FCSTD DOCUMENT  (FreeCAD 0.20R29410 (Git))
Label: feeder_assembly
License: All rights reserved
LicenseURL: http://en.wikipedia.org/wiki/All_rights_reserved
objects: Part::FeaturePython×592, App::FeaturePython×507, Sketcher::SketchObject×232, PartDesign::Fillet×137, PartDesign::Pad×118, PartDesign::Pocket×107, PartDesign::Body×40, App::Link×18, PartDesign::Chamfer×18, App::DocumentObjectGroup×16, PartDesign::Mirrored×8, Part::Feature×6, PartDesign::LinearPattern×6, Part::Mirroring×4, PartDesign::PolarPattern×3, PartDesign::MultiTransform×2, PartDesign::FeatureBase×1, PartDesign::Thickness×1
note: 1617 computed .brp shape members not serialized (recipe doc carries the construction recipe); baked Part::Feature solids carry a one-line shape summary decoded from their .brp
EXTERNAL_REF file=40cm_2020_aluminum_extrusion.FCStd obj=Pad001
EXTERNAL_REF file=food_dish.FCStd obj=Revolution
EXTERNAL_REF file=orthogonal_2020_aluminum_connector.FCStd obj=Fillet003
EXTERNAL_REF file=dispenser.FCStd obj=Assembly
EXTERNAL_REF file=MG996R.FCStd obj=MG996R001

FEATURE [App::Link] Link  label="40cm_2020_extrusion-01"
  LinkPlacement = pos=(557,-323,-130) rot=(0,0,1;0rad)
  LinkedObject = -> <external 40cm_2020_aluminum_extrusion.FCStd>#Pad001
  Placement = pos=(557,-323,-130) rot=(0,0,1;0rad)
FEATURE [App::Link] Link001  label="40cm_2020_extrusion-02"
  LinkPlacement = pos=(367,-323,-130) rot=(0,0,1;0rad)
  LinkedObject = -> <external 40cm_2020_aluminum_extrusion.FCStd>#Pad001
  Placement = pos=(367,-323,-130) rot=(0,0,1;0rad)
FEATURE [App::Link] Link002  label="40cm_2020_extrusion-03"
  LinkPlacement = pos=(747,-323,-130) rot=(0,0,1;0rad)
  LinkedObject = -> <external 40cm_2020_aluminum_extrusion.FCStd>#Pad001
  Placement = pos=(747,-323,-130) rot=(0,0,1;0rad)
FEATURE [App::Link] Link003  label="40cm_2020_extrusion-04"
  LinkPlacement = pos=(410,-646,-130) rot=(0,0,-1;1.5708rad)
  LinkedObject = -> <external 40cm_2020_aluminum_extrusion.FCStd>#Pad001
  Placement = pos=(410,-646,-130) rot=(0,0,-1;1.5708rad)
FEATURE [App::Link] Link004  label="40cm_2020_extrusion-05"
  LinkPlacement = pos=(23.9999,-386,-130) rot=(0,0,1;1.5708rad)
  LinkedObject = -> <external 40cm_2020_aluminum_extrusion.FCStd>#Pad001
  Placement = pos=(23.9999,-386,-130) rot=(0,0,1;1.5708rad)
FEATURE [App::Link] Link005  label="food_dish_left"
  LinkPlacement = pos=(122.089,-400.044,0) rot=(0.99982,-0.013426,-0.013426;1.57098rad)
  LinkedObject = -> <external food_dish.FCStd>#Revolution
  Placement = pos=(122.089,-400.044,0) rot=(0.99982,-0.013426,-0.013426;1.57098rad)
FEATURE [App::Link] Link006  label="food_dish_right"
  LinkPlacement = pos=(311.742,-398.636,2.1e-14) rot=(0.999997,-0.001682,-0.001682;1.5708rad)
  LinkedObject = -> <external food_dish.FCStd>#Revolution
  Placement = pos=(311.742,-398.636,2.1e-14) rot=(0.999997,-0.001682,-0.001682;1.5708rad)
FEATURE [App::Link] Link007  label="40_cm_2020_vertical-left"
  LinkPlacement = pos=(347,-615.994,7) rot=(-1,0,0;1.5708rad)
  LinkedObject = -> <external 40cm_2020_aluminum_extrusion.FCStd>#Pad001
  Placement = pos=(347,-615.994,7) rot=(-1,0,0;1.5708rad)
FEATURE [App::Link] Link008  label="orthogonal-left-front"
  LinkPlacement = pos=(16.9999,-485.994,20) rot=(-0.707107,0,0.707107;3.14159rad)
  LinkedObject = -> <external orthogonal_2020_aluminum_connector.FCStd>#Fillet003
  Placement = pos=(16.9999,-485.994,20) rot=(-0.707107,0,0.707107;3.14159rad)
FEATURE [App::Link] Link009  label="orthogonal-left-back"
  LinkPlacement = pos=(16.9999,-465.994,1.01614e-10) rot=(0,-1,0;1.5708rad)
  LinkedObject = -> <external orthogonal_2020_aluminum_connector.FCStd>#Fillet003
  Placement = pos=(16.9999,-465.994,1.01614e-10) rot=(0,-1,0;1.5708rad)
FEATURE [Sketcher::SketchObject] Sketch
  FullyConstrained = true
  MapMode = 5
  Placement = pos=(0,0,0) rot=(0.57735,0.57735,0.57735;2.0944rad)
  Support = -> [YZ_Plane]
  sketch-geometry (4):
    g0: LineSegment StartX=0 StartY=0 StartZ=0 EndX=20 EndY=0 EndZ=0
    g1: LineSegment StartX=20 StartY=0 StartZ=0 EndX=20 EndY=30 EndZ=0
    g2: LineSegment StartX=20 StartY=30 StartZ=0 EndX=0 EndY=30 EndZ=0
    g3: LineSegment StartX=0 StartY=30 StartZ=0 EndX=0 EndY=0 EndZ=0
  constraints (11):
    c: Coincident(g0,g1)
    c: Coincident(g1,g2)
    c: Coincident(g2,g3)
    c: Coincident(g3,g0)
    c: Horizontal(g0)
    c: Horizontal(g2)
    c: Vertical(g1)
    c: Vertical(g3)
    c: Coincident(g0,g-1)
    c: DistanceY(g3,g3) = 30
    c: DistanceX(g0,g0) = 20
FEATURE [PartDesign::Pad] Pad  label="Pad-body001"
  Direction = (1,-2e-16,3e-16)
  Length = 200
  Length2 = 10
  Placement = pos=(0,0,0) rot=(0.57735,0.57735,0.57735;2.0944rad)
  Profile = -> Sketch
  ReferenceAxis = -> Sketch [N_Axis]
  Type = 0
FEATURE [Sketcher::SketchObject] Sketch004
  FullyConstrained = true
  MapMode = 5
  Support = -> [XY_Plane003]
  sketch-geometry (4):
    g0: LineSegment StartX=0 StartY=0 StartZ=0 EndX=166 EndY=0 EndZ=0
    g1: LineSegment StartX=166 StartY=0 StartZ=0 EndX=166 EndY=-90 EndZ=0
    g2: LineSegment StartX=166 StartY=-90 StartZ=0 EndX=0 EndY=-90 EndZ=0
    g3: LineSegment StartX=0 StartY=-90 StartZ=0 EndX=0 EndY=0 EndZ=0
  constraints (11):
    c: Coincident(g0,g1)
    c: Coincident(g1,g2)
    c: Coincident(g2,g3)
    c: Coincident(g3,g0)
    c: Horizontal(g0)
    c: Horizontal(g2)
    c: Vertical(g1)
    c: Vertical(g3)
    c: Coincident(g0,g-1)
    c: DistanceX(g2,g2) = 166
    c: DistanceY(g1,g1) = 90
FEATURE [PartDesign::Pad] Pad004  label="Pad-body"
  Direction = (0,0,1)
  Length = 5
  Length2 = 10
  Profile = -> Sketch004
  ReferenceAxis = -> Sketch004 [N_Axis]
  Type = 0
FEATURE [Sketcher::SketchObject] Sketch006
  ExternalGeometry = -> [Pad004]
  FullyConstrained = true
  MapMode = 5
  Placement = pos=(0,0,0) rot=(0.57735,-0.57735,-0.57735;2.0944rad)
  Support = -> [Pad004]
  sketch-geometry (1):
    g0: Circle CenterX=90 CenterY=2.5 CenterZ=0 NormalX=0 NormalY=0 NormalZ=1 AngleXU=0 Radius=4.5
  constraints (3):
    c: PointOnObject(g0,g-3)
    c: DistanceY(g-3,g0) = 2.5
    c: Diameter(g0) = 9
FEATURE [PartDesign::Pad] Pad006  label="Pad-slider_pin"
  BaseFeature = -> Pad004
  Direction = (-1,0,0)
  Length = 21
  Length2 = 177
  Profile = -> Sketch006
  ReferenceAxis = -> Sketch006 [N_Axis]
  Type = 4
FEATURE [App::Link] Link011  label="assy-dispenser-left"
  LinkPlacement = pos=(147,-465.994,202) rot=(0,0,1;1.5708rad)
  LinkedObject = -> <external dispenser.FCStd>#Assembly
  Placement = pos=(147,-465.994,202) rot=(0,0,1;1.5708rad)
FEATURE [App::Link] Link012  label="40cm_2020_extrusion-06"
  LinkPlacement = pos=(767,-335.994,393) rot=(1,0,0;1.5708rad)
  LinkedObject = -> <external 40cm_2020_aluminum_extrusion.FCStd>#Pad001
  Placement = pos=(767,-335.994,393) rot=(1,0,0;1.5708rad)
FEATURE [App::Link] Link013  label="orthogonal-right-front"
  LinkPlacement = pos=(417,-485.994,-1.29023e-10) rot=(0.707107,0,0.707107;3.14159rad)
  LinkedObject = -> <external orthogonal_2020_aluminum_connector.FCStd>#Fillet003
  Placement = pos=(417,-485.994,-1.29023e-10) rot=(0.707107,0,0.707107;3.14159rad)
FEATURE [App::Link] Link014  label="40cm_2020_extrusion-007"
  LinkPlacement = pos=(410,-815.994,124.795) rot=(0,0,-1;1.5708rad)
  LinkedObject = -> <external 40cm_2020_aluminum_extrusion.FCStd>#Pad001
  Placement = pos=(410,-815.994,124.795) rot=(0,0,-1;1.5708rad)
FEATURE [App::Link] Link015  label="assy-dispenser-right"
  LinkPlacement = pos=(287,-465.994,202) rot=(0,0,1;0rad)
  LinkedObject = -> <external dispenser.FCStd>#Assembly
  Placement = pos=(287,-465.994,202) rot=(0,0,1;0rad)
FEATURE [Sketcher::SketchObject] Sketch008
  FullyConstrained = true
  MapMode = 5
  Placement = pos=(8.8e-15,20,-4.4e-15) rot=(0.57735,0.57735,0.57735;4.18879rad)
  Support = -> [Pad]
  sketch-geometry (5):
    g0: Circle CenterX=15 CenterY=10 CenterZ=0 NormalX=0 NormalY=0 NormalZ=1 AngleXU=0 Radius=5
    g1: ArcOfCircle CenterX=15 CenterY=190 CenterZ=0 NormalX=0 NormalY=0 NormalZ=1 AngleXU=0 Radius=5 StartAngle=1.7e-15 EndAngle=3.14159
    g2: ArcOfCircle CenterX=15 CenterY=35 CenterZ=0 NormalX=0 NormalY=0 NormalZ=1 AngleXU=0 Radius=5 StartAngle=3.14159 EndAngle=6.28319
    g3: LineSegment StartX=10 StartY=190 StartZ=0 EndX=10 EndY=35 EndZ=0
    g4: LineSegment StartX=20 StartY=35 StartZ=0 EndX=20 EndY=190 EndZ=0
  constraints (13):
    c: Diameter(g0) = 10
    c: DistanceX(g-1,g0) = 15
    c: DistanceY(g-1,g0) = 10
    c: Tangent(g1,g3) = -1.5708
    c: Tangent(g3,g2) = -1.5708
    c: Tangent(g2,g4) = -1.5708
    c: Tangent(g4,g1) = -1.5708
    c: Equal(g1,g2)
    c: Vertical(g3)
    c: Radius(g2) = 5
    c: Vertical(g2,g0)
    c: DistanceY(g0,g2) = 25
    c: DistanceY(g0,g1) = 180
FEATURE [PartDesign::Pocket] Pocket  label="Pocket-slider_guide"
  BaseFeature = -> Pad
  Direction = (-3e-16,-1,1e-16)
  Length = 5
  Length2 = 5
  Placement = pos=(0,0,0) rot=(0.57735,0.57735,0.57735;2.0944rad)
  Profile = -> Sketch008
  ReferenceAxis = -> Sketch008 [N_Axis]
  Type = 1
FEATURE [Sketcher::SketchObject] Sketch009
  FullyConstrained = true
  MapMode = 5
  Placement = pos=(-8.4e-15,1.32e-14,30) rot=(0,0,-1;1.5708rad)
  Support = -> [Pocket]
  sketch-geometry (2):
    g0: Circle CenterX=-10 CenterY=50 CenterZ=0 NormalX=0 NormalY=0 NormalZ=1 AngleXU=0 Radius=3.1
    g1: Circle CenterX=-10 CenterY=180 CenterZ=0 NormalX=0 NormalY=0 NormalZ=1 AngleXU=0 Radius=3.1
  constraints (6):
    c: DistanceX(g0,g-1) = 10
    c: Vertical(g1,g0)
    c: DistanceY(g-1,g0) = 50
    c: DistanceY(g0,g1) = 130
    c: Diameter(g0) = 6.2
    c: Equal(g1,g0)
FEATURE [PartDesign::Pocket] Pocket001  label="Pocket-mount_holes"
  BaseFeature = -> Pocket
  Direction = (3e-16,-5e-16,-1)
  Length = 26.5
  Length2 = 5
  Placement = pos=(0,0,0) rot=(0.57735,0.57735,0.57735;2.0944rad)
  Profile = -> Sketch009
  ReferenceAxis = -> Sketch009 [N_Axis]
  Type = 0
FEATURE [Sketcher::SketchObject] Sketch013  label="Sketch-slider_guide_line"
  FullyConstrained = false
  MapMode = 5
  Placement = pos=(0,1e-16,0) rot=(-0.57735,-0.57735,0.57735;4.18879rad)
  Support = -> [Pocket001]
  sketch-geometry (1):
    g0: LineSegment StartX=-14.7121 StartY=24.4994 StartZ=0 EndX=-14.7121 EndY=187.74 EndZ=0
  constraints (1):
    c: Vertical(g0)
FEATURE [App::Link] Link016  label="assy-link-slide-right"
  LinkPlacement = pos=(772,-351.327,-140) rot=(0,0,1;0rad)
  LinkedObject = -> Assembly001
  Placement = pos=(772,-351.327,-140) rot=(0,0,1;0rad)
FEATURE [Sketcher::SketchObject] Sketch016
  ExternalGeometry = -> [Pad006]
  FullyConstrained = true
  MapMode = 5
  Placement = pos=(0,0,0) rot=(1,0,0;3.14159rad)
  Support = -> [Pad006]
  sketch-geometry (10):
    g0: LineSegment StartX=15.25 StartY=10.5 StartZ=0 EndX=25.25 EndY=10.5 EndZ=0
    g1: LineSegment StartX=25.25 StartY=10.5 StartZ=0 EndX=25.25 EndY=-4.5 EndZ=0
    g2: LineSegment StartX=25.25 StartY=-4.5 StartZ=0 EndX=15.25 EndY=-4.5 EndZ=0
    g3: LineSegment StartX=15.25 StartY=-4.5 StartZ=0 EndX=15.25 EndY=10.5 EndZ=0
    g4: LineSegment StartX=140.75 StartY=10.5 StartZ=0 EndX=150.75 EndY=10.5 EndZ=0
    g5: LineSegment StartX=150.75 StartY=10.5 StartZ=0 EndX=150.75 EndY=-4.5 EndZ=0
    g6: LineSegment StartX=150.75 StartY=-4.5 StartZ=0 EndX=140.75 EndY=-4.5 EndZ=0
    g7: LineSegment StartX=140.75 StartY=-4.5 StartZ=0 EndX=140.75 EndY=10.5 EndZ=0
    g8: LineSegment StartX=0 StartY=0 StartZ=0 EndX=15.25 EndY=10.5 EndZ=0
    g9: LineSegment StartX=150.75 StartY=10.5 StartZ=0 EndX=166 EndY=-1.8e-15 EndZ=0
  constraints (28):
    c: Coincident(g0,g1)
    c: Coincident(g1,g2)
    c: Coincident(g2,g3)
    c: Coincident(g3,g0)
    c: Horizontal(g0)
    c: Horizontal(g2)
    c: Vertical(g1)
    c: Vertical(g3)
    c: Coincident(g4,g5)
    c: Coincident(g5,g6)
    c: Coincident(g6,g7)
    c: Coincident(g7,g4)
    c: Horizontal(g4)
    c: Horizontal(g6)
    c: Vertical(g5)
    c: Vertical(g7)
    c: Equal(g3,g7)
    c: Equal(g2,g6)
    c: DistanceY(g2,g-3) = 4.5
    c: DistanceX(g-3,g2) = 15.25
    c: DistanceX(g0,g0) = 10
    c: DistanceY(g1,g1) = 15
    c: Horizontal(g6,g1)
    c: Coincident(g8,g-3)
    c: Coincident(g8,g0)
    c: Coincident(g9,g4)
    c: Coincident(g9,g-3)
    c: Equal(g8,g9)
FEATURE [PartDesign::Pad] Pad009
  BaseFeature = -> Pad006
  Direction = (0,0,-1)
  Length = 7
  Length2 = 10
  Profile = -> Sketch016
  ReferenceAxis = -> Sketch016 [N_Axis]
  Type = 0
FEATURE [Sketcher::SketchObject] Sketch017
  FullyConstrained = true
  MapMode = 5
  Placement = pos=(15.25,0,0) rot=(0.57735,-0.57735,-0.57735;2.0944rad)
  Support = -> [Pad009]
  sketch-geometry (4):
    g0: Circle CenterX=-1 CenterY=-3.5 CenterZ=0 NormalX=0 NormalY=0 NormalZ=1 AngleXU=0 Radius=1.75
    g1: LineSegment StartX=10.5 StartY=0 StartZ=0 EndX=10.5 EndY=-7 EndZ=0
    g2: LineSegment StartX=10.5 StartY=-7 StartZ=0 EndX=3.5 EndY=-7 EndZ=0
    g3: LineSegment StartX=3.5 StartY=-7 StartZ=0 EndX=10.5 EndY=0 EndZ=0
  constraints (12):
    c: Diameter(g0) = 3.5
    c: DistanceY(g0,g-1) = 3.5
    c: DistanceX(g0,g-1) = 1
    c: PointOnObject(g1,g-1)
    c: Vertical(g1)
    c: Horizontal(g2)
    c: Coincident(g3,g1)
    c: Coincident(g2,g3)
    c: Coincident(g1,g2)
    c: Angle(g3,g1) = 0.785398
    c: DistanceX(g-1,g1) = 10.5
    c: DistanceY(g1,g1) = 7
FEATURE [PartDesign::Pocket] Pocket005
  BaseFeature = -> Pad009
  Direction = (1,0,0)
  Length = 5
  Length2 = 5
  Profile = -> Sketch017
  ReferenceAxis = -> Sketch017 [N_Axis]
  Type = 1
FEATURE [Sketcher::SketchObject] Sketch018
  ExternalGeometry = -> [Pocket005]
  FullyConstrained = true
  MapMode = 5
  Placement = pos=(-21,0,0) rot=(0.57735,-0.57735,-0.57735;2.0944rad)
  Support = -> [Pocket005]
  sketch-geometry (1):
    g0: GeomPoint X=90 Y=2.5 Z=0
  constraints (1):
    c: Coincident(g0,g-3)
FEATURE [Part::FeaturePython] Workplane  label="Workplane-XY"  # WARN: FeaturePython — macro-defined, semantics opaque (R4)
  Fixed = true
  Length = 400.999
  Placement = pos=(16.9999,-296,0) rot=(0,0,-1;1.5708rad)
  Width = 400.999
FEATURE [Part::FeaturePython] Workplane001  label="Workplane-YZ"  # WARN: FeaturePython — macro-defined, semantics opaque (R4)
  Fixed = true
  Length = 567.098
  Placement = pos=(16.9999,-296,0) rot=(0,-1,0;1.5708rad)
  Width = 567.098
FEATURE [Part::FeaturePython] Workplane002  label="WorkplaneXZ"  # WARN: FeaturePython — macro-defined, semantics opaque (R4)
  Fixed = true
  Length = 567.098
  Placement = pos=(16.9999,-296,0) rot=(1,0,0;1.5708rad)
  Width = 567.098
FEATURE [Sketcher::SketchObject] Sketch001
  FullyConstrained = true
  MapMode = 5
  Support = -> [XY_Plane001]
  sketch-geometry (4):
    g0: LineSegment StartX=0 StartY=50 StartZ=0 EndX=166 EndY=50 EndZ=0
    g1: LineSegment StartX=166 StartY=50 StartZ=0 EndX=166 EndY=140 EndZ=0
    g2: LineSegment StartX=166 StartY=140 StartZ=0 EndX=0 EndY=140 EndZ=0
    g3: LineSegment StartX=0 StartY=140 StartZ=0 EndX=0 EndY=50 EndZ=0
  constraints (12):
    c: Coincident(g0,g1)
    c: Coincident(g1,g2)
    c: Coincident(g2,g3)
    c: Coincident(g3,g0)
    c: Horizontal(g0)
    c: Horizontal(g2)
    c: Vertical(g1)
    c: Vertical(g3)
    c: PointOnObject(g0,g-2)
    c: DistanceY(g1,g1) = 90
    c: DistanceX(g0,g0) = 166
    c: DistanceY(g-1,g2) = 140
FEATURE [PartDesign::Pad] Pad001  label="Pad-base_rect"
  Direction = (0,0,1)
  Length = 5
  Length2 = 10
  Profile = -> Sketch001
  ReferenceAxis = -> Sketch001 [N_Axis]
  Type = 0
FEATURE [Sketcher::SketchObject] Sketch002
  ExternalGeometry = -> [Pad001]
  FullyConstrained = true
  MapMode = 5
  Placement = pos=(0,0,0) rot=(0.57735,-0.57735,-0.57735;2.0944rad)
  Support = -> [Pad001]
  sketch-geometry (1):
    g0: Circle CenterX=-140 CenterY=2.5 CenterZ=0 NormalX=0 NormalY=0 NormalZ=1 AngleXU=0 Radius=4.5
  constraints (3):
    c: DistanceY(g-3,g0) = 2.5
    c: Diameter(g0) = 9
    c: PointOnObject(g0,g-3)
FEATURE [PartDesign::Pad] Pad002  label="Pad-base_9mm_shaft"
  BaseFeature = -> Pad001
  Direction = (-1,0,0)
  Length = 21
  Length2 = 177
  Profile = -> Sketch002
  ReferenceAxis = -> Sketch002 [N_Axis]
  Type = 4
FEATURE [Sketcher::SketchObject] Sketch014
  ExternalGeometry = -> [Pad002]
  FullyConstrained = true
  MapMode = 5
  Placement = pos=(0,0,0) rot=(1,0,0;3.14159rad)
  Support = -> [Pad002]
  sketch-geometry (18):
    g0: LineSegment StartX=10 StartY=-45.5 StartZ=0 EndX=15 EndY=-45.5 EndZ=0
    g1: LineSegment StartX=15 StartY=-45.5 StartZ=0 EndX=15 EndY=-60.5 EndZ=0
    g2: LineSegment StartX=15 StartY=-60.5 StartZ=0 EndX=10 EndY=-60.5 EndZ=0
    g3: LineSegment StartX=10 StartY=-60.5 StartZ=0 EndX=10 EndY=-45.5 EndZ=0
    g4: LineSegment StartX=25.5 StartY=-45.5 StartZ=0 EndX=30.5 EndY=-45.5 EndZ=0
    g5: LineSegment StartX=30.5 StartY=-45.5 StartZ=0 EndX=30.5 EndY=-60.5 EndZ=0
    g6: LineSegment StartX=30.5 StartY=-60.5 StartZ=0 EndX=25.5 EndY=-60.5 EndZ=0
    g7: LineSegment StartX=25.5 StartY=-60.5 StartZ=0 EndX=25.5 EndY=-45.5 EndZ=0
    g8: LineSegment StartX=135.5 StartY=-45.5 StartZ=0 EndX=140.5 EndY=-45.5 EndZ=0
    g9: LineSegment StartX=140.5 StartY=-45.5 StartZ=0 EndX=140.5 EndY=-60.5 EndZ=0
    g10: LineSegment StartX=140.5 StartY=-60.5 StartZ=0 EndX=135.5 EndY=-60.5 EndZ=0
    g11: LineSegment StartX=135.5 StartY=-60.5 StartZ=0 EndX=135.5 EndY=-45.5 EndZ=0
    g12: LineSegment StartX=151 StartY=-45.5 StartZ=0 EndX=156 EndY=-45.5 EndZ=0
    g13: LineSegment StartX=156 StartY=-45.5 StartZ=0 EndX=156 EndY=-60.5 EndZ=0
    g14: LineSegment StartX=156 StartY=-60.5 StartZ=0 EndX=151 EndY=-60.5 EndZ=0
    g15: LineSegment StartX=151 StartY=-60.5 StartZ=0 EndX=151 EndY=-45.5 EndZ=0
    g16: LineSegment StartX=15 StartY=-60.5 StartZ=0 EndX=25.5 EndY=-60.5 EndZ=0
    g17: LineSegment StartX=140.5 StartY=-60.5 StartZ=0 EndX=151 EndY=-60.5 EndZ=0
  constraints (52):
    c: Coincident(g0,g1)
    c: Coincident(g1,g2)
    c: Coincident(g2,g3)
    c: Coincident(g3,g0)
    c: Horizontal(g0)
    c: Horizontal(g2)
    c: Vertical(g1)
    c: Vertical(g3)
    c: Coincident(g4,g5)
    c: Coincident(g5,g6)
    c: Coincident(g6,g7)
    c: Coincident(g7,g4)
    c: Horizontal(g4)
    c: Horizontal(g6)
    c: Vertical(g5)
    c: Vertical(g7)
    c: Coincident(g8,g9)
    c: Coincident(g9,g10)
    c: Coincident(g10,g11)
    c: Coincident(g11,g8)
    c: Horizontal(g8)
    c: Horizontal(g10)
    c: Vertical(g9)
    c: Vertical(g11)
    c: Coincident(g12,g13)
    c: Coincident(g13,g14)
    c: Coincident(g14,g15)
    c: Coincident(g15,g12)
    c: Horizontal(g12)
    c: Horizontal(g14)
    c: Vertical(g13)
    c: Vertical(g15)
    c: Horizontal(g6,g10)
    c: Horizontal(g0,g4)
    c: Horizontal(g4,g8)
    c: Horizontal(g8,g12)
    c: Equal(g2,g6)
    c: Equal(g6,g10)
    c: Equal(g10,g14)
    c: DistanceX(g-1,g2) = 10
    c: DistanceX(g2,g2) = 5
    c: DistanceX(g1,g6) = 10.5
    c: DistanceY(g3,g3) = 15
    c: Coincident(g16,g1)
    c: Coincident(g16,g6)
    c: Horizontal(g16)
    c: Coincident(g17,g9)
    c: Coincident(g17,g14)
    c: Horizontal(g17)
    c: Equal(g16,g17)
    c: DistanceX(g12,g-3) = 10
    c: DistanceY(g-3,g0) = 4.5
FEATURE [PartDesign::Pad] Pad008  label="Pad-left_right_hinges"
  BaseFeature = -> Pad002
  Direction = (0,0,-1)
  Length = 7
  Length2 = 10
  Profile = -> Sketch014
  ReferenceAxis = -> Sketch014 [N_Axis]
  Type = 0
FEATURE [Sketcher::SketchObject] Sketch015
  ExternalGeometry = -> [Pad008]
  FullyConstrained = true
  MapMode = 5
  Placement = pos=(10,0,0) rot=(0.57735,-0.57735,-0.57735;2.0944rad)
  Support = -> [Pad008]
  sketch-geometry (4):
    g0: Circle CenterX=-49 CenterY=-3.5 CenterZ=0 NormalX=0 NormalY=0 NormalZ=1 AngleXU=0 Radius=1.75
    g1: LineSegment StartX=-60.5 StartY=0 StartZ=0 EndX=-53.5 EndY=-7 EndZ=0
    g2: LineSegment StartX=-53.5 StartY=-7 StartZ=0 EndX=-60.5 EndY=-7 EndZ=0
    g3: LineSegment StartX=-60.5 StartY=-7 StartZ=0 EndX=-60.5 EndY=0 EndZ=0
  constraints (12):
    c: Diameter(g0) = 3.5
    c: DistanceX(g-3,g0) = 1
    c: DistanceY(g0,g-3) = 3.5
    c: PointOnObject(g1,g-1)
    c: Coincident(g2,g1)
    c: Horizontal(g2)
    c: Coincident(g3,g2)
    c: Coincident(g3,g1)
    c: Vertical(g3)
    c: DistanceY(g3,g3) = 7
    c: Angle(g3,g1) = 0.785398
    c: DistanceX(g1,g-3) = 10.5
FEATURE [PartDesign::Pocket] Pocket004  label="Pocket-left_right_hinge2"
  BaseFeature = -> Pad008
  Direction = (1,0,0)
  Length = 5
  Length2 = 5
  Profile = -> Sketch015
  ReferenceAxis = -> Sketch015 [N_Axis]
  Type = 1
FEATURE [App::FeaturePython] Constraints005  # WARN: FeaturePython — macro-defined, semantics opaque (R4)
  _Version = 1
FEATURE [Part::Mirroring] Part__Mirroring001  label="Pocket005 (Mirror #2)"
  Base = (0,0,0)
  Normal = (1,0,0)
  Source = -> Pocket005
FEATURE [App::FeaturePython] Constraints006  # WARN: FeaturePython — macro-defined, semantics opaque (R4)
  _Version = 1
FEATURE [Part::FeaturePython] Parts006  # WARN: FeaturePython — macro-defined, semantics opaque (R4)
  Group = -> [Part__Mirroring001]
  GroupMode = 0
FEATURE [App::FeaturePython] Constraints007  # WARN: FeaturePython — macro-defined, semantics opaque (R4)
  _Version = 1
FEATURE [Sketcher::SketchObject] Sketch019
  FullyConstrained = true
  MapMode = 5
  Placement = pos=(0,0,0) rot=(0.57735,0.57735,0.57735;2.0944rad)
  Support = -> [YZ_Plane004]
  sketch-geometry (4):
    g0: LineSegment StartX=0 StartY=0 StartZ=0 EndX=20 EndY=0 EndZ=0
    g1: LineSegment StartX=20 StartY=0 StartZ=0 EndX=20 EndY=30 EndZ=0
    g2: LineSegment StartX=20 StartY=30 StartZ=0 EndX=0 EndY=30 EndZ=0
    g3: LineSegment StartX=0 StartY=30 StartZ=0 EndX=0 EndY=0 EndZ=0
  constraints (11):
    c: Coincident(g0,g1)
    c: Coincident(g1,g2)
    c: Coincident(g2,g3)
    c: Coincident(g3,g0)
    c: Horizontal(g0)
    c: Horizontal(g2)
    c: Vertical(g1)
    c: Vertical(g3)
    c: Coincident(g0,g-1)
    c: DistanceY(g3,g3) = 30
    c: DistanceX(g0,g0) = 20
FEATURE [PartDesign::Pad] Pad010  label="Pad-body002"
  Direction = (1,-2e-16,3e-16)
  Length = 200
  Length2 = 10
  Placement = pos=(0,0,0) rot=(0.57735,0.57735,0.57735;2.0944rad)
  Profile = -> Sketch019
  ReferenceAxis = -> Sketch019 [N_Axis]
  Type = 0
FEATURE [Sketcher::SketchObject] Sketch020
  FullyConstrained = true
  MapMode = 5
  Placement = pos=(8.8e-15,20,-4.4e-15) rot=(0.57735,0.57735,0.57735;4.18879rad)
  Support = -> [Pad010]
  sketch-geometry (5):
    g0: Circle CenterX=15 CenterY=10 CenterZ=0 NormalX=0 NormalY=0 NormalZ=1 AngleXU=0 Radius=5
    g1: ArcOfCircle CenterX=15 CenterY=190 CenterZ=0 NormalX=0 NormalY=0 NormalZ=1 AngleXU=0 Radius=5 StartAngle=1.7e-15 EndAngle=3.14159
    g2: ArcOfCircle CenterX=15 CenterY=35 CenterZ=0 NormalX=0 NormalY=0 NormalZ=1 AngleXU=0 Radius=5 StartAngle=3.14159 EndAngle=6.28319
    g3: LineSegment StartX=10 StartY=190 StartZ=0 EndX=10 EndY=35 EndZ=0
    g4: LineSegment StartX=20 StartY=35 StartZ=0 EndX=20 EndY=190 EndZ=0
  constraints (13):
    c: Diameter(g0) = 10
    c: DistanceX(g-1,g0) = 15
    c: DistanceY(g-1,g0) = 10
    c: Tangent(g1,g3) = -1.5708
    c: Tangent(g3,g2) = -1.5708
    c: Tangent(g2,g4) = -1.5708
    c: Tangent(g4,g1) = -1.5708
    c: Equal(g1,g2)
    c: Vertical(g3)
    c: Radius(g2) = 5
    c: Vertical(g2,g0)
    c: DistanceY(g0,g2) = 25
    c: DistanceY(g0,g1) = 180
FEATURE [PartDesign::Pocket] Pocket006  label="Pocket-slider_guide001"
  BaseFeature = -> Pad010
  Direction = (-4e-16,-1,2e-16)
  Length = 5
  Length2 = 5
  Placement = pos=(0,0,0) rot=(0.57735,0.57735,0.57735;2.0944rad)
  Profile = -> Sketch020
  ReferenceAxis = -> Sketch020 [N_Axis]
  Type = 1
FEATURE [Sketcher::SketchObject] Sketch021
  FullyConstrained = true
  MapMode = 5
  Placement = pos=(-8.4e-15,1.32e-14,30) rot=(0,0,-1;1.5708rad)
  Support = -> [Pocket006]
  sketch-geometry (2):
    g0: Circle CenterX=-10 CenterY=50 CenterZ=0 NormalX=0 NormalY=0 NormalZ=1 AngleXU=0 Radius=5
    g1: Circle CenterX=-10 CenterY=180 CenterZ=0 NormalX=0 NormalY=0 NormalZ=1 AngleXU=0 Radius=5
  constraints (6):
    c: DistanceX(g0,g-1) = 10
    c: Vertical(g1,g0)
    c: DistanceY(g-1,g0) = 50
    c: DistanceY(g0,g1) = 130
    c: Diameter(g1) = 10
    c: Diameter(g0) = 10
FEATURE [PartDesign::Pocket] Pocket007  label="Pocket-mount_holes001"
  BaseFeature = -> Pocket006
  Direction = (7e-16,-7e-16,-1)
  Length = 28
  Length2 = 5
  Placement = pos=(0,0,0) rot=(0.57735,0.57735,0.57735;2.0944rad)
  Profile = -> Sketch021
  ReferenceAxis = -> Sketch021 [N_Axis]
  Type = 0
FEATURE [Sketcher::SketchObject] Sketch022  label="Sketch-slider_guide_line001"
  FullyConstrained = false
  MapMode = 5
  Placement = pos=(0,1e-16,0) rot=(-0.57735,-0.57735,0.57735;4.18879rad)
  Support = -> [Pocket007]
  sketch-geometry (1):
    g0: LineSegment StartX=-14.7121 StartY=24.4994 StartZ=0 EndX=-14.7121 EndY=187.74 EndZ=0
  constraints (1):
    c: Vertical(g0)
FEATURE [PartDesign::Body] Body004  label="Slide-mid-Body001"
  Group = -> [Sketch019,Pad010,Sketch020,Pocket006,Sketch021,Pocket007,Sketch022]
  Origin = -> Origin004
  Placement = pos=(-375,53,160) rot=(0,0,-1;1.5708rad)
  Tip = -> Pocket007
FEATURE [Part::FeaturePython] Parts007  # WARN: FeaturePython — macro-defined, semantics opaque (R4)
  Group = -> [Body004]
  GroupMode = 0
FEATURE [App::FeaturePython] Constraints008  # WARN: FeaturePython — macro-defined, semantics opaque (R4)
  _Version = 1
FEATURE [App::FeaturePython] Elements008  # WARN: FeaturePython — macro-defined, semantics opaque (R4)
FEATURE [App::Link] Link017  label="link-servo"
  LinkPlacement = pos=(-23.0002,-306,45) rot=(0.57735,0.57735,0.57735;4.18879rad)
  LinkedObject = -> <external MG996R.FCStd>#MG996R001
  Placement = pos=(-23.0002,-306,45) rot=(0.57735,0.57735,0.57735;4.18879rad)
FEATURE [Part::FeaturePython] Parts008  # WARN: FeaturePython — macro-defined, semantics opaque (R4)
  Group = -> [Link017]
  GroupMode = 0
FEATURE [Part::FeaturePython] Assembly008  label="assy_servo"  # WARN: FeaturePython — macro-defined, semantics opaque (R4)
  AutoRelax = true
  BuildShape = 0
  Freeze = false
  Group = -> [Constraints008,Elements008,Parts008]
  Verbose = false
  _SolverType = 1
  _Version = 1
FEATURE [Sketcher::SketchObject] Sketch023
  ExternalGeometry = -> [Pocket001]
  FullyConstrained = true
  MapMode = 5
  Placement = pos=(0,0,0) rot=(0.57735,0.57735,-0.57735;4.18879rad)
  Support = -> [Pocket001]
  sketch-geometry (8):
    g0: LineSegment StartX=-10 StartY=2.5 StartZ=0 EndX=-10 EndY=-52.5 EndZ=0
    g1: LineSegment StartX=0 StartY=0 StartZ=0 EndX=0 EndY=-30 EndZ=0
    g2: LineSegment StartX=0 StartY=-30 StartZ=0 EndX=20 EndY=-30 EndZ=0
    g3: GeomPoint X=0 Y=-15 Z=0
    g4: LineSegment StartX=4.24533 StartY=-52.5 StartZ=0 EndX=20 EndY=-30 EndZ=0
    g5: LineSegment StartX=-10 StartY=-52.5 StartZ=0 EndX=4.24533 EndY=-52.5 EndZ=0
    g6: LineSegment StartX=0 StartY=0 StartZ=0 EndX=-5 EndY=2.5 EndZ=0
    g7: LineSegment StartX=-5 StartY=2.5 StartZ=0 EndX=-10 EndY=2.5 EndZ=0
  constraints (20):
    c: Coincident(g6,g-4)
    c: Vertical(g0)
    c: Coincident(g5,g0)
    c: Coincident(g1,g6)
    c: Coincident(g0,g7)
    c: Coincident(g1,g2)
    c: Coincident(g1,g-4)
    c: DistanceX(g7,g6) = 10
    c: DistanceY(g0,g0) = 55
    c: PointOnObject(g3,g1)
    c: DistanceY(g3,g6) = 15
    c: DistanceY(g3,g7) = 17.5
    c: Horizontal(g5)
    c: Coincident(g5,g4)
    c: Coincident(g2,g4)
    c: Coincident(g2,g-3)
    c: Angle(g2,g4) = 0.959931
    c: Coincident(g6,g7)
    c: Horizontal(g7)
    c: DistanceX(g0,g6) = 5
FEATURE [PartDesign::Pad] Pad011
  BaseFeature = -> Pocket001
  Direction = (-1,2e-16,-2e-16)
  Length = 20
  Length2 = 10
  Placement = pos=(0,0,0) rot=(0.57735,0.57735,0.57735;2.0944rad)
  Profile = -> Sketch023
  ReferenceAxis = -> Sketch023 [N_Axis]
  Reversed = true
  Type = 0
FEATURE [Sketcher::SketchObject] Sketch025
  ExternalGeometry = -> [Pad011]
  FullyConstrained = true
  MapMode = 5
  Placement = pos=(-2.2e-15,-10,6e-16) rot=(-0.57735,-0.57735,0.57735;4.18879rad)
  Support = -> [Pad011]
  sketch-geometry (15):
    g0: Circle CenterX=-49.575 CenterY=14.9 CenterZ=0 NormalX=0 NormalY=0 NormalZ=1 AngleXU=0 Radius=1.125
    g1: Circle CenterX=-49.575 CenterY=5.1 CenterZ=0 NormalX=0 NormalY=0 NormalZ=1 AngleXU=0 Radius=1.125
    g2: Circle CenterX=-1.125 CenterY=14.9 CenterZ=0 NormalX=0 NormalY=0 NormalZ=1 AngleXU=0 Radius=1.125
    g3: Circle CenterX=-1.125 CenterY=5.1 CenterZ=0 NormalX=0 NormalY=0 NormalZ=1 AngleXU=0 Radius=1.125
    g4: LineSegment StartX=-46.35 StartY=0 StartZ=0 EndX=-4.35 EndY=0 EndZ=0
    g5: LineSegment StartX=-4.35 StartY=0 StartZ=0 EndX=-4.35 EndY=20 EndZ=0
    g6: LineSegment StartX=-4.35 StartY=20 StartZ=0 EndX=-46.35 EndY=20 EndZ=0
    g7: LineSegment StartX=-46.35 StartY=20 StartZ=0 EndX=-46.35 EndY=0 EndZ=0
    g8: LineSegment StartX=-49.575 StartY=14.9 StartZ=0 EndX=-49.575 EndY=5.1 EndZ=0
    g9: LineSegment StartX=-49.575 StartY=5.1 StartZ=0 EndX=-1.125 EndY=5.1 EndZ=0
    g10: LineSegment StartX=-1.125 StartY=14.9 StartZ=0 EndX=-49.575 EndY=14.9 EndZ=0
    g11: LineSegment StartX=-46.35 StartY=20 StartZ=0 EndX=-49.575 EndY=14.9 EndZ=0
    g12: LineSegment StartX=-4.35 StartY=20 StartZ=0 EndX=-1.125 EndY=14.9 EndZ=0
    g13: LineSegment StartX=-1.125 StartY=5.1 StartZ=0 EndX=-1.125 EndY=10 EndZ=0
    g14: LineSegment StartX=-1.125 StartY=10 StartZ=0 EndX=-1.125 EndY=14.9 EndZ=0
  constraints (39):
    c: Tangent(g3,g-2)
    c: Coincident(g4,g5)
    c: Coincident(g5,g6)
    c: Coincident(g6,g7)
    c: Coincident(g7,g4)
    c: Horizontal(g4)
    c: Horizontal(g6)
    c: Vertical(g5)
    c: Vertical(g7)
    c: Horizontal(g-4,g5)
    c: DistanceX(g6,g6) = 42
    c: Diameter(g2) = 2.25
    c: Equal(g0,g1)
    c: Equal(g1,g3)
    c: Equal(g3,g2)
    c: Coincident(g8,g0)
    c: Coincident(g8,g1)
    c: Vertical(g8)
    c: Coincident(g9,g1)
    c: Coincident(g9,g3)
    c: Horizontal(g9)
    c: Coincident(g13,g3)
    c: Coincident(g14,g2)
    c: Coincident(g10,g2)
    c: Coincident(g10,g0)
    c: Horizontal(g10)
    c: Coincident(g11,g6)
    c: Coincident(g11,g0)
    c: Coincident(g12,g5)
    c: Coincident(g12,g2)
    c: Equal(g12,g11)
    c: DistanceX(g9,g9) = 48.45
    c: DistanceY(g8,g8) = 9.8
    c: Coincident(g13,g14)
    c: Vertical(g13)
    c: Vertical(g14)
    c: Equal(g14,g13)
    c: DistanceY(g-4,g13) = 10
    c: PointOnObject(g4,g-5)
FEATURE [PartDesign::Pocket] Pocket008
  BaseFeature = -> Pad011
  Direction = (1e-16,1,1e-16)
  Length = 10
  Length2 = 5
  Placement = pos=(0,0,0) rot=(0.57735,0.57735,0.57735;2.0944rad)
  Profile = -> Sketch025
  ReferenceAxis = -> Sketch025 [N_Axis]
  Type = 0
FEATURE [Sketcher::SketchObject] Sketch026
  ExternalGeometry = -> [Pocket008]
  FullyConstrained = true
  MapMode = 5
  Placement = pos=(-1.47e-14,0,52.5) rot=(0,0,-1;1.5708rad)
  Support = -> [Pocket008]
  sketch-geometry (4):
    g0: LineSegment StartX=-20 StartY=17.5 StartZ=0 EndX=5 EndY=17.5 EndZ=0
    g1: LineSegment StartX=5 StartY=17.5 StartZ=0 EndX=5 EndY=2.5 EndZ=0
    g2: LineSegment StartX=5 StartY=2.5 StartZ=0 EndX=-20 EndY=2.5 EndZ=0
    g3: LineSegment StartX=-20 StartY=2.5 StartZ=0 EndX=-20 EndY=17.5 EndZ=0
  constraints (12):
    c: Coincident(g0,g1)
    c: Coincident(g1,g2)
    c: Coincident(g2,g3)
    c: Coincident(g3,g0)
    c: Horizontal(g0)
    c: Horizontal(g2)
    c: Vertical(g1)
    c: Vertical(g3)
    c: DistanceX(g2,g2) = 25
    c: DistanceX(g1,g-3) = 5
    c: DistanceY(g-3,g1) = 2.5
    c: DistanceY(g0,g-4) = 2.5
FEATURE [PartDesign::Pocket] Pocket009
  BaseFeature = -> Pocket008
  Direction = (3e-16,-1e-16,-1)
  Length = 6
  Length2 = 5
  Placement = pos=(0,0,0) rot=(0.57735,0.57735,0.57735;2.0944rad)
  Profile = -> Sketch026
  ReferenceAxis = -> Sketch026 [N_Axis]
  Type = 0
FEATURE [Sketcher::SketchObject] Sketch027
  ExternalGeometry = -> [Pocket009]
  FullyConstrained = true
  MapMode = 5
  Placement = pos=(7e-16,0,-2.5) rot=(0.707107,0.707107,0;3.14159rad)
  Support = -> [Pocket009]
  sketch-geometry (4):
    g0: LineSegment StartX=-5 StartY=17.5 StartZ=0 EndX=5 EndY=17.5 EndZ=0
    g1: LineSegment StartX=5 StartY=17.5 StartZ=0 EndX=5 EndY=2.5 EndZ=0
    g2: LineSegment StartX=5 StartY=2.5 StartZ=0 EndX=-5 EndY=2.5 EndZ=0
    g3: LineSegment StartX=-5 StartY=2.5 StartZ=0 EndX=-5 EndY=17.5 EndZ=0
  constraints (12):
    c: Coincident(g0,g1)
    c: Coincident(g1,g2)
    c: Coincident(g2,g3)
    c: Coincident(g3,g0)
    c: Horizontal(g0)
    c: Horizontal(g2)
    c: Vertical(g1)
    c: Vertical(g3)
    c: DistanceX(g-3,g2) = 5
    c: DistanceY(g-3,g2) = 2.5
    c: DistanceY(g0,g-3) = 2.5
    c: DistanceX(g0,g0) = 10
FEATURE [PartDesign::Pocket] Pocket010
  BaseFeature = -> Pocket009
  Direction = (-3e-16,1e-16,1)
  Length = 6
  Length2 = 5
  Placement = pos=(0,0,0) rot=(0.57735,0.57735,0.57735;2.0944rad)
  Profile = -> Sketch027
  ReferenceAxis = -> Sketch027 [N_Axis]
  Type = 0
FEATURE [Sketcher::SketchObject] Sketch028
  ExternalGeometry = -> [Pocket004]
  FullyConstrained = true
  MapMode = 5
  Placement = pos=(-21,0,0) rot=(0.57735,-0.57735,-0.57735;2.0944rad)
  Support = -> [Pocket004]
  sketch-geometry (5):
    g0: LineSegment StartX=-140 StartY=2.5 StartZ=0 EndX=-140 EndY=5.6 EndZ=0
    g1: LineSegment StartX=-140 StartY=5.6 StartZ=0 EndX=-139.662 EndY=5.17871 EndZ=0
    g2: LineSegment StartX=-139.662 StartY=5.17871 StartZ=0 EndX=-139.229 EndY=5.50261 EndZ=0
    g3: LineSegment StartX=-139.229 StartY=5.50261 StartZ=0 EndX=-140 EndY=2.5 EndZ=0
    g4: LineSegment StartX=-140 StartY=2.5 StartZ=0 EndX=-139.662 EndY=5.17871 EndZ=0
  constraints (13):
    c: Coincident(g0,g-3)
    c: Coincident(g1,g0)
    c: Coincident(g2,g1)
    c: Coincident(g3,g2)
    c: Coincident(g3,g0)
    c: Distance(g0) = 3.1
    c: Distance(g3) = 3.1
    c: Coincident(g4,g0)
    c: Coincident(g4,g1)
    c: Angle(g4,g0) = 0.125664
    c: Angle(g3,g0) = 0.251327
    c: Distance(g4) = 2.7
    c: Vertical(g0)
FEATURE [PartDesign::Pocket] Pocket011  label="Pocket-spline-single"
  BaseFeature = -> Pocket004
  Direction = (1,0,0)
  Length = 4
  Length2 = 5
  Profile = -> Sketch028
  ReferenceAxis = -> Sketch028 [N_Axis]
  Type = 0
FEATURE [PartDesign::PolarPattern] PolarPattern
  Angle = 360
  Axis = -> Pocket011 [Edge104]
  BaseFeature = -> Pocket011
  Occurrences = 25
  Originals = -> [Pocket011]
FEATURE [PartDesign::Fillet] Fillet001
  Base = -> Pocket005 [Edge45,Edge23,Edge52,Edge28]
  BaseFeature = -> Pocket005
  Radius = 3.4
  SupportTransform = false
  UseAllEdges = false
FEATURE [Sketcher::SketchObject] Sketch030
  FullyConstrained = true
  MapMode = 5
  Placement = pos=(-8.4e-15,1.32e-14,30) rot=(0,0,-1;1.5708rad)
  Support = -> [Pocket010]
  sketch-geometry (8):
    g0: ArcOfCircle CenterX=-10 CenterY=40 CenterZ=0 NormalX=0 NormalY=0 NormalZ=1 AngleXU=0 Radius=6 StartAngle=3.14159 EndAngle=6.28319
    g1: ArcOfCircle CenterX=-10 CenterY=80 CenterZ=0 NormalX=0 NormalY=0 NormalZ=1 AngleXU=0 Radius=6 StartAngle=-1.8e-15 EndAngle=3.14159
    g2: LineSegment StartX=-4 StartY=40 StartZ=0 EndX=-4 EndY=80 EndZ=0
    g3: LineSegment StartX=-16 StartY=80 StartZ=0 EndX=-16 EndY=40 EndZ=0
    g4: ArcOfCircle CenterX=-10 CenterY=180 CenterZ=0 NormalX=0 NormalY=0 NormalZ=1 AngleXU=0 Radius=6 StartAngle=2.9e-15 EndAngle=3.14159
    g5: ArcOfCircle CenterX=-10 CenterY=140 CenterZ=0 NormalX=0 NormalY=0 NormalZ=1 AngleXU=0 Radius=6 StartAngle=3.14159 EndAngle=6.28319
    g6: LineSegment StartX=-16 StartY=180 StartZ=0 EndX=-16 EndY=140 EndZ=0
    g7: LineSegment StartX=-4 StartY=140 StartZ=0 EndX=-4 EndY=180 EndZ=0
  constraints (20):
    c: Tangent(g0,g2) = -1.5708
    c: Tangent(g2,g1) = -1.5708
    c: Tangent(g1,g3) = -1.5708
    c: Tangent(g3,g0) = -1.5708
    c: Equal(g0,g1)
    c: Vertical(g2)
    c: Diameter(g1) = 12
    c: DistanceY(g2,g2) = 40
    c: DistanceX(g-1,g0) = -10
    c: DistanceY(g-1,g0) = 40
    c: Tangent(g4,g6) = -1.5708
    c: Tangent(g6,g5) = -1.5708
    c: Tangent(g5,g7) = -1.5708
    c: Tangent(g7,g4) = -1.5708
    c: Equal(g4,g5)
    c: Vertical(g6)
    c: DistanceY(g1,g5) = 60
    c: DistanceY(g7,g7) = 40
    c: Diameter(g5) = 12
    c: Vertical(g5,g1)
FEATURE [PartDesign::Pocket] Pocket012
  BaseFeature = -> Pocket010
  Direction = (3e-16,-8e-16,-1)
  Length = 26.5
  Length2 = 5
  Placement = pos=(0,0,0) rot=(0.57735,0.57735,0.57735;2.0944rad)
  Profile = -> Sketch030
  ReferenceAxis = -> Sketch030 [N_Axis]
  Type = 0
FEATURE [Sketcher::SketchObject] Sketch031
  FullyConstrained = true
  MapMode = 5
  Placement = pos=(-8.4e-15,1.32e-14,30) rot=(0,0,-1;1.5708rad)
  Support = -> [Pocket012]
  sketch-geometry (4):
    g0: Circle CenterX=-10 CenterY=45 CenterZ=0 NormalX=0 NormalY=0 NormalZ=1 AngleXU=0 Radius=3.1
    g1: Circle CenterX=-10 CenterY=75 CenterZ=0 NormalX=0 NormalY=0 NormalZ=1 AngleXU=0 Radius=3.1
    g2: Circle CenterX=-10 CenterY=145 CenterZ=0 NormalX=0 NormalY=0 NormalZ=1 AngleXU=0 Radius=3.1
    g3: Circle CenterX=-10 CenterY=175 CenterZ=0 NormalX=0 NormalY=0 NormalZ=1 AngleXU=0 Radius=3.1
  constraints (12):
    c: Equal(g0,g1)
    c: Equal(g1,g2)
    c: Equal(g2,g3)
    c: Vertical(g3,g2)
    c: Vertical(g2,g1)
    c: Vertical(g1,g0)
    c: DistanceX(g0,g-1) = 10
    c: DistanceY(g-1,g0) = 45
    c: DistanceY(g0,g1) = 30
    c: DistanceY(g1,g2) = 70
    c: DistanceY(g2,g3) = 30
    c: Diameter(g2) = 6.2
FEATURE [PartDesign::Pocket] Pocket013
  BaseFeature = -> Pocket012
  Direction = (3e-16,-8e-16,-1)
  Length = 5
  Length2 = 5
  Placement = pos=(0,0,0) rot=(0.57735,0.57735,0.57735;2.0944rad)
  Profile = -> Sketch031
  ReferenceAxis = -> Sketch031 [N_Axis]
  Type = 1
FEATURE [Sketcher::SketchObject] Sketch032
  ExternalGeometry = -> [Pocket013]
  FullyConstrained = true
  MapMode = 5
  Placement = pos=(-1.47e-14,0,52.5) rot=(0,0,-1;1.5708rad)
  Support = -> [Pocket013]
  sketch-geometry (6):
    g0: LineSegment StartX=10 StartY=11 StartZ=0 EndX=8 EndY=11 EndZ=0
    g1: LineSegment StartX=8 StartY=11 StartZ=0 EndX=8 EndY=9 EndZ=0
    g2: LineSegment StartX=8 StartY=9 StartZ=0 EndX=10 EndY=9 EndZ=0
    g3: LineSegment StartX=10 StartY=9 StartZ=0 EndX=10 EndY=11 EndZ=0
    g4: LineSegment StartX=10 StartY=20 StartZ=0 EndX=8 EndY=11 EndZ=0
    g5: LineSegment StartX=8 StartY=9 StartZ=0 EndX=10 EndY=-3.6e-15 EndZ=0
  constraints (16):
    c: Coincident(g0,g1)
    c: Coincident(g1,g2)
    c: Coincident(g2,g3)
    c: Coincident(g3,g0)
    c: Horizontal(g0)
    c: Horizontal(g2)
    c: Vertical(g1)
    c: Vertical(g3)
    c: PointOnObject(g0,g-3)
    c: DistanceX(g2,g2) = 2
    c: DistanceY(g1,g1) = 2
    c: Coincident(g4,g-3)
    c: Coincident(g4,g0)
    c: Coincident(g5,g1)
    c: Coincident(g5,g-3)
    c: Equal(g4,g5)
FEATURE [PartDesign::Pocket] Pocket014
  BaseFeature = -> Pocket013
  Direction = (3e-16,-3e-16,-1)
  Length = 5
  Length2 = 5
  Placement = pos=(0,0,0) rot=(0.57735,0.57735,0.57735;2.0944rad)
  Profile = -> Sketch032
  ReferenceAxis = -> Sketch032 [N_Axis]
  Type = 1
FEATURE [PartDesign::Body] Body  label="Slide-left-Body"
  Group = -> [Sketch,Pad,Sketch008,Pocket,Sketch009,Pocket001,Sketch013,Sketch023,Pad011,Sketch025,Pocket008,Sketch026,Pocket009,Sketch027,Pocket010,Sketch030,Pocket012,Sketch031,Pocket013,Sketch032,Pocket014]
  Origin = -> Origin
  Placement = pos=(-375,53,160) rot=(0,0,-1;1.5708rad)
  Tip = -> Pocket014
FEATURE [Part::Feature] Body005  label="Slide-left-Body001"
  Placement = pos=(-2.65e-13,52.3784,-2.09e-13) rot=(0,0,-1;1.5708rad)
  shape: bbox 30 x 200 x 55 mm, 70 faces (baked)
FEATURE [Sketcher::SketchObject] Sketch033
  FullyConstrained = true
  MapMode = 5
  Support = -> [XY_Plane005]
  sketch-geometry (12):
    g0: LineSegment StartX=0 StartY=0 StartZ=0 EndX=80 EndY=0 EndZ=0
    g1: LineSegment StartX=80 StartY=0 StartZ=0 EndX=80 EndY=-200 EndZ=0
    g2: LineSegment StartX=80 StartY=-200 StartZ=0 EndX=0 EndY=-200 EndZ=0
    g3: LineSegment StartX=0 StartY=-200 StartZ=0 EndX=0 EndY=0 EndZ=0
    g4: LineSegment StartX=0 StartY=0 StartZ=0 EndX=10 EndY=20 EndZ=0
    g5: LineSegment StartX=10 StartY=20 StartZ=0 EndX=20 EndY=0 EndZ=0
    g6: LineSegment StartX=20 StartY=0 StartZ=0 EndX=30 EndY=20 EndZ=0
    g7: LineSegment StartX=30 StartY=20 StartZ=0 EndX=40 EndY=0 EndZ=0
    g8: LineSegment StartX=40 StartY=0 StartZ=0 EndX=50 EndY=20 EndZ=0
    g9: LineSegment StartX=50 StartY=20 StartZ=0 EndX=60 EndY=0 EndZ=0
    g10: LineSegment StartX=60 StartY=0 StartZ=0 EndX=70 EndY=20 EndZ=0
    g11: LineSegment StartX=70 StartY=20 StartZ=0 EndX=80 EndY=0 EndZ=0
  constraints (34):
    c: Coincident(g0,g1)
    c: Coincident(g1,g2)
    c: Coincident(g2,g3)
    c: Coincident(g3,g0)
    c: Horizontal(g0)
    c: Horizontal(g2)
    c: Vertical(g1)
    c: Vertical(g3)
    c: Coincident(g0,g-1)
    c: Coincident(g4,g0)
    c: Coincident(g5,g4)
    c: PointOnObject(g5,g0)
    c: Coincident(g6,g5)
    c: Coincident(g7,g6)
    c: PointOnObject(g7,g0)
    c: Coincident(g8,g7)
    c: Coincident(g9,g8)
    c: PointOnObject(g9,g0)
    c: Coincident(g10,g9)
    c: Coincident(g11,g10)
    c: Coincident(g11,g0)
    c: Horizontal(g4,g6)
    c: Horizontal(g6,g8)
    c: Horizontal(g8,g10)
    c: Equal(g4,g5)
    c: Equal(g5,g6)
    c: Equal(g6,g7)
    c: Equal(g7,g8)
    c: Equal(g8,g9)
    c: Equal(g9,g10)
    c: Equal(g10,g11)
    c: DistanceY(g3,g4) = 20
    c: DistanceX(g2,g2) = 80
    c: DistanceY(g3,g3) = 200
FEATURE [PartDesign::Pad] Pad012
  Direction = (0,0,1)
  Length = 100
  Length2 = 10
  Profile = -> Sketch033
  ReferenceAxis = -> Sketch033 [N_Axis]
  Type = 0
FEATURE [PartDesign::Body] Body006  label="slicer"
  Group = -> [Sketch033,Pad012]
  Origin = -> Origin005
  Placement = pos=(0,-118,0) rot=(0,0,1;0rad)
  Tip = -> Pad012
FEATURE [Part::FeaturePython] Workplane003  # WARN: FeaturePython — macro-defined, semantics opaque (R4)
  Fixed = true
  Length = 293.07
  Width = 293.07
FEATURE [Part::FeaturePython] Workplane004  # WARN: FeaturePython — macro-defined, semantics opaque (R4)
  Fixed = true
  Length = 642.746
  Placement = pos=(0,0,0) rot=(0,-1,0;1.5708rad)
  Width = 642.746
FEATURE [PartDesign::FeatureBase] BaseFeature
  BaseFeature = -> Body005
FEATURE [PartDesign::Body] Body007  label="slide_left"
  BaseFeature = -> Body005
  Group = -> [BaseFeature]
  Origin = -> Origin006
  Placement = pos=(-3.61219e-10,-6.07967e-06,-1.25325e-09) rot=(0,0,-1;1.5708rad)
  Tip = -> BaseFeature
FEATURE [Part::FeaturePython] Slice  # WARN: FeaturePython — macro-defined, semantics opaque (R4)
  Base = -> Body007
  Mode = 1
  Tolerance = 0
  Tools = -> [Body006]
FEATURE [Part::FeaturePython] Slice_child0  label="Slice.0"  # WARN: FeaturePython — macro-defined, semantics opaque (R4)
  Base = -> Slice
  FilterType = 1
  Invert = false
  OverrideMaxVal = 0
  WindowFrom = 80
  WindowTo = 100
  items = 0
FEATURE [Part::FeaturePython] Slice_child1  label="Slice.1"  # WARN: FeaturePython — macro-defined, semantics opaque (R4)
  Base = -> Slice
  FilterType = 1
  Invert = false
  OverrideMaxVal = 0
  WindowFrom = 80
  WindowTo = 100
  items = 1
FEATURE [App::DocumentObjectGroup] GrExplode_Slice  label="Exploded Slice"
  Group = -> [Slice_child0,Slice_child1]
FEATURE [Part::FeaturePython] Parts009  # WARN: FeaturePython — macro-defined, semantics opaque (R4)
  Group = -> [Body006,Workplane003,Workplane004,Body007,GrExplode_Slice]
  GroupMode = 0
FEATURE [Sketcher::SketchObject] Sketch034
  FullyConstrained = true
  MapMode = 5
  Support = -> [XY_Plane007]
  sketch-geometry (12):
    g0: LineSegment StartX=0 StartY=0 StartZ=0 EndX=80 EndY=0 EndZ=0
    g1: LineSegment StartX=80 StartY=0 StartZ=0 EndX=80 EndY=-200 EndZ=0
    g2: LineSegment StartX=80 StartY=-200 StartZ=0 EndX=0 EndY=-200 EndZ=0
    g3: LineSegment StartX=0 StartY=-200 StartZ=0 EndX=0 EndY=0 EndZ=0
    g4: LineSegment StartX=0 StartY=0 StartZ=0 EndX=10 EndY=20 EndZ=0
    g5: LineSegment StartX=10 StartY=20 StartZ=0 EndX=20 EndY=0 EndZ=0
    g6: LineSegment StartX=20 StartY=0 StartZ=0 EndX=30 EndY=20 EndZ=0
    g7: LineSegment StartX=30 StartY=20 StartZ=0 EndX=40 EndY=0 EndZ=0
    g8: LineSegment StartX=40 StartY=0 StartZ=0 EndX=50 EndY=20 EndZ=0
    g9: LineSegment StartX=50 StartY=20 StartZ=0 EndX=60 EndY=0 EndZ=0
    g10: LineSegment StartX=60 StartY=0 StartZ=0 EndX=70 EndY=20 EndZ=0
    g11: LineSegment StartX=70 StartY=20 StartZ=0 EndX=80 EndY=0 EndZ=0
  constraints (34):
    c: Coincident(g0,g1)
    c: Coincident(g1,g2)
    c: Coincident(g2,g3)
    c: Coincident(g3,g0)
    c: Horizontal(g0)
    c: Horizontal(g2)
    c: Vertical(g1)
    c: Vertical(g3)
    c: Coincident(g0,g-1)
    c: Coincident(g4,g0)
    c: Coincident(g5,g4)
    c: PointOnObject(g5,g0)
    c: Coincident(g6,g5)
    c: Coincident(g7,g6)
    c: PointOnObject(g7,g0)
    c: Coincident(g8,g7)
    c: Coincident(g9,g8)
    c: PointOnObject(g9,g0)
    c: Coincident(g10,g9)
    c: Coincident(g11,g10)
    c: Coincident(g11,g0)
    c: Horizontal(g4,g6)
    c: Horizontal(g6,g8)
    c: Horizontal(g8,g10)
    c: Equal(g4,g5)
    c: Equal(g5,g6)
    c: Equal(g6,g7)
    c: Equal(g7,g8)
    c: Equal(g8,g9)
    c: Equal(g9,g10)
    c: Equal(g10,g11)
    c: DistanceY(g3,g4) = 20
    c: DistanceX(g2,g2) = 80
    c: DistanceY(g3,g3) = 200
FEATURE [PartDesign::Pad] Pad013
  Direction = (0,0,1)
  Length = 100
  Length2 = 10
  Profile = -> Sketch034
  ReferenceAxis = -> Sketch034 [N_Axis]
  Type = 0
FEATURE [PartDesign::Body] Body008  label="slicer001"
  Group = -> [Sketch034,Pad013]
  Origin = -> Origin007
  Placement = pos=(-375,-66.9999,160) rot=(0,0,-1;0rad)
  Tip = -> Pad013
FEATURE [Part::FeaturePython] Slice001  # WARN: FeaturePython — macro-defined, semantics opaque (R4)
  Base = -> Body
  Mode = 1
  Tolerance = 0
  Tools = -> [Body008]
FEATURE [Part::FeaturePython] Slice001_child0  label="Slice001.0"  # WARN: FeaturePython — macro-defined, semantics opaque (R4)
  Base = -> Slice001
  FilterType = 1
  Invert = false
  OverrideMaxVal = 0
  WindowFrom = 80
  WindowTo = 100
  items = 0
FEATURE [Part::FeaturePython] Slice001_child1  label="Slice001.1"  # WARN: FeaturePython — macro-defined, semantics opaque (R4)
  Base = -> Slice001
  FilterType = 1
  Invert = false
  OverrideMaxVal = 0
  WindowFrom = 80
  WindowTo = 100
  items = 1
FEATURE [App::DocumentObjectGroup] GrExplode_Slice001  label="Exploded Slice001"
  Group = -> [Slice001_child0,Slice001_child1]
FEATURE [Part::FeaturePython] Parts001  # WARN: FeaturePython — macro-defined, semantics opaque (R4)
  Group = -> [Body,Body008,GrExplode_Slice001]
  GroupMode = 0
FEATURE [Sketcher::SketchObject] Sketch035
  FullyConstrained = true
  MapMode = 5
  Support = -> [XY_Plane008]
  sketch-geometry (12):
    g0: LineSegment StartX=0 StartY=0 StartZ=0 EndX=100 EndY=0 EndZ=0
    g1: LineSegment StartX=100 StartY=0 StartZ=0 EndX=100 EndY=-200 EndZ=0
    g2: LineSegment StartX=100 StartY=-200 StartZ=0 EndX=0 EndY=-200 EndZ=0
    g3: LineSegment StartX=0 StartY=-200 StartZ=0 EndX=0 EndY=0 EndZ=0
    g4: LineSegment StartX=0 StartY=0 StartZ=0 EndX=12.5 EndY=20 EndZ=0
    g5: LineSegment StartX=12.5 StartY=20 StartZ=0 EndX=25 EndY=0 EndZ=0
    g6: LineSegment StartX=25 StartY=0 StartZ=0 EndX=37.5 EndY=20 EndZ=0
    g7: LineSegment StartX=37.5 StartY=20 StartZ=0 EndX=50 EndY=0 EndZ=0
    g8: LineSegment StartX=50 StartY=0 StartZ=0 EndX=62.5 EndY=20 EndZ=0
    g9: LineSegment StartX=62.5 StartY=20 StartZ=0 EndX=75 EndY=0 EndZ=0
    g10: LineSegment StartX=75 StartY=0 StartZ=0 EndX=87.5 EndY=20 EndZ=0
    g11: LineSegment StartX=87.5 StartY=20 StartZ=0 EndX=100 EndY=0 EndZ=0
  constraints (34):
    c: Coincident(g0,g1)
    c: Coincident(g1,g2)
    c: Coincident(g2,g3)
    c: Coincident(g3,g0)
    c: Horizontal(g0)
    c: Horizontal(g2)
    c: Vertical(g1)
    c: Vertical(g3)
    c: Coincident(g0,g-1)
    c: Coincident(g4,g0)
    c: Coincident(g5,g4)
    c: PointOnObject(g5,g0)
    c: Coincident(g6,g5)
    c: Coincident(g7,g6)
    c: PointOnObject(g7,g0)
    c: Coincident(g8,g7)
    c: Coincident(g9,g8)
    c: PointOnObject(g9,g0)
    c: Coincident(g10,g9)
    c: Coincident(g11,g10)
    c: Coincident(g11,g0)
    c: Horizontal(g4,g6)
    c: Horizontal(g6,g8)
    c: Horizontal(g8,g10)
    c: Equal(g4,g5)
    c: Equal(g5,g6)
    c: Equal(g6,g7)
    c: Equal(g7,g8)
    c: Equal(g8,g9)
    c: Equal(g9,g10)
    c: Equal(g10,g11)
    c: DistanceY(g3,g4) = 20
    c: DistanceX(g2,g2) = 100
    c: DistanceY(g3,g3) = 200
FEATURE [PartDesign::Pad] Pad014
  Direction = (0,0,1)
  Length = 100
  Length2 = 10
  Profile = -> Sketch035
  ReferenceAxis = -> Sketch035 [N_Axis]
  Type = 0
FEATURE [PartDesign::Body] Body009  label="slicer-door"
  Group = -> [Sketch035,Pad014]
  Origin = -> Origin008
  Placement = pos=(-301,-38.5,136.994) rot=(-0.000109,-0.000109,1;1.5708rad)
  Tip = -> Pad014
FEATURE [Sketcher::SketchObject] Sketch036
  FullyConstrained = true
  MapMode = 5
  Support = -> [XY_Plane009]
  sketch-geometry (12):
    g0: LineSegment StartX=0 StartY=0 StartZ=0 EndX=100 EndY=0 EndZ=0
    g1: LineSegment StartX=100 StartY=0 StartZ=0 EndX=100 EndY=-200 EndZ=0
    g2: LineSegment StartX=100 StartY=-200 StartZ=0 EndX=0 EndY=-200 EndZ=0
    g3: LineSegment StartX=0 StartY=-200 StartZ=0 EndX=0 EndY=0 EndZ=0
    g4: LineSegment StartX=0 StartY=0 StartZ=0 EndX=12.5 EndY=20 EndZ=0
    g5: LineSegment StartX=12.5 StartY=20 StartZ=0 EndX=25 EndY=0 EndZ=0
    g6: LineSegment StartX=25 StartY=0 StartZ=0 EndX=37.5 EndY=20 EndZ=0
    g7: LineSegment StartX=37.5 StartY=20 StartZ=0 EndX=50 EndY=0 EndZ=0
    g8: LineSegment StartX=50 StartY=0 StartZ=0 EndX=62.5 EndY=20 EndZ=0
    g9: LineSegment StartX=62.5 StartY=20 StartZ=0 EndX=75 EndY=0 EndZ=0
    g10: LineSegment StartX=75 StartY=0 StartZ=0 EndX=87.5 EndY=20 EndZ=0
    g11: LineSegment StartX=87.5 StartY=20 StartZ=0 EndX=100 EndY=0 EndZ=0
  constraints (34):
    c: Coincident(g0,g1)
    c: Coincident(g1,g2)
    c: Coincident(g2,g3)
    c: Coincident(g3,g0)
    c: Horizontal(g0)
    c: Horizontal(g2)
    c: Vertical(g1)
    c: Vertical(g3)
    c: Coincident(g0,g-1)
    c: Coincident(g4,g0)
    c: Coincident(g5,g4)
    c: PointOnObject(g5,g0)
    c: Coincident(g6,g5)
    c: Coincident(g7,g6)
    c: PointOnObject(g7,g0)
    c: Coincident(g8,g7)
    c: Coincident(g9,g8)
    c: PointOnObject(g9,g0)
    c: Coincident(g10,g9)
    c: Coincident(g11,g10)
    c: Coincident(g11,g0)
    c: Horizontal(g4,g6)
    c: Horizontal(g6,g8)
    c: Horizontal(g8,g10)
    c: Equal(g4,g5)
    c: Equal(g5,g6)
    c: Equal(g6,g7)
    c: Equal(g7,g8)
    c: Equal(g8,g9)
    c: Equal(g9,g10)
    c: Equal(g10,g11)
    c: DistanceY(g3,g4) = 20
    c: DistanceX(g2,g2) = 100
    c: DistanceY(g3,g3) = 200
FEATURE [PartDesign::Pad] Pad015
  Direction = (0,0,1)
  Length = 100
  Length2 = 10
  Profile = -> Sketch036
  ReferenceAxis = -> Sketch036 [N_Axis]
  Type = 0
FEATURE [PartDesign::Body] Body010  label="slicer-door001"
  Group = -> [Sketch036,Pad015]
  Origin = -> Origin009
  Placement = pos=(-239.019,-38.5,137.008) rot=(-0.000109,-0.000109,1;1.5708rad)
  Tip = -> Pad015
FEATURE [PartDesign::Fillet] Fillet
  Base = -> PolarPattern [Edge34,Edge74,Edge81,Edge39,Edge44,Edge49,Edge95,Edge88]
  BaseFeature = -> PolarPattern
  Radius = 3.4
  SupportTransform = false
  UseAllEdges = false
FEATURE [Sketcher::SketchObject] Sketch037
  FullyConstrained = true
  MapMode = 5
  Support = -> [XY_Plane010]
  sketch-geometry (12):
    g0: LineSegment StartX=0 StartY=0 StartZ=0 EndX=100 EndY=0 EndZ=0
    g1: LineSegment StartX=100 StartY=0 StartZ=0 EndX=100 EndY=-200 EndZ=0
    g2: LineSegment StartX=100 StartY=-200 StartZ=0 EndX=0 EndY=-200 EndZ=0
    g3: LineSegment StartX=0 StartY=-200 StartZ=0 EndX=0 EndY=0 EndZ=0
    g4: LineSegment StartX=0 StartY=0 StartZ=0 EndX=12.5 EndY=20 EndZ=0
    g5: LineSegment StartX=12.5 StartY=20 StartZ=0 EndX=25 EndY=0 EndZ=0
    g6: LineSegment StartX=25 StartY=0 StartZ=0 EndX=37.5 EndY=20 EndZ=0
    g7: LineSegment StartX=37.5 StartY=20 StartZ=0 EndX=50 EndY=0 EndZ=0
    g8: LineSegment StartX=50 StartY=0 StartZ=0 EndX=62.5 EndY=20 EndZ=0
    g9: LineSegment StartX=62.5 StartY=20 StartZ=0 EndX=75 EndY=0 EndZ=0
    g10: LineSegment StartX=75 StartY=0 StartZ=0 EndX=87.5 EndY=20 EndZ=0
    g11: LineSegment StartX=87.5 StartY=20 StartZ=0 EndX=100 EndY=0 EndZ=0
  constraints (34):
    c: Coincident(g0,g1)
    c: Coincident(g1,g2)
    c: Coincident(g2,g3)
    c: Coincident(g3,g0)
    c: Horizontal(g0)
    c: Horizontal(g2)
    c: Vertical(g1)
    c: Vertical(g3)
    c: Coincident(g0,g-1)
    c: Coincident(g4,g0)
    c: Coincident(g5,g4)
    c: PointOnObject(g5,g0)
    c: Coincident(g6,g5)
    c: Coincident(g7,g6)
    c: PointOnObject(g7,g0)
    c: Coincident(g8,g7)
    c: Coincident(g9,g8)
    c: PointOnObject(g9,g0)
    c: Coincident(g10,g9)
    c: Coincident(g11,g10)
    c: Coincident(g11,g0)
    c: Horizontal(g4,g6)
    c: Horizontal(g6,g8)
    c: Horizontal(g8,g10)
    c: Equal(g4,g5)
    c: Equal(g5,g6)
    c: Equal(g6,g7)
    c: Equal(g7,g8)
    c: Equal(g8,g9)
    c: Equal(g9,g10)
    c: Equal(g10,g11)
    c: DistanceY(g3,g4) = 20
    c: DistanceX(g2,g2) = 100
    c: DistanceY(g3,g3) = 200
FEATURE [PartDesign::Pad] Pad016
  Direction = (0,0,1)
  Length = 100
  Length2 = 10
  Profile = -> Sketch037
  ReferenceAxis = -> Sketch037 [N_Axis]
  Type = 0
FEATURE [PartDesign::Body] Body011  label="slicer-door002"
  Group = -> [Sketch037,Pad016]
  Origin = -> Origin010
  Placement = pos=(61.2383,-95.0997,-36.5271) rot=(-0.000109,-0.000109,1;1.5708rad)
  Tip = -> Pad016
FEATURE [Sketcher::SketchObject] Sketch038
  FullyConstrained = true
  MapMode = 5
  Support = -> [XY_Plane011]
  sketch-geometry (12):
    g0: LineSegment StartX=0 StartY=0 StartZ=0 EndX=100 EndY=0 EndZ=0
    g1: LineSegment StartX=100 StartY=0 StartZ=0 EndX=100 EndY=-200 EndZ=0
    g2: LineSegment StartX=100 StartY=-200 StartZ=0 EndX=0 EndY=-200 EndZ=0
    g3: LineSegment StartX=0 StartY=-200 StartZ=0 EndX=0 EndY=0 EndZ=0
    g4: LineSegment StartX=0 StartY=0 StartZ=0 EndX=12.5 EndY=20 EndZ=0
    g5: LineSegment StartX=12.5 StartY=20 StartZ=0 EndX=25 EndY=0 EndZ=0
    g6: LineSegment StartX=25 StartY=0 StartZ=0 EndX=37.5 EndY=20 EndZ=0
    g7: LineSegment StartX=37.5 StartY=20 StartZ=0 EndX=50 EndY=0 EndZ=0
    g8: LineSegment StartX=50 StartY=0 StartZ=0 EndX=62.5 EndY=20 EndZ=0
    g9: LineSegment StartX=62.5 StartY=20 StartZ=0 EndX=75 EndY=0 EndZ=0
    g10: LineSegment StartX=75 StartY=0 StartZ=0 EndX=87.5 EndY=20 EndZ=0
    g11: LineSegment StartX=87.5 StartY=20 StartZ=0 EndX=100 EndY=0 EndZ=0
  constraints (34):
    c: Coincident(g0,g1)
    c: Coincident(g1,g2)
    c: Coincident(g2,g3)
    c: Coincident(g3,g0)
    c: Horizontal(g0)
    c: Horizontal(g2)
    c: Vertical(g1)
    c: Vertical(g3)
    c: Coincident(g0,g-1)
    c: Coincident(g4,g0)
    c: Coincident(g5,g4)
    c: PointOnObject(g5,g0)
    c: Coincident(g6,g5)
    c: Coincident(g7,g6)
    c: PointOnObject(g7,g0)
    c: Coincident(g8,g7)
    c: Coincident(g9,g8)
    c: PointOnObject(g9,g0)
    c: Coincident(g10,g9)
    c: Coincident(g11,g10)
    c: Coincident(g11,g0)
    c: Horizontal(g4,g6)
    c: Horizontal(g6,g8)
    c: Horizontal(g8,g10)
    c: Equal(g4,g5)
    c: Equal(g5,g6)
    c: Equal(g6,g7)
    c: Equal(g7,g8)
    c: Equal(g8,g9)
    c: Equal(g9,g10)
    c: Equal(g10,g11)
    c: DistanceY(g3,g4) = 20
    c: DistanceX(g2,g2) = 100
    c: DistanceY(g3,g3) = 200
FEATURE [PartDesign::Pad] Pad017
  Direction = (0,0,1)
  Length = 100
  Length2 = 10
  Profile = -> Sketch038
  ReferenceAxis = -> Sketch038 [N_Axis]
  Type = 0
FEATURE [PartDesign::Body] Body012  label="slicer-door003"
  Group = -> [Sketch038,Pad017]
  Origin = -> Origin011
  Placement = pos=(122.838,-95.0997,-36.5136) rot=(-0.000109,-0.000109,1;1.5708rad)
  Tip = -> Pad017
FEATURE [Sketcher::SketchObject] Sketch039
  FullyConstrained = true
  MapMode = 5
  Placement = pos=(0,0,0) rot=(0.57735,0.57735,0.57735;2.0944rad)
  Support = -> [YZ_Plane012]
  sketch-geometry (4):
    g0: LineSegment StartX=0 StartY=0 StartZ=0 EndX=20 EndY=0 EndZ=0
    g1: LineSegment StartX=20 StartY=0 StartZ=0 EndX=20 EndY=30 EndZ=0
    g2: LineSegment StartX=20 StartY=30 StartZ=0 EndX=0 EndY=30 EndZ=0
    g3: LineSegment StartX=0 StartY=30 StartZ=0 EndX=0 EndY=0 EndZ=0
  constraints (11):
    c: Coincident(g0,g1)
    c: Coincident(g1,g2)
    c: Coincident(g2,g3)
    c: Coincident(g3,g0)
    c: Horizontal(g0)
    c: Horizontal(g2)
    c: Vertical(g1)
    c: Vertical(g3)
    c: Coincident(g0,g-1)
    c: DistanceY(g3,g3) = 30
    c: DistanceX(g0,g0) = 20
FEATURE [PartDesign::Pad] Pad018  label="Pad-body003"
  Direction = (1,-2e-16,3e-16)
  Length = 200
  Length2 = 10
  Placement = pos=(0,0,0) rot=(0.57735,0.57735,0.57735;2.0944rad)
  Profile = -> Sketch039
  ReferenceAxis = -> Sketch039 [N_Axis]
  Type = 0
FEATURE [Sketcher::SketchObject] Sketch040
  FullyConstrained = true
  MapMode = 5
  Placement = pos=(8.8e-15,20,-4.4e-15) rot=(0.57735,0.57735,0.57735;4.18879rad)
  Support = -> [Pad018]
  sketch-geometry (5):
    g0: Circle CenterX=15 CenterY=10 CenterZ=0 NormalX=0 NormalY=0 NormalZ=1 AngleXU=0 Radius=5
    g1: ArcOfCircle CenterX=15 CenterY=190 CenterZ=0 NormalX=0 NormalY=0 NormalZ=1 AngleXU=0 Radius=5 StartAngle=1.7e-15 EndAngle=3.14159
    g2: ArcOfCircle CenterX=15 CenterY=35 CenterZ=0 NormalX=0 NormalY=0 NormalZ=1 AngleXU=0 Radius=5 StartAngle=3.14159 EndAngle=6.28319
    g3: LineSegment StartX=10 StartY=190 StartZ=0 EndX=10 EndY=35 EndZ=0
    g4: LineSegment StartX=20 StartY=35 StartZ=0 EndX=20 EndY=190 EndZ=0
  constraints (13):
    c: Diameter(g0) = 10
    c: DistanceX(g-1,g0) = 15
    c: DistanceY(g-1,g0) = 10
    c: Tangent(g1,g3) = -1.5708
    c: Tangent(g3,g2) = -1.5708
    c: Tangent(g2,g4) = -1.5708
    c: Tangent(g4,g1) = -1.5708
    c: Equal(g1,g2)
    c: Vertical(g3)
    c: Radius(g2) = 5
    c: Vertical(g2,g0)
    c: DistanceY(g0,g2) = 25
    c: DistanceY(g0,g1) = 180
FEATURE [PartDesign::Pocket] Pocket015  label="Pocket-slider_guide002"
  BaseFeature = -> Pad018
  Direction = (-3e-16,-1,1e-16)
  Length = 5
  Length2 = 5
  Placement = pos=(0,0,0) rot=(0.57735,0.57735,0.57735;2.0944rad)
  Profile = -> Sketch040
  ReferenceAxis = -> Sketch040 [N_Axis]
  Type = 1
FEATURE [Sketcher::SketchObject] Sketch041
  FullyConstrained = true
  MapMode = 5
  Placement = pos=(-8.4e-15,1.32e-14,30) rot=(0,0,-1;1.5708rad)
  Support = -> [Pocket015]
  sketch-geometry (2):
    g0: Circle CenterX=-10 CenterY=50 CenterZ=0 NormalX=0 NormalY=0 NormalZ=1 AngleXU=0 Radius=3.1
    g1: Circle CenterX=-10 CenterY=180 CenterZ=0 NormalX=0 NormalY=0 NormalZ=1 AngleXU=0 Radius=3.1
  constraints (6):
    c: DistanceX(g0,g-1) = 10
    c: Vertical(g1,g0)
    c: DistanceY(g-1,g0) = 50
    c: DistanceY(g0,g1) = 130
    c: Diameter(g0) = 6.2
    c: Equal(g1,g0)
FEATURE [PartDesign::Pocket] Pocket016  label="Pocket-mount_holes002"
  BaseFeature = -> Pocket015
  Direction = (3e-16,-5e-16,-1)
  Length = 26.5
  Length2 = 5
  Placement = pos=(0,0,0) rot=(0.57735,0.57735,0.57735;2.0944rad)
  Profile = -> Sketch041
  ReferenceAxis = -> Sketch041 [N_Axis]
  Type = 0
FEATURE [Sketcher::SketchObject] Sketch042  label="Sketch-slider_guide_line002"
  FullyConstrained = false
  MapMode = 5
  Placement = pos=(0,1e-16,0) rot=(-0.57735,-0.57735,0.57735;4.18879rad)
  Support = -> [Pocket016]
  sketch-geometry (1):
    g0: LineSegment StartX=-14.7121 StartY=24.4994 StartZ=0 EndX=-14.7121 EndY=187.74 EndZ=0
  constraints (1):
    c: Vertical(g0)
FEATURE [Sketcher::SketchObject] Sketch043
  ExternalGeometry = -> [Pocket016]
  FullyConstrained = true
  MapMode = 5
  Placement = pos=(0,0,0) rot=(0.57735,0.57735,-0.57735;4.18879rad)
  Support = -> [Pocket016]
  sketch-geometry (8):
    g0: LineSegment StartX=-10 StartY=2.5 StartZ=0 EndX=-10 EndY=-52.5 EndZ=0
    g1: LineSegment StartX=0 StartY=0 StartZ=0 EndX=0 EndY=-30 EndZ=0
    g2: LineSegment StartX=0 StartY=-30 StartZ=0 EndX=20 EndY=-30 EndZ=0
    g3: GeomPoint X=0 Y=-15 Z=0
    g4: LineSegment StartX=4.24533 StartY=-52.5 StartZ=0 EndX=20 EndY=-30 EndZ=0
    g5: LineSegment StartX=-10 StartY=-52.5 StartZ=0 EndX=4.24533 EndY=-52.5 EndZ=0
    g6: LineSegment StartX=0 StartY=0 StartZ=0 EndX=-5 EndY=2.5 EndZ=0
    g7: LineSegment StartX=-5 StartY=2.5 StartZ=0 EndX=-10 EndY=2.5 EndZ=0
  constraints (20):
    c: Coincident(g6,g-4)
    c: Vertical(g0)
    c: Coincident(g5,g0)
    c: Coincident(g1,g6)
    c: Coincident(g0,g7)
    c: Coincident(g1,g2)
    c: Coincident(g1,g-4)
    c: DistanceX(g7,g6) = 10
    c: DistanceY(g0,g0) = 55
    c: PointOnObject(g3,g1)
    c: DistanceY(g3,g6) = 15
    c: DistanceY(g3,g7) = 17.5
    c: Horizontal(g5)
    c: Coincident(g5,g4)
    c: Coincident(g2,g4)
    c: Coincident(g2,g-3)
    c: Angle(g2,g4) = 0.959931
    c: Coincident(g6,g7)
    c: Horizontal(g7)
    c: DistanceX(g0,g6) = 5
FEATURE [PartDesign::Pad] Pad019
  BaseFeature = -> Pocket016
  Direction = (-1,2e-16,-2e-16)
  Length = 20
  Length2 = 10
  Placement = pos=(0,0,0) rot=(0.57735,0.57735,0.57735;2.0944rad)
  Profile = -> Sketch043
  ReferenceAxis = -> Sketch043 [N_Axis]
  Reversed = true
  Type = 0
FEATURE [Sketcher::SketchObject] Sketch044
  ExternalGeometry = -> [Pad019]
  FullyConstrained = true
  MapMode = 5
  Placement = pos=(-2.2e-15,-10,6e-16) rot=(-0.57735,-0.57735,0.57735;4.18879rad)
  Support = -> [Pad019]
  sketch-geometry (15):
    g0: Circle CenterX=-49.575 CenterY=14.9 CenterZ=0 NormalX=0 NormalY=0 NormalZ=1 AngleXU=0 Radius=1.125
    g1: Circle CenterX=-49.575 CenterY=5.1 CenterZ=0 NormalX=0 NormalY=0 NormalZ=1 AngleXU=0 Radius=1.125
    g2: Circle CenterX=-1.125 CenterY=14.9 CenterZ=0 NormalX=0 NormalY=0 NormalZ=1 AngleXU=0 Radius=1.125
    g3: Circle CenterX=-1.125 CenterY=5.1 CenterZ=0 NormalX=0 NormalY=0 NormalZ=1 AngleXU=0 Radius=1.125
    g4: LineSegment StartX=-46.35 StartY=0 StartZ=0 EndX=-4.35 EndY=0 EndZ=0
    g5: LineSegment StartX=-4.35 StartY=0 StartZ=0 EndX=-4.35 EndY=20 EndZ=0
    g6: LineSegment StartX=-4.35 StartY=20 StartZ=0 EndX=-46.35 EndY=20 EndZ=0
    g7: LineSegment StartX=-46.35 StartY=20 StartZ=0 EndX=-46.35 EndY=0 EndZ=0
    g8: LineSegment StartX=-49.575 StartY=14.9 StartZ=0 EndX=-49.575 EndY=5.1 EndZ=0
    g9: LineSegment StartX=-49.575 StartY=5.1 StartZ=0 EndX=-1.125 EndY=5.1 EndZ=0
    g10: LineSegment StartX=-1.125 StartY=14.9 StartZ=0 EndX=-49.575 EndY=14.9 EndZ=0
    g11: LineSegment StartX=-46.35 StartY=20 StartZ=0 EndX=-49.575 EndY=14.9 EndZ=0
    g12: LineSegment StartX=-4.35 StartY=20 StartZ=0 EndX=-1.125 EndY=14.9 EndZ=0
    g13: LineSegment StartX=-1.125 StartY=5.1 StartZ=0 EndX=-1.125 EndY=10 EndZ=0
    g14: LineSegment StartX=-1.125 StartY=10 StartZ=0 EndX=-1.125 EndY=14.9 EndZ=0
  constraints (39):
    c: Tangent(g3,g-2)
    c: Coincident(g4,g5)
    c: Coincident(g5,g6)
    c: Coincident(g6,g7)
    c: Coincident(g7,g4)
    c: Horizontal(g4)
    c: Horizontal(g6)
    c: Vertical(g5)
    c: Vertical(g7)
    c: Horizontal(g-4,g5)
    c: DistanceX(g6,g6) = 42
    c: Diameter(g2) = 2.25
    c: Equal(g0,g1)
    c: Equal(g1,g3)
    c: Equal(g3,g2)
    c: Coincident(g8,g0)
    c: Coincident(g8,g1)
    c: Vertical(g8)
    c: Coincident(g9,g1)
    c: Coincident(g9,g3)
    c: Horizontal(g9)
    c: Coincident(g13,g3)
    c: Coincident(g14,g2)
    c: Coincident(g10,g2)
    c: Coincident(g10,g0)
    c: Horizontal(g10)
    c: Coincident(g11,g6)
    c: Coincident(g11,g0)
    c: Coincident(g12,g5)
    c: Coincident(g12,g2)
    c: Equal(g12,g11)
    c: DistanceX(g9,g9) = 48.45
    c: DistanceY(g8,g8) = 9.8
    c: Coincident(g13,g14)
    c: Vertical(g13)
    c: Vertical(g14)
    c: Equal(g14,g13)
    c: DistanceY(g-4,g13) = 10
    c: PointOnObject(g4,g-5)
FEATURE [PartDesign::Pocket] Pocket017  label="Pocket-servo_mount_screw_hole_body_profile"
  BaseFeature = -> Pad019
  Direction = (1e-16,1,1e-16)
  Length = 10
  Length2 = 5
  Placement = pos=(0,0,0) rot=(0.57735,0.57735,0.57735;2.0944rad)
  Profile = -> Sketch044
  ReferenceAxis = -> Sketch044 [N_Axis]
  Type = 0
FEATURE [Sketcher::SketchObject] Sketch045
  ExternalGeometry = -> [Pocket017]
  FullyConstrained = true
  MapMode = 5
  Placement = pos=(-1.47e-14,0,52.5) rot=(0,0,-1;1.5708rad)
  Support = -> [Pocket017]
  sketch-geometry (4):
    g0: LineSegment StartX=-20 StartY=17.5 StartZ=0 EndX=5 EndY=17.5 EndZ=0
    g1: LineSegment StartX=5 StartY=17.5 StartZ=0 EndX=5 EndY=2.5 EndZ=0
    g2: LineSegment StartX=5 StartY=2.5 StartZ=0 EndX=-20 EndY=2.5 EndZ=0
    g3: LineSegment StartX=-20 StartY=2.5 StartZ=0 EndX=-20 EndY=17.5 EndZ=0
  constraints (12):
    c: Coincident(g0,g1)
    c: Coincident(g1,g2)
    c: Coincident(g2,g3)
    c: Coincident(g3,g0)
    c: Horizontal(g0)
    c: Horizontal(g2)
    c: Vertical(g1)
    c: Vertical(g3)
    c: DistanceX(g2,g2) = 25
    c: DistanceX(g1,g-3) = 5
    c: DistanceY(g-3,g1) = 2.5
    c: DistanceY(g0,g-4) = 2.5
FEATURE [PartDesign::Pocket] Pocket018  label="Pocket-servo_mount_top_nut_space"
  BaseFeature = -> Pocket017
  Direction = (3e-16,-1e-16,-1)
  Length = 6
  Length2 = 5
  Placement = pos=(0,0,0) rot=(0.57735,0.57735,0.57735;2.0944rad)
  Profile = -> Sketch045
  ReferenceAxis = -> Sketch045 [N_Axis]
  Type = 0
FEATURE [Sketcher::SketchObject] Sketch046
  ExternalGeometry = -> [Pocket018]
  FullyConstrained = true
  MapMode = 5
  Placement = pos=(7e-16,0,-2.5) rot=(0.707107,0.707107,0;3.14159rad)
  Support = -> [Pocket018]
  sketch-geometry (4):
    g0: LineSegment StartX=-5 StartY=17.5 StartZ=0 EndX=5 EndY=17.5 EndZ=0
    g1: LineSegment StartX=5 StartY=17.5 StartZ=0 EndX=5 EndY=2.5 EndZ=0
    g2: LineSegment StartX=5 StartY=2.5 StartZ=0 EndX=-5 EndY=2.5 EndZ=0
    g3: LineSegment StartX=-5 StartY=2.5 StartZ=0 EndX=-5 EndY=17.5 EndZ=0
  constraints (12):
    c: Coincident(g0,g1)
    c: Coincident(g1,g2)
    c: Coincident(g2,g3)
    c: Coincident(g3,g0)
    c: Horizontal(g0)
    c: Horizontal(g2)
    c: Vertical(g1)
    c: Vertical(g3)
    c: DistanceX(g-3,g2) = 5
    c: DistanceY(g-3,g2) = 2.5
    c: DistanceY(g0,g-3) = 2.5
    c: DistanceX(g0,g0) = 10
FEATURE [PartDesign::Pocket] Pocket019
  BaseFeature = -> Pocket018
  Direction = (-3e-16,1e-16,1)
  Length = 6
  Length2 = 5
  Placement = pos=(0,0,0) rot=(0.57735,0.57735,0.57735;2.0944rad)
  Profile = -> Sketch046
  ReferenceAxis = -> Sketch046 [N_Axis]
  Type = 0
FEATURE [Sketcher::SketchObject] Sketch047
  FullyConstrained = true
  MapMode = 5
  Placement = pos=(-8.4e-15,1.32e-14,30) rot=(0,0,-1;1.5708rad)
  Support = -> [Pocket019]
  sketch-geometry (8):
    g0: ArcOfCircle CenterX=-10 CenterY=40 CenterZ=0 NormalX=0 NormalY=0 NormalZ=1 AngleXU=0 Radius=6 StartAngle=3.14159 EndAngle=6.28319
    g1: ArcOfCircle CenterX=-10 CenterY=80 CenterZ=0 NormalX=0 NormalY=0 NormalZ=1 AngleXU=0 Radius=6 StartAngle=-1.8e-15 EndAngle=3.14159
    g2: LineSegment StartX=-4 StartY=40 StartZ=0 EndX=-4 EndY=80 EndZ=0
    g3: LineSegment StartX=-16 StartY=80 StartZ=0 EndX=-16 EndY=40 EndZ=0
    g4: ArcOfCircle CenterX=-10 CenterY=180 CenterZ=0 NormalX=0 NormalY=0 NormalZ=1 AngleXU=0 Radius=6 StartAngle=2.9e-15 EndAngle=3.14159
    g5: ArcOfCircle CenterX=-10 CenterY=140 CenterZ=0 NormalX=0 NormalY=0 NormalZ=1 AngleXU=0 Radius=6 StartAngle=3.14159 EndAngle=6.28319
    g6: LineSegment StartX=-16 StartY=180 StartZ=0 EndX=-16 EndY=140 EndZ=0
    g7: LineSegment StartX=-4 StartY=140 StartZ=0 EndX=-4 EndY=180 EndZ=0
  constraints (20):
    c: Tangent(g0,g2) = -1.5708
    c: Tangent(g2,g1) = -1.5708
    c: Tangent(g1,g3) = -1.5708
    c: Tangent(g3,g0) = -1.5708
    c: Equal(g0,g1)
    c: Vertical(g2)
    c: Diameter(g1) = 12
    c: DistanceY(g2,g2) = 40
    c: DistanceX(g-1,g0) = -10
    c: DistanceY(g-1,g0) = 40
    c: Tangent(g4,g6) = -1.5708
    c: Tangent(g6,g5) = -1.5708
    c: Tangent(g5,g7) = -1.5708
    c: Tangent(g7,g4) = -1.5708
    c: Equal(g4,g5)
    c: Vertical(g6)
    c: DistanceY(g1,g5) = 60
    c: DistanceY(g7,g7) = 40
    c: Diameter(g5) = 12
    c: Vertical(g5,g1)
FEATURE [PartDesign::Pocket] Pocket020  label="Pocket-mount_slots"
  BaseFeature = -> Pocket019
  Direction = (3e-16,-6e-16,-1)
  Length = 26.5
  Length2 = 5
  Placement = pos=(0,0,0) rot=(0.57735,0.57735,0.57735;2.0944rad)
  Profile = -> Sketch047
  ReferenceAxis = -> Sketch047 [N_Axis]
  Type = 0
FEATURE [Sketcher::SketchObject] Sketch048
  FullyConstrained = true
  MapMode = 5
  Placement = pos=(-8.4e-15,1.32e-14,30) rot=(0,0,-1;1.5708rad)
  Support = -> [Pocket020]
  sketch-geometry (4):
    g0: Circle CenterX=-10 CenterY=45 CenterZ=0 NormalX=0 NormalY=0 NormalZ=1 AngleXU=0 Radius=3.1
    g1: Circle CenterX=-10 CenterY=75 CenterZ=0 NormalX=0 NormalY=0 NormalZ=1 AngleXU=0 Radius=3.1
    g2: Circle CenterX=-10 CenterY=145 CenterZ=0 NormalX=0 NormalY=0 NormalZ=1 AngleXU=0 Radius=3.1
    g3: Circle CenterX=-10 CenterY=175 CenterZ=0 NormalX=0 NormalY=0 NormalZ=1 AngleXU=0 Radius=3.1
  constraints (12):
    c: Equal(g0,g1)
    c: Equal(g1,g2)
    c: Equal(g2,g3)
    c: Vertical(g3,g2)
    c: Vertical(g2,g1)
    c: Vertical(g1,g0)
    c: DistanceX(g0,g-1) = 10
    c: DistanceY(g-1,g0) = 45
    c: DistanceY(g0,g1) = 30
    c: DistanceY(g1,g2) = 70
    c: DistanceY(g2,g3) = 30
    c: Diameter(g2) = 6.2
FEATURE [PartDesign::Pocket] Pocket021  label="Pocket-mounting-holes"
  BaseFeature = -> Pocket020
  Direction = (3e-16,-7e-16,-1)
  Length = 5
  Length2 = 5
  Placement = pos=(0,0,0) rot=(0.57735,0.57735,0.57735;2.0944rad)
  Profile = -> Sketch048
  ReferenceAxis = -> Sketch048 [N_Axis]
  Type = 1
FEATURE [Sketcher::SketchObject] Sketch049
  ExternalGeometry = -> [Pocket021]
  FullyConstrained = true
  MapMode = 5
  Placement = pos=(-1.47e-14,0,52.5) rot=(0,0,-1;1.5708rad)
  Support = -> [Pocket021]
  sketch-geometry (6):
    g0: LineSegment StartX=10 StartY=11 StartZ=0 EndX=8 EndY=11 EndZ=0
    g1: LineSegment StartX=8 StartY=11 StartZ=0 EndX=8 EndY=9 EndZ=0
    g2: LineSegment StartX=8 StartY=9 StartZ=0 EndX=10 EndY=9 EndZ=0
    g3: LineSegment StartX=10 StartY=9 StartZ=0 EndX=10 EndY=11 EndZ=0
    g4: LineSegment StartX=10 StartY=20 StartZ=0 EndX=8 EndY=11 EndZ=0
    g5: LineSegment StartX=8 StartY=9 StartZ=0 EndX=10 EndY=-3.6e-15 EndZ=0
  constraints (16):
    c: Coincident(g0,g1)
    c: Coincident(g1,g2)
    c: Coincident(g2,g3)
    c: Coincident(g3,g0)
    c: Horizontal(g0)
    c: Horizontal(g2)
    c: Vertical(g1)
    c: Vertical(g3)
    c: PointOnObject(g0,g-3)
    c: DistanceX(g2,g2) = 2
    c: DistanceY(g1,g1) = 2
    c: Coincident(g4,g-3)
    c: Coincident(g4,g0)
    c: Coincident(g5,g1)
    c: Coincident(g5,g-3)
    c: Equal(g4,g5)
FEATURE [PartDesign::Pocket] Pocket022  label="Pocket-servo_bracket_cantilever_cutout"
  BaseFeature = -> Pocket021
  Direction = (3e-16,-3e-16,-1)
  Length = 5
  Length2 = 5
  Placement = pos=(0,0,0) rot=(0.57735,0.57735,0.57735;2.0944rad)
  Profile = -> Sketch049
  ReferenceAxis = -> Sketch049 [N_Axis]
  Type = 1
FEATURE [Sketcher::SketchObject] Sketch050
  FullyConstrained = true
  MapMode = 5
  Support = -> [XY_Plane013]
  sketch-geometry (12):
    g0: LineSegment StartX=0 StartY=0 StartZ=0 EndX=40 EndY=0 EndZ=0
    g1: LineSegment StartX=40 StartY=0 StartZ=0 EndX=40 EndY=-104 EndZ=0
    g2: LineSegment StartX=40 StartY=-104 StartZ=0 EndX=0 EndY=-104 EndZ=0
    g3: LineSegment StartX=0 StartY=-104 StartZ=0 EndX=0 EndY=0 EndZ=0
    g4: LineSegment StartX=0 StartY=0 StartZ=0 EndX=5 EndY=6 EndZ=0
    g5: LineSegment StartX=5 StartY=6 StartZ=0 EndX=10 EndY=0 EndZ=0
    g6: LineSegment StartX=10 StartY=0 StartZ=0 EndX=15 EndY=6 EndZ=0
    g7: LineSegment StartX=15 StartY=6 StartZ=0 EndX=20 EndY=0 EndZ=0
    g8: LineSegment StartX=20 StartY=0 StartZ=0 EndX=25 EndY=6 EndZ=0
    g9: LineSegment StartX=25 StartY=6 StartZ=0 EndX=30 EndY=0 EndZ=0
    g10: LineSegment StartX=30 StartY=0 StartZ=0 EndX=35 EndY=6 EndZ=0
    g11: LineSegment StartX=35 StartY=6 StartZ=0 EndX=40 EndY=0 EndZ=0
  constraints (34):
    c: Coincident(g0,g1)
    c: Coincident(g1,g2)
    c: Coincident(g2,g3)
    c: Coincident(g3,g0)
    c: Horizontal(g0)
    c: Horizontal(g2)
    c: Vertical(g1)
    c: Vertical(g3)
    c: Coincident(g0,g-1)
    c: Coincident(g4,g0)
    c: Coincident(g5,g4)
    c: PointOnObject(g5,g0)
    c: Coincident(g6,g5)
    c: Coincident(g7,g6)
    c: PointOnObject(g7,g0)
    c: Coincident(g8,g7)
    c: Coincident(g9,g8)
    c: PointOnObject(g9,g0)
    c: Coincident(g10,g9)
    c: Coincident(g11,g10)
    c: Coincident(g11,g0)
    c: Horizontal(g4,g6)
    c: Horizontal(g6,g8)
    c: Horizontal(g8,g10)
    c: Equal(g4,g5)
    c: Equal(g5,g6)
    c: Equal(g6,g7)
    c: Equal(g7,g8)
    c: Equal(g8,g9)
    c: Equal(g9,g10)
    c: Equal(g10,g11)
    c: DistanceY(g3,g4) = 6
    c: DistanceY(g3,g3) = 104
    c: DistanceX(g2,g2) = 40
FEATURE [PartDesign::Pad] Pad020
  Direction = (0,0,1)
  Length = 100
  Length2 = 10
  Profile = -> Sketch050
  ReferenceAxis = -> Sketch050 [N_Axis]
  Type = 0
FEATURE [PartDesign::Body] Body014  label="slicer002"
  Group = -> [Sketch050,Pad020]
  Origin = -> Origin013
  Placement = pos=(-377,-57,160) rot=(3e-06,0,-1;0rad)
  Tip = -> Pad020
FEATURE [Sketcher::SketchObject] Sketch051
  ExternalGeometry = -> [Pocket022]
  FullyConstrained = true
  MapMode = 5
  Placement = pos=(-8.4e-15,1.32e-14,30) rot=(0,0,-1;1.5708rad)
  Support = -> [Pocket022]
  sketch-geometry (4):
    g0: LineSegment StartX=-20 StartY=200 StartZ=0 EndX=0 EndY=200 EndZ=0
    g1: LineSegment StartX=0 StartY=200 StartZ=0 EndX=0 EndY=20 EndZ=0
    g2: LineSegment StartX=0 StartY=20 StartZ=0 EndX=-20 EndY=20 EndZ=0
    g3: LineSegment StartX=-20 StartY=20 StartZ=0 EndX=-20 EndY=200 EndZ=0
  constraints (10):
    c: Coincident(g0,g1)
    c: Coincident(g1,g2)
    c: Coincident(g2,g3)
    c: Coincident(g3,g0)
    c: Horizontal(g0)
    c: Horizontal(g2)
    c: Vertical(g1)
    c: Vertical(g3)
    c: Coincident(g0,g-3)
    c: Coincident(g1,g-4)
FEATURE [PartDesign::Pocket] Pocket023  label="Pocket-remove_flat_rail"
  BaseFeature = -> Pocket022
  Direction = (3e-16,-8e-16,-1)
  Length = 22
  Length2 = 5
  Placement = pos=(0,0,0) rot=(0.57735,0.57735,0.57735;2.0944rad)
  Profile = -> Sketch051
  ReferenceAxis = -> Sketch051 [N_Axis]
  Type = 0
FEATURE [Sketcher::SketchObject] Sketch052
  ExternalGeometry = -> [Pocket023]
  FullyConstrained = true
  MapMode = 5
  Placement = pos=(0,1e-16,0) rot=(-0.57735,-0.57735,0.57735;4.18879rad)
  Support = -> [Pocket023]
  sketch-geometry (14):
    g0: LineSegment StartX=-8 StartY=20 StartZ=0 EndX=-92.8376 EndY=20 EndZ=0
    g1: LineSegment StartX=-92.8376 StartY=20 StartZ=0 EndX=-27.323 EndY=200 EndZ=0
    g2: LineSegment StartX=-8 StartY=200 StartZ=0 EndX=-27.323 EndY=200 EndZ=0
    g3: LineSegment StartX=-59.0924 StartY=25 StartZ=0 EndX=-8 EndY=165.375 EndZ=0
    g4: LineSegment StartX=-8 StartY=165.375 StartZ=0 EndX=-8 EndY=200 EndZ=0
    g5: LineSegment StartX=-59.0924 StartY=25 StartZ=0 EndX=-8 EndY=25 EndZ=0
    g6: ArcOfCircle CenterX=-73.1434 CenterY=30.2523 CenterZ=0 NormalX=0 NormalY=0 NormalZ=1 AngleXU=0 Radius=5 StartAngle=2.79253 EndAngle=5.93412
    g7: ArcOfCircle CenterX=-15 CenterY=190 CenterZ=0 NormalX=0 NormalY=0 NormalZ=1 AngleXU=0 Radius=5 StartAngle=5.93412 EndAngle=9.07571
    g8: LineSegment StartX=-68.445 StartY=28.5422 StartZ=0 EndX=-10.3015 EndY=188.29 EndZ=0
    g9: LineSegment StartX=-19.6985 StartY=191.71 StartZ=0 EndX=-77.8419 EndY=31.9624 EndZ=0
    g10: LineSegment StartX=-19.6985 StartY=191.71 StartZ=0 EndX=-29.0954 EndY=195.13 EndZ=0
    g11: GeomPoint X=-34.2429 Y=122.511 Z=0
    g12: LineSegment StartX=-34.2429 StartY=122.511 StartZ=0 EndX=-24.846 EndY=119.091 EndZ=0
    g13: LineSegment StartX=-8 StartY=25 StartZ=0 EndX=-8 EndY=20 EndZ=0
  constraints (37):
    c: Coincident(g0,g-3)
    c: Horizontal(g0)
    c: Coincident(g1,g0)
    c: Coincident(g2,g-3)
    c: Coincident(g2,g1)
    c: Horizontal(g2)
    c: Angle(g1,g2) = 1.91986
    c: Coincident(g4,g3)
    c: Coincident(g5,g3)
    c: PointOnObject(g5,g-3)
    c: Horizontal(g5)
    c: Parallel(g3,g1)
    c: Tangent(g6,g8) = -1.5708
    c: Tangent(g8,g7) = -1.5708
    c: Tangent(g7,g9) = -1.5708
    c: Tangent(g9,g6) = -1.5708
    c: Equal(g6,g7)
    c: Parallel(g9,g1)
    c: Diameter(g6) = 10
    c: Coincident(g10,g7)
    c: PointOnObject(g10,g1)
    c: Angle(g1,g10) = 1.5708
    c: Distance(g10) = 10
    c: DistanceY(g7,g2) = 10
    c: DistanceX(g7,g2) = 7
    c: Coincident(g4,g2)
    c: Vertical(g4)
    c: PointOnObject(g11,g8)
    c: Coincident(g12,g11)
    c: PointOnObject(g12,g3)
    c: Angle(g8,g12) = 1.5708
    c: Distance(g12,g7) = 70
    c: Distance(g12) = 10
    c: Coincident(g13,g5)
    c: Coincident(g13,g0)
    c: DistanceY(g13,g13) = 5
    c: Distance(g9) = 170
FEATURE [PartDesign::Pad] Pad021  label="Pad-ramp"
  BaseFeature = -> Pocket023
  Direction = (-8e-16,-1,1e-16)
  Length = 20
  Length2 = 10
  Placement = pos=(0,0,0) rot=(0.57735,0.57735,0.57735;2.0944rad)
  Profile = -> Sketch052
  ReferenceAxis = -> Sketch052 [N_Axis]
  Reversed = true
  Type = 0
FEATURE [Sketcher::SketchObject] Sketch053  label="sketch-slide-guide"
  ExternalGeometry = -> [Pad021]
  FullyConstrained = true
  MapMode = 5
  Placement = pos=(0,1.19e-14,0) rot=(-0.57735,-0.57735,0.57735;4.18879rad)
  Support = -> [Pad021]
  sketch-geometry (3):
    g0: LineSegment StartX=-73.1434 StartY=30.2523 StartZ=0 EndX=-15 EndY=190 EndZ=0
    g1: LineSegment StartX=-15 StartY=190 StartZ=0 EndX=-10.3015 EndY=188.29 EndZ=0
    g2: LineSegment StartX=-73.1434 StartY=30.2523 StartZ=0 EndX=-68.445 EndY=28.5422 EndZ=0
  constraints (8):
    c: Coincident(g1,g0)
    c: Coincident(g1,g-3)
    c: Coincident(g2,g0)
    c: Coincident(g2,g-3)
    c: Distance(g2) = 5
    c: Angle(g-3,g2) = 1.5708
    c: Angle(g1,g-3) = 1.5708
    c: Parallel(g0,g-3)
FEATURE [Sketcher::SketchObject] Sketch054
  ExternalGeometry = -> [Pad021]
  FullyConstrained = true
  MapMode = 5
  Placement = pos=(0,1.19e-14,0) rot=(-0.57735,-0.57735,0.57735;4.18879rad)
  Support = -> [Pad021]
  sketch-geometry (5):
    g0: LineSegment StartX=-92.8376 StartY=20 StartZ=0 EndX=-27.323 EndY=200 EndZ=0
    g1: LineSegment StartX=-27.323 StartY=200 StartZ=0 EndX=-8 EndY=200 EndZ=0
    g2: LineSegment StartX=-8 StartY=200 StartZ=0 EndX=-8 EndY=165.375 EndZ=0
    g3: LineSegment StartX=-8 StartY=165.375 StartZ=0 EndX=-60.9123 EndY=20 EndZ=0
    g4: LineSegment StartX=-60.9123 StartY=20 StartZ=0 EndX=-92.8376 EndY=20 EndZ=0
  constraints (11):
    c: Coincident(g0,g-4)
    c: Coincident(g0,g-5)
    c: Coincident(g1,g0)
    c: Coincident(g1,g-6)
    c: Coincident(g2,g1)
    c: Coincident(g2,g-7)
    c: Coincident(g3,g2)
    c: PointOnObject(g3,g-4)
    c: Coincident(g4,g3)
    c: Coincident(g4,g0)
    c: PointOnObject(g-7,g3)
FEATURE [PartDesign::Pocket] Pocket024  label="Pocket-skinny_ramp"
  BaseFeature = -> Pad021
  Direction = (8e-16,1,-1e-16)
  Length = 8
  Length2 = 5
  Placement = pos=(0,0,0) rot=(0.57735,0.57735,0.57735;2.0944rad)
  Profile = -> Sketch054
  ReferenceAxis = -> Sketch054 [N_Axis]
  Type = 0
FEATURE [Sketcher::SketchObject] Sketch055
  ExternalGeometry = -> [Pocket024]
  FullyConstrained = true
  MapMode = 5
  Placement = pos=(7.1e-15,8,-9e-16) rot=(-0.57735,-0.57735,0.57735;4.18879rad)
  Support = -> [Pocket024]
  sketch-geometry (4):
    g0: ArcOfCircle CenterX=-73.1434 CenterY=30.2523 CenterZ=0 NormalX=0 NormalY=0 NormalZ=1 AngleXU=0 Radius=11.1 StartAngle=2.79253 EndAngle=5.93412
    g1: ArcOfCircle CenterX=-15 CenterY=190 CenterZ=0 NormalX=0 NormalY=0 NormalZ=1 AngleXU=0 Radius=11.1 StartAngle=5.93412 EndAngle=9.07571
    g2: LineSegment StartX=-62.7128 StartY=26.4558 StartZ=0 EndX=-4.56941 EndY=186.204 EndZ=0
    g3: LineSegment StartX=-25.4306 StartY=193.796 StartZ=0 EndX=-83.574 EndY=34.0487 EndZ=0
  constraints (8):
    c: Tangent(g0,g2) = -1.5708
    c: Tangent(g2,g1) = -1.5708
    c: Tangent(g1,g3) = -1.5708
    c: Tangent(g3,g0) = -1.5708
    c: Equal(g0,g1)
    c: Coincident(g0,g-3)
    c: Coincident(g1,g-4)
    c: Diameter(g0) = 22.2
FEATURE [PartDesign::Pocket] Pocket025  label="Pocket-bearing_slot"
  BaseFeature = -> Pocket024
  Direction = (9e-16,1,0)
  Length = 7.5
  Length2 = 5
  Placement = pos=(0,0,0) rot=(0.57735,0.57735,0.57735;2.0944rad)
  Profile = -> Sketch055
  ReferenceAxis = -> Sketch055 [N_Axis]
  Type = 0
FEATURE [Sketcher::SketchObject] Sketch056
  ExternalGeometry = -> [Pocket025]
  FullyConstrained = false
  MapMode = 5
  Placement = pos=(0,-3e-16,0) rot=(0.57735,0.57735,-0.57735;2.0944rad)
  Support = -> [Pocket025]
  sketch-geometry (7):
    g0: LineSegment StartX=-42.35 StartY=4 StartZ=0 EndX=-22.35 EndY=4 EndZ=0
    g1: LineSegment StartX=-22.35 StartY=4 StartZ=0 EndX=-22.35 EndY=15.3962 EndZ=0
    g2: LineSegment StartX=-22.35 StartY=15.3962 StartZ=0 EndX=-42.35 EndY=4 EndZ=0
    g3: LineSegment StartX=-42.35 StartY=8.6038 StartZ=0 EndX=-42.35 EndY=20 EndZ=0
    g4: LineSegment StartX=-42.35 StartY=20 StartZ=0 EndX=-22.35 EndY=20 EndZ=0
    g5: LineSegment StartX=-22.35 StartY=20 StartZ=0 EndX=-42.35 EndY=8.6038 EndZ=0
    g6: LineSegment StartX=-38.346 StartY=6.28152 StartZ=0 EndX=-40.3263 EndY=9.75691 EndZ=0
  constraints (21):
    c: Horizontal(g0)
    c: Coincident(g1,g0)
    c: Vertical(g1)
    c: Coincident(g2,g1)
    c: Coincident(g2,g0)
    c: Vertical(g3)
    c: Coincident(g4,g3)
    c: Horizontal(g4)
    c: Coincident(g5,g4)
    c: Coincident(g5,g3)
    c: Parallel(g2,g5)
    c: DistanceY(g3,g-5) = 0
    c: DistanceY(g-3,g0) = 4
    c: PointOnObject(g6,g2)
    c: PointOnObject(g6,g5)
    c: Angle(g2,g6) = 1.5708
    c: Distance(g6) = 4
    c: DistanceX(g-5,g3) = 4
    c: DistanceX(g0,g0) = 20
    c: Vertical(g4,g1)
    c: Vertical(g3,g0)
FEATURE [PartDesign::Pocket] Pocket026  label="Pocket-truss"
  BaseFeature = -> Pocket025
  Direction = (9e-16,1,1e-16)
  Length = 5
  Length2 = 5
  Placement = pos=(0,0,0) rot=(0.57735,0.57735,0.57735;2.0944rad)
  Profile = -> Sketch056
  ReferenceAxis = -> Sketch056 [N_Axis]
  Type = 1
FEATURE [Sketcher::SketchObject] Sketch057
  ExternalGeometry = -> [Pocket026]
  FullyConstrained = true
  MapMode = 5
  Placement = pos=(2.7e-15,0,0) rot=(0.57735,0.57735,-0.57735;4.18879rad)
  Support = -> [Pocket026]
  sketch-geometry (5):
    g0: LineSegment StartX=4 StartY=-22.35 StartZ=0 EndX=16 EndY=-22.35 EndZ=0
    g1: LineSegment StartX=16 StartY=-22.35 StartZ=0 EndX=16 EndY=-30 EndZ=0
    g2: LineSegment StartX=16 StartY=-30 StartZ=0 EndX=7.35244 EndY=-42.35 EndZ=0
    g3: LineSegment StartX=7.35244 StartY=-42.35 StartZ=0 EndX=4 EndY=-42.35 EndZ=0
    g4: LineSegment StartX=4 StartY=-42.35 StartZ=0 EndX=4 EndY=-22.35 EndZ=0
  constraints (15):
    c: Horizontal(g0)
    c: Coincident(g1,g0)
    c: PointOnObject(g1,g-7)
    c: Vertical(g1)
    c: Coincident(g2,g1)
    c: Coincident(g3,g2)
    c: Horizontal(g3)
    c: Coincident(g4,g3)
    c: Coincident(g4,g0)
    c: Vertical(g4)
    c: DistanceX(g-7,g0) = 4
    c: DistanceX(g1,g-7) = 4
    c: DistanceY(g-3,g3) = 4
    c: DistanceY(g4,g4) = 20
    c: Parallel(g2,g-4)
FEATURE [PartDesign::Pocket] Pocket027  label="Pocket-truss2"
  BaseFeature = -> Pocket026
  Direction = (1,-1e-16,8e-16)
  Length = 20
  Length2 = 5
  Placement = pos=(0,0,0) rot=(0.57735,0.57735,0.57735;2.0944rad)
  Profile = -> Sketch057
  ReferenceAxis = -> Sketch057 [N_Axis]
  Type = 0
FEATURE [Sketcher::SketchObject] Sketch058
  ExternalGeometry = -> [Pocket027]
  FullyConstrained = true
  MapMode = 5
  Placement = pos=(200,-4.4e-14,4.4e-14) rot=(0.57735,0.57735,0.57735;2.0944rad)
  Support = -> [Pocket027]
  sketch-geometry (4):
    g0: LineSegment StartX=-4.26e-14 StartY=8 StartZ=0 EndX=20 EndY=8 EndZ=0
    g1: LineSegment StartX=20 StartY=8 StartZ=0 EndX=20 EndY=1.07e-14 EndZ=0
    g2: LineSegment StartX=20 StartY=1.07e-14 StartZ=0 EndX=-4.26e-14 EndY=1.07e-14 EndZ=0
    g3: LineSegment StartX=-4.26e-14 StartY=1.07e-14 StartZ=0 EndX=-4.26e-14 EndY=8 EndZ=0
  constraints (10):
    c: Coincident(g0,g1)
    c: Coincident(g1,g2)
    c: Coincident(g2,g3)
    c: Coincident(g3,g0)
    c: Horizontal(g0)
    c: Horizontal(g2)
    c: Vertical(g1)
    c: Vertical(g3)
    c: Coincident(g0,g-5)
    c: Coincident(g1,g-4)
FEATURE [PartDesign::Pad] Pad022  label="Pad-mount_extender"
  BaseFeature = -> Pocket027
  Direction = (1,-1e-16,8e-16)
  Length = 14
  Length2 = 10
  Placement = pos=(0,0,0) rot=(0.57735,0.57735,0.57735;2.0944rad)
  Profile = -> Sketch058
  ReferenceAxis = -> Sketch058 [N_Axis]
  Type = 0
FEATURE [Sketcher::SketchObject] Sketch059
  ExternalGeometry = -> [Pad022]
  FullyConstrained = true
  MapMode = 5
  Placement = pos=(-6.6e-15,-9e-16,8) rot=(0,0,-1;1.5708rad)
  Support = -> [Pad022]
  sketch-geometry (1):
    g0: Circle CenterX=-10 CenterY=207 CenterZ=0 NormalX=0 NormalY=0 NormalZ=1 AngleXU=0 Radius=6
  constraints (3):
    c: Diameter(g0) = 12
    c: DistanceX(g-3,g0) = 10
    c: DistanceY(g0,g-3) = 7
FEATURE [PartDesign::Pocket] Pocket028  label="Pocket-mount_extender_inset"
  BaseFeature = -> Pad022
  Direction = (8e-16,1e-16,-1)
  Length = 4.5
  Length2 = 5
  Placement = pos=(0,0,0) rot=(0.57735,0.57735,0.57735;2.0944rad)
  Profile = -> Sketch059
  ReferenceAxis = -> Sketch059 [N_Axis]
  Type = 0
FEATURE [Sketcher::SketchObject] Sketch060
  ExternalGeometry = -> [Pocket028]
  FullyConstrained = true
  MapMode = 5
  Placement = pos=(-6.6e-15,-9e-16,8) rot=(0,0,-1;1.5708rad)
  Support = -> [Pocket028]
  sketch-geometry (1):
    g0: Circle CenterX=-10 CenterY=207 CenterZ=0 NormalX=0 NormalY=0 NormalZ=1 AngleXU=0 Radius=3.1
  constraints (2):
    c: Coincident(g0,g-3)
    c: Diameter(g0) = 6.2
FEATURE [PartDesign::Pocket] Pocket029  label="Pocket-mount_extender_mount_hole"
  BaseFeature = -> Pocket028
  Direction = (8e-16,1e-16,-1)
  Length = 5
  Length2 = 5
  Placement = pos=(0,0,0) rot=(0.57735,0.57735,0.57735;2.0944rad)
  Profile = -> Sketch060
  ReferenceAxis = -> Sketch060 [N_Axis]
  Type = 1
FEATURE [App::FeaturePython] Constraints011  # WARN: FeaturePython — macro-defined, semantics opaque (R4)
  _Version = 1
FEATURE [Sketcher::SketchObject] Sketch061
  FullyConstrained = true
  MapMode = 5
  Support = -> [XY_Plane014]
  sketch-geometry (2):
    g0: Circle CenterX=0 CenterY=0 CenterZ=0 NormalX=0 NormalY=0 NormalZ=1 AngleXU=0 Radius=3.95
    g1: Circle CenterX=0 CenterY=0 CenterZ=0 NormalX=0 NormalY=0 NormalZ=1 AngleXU=0 Radius=11
  constraints (4):
    c: Coincident(g0,g-1)
    c: Coincident(g1,g0)
    c: Diameter(g0) = 7.9
    c: Diameter(g1) = 22
FEATURE [PartDesign::Pad] Pad023
  Direction = (0,0,1)
  Length = 7
  Length2 = 10
  Profile = -> Sketch061
  ReferenceAxis = -> Sketch061 [N_Axis]
  Type = 0
FEATURE [PartDesign::Body] Body015  label="Body-bearing"
  Group = -> [Sketch061,Pad023]
  Origin = -> Origin014
  Tip = -> Pad023
FEATURE [Part::FeaturePython] Parts011  # WARN: FeaturePython — macro-defined, semantics opaque (R4)
  Group = -> [Body015]
  GroupMode = 0
FEATURE [Sketcher::SketchObject] Sketch062
  ExternalGeometry = -> [Fillet001]
  FullyConstrained = true
  MapMode = 5
  Placement = pos=(-21,0,0) rot=(0.57735,-0.57735,-0.57735;2.0944rad)
  Support = -> [Fillet001]
  sketch-geometry (2):
    g0: Circle CenterX=90 CenterY=2.5 CenterZ=0 NormalX=0 NormalY=0 NormalZ=1 AngleXU=0 Radius=3.95
    g1: Circle CenterX=90 CenterY=2.5 CenterZ=0 NormalX=0 NormalY=0 NormalZ=1 AngleXU=0 Radius=10
  constraints (4):
    c: Coincident(g0,g-3)
    c: Coincident(g1,g0)
    c: Diameter(g1) = 20
    c: Diameter(g0) = 7.9
FEATURE [PartDesign::Pocket] Pocket030  label="Pocket-bearing_shaft"
  BaseFeature = -> Fillet001
  Direction = (1,0,0)
  Length = 15
  Length2 = 5
  Profile = -> Sketch062
  ReferenceAxis = -> Sketch062 [N_Axis]
  Type = 0
FEATURE [Sketcher::SketchObject] Sketch063
  ExternalGeometry = -> [Pocket030]
  FullyConstrained = true
  MapMode = 5
  Placement = pos=(0,0,5) rot=(0,0,1;0rad)
  Support = -> [Pocket030]
  sketch-geometry (1):
    g0: Circle CenterX=-13.5 CenterY=-90 CenterZ=0 NormalX=0 NormalY=0 NormalZ=1 AngleXU=0 Radius=0.5
  constraints (3):
    c: Diameter(g0) = 1
    c: DistanceX(g0,g-3) = 13.5
    c: DistanceY(g-4,g0) = 4.5
FEATURE [PartDesign::Pocket] Pocket031
  BaseFeature = -> Pocket030
  Direction = (0,0,-1)
  Length = 10
  Length2 = 10
  Profile = -> Sketch063
  ReferenceAxis = -> Sketch063 [N_Axis]
  Type = 4
FEATURE [PartDesign::Chamfer] Chamfer
  Angle = 45
  Base = -> Fillet [Edge16,Edge17,Edge19,Edge23,Edge21]
  BaseFeature = -> Fillet
  ChamferType = 0
  FlipDirection = false
  Size = 3
  Size2 = 1
  SupportTransform = false
  UseAllEdges = false
FEATURE [PartDesign::Chamfer] Chamfer001
  Angle = 45
  Base = -> Pocket031 [Edge16,Edge17,Edge19]
  BaseFeature = -> Pocket031
  ChamferType = 0
  FlipDirection = false
  Size = 3
  Size2 = 1
  SupportTransform = false
  UseAllEdges = false
FEATURE [Sketcher::SketchObject] Sketch064
  ExternalGeometry = -> [Pocket029]
  FullyConstrained = true
  MapMode = 5
  Placement = pos=(1.78e-14,20,-2.2e-15) rot=(0.57735,0.57735,0.57735;4.18879rad)
  Support = -> [Pocket029]
  sketch-geometry (5):
    g0: LineSegment StartX=27.427 StartY=112 StartZ=0 EndX=8 EndY=112 EndZ=0
    g1: LineSegment StartX=8 StartY=102 StartZ=0 EndX=31.0667 EndY=102 EndZ=0
    g2: LineSegment StartX=31.0667 StartY=102 StartZ=0 EndX=27.427 EndY=112 EndZ=0
    g3: LineSegment StartX=8 StartY=112 StartZ=0 EndX=8 EndY=102 EndZ=0
    g4: GeomPoint X=8 Y=107 Z=0
  constraints (13):
    c: PointOnObject(g0,g-3)
    c: PointOnObject(g0,g-4)
    c: Horizontal(g0)
    c: PointOnObject(g1,g-4)
    c: PointOnObject(g1,g-3)
    c: Horizontal(g1)
    c: Coincident(g2,g1)
    c: Coincident(g2,g0)
    c: Coincident(g3,g0)
    c: Coincident(g3,g1)
    c: DistanceY(g3,g3) = 10
    c: Symmetric(g3,g3,g4)
    c: DistanceY(g-1,g4) = 107
FEATURE [PartDesign::Pad] Pad024  label="Pad-mid-support"
  BaseFeature = -> Pocket029
  Direction = (9e-16,1,0)
  Length = 12
  Length2 = 10
  Placement = pos=(0,0,0) rot=(0.57735,0.57735,0.57735;2.0944rad)
  Profile = -> Sketch064
  ReferenceAxis = -> Sketch064 [N_Axis]
  Reversed = true
  Type = 0
FEATURE [PartDesign::Chamfer] Chamfer002
  Angle = 45
  Base = -> Pad024 [Edge171]
  BaseFeature = -> Pad024
  ChamferType = 0
  FlipDirection = false
  Placement = pos=(0,0,0) rot=(0.57735,0.57735,0.57735;2.0944rad)
  Size = 7.9
  Size2 = 1
  SupportTransform = false
  UseAllEdges = false
FEATURE [PartDesign::Fillet] Fillet002
  Base = -> Chamfer002 [Edge28,Edge123,Edge129,Edge30,Edge131,Edge225,Edge133]
  BaseFeature = -> Chamfer002
  Placement = pos=(0,0,0) rot=(0.57735,0.57735,0.57735;2.0944rad)
  Radius = 3
  SupportTransform = false
  UseAllEdges = false
FEATURE [PartDesign::Fillet] Fillet003
  Base = -> Fillet002 [Edge36,Edge164]
  BaseFeature = -> Fillet002
  Placement = pos=(0,0,0) rot=(0.57735,0.57735,0.57735;2.0944rad)
  Radius = 10
  SupportTransform = false
  UseAllEdges = false
FEATURE [PartDesign::Fillet] Fillet004
  Base = -> Fillet003 [Edge301,Edge248]
  BaseFeature = -> Fillet003
  Placement = pos=(0,0,0) rot=(0.57735,0.57735,0.57735;2.0944rad)
  Radius = 9
  SupportTransform = false
  UseAllEdges = false
FEATURE [PartDesign::Fillet] Fillet005
  Base = -> Fillet004 [Face55,Face56,Face57,Face58]
  BaseFeature = -> Fillet004
  Placement = pos=(0,0,0) rot=(0.57735,0.57735,0.57735;2.0944rad)
  Radius = 1
  SupportTransform = false
  UseAllEdges = false
FEATURE [Sketcher::SketchObject] Sketch065
  ExternalGeometry = -> [Fillet005]
  FullyConstrained = true
  MapMode = 5
  Placement = pos=(-2.2e-15,-10,6e-16) rot=(-0.57735,-0.57735,0.57735;4.18879rad)
  Support = -> [Fillet005]
  sketch-geometry (4):
    g0: LineSegment StartX=-52.5 StartY=0 StartZ=0 EndX=2.5 EndY=0 EndZ=0
    g1: LineSegment StartX=2.5 StartY=0 StartZ=0 EndX=2.5 EndY=20 EndZ=0
    g2: LineSegment StartX=2.5 StartY=20 StartZ=0 EndX=-52.5 EndY=20 EndZ=0
    g3: LineSegment StartX=-52.5 StartY=20 StartZ=0 EndX=-52.5 EndY=0 EndZ=0
  constraints (10):
    c: Coincident(g0,g1)
    c: Coincident(g1,g2)
    c: Coincident(g2,g3)
    c: Coincident(g3,g0)
    c: Horizontal(g0)
    c: Horizontal(g2)
    c: Vertical(g1)
    c: Vertical(g3)
    c: Coincident(g0,g-3)
    c: Coincident(g1,g-4)
FEATURE [PartDesign::Pocket] Pocket032  label="Pocket-v3-thin_servo_mount_for_bushing"
  BaseFeature = -> Fillet005
  Direction = (4e-16,1,-1e-16)
  Length = 1
  Length2 = 5
  Placement = pos=(0,0,0) rot=(0.57735,0.57735,0.57735;2.0944rad)
  Profile = -> Sketch065
  ReferenceAxis = -> Sketch065 [N_Axis]
  Type = 0
FEATURE [Sketcher::SketchObject] Sketch066
  ExternalGeometry = -> [Pocket032]
  FullyConstrained = true
  MapMode = 5
  Placement = pos=(0,-3e-16,0) rot=(0.57735,0.57735,-0.57735;2.0944rad)
  Support = -> [Pocket032]
  sketch-geometry (1):
    g0: Circle CenterX=-15 CenterY=10 CenterZ=0 NormalX=0 NormalY=0 NormalZ=1 AngleXU=0 Radius=6.5
  constraints (2):
    c: Coincident(g0,g-3)
    c: Diameter(g0) = 13
FEATURE [PartDesign::Pocket] Pocket033  label="Pocket-13mm_shaft_cutout"
  BaseFeature = -> Pocket032
  Direction = (4e-16,1,1e-16)
  Length = 5
  Length2 = 5
  Placement = pos=(0,0,0) rot=(0.57735,0.57735,0.57735;2.0944rad)
  Profile = -> Sketch066
  ReferenceAxis = -> Sketch066 [N_Axis]
  Type = 1
FEATURE [Sketcher::SketchObject] Sketch067
  ExternalGeometry = -> [Chamfer]
  FullyConstrained = false
  MapMode = 5
  Placement = pos=(-21,0,0) rot=(0.57735,-0.57735,-0.57735;2.0944rad)
  Support = -> [Chamfer]
  sketch-geometry (1):
    g0: Circle CenterX=-140 CenterY=2.5 CenterZ=0 NormalX=0 NormalY=0 NormalZ=1 AngleXU=0 Radius=6
  constraints (1):
    c: Diameter(g0) = 12
FEATURE [PartDesign::Pad] Pad025  label="Pad-thicker_shaft"
  BaseFeature = -> Chamfer
  Direction = (-1,0,0)
  Length = 1
  Length2 = 198
  Profile = -> Sketch067
  ReferenceAxis = -> Sketch067 [N_Axis]
  Type = 4
FEATURE [Sketcher::SketchObject] Sketch068
  ExternalGeometry = -> [Pocket004]
  FullyConstrained = true
  MapMode = 5
  Placement = pos=(-21,0,0) rot=(0.57735,-0.57735,-0.57735;2.0944rad)
  Support = -> [Pocket004]
  sketch-geometry (5):
    g0: LineSegment StartX=-140 StartY=2.5 StartZ=0 EndX=-140 EndY=5.6 EndZ=0
    g1: LineSegment StartX=-140 StartY=5.6 StartZ=0 EndX=-139.662 EndY=5.17871 EndZ=0
    g2: LineSegment StartX=-139.662 StartY=5.17871 StartZ=0 EndX=-139.229 EndY=5.50261 EndZ=0
    g3: LineSegment StartX=-139.229 StartY=5.50261 StartZ=0 EndX=-140 EndY=2.5 EndZ=0
    g4: LineSegment StartX=-140 StartY=2.5 StartZ=0 EndX=-139.662 EndY=5.17871 EndZ=0
  constraints (13):
    c: Coincident(g0,g-3)
    c: Coincident(g1,g0)
    c: Coincident(g2,g1)
    c: Coincident(g3,g2)
    c: Coincident(g3,g0)
    c: Distance(g0) = 3.1
    c: Distance(g3) = 3.1
    c: Coincident(g4,g0)
    c: Coincident(g4,g1)
    c: Angle(g4,g0) = 0.125664
    c: Angle(g3,g0) = 0.251327
    c: Distance(g4) = 2.7
    c: Vertical(g0)
FEATURE [PartDesign::Pocket] Pocket034  label="Pocket-spline2"
  BaseFeature = -> Pad025
  Direction = (1,0,0)
  Length = 4
  Length2 = 5
  Profile = -> Sketch068
  ReferenceAxis = -> Sketch068 [N_Axis]
  Type = 4
FEATURE [PartDesign::PolarPattern] PolarPattern001
  Angle = 360
  Axis = -> Pocket034 [Edge157]
  BaseFeature = -> Pocket034
  Occurrences = 25
  Originals = -> [Pocket034]
FEATURE [Sketcher::SketchObject] Sketch069
  ExternalGeometry = -> [Chamfer001]
  FullyConstrained = true
  MapMode = 5
  Placement = pos=(-21,0,0) rot=(0.57735,-0.57735,-0.57735;2.0944rad)
  Support = -> [Chamfer001]
  sketch-geometry (1):
    g0: Circle CenterX=90 CenterY=2.5 CenterZ=0 NormalX=0 NormalY=0 NormalZ=1 AngleXU=0 Radius=6
  constraints (2):
    c: Coincident(g0,g-3)
    c: Diameter(g0) = 12
FEATURE [PartDesign::Pocket] Pocket035
  BaseFeature = -> Chamfer001
  Direction = (1,0,0)
  Length = 5
  Length2 = 5
  Profile = -> Sketch069
  ReferenceAxis = -> Sketch069 [N_Axis]
  Type = 0
FEATURE [Sketcher::SketchObject] Sketch070
  ExternalGeometry = -> [Pocket033]
  FullyConstrained = true
  MapMode = 5
  Placement = pos=(7.6e-15,8,-9e-16) rot=(-0.57735,-0.57735,0.57735;4.18879rad)
  Support = -> [Pocket033]
  sketch-geometry (4):
    g0: LineSegment StartX=-21.1426 StartY=102 StartZ=0 EndX=-21.1426 EndY=112 EndZ=0
    g1: LineSegment StartX=-21.1426 StartY=112 StartZ=0 EndX=-59.3523 EndY=112 EndZ=0
    g2: LineSegment StartX=-59.3523 StartY=112 StartZ=0 EndX=-62.992 EndY=102 EndZ=0
    g3: LineSegment StartX=-62.992 StartY=102 StartZ=0 EndX=-21.1426 EndY=102 EndZ=0
  constraints (12):
    c: PointOnObject(g0,g-3)
    c: PointOnObject(g0,g-5)
    c: Vertical(g0)
    c: Coincident(g1,g0)
    c: PointOnObject(g1,g-4)
    c: Horizontal(g1)
    c: Coincident(g2,g1)
    c: PointOnObject(g2,g-4)
    c: Coincident(g3,g2)
    c: Coincident(g3,g0)
    c: Horizontal(g3)
    c: DistanceX(g-5,g0) = 2
FEATURE [PartDesign::Pad] Pad026  label="Pad-mid_rail_support_main_body"
  BaseFeature = -> Pocket033
  Direction = (-1e-15,-1,-1e-16)
  Length = 10
  Length2 = 10
  Placement = pos=(0,0,0) rot=(0.57735,0.57735,0.57735;2.0944rad)
  Profile = -> Sketch070
  ReferenceAxis = -> Sketch070 [N_Axis]
  Type = 0
FEATURE [Sketcher::SketchObject] Sketch071
  ExternalGeometry = -> [Pad026]
  FullyConstrained = true
  MapMode = 5
  Placement = pos=(9e-15,8,8e-16) rot=(0.57735,0.57735,0.57735;4.18879rad)
  Support = -> [Pad026]
  sketch-geometry (4):
    g0: LineSegment StartX=55.2021 StartY=112 StartZ=0 EndX=58.8418 EndY=102 EndZ=0
    g1: LineSegment StartX=58.8418 StartY=102 StartZ=0 EndX=35.217 EndY=102 EndZ=0
    g2: LineSegment StartX=35.217 StartY=102 StartZ=0 EndX=31.5773 EndY=112 EndZ=0
    g3: LineSegment StartX=31.5773 StartY=112 StartZ=0 EndX=55.2021 EndY=112 EndZ=0
  constraints (8):
    c: Coincident(g0,g-3)
    c: Coincident(g0,g-4)
    c: Coincident(g1,g0)
    c: Coincident(g1,g-4)
    c: Coincident(g2,g1)
    c: Coincident(g2,g-3)
    c: Coincident(g3,g2)
    c: Coincident(g3,g0)
FEATURE [PartDesign::Pocket] Pocket036  label="Pocket-mid_rail_support_inside"
  BaseFeature = -> Pad026
  Direction = (-1.3e-15,-1,-1e-16)
  Length = 6.5
  Length2 = 5
  Placement = pos=(0,0,0) rot=(0.57735,0.57735,0.57735;2.0944rad)
  Profile = -> Sketch071
  ReferenceAxis = -> Sketch071 [N_Axis]
  Type = 0
FEATURE [PartDesign::Chamfer] Chamfer003  label="Chamfer-midrail_support-vertical"
  Angle = 45
  Base = -> Pocket036 [Edge320]
  BaseFeature = -> Pocket036
  ChamferType = 0
  FlipDirection = false
  Placement = pos=(0,0,0) rot=(0.57735,0.57735,0.57735;2.0944rad)
  Size = 9.8
  Size2 = 1
  SupportTransform = false
  UseAllEdges = false
FEATURE [PartDesign::Fillet] Fillet006  label="Fillet-midrail_support-vertical"
  Base = -> Chamfer003 [Edge22,Edge41,Edge44]
  BaseFeature = -> Chamfer003
  Placement = pos=(0,0,0) rot=(0.57735,0.57735,0.57735;2.0944rad)
  Radius = 5
  SupportTransform = false
  UseAllEdges = false
FEATURE [PartDesign::Fillet] Fillet007  label="Fillet-midrail_support-lateral"
  Base = -> Fillet006 [Edge55,Edge58,Edge6,Edge11]
  BaseFeature = -> Fillet006
  Placement = pos=(0,0,0) rot=(0.57735,0.57735,0.57735;2.0944rad)
  Radius = 1
  SupportTransform = false
  UseAllEdges = false
FEATURE [Sketcher::SketchObject] Sketch072
  FullyConstrained = true
  MapMode = 5
  Placement = pos=(0,0,0) rot=(1,0,0;1.5708rad)
  Support = -> [XZ_Plane015]
  sketch-geometry (16):
    g0: LineSegment StartX=-3.8476e-12 StartY=-10.8333 StartZ=0 EndX=4 EndY=-10.8333 EndZ=0
    g1: LineSegment StartX=4 StartY=-10.8333 StartZ=0 EndX=4 EndY=-0.833334 EndZ=0
    g2: LineSegment StartX=4 StartY=-0.833334 StartZ=0 EndX=-15 EndY=-0.833334 EndZ=0
    g3: LineSegment StartX=-15 StartY=-0.833334 StartZ=0 EndX=-15 EndY=0.833334 EndZ=0
    g4: LineSegment StartX=-15 StartY=0.833334 StartZ=0 EndX=4 EndY=0.833334 EndZ=0
    g5: LineSegment StartX=4 StartY=0.833334 StartZ=0 EndX=4 EndY=10.8333 EndZ=0
    g6: LineSegment StartX=4 StartY=10.8333 StartZ=0 EndX=0 EndY=10.8333 EndZ=0
    g7: LineSegment StartX=0 StartY=10.8333 StartZ=0 EndX=0 EndY=0.853333 EndZ=0
    g8: LineSegment StartX=0 StartY=0.853333 StartZ=0 EndX=-19 EndY=0.853333 EndZ=0
    g9: LineSegment StartX=-19 StartY=0.853333 StartZ=0 EndX=-19 EndY=-0.853333 EndZ=0
    g10: LineSegment StartX=-19 StartY=-0.853333 StartZ=0 EndX=-3.8476e-12 EndY=-0.853333 EndZ=0
    g11: LineSegment StartX=-3.8476e-12 StartY=-0.853333 StartZ=0 EndX=-3.8476e-12 EndY=-10.8333 EndZ=0
    g12: LineSegment StartX=-19 StartY=0.853333 StartZ=0 EndX=-15 EndY=-0.833334 EndZ=0
    g13: LineSegment StartX=-15 StartY=0.833334 StartZ=0 EndX=-19 EndY=-0.853333 EndZ=0
    g14: LineSegment StartX=0 StartY=0.853333 StartZ=0 EndX=0 EndY=0 EndZ=0
    g15: LineSegment StartX=0 StartY=0 StartZ=0 EndX=-3.8476e-12 EndY=-0.853333 EndZ=0
  constraints (44):
    c: Horizontal(g0)
    c: Coincident(g1,g0)
    c: Vertical(g1)
    c: Coincident(g2,g1)
    c: Horizontal(g2)
    c: Coincident(g3,g2)
    c: Vertical(g3)
    c: Horizontal(g4)
    c: Coincident(g5,g4)
    c: Vertical(g5)
    c: Coincident(g6,g5)
    c: PointOnObject(g6,g-2)
    c: Horizontal(g6)
    c: Coincident(g7,g6)
    c: Vertical(g7)
    c: Coincident(g8,g7)
    c: Horizontal(g8)
    c: Coincident(g9,g8)
    c: Vertical(g9)
    c: Coincident(g10,g9)
    c: Horizontal(g10)
    c: Coincident(g11,g10)
    c: Vertical(g11)
    c: DistanceY(g3,g3) = 1.66667
    c: Coincident(g3,g4)
    c: DistanceY(g9,g9) = 1.70667
    c: Coincident(g12,g8)
    c: Coincident(g12,g2)
    c: Coincident(g13,g3)
    c: Coincident(g13,g9)
    c: Equal(g13,g12)
    c: DistanceX(g9,g2) = 4
    c: DistanceX(g0,g0) = 4
    c: Equal(g0,g6)
    c: Equal(g1,g5)
    c: DistanceY(g1,g1) = 10
    c: DistanceX(g2,g10) = 15
    c: Coincident(g11,g0)
    c: Vertical(g1,g4)
    c: Coincident(g14,g7)
    c: Coincident(g14,g-1)
    c: Coincident(g15,g14)
    c: Coincident(g15,g10)
    c: Equal(g15,g14)
FEATURE [PartDesign::Pad] Pad027  label="Pad-main_body"
  Direction = (0,-1,-2e-16)
  Length = 150
  Length2 = 10
  Placement = pos=(0,0,0) rot=(1,0,0;1.5708rad)
  Profile = -> Sketch072
  ReferenceAxis = -> Sketch072 [N_Axis]
  Type = 0
FEATURE [Sketcher::SketchObject] Sketch073
  ExternalGeometry = -> [Pad027]
  FullyConstrained = true
  MapMode = 5
  Placement = pos=(0,2e-16,0.853333) rot=(0,0,1;3.14159rad)
  Support = -> [Pad027]
  sketch-geometry (14):
    g0: ArcOfCircle CenterX=5.5 CenterY=50 CenterZ=0 NormalX=0 NormalY=0 NormalZ=1 AngleXU=0 Radius=1.7 StartAngle=1.5708 EndAngle=4.71239
    g1: ArcOfCircle CenterX=11.5 CenterY=50 CenterZ=0 NormalX=0 NormalY=0 NormalZ=1 AngleXU=0 Radius=1.7 StartAngle=4.71239 EndAngle=7.85398
    g2: LineSegment StartX=5.5 StartY=48.3 StartZ=0 EndX=11.5 EndY=48.3 EndZ=0
    g3: LineSegment StartX=11.5 StartY=51.7 StartZ=0 EndX=5.5 EndY=51.7 EndZ=0
    g4: ArcOfCircle CenterX=5.5 CenterY=75 CenterZ=0 NormalX=0 NormalY=0 NormalZ=1 AngleXU=0 Radius=1.7 StartAngle=1.5708 EndAngle=4.71239
    g5: ArcOfCircle CenterX=11.5 CenterY=75 CenterZ=0 NormalX=0 NormalY=0 NormalZ=1 AngleXU=0 Radius=1.7 StartAngle=4.71239 EndAngle=7.85398
    g6: LineSegment StartX=5.5 StartY=73.3 StartZ=0 EndX=11.5 EndY=73.3 EndZ=0
    g7: LineSegment StartX=11.5 StartY=76.7 StartZ=0 EndX=5.5 EndY=76.7 EndZ=0
    g8: ArcOfCircle CenterX=5.5 CenterY=100 CenterZ=0 NormalX=0 NormalY=0 NormalZ=1 AngleXU=0 Radius=1.7 StartAngle=1.5708 EndAngle=4.71239
    g9: ArcOfCircle CenterX=11.5 CenterY=100 CenterZ=0 NormalX=0 NormalY=0 NormalZ=1 AngleXU=0 Radius=1.7 StartAngle=4.71239 EndAngle=7.85398
    g10: LineSegment StartX=5.5 StartY=98.3 StartZ=0 EndX=11.5 EndY=98.3 EndZ=0
    g11: LineSegment StartX=11.5 StartY=101.7 StartZ=0 EndX=5.5 EndY=101.7 EndZ=0
    g12: LineSegment StartX=11.5 StartY=100 StartZ=0 EndX=11.5 EndY=75 EndZ=0
    g13: LineSegment StartX=11.5 StartY=75 StartZ=0 EndX=11.5 EndY=50 EndZ=0
  constraints (34):
    c: Tangent(g0,g2) = -1.5708
    c: Tangent(g2,g1) = -1.5708
    c: Tangent(g1,g3) = -1.5708
    c: Tangent(g3,g0) = -1.5708
    c: Equal(g0,g1)
    c: Horizontal(g2)
    c: Diameter(g1) = 3.4
    c: DistanceX(g2,g2) = 6
    c: DistanceX(g1,g-3) = 7.5
    c: DistanceY(g-3,g1) = 50
    c: Tangent(g4,g6) = -1.5708
    c: Tangent(g6,g5) = -1.5708
    c: Tangent(g5,g7) = -1.5708
    c: Tangent(g7,g4) = -1.5708
    c: Equal(g4,g5)
    c: Tangent(g8,g10) = -1.5708
    c: Tangent(g10,g9) = -1.5708
    c: Tangent(g9,g11) = -1.5708
    c: Tangent(g11,g8) = -1.5708
    c: Equal(g8,g9)
    c: Equal(g9,g5)
    c: Equal(g5,g1)
    c: Horizontal(g5,g4)
    c: Horizontal(g9,g8)
    c: Vertical(g8,g4)
    c: Vertical(g4,g0)
    c: Coincident(g12,g9)
    c: Coincident(g12,g5)
    c: Vertical(g12)
    c: Coincident(g13,g5)
    c: Coincident(g13,g1)
    c: Vertical(g13)
    c: Equal(g12,g13)
    c: DistanceY(g12,g12) = 25
FEATURE [PartDesign::Pad] Pad028  label="Pad-slots"
  BaseFeature = -> Pad027
  Direction = (0,-2e-16,1)
  Length = 10
  Length2 = 10
  Placement = pos=(0,0,0) rot=(1,0,0;1.5708rad)
  Profile = -> Sketch073
  ReferenceAxis = -> Sketch073 [N_Axis]
  Type = 0
FEATURE [PartDesign::Mirrored] Mirrored  label="Mirrored-slots_top_to_bottom"
  BaseFeature = -> Pad028
  MirrorPlane = -> XY_Plane015
  Originals = -> [Pad028]
  Placement = pos=(0,0,0) rot=(1,0,0;1.5708rad)
FEATURE [Sketcher::SketchObject] Sketch074
  ExternalGeometry = -> [Mirrored]
  FullyConstrained = true
  MapMode = 5
  Placement = pos=(0,-2e-16,-0.833334) rot=(0,0,1;3.14159rad)
  Support = -> [Mirrored]
  sketch-geometry (5):
    g0: Circle CenterX=7.5 CenterY=50 CenterZ=0 NormalX=0 NormalY=0 NormalZ=1 AngleXU=0 Radius=1.69
    g1: Circle CenterX=7.5 CenterY=75 CenterZ=0 NormalX=0 NormalY=0 NormalZ=1 AngleXU=0 Radius=1.69
    g2: Circle CenterX=7.5 CenterY=100 CenterZ=0 NormalX=0 NormalY=0 NormalZ=1 AngleXU=0 Radius=1.69
    g3: LineSegment StartX=7.5 StartY=100 StartZ=0 EndX=7.5 EndY=75 EndZ=0
    g4: LineSegment StartX=7.5 StartY=75 StartZ=0 EndX=7.5 EndY=50 EndZ=0
  constraints (13):
    c: Equal(g2,g1)
    c: Equal(g2,g0)
    c: Diameter(g2) = 3.38
    c: Coincident(g3,g2)
    c: Coincident(g3,g1)
    c: Vertical(g3)
    c: Coincident(g4,g1)
    c: Coincident(g4,g0)
    c: Vertical(g4)
    c: DistanceY(g3,g3) = 25
    c: DistanceY(g-1,g0) = 50
    c: DistanceX(g0,g-3) = 7.5
    c: Equal(g3,g4)
FEATURE [PartDesign::Pad] Pad029  label="Pad-inside_holes"
  BaseFeature = -> Mirrored
  Direction = (0,-2e-16,1)
  Length = 10
  Length2 = 10
  Placement = pos=(0,0,0) rot=(1,0,0;1.5708rad)
  Profile = -> Sketch074
  ReferenceAxis = -> Sketch074 [N_Axis]
  Type = 0
FEATURE [Sketcher::SketchObject] Sketch075
  ExternalGeometry = -> [PolarPattern001]
  FullyConstrained = true
  MapMode = 5
  Placement = pos=(177,0,0) rot=(0.57735,0.57735,0.57735;2.0944rad)
  Support = -> [PolarPattern001]
  sketch-geometry (2):
    g0: Circle CenterX=140 CenterY=2.5 CenterZ=0 NormalX=0 NormalY=0 NormalZ=1 AngleXU=0 Radius=3.95
    g1: Circle CenterX=140 CenterY=2.5 CenterZ=0 NormalX=0 NormalY=0 NormalZ=1 AngleXU=0 Radius=7.565
  constraints (4):
    c: Coincident(g0,g-3)
    c: Coincident(g1,g0)
    c: Diameter(g0) = 7.9
    c: Diameter(g1) = 15.13
FEATURE [PartDesign::Pocket] Pocket037  label="Pocket-neck_down_bearing"
  BaseFeature = -> PolarPattern001
  Direction = (-1,0,0)
  Length = 10
  Length2 = 5
  Profile = -> Sketch075
  ReferenceAxis = -> Sketch075 [N_Axis]
  Type = 0
FEATURE [Sketcher::SketchObject] Sketch076
  ExternalGeometry = -> [Pocket037]
  FullyConstrained = true
  MapMode = 5
  Placement = pos=(177,0,0) rot=(0.57735,0.57735,0.57735;2.0944rad)
  Support = -> [Pocket037]
  sketch-geometry (1):
    g0: Circle CenterX=140 CenterY=2.5 CenterZ=0 NormalX=0 NormalY=0 NormalZ=1 AngleXU=0 Radius=7.5
  constraints (2):
    c: Coincident(g0,g-3)
    c: Diameter(g0) = 15
FEATURE [PartDesign::Pocket] Pocket038  label="Pocket-shorten_down_bearing_shaft"
  BaseFeature = -> Pocket037
  Direction = (-1,0,0)
  Length = 2
  Length2 = 5
  Profile = -> Sketch076
  ReferenceAxis = -> Sketch076 [N_Axis]
  Type = 0
FEATURE [PartDesign::Fillet] Fillet008
  Base = -> Pad029 [Edge5,Edge53,Edge47,Edge8]
  BaseFeature = -> Pad029
  Placement = pos=(0,0,0) rot=(1,0,0;1.5708rad)
  Radius = 1
  SupportTransform = false
  UseAllEdges = false
FEATURE [PartDesign::Fillet] Fillet009
  Base = -> Fillet008 [Edge43,Edge39,Edge62,Edge48]
  BaseFeature = -> Fillet008
  Placement = pos=(0,0,0) rot=(1,0,0;1.5708rad)
  Radius = 0.8
  SupportTransform = false
  UseAllEdges = false
FEATURE [PartDesign::Chamfer] Chamfer004
  Angle = 45
  Base = -> Fillet009 [Face25,Face24,Face23]
  BaseFeature = -> Fillet009
  ChamferType = 0
  FlipDirection = false
  Placement = pos=(0,0,0) rot=(1,0,0;1.5708rad)
  Size = 0.5
  Size2 = 1
  SupportTransform = false
  UseAllEdges = false
FEATURE [PartDesign::Chamfer] Chamfer005
  Angle = 45
  Base = -> Chamfer004 [Face53,Face54,Face55,Face52,Face50,Face46,Face45,Face47,Face51,Face49,Face48,Face44]
  BaseFeature = -> Chamfer004
  ChamferType = 0
  FlipDirection = false
  Placement = pos=(0,0,0) rot=(1,0,0;1.5708rad)
  Size = 0.5
  Size2 = 1
  SupportTransform = false
  UseAllEdges = false
FEATURE [PartDesign::Chamfer] Chamfer006
  Angle = 45
  Base = -> Chamfer005 [Face66,Face67,Face65,Face61,Face62,Face63,Face57,Face58,Face59,Face68,Face64,Face60]
  BaseFeature = -> Chamfer005
  ChamferType = 0
  FlipDirection = false
  Placement = pos=(0,0,0) rot=(1,0,0;1.5708rad)
  Size = 0.5
  Size2 = 1
  SupportTransform = false
  UseAllEdges = false
FEATURE [PartDesign::Body] Body016  label="Body-v3_slicer"
  Group = -> [Sketch072,Pad027,Sketch073,Pad028,Mirrored,Sketch074,Pad029,Fillet008,Fillet009,Chamfer004,Chamfer005,Chamfer006]
  Origin = -> Origin015
  Placement = pos=(-275,91,161.477) rot=(0,0,1;0rad)
  Tip = -> Chamfer006
FEATURE [PartDesign::Fillet] Fillet010  label="Fillet-bearing_shaft_corner"
  Base = -> Pocket038 [Edge135]
  BaseFeature = -> Pocket038
  Radius = 0.2
  SupportTransform = false
  UseAllEdges = false
FEATURE [PartDesign::Fillet] Fillet011  label="Fillet-shaft_end"
  Base = -> Fillet010 [Edge2,Edge15]
  BaseFeature = -> Fillet010
  Radius = 0.5
  SupportTransform = false
  UseAllEdges = false
FEATURE [PartDesign::Fillet] Fillet012
  Base = -> Fillet011 [Edge12,Edge9]
  BaseFeature = -> Fillet011
  Radius = 5
  SupportTransform = false
  UseAllEdges = false
FEATURE [Sketcher::SketchObject] Sketch077
  FullyConstrained = true
  MapMode = 5
  Support = -> [XY_Plane016]
  sketch-geometry (6):
    g0: LineSegment StartX=-11 StartY=0 StartZ=0 EndX=11 EndY=0 EndZ=0
    g1: LineSegment StartX=11 StartY=0 StartZ=0 EndX=11 EndY=-214 EndZ=0
    g2: LineSegment StartX=11 StartY=-214 StartZ=0 EndX=-11 EndY=-214 EndZ=0
    g3: LineSegment StartX=-11 StartY=-214 StartZ=0 EndX=-11 EndY=0 EndZ=0
    g4: LineSegment StartX=-11 StartY=0 StartZ=0 EndX=0 EndY=0 EndZ=0
    g5: LineSegment StartX=0 StartY=0 StartZ=0 EndX=11 EndY=0 EndZ=0
  constraints (16):
    c: Coincident(g0,g1)
    c: Coincident(g1,g2)
    c: Coincident(g2,g3)
    c: Horizontal(g0)
    c: Horizontal(g2)
    c: Vertical(g1)
    c: Vertical(g3)
    c: DistanceX(g0,g0) = 22
    c: DistanceY(g3,g3) = 214
    c: Coincident(g0,g3)
    c: PointOnObject(g-1,g0)
    c: Coincident(g4,g0)
    c: Coincident(g4,g-1)
    c: Coincident(g5,g4)
    c: Coincident(g5,g0)
    c: Equal(g4,g5)
FEATURE [PartDesign::Pad] Pad030  label="Pad-base_plate"
  Direction = (0,0,1)
  Length = 8
  Length2 = 10
  Profile = -> Sketch077
  ReferenceAxis = -> Sketch077 [N_Axis]
  Type = 0
FEATURE [Sketcher::SketchObject] Sketch078
  FullyConstrained = true
  MapMode = 5
  Placement = pos=(-11,0,0) rot=(0.57735,-0.57735,-0.57735;2.0944rad)
  Support = -> [Pad030]
FEATURE [Sketcher::SketchObject] Sketch079
  ExternalGeometry = -> [Pad030]
  FullyConstrained = true
  MapMode = 5
  Placement = pos=(0,0,8) rot=(0,0,1;0rad)
  Support = -> [Pad030]
  sketch-geometry (4):
    g0: LineSegment StartX=-11 StartY=2.5 StartZ=0 EndX=11 EndY=2.5 EndZ=0
    g1: LineSegment StartX=11 StartY=2.5 StartZ=0 EndX=11 EndY=-22.5 EndZ=0
    g2: LineSegment StartX=11 StartY=-22.5 StartZ=0 EndX=-11 EndY=-22.5 EndZ=0
    g3: LineSegment StartX=-11 StartY=-22.5 StartZ=0 EndX=-11 EndY=2.5 EndZ=0
  constraints (12):
    c: Coincident(g0,g1)
    c: Coincident(g1,g2)
    c: Coincident(g2,g3)
    c: Horizontal(g0)
    c: Horizontal(g2)
    c: Vertical(g1)
    c: Vertical(g3)
    c: DistanceY(g1,g1) = 25
    c: Coincident(g3,g0)
    c: PointOnObject(g1,g-3)
    c: Vertical(g0,g-4)
    c: DistanceY(g-4,g0) = 2.5
FEATURE [PartDesign::Pad] Pad031  label="Pad-bearing_mount_base"
  BaseFeature = -> Pad030
  Direction = (0,0,1)
  Length = 20
  Length2 = 8
  Profile = -> Sketch079
  ReferenceAxis = -> Sketch079 [N_Axis]
  Type = 4
FEATURE [Sketcher::SketchObject] Sketch080
  FullyConstrained = true
  MapMode = 5
  Placement = pos=(-11,0,0) rot=(0.57735,-0.57735,-0.57735;2.0944rad)
  Support = -> [Pad031]
  sketch-geometry (1):
    g0: Circle CenterX=10 CenterY=15 CenterZ=0 NormalX=0 NormalY=0 NormalZ=1 AngleXU=0 Radius=11.01
  constraints (3):
    c: DistanceX(g0) = 10
    c: DistanceY(g0) = 15
    c: Diameter(g0) = 22.02
FEATURE [PartDesign::Pocket] Pocket039  label="Pocket-bearing-OD"
  BaseFeature = -> Pad031
  Direction = (1,0,0)
  Length = 7
  Length2 = 5
  Profile = -> Sketch080
  ReferenceAxis = -> Sketch080 [N_Axis]
  Type = 0
FEATURE [PartDesign::Mirrored] Mirrored001  label="Mirrored-bearing_pocket"
  BaseFeature = -> Pocket039
  MirrorPlane = -> YZ_Plane016
  Originals = -> [Pocket039]
FEATURE [Sketcher::SketchObject] Sketch081
  ExternalGeometry = -> [Mirrored001]
  FullyConstrained = true
  MapMode = 5
  Placement = pos=(-4,0,0) rot=(0.57735,-0.57735,-0.57735;2.0944rad)
  Support = -> [Mirrored001]
  sketch-geometry (1):
    g0: Circle CenterX=10 CenterY=15 CenterZ=0 NormalX=0 NormalY=0 NormalZ=1 AngleXU=0 Radius=10
  constraints (2):
    c: Coincident(g0,g-3)
    c: Diameter(g0) = 20
FEATURE [PartDesign::Pocket] Pocket040
  BaseFeature = -> Mirrored001
  Direction = (1,0,0)
  Length = 5
  Length2 = 5
  Profile = -> Sketch081
  ReferenceAxis = -> Sketch081 [N_Axis]
  Type = 1
FEATURE [Sketcher::SketchObject] Sketch082
  FullyConstrained = true
  MapMode = 5
  Support = -> [XY_Plane017]
  sketch-geometry (2):
    g0: Circle CenterX=0 CenterY=0 CenterZ=0 NormalX=0 NormalY=0 NormalZ=1 AngleXU=0 Radius=3.95
    g1: Circle CenterX=0 CenterY=0 CenterZ=0 NormalX=0 NormalY=0 NormalZ=1 AngleXU=0 Radius=11
  constraints (4):
    c: Coincident(g0,g-1)
    c: Coincident(g1,g0)
    c: Diameter(g0) = 7.9
    c: Diameter(g1) = 22
FEATURE [PartDesign::Pad] Pad032
  Direction = (0,0,1)
  Length = 7
  Length2 = 10
  Profile = -> Sketch082
  ReferenceAxis = -> Sketch082 [N_Axis]
  Type = 0
FEATURE [PartDesign::Body] Body018  label="Body-bearing001"
  Group = -> [Sketch082,Pad032]
  Origin = -> Origin017
  Placement = pos=(-3.26003,-10.1498,15.02) rot=(0,-1,0;1.5708rad)
  Tip = -> Pad032
FEATURE [Sketcher::SketchObject] Sketch083
  ExternalGeometry = -> [Pocket040]
  FullyConstrained = false
  MapMode = 5
  Placement = pos=(-11,0,0) rot=(0.57735,-0.57735,-0.57735;2.0944rad)
  Support = -> [Pocket040]
  sketch-geometry (31):
    g0: LineSegment StartX=17.5 StartY=28 StartZ=0 EndX=17.5 EndY=93.7475 EndZ=0
    g1: LineSegment StartX=17.5 StartY=93.7475 StartZ=0 EndX=202.5 EndY=26.413 EndZ=0
    g2: LineSegment StartX=202.5 StartY=26.413 StartZ=0 EndX=202.5 EndY=8 EndZ=0
    g3: LineSegment StartX=165.375 StartY=8 StartZ=0 EndX=112 EndY=27.427 EndZ=0
    g4: LineSegment StartX=25 StartY=59.0924 StartZ=0 EndX=25 EndY=8 EndZ=0
    g5: LineSegment StartX=25 StartY=8 StartZ=0 EndX=22.5 EndY=8 EndZ=0
    g6: LineSegment StartX=22.5 StartY=8 StartZ=0 EndX=22.5 EndY=28 EndZ=0
    g7: LineSegment StartX=22.5 StartY=28 StartZ=0 EndX=17.5 EndY=28 EndZ=0
    g8: ArcOfCircle CenterX=30.2523 CenterY=73.1434 CenterZ=0 NormalX=0 NormalY=0 NormalZ=1 AngleXU=0 Radius=8 StartAngle=1.22173 EndAngle=4.36332
    g9: LineSegment StartX=27.5161 StartY=65.6259 StartZ=0 EndX=187.264 EndY=7.48246 EndZ=0
    g10: LineSegment StartX=192.736 StartY=22.5175 StartZ=0 EndX=32.9884 EndY=80.661 EndZ=0
    g11: LineSegment StartX=30.2523 StartY=73.1434 StartZ=0 EndX=190 EndY=15 EndZ=0
    g12: LineSegment StartX=77.1149 StartY=56.0868 StartZ=0 EndX=71.9846 EndY=41.9914 EndZ=0
    g13: LineSegment StartX=82.2452 StartY=70.1822 StartZ=0 EndX=77.1149 EndY=56.0868 EndZ=0
    g14: LineSegment StartX=102 StartY=31.0667 StartZ=0 EndX=102 EndY=8 EndZ=0
    g15: LineSegment StartX=102 StartY=8 StartZ=0 EndX=112 EndY=8 EndZ=0
    g16: LineSegment StartX=112 StartY=8 StartZ=0 EndX=112 EndY=27.427 EndZ=0
    g17: LineSegment StartX=102 StartY=31.0667 StartZ=0 EndX=25 EndY=59.0924 EndZ=0
    g18: GeomPoint X=72.1528 Y=42.4533 Z=0
    g19: LineSegment StartX=102 StartY=38.516 StartZ=0 EndX=102 EndY=55.5428 EndZ=0
    g20: LineSegment StartX=112 StartY=51.9031 StartZ=0 EndX=112 EndY=34.8763 EndZ=0
    g21: LineSegment StartX=32.9884 StartY=80.661 StartZ=0 EndX=102 EndY=55.5428 EndZ=0
    g22: LineSegment StartX=102 StartY=38.516 StartZ=0 EndX=27.5161 EndY=65.6259 EndZ=0
    g23: LineSegment StartX=112 StartY=51.9031 StartZ=0 EndX=192.736 EndY=22.5175 EndZ=0
    g24: LineSegment StartX=185.842 StartY=8 StartZ=0 EndX=165.375 EndY=8 EndZ=0
    g25: LineSegment StartX=202.5 StartY=8 StartZ=0 EndX=193.873 EndY=8 EndZ=0
    g26: LineSegment StartX=193.873 StartY=8 StartZ=0 EndX=185.842 EndY=8 EndZ=0
    g27: LineSegment StartX=187.264 StartY=7.48246 StartZ=0 EndX=185.842 EndY=8 EndZ=0
    g28: LineSegment StartX=185.842 StartY=8 StartZ=0 EndX=112 EndY=34.8763 EndZ=0
    g29: ArcOfCircle CenterX=190 CenterY=15 CenterZ=0 NormalX=0 NormalY=0 NormalZ=1 AngleXU=0 Radius=8 StartAngle=4.36332 EndAngle=5.21775
    g30: ArcOfCircle CenterX=190 CenterY=15 CenterZ=0 NormalX=0 NormalY=0 NormalZ=1 AngleXU=0 Radius=8 StartAngle=5.21775 EndAngle=7.50492
  constraints (84):
    c: PointOnObject(g0,g-5)
    c: Vertical(g0)
    c: Coincident(g1,g0)
    c: Coincident(g2,g1)
    c: PointOnObject(g2,g-3)
    c: Vertical(g2)
    c: PointOnObject(g25,g2)
    c: PointOnObject(g24,g-3)
    c: Coincident(g3,g24)
    c: Coincident(g4,g17)
    c: PointOnObject(g4,g-3)
    c: Vertical(g4)
    c: Coincident(g5,g4)
    c: Coincident(g5,g-4)
    c: Coincident(g6,g5)
    c: Coincident(g6,g-5)
    c: Coincident(g7,g6)
    c: Coincident(g7,g0)
    c: Parallel(g3,g1)
    c: Tangent(g8,g9) = -1.5708
    c: Tangent(g9,g29) = -1.5708
    c: Tangent(g30,g10) = -1.5708
    c: Tangent(g10,g8) = -1.5708
    c: Diameter(g8) = 16
    c: Coincident(g11,g8)
    c: Coincident(g11,g29)
    c: Parallel(g11,g3)
    c: Angle(g3,g-3) = 0.349066
    c: PointOnObject(g12,g11)
    c: PointOnObject(g12,g3)
    c: Angle(g3,g12) = 1.5708
    c: PointOnObject(g13,g1)
    c: Coincident(g13,g12)
    c: Parallel(g13,g12)
    c: Distance(g12,g17) = 50
    c: Distance(g13) = 15
    c: Distance(g12) = 15
    c: Distance(g10) = 170
    c: DistanceY(g2,g29) = 7
    c: DistanceX(g-5,g0) = 20
    c: DistanceX(g0,g4) = 7.5
    c: DistanceX(g4,g2) = 177.5
    c: DistanceX(g29,g2) = 12.5
    c: PointOnObject(g14,g-3)
    c: Coincident(g15,g14)
    c: PointOnObject(g15,g-3)
    c: Coincident(g16,g15)
    c: Vertical(g16)
    c: Vertical(g14)
    c: DistanceX(g15,g15) = 10
    c: DistanceX(g0,g14) = 84.5
    c: Coincident(g3,g16)
    c: Coincident(g17,g14)
    c: Parallel(g17,g3)
    c: PointOnObject(g18,g12)
    c: PointOnObject(g12,g17)
    c: PointOnObject(g19,g9)
    c: PointOnObject(g19,g10)
    c: PointOnObject(g20,g10)
    c: PointOnObject(g20,g9)
    c: Vertical(g20)
    c: Vertical(g14,g19)
    c: Vertical(g20,g3)
    c: Vertical(g19)
    c: Coincident(g21,g8)
    c: Coincident(g21,g19)
    c: Coincident(g22,g19)
    c: Coincident(g22,g8)
    c: Coincident(g23,g20)
    c: Coincident(g23,g30)
    c: Coincident(g27,g29)
    c: Coincident(g20,g28)
    c: Coincident(g26,g24)
    c: Horizontal(g24)
    c: Coincident(g25,g26)
    c: Horizontal(g25)
    c: Horizontal(g26)
    c: Coincident(g27,g28)
    c: Coincident(g27,g24)
    c: PointOnObject(g24,g9)
    c: Coincident(g29,g30)
    c: Coincident(g29,g30)
    c: Equal(g8,g29)
    c: Coincident(g25,g29)
FEATURE [PartDesign::Pad] Pad033  label="Pad-ramp001"
  BaseFeature = -> Pocket040
  Direction = (-1,0,0)
  Length = 22
  Length2 = 10
  Profile = -> Sketch083
  ReferenceAxis = -> Sketch083 [N_Axis]
  Reversed = true
  Type = 0
FEATURE [Sketcher::SketchObject] Sketch084
  ExternalGeometry = -> [Fillet007]
  FullyConstrained = false
  MapMode = 5
  Placement = pos=(-1e-15,2.3e-15,3.5) rot=(0,0,-1;1.5708rad)
  Support = -> [Fillet007]
  sketch-geometry (7):
    g0: ArcOfCircle CenterX=-10 CenterY=145 CenterZ=0 NormalX=0 NormalY=0 NormalZ=1 AngleXU=0 Radius=3.1 StartAngle=1.5708 EndAngle=4.71239
    g1: GeomPoint X=-12.2613 Y=142.879 Z=0
    g2: LineSegment StartX=-10 StartY=148.1 StartZ=0 EndX=-5 EndY=148.1 EndZ=0
    g3: LineSegment StartX=-5 StartY=148.1 StartZ=0 EndX=-5 EndY=141.9 EndZ=0
    g4: LineSegment StartX=-5 StartY=141.9 StartZ=0 EndX=-10 EndY=141.9 EndZ=0
    g5: LineSegment StartX=-10 StartY=148.1 StartZ=0 EndX=-10 EndY=145 EndZ=0
    g6: LineSegment StartX=-10 StartY=145 StartZ=0 EndX=-10 EndY=141.9 EndZ=0
  constraints (17):
    c: Coincident(g0,g-3)
    c: PointOnObject(g1,g-3)
    c: PointOnObject(g1,g0)
    c: Horizontal(g2)
    c: Coincident(g3,g2)
    c: Vertical(g3)
    c: Coincident(g4,g3)
    c: Horizontal(g4)
    c: Coincident(g5,g2)
    c: Coincident(g5,g0)
    c: Coincident(g6,g0)
    c: Coincident(g6,g4)
    c: Vertical(g5)
    c: Vertical(g6)
    c: DistanceX(g4,g4) = 5
    c: Coincident(g0,g2)
    c: Coincident(g0,g4)
FEATURE [PartDesign::Pocket] Pocket041  label="Pocket-front_mount_access_hole"
  BaseFeature = -> Fillet007
  Direction = (3e-16,-9e-16,-1)
  Length = 5
  Length2 = 5
  Placement = pos=(0,0,0) rot=(0.57735,0.57735,0.57735;2.0944rad)
  Profile = -> Sketch084
  ReferenceAxis = -> Sketch084 [N_Axis]
  Reversed = true
  Type = 1
FEATURE [PartDesign::Fillet] Fillet013
  Base = -> Pocket041 [Edge132,Edge203,Edge209,Edge135]
  BaseFeature = -> Pocket041
  Placement = pos=(0,0,0) rot=(0.57735,0.57735,0.57735;2.0944rad)
  Radius = 1
  SupportTransform = false
  UseAllEdges = false
FEATURE [Sketcher::SketchObject] Sketch085
  ExternalGeometry = -> [Pad033]
  FullyConstrained = true
  MapMode = 5
  Placement = pos=(-11,0,0) rot=(0.57735,-0.57735,-0.57735;2.0944rad)
  Support = -> [Pad033]
  sketch-geometry (6):
    g0: ArcOfCircle CenterX=30.2523 CenterY=73.1434 CenterZ=0 NormalX=0 NormalY=0 NormalZ=1 AngleXU=0 Radius=11.25 StartAngle=1.22173 EndAngle=4.36332
    g1: ArcOfCircle CenterX=190 CenterY=15 CenterZ=0 NormalX=0 NormalY=0 NormalZ=1 AngleXU=0 Radius=11.25 StartAngle=4.36332 EndAngle=7.50492
    g2: LineSegment StartX=26.4045 StartY=62.5719 StartZ=0 EndX=186.152 EndY=4.42846 EndZ=0
    g3: LineSegment StartX=193.848 StartY=25.5715 StartZ=0 EndX=34.1 EndY=83.715 EndZ=0
    g4: LineSegment StartX=30.2523 StartY=73.1434 StartZ=0 EndX=190 EndY=15 EndZ=0
    g5: LineSegment StartX=55.3826 StartY=79.9594 StartZ=0 EndX=50.2523 EndY=65.864 EndZ=0
  constraints (17):
    c: Tangent(g0,g2) = -1.5708
    c: Tangent(g2,g1) = -1.5708
    c: Tangent(g3,g0) = -1.5708
    c: Equal(g0,g1)
    c: Diameter(g0) = 22.5
    c: Coincident(g4,g0)
    c: Coincident(g4,g1)
    c: Distance(g3) = 170
    c: DistanceX(g1,g-3) = 12.5
    c: PointOnObject(g5,g-4)
    c: PointOnObject(g5,g4)
    c: Angle(g4,g5) = 1.5708
    c: Distance(g5) = 15
    c: Parallel(g-4,g4)
    c: Angle(g1) = 3.14159
    c: Coincident(g3,g1)
    c: DistanceX(g0,g5) = 20
FEATURE [Sketcher::SketchObject] Sketch086
  FullyConstrained = true
  MapMode = 5
  Placement = pos=(0,0,0) rot=(1,0,0;1.5708rad)
  Support = -> [XZ_Plane018]
  sketch-geometry (16):
    g0: LineSegment StartX=-3.8476e-12 StartY=-10.8333 StartZ=0 EndX=4 EndY=-10.8333 EndZ=0
    g1: LineSegment StartX=4 StartY=-10.8333 StartZ=0 EndX=4 EndY=-0.833334 EndZ=0
    g2: LineSegment StartX=4 StartY=-0.833334 StartZ=0 EndX=-15 EndY=-0.833334 EndZ=0
    g3: LineSegment StartX=-15 StartY=-0.833334 StartZ=0 EndX=-15 EndY=0.833334 EndZ=0
    g4: LineSegment StartX=-15 StartY=0.833334 StartZ=0 EndX=4 EndY=0.833334 EndZ=0
    g5: LineSegment StartX=4 StartY=0.833334 StartZ=0 EndX=4 EndY=10.8333 EndZ=0
    g6: LineSegment StartX=4 StartY=10.8333 StartZ=0 EndX=0 EndY=10.8333 EndZ=0
    g7: LineSegment StartX=0 StartY=10.8333 StartZ=0 EndX=0 EndY=0.853333 EndZ=0
    g8: LineSegment StartX=0 StartY=0.853333 StartZ=0 EndX=-19 EndY=0.853333 EndZ=0
    g9: LineSegment StartX=-19 StartY=0.853333 StartZ=0 EndX=-19 EndY=-0.853333 EndZ=0
    g10: LineSegment StartX=-19 StartY=-0.853333 StartZ=0 EndX=-3.8476e-12 EndY=-0.853333 EndZ=0
    g11: LineSegment StartX=-3.8476e-12 StartY=-0.853333 StartZ=0 EndX=-3.8476e-12 EndY=-10.8333 EndZ=0
    g12: LineSegment StartX=-19 StartY=0.853333 StartZ=0 EndX=-15 EndY=-0.833334 EndZ=0
    g13: LineSegment StartX=-15 StartY=0.833334 StartZ=0 EndX=-19 EndY=-0.853333 EndZ=0
    g14: LineSegment StartX=0 StartY=0.853333 StartZ=0 EndX=0 EndY=0 EndZ=0
    g15: LineSegment StartX=0 StartY=0 StartZ=0 EndX=-3.8476e-12 EndY=-0.853333 EndZ=0
  constraints (44):
    c: Horizontal(g0)
    c: Coincident(g1,g0)
    c: Vertical(g1)
    c: Coincident(g2,g1)
    c: Horizontal(g2)
    c: Coincident(g3,g2)
    c: Vertical(g3)
    c: Horizontal(g4)
    c: Coincident(g5,g4)
    c: Vertical(g5)
    c: Coincident(g6,g5)
    c: PointOnObject(g6,g-2)
    c: Horizontal(g6)
    c: Coincident(g7,g6)
    c: Vertical(g7)
    c: Coincident(g8,g7)
    c: Horizontal(g8)
    c: Coincident(g9,g8)
    c: Vertical(g9)
    c: Coincident(g10,g9)
    c: Horizontal(g10)
    c: Coincident(g11,g10)
    c: Vertical(g11)
    c: DistanceY(g3,g3) = 1.66667
    c: Coincident(g3,g4)
    c: DistanceY(g9,g9) = 1.70667
    c: Coincident(g12,g8)
    c: Coincident(g12,g2)
    c: Coincident(g13,g3)
    c: Coincident(g13,g9)
    c: Equal(g13,g12)
    c: DistanceX(g9,g2) = 4
    c: DistanceX(g0,g0) = 4
    c: Equal(g0,g6)
    c: Equal(g1,g5)
    c: DistanceY(g1,g1) = 10
    c: DistanceX(g2,g10) = 15
    c: Coincident(g11,g0)
    c: Vertical(g1,g4)
    c: Coincident(g14,g7)
    c: Coincident(g14,g-1)
    c: Coincident(g15,g14)
    c: Coincident(g15,g10)
    c: Equal(g15,g14)
FEATURE [PartDesign::Pad] Pad034  label="Pad-main_body001"
  Direction = (0,-1,-2e-16)
  Length = 93
  Length2 = 10
  Placement = pos=(0,0,0) rot=(1,0,0;1.5708rad)
  Profile = -> Sketch086
  ReferenceAxis = -> Sketch086 [N_Axis]
  Type = 0
FEATURE [Sketcher::SketchObject] Sketch087
  ExternalGeometry = -> [Pad034]
  FullyConstrained = true
  MapMode = 5
  Placement = pos=(0,2e-16,0.853333) rot=(0,0,1;3.14159rad)
  Support = -> [Pad034]
  sketch-geometry (14):
    g0: ArcOfCircle CenterX=5.5 CenterY=23 CenterZ=0 NormalX=0 NormalY=0 NormalZ=1 AngleXU=0 Radius=1.7 StartAngle=1.5708 EndAngle=4.71239
    g1: ArcOfCircle CenterX=11.5 CenterY=23 CenterZ=0 NormalX=0 NormalY=0 NormalZ=1 AngleXU=0 Radius=1.7 StartAngle=4.71239 EndAngle=7.85398
    g2: LineSegment StartX=5.5 StartY=21.3 StartZ=0 EndX=11.5 EndY=21.3 EndZ=0
    g3: LineSegment StartX=11.5 StartY=24.7 StartZ=0 EndX=5.5 EndY=24.7 EndZ=0
    g4: ArcOfCircle CenterX=5.5 CenterY=48 CenterZ=0 NormalX=0 NormalY=0 NormalZ=1 AngleXU=0 Radius=1.7 StartAngle=1.5708 EndAngle=4.71239
    g5: ArcOfCircle CenterX=11.5 CenterY=48 CenterZ=0 NormalX=0 NormalY=0 NormalZ=1 AngleXU=0 Radius=1.7 StartAngle=4.71239 EndAngle=7.85398
    g6: LineSegment StartX=5.5 StartY=46.3 StartZ=0 EndX=11.5 EndY=46.3 EndZ=0
    g7: LineSegment StartX=11.5 StartY=49.7 StartZ=0 EndX=5.5 EndY=49.7 EndZ=0
    g8: ArcOfCircle CenterX=5.5 CenterY=73 CenterZ=0 NormalX=0 NormalY=0 NormalZ=1 AngleXU=0 Radius=1.7 StartAngle=1.5708 EndAngle=4.71239
    g9: ArcOfCircle CenterX=11.5 CenterY=73 CenterZ=0 NormalX=0 NormalY=0 NormalZ=1 AngleXU=0 Radius=1.7 StartAngle=4.71239 EndAngle=7.85398
    g10: LineSegment StartX=5.5 StartY=71.3 StartZ=0 EndX=11.5 EndY=71.3 EndZ=0
    g11: LineSegment StartX=11.5 StartY=74.7 StartZ=0 EndX=5.5 EndY=74.7 EndZ=0
    g12: LineSegment StartX=11.5 StartY=73 StartZ=0 EndX=11.5 EndY=48 EndZ=0
    g13: LineSegment StartX=11.5 StartY=48 StartZ=0 EndX=11.5 EndY=23 EndZ=0
  constraints (34):
    c: Tangent(g0,g2) = -1.5708
    c: Tangent(g2,g1) = -1.5708
    c: Tangent(g1,g3) = -1.5708
    c: Tangent(g3,g0) = -1.5708
    c: Equal(g0,g1)
    c: Horizontal(g2)
    c: Diameter(g1) = 3.4
    c: DistanceX(g2,g2) = 6
    c: DistanceX(g1,g-3) = 7.5
    c: Tangent(g4,g6) = -1.5708
    c: Tangent(g6,g5) = -1.5708
    c: Tangent(g5,g7) = -1.5708
    c: Tangent(g7,g4) = -1.5708
    c: Equal(g4,g5)
    c: Tangent(g8,g10) = -1.5708
    c: Tangent(g10,g9) = -1.5708
    c: Tangent(g9,g11) = -1.5708
    c: Tangent(g11,g8) = -1.5708
    c: Equal(g8,g9)
    c: Equal(g9,g5)
    c: Equal(g5,g1)
    c: Horizontal(g5,g4)
    c: Horizontal(g9,g8)
    c: Vertical(g8,g4)
    c: Vertical(g4,g0)
    c: Coincident(g12,g9)
    c: Coincident(g12,g5)
    c: Vertical(g12)
    c: Coincident(g13,g5)
    c: Coincident(g13,g1)
    c: Vertical(g13)
    c: Equal(g12,g13)
    c: DistanceY(g12,g12) = 25
    c: DistanceY(g9,g-3) = 20
FEATURE [PartDesign::Pad] Pad035  label="Pad-slots001"
  BaseFeature = -> Pad034
  Direction = (0,-2e-16,1)
  Length = 10
  Length2 = 10
  Placement = pos=(0,0,0) rot=(1,0,0;1.5708rad)
  Profile = -> Sketch087
  ReferenceAxis = -> Sketch087 [N_Axis]
  Type = 0
FEATURE [PartDesign::Mirrored] Mirrored002  label="Mirrored-slots_top_to_bottom001"
  BaseFeature = -> Pad035
  MirrorPlane = -> XY_Plane018
  Originals = -> [Pad035]
  Placement = pos=(0,0,0) rot=(1,0,0;1.5708rad)
FEATURE [Sketcher::SketchObject] Sketch088
  ExternalGeometry = -> [Mirrored002]
  FullyConstrained = true
  MapMode = 5
  Placement = pos=(0,-2e-16,-0.833334) rot=(0,0,1;3.14159rad)
  Support = -> [Mirrored002]
  sketch-geometry (5):
    g0: Circle CenterX=7.5 CenterY=23 CenterZ=0 NormalX=0 NormalY=0 NormalZ=1 AngleXU=0 Radius=1.69
    g1: Circle CenterX=7.5 CenterY=48 CenterZ=0 NormalX=0 NormalY=0 NormalZ=1 AngleXU=0 Radius=1.69
    g2: Circle CenterX=7.5 CenterY=73 CenterZ=0 NormalX=0 NormalY=0 NormalZ=1 AngleXU=0 Radius=1.69
    g3: LineSegment StartX=7.5 StartY=73 StartZ=0 EndX=7.5 EndY=48 EndZ=0
    g4: LineSegment StartX=7.5 StartY=48 StartZ=0 EndX=7.5 EndY=23 EndZ=0
  constraints (13):
    c: Equal(g2,g1)
    c: Equal(g2,g0)
    c: Diameter(g2) = 3.38
    c: Coincident(g3,g2)
    c: Coincident(g3,g1)
    c: Vertical(g3)
    c: Coincident(g4,g1)
    c: Coincident(g4,g0)
    c: Vertical(g4)
    c: DistanceY(g3,g3) = 25
    c: DistanceX(g0,g-3) = 7.5
    c: Equal(g3,g4)
    c: DistanceY(g2,g-3) = 20
FEATURE [PartDesign::Pad] Pad036  label="Pad-inside_holes001"
  BaseFeature = -> Mirrored002
  Direction = (0,-2e-16,1)
  Length = 10
  Length2 = 10
  Placement = pos=(0,0,0) rot=(1,0,0;1.5708rad)
  Profile = -> Sketch088
  ReferenceAxis = -> Sketch088 [N_Axis]
  Type = 0
FEATURE [Sketcher::SketchObject] Sketch089
  FullyConstrained = true
  MapMode = 5
  Placement = pos=(0,0,0) rot=(0.707107,0,-0.707107;3.14159rad)
  Support = -> [Pad036]
  sketch-geometry (1):
    g0: Circle CenterX=0 CenterY=3 CenterZ=0 NormalX=0 NormalY=0 NormalZ=1 AngleXU=0 Radius=4.55
  constraints (3):
    c: PointOnObject(g0,g-2)
    c: Diameter(g0) = 9.1
    c: DistanceY(g-1,g0) = 3
FEATURE [PartDesign::Pad] Pad037  label="Pad-shaft_female"
  BaseFeature = -> Pad036
  Direction = (-1,0,-2e-16)
  Length = 19
  Length2 = 10
  Placement = pos=(0,0,0) rot=(1,0,0;1.5708rad)
  Profile = -> Sketch089
  ReferenceAxis = -> Sketch089 [N_Axis]
  Type = 0
FEATURE [Sketcher::SketchObject] Sketch092
  ExternalGeometry = -> [Pad037]
  FullyConstrained = true
  MapMode = 5
  Placement = pos=(0,0,0) rot=(-1,0,0;1.5708rad)
  Support = -> [Pad037]
  sketch-geometry (4):
    g0: LineSegment StartX=-3.8476e-12 StartY=10.8333 StartZ=0 EndX=4 EndY=10.8333 EndZ=0
    g1: LineSegment StartX=4 StartY=10.8333 StartZ=0 EndX=4 EndY=-10.8333 EndZ=0
    g2: LineSegment StartX=4 StartY=-10.8333 StartZ=0 EndX=-3.8476e-12 EndY=-10.8333 EndZ=0
    g3: LineSegment StartX=-3.8476e-12 StartY=-10.8333 StartZ=0 EndX=-3.8476e-12 EndY=10.8333 EndZ=0
  constraints (10):
    c: Coincident(g0,g1)
    c: Coincident(g1,g2)
    c: Coincident(g2,g3)
    c: Coincident(g3,g0)
    c: Horizontal(g0)
    c: Horizontal(g2)
    c: Vertical(g1)
    c: Vertical(g3)
    c: Coincident(g0,g-3)
    c: Coincident(g1,g-4)
FEATURE [PartDesign::Pad] Pad038  label="Pad-gap_extension"
  BaseFeature = -> Pad037
  Direction = (0,1,2e-16)
  Length = 10
  Length2 = 10
  Placement = pos=(0,0,0) rot=(1,0,0;1.5708rad)
  Profile = -> Sketch092
  ReferenceAxis = -> Sketch092 [N_Axis]
  Type = 0
FEATURE [Sketcher::SketchObject] Sketch093
  ExternalGeometry = -> [Pad038]
  FullyConstrained = true
  MapMode = 5
  Placement = pos=(4,0,0) rot=(0.707107,0,0.707107;3.14159rad)
  Support = -> [Pad038]
  sketch-geometry (6):
    g0: ArcOfCircle CenterX=0 CenterY=3 CenterZ=0 NormalX=0 NormalY=0 NormalZ=1 AngleXU=0 Radius=4.5 StartAngle=1.75706 EndAngle=7.66772
    g1: GeomPoint X=-0.833334 Y=7.42217 Z=0
    g2: GeomPoint X=0.833334 Y=7.42217 Z=0
    g3: LineSegment StartX=-0.833334 StartY=7.42217 StartZ=0 EndX=-0.833334 EndY=8.42217 EndZ=0
    g4: LineSegment StartX=-0.833334 StartY=8.42217 StartZ=0 EndX=0.833334 EndY=8.42217 EndZ=0
    g5: LineSegment StartX=0.833334 StartY=8.42217 StartZ=0 EndX=0.833334 EndY=7.42217 EndZ=0
  constraints (15):
    c: PointOnObject(g0,g-2)
    c: DistanceY(g0) = 3
    c: Diameter(g0) = 9
    c: PointOnObject(g1,g-3)
    c: PointOnObject(g2,g-4)
    c: Coincident(g3,g1)
    c: PointOnObject(g3,g-3)
    c: Coincident(g4,g3)
    c: PointOnObject(g4,g-4)
    c: Horizontal(g4)
    c: Coincident(g5,g4)
    c: Coincident(g5,g2)
    c: Coincident(g0,g5)
    c: Coincident(g0,g3)
    c: DistanceY(g5,g5) = 1
FEATURE [PartDesign::Pocket] Pocket042  label="Pocket-shaft_male"
  BaseFeature = -> Pad038
  Direction = (-1,0,2e-16)
  Length = 19
  Length2 = 5
  Placement = pos=(0,0,0) rot=(1,0,0;1.5708rad)
  Profile = -> Sketch093
  ReferenceAxis = -> Sketch093 [N_Axis]
  Type = 0
FEATURE [PartDesign::Fillet] Fillet014
  Base = -> Pocket042 [Edge69,Edge125,Edge59,Edge64,Edge62]
  BaseFeature = -> Pocket042
  Placement = pos=(0,0,0) rot=(1,0,0;1.5708rad)
  Radius = 0.45
  SupportTransform = false
  UseAllEdges = false
FEATURE [PartDesign::Fillet] Fillet015
  Base = -> Fillet014 [Edge64,Edge42]
  BaseFeature = -> Fillet014
  Placement = pos=(0,0,0) rot=(1,0,0;1.5708rad)
  Radius = 1
  SupportTransform = false
  UseAllEdges = false
FEATURE [PartDesign::Fillet] Fillet016
  Base = -> Fillet015 [Edge140,Edge141,Edge138,Edge132]
  BaseFeature = -> Fillet015
  Placement = pos=(0,0,0) rot=(1,0,0;1.5708rad)
  Radius = 1
  SupportTransform = false
  UseAllEdges = false
FEATURE [PartDesign::Fillet] Fillet017
  Base = -> Fillet016 [Edge52,Edge47,Edge11,Edge12,Edge1,Edge2,Edge6,Edge101,Edge115,Edge114,Edge133,Edge66,Edge64,Edge65,Edge67]
  BaseFeature = -> Fillet016
  Placement = pos=(0,0,0) rot=(1,0,0;1.5708rad)
  Radius = 1.5
  SupportTransform = false
  UseAllEdges = false
FEATURE [PartDesign::Fillet] Fillet018
  Base = -> Fillet017 [Edge103,Edge87,Edge185,Edge184,Edge183,Edge157]
  BaseFeature = -> Fillet017
  Placement = pos=(0,0,0) rot=(1,0,0;1.5708rad)
  Radius = 0.45
  SupportTransform = false
  UseAllEdges = false
FEATURE [PartDesign::Fillet] Fillet019
  Base = -> Fillet018 [Face53,Face54,Face55,Face49,Face50,Face51,Face45,Face46,Face47,Face25,Face26,Face23,Face29,Face30,Face27,Face33,Face34,Face31,Face52,Face32,Face28,Face48,Face44,Face24]
  BaseFeature = -> Fillet018
  Placement = pos=(0,0,0) rot=(1,0,0;1.5708rad)
  Radius = 0.5
  SupportTransform = false
  UseAllEdges = false
FEATURE [PartDesign::Fillet] Fillet020
  Base = -> Fillet019 [Face87,Face85,Face86]
  BaseFeature = -> Fillet019
  Placement = pos=(0,0,0) rot=(1,0,0;1.5708rad)
  Radius = 0.5
  SupportTransform = false
  UseAllEdges = false
FEATURE [PartDesign::Body] Body019  label="Body-v3.1_slicer"
  Group = -> [Sketch086,Pad034,Sketch087,Pad035,Mirrored002,Sketch088,Pad036,Sketch089,Pad037,Sketch092,Pad038,Sketch093,Pocket042,Fillet014,Fillet015,Fillet016,Fillet017,Fillet018,Fillet019,Fillet020]
  Origin = -> Origin018
  Placement = pos=(-280,59,161.477) rot=(0,0,1;0rad)
  Tip = -> Fillet020
FEATURE [PartDesign::Pocket] Pocket043  label="Pocket-bearing_slot001"
  BaseFeature = -> Pad033
  Direction = (1,0,0)
  Length = 7.5
  Length2 = 5
  Profile = -> Sketch085
  ReferenceAxis = -> Sketch085 [N_Axis]
  Type = 0
FEATURE [PartDesign::Mirrored] Mirrored003  label="Mirrored-bearing_slot"
  BaseFeature = -> Pocket043
  MirrorPlane = -> YZ_Plane016
  Originals = -> [Pocket043]
FEATURE [Sketcher::SketchObject] Sketch094
  ExternalGeometry = -> [Mirrored003]
  FullyConstrained = true
  MapMode = 5
  Placement = pos=(-3.5,0,0) rot=(0.57735,-0.57735,-0.57735;2.0944rad)
  Support = -> [Mirrored003]
  sketch-geometry (4):
    g0: LineSegment StartX=112 StartY=34.8763 StartZ=0 EndX=102 EndY=38.516 EndZ=0
    g1: LineSegment StartX=102 StartY=38.516 StartZ=0 EndX=102 EndY=55.5428 EndZ=0
    g2: LineSegment StartX=102 StartY=55.5428 StartZ=0 EndX=112 EndY=51.9031 EndZ=0
    g3: LineSegment StartX=112 StartY=51.9031 StartZ=0 EndX=112 EndY=34.8763 EndZ=0
  constraints (8):
    c: Coincident(g1,g0)
    c: Coincident(g2,g1)
    c: Coincident(g3,g2)
    c: Coincident(g3,g0)
    c: Coincident(g1,g-4)
    c: Coincident(g0,g-4)
    c: Coincident(g-3,g2)
    c: Coincident(g-3,g0)
FEATURE [PartDesign::Pocket] Pocket044  label="Pocket-mid_support_inside"
  BaseFeature = -> Mirrored003
  Direction = (1,0,0)
  Length = 2.5
  Length2 = 5
  Profile = -> Sketch094
  ReferenceAxis = -> Sketch094 [N_Axis]
  Type = 0
FEATURE [PartDesign::Mirrored] Mirrored004
  BaseFeature = -> Pocket044
  MirrorPlane = -> YZ_Plane016
  Originals = -> [Pocket044]
FEATURE [Sketcher::SketchObject] Sketch095
  ExternalGeometry = -> [Mirrored004,Sketch085]
  FullyConstrained = true
  MapMode = 5
  Placement = pos=(-11,0,0) rot=(0.57735,-0.57735,-0.57735;2.0944rad)
  Support = -> [Mirrored004]
  sketch-geometry (9):
    g0: LineSegment StartX=17.5 StartY=93.7475 StartZ=0 EndX=202.5 EndY=26.413 EndZ=0
    g1: LineSegment StartX=202.5 StartY=26.413 StartZ=0 EndX=202.5 EndY=0 EndZ=0
    g2: LineSegment StartX=202.5 StartY=0 StartZ=0 EndX=187.355 EndY=0 EndZ=0
    g3: LineSegment StartX=187.355 StartY=0 StartZ=0 EndX=17.5 EndY=61.8222 EndZ=0
    g4: LineSegment StartX=17.5 StartY=61.8222 StartZ=0 EndX=17.5 EndY=93.7475 EndZ=0
    g5: ArcOfCircle CenterX=30.2523 CenterY=73.1434 CenterZ=0 NormalX=0 NormalY=0 NormalZ=1 AngleXU=0 Radius=6 StartAngle=1.22173 EndAngle=4.36332
    g6: ArcOfCircle CenterX=190 CenterY=15 CenterZ=0 NormalX=0 NormalY=0 NormalZ=1 AngleXU=0 Radius=6 StartAngle=4.36332 EndAngle=7.50492
    g7: LineSegment StartX=28.2001 StartY=67.5053 StartZ=0 EndX=187.948 EndY=9.36184 EndZ=0
    g8: LineSegment StartX=192.052 StartY=20.6382 StartZ=0 EndX=32.3044 EndY=78.7816 EndZ=0
  constraints (21):
    c: Coincident(g0,g-4)
    c: Coincident(g0,g-6)
    c: Coincident(g1,g0)
    c: PointOnObject(g1,g-7)
    c: Vertical(g1)
    c: Coincident(g2,g1)
    c: PointOnObject(g2,g-7)
    c: Coincident(g3,g2)
    c: PointOnObject(g3,g-4)
    c: Coincident(g4,g3)
    c: Coincident(g4,g0)
    c: Parallel(g-5,g3)
    c: PointOnObject(g-5,g3)
    c: Tangent(g5,g7) = -1.5708
    c: Tangent(g7,g6) = -1.5708
    c: Tangent(g6,g8) = -1.5708
    c: Tangent(g8,g5) = -1.5708
    c: Equal(g5,g6)
    c: Coincident(g5,g-9)
    c: Coincident(g6,g-8)
    c: Diameter(g6) = 12
FEATURE [PartDesign::Pad] Pad039  label="Pad-bearing_cap"
  BaseFeature = -> Mirrored004
  Direction = (-1,0,0)
  Length = 2.5
  Length2 = 10
  Profile = -> Sketch095
  ReferenceAxis = -> Sketch095 [N_Axis]
  Type = 0
FEATURE [PartDesign::Mirrored] Mirrored005
  BaseFeature = -> Pad039
  MirrorPlane = -> YZ_Plane016
  Originals = -> [Pad039]
FEATURE [Sketcher::SketchObject] Sketch096
  FullyConstrained = true
  MapMode = 5
  Support = -> [XY_Plane019]
  sketch-geometry (2):
    g0: Circle CenterX=0 CenterY=0 CenterZ=0 NormalX=0 NormalY=0 NormalZ=1 AngleXU=0 Radius=3.95
    g1: Circle CenterX=0 CenterY=0 CenterZ=0 NormalX=0 NormalY=0 NormalZ=1 AngleXU=0 Radius=11
  constraints (4):
    c: Coincident(g0,g-1)
    c: Coincident(g1,g0)
    c: Diameter(g0) = 7.9
    c: Diameter(g1) = 22
FEATURE [PartDesign::Pad] Pad040
  Direction = (0,0,1)
  Length = 7
  Length2 = 10
  Profile = -> Sketch096
  ReferenceAxis = -> Sketch096 [N_Axis]
  Type = 0
FEATURE [PartDesign::Body] Body020  label="Body-bearing002"
  Group = -> [Sketch096,Pad040]
  Origin = -> Origin019
  Placement = pos=(-3.26004,-190.15,15.02) rot=(0,-1,0;1.5708rad)
  Tip = -> Pad040
FEATURE [PartDesign::Fillet] Fillet021
  Base = -> Mirrored005 [Edge81,Edge94,Edge122]
  BaseFeature = -> Mirrored005
  Radius = 14
  SupportTransform = false
  UseAllEdges = false
FEATURE [Sketcher::SketchObject] Sketch097
  FullyConstrained = true
  MapMode = 5
  Support = -> [XY_Plane020]
  sketch-geometry (12):
    g0: LineSegment StartX=0 StartY=0 StartZ=0 EndX=40 EndY=0 EndZ=0
    g1: LineSegment StartX=40 StartY=0 StartZ=0 EndX=40 EndY=-104 EndZ=0
    g2: LineSegment StartX=40 StartY=-104 StartZ=0 EndX=0 EndY=-104 EndZ=0
    g3: LineSegment StartX=0 StartY=-104 StartZ=0 EndX=0 EndY=0 EndZ=0
    g4: LineSegment StartX=0 StartY=0 StartZ=0 EndX=5 EndY=6 EndZ=0
    g5: LineSegment StartX=5 StartY=6 StartZ=0 EndX=10 EndY=0 EndZ=0
    g6: LineSegment StartX=10 StartY=0 StartZ=0 EndX=15 EndY=6 EndZ=0
    g7: LineSegment StartX=15 StartY=6 StartZ=0 EndX=20 EndY=0 EndZ=0
    g8: LineSegment StartX=20 StartY=0 StartZ=0 EndX=25 EndY=6 EndZ=0
    g9: LineSegment StartX=25 StartY=6 StartZ=0 EndX=30 EndY=0 EndZ=0
    g10: LineSegment StartX=30 StartY=0 StartZ=0 EndX=35 EndY=6 EndZ=0
    g11: LineSegment StartX=35 StartY=6 StartZ=0 EndX=40 EndY=0 EndZ=0
  constraints (34):
    c: Coincident(g0,g1)
    c: Coincident(g1,g2)
    c: Coincident(g2,g3)
    c: Coincident(g3,g0)
    c: Horizontal(g0)
    c: Horizontal(g2)
    c: Vertical(g1)
    c: Vertical(g3)
    c: Coincident(g0,g-1)
    c: Coincident(g4,g0)
    c: Coincident(g5,g4)
    c: PointOnObject(g5,g0)
    c: Coincident(g6,g5)
    c: Coincident(g7,g6)
    c: PointOnObject(g7,g0)
    c: Coincident(g8,g7)
    c: Coincident(g9,g8)
    c: PointOnObject(g9,g0)
    c: Coincident(g10,g9)
    c: Coincident(g11,g10)
    c: Coincident(g11,g0)
    c: Horizontal(g4,g6)
    c: Horizontal(g6,g8)
    c: Horizontal(g8,g10)
    c: Equal(g4,g5)
    c: Equal(g5,g6)
    c: Equal(g6,g7)
    c: Equal(g7,g8)
    c: Equal(g8,g9)
    c: Equal(g9,g10)
    c: Equal(g10,g11)
    c: DistanceY(g3,g4) = 6
    c: DistanceY(g3,g3) = 104
    c: DistanceX(g2,g2) = 40
FEATURE [PartDesign::Pad] Pad041
  Direction = (0,0,1)
  Length = 100
  Length2 = 10
  Profile = -> Sketch097
  ReferenceAxis = -> Sketch097 [N_Axis]
  Type = 0
FEATURE [PartDesign::Body] Body021  label="slicer003"
  Group = -> [Sketch097,Pad041]
  Origin = -> Origin020
  Placement = pos=(-17,-110,-3.233e-12) rot=(0,0,1;0rad)
  Tip = -> Pad041
FEATURE [PartDesign::Fillet] Fillet022
  Base = -> Fillet021 [Edge45]
  BaseFeature = -> Fillet021
  Radius = 14
  SupportTransform = false
  UseAllEdges = false
FEATURE [PartDesign::Fillet] Fillet023  label="Fillet-bottom_face_to_vertical"
  Base = -> Fillet022 [Edge121,Edge122,Edge120]
  BaseFeature = -> Fillet022
  Radius = 2
  SupportTransform = false
  UseAllEdges = false
FEATURE [PartDesign::Fillet] Fillet024  label="Fillet-acute_end_angle"
  Base = -> Fillet023 [Edge32]
  BaseFeature = -> Fillet023
  Radius = 2
  SupportTransform = false
  UseAllEdges = false
FEATURE [PartDesign::Fillet] Fillet025
  Base = -> Fillet024 [Edge107]
  BaseFeature = -> Fillet024
  Radius = 5
  SupportTransform = false
  UseAllEdges = false
FEATURE [PartDesign::Fillet] Fillet026
  Base = -> Fillet025 [Edge62]
  BaseFeature = -> Fillet025
  Radius = 12
  SupportTransform = false
  UseAllEdges = false
FEATURE [PartDesign::Fillet] Fillet027
  Base = -> Fillet026 [Edge25]
  BaseFeature = -> Fillet026
  Radius = 2
  SupportTransform = false
  UseAllEdges = false
FEATURE [PartDesign::Fillet] Fillet028
  Base = -> Fillet027 [Edge231,Edge246]
  BaseFeature = -> Fillet027
  Radius = 3
  SupportTransform = false
  UseAllEdges = false
FEATURE [PartDesign::Fillet] Fillet029
  Base = -> Fillet028 [Edge51,Edge54]
  BaseFeature = -> Fillet028
  Radius = 3
  SupportTransform = false
  UseAllEdges = false
FEATURE [PartDesign::Fillet] Fillet030  label="Fillet-extender_main_curvature"
  Base = -> Fillet029 [Edge176,Edge209]
  BaseFeature = -> Fillet029
  Radius = 10
  SupportTransform = false
  UseAllEdges = false
FEATURE [PartDesign::Fillet] Fillet031  label="Fillet-bearing_face"
  Base = -> Fillet030 [Face16]
  BaseFeature = -> Fillet030
  Radius = 0.4
  SupportTransform = false
  UseAllEdges = false
FEATURE [PartDesign::Fillet] Fillet032  label="Fillet-bearing_face_mirror"
  Base = -> Fillet031 [Face28]
  BaseFeature = -> Fillet031
  Radius = 0.4
  SupportTransform = false
  UseAllEdges = false
FEATURE [PartDesign::Fillet] Fillet033
  Base = -> Fillet032 [Face96,Face112]
  BaseFeature = -> Fillet032
  Radius = 1
  SupportTransform = false
  UseAllEdges = false
FEATURE [PartDesign::Fillet] Fillet034
  Base = -> Fillet033 [Face119,Face4]
  BaseFeature = -> Fillet033
  Radius = 0.4
  SupportTransform = false
  UseAllEdges = false
FEATURE [Sketcher::SketchObject] Sketch098
  ExternalGeometry = -> [Fillet021]
  FullyConstrained = true
  MapMode = 5
  Placement = pos=(0,0,8) rot=(0,0,1;0rad)
  Support = -> [Fillet034]
  sketch-geometry (8):
    g0: ArcOfCircle CenterX=-2e-16 CenterY=-40 CenterZ=0 NormalX=0 NormalY=0 NormalZ=1 AngleXU=0 Radius=6 StartAngle=-1.8e-15 EndAngle=3.14159
    g1: ArcOfCircle CenterX=0 CenterY=-80 CenterZ=0 NormalX=0 NormalY=0 NormalZ=1 AngleXU=0 Radius=6 StartAngle=3.14159 EndAngle=6.28319
    g2: LineSegment StartX=-6 StartY=-40 StartZ=0 EndX=-6 EndY=-80 EndZ=0
    g3: LineSegment StartX=6 StartY=-80 StartZ=0 EndX=6 EndY=-40 EndZ=0
    g4: ArcOfCircle CenterX=0 CenterY=-120 CenterZ=0 NormalX=0 NormalY=0 NormalZ=1 AngleXU=0 Radius=6 StartAngle=4e-16 EndAngle=3.14159
    g5: ArcOfCircle CenterX=0 CenterY=-140 CenterZ=0 NormalX=0 NormalY=0 NormalZ=1 AngleXU=0 Radius=6 StartAngle=3.14159 EndAngle=6.28319
    g6: LineSegment StartX=-6 StartY=-120 StartZ=0 EndX=-6 EndY=-140 EndZ=0
    g7: LineSegment StartX=6 StartY=-140 StartZ=0 EndX=6 EndY=-120 EndZ=0
  constraints (20):
    c: Tangent(g0,g2) = -1.5708
    c: Tangent(g2,g1) = -1.5708
    c: Tangent(g1,g3) = -1.5708
    c: Tangent(g3,g0) = -1.5708
    c: Equal(g0,g1)
    c: DistanceX(g-3,g0) = 11
    c: Diameter(g1) = 12
    c: DistanceY(g0) = -40
    c: DistanceY(g2,g2) = 40
    c: Tangent(g4,g6) = -1.5708
    c: Tangent(g6,g5) = -1.5708
    c: Tangent(g5,g7) = -1.5708
    c: Tangent(g7,g4) = -1.5708
    c: Equal(g4,g5)
    c: PointOnObject(g4,g-2)
    c: PointOnObject(g5,g-2)
    c: DistanceY(g6,g6) = 20
    c: Diameter(g5) = 12
    c: DistanceY(g4,g1) = 40
    c: PointOnObject(g1,g-2)
FEATURE [PartDesign::Pocket] Pocket051
  BaseFeature = -> Fillet034
  Direction = (0,0,-1)
  Length = 5
  Length2 = 5
  Profile = -> Sketch098
  ReferenceAxis = -> Sketch098 [N_Axis]
  Type = 0
FEATURE [Sketcher::SketchObject] Sketch100
  FullyConstrained = false
  MapMode = 5
  Placement = pos=(0,0,8) rot=(0,0,1;0rad)
  Support = -> [Pocket051]
  sketch-geometry (1):
    g0: Circle CenterX=0 CenterY=-207 CenterZ=0 NormalX=0 NormalY=0 NormalZ=1 AngleXU=0 Radius=6
  constraints (2):
    c: PointOnObject(g0,g-2)
    c: Diameter(g0) = 12
FEATURE [PartDesign::Pocket] Pocket052  label="Pocket-extender_inset"
  BaseFeature = -> Pocket051
  Direction = (0,0,-1)
  Length = 5
  Length2 = 40
  Profile = -> Sketch100
  ReferenceAxis = -> Sketch100 [N_Axis]
  Type = 4
FEATURE [Sketcher::SketchObject] Sketch101
  FullyConstrained = false
  MapMode = 5
  Placement = pos=(-11,0,0) rot=(0.57735,-0.57735,-0.57735;2.0944rad)
  sketch-geometry (9):
    g0: LineSegment StartX=25 StartY=59.0924 StartZ=0 EndX=25 EndY=55.5221 EndZ=0
    g1: LineSegment StartX=25 StartY=59.0924 StartZ=0 EndX=28.3551 EndY=57.8713 EndZ=0
    g2: ArcOfCircle CenterX=27.5 CenterY=55.5221 CenterZ=0 NormalX=0 NormalY=0 NormalZ=1 AngleXU=0 Radius=2.5 StartAngle=1.22173 EndAngle=3.14159
    g3: ArcOfCircle CenterX=97 CenterY=27.5657 CenterZ=0 NormalX=0 NormalY=0 NormalZ=1 AngleXU=0 Radius=5 StartAngle=2.0166e-12 EndAngle=1.22173
    g4: ArcOfCircle CenterX=114.5 CenterY=23.8566 CenterZ=0 NormalX=0 NormalY=0 NormalZ=1 AngleXU=0 Radius=2.5 StartAngle=1.22173 EndAngle=3.14159
    g5: LineSegment StartX=98.7101 StartY=32.2641 StartZ=0 EndX=102 EndY=31.0667 EndZ=0
    g6: LineSegment StartX=102 StartY=31.0667 StartZ=0 EndX=102 EndY=27.5657 EndZ=0
    g7: LineSegment StartX=112 StartY=23.8566 StartZ=0 EndX=112 EndY=27.427 EndZ=0
    g8: LineSegment StartX=112 StartY=27.427 StartZ=0 EndX=115.355 EndY=26.2059 EndZ=0
  constraints (18):
    c: Coincident(g1,g0)
    c: Coincident(g0,g2)
    c: Coincident(g1,g2)
    c: Diameter(g2) = 5
    c: Coincident(g5,g3)
    c: Coincident(g6,g5)
    c: Coincident(g6,g3)
    c: Coincident(g7,g4)
    c: Coincident(g8,g7)
    c: Coincident(g8,g4)
    c: Diameter(g3) = 10
    c: Angle(g3) = 1.22173
    c: Equal(g6,g5)
    c: Equal(g8,g7)
    c: Angle(g4) = 1.91986
    c: Equal(g0,g1)
    c: Angle(g2) = 1.91986
    c: Equal(g4,g2)
FEATURE [PartDesign::Pad] Pad042
  BaseFeature = -> Pocket052
  Direction = (-1,0,0)
  Length = 22
  Length2 = 10
  Profile = -> Sketch101
  ReferenceAxis = -> Sketch101 [N_Axis]
  Reversed = true
  Type = 0
FEATURE [Sketcher::SketchObject] Sketch102
  FullyConstrained = true
  MapMode = 5
  Placement = pos=(0,0,0) rot=(1,0,0;1.5708rad)
  Support = -> [XZ_Plane021]
  sketch-geometry (16):
    g0: LineSegment StartX=-3.8476e-12 StartY=-10.8333 StartZ=0 EndX=4 EndY=-10.8333 EndZ=0
    g1: LineSegment StartX=4 StartY=-10.8333 StartZ=0 EndX=4 EndY=-0.833334 EndZ=0
    g2: LineSegment StartX=4 StartY=-0.833334 StartZ=0 EndX=-15 EndY=-0.833334 EndZ=0
    g3: LineSegment StartX=-15 StartY=-0.833334 StartZ=0 EndX=-15 EndY=0.833334 EndZ=0
    g4: LineSegment StartX=-15 StartY=0.833334 StartZ=0 EndX=4 EndY=0.833334 EndZ=0
    g5: LineSegment StartX=4 StartY=0.833334 StartZ=0 EndX=4 EndY=10.8333 EndZ=0
    g6: LineSegment StartX=4 StartY=10.8333 StartZ=0 EndX=0 EndY=10.8333 EndZ=0
    g7: LineSegment StartX=0 StartY=10.8333 StartZ=0 EndX=0 EndY=0.853333 EndZ=0
    g8: LineSegment StartX=0 StartY=0.853333 StartZ=0 EndX=-19 EndY=0.853333 EndZ=0
    g9: LineSegment StartX=-19 StartY=0.853333 StartZ=0 EndX=-19 EndY=-0.853333 EndZ=0
    g10: LineSegment StartX=-19 StartY=-0.853333 StartZ=0 EndX=-3.8476e-12 EndY=-0.853333 EndZ=0
    g11: LineSegment StartX=-3.8476e-12 StartY=-0.853333 StartZ=0 EndX=-3.8476e-12 EndY=-10.8333 EndZ=0
    g12: LineSegment StartX=-19 StartY=0.853333 StartZ=0 EndX=-15 EndY=-0.833334 EndZ=0
    g13: LineSegment StartX=-15 StartY=0.833334 StartZ=0 EndX=-19 EndY=-0.853333 EndZ=0
    g14: LineSegment StartX=0 StartY=0.853333 StartZ=0 EndX=0 EndY=0 EndZ=0
    g15: LineSegment StartX=0 StartY=0 StartZ=0 EndX=-3.8476e-12 EndY=-0.853333 EndZ=0
  constraints (44):
    c: Horizontal(g0)
    c: Coincident(g1,g0)
    c: Vertical(g1)
    c: Coincident(g2,g1)
    c: Horizontal(g2)
    c: Coincident(g3,g2)
    c: Vertical(g3)
    c: Horizontal(g4)
    c: Coincident(g5,g4)
    c: Vertical(g5)
    c: Coincident(g6,g5)
    c: PointOnObject(g6,g-2)
    c: Horizontal(g6)
    c: Coincident(g7,g6)
    c: Vertical(g7)
    c: Coincident(g8,g7)
    c: Horizontal(g8)
    c: Coincident(g9,g8)
    c: Vertical(g9)
    c: Coincident(g10,g9)
    c: Horizontal(g10)
    c: Coincident(g11,g10)
    c: Vertical(g11)
    c: DistanceY(g3,g3) = 1.66667
    c: Coincident(g3,g4)
    c: DistanceY(g9,g9) = 1.70667
    c: Coincident(g12,g8)
    c: Coincident(g12,g2)
    c: Coincident(g13,g3)
    c: Coincident(g13,g9)
    c: Equal(g13,g12)
    c: DistanceX(g9,g2) = 4
    c: DistanceX(g0,g0) = 4
    c: Equal(g0,g6)
    c: Equal(g1,g5)
    c: DistanceY(g1,g1) = 10
    c: DistanceX(g2,g10) = 15
    c: Coincident(g11,g0)
    c: Vertical(g1,g4)
    c: Coincident(g14,g7)
    c: Coincident(g14,g-1)
    c: Coincident(g15,g14)
    c: Coincident(g15,g10)
    c: Equal(g15,g14)
FEATURE [PartDesign::Pad] Pad043  label="Pad-main_body002"
  Direction = (0,-1,-2e-16)
  Length = 93
  Length2 = 10
  Placement = pos=(0,0,0) rot=(1,0,0;1.5708rad)
  Profile = -> Sketch102
  ReferenceAxis = -> Sketch102 [N_Axis]
  Type = 0
FEATURE [Sketcher::SketchObject] Sketch103
  ExternalGeometry = -> [Pad043]
  FullyConstrained = true
  MapMode = 5
  Placement = pos=(0,2e-16,0.853333) rot=(0,0,1;3.14159rad)
  Support = -> [Pad043]
  sketch-geometry (14):
    g0: ArcOfCircle CenterX=5.5 CenterY=23 CenterZ=0 NormalX=0 NormalY=0 NormalZ=1 AngleXU=0 Radius=1.7 StartAngle=1.5708 EndAngle=4.71239
    g1: ArcOfCircle CenterX=11.5 CenterY=23 CenterZ=0 NormalX=0 NormalY=0 NormalZ=1 AngleXU=0 Radius=1.7 StartAngle=4.71239 EndAngle=7.85398
    g2: LineSegment StartX=5.5 StartY=21.3 StartZ=0 EndX=11.5 EndY=21.3 EndZ=0
    g3: LineSegment StartX=11.5 StartY=24.7 StartZ=0 EndX=5.5 EndY=24.7 EndZ=0
    g4: ArcOfCircle CenterX=5.5 CenterY=48 CenterZ=0 NormalX=0 NormalY=0 NormalZ=1 AngleXU=0 Radius=1.7 StartAngle=1.5708 EndAngle=4.71239
    g5: ArcOfCircle CenterX=11.5 CenterY=48 CenterZ=0 NormalX=0 NormalY=0 NormalZ=1 AngleXU=0 Radius=1.7 StartAngle=4.71239 EndAngle=7.85398
    g6: LineSegment StartX=5.5 StartY=46.3 StartZ=0 EndX=11.5 EndY=46.3 EndZ=0
    g7: LineSegment StartX=11.5 StartY=49.7 StartZ=0 EndX=5.5 EndY=49.7 EndZ=0
    g8: ArcOfCircle CenterX=5.5 CenterY=73 CenterZ=0 NormalX=0 NormalY=0 NormalZ=1 AngleXU=0 Radius=1.7 StartAngle=1.5708 EndAngle=4.71239
    g9: ArcOfCircle CenterX=11.5 CenterY=73 CenterZ=0 NormalX=0 NormalY=0 NormalZ=1 AngleXU=0 Radius=1.7 StartAngle=4.71239 EndAngle=7.85398
    g10: LineSegment StartX=5.5 StartY=71.3 StartZ=0 EndX=11.5 EndY=71.3 EndZ=0
    g11: LineSegment StartX=11.5 StartY=74.7 StartZ=0 EndX=5.5 EndY=74.7 EndZ=0
    g12: LineSegment StartX=11.5 StartY=73 StartZ=0 EndX=11.5 EndY=48 EndZ=0
    g13: LineSegment StartX=11.5 StartY=48 StartZ=0 EndX=11.5 EndY=23 EndZ=0
  constraints (34):
    c: Tangent(g0,g2) = -1.5708
    c: Tangent(g2,g1) = -1.5708
    c: Tangent(g1,g3) = -1.5708
    c: Tangent(g3,g0) = -1.5708
    c: Equal(g0,g1)
    c: Horizontal(g2)
    c: Diameter(g1) = 3.4
    c: DistanceX(g2,g2) = 6
    c: DistanceX(g1,g-3) = 7.5
    c: Tangent(g4,g6) = -1.5708
    c: Tangent(g6,g5) = -1.5708
    c: Tangent(g5,g7) = -1.5708
    c: Tangent(g7,g4) = -1.5708
    c: Equal(g4,g5)
    c: Tangent(g8,g10) = -1.5708
    c: Tangent(g10,g9) = -1.5708
    c: Tangent(g9,g11) = -1.5708
    c: Tangent(g11,g8) = -1.5708
    c: Equal(g8,g9)
    c: Equal(g9,g5)
    c: Equal(g5,g1)
    c: Horizontal(g5,g4)
    c: Horizontal(g9,g8)
    c: Vertical(g8,g4)
    c: Vertical(g4,g0)
    c: Coincident(g12,g9)
    c: Coincident(g12,g5)
    c: Vertical(g12)
    c: Coincident(g13,g5)
    c: Coincident(g13,g1)
    c: Vertical(g13)
    c: Equal(g12,g13)
    c: DistanceY(g12,g12) = 25
    c: DistanceY(g9,g-3) = 20
FEATURE [PartDesign::Pad] Pad044  label="Pad-slots002"
  BaseFeature = -> Pad043
  Direction = (0,-2e-16,1)
  Length = 10
  Length2 = 10
  Placement = pos=(0,0,0) rot=(1,0,0;1.5708rad)
  Profile = -> Sketch103
  ReferenceAxis = -> Sketch103 [N_Axis]
  Type = 0
FEATURE [PartDesign::Mirrored] Mirrored006  label="Mirrored-slots_top_to_bottom002"
  BaseFeature = -> Pad044
  MirrorPlane = -> XY_Plane021
  Originals = -> [Pad044]
  Placement = pos=(0,0,0) rot=(1,0,0;1.5708rad)
FEATURE [Sketcher::SketchObject] Sketch104
  ExternalGeometry = -> [Mirrored006]
  FullyConstrained = true
  MapMode = 5
  Placement = pos=(0,-2e-16,-0.833334) rot=(0,0,1;3.14159rad)
  Support = -> [Mirrored006]
  sketch-geometry (5):
    g0: Circle CenterX=7.5 CenterY=23 CenterZ=0 NormalX=0 NormalY=0 NormalZ=1 AngleXU=0 Radius=1.69
    g1: Circle CenterX=7.5 CenterY=48 CenterZ=0 NormalX=0 NormalY=0 NormalZ=1 AngleXU=0 Radius=1.69
    g2: Circle CenterX=7.5 CenterY=73 CenterZ=0 NormalX=0 NormalY=0 NormalZ=1 AngleXU=0 Radius=1.69
    g3: LineSegment StartX=7.5 StartY=73 StartZ=0 EndX=7.5 EndY=48 EndZ=0
    g4: LineSegment StartX=7.5 StartY=48 StartZ=0 EndX=7.5 EndY=23 EndZ=0
  constraints (13):
    c: Equal(g2,g1)
    c: Equal(g2,g0)
    c: Diameter(g2) = 3.38
    c: Coincident(g3,g2)
    c: Coincident(g3,g1)
    c: Vertical(g3)
    c: Coincident(g4,g1)
    c: Coincident(g4,g0)
    c: Vertical(g4)
    c: DistanceY(g3,g3) = 25
    c: DistanceX(g0,g-3) = 7.5
    c: Equal(g3,g4)
    c: DistanceY(g2,g-3) = 20
FEATURE [PartDesign::Pad] Pad045  label="Pad-inside_holes002"
  BaseFeature = -> Mirrored006
  Direction = (0,-2e-16,1)
  Length = 10
  Length2 = 10
  Placement = pos=(0,0,0) rot=(1,0,0;1.5708rad)
  Profile = -> Sketch104
  ReferenceAxis = -> Sketch104 [N_Axis]
  Type = 0
FEATURE [Sketcher::SketchObject] Sketch105
  FullyConstrained = true
  MapMode = 5
  Placement = pos=(0,0,0) rot=(0.707107,0,-0.707107;3.14159rad)
  Support = -> [Pad045]
  sketch-geometry (1):
    g0: Circle CenterX=0 CenterY=3 CenterZ=0 NormalX=0 NormalY=0 NormalZ=1 AngleXU=0 Radius=4.55
  constraints (3):
    c: PointOnObject(g0,g-2)
    c: Diameter(g0) = 9.1
    c: DistanceY(g-1,g0) = 3
FEATURE [PartDesign::Pad] Pad046  label="Pad-shaft_female001"
  BaseFeature = -> Pad045
  Direction = (-1,0,-2e-16)
  Length = 19
  Length2 = 10
  Placement = pos=(0,0,0) rot=(1,0,0;1.5708rad)
  Profile = -> Sketch105
  ReferenceAxis = -> Sketch105 [N_Axis]
  Type = 0
FEATURE [Sketcher::SketchObject] Sketch106
  ExternalGeometry = -> [Pad046]
  FullyConstrained = true
  MapMode = 5
  Placement = pos=(0,0,0) rot=(-1,0,0;1.5708rad)
  Support = -> [Pad046]
  sketch-geometry (4):
    g0: LineSegment StartX=-3.8476e-12 StartY=10.8333 StartZ=0 EndX=4 EndY=10.8333 EndZ=0
    g1: LineSegment StartX=4 StartY=10.8333 StartZ=0 EndX=4 EndY=-10.8333 EndZ=0
    g2: LineSegment StartX=4 StartY=-10.8333 StartZ=0 EndX=-3.8476e-12 EndY=-10.8333 EndZ=0
    g3: LineSegment StartX=-3.8476e-12 StartY=-10.8333 StartZ=0 EndX=-3.8476e-12 EndY=10.8333 EndZ=0
  constraints (10):
    c: Coincident(g0,g1)
    c: Coincident(g1,g2)
    c: Coincident(g2,g3)
    c: Coincident(g3,g0)
    c: Horizontal(g0)
    c: Horizontal(g2)
    c: Vertical(g1)
    c: Vertical(g3)
    c: Coincident(g0,g-3)
    c: Coincident(g1,g-4)
FEATURE [PartDesign::Pad] Pad047  label="Pad-gap_extension001"
  BaseFeature = -> Pad046
  Direction = (0,1,2e-16)
  Length = 10
  Length2 = 10
  Placement = pos=(0,0,0) rot=(1,0,0;1.5708rad)
  Profile = -> Sketch106
  ReferenceAxis = -> Sketch106 [N_Axis]
  Type = 0
FEATURE [Sketcher::SketchObject] Sketch107
  ExternalGeometry = -> [Pad047]
  FullyConstrained = true
  MapMode = 5
  Placement = pos=(4,0,0) rot=(0.707107,0,0.707107;3.14159rad)
  Support = -> [Pad047]
  sketch-geometry (6):
    g0: ArcOfCircle CenterX=0 CenterY=3 CenterZ=0 NormalX=0 NormalY=0 NormalZ=1 AngleXU=0 Radius=4.5 StartAngle=1.75706 EndAngle=7.66772
    g1: GeomPoint X=-0.833334 Y=7.42217 Z=0
    g2: GeomPoint X=0.833334 Y=7.42217 Z=0
    g3: LineSegment StartX=-0.833334 StartY=7.42217 StartZ=0 EndX=-0.833334 EndY=8.42217 EndZ=0
    g4: LineSegment StartX=-0.833334 StartY=8.42217 StartZ=0 EndX=0.833334 EndY=8.42217 EndZ=0
    g5: LineSegment StartX=0.833334 StartY=8.42217 StartZ=0 EndX=0.833334 EndY=7.42217 EndZ=0
  constraints (15):
    c: PointOnObject(g0,g-2)
    c: DistanceY(g0) = 3
    c: Diameter(g0) = 9
    c: PointOnObject(g1,g-3)
    c: PointOnObject(g2,g-4)
    c: Coincident(g3,g1)
    c: PointOnObject(g3,g-3)
    c: Coincident(g4,g3)
    c: PointOnObject(g4,g-4)
    c: Horizontal(g4)
    c: Coincident(g5,g4)
    c: Coincident(g5,g2)
    c: Coincident(g0,g5)
    c: Coincident(g0,g3)
    c: DistanceY(g5,g5) = 1
FEATURE [PartDesign::Pocket] Pocket054  label="Pocket-shaft_male001"
  BaseFeature = -> Pad047
  Direction = (-1,0,2e-16)
  Length = 19
  Length2 = 5
  Placement = pos=(0,0,0) rot=(1,0,0;1.5708rad)
  Profile = -> Sketch107
  ReferenceAxis = -> Sketch107 [N_Axis]
  Type = 0
FEATURE [PartDesign::Fillet] Fillet035
  Base = -> Pocket054 [Edge69,Edge125,Edge59,Edge64,Edge62]
  BaseFeature = -> Pocket054
  Placement = pos=(0,0,0) rot=(1,0,0;1.5708rad)
  Radius = 0.45
  SupportTransform = false
  UseAllEdges = false
FEATURE [PartDesign::Fillet] Fillet036
  Base = -> Fillet035 [Edge64,Edge42]
  BaseFeature = -> Fillet035
  Placement = pos=(0,0,0) rot=(1,0,0;1.5708rad)
  Radius = 1
  SupportTransform = false
  UseAllEdges = false
FEATURE [PartDesign::Fillet] Fillet037
  Base = -> Fillet036 [Edge140,Edge141,Edge138,Edge132]
  BaseFeature = -> Fillet036
  Placement = pos=(0,0,0) rot=(1,0,0;1.5708rad)
  Radius = 1
  SupportTransform = false
  UseAllEdges = false
FEATURE [PartDesign::Fillet] Fillet038
  Base = -> Fillet037 [Edge52,Edge47,Edge11,Edge12,Edge1,Edge2,Edge6,Edge101,Edge115,Edge114,Edge133,Edge66,Edge64,Edge65,Edge67]
  BaseFeature = -> Fillet037
  Placement = pos=(0,0,0) rot=(1,0,0;1.5708rad)
  Radius = 1.5
  SupportTransform = false
  UseAllEdges = false
FEATURE [PartDesign::Fillet] Fillet039
  Base = -> Fillet038 [Edge103,Edge87,Edge185,Edge184,Edge183,Edge157]
  BaseFeature = -> Fillet038
  Placement = pos=(0,0,0) rot=(1,0,0;1.5708rad)
  Radius = 0.45
  SupportTransform = false
  UseAllEdges = false
FEATURE [PartDesign::Fillet] Fillet040
  Base = -> Fillet039 [Face53,Face54,Face55,Face49,Face50,Face51,Face45,Face46,Face47,Face25,Face26,Face23,Face29,Face30,Face27,Face33,Face34,Face31,Face52,Face32,Face28,Face48,Face44,Face24]
  BaseFeature = -> Fillet039
  Placement = pos=(0,0,0) rot=(1,0,0;1.5708rad)
  Radius = 0.5
  SupportTransform = false
  UseAllEdges = false
FEATURE [PartDesign::Fillet] Fillet041
  Base = -> Fillet040 [Face87,Face85,Face86]
  BaseFeature = -> Fillet040
  Placement = pos=(0,0,0) rot=(1,0,0;1.5708rad)
  Radius = 0.5
  SupportTransform = false
  UseAllEdges = false
FEATURE [PartDesign::Body] Body022  label="Body-v3.1_slicer001"
  Group = -> [Sketch102,Pad043,Sketch103,Pad044,Mirrored006,Sketch104,Pad045,Sketch105,Pad046,Sketch106,Pad047,Sketch107,Pocket054,Fillet035,Fillet036,Fillet037,Fillet038,Fillet039,Fillet040,Fillet041]
  Origin = -> Origin021
  Placement = pos=(-93.7453,-9.38195,-38.8423) rot=(-0.511946,0.823177,-0.245541;2.96464rad)
  Tip = -> Fillet041
FEATURE [Sketcher::SketchObject] Sketch108
  ExternalGeometry = -> [Pocket035]
  FullyConstrained = true
  MapMode = 5
  Placement = pos=(0,0,0) rot=(0.57735,-0.57735,-0.57735;2.0944rad)
  Support = -> [Pocket035]
  sketch-geometry (1):
    g0: Circle CenterX=90 CenterY=2.5 CenterZ=0 NormalX=0 NormalY=0 NormalZ=1 AngleXU=0 Radius=5.75
  constraints (2):
    c: Coincident(g0,g-3)
    c: Diameter(g0) = 11.5
FEATURE [PartDesign::Pad] Pad048
  BaseFeature = -> Pocket035
  Direction = (-1,0,0)
  Length = 166
  Length2 = 10
  Profile = -> Sketch108
  ReferenceAxis = -> Sketch108 [N_Axis]
  Reversed = true
  Type = 0
FEATURE [Sketcher::SketchObject] Sketch109
  ExternalGeometry = -> [Pad048]
  FullyConstrained = true
  MapMode = 5
  Placement = pos=(177,0,0) rot=(0.57735,0.57735,0.57735;2.0944rad)
  Support = -> [Pad048]
  sketch-geometry (2):
    g0: Circle CenterX=-90 CenterY=2.5 CenterZ=0 NormalX=0 NormalY=0 NormalZ=1 AngleXU=0 Radius=3.8
    g1: Circle CenterX=-90 CenterY=2.5 CenterZ=0 NormalX=0 NormalY=0 NormalZ=1 AngleXU=0 Radius=6
  constraints (4):
    c: Coincident(g0,g-3)
    c: Coincident(g1,g0)
    c: Diameter(g0) = 7.6
    c: Diameter(g1) = 12
FEATURE [PartDesign::Pocket] Pocket055
  BaseFeature = -> Pad048
  Direction = (-1,0,0)
  Length = 11
  Length2 = 5
  Profile = -> Sketch109
  ReferenceAxis = -> Sketch109 [N_Axis]
  Type = 0
FEATURE [Sketcher::SketchObject] Sketch110
  ExternalGeometry = -> [Pocket055]
  FullyConstrained = true
  MapMode = 5
  Placement = pos=(166,0,0) rot=(0.57735,0.57735,0.57735;2.0944rad)
  Support = -> [Pocket055]
  sketch-geometry (1):
    g0: Circle CenterX=-90 CenterY=2.5 CenterZ=0 NormalX=0 NormalY=0 NormalZ=1 AngleXU=0 Radius=4.5
  constraints (2):
    c: Coincident(g0,g-3)
    c: PointOnObject(g-3,g0)
FEATURE [PartDesign::Pad] Pad049  label="Pad-bearing_inside_retainer"
  BaseFeature = -> Pocket055
  Direction = (1,0,0)
  Length = 4.5
  Length2 = 10
  Profile = -> Sketch110
  ReferenceAxis = -> Sketch110 [N_Axis]
  Type = 0
FEATURE [Sketcher::SketchObject] Sketch112
  FullyConstrained = true
  MapMode = 5
  Support = -> [XY_Plane022]
  sketch-geometry (2):
    g0: Circle CenterX=0 CenterY=0 CenterZ=0 NormalX=0 NormalY=0 NormalZ=1 AngleXU=0 Radius=3.95
    g1: Circle CenterX=0 CenterY=0 CenterZ=0 NormalX=0 NormalY=0 NormalZ=1 AngleXU=0 Radius=11
  constraints (4):
    c: Coincident(g0,g-1)
    c: Coincident(g1,g0)
    c: Diameter(g0) = 7.9
    c: Diameter(g1) = 22
FEATURE [PartDesign::Pad] Pad050
  Direction = (0,0,1)
  Length = 7
  Length2 = 10
  Profile = -> Sketch112
  ReferenceAxis = -> Sketch112 [N_Axis]
  Type = 0
FEATURE [PartDesign::Body] Body023  label="Body-bearing003"
  Group = -> [Sketch112,Pad050]
  Origin = -> Origin022
  Placement = pos=(-125.413,-93.1724,-47.4092) rot=(0.443141,-0.743648,0.500613;1.76697rad)
  Tip = -> Pad050
FEATURE [Sketcher::SketchObject] Sketch113
  ExternalGeometry = -> [Pad049]
  FullyConstrained = true
  MapMode = 5
  Placement = pos=(177,0,0) rot=(0.57735,0.57735,0.57735;2.0944rad)
  Support = -> [Pad049]
  sketch-geometry (2):
    g0: GeomPoint X=-93.8 Y=2.5 Z=0
    g1: Circle CenterX=-90 CenterY=2.5 CenterZ=0 NormalX=0 NormalY=0 NormalZ=1 AngleXU=0 Radius=3.8
  constraints (4):
    c: PointOnObject(g0,g-3)
    c: Horizontal(g0,g-3)
    c: Coincident(g1,g-3)
    c: PointOnObject(g0,g1)
FEATURE [PartDesign::Pocket] Pocket056  label="Pocket-remove_bearing_shaft"
  BaseFeature = -> Pad049
  Direction = (-1,0,0)
  Length = 6.5
  Length2 = 5
  Profile = -> Sketch113
  ReferenceAxis = -> Sketch113 [N_Axis]
  Type = 0
FEATURE [Sketcher::SketchObject] Sketch114
  ExternalGeometry = -> [Pocket056]
  FullyConstrained = true
  MapMode = 5
  Placement = pos=(170.5,0,0) rot=(0.57735,0.57735,0.57735;2.0944rad)
  Support = -> [Pocket056]
  sketch-geometry (2):
    g0: GeomPoint X=-93.8 Y=2.5 Z=0
    g1: Circle CenterX=-90 CenterY=2.5 CenterZ=0 NormalX=0 NormalY=0 NormalZ=1 AngleXU=0 Radius=3.8
  constraints (4):
    c: PointOnObject(g0,g-3)
    c: Horizontal(g0,g-3)
    c: Coincident(g1,g-3)
    c: PointOnObject(g0,g1)
FEATURE [PartDesign::Pad] Pad051  label="Pad-bearing_shaft"
  BaseFeature = -> Pocket056
  Direction = (1,0,0)
  Length = 7.2
  Length2 = 10
  Profile = -> Sketch114
  ReferenceAxis = -> Sketch114 [N_Axis]
  Type = 0
FEATURE [Sketcher::SketchObject] Sketch115
  ExternalGeometry = -> [Pad051]
  FullyConstrained = true
  MapMode = 5
  Placement = pos=(177.7,0,0) rot=(0.57735,0.57735,0.57735;2.0944rad)
  Support = -> [Pad051]
  sketch-geometry (2):
    g0: GeomPoint X=-93.8 Y=2.5 Z=0
    g1: Circle CenterX=-90 CenterY=2.5 CenterZ=0 NormalX=0 NormalY=0 NormalZ=1 AngleXU=0 Radius=5.75
  constraints (4):
    c: PointOnObject(g0,g-3)
    c: Horizontal(g0,g-3)
    c: Coincident(g1,g-3)
    c: Diameter(g1) = 11.5
FEATURE [PartDesign::Pad] Pad052  label="Pad-bearing_retainer"
  BaseFeature = -> Pad051
  Direction = (1,0,0)
  Length = 2
  Length2 = 10
  Profile = -> Sketch115
  ReferenceAxis = -> Sketch115 [N_Axis]
  Type = 0
FEATURE [Sketcher::SketchObject] Sketch116
  ExternalGeometry = -> [Pad052]
  FullyConstrained = true
  MapMode = 5
  Placement = pos=(179.7,0,0) rot=(0.57735,0.57735,0.57735;2.0944rad)
  Support = -> [Pad052]
  sketch-geometry (1):
    g0: Circle CenterX=-90 CenterY=2.5 CenterZ=0 NormalX=0 NormalY=0 NormalZ=1 AngleXU=0 Radius=2.725
  constraints (2):
    c: Coincident(g0,g-3)
    c: Diameter(g0) = 5.45
FEATURE [PartDesign::Pocket] Pocket057  label="Pocket-screw_head"
  BaseFeature = -> Pad052
  Direction = (-1,0,0)
  Length = 2.9
  Length2 = 5
  Profile = -> Sketch116
  ReferenceAxis = -> Sketch116 [N_Axis]
  Type = 0
FEATURE [Sketcher::SketchObject] Sketch111
  ExternalGeometry = -> [Pocket055]
  FullyConstrained = true
  MapMode = 5
  Placement = pos=(166,0,0) rot=(0.57735,0.57735,0.57735;2.0944rad)
  Support = -> [Pocket057]
  sketch-geometry (10):
    g0: LineSegment StartX=-88.4123 StartY=5.25 StartZ=0 EndX=-91.5877 EndY=5.25 EndZ=0
    g1: LineSegment StartX=-91.5877 StartY=5.25 StartZ=0 EndX=-93.1754 EndY=2.5 EndZ=0
    g2: LineSegment StartX=-93.1754 StartY=2.5 StartZ=0 EndX=-91.5877 EndY=-0.25 EndZ=0
    g3: LineSegment StartX=-91.5877 StartY=-0.25 StartZ=0 EndX=-88.4123 EndY=-0.25 EndZ=0
    g4: LineSegment StartX=-88.4123 StartY=-0.25 StartZ=0 EndX=-86.8246 EndY=2.5 EndZ=0
    g5: LineSegment StartX=-86.8246 StartY=2.5 StartZ=0 EndX=-88.4123 EndY=5.25 EndZ=0
    g6: Circle CenterX=-90 CenterY=2.5 CenterZ=0 NormalX=0 NormalY=0 NormalZ=1 AngleXU=0 Radius=3.17543
    g7: LineSegment StartX=-91.5877 StartY=5.25 StartZ=0 EndX=-101.588 EndY=5.25 EndZ=0
    g8: LineSegment StartX=-101.588 StartY=5.25 StartZ=0 EndX=-101.588 EndY=-0.25 EndZ=0
    g9: LineSegment StartX=-101.588 StartY=-0.25 StartZ=0 EndX=-91.5877 EndY=-0.25 EndZ=0
  constraints (24):
    c: Coincident(g0,g1)
    c: Coincident(g1,g2)
    c: Coincident(g2,g3)
    c: Coincident(g3,g4)
    c: Coincident(g4,g5)
    c: Coincident(g5,g0)
    c: Equal(g0, g1-g5) x5
    c: PointOnObject(g0,g6)
    c: PointOnObject(g1,g6)
    c: PointOnObject(g2,g6)
    c: PointOnObject(g3,g6)
    c: PointOnObject(g4,g6)
    c: PointOnObject(g5,g6)
    c: Coincident(g6,g-3)
    c: Horizontal(g0)
    c: Coincident(g7,g0)
    c: Horizontal(g7)
    c: Coincident(g8,g7)
    c: Vertical(g8)
    c: Coincident(g9,g8)
    c: Coincident(g9,g2)
    c: Horizontal(g9)
    c: DistanceY(g8,g8) = 5.5
    c: DistanceX(g7,g7) = 10
FEATURE [PartDesign::Pocket] Pocket058  label="Pocket-nut_profile"
  BaseFeature = -> Pocket057
  Direction = (-1,0,0)
  Length = 9
  Length2 = 5
  Profile = -> Sketch111
  ReferenceAxis = -> Sketch111 [N_Axis]
  Type = 0
FEATURE [Sketcher::SketchObject] Sketch117
  ExternalGeometry = -> [Pocket058]
  FullyConstrained = true
  MapMode = 5
  Placement = pos=(166,0,0) rot=(0.57735,0.57735,0.57735;2.0944rad)
  Support = -> [Pocket058]
  sketch-geometry (1):
    g0: Circle CenterX=-90 CenterY=2.5 CenterZ=0 NormalX=0 NormalY=0 NormalZ=1 AngleXU=0 Radius=5.75
  constraints (2):
    c: Coincident(g0,g-3)
    c: PointOnObject(g-3,g0)
FEATURE [PartDesign::Pad] Pad053  label="Pad-bury nut profile"
  BaseFeature = -> Pocket058
  Direction = (1,0,0)
  Length = 4
  Length2 = 10
  Profile = -> Sketch117
  ReferenceAxis = -> Sketch117 [N_Axis]
  Reversed = true
  Type = 0
FEATURE [Sketcher::SketchObject] Sketch118
  ExternalGeometry = -> [Pad053]
  FullyConstrained = true
  MapMode = 5
  Placement = pos=(176.8,0,0) rot=(0.57735,0.57735,0.57735;2.0944rad)
  Support = -> [Pad053]
  sketch-geometry (1):
    g0: Circle CenterX=-90 CenterY=2.5 CenterZ=0 NormalX=0 NormalY=0 NormalZ=1 AngleXU=0 Radius=1.5
  constraints (2):
    c: Coincident(g0,g-3)
    c: Diameter(g0) = 3
FEATURE [PartDesign::Pocket] Pocket059
  BaseFeature = -> Pad053
  Direction = (-1,0,0)
  Length = 110
  Length2 = 5
  Profile = -> Sketch118
  ReferenceAxis = -> Sketch118 [N_Axis]
  Type = 0
FEATURE [Sketcher::SketchObject] Sketch119
  FullyConstrained = true
  MapMode = 5
  Support = -> [XY_Plane023]
  sketch-geometry (1):
    g0: Circle CenterX=0 CenterY=0 CenterZ=0 NormalX=0 NormalY=0 NormalZ=1 AngleXU=0 Radius=2.675
  constraints (2):
    c: Coincident(g0,g-1)
    c: Diameter(g0) = 5.35
FEATURE [PartDesign::Pad] Pad054
  Direction = (0,0,1)
  Length = 2.9
  Length2 = 10
  Profile = -> Sketch119
  ReferenceAxis = -> Sketch119 [N_Axis]
  Type = 0
FEATURE [Sketcher::SketchObject] Sketch120
  FullyConstrained = true
  MapMode = 5
  Placement = pos=(0,0,2.9) rot=(0,0,1;0rad)
  Support = -> [Pad054]
  sketch-geometry (1):
    g0: Circle CenterX=0 CenterY=0 CenterZ=0 NormalX=0 NormalY=0 NormalZ=1 AngleXU=0 Radius=1.465
  constraints (2):
    c: Coincident(g0,g-1)
    c: Diameter(g0) = 2.93
FEATURE [PartDesign::Pad] Pad055
  BaseFeature = -> Pad054
  Direction = (0,0,1)
  Length = 20
  Length2 = 10
  Profile = -> Sketch120
  ReferenceAxis = -> Sketch120 [N_Axis]
  Type = 0
FEATURE [Sketcher::SketchObject] Sketch121
  FullyConstrained = true
  MapMode = 5
  Placement = pos=(0,0,0) rot=(1,0,0;3.14159rad)
  Support = -> [Pad055]
  sketch-geometry (7):
    g0: LineSegment StartX=1.20378 StartY=0.695 StartZ=0 EndX=0 EndY=1.39 EndZ=0
    g1: LineSegment StartX=0 StartY=1.39 StartZ=0 EndX=-1.20378 EndY=0.695 EndZ=0
    g2: LineSegment StartX=-1.20378 StartY=0.695 StartZ=0 EndX=-1.20378 EndY=-0.695 EndZ=0
    g3: LineSegment StartX=-1.20378 StartY=-0.695 StartZ=0 EndX=1.122e-12 EndY=-1.39 EndZ=0
    g4: LineSegment StartX=1.122e-12 StartY=-1.39 StartZ=0 EndX=1.20378 EndY=-0.695 EndZ=0
    g5: LineSegment StartX=1.20378 StartY=-0.695 StartZ=0 EndX=1.20378 EndY=0.695 EndZ=0
    g6: Circle CenterX=0 CenterY=0 CenterZ=0 NormalX=0 NormalY=0 NormalZ=1 AngleXU=0 Radius=1.39
  constraints (16):
    c: Coincident(g0,g1)
    c: Coincident(g1,g2)
    c: Coincident(g2,g3)
    c: Coincident(g3,g4)
    c: Coincident(g4,g5)
    c: Coincident(g5,g0)
    c: Equal(g0, g1-g5) x5
    c: PointOnObject(g0,g6)
    c: PointOnObject(g1,g6)
    c: PointOnObject(g2,g6)
    c: PointOnObject(g3,g6)
    c: PointOnObject(g4,g6)
    c: PointOnObject(g5,g6)
    c: Coincident(g6,g-1)
    c: Vertical(g6,g0)
    c: Diameter(g6) = 2.78
FEATURE [PartDesign::Pocket] Pocket060
  BaseFeature = -> Pad055
  Direction = (0,0,1)
  Length = 1.94
  Length2 = 5
  Profile = -> Sketch121
  ReferenceAxis = -> Sketch121 [N_Axis]
  Type = 0
FEATURE [PartDesign::Body] Body024  label="Body_M3_20mm"
  Group = -> [Sketch119,Pad054,Sketch120,Pad055,Sketch121,Pocket060]
  Origin = -> Origin023
  Placement = pos=(-136.273,-95.5019,-27.2393) rot=(-0.915728,-0.020525,-0.401274;1.89287rad)
  Tip = -> Pocket060
FEATURE [Sketcher::SketchObject] Sketch122
  FullyConstrained = true
  MapMode = 5
  Support = -> [XY_Plane024]
  sketch-geometry (4):
    g0: LineSegment StartX=0 StartY=0 StartZ=0 EndX=2 EndY=0 EndZ=0
    g1: LineSegment StartX=2 StartY=0 StartZ=0 EndX=2 EndY=-20 EndZ=0
    g2: LineSegment StartX=2 StartY=-20 StartZ=0 EndX=0 EndY=-20 EndZ=0
    g3: LineSegment StartX=0 StartY=-20 StartZ=0 EndX=0 EndY=0 EndZ=0
  constraints (11):
    c: Coincident(g0,g1)
    c: Coincident(g1,g2)
    c: Coincident(g2,g3)
    c: Coincident(g3,g0)
    c: Horizontal(g0)
    c: Horizontal(g2)
    c: Vertical(g1)
    c: Vertical(g3)
    c: Coincident(g0,g-1)
    c: DistanceX(g2,g2) = 2
    c: DistanceY(g3,g3) = 20
FEATURE [PartDesign::Pad] Pad056
  Direction = (0,0,1)
  Length = 20
  Length2 = 10
  Profile = -> Sketch122
  ReferenceAxis = -> Sketch122 [N_Axis]
  Type = 0
FEATURE [PartDesign::Body] Body025  label="Body-bearing_retainer_slicer"
  Group = -> [Sketch122,Pad056]
  Origin = -> Origin024
  Placement = pos=(-140.26,-89.9499,-43.1962) rot=(-0.427271,-0.154361,0.890849;1.21892rad)
  Tip = -> Pad056
FEATURE [Sketcher::SketchObject] Sketch123
  ExternalGeometry = -> [Pad042]
  FullyConstrained = true
  MapMode = 5
  Placement = pos=(0,0,3) rot=(0,0,1;0rad)
  Support = -> [Pad042]
  sketch-geometry (4):
    g0: Circle CenterX=0 CenterY=-45 CenterZ=0 NormalX=0 NormalY=0 NormalZ=1 AngleXU=0 Radius=3.15
    g1: Circle CenterX=0 CenterY=-75 CenterZ=0 NormalX=0 NormalY=0 NormalZ=1 AngleXU=0 Radius=3.15
    g2: Circle CenterX=0 CenterY=-125 CenterZ=0 NormalX=0 NormalY=0 NormalZ=1 AngleXU=0 Radius=3.15
    g3: Circle CenterX=0 CenterY=-207 CenterZ=0 NormalX=0 NormalY=0 NormalZ=1 AngleXU=0 Radius=3.15
  constraints (11):
    c: PointOnObject(g0,g-2)
    c: PointOnObject(g1,g-2)
    c: PointOnObject(g2,g-2)
    c: Coincident(g3,g-3)
    c: Equal(g3,g1)
    c: Equal(g1,g0)
    c: Equal(g0,g2)
    c: Diameter(g3) = 6.3
    c: DistanceY(g0) = -45
    c: DistanceY(g1,g0) = 30
    c: DistanceY(g2,g1) = 50
FEATURE [PartDesign::Pocket] Pocket061  label="Pocket-screw_holes"
  BaseFeature = -> Pad042
  Direction = (0,0,-1)
  Length = 10
  Length2 = 100
  Profile = -> Sketch123
  ReferenceAxis = -> Sketch123 [N_Axis]
  Type = 4
FEATURE [Part::FeaturePython] Workplane005  # WARN: FeaturePython — macro-defined, semantics opaque (R4)
  Fixed = true
  Length = 260.851
  Width = 260.851
FEATURE [Part::FeaturePython] Workplane006  # WARN: FeaturePython — macro-defined, semantics opaque (R4)
  Fixed = true
  Length = 368.899
  Placement = pos=(0,0,0) rot=(1,0,0;1.5708rad)
  Width = 368.899
FEATURE [Part::FeaturePython] Workplane007  # WARN: FeaturePython — macro-defined, semantics opaque (R4)
  Fixed = true
  Length = 521.703
  Placement = pos=(0,0,0) rot=(0,-1,0;1.5708rad)
  Width = 521.703
FEATURE [Sketcher::SketchObject] Sketch124
  ExternalGeometry = -> [Pocket059]
  FullyConstrained = true
  MapMode = 5
  Placement = pos=(0,0,-0.25) rot=(0,0,1;0rad)
  Support = -> [Pocket059]
  sketch-geometry (3):
    g0: LineSegment StartX=157 StartY=-88.4123 StartZ=0 EndX=153.36 EndY=-98.4123 EndZ=0
    g1: LineSegment StartX=153.36 StartY=-98.4123 StartZ=0 EndX=157 EndY=-98.4123 EndZ=0
    g2: LineSegment StartX=157 StartY=-98.4123 StartZ=0 EndX=157 EndY=-88.4123 EndZ=0
  constraints (8):
    c: Coincident(g0,g-4)
    c: Coincident(g1,g0)
    c: Horizontal(g1)
    c: Coincident(g2,g1)
    c: Coincident(g2,g0)
    c: Vertical(g2)
    c: Angle(g0,g2) = 0.349066
    c: DistanceY(g2,g2) = 10
FEATURE [PartDesign::Pocket] Pocket062
  BaseFeature = -> Pocket059
  Direction = (0,0,-1)
  Length = 5.5
  Length2 = 5
  Profile = -> Sketch124
  ReferenceAxis = -> Sketch124 [N_Axis]
  Reversed = true
  Type = 0
FEATURE [PartDesign::Fillet] Fillet043
  Base = -> Pocket062 [Edge47,Edge77,Edge31,Edge54,Edge81,Edge80,Edge78]
  BaseFeature = -> Pocket062
  Radius = 0.5
  SupportTransform = false
  UseAllEdges = false
FEATURE [PartDesign::Fillet] Fillet044
  Base = -> Fillet043 [Edge11,Edge66]
  BaseFeature = -> Fillet043
  Radius = 0.3
  SupportTransform = false
  UseAllEdges = false
FEATURE [PartDesign::Fillet] Fillet045
  Base = -> Fillet044 [Edge104,Edge38]
  BaseFeature = -> Fillet044
  Radius = 0.3
  SupportTransform = false
  UseAllEdges = false
FEATURE [PartDesign::Fillet] Fillet046
  Base = -> Fillet045 [Edge67,Edge111,Edge161]
  BaseFeature = -> Fillet045
  Radius = 0.2
  SupportTransform = false
  UseAllEdges = false
FEATURE [PartDesign::Fillet] Fillet047
  Base = -> Fillet046 [Face16]
  BaseFeature = -> Fillet046
  Radius = 0.2
  SupportTransform = false
  UseAllEdges = false
FEATURE [PartDesign::Fillet] Fillet048
  Base = -> Fillet047 [Edge2]
  BaseFeature = -> Fillet047
  Radius = 0.2
  SupportTransform = false
  UseAllEdges = false
FEATURE [Sketcher::SketchObject] Sketch125
  ExternalGeometry = -> [Fillet048]
  FullyConstrained = true
  MapMode = 5
  Placement = pos=(166,0,0) rot=(0.57735,0.57735,0.57735;2.0944rad)
  Support = -> [Fillet048]
  sketch-geometry (6):
    g0: ArcOfCircle CenterX=-80.2435 CenterY=14.8502 CenterZ=0 NormalX=0 NormalY=0 NormalZ=1 AngleXU=0 Radius=10 StartAngle=4.01549 EndAngle=4.53909
    g1: LineSegment StartX=-86.6619 StartY=7.18184 StartZ=0 EndX=-84.8219 EndY=5 EndZ=0
    g2: LineSegment StartX=-84.8219 StartY=5 StartZ=0 EndX=-81.9678 EndY=5 EndZ=0
    g3: ArcOfCircle CenterX=-80.2435 CenterY=-9.85021 CenterZ=0 NormalX=0 NormalY=0 NormalZ=1 AngleXU=0 Radius=10 StartAngle=1.74409 EndAngle=2.26769
    g4: LineSegment StartX=-84.8219 StartY=0 StartZ=0 EndX=-86.6619 EndY=-2.18184 EndZ=0
    g5: LineSegment StartX=-84.8219 StartY=0 StartZ=0 EndX=-81.9678 EndY=-1.457e-13 EndZ=0
  constraints (18):
    c: PointOnObject(g0,g-3)
    c: PointOnObject(g0,g-4)
    c: Coincident(g1,g0)
    c: Coincident(g1,g-5)
    c: Coincident(g2,g1)
    c: Coincident(g2,g0)
    c: Equal(g1,g2)
    c: Angle(g0) = 0.523599
    c: Radius(g0) = 10
    c: PointOnObject(g3,g-6)
    c: PointOnObject(g3,g-7)
    c: Angle(g3) = 0.523599
    c: Radius(g3) = 10
    c: Coincident(g4,g-8)
    c: Coincident(g4,g3)
    c: Coincident(g5,g4)
    c: Coincident(g5,g3)
    c: Equal(g4,g5)
FEATURE [PartDesign::Pad] Pad057
  BaseFeature = -> Fillet048
  Direction = (1,0,0)
  Length = 166
  Length2 = 10
  Profile = -> Sketch125
  ReferenceAxis = -> Sketch125 [N_Axis]
  Reversed = true
  Type = 0
FEATURE [PartDesign::Body] Body003
  Group = -> [Sketch004,Pad004,Sketch006,Pad006,Sketch016,Pad009,Sketch017,Pocket005,Sketch018,Fillet001,Sketch062,Pocket030,Sketch063,Pocket031,Chamfer001,Sketch069,Pocket035,Sketch108,Pad048,Sketch109,Pocket055,Sketch110,Pad049,Sketch111,Sketch113,Pocket056,Sketch114,Pad051,Sketch115,Pad052,Sketch116,Pocket057,Pocket058,Sketch117,Pad053,Sketch118,Pocket059,Sketch124,Pocket062,Fillet043,Fillet044,Fillet045,+5 more]
  Origin = -> Origin003
  Placement = pos=(19.5211,29.3396,-3.97852) rot=(0.102719,-0.284327,-0.953209;2.07135rad)
  Tip = -> Pad057
FEATURE [Part::FeaturePython] Parts004  # WARN: FeaturePython — macro-defined, semantics opaque (R4)
  Group = -> [Body003,Body011,Body012,Body022,Body023,Body024,Body025]
  GroupMode = 0
FEATURE [Part::FeaturePython] Slice005  # WARN: FeaturePython — macro-defined, semantics opaque (R4)
  Base = -> Body003
  Mode = 1
  Tolerance = 0
  Tools = -> [Body011]
FEATURE [Part::FeaturePython] Slice005_child0  label="Slice005.0"  # WARN: FeaturePython — macro-defined, semantics opaque (R4)
  Base = -> Slice005
  FilterType = 1
  Invert = false
  OverrideMaxVal = 0
  WindowFrom = 80
  WindowTo = 100
  items = 0
FEATURE [Part::FeaturePython] Slice005_child1  label="Slice005.1"  # WARN: FeaturePython — macro-defined, semantics opaque (R4)
  Base = -> Slice005
  FilterType = 1
  Invert = false
  OverrideMaxVal = 0
  WindowFrom = 80
  WindowTo = 100
  items = 1
FEATURE [App::DocumentObjectGroup] GrExplode_Slice005  label="Exploded Slice-door-left-front-far-left"
  Group = -> [Slice005_child0,Slice005_child1]
FEATURE [Part::FeaturePython] Slice012  # WARN: FeaturePython — macro-defined, semantics opaque (R4)
  Base = -> Body003
  Mode = 1
  Tolerance = 0
  Tools = -> [Body022,Body025]
FEATURE [Part::FeaturePython] Slice013  # WARN: FeaturePython — macro-defined, semantics opaque (R4)
  Base = -> Body003
  Mode = 1
  Tolerance = 0
  Tools = -> [Body022,Body025]
FEATURE [Part::FeaturePython] Slice013_child0  label="Slice013.0"  # WARN: FeaturePython — macro-defined, semantics opaque (R4)
  Base = -> Slice013
  FilterType = 1
  Invert = false
  OverrideMaxVal = 0
  Placement = pos=(-3.06846,0.620866,2.01466) rot=(0.324781,0.692181,0.644517;0.694089rad)
  WindowFrom = 80
  WindowTo = 100
  items = 0
FEATURE [Part::FeaturePython] Slice013_child1  label="Slice013.1"  # WARN: FeaturePython — macro-defined, semantics opaque (R4)
  Base = -> Slice013
  FilterType = 1
  Invert = false
  OverrideMaxVal = 0
  WindowFrom = 80
  WindowTo = 100
  items = 1
FEATURE [Part::FeaturePython] Slice013_child2  label="Slice013.2"  # WARN: FeaturePython — macro-defined, semantics opaque (R4)
  Base = -> Slice013
  FilterType = 1
  Invert = false
  OverrideMaxVal = 0
  Placement = pos=(-57.5034,-116.246,144.417) rot=(0.949505,-0.218571,0.225094;1.73503rad)
  WindowFrom = 80
  WindowTo = 100
  items = 2
FEATURE [Part::FeaturePython] Slice013_child3  label="Slice013.3"  # WARN: FeaturePython — macro-defined, semantics opaque (R4)
  Base = -> Slice013
  FilterType = 1
  Invert = false
  OverrideMaxVal = 0
  WindowFrom = 80
  WindowTo = 100
  items = 3
FEATURE [Part::FeaturePython] Slice013_child4  label="Slice013.4"  # WARN: FeaturePython — macro-defined, semantics opaque (R4)
  Base = -> Slice013
  FilterType = 1
  Invert = false
  OverrideMaxVal = 0
  Placement = pos=(-2.62275,1.52172,3.18742) rot=(0.324781,0.692181,0.644517;0.694089rad)
  WindowFrom = 80
  WindowTo = 100
  items = 4
FEATURE [App::DocumentObjectGroup] GrExplode_Slice013  label="Exploded Slice-front_door_left"
  Group = -> [Slice013_child0,Slice013_child1,Slice013_child2,Slice013_child3,Slice013_child4]
FEATURE [Part::FeaturePython] Parts013  # WARN: FeaturePython — macro-defined, semantics opaque (R4)
  Group = -> [Workplane005,Workplane006,Workplane007,GrExplode_Slice013]
  GroupMode = 0
FEATURE [App::FeaturePython] Constraints014  # WARN: FeaturePython — macro-defined, semantics opaque (R4)
  _Version = 1
FEATURE [App::FeaturePython] Constraints015  # WARN: FeaturePython — macro-defined, semantics opaque (R4)
  _Version = 1
FEATURE [App::FeaturePython] Elements015  # WARN: FeaturePython — macro-defined, semantics opaque (R4)
FEATURE [Sketcher::SketchObject] Sketch126
  FullyConstrained = true
  MapMode = 5
  Placement = pos=(0,0,0) rot=(0.57735,0.57735,0.57735;2.0944rad)
  Support = -> [YZ_Plane025]
  sketch-geometry (4):
    g0: LineSegment StartX=0 StartY=0 StartZ=0 EndX=60 EndY=0 EndZ=0
    g1: LineSegment StartX=60 StartY=0 StartZ=0 EndX=60 EndY=20 EndZ=0
    g2: LineSegment StartX=60 StartY=20 StartZ=0 EndX=0 EndY=20 EndZ=0
    g3: LineSegment StartX=0 StartY=20 StartZ=0 EndX=0 EndY=0 EndZ=0
  constraints (11):
    c: Coincident(g0,g1)
    c: Coincident(g1,g2)
    c: Coincident(g2,g3)
    c: Horizontal(g0)
    c: Horizontal(g2)
    c: Vertical(g1)
    c: Vertical(g3)
    c: DistanceY(g1,g1) = 20
    c: DistanceX(g0,g0) = 60
    c: Coincident(g0,g3)
    c: Coincident(g0,g-1)
FEATURE [PartDesign::Pad] Pad058
  Direction = (1,-2e-16,3e-16)
  Length = 8
  Length2 = 10
  Placement = pos=(0,0,0) rot=(0.57735,0.57735,0.57735;2.0944rad)
  Profile = -> Sketch126
  ReferenceAxis = -> Sketch126 [N_Axis]
  Type = 0
FEATURE [Sketcher::SketchObject] Sketch127
  FullyConstrained = true
  MapMode = 5
  Placement = pos=(0,0,0) rot=(-0.57735,-0.57735,0.57735;4.18879rad)
  Support = -> [Pad058]
  sketch-geometry (4):
    g0: LineSegment StartX=0 StartY=0 StartZ=0 EndX=-60 EndY=0 EndZ=0
    g1: LineSegment StartX=-60 StartY=0 StartZ=0 EndX=-60 EndY=20 EndZ=0
    g2: LineSegment StartX=-60 StartY=20 StartZ=0 EndX=0 EndY=20 EndZ=0
    g3: LineSegment StartX=0 StartY=20 StartZ=0 EndX=0 EndY=0 EndZ=0
  constraints (11):
    c: Coincident(g0,g1)
    c: Coincident(g1,g2)
    c: Coincident(g2,g3)
    c: Coincident(g3,g0)
    c: Horizontal(g0)
    c: Horizontal(g2)
    c: Vertical(g1)
    c: Vertical(g3)
    c: Coincident(g0,g-1)
    c: DistanceX(g2,g2) = 60
    c: DistanceY(g3,g3) = 20
FEATURE [PartDesign::Pad] Pad059
  BaseFeature = -> Pad058
  Direction = (-4e-16,-1,2e-16)
  Length = 10
  Length2 = 10
  Placement = pos=(0,0,0) rot=(0.57735,0.57735,0.57735;2.0944rad)
  Profile = -> Sketch127
  ReferenceAxis = -> Sketch127 [N_Axis]
  Reversed = true
  Type = 0
FEATURE [Sketcher::SketchObject] Sketch128
  ExternalGeometry = -> [Pad059]
  FullyConstrained = true
  MapMode = 5
  Placement = pos=(0,0,0) rot=(0.57735,0.57735,-0.57735;4.18879rad)
  Support = -> [Pad059]
  sketch-geometry (5):
    g0: LineSegment StartX=10 StartY=-60 StartZ=0 EndX=60 EndY=-20 EndZ=0
    g1: LineSegment StartX=60 StartY=-20 StartZ=0 EndX=43.9922 EndY=-20 EndZ=0
    g2: LineSegment StartX=43.9922 StartY=-20 StartZ=0 EndX=10 EndY=-47.1938 EndZ=0
    g3: LineSegment StartX=10 StartY=-47.1938 StartZ=0 EndX=10 EndY=-60 EndZ=0
    g4: LineSegment StartX=25 StartY=-35.1938 StartZ=0 EndX=31.247 EndY=-43.0024 EndZ=0
  constraints (14):
    c: Coincident(g0,g-4)
    c: Coincident(g0,g-3)
    c: Coincident(g1,g0)
    c: PointOnObject(g1,g-3)
    c: Coincident(g2,g1)
    c: PointOnObject(g2,g-4)
    c: Coincident(g3,g2)
    c: Coincident(g3,g0)
    c: Parallel(g2,g0)
    c: PointOnObject(g4,g2)
    c: PointOnObject(g4,g0)
    c: Angle(g0,g4) = 1.5708
    c: Distance(g4) = 10
    c: DistanceX(g4) = 25
FEATURE [PartDesign::Pad] Pad060
  BaseFeature = -> Pad059
  Direction = (-1,6e-16,-5e-16)
  Length = 4
  Length2 = 10
  Placement = pos=(0,0,0) rot=(0.57735,0.57735,0.57735;2.0944rad)
  Profile = -> Sketch128
  ReferenceAxis = -> Sketch128 [N_Axis]
  Reversed = true
  Type = 0
FEATURE [Sketcher::SketchObject] Sketch129
  ExternalGeometry = -> [Pad060]
  FullyConstrained = true
  MapMode = 5
  Placement = pos=(8,-1.8e-15,1.8e-15) rot=(0.57735,0.57735,0.57735;2.0944rad)
  Support = -> [Pad060]
  sketch-geometry (7):
    g0: ArcOfCircle CenterX=22.5 CenterY=10 CenterZ=0 NormalX=0 NormalY=0 NormalZ=1 AngleXU=0 Radius=6 StartAngle=1.5708 EndAngle=4.71239
    g1: ArcOfCircle CenterX=47.5 CenterY=10 CenterZ=0 NormalX=0 NormalY=0 NormalZ=1 AngleXU=0 Radius=6 StartAngle=4.71239 EndAngle=7.85398
    g2: LineSegment StartX=22.5 StartY=4 StartZ=0 EndX=47.5 EndY=4 EndZ=0
    g3: LineSegment StartX=47.5 StartY=16 StartZ=0 EndX=22.5 EndY=16 EndZ=0
    g4: LineSegment StartX=47.5 StartY=10 StartZ=0 EndX=60 EndY=20 EndZ=0
    g5: LineSegment StartX=10 StartY=20 StartZ=0 EndX=22.5 EndY=10 EndZ=0
    g6: LineSegment StartX=22.5 StartY=10 StartZ=0 EndX=10 EndY=-5.3e-15 EndZ=0
  constraints (16):
    c: Tangent(g0,g2) = -1.5708
    c: Tangent(g2,g1) = -1.5708
    c: Tangent(g1,g3) = -1.5708
    c: Tangent(g3,g0) = -1.5708
    c: Equal(g0,g1)
    c: Horizontal(g2)
    c: Coincident(g4,g1)
    c: Coincident(g4,g-3)
    c: DistanceX(g2,g2) = 25
    c: Diameter(g1) = 12
    c: Coincident(g5,g-5)
    c: Coincident(g5,g0)
    c: Coincident(g6,g0)
    c: Coincident(g6,g-5)
    c: Equal(g5,g6)
    c: Equal(g6,g4)
FEATURE [PartDesign::Pocket] Pocket063
  BaseFeature = -> Pad060
  Direction = (-1,8e-16,-6e-16)
  Length = 5
  Length2 = 5
  Placement = pos=(0,0,0) rot=(0.57735,0.57735,0.57735;2.0944rad)
  Profile = -> Sketch129
  ReferenceAxis = -> Sketch129 [N_Axis]
  Type = 0
FEATURE [Sketcher::SketchObject] Sketch133
  ExternalGeometry = -> [Pocket063]
  FullyConstrained = true
  MapMode = 5
  Placement = pos=(4.4e-15,10,-1.7e-15) rot=(0.57735,0.57735,0.57735;4.18879rad)
  Support = -> [Pocket063]
  sketch-geometry (7):
    g0: ArcOfCircle CenterX=27.5 CenterY=10 CenterZ=0 NormalX=0 NormalY=0 NormalZ=1 AngleXU=0 Radius=6 StartAngle=1.5708 EndAngle=4.71239
    g1: ArcOfCircle CenterX=52.5 CenterY=10 CenterZ=0 NormalX=0 NormalY=0 NormalZ=1 AngleXU=0 Radius=6 StartAngle=4.71239 EndAngle=7.85398
    g2: LineSegment StartX=27.5 StartY=4 StartZ=0 EndX=52.5 EndY=4 EndZ=0
    g3: LineSegment StartX=52.5 StartY=16 StartZ=0 EndX=27.5 EndY=16 EndZ=0
    g4: LineSegment StartX=52.5 StartY=10 StartZ=0 EndX=60 EndY=20 EndZ=0
    g5: LineSegment StartX=60 StartY=-5.72e-14 StartZ=0 EndX=52.5 EndY=10 EndZ=0
    g6: LineSegment StartX=27.5 StartY=10 StartZ=0 EndX=20 EndY=-2.49e-14 EndZ=0
  constraints (16):
    c: Tangent(g0,g2) = -1.5708
    c: Tangent(g2,g1) = -1.5708
    c: Tangent(g1,g3) = -1.5708
    c: Tangent(g3,g0) = -1.5708
    c: Equal(g0,g1)
    c: Horizontal(g2)
    c: DistanceX(g2,g2) = 25
    c: Diameter(g1) = 12
    c: Coincident(g4,g1)
    c: Coincident(g4,g-3)
    c: Coincident(g5,g1)
    c: Coincident(g6,g0)
    c: Coincident(g6,g-5)
    c: Equal(g5,g4)
    c: Equal(g4,g6)
    c: Coincident(g5,g-4)
FEATURE [PartDesign::Pocket] Pocket064
  BaseFeature = -> Pocket063
  Direction = (-4e-16,-1,1.1e-15)
  Length = 5
  Length2 = 5
  Placement = pos=(0,0,0) rot=(0.57735,0.57735,0.57735;2.0944rad)
  Profile = -> Sketch133
  ReferenceAxis = -> Sketch133 [N_Axis]
  Type = 0
FEATURE [PartDesign::Chamfer] Chamfer007
  Angle = 45
  Base = -> Pocket064 [Edge13]
  BaseFeature = -> Pocket064
  ChamferType = 0
  FlipDirection = false
  Placement = pos=(0,0,0) rot=(0.57735,0.57735,0.57735;2.0944rad)
  Size = 6
  Size2 = 1
  SupportTransform = false
  UseAllEdges = false
FEATURE [PartDesign::Fillet] Fillet049
  Base = -> Chamfer007 [Edge44,Edge35]
  BaseFeature = -> Chamfer007
  Placement = pos=(0,0,0) rot=(0.57735,0.57735,0.57735;2.0944rad)
  Radius = 9
  SupportTransform = false
  UseAllEdges = false
FEATURE [PartDesign::Fillet] Fillet050
  Base = -> Fillet049 [Edge23]
  BaseFeature = -> Fillet049
  Placement = pos=(0,0,0) rot=(0.57735,0.57735,0.57735;2.0944rad)
  Radius = 19
  SupportTransform = false
  UseAllEdges = false
FEATURE [PartDesign::Fillet] Fillet051
  Base = -> Fillet050 [Edge32]
  BaseFeature = -> Fillet050
  Placement = pos=(0,0,0) rot=(0.57735,0.57735,0.57735;2.0944rad)
  Radius = 5
  SupportTransform = false
  UseAllEdges = false
FEATURE [PartDesign::Fillet] Fillet052
  Base = -> Fillet051 [Edge33,Edge35]
  BaseFeature = -> Fillet051
  Placement = pos=(0,0,0) rot=(0.57735,0.57735,0.57735;2.0944rad)
  Radius = 1
  SupportTransform = false
  UseAllEdges = false
FEATURE [PartDesign::Fillet] Fillet053
  Base = -> Fillet052 [Edge57,Edge15]
  BaseFeature = -> Fillet052
  Placement = pos=(0,0,0) rot=(0.57735,0.57735,0.57735;2.0944rad)
  Radius = 3
  SupportTransform = false
  UseAllEdges = false
FEATURE [PartDesign::Fillet] Fillet054
  Base = -> Fillet053 [Edge77]
  BaseFeature = -> Fillet053
  Placement = pos=(0,0,0) rot=(0.57735,0.57735,0.57735;2.0944rad)
  Radius = 9
  SupportTransform = false
  UseAllEdges = false
FEATURE [PartDesign::Fillet] Fillet055
  Base = -> Fillet054 [Face29,Face28,Face30,Face15]
  BaseFeature = -> Fillet054
  Placement = pos=(0,0,0) rot=(0.57735,0.57735,0.57735;2.0944rad)
  Radius = 1
  SupportTransform = false
  UseAllEdges = false
FEATURE [PartDesign::Fillet] Fillet056
  Base = -> Fillet055 [Face4,Face10,Face6,Face8]
  BaseFeature = -> Fillet055
  Placement = pos=(0,0,0) rot=(0.57735,0.57735,0.57735;2.0944rad)
  Radius = 0.5
  SupportTransform = false
  UseAllEdges = false
FEATURE [PartDesign::Fillet] Fillet057
  Base = -> Fillet056 [Edge60]
  BaseFeature = -> Fillet056
  Placement = pos=(0,0,0) rot=(0.57735,0.57735,0.57735;2.0944rad)
  Radius = 0.5
  SupportTransform = false
  UseAllEdges = false
FEATURE [PartDesign::Fillet] Fillet058
  Base = -> Fillet057 [Face27,Face50]
  BaseFeature = -> Fillet057
  Placement = pos=(0,0,0) rot=(0.57735,0.57735,0.57735;2.0944rad)
  Radius = 0.5
  SupportTransform = false
  UseAllEdges = false
FEATURE [PartDesign::Fillet] Fillet059
  Base = -> Fillet058 [Face77,Face76,Face74,Face75]
  BaseFeature = -> Fillet058
  Placement = pos=(0,0,0) rot=(0.57735,0.57735,0.57735;2.0944rad)
  Radius = 0.5
  SupportTransform = false
  UseAllEdges = false
FEATURE [Sketcher::SketchObject] Sketch134
  ExternalGeometry = -> [Fillet059]
  FullyConstrained = true
  MapMode = 5
  Placement = pos=(2.2e-15,5,-5.3e-15) rot=(0.57735,0.57735,0.57735;4.18879rad)
  Support = -> [Fillet059]
  sketch-geometry (2):
    g0: Circle CenterX=27.5 CenterY=10 CenterZ=0 NormalX=0 NormalY=0 NormalZ=1 AngleXU=0 Radius=3.15
    g1: Circle CenterX=52.5 CenterY=10 CenterZ=0 NormalX=0 NormalY=0 NormalZ=1 AngleXU=0 Radius=3.15
  constraints (4):
    c: Coincident(g0,g-3)
    c: Coincident(g1,g-4)
    c: Equal(g0,g1)
    c: Diameter(g0) = 6.3
FEATURE [PartDesign::Pocket] Pocket065
  BaseFeature = -> Fillet059
  Direction = (-5e-16,-1,1.4e-15)
  Length = 5
  Length2 = 5
  Placement = pos=(0,0,0) rot=(0.57735,0.57735,0.57735;2.0944rad)
  Profile = -> Sketch134
  ReferenceAxis = -> Sketch134 [N_Axis]
  Type = 0
FEATURE [Sketcher::SketchObject] Sketch135
  ExternalGeometry = -> [Pocket065]
  FullyConstrained = true
  MapMode = 5
  Placement = pos=(3,-2.1e-15,1.7e-15) rot=(0.57735,0.57735,0.57735;2.0944rad)
  Support = -> [Pocket065]
  sketch-geometry (2):
    g0: Circle CenterX=22.5 CenterY=10 CenterZ=0 NormalX=0 NormalY=0 NormalZ=1 AngleXU=0 Radius=3.15
    g1: Circle CenterX=47.5 CenterY=10 CenterZ=0 NormalX=0 NormalY=0 NormalZ=1 AngleXU=0 Radius=3.15
  constraints (4):
    c: Coincident(g0,g-3)
    c: Coincident(g1,g-4)
    c: Equal(g1,g0)
    c: Diameter(g0) = 6.3
FEATURE [PartDesign::Pocket] Pocket066
  BaseFeature = -> Pocket065
  Direction = (-1,1.3e-15,-9e-16)
  Length = 5
  Length2 = 5
  Placement = pos=(0,0,0) rot=(0.57735,0.57735,0.57735;2.0944rad)
  Profile = -> Sketch135
  ReferenceAxis = -> Sketch135 [N_Axis]
  Type = 0
FEATURE [PartDesign::Body] Body026
  Group = -> [Sketch126,Pad058,Sketch127,Pad059,Sketch128,Pad060,Sketch129,Pocket063,Sketch133,Pocket064,Chamfer007,Fillet049,Fillet050,Fillet051,Fillet052,Fillet053,Fillet054,Fillet055,Fillet056,Fillet057,Fillet058,Fillet059,Sketch134,Pocket065,Sketch135,Pocket066]
  Origin = -> Origin025
  Tip = -> Pocket066
FEATURE [Part::FeaturePython] Parts014  # WARN: FeaturePython — macro-defined, semantics opaque (R4)
  Group = -> [Body026]
  GroupMode = 0
FEATURE [Part::Mirroring] Part__Mirroring002  label="Body026 (Mirror #3)"
  Base = (0,0,0)
  Normal = (0,1,0)
  Source = -> Body026
FEATURE [App::FeaturePython] Constraints016  # WARN: FeaturePython — macro-defined, semantics opaque (R4)
  _Version = 1
FEATURE [Part::FeaturePython] Parts016  # WARN: FeaturePython — macro-defined, semantics opaque (R4)
  Group = -> [Part__Mirroring002]
  GroupMode = 0
FEATURE [App::FeaturePython] Constraints017  # WARN: FeaturePython — macro-defined, semantics opaque (R4)
  _Version = 1
FEATURE [Sketcher::SketchObject] Sketch136
  FullyConstrained = true
  MapMode = 5
  Support = -> [XY_Plane026]
  sketch-geometry (5):
    g0: LineSegment StartX=0 StartY=0 StartZ=0 EndX=65 EndY=0 EndZ=0
    g1: LineSegment StartX=65 StartY=0 StartZ=0 EndX=65 EndY=4.27341 EndZ=0
    g2: ArcOfCircle CenterX=85 CenterY=75 CenterZ=0 NormalX=0 NormalY=0 NormalZ=1 AngleXU=0 Radius=73.5 StartAngle=3.80049 EndAngle=4.43681
    g3: LineSegment StartX=26.8859 StartY=30 StartZ=0 EndX=0 EndY=30 EndZ=0
    g4: LineSegment StartX=0 StartY=30 StartZ=0 EndX=0 EndY=0 EndZ=0
  constraints (16):
    c: Coincident(g0,g-1)
    c: PointOnObject(g0,g-1)
    c: Coincident(g1,g0)
    c: Vertical(g1)
    c: Coincident(g2,g1)
    c: Coincident(g3,g2)
    c: PointOnObject(g3,g-2)
    c: Horizontal(g3)
    c: Coincident(g4,g3)
    c: PointOnObject(g4,g-1)
    c: Vertical(g4)
    c: DistanceX(g2) = 85
    c: DistanceY(g2) = 75
    c: Diameter(g2) = 147
    c: DistanceX(g0,g0) = 65
    c: DistanceY(g3) = 30
FEATURE [PartDesign::Pad] Pad064
  Direction = (0,0,1)
  Length = 4
  Length2 = 10
  Profile = -> Sketch136
  ReferenceAxis = -> Sketch136 [N_Axis]
  Reversed = true
  Type = 0
FEATURE [Sketcher::SketchObject] Sketch137
  ExternalGeometry = -> [Pad064]
  FullyConstrained = true
  MapMode = 5
  Placement = pos=(0,0,0) rot=(1,0,0;1.5708rad)
  Support = -> [Pad064]
  sketch-geometry (4):
    g0: LineSegment StartX=65 StartY=-4 StartZ=0 EndX=0 EndY=-4 EndZ=0
    g1: LineSegment StartX=0 StartY=-4 StartZ=0 EndX=0 EndY=-20 EndZ=0
    g2: LineSegment StartX=0 StartY=-20 StartZ=0 EndX=65 EndY=-20 EndZ=0
    g3: LineSegment StartX=65 StartY=-20 StartZ=0 EndX=65 EndY=-4 EndZ=0
  constraints (11):
    c: Coincident(g0,g1)
    c: Coincident(g1,g2)
    c: Coincident(g2,g3)
    c: Coincident(g3,g0)
    c: Horizontal(g0)
    c: Horizontal(g2)
    c: Vertical(g1)
    c: Vertical(g3)
    c: Coincident(g0,g-3)
    c: PointOnObject(g1,g-2)
    c: DistanceY(g1) = -20
FEATURE [PartDesign::Pad] Pad065
  BaseFeature = -> Pad064
  Direction = (0,-1,2e-16)
  Length = 3
  Length2 = 10
  Profile = -> Sketch137
  ReferenceAxis = -> Sketch137 [N_Axis]
  Reversed = true
  Type = 0
FEATURE [Sketcher::SketchObject] Sketch138
  ExternalGeometry = -> [Pad065]
  FullyConstrained = true
  MapMode = 5
  Placement = pos=(0,0,0) rot=(0.57735,-0.57735,-0.57735;2.0944rad)
  Support = -> [Pad065]
  sketch-geometry (4):
    g0: LineSegment StartX=-30 StartY=-4 StartZ=0 EndX=-3 EndY=-4 EndZ=0
    g1: LineSegment StartX=-3 StartY=-4 StartZ=0 EndX=-3 EndY=-20 EndZ=0
    g2: LineSegment StartX=-3 StartY=-20 StartZ=0 EndX=-30 EndY=-20 EndZ=0
    g3: LineSegment StartX=-30 StartY=-20 StartZ=0 EndX=-30 EndY=-4 EndZ=0
  constraints (10):
    c: Coincident(g0,g1)
    c: Coincident(g1,g2)
    c: Coincident(g2,g3)
    c: Coincident(g3,g0)
    c: Horizontal(g0)
    c: Horizontal(g2)
    c: Vertical(g1)
    c: Vertical(g3)
    c: Coincident(g0,g-3)
    c: Coincident(g1,g-4)
FEATURE [PartDesign::Pad] Pad066
  BaseFeature = -> Pad065
  Direction = (-1,0,0)
  Length = 8
  Length2 = 10
  Profile = -> Sketch138
  ReferenceAxis = -> Sketch138 [N_Axis]
  Reversed = true
  Type = 0
FEATURE [Sketcher::SketchObject] Sketch139
  ExternalGeometry = -> [Pad066]
  FullyConstrained = true
  MapMode = 5
  Placement = pos=(8,0,0) rot=(0.57735,0.57735,0.57735;2.0944rad)
  Support = -> [Pad066]
  sketch-geometry (4):
    g0: ArcOfCircle CenterX=9 CenterY=-10 CenterZ=0 NormalX=0 NormalY=0 NormalZ=1 AngleXU=0 Radius=6 StartAngle=1.5708 EndAngle=4.71239
    g1: ArcOfCircle CenterX=21 CenterY=-10 CenterZ=0 NormalX=0 NormalY=0 NormalZ=1 AngleXU=0 Radius=6 StartAngle=4.71239 EndAngle=7.85398
    g2: LineSegment StartX=9 StartY=-16 StartZ=0 EndX=21 EndY=-16 EndZ=0
    g3: LineSegment StartX=21 StartY=-4 StartZ=0 EndX=9 EndY=-4 EndZ=0
  constraints (10):
    c: Tangent(g0,g2) = -1.5708
    c: Tangent(g2,g1) = -1.5708
    c: Tangent(g1,g3) = -1.5708
    c: Tangent(g3,g0) = -1.5708
    c: Equal(g0,g1)
    c: Horizontal(g2)
    c: Diameter(g1) = 12
    c: DistanceY(g-4,g0) = 10
    c: DistanceX(g1,g-3) = 9
    c: DistanceX(g0) = 9
FEATURE [PartDesign::Pocket] Pocket067
  BaseFeature = -> Pad066
  Direction = (-1,0,0)
  Length = 5
  Length2 = 5
  Profile = -> Sketch139
  ReferenceAxis = -> Sketch139 [N_Axis]
  Type = 0
FEATURE [PartDesign::Fillet] Fillet060
  Base = -> Pocket067 [Edge28]
  BaseFeature = -> Pocket067
  Radius = 1
  SupportTransform = false
  UseAllEdges = false
FEATURE [PartDesign::Fillet] Fillet061
  Base = -> Fillet060 [Edge48]
  BaseFeature = -> Fillet060
  Radius = 10
  SupportTransform = false
  UseAllEdges = false
FEATURE [PartDesign::Fillet] Fillet062
  Base = -> Fillet061 [Edge56]
  BaseFeature = -> Fillet061
  Radius = 3.5
  SupportTransform = false
  UseAllEdges = false
FEATURE [PartDesign::Fillet] Fillet063
  Base = -> Fillet062 [Edge32,Edge25,Edge47,Edge23,Edge26,Edge24,Edge1,Edge2,Edge20,Edge11]
  BaseFeature = -> Fillet062
  Radius = 1
  SupportTransform = false
  UseAllEdges = false
FEATURE [PartDesign::Fillet] Fillet064
  Base = -> Fillet063 [Face31,Face32,Face21]
  BaseFeature = -> Fillet063
  Radius = 1
  SupportTransform = false
  UseAllEdges = false
FEATURE [PartDesign::Fillet] Fillet065
  Base = -> Fillet064 [Face33]
  BaseFeature = -> Fillet064
  Radius = 0.5
  SupportTransform = false
  UseAllEdges = false
FEATURE [PartDesign::Fillet] Fillet066
  Base = -> Fillet065 [Face23]
  BaseFeature = -> Fillet065
  Radius = 0.9
  SupportTransform = false
  UseAllEdges = false
FEATURE [Sketcher::SketchObject] Sketch140
  ExternalGeometry = -> [Fillet066]
  FullyConstrained = true
  MapMode = 5
  Placement = pos=(3,0,0) rot=(0.57735,0.57735,0.57735;2.0944rad)
  Support = -> [Fillet066]
  sketch-geometry (2):
    g0: Circle CenterX=9 CenterY=-10 CenterZ=0 NormalX=0 NormalY=0 NormalZ=1 AngleXU=0 Radius=2.075
    g1: Circle CenterX=21 CenterY=-10 CenterZ=0 NormalX=0 NormalY=0 NormalZ=1 AngleXU=0 Radius=2.075
  constraints (4):
    c: Coincident(g0,g-3)
    c: Coincident(g1,g-4)
    c: Equal(g0,g1)
    c: Diameter(g1) = 4.15
FEATURE [PartDesign::Pocket] Pocket068
  BaseFeature = -> Fillet066
  Direction = (-1,0,0)
  Length = 5
  Length2 = 5
  Profile = -> Sketch140
  ReferenceAxis = -> Sketch140 [N_Axis]
  Type = 0
FEATURE [Sketcher::SketchObject] Sketch141
  ExternalGeometry = -> [Pocket068]
  FullyConstrained = true
  MapMode = 5
  Placement = pos=(0,3,-7e-16) rot=(0,0.707107,0.707107;3.14159rad)
  Support = -> [Pocket068]
  sketch-geometry (4):
    g0: LineSegment StartX=-8 StartY=-18.5 StartZ=0 EndX=-38 EndY=-18.5 EndZ=0
    g1: LineSegment StartX=-38 StartY=-18.5 StartZ=0 EndX=-38 EndY=-16.5 EndZ=0
    g2: LineSegment StartX=-38 StartY=-16.5 StartZ=0 EndX=-8 EndY=-16.5 EndZ=0
    g3: LineSegment StartX=-8 StartY=-16.5 StartZ=0 EndX=-8 EndY=-18.5 EndZ=0
  constraints (12):
    c: Coincident(g0,g1)
    c: Coincident(g1,g2)
    c: Coincident(g2,g3)
    c: Coincident(g3,g0)
    c: Horizontal(g0)
    c: Horizontal(g2)
    c: Vertical(g1)
    c: Vertical(g3)
    c: DistanceY(g3,g3) = 2
    c: DistanceX(g0,g0) = 30
    c: PointOnObject(g0,g-3)
    c: DistanceY(g-3,g0) = 0.5
FEATURE [PartDesign::Pad] Pad067
  BaseFeature = -> Pocket068
  Direction = (0,1,-2e-16)
  Length = 5
  Length2 = 10
  Profile = -> Sketch141
  ReferenceAxis = -> Sketch141 [N_Axis]
  Type = 0
FEATURE [Sketcher::SketchObject] Sketch142
  ExternalGeometry = -> [Pad067]
  FullyConstrained = true
  MapMode = 5
  Placement = pos=(0,-4.1e-15,-18.5) rot=(1,0,0;3.14159rad)
  Support = -> [Pad067]
  sketch-geometry (3):
    g0: LineSegment StartX=8 StartY=-8 StartZ=0 EndX=38 EndY=-3 EndZ=0
    g1: LineSegment StartX=38 StartY=-3 StartZ=0 EndX=38 EndY=-8 EndZ=0
    g2: LineSegment StartX=38 StartY=-8 StartZ=0 EndX=8 EndY=-8 EndZ=0
  constraints (6):
    c: Coincident(g0,g-6)
    c: Coincident(g0,g-5)
    c: Coincident(g1,g0)
    c: Coincident(g1,g-5)
    c: Coincident(g2,g1)
    c: Coincident(g2,g0)
FEATURE [PartDesign::Pocket] Pocket069
  BaseFeature = -> Pad067
  Direction = (0,2e-16,1)
  Length = 0
  Length2 = 5
  Profile = -> Sketch142
  ReferenceAxis = -> Sketch142 [N_Axis]
  Type = 2
FEATURE [App::FeaturePython] Constraints018  # WARN: FeaturePython — macro-defined, semantics opaque (R4)
  _Version = 1
FEATURE [PartDesign::Fillet] Fillet067
  Base = -> Pocket069 [Face26,Face27,Face24]
  BaseFeature = -> Pocket069
  Radius = 0.4
  SupportTransform = false
  UseAllEdges = false
FEATURE [PartDesign::Fillet] Fillet068
  Base = -> Fillet067 [Face69,Face68]
  BaseFeature = -> Fillet067
  Radius = 0.3
  SupportTransform = false
  UseAllEdges = false
FEATURE [PartDesign::Body] Body027
  Group = -> [Sketch136,Pad064,Sketch137,Pad065,Sketch138,Pad066,Sketch139,Pocket067,Fillet060,Fillet061,Fillet062,Fillet063,Fillet064,Fillet065,Fillet066,Sketch140,Pocket068,Sketch141,Pad067,Sketch142,Pocket069,Fillet067,Fillet068]
  Origin = -> Origin026
  Tip = -> Fillet068
FEATURE [Part::FeaturePython] Parts017  # WARN: FeaturePython — macro-defined, semantics opaque (R4)
  Group = -> [Body027]
  GroupMode = 0
FEATURE [Part::Mirroring] Part__Mirroring003  label="Body027 (Mirror #4)"
  Base = (0,0,0)
  Normal = (1,0,0)
  Source = -> Body027
FEATURE [Part::FeaturePython] Parts018  # WARN: FeaturePython — macro-defined, semantics opaque (R4)
  Group = -> [Part__Mirroring003]
  GroupMode = 0
FEATURE [App::FeaturePython] Constraints019  # WARN: FeaturePython — macro-defined, semantics opaque (R4)
  _Version = 1
FEATURE [Part::Feature] Part__Mirroring003001  label="Body027 (Mirror #4)001"
  shape: bbox 65 x 33.66 x 21.11 mm, 87 faces (baked)
FEATURE [Part::FeaturePython] Parts019  # WARN: FeaturePython — macro-defined, semantics opaque (R4)
  Group = -> [Part__Mirroring003001]
  GroupMode = 0
FEATURE [App::FeaturePython] Constraints021  # WARN: FeaturePython — macro-defined, semantics opaque (R4)
  _Version = 1
FEATURE [Sketcher::SketchObject] Sketch144
  FullyConstrained = true
  MapMode = 5
  Support = -> [XY_Plane028]
  sketch-geometry (4):
    g0: LineSegment StartX=0 StartY=0 StartZ=0 EndX=65.5 EndY=0 EndZ=0
    g1: LineSegment StartX=65.5 StartY=0 StartZ=0 EndX=65.5 EndY=30.6 EndZ=0
    g2: LineSegment StartX=65.5 StartY=30.6 StartZ=0 EndX=0 EndY=30.6 EndZ=0
    g3: LineSegment StartX=0 StartY=30.6 StartZ=0 EndX=0 EndY=0 EndZ=0
  constraints (11):
    c: Coincident(g0,g1)
    c: Coincident(g1,g2)
    c: Coincident(g2,g3)
    c: Coincident(g3,g0)
    c: Horizontal(g0)
    c: Horizontal(g2)
    c: Vertical(g1)
    c: Vertical(g3)
    c: Coincident(g0,g-1)
    c: DistanceX(g0,g0) = 65.5
    c: DistanceY(g1,g1) = 30.6
FEATURE [PartDesign::Pad] Pad069
  Direction = (0,0,1)
  Length = 1.6
  Length2 = 10
  Profile = -> Sketch144
  ReferenceAxis = -> Sketch144 [N_Axis]
  Type = 0
FEATURE [Sketcher::SketchObject] Sketch145
  ExternalGeometry = -> [Pad069]
  FullyConstrained = true
  MapMode = 5
  Placement = pos=(0,0,1.6) rot=(0,0,1;0rad)
  Support = -> [Pad069]
  sketch-geometry (4):
    g0: Circle CenterX=3.5 CenterY=26.5 CenterZ=0 NormalX=0 NormalY=0 NormalZ=1 AngleXU=0 Radius=1.5
    g1: Circle CenterX=3.5 CenterY=3.5 CenterZ=0 NormalX=0 NormalY=0 NormalZ=1 AngleXU=0 Radius=1.5
    g2: Circle CenterX=61.5 CenterY=3.5 CenterZ=0 NormalX=0 NormalY=0 NormalZ=1 AngleXU=0 Radius=1.5
    g3: Circle CenterX=61.5 CenterY=26.5 CenterZ=0 NormalX=0 NormalY=0 NormalZ=1 AngleXU=0 Radius=1.5
  constraints (12):
    c: Equal(g2,g3)
    c: Equal(g3,g0)
    c: Equal(g0,g1)
    c: Diameter(g2) = 3
    c: Horizontal(g1,g2)
    c: Horizontal(g3,g0)
    c: Vertical(g3,g2)
    c: Vertical(g0,g1)
    c: DistanceX(g1) = 3.5
    c: DistanceY(g1) = 3.5
    c: DistanceX(g1,g2) = 58
    c: DistanceY(g1,g0) = 23
FEATURE [PartDesign::Pocket] Pocket070
  BaseFeature = -> Pad069
  Direction = (0,0,-1)
  Length = 5
  Length2 = 5
  Profile = -> Sketch145
  ReferenceAxis = -> Sketch145 [N_Axis]
  Type = 0
FEATURE [Sketcher::SketchObject] Sketch146
  ExternalGeometry = -> [Pocket070]
  FullyConstrained = true
  MapMode = 5
  Placement = pos=(0,0,0) rot=(1,0,0;3.14159rad)
  Support = -> [Pocket070]
  sketch-geometry (6):
    g0: LineSegment StartX=6.875 StartY=-29 StartZ=0 EndX=58.125 EndY=-29 EndZ=0
    g1: LineSegment StartX=58.125 StartY=-29 StartZ=0 EndX=58.125 EndY=-24 EndZ=0
    g2: LineSegment StartX=58.125 StartY=-24 StartZ=0 EndX=6.875 EndY=-24 EndZ=0
    g3: LineSegment StartX=6.875 StartY=-24 StartZ=0 EndX=6.875 EndY=-29 EndZ=0
    g4: GeomPoint X=32.5 Y=-29 Z=0
    g5: GeomPoint X=6.875 Y=-26.5 Z=0
  constraints (14):
    c: Coincident(g0,g1)
    c: Coincident(g1,g2)
    c: Coincident(g2,g3)
    c: Coincident(g3,g0)
    c: Horizontal(g0)
    c: Horizontal(g2)
    c: Vertical(g1)
    c: Vertical(g3)
    c: DistanceX(g0,g0) = 51.25
    c: DistanceY(g3,g3) = 5
    c: Symmetric(g0,g0,g4)
    c: DistanceX(g-4,g4) = 29
    c: Symmetric(g3,g3,g5)
    c: Horizontal(g5,g-4)
FEATURE [PartDesign::Pad] Pad070
  BaseFeature = -> Pocket070
  Direction = (0,0,-1)
  Length = 30
  Length2 = 10
  Profile = -> Sketch146
  ReferenceAxis = -> Sketch146 [N_Axis]
  Type = 0
FEATURE [Sketcher::SketchObject] Sketch147
  ExternalGeometry = -> [Pad070]
  FullyConstrained = true
  MapMode = 5
  Placement = pos=(0,0,1.6) rot=(0,0,1;0rad)
  Support = -> [Pad070]
  sketch-geometry (10):
    g0: LineSegment StartX=6.5 StartY=30.6 StartZ=0 EndX=58.5 EndY=30.6 EndZ=0
    g1: LineSegment StartX=58.5 StartY=30.6 StartZ=0 EndX=58.5 EndY=24.1 EndZ=0
    g2: LineSegment StartX=58.5 StartY=24.1 StartZ=0 EndX=6.5 EndY=24.1 EndZ=0
    g3: LineSegment StartX=6.5 StartY=24.1 StartZ=0 EndX=6.5 EndY=30.6 EndZ=0
    g4: LineSegment StartX=8.5 StartY=0 StartZ=0 EndX=56.5 EndY=0 EndZ=0
    g5: LineSegment StartX=56.5 StartY=0 StartZ=0 EndX=56.5 EndY=8.5 EndZ=0
    g6: LineSegment StartX=56.5 StartY=8.5 StartZ=0 EndX=8.5 EndY=8.5 EndZ=0
    g7: LineSegment StartX=8.5 StartY=8.5 StartZ=0 EndX=8.5 EndY=0 EndZ=0
    g8: GeomPoint X=32.5 Y=8.5 Z=0
    g9: GeomPoint X=32.5 Y=24.1 Z=0
  constraints (26):
    c: Coincident(g0,g1)
    c: Coincident(g1,g2)
    c: Coincident(g2,g3)
    c: Coincident(g3,g0)
    c: Horizontal(g0)
    c: Horizontal(g2)
    c: Vertical(g1)
    c: Vertical(g3)
    c: PointOnObject(g0,g-3)
    c: Coincident(g4,g5)
    c: Coincident(g5,g6)
    c: Coincident(g6,g7)
    c: Coincident(g7,g4)
    c: Horizontal(g4)
    c: Horizontal(g6)
    c: Vertical(g5)
    c: Vertical(g7)
    c: PointOnObject(g4,g-1)
    c: DistanceY(g5,g5) = 8.5
    c: DistanceX(g4,g4) = 48
    c: DistanceX(g2,g2) = 52
    c: DistanceY(g1,g1) = 6.5
    c: Symmetric(g6,g6,g8)
    c: Symmetric(g2,g2,g9)
    c: Vertical(g9,g8)
    c: DistanceX(g-4,g9) = 29
FEATURE [PartDesign::Pad] Pad071
  BaseFeature = -> Pad070
  Direction = (0,0,1)
  Length = 20
  Length2 = 10
  Profile = -> Sketch147
  ReferenceAxis = -> Sketch147 [N_Axis]
  Type = 0
FEATURE [Sketcher::SketchObject] Sketch148
  FullyConstrained = true
  MapMode = 5
  Placement = pos=(0,0,1.6) rot=(0,0,1;0rad)
  Support = -> [Pad071]
  sketch-geometry (4):
    g0: LineSegment StartX=0 StartY=11.5 StartZ=0 EndX=7.5 EndY=11.5 EndZ=0
    g1: LineSegment StartX=7.5 StartY=11.5 StartZ=0 EndX=7.5 EndY=18.5 EndZ=0
    g2: LineSegment StartX=7.5 StartY=18.5 StartZ=0 EndX=0 EndY=18.5 EndZ=0
    g3: LineSegment StartX=0 StartY=18.5 StartZ=0 EndX=0 EndY=11.5 EndZ=0
  constraints (12):
    c: Coincident(g0,g1)
    c: Coincident(g1,g2)
    c: Coincident(g2,g3)
    c: Coincident(g3,g0)
    c: Horizontal(g0)
    c: Horizontal(g2)
    c: Vertical(g1)
    c: Vertical(g3)
    c: PointOnObject(g0,g-2)
    c: DistanceY(g0) = 11.5
    c: DistanceY(g1,g1) = 7
    c: DistanceX(g0,g0) = 7.5
FEATURE [PartDesign::Pad] Pad072
  BaseFeature = -> Pad071
  Direction = (0,0,1)
  Length = 9.5
  Length2 = 10
  Profile = -> Sketch148
  ReferenceAxis = -> Sketch148 [N_Axis]
  Type = 0
FEATURE [PartDesign::Body] Body029
  Group = -> [Sketch144,Pad069,Sketch145,Pocket070,Sketch146,Pad070,Sketch147,Pad071,Sketch148,Pad072]
  Origin = -> Origin028
  Tip = -> Pad072
FEATURE [Part::FeaturePython] Parts021  # WARN: FeaturePython — macro-defined, semantics opaque (R4)
  Group = -> [Body029]
  GroupMode = 0
FEATURE [App::FeaturePython] Constraints022  # WARN: FeaturePython — macro-defined, semantics opaque (R4)
  _Version = 1
FEATURE [Sketcher::SketchObject] Sketch149
  FullyConstrained = true
  MapMode = 5
  Support = -> [XY_Plane029]
  sketch-geometry (4):
    g0: LineSegment StartX=0 StartY=0 StartZ=0 EndX=85 EndY=0 EndZ=0
    g1: LineSegment StartX=85 StartY=0 StartZ=0 EndX=85 EndY=56 EndZ=0
    g2: LineSegment StartX=85 StartY=56 StartZ=0 EndX=0 EndY=56 EndZ=0
    g3: LineSegment StartX=0 StartY=56 StartZ=0 EndX=0 EndY=0 EndZ=0
  constraints (11):
    c: Coincident(g0,g1)
    c: Coincident(g1,g2)
    c: Coincident(g2,g3)
    c: Coincident(g3,g0)
    c: Horizontal(g0)
    c: Horizontal(g2)
    c: Vertical(g1)
    c: Vertical(g3)
    c: Coincident(g0,g-1)
    c: DistanceX(g0,g0) = 85
    c: DistanceY(g3,g3) = 56
FEATURE [PartDesign::Pad] Pad073
  Direction = (0,0,1)
  Length = 1.5
  Length2 = 10
  Profile = -> Sketch149
  ReferenceAxis = -> Sketch149 [N_Axis]
  Type = 0
FEATURE [Sketcher::SketchObject] Sketch150
  ExternalGeometry = -> [Pad073]
  FullyConstrained = true
  MapMode = 5
  Placement = pos=(0,0,1.5) rot=(0,0,1;0rad)
  Support = -> [Pad073]
  sketch-geometry (4):
    g0: Circle CenterX=3.5 CenterY=52.5 CenterZ=0 NormalX=0 NormalY=0 NormalZ=1 AngleXU=0 Radius=1.375
    g1: Circle CenterX=61.5 CenterY=52.5 CenterZ=0 NormalX=0 NormalY=0 NormalZ=1 AngleXU=0 Radius=1.375
    g2: Circle CenterX=3.5 CenterY=3.5 CenterZ=0 NormalX=0 NormalY=0 NormalZ=1 AngleXU=0 Radius=1.375
    g3: Circle CenterX=61.5 CenterY=3.5 CenterZ=0 NormalX=0 NormalY=0 NormalZ=1 AngleXU=0 Radius=1.375
  constraints (12):
    c: Equal(g0,g1)
    c: Equal(g1,g2)
    c: Equal(g2,g3)
    c: Diameter(g1) = 2.75
    c: Vertical(g0,g2)
    c: DistanceX(g2) = 3.5
    c: DistanceY(g2) = 3.5
    c: DistanceY(g0,g-3) = 3.5
    c: Horizontal(g3,g2)
    c: Horizontal(g1,g0)
    c: DistanceX(g0,g1) = 58
    c: Vertical(g3,g1)
FEATURE [PartDesign::Pocket] Pocket071
  BaseFeature = -> Pad073
  Direction = (0,0,-1)
  Length = 5
  Length2 = 5
  Profile = -> Sketch150
  ReferenceAxis = -> Sketch150 [N_Axis]
  Type = 0
FEATURE [Sketcher::SketchObject] Sketch151
  FullyConstrained = true
  MapMode = 5
  Placement = pos=(0,0,1.5) rot=(0,0,1;0rad)
  Support = -> [Pocket071]
  sketch-geometry (5):
    g0: LineSegment StartX=24.5 StartY=-1.5 StartZ=0 EndX=39.5 EndY=-1.5 EndZ=0
    g1: LineSegment StartX=39.5 StartY=-1.5 StartZ=0 EndX=39.5 EndY=10 EndZ=0
    g2: LineSegment StartX=39.5 StartY=10 StartZ=0 EndX=24.5 EndY=10 EndZ=0
    g3: LineSegment StartX=24.5 StartY=10 StartZ=0 EndX=24.5 EndY=-1.5 EndZ=0
    g4: GeomPoint X=32 Y=-1.5 Z=0
  constraints (13):
    c: Coincident(g0,g1)
    c: Coincident(g1,g2)
    c: Coincident(g2,g3)
    c: Coincident(g3,g0)
    c: Horizontal(g0)
    c: Horizontal(g2)
    c: Vertical(g1)
    c: Vertical(g3)
    c: DistanceX(g0,g0) = 15
    c: DistanceY(g1,g1) = 11.5
    c: DistanceY(g0) = -1.5
    c: Symmetric(g0,g0,g4)
    c: DistanceX(g4) = 32
FEATURE [PartDesign::Pad] Pad074
  BaseFeature = -> Pocket071
  Direction = (0,0,1)
  Length = 6.5
  Length2 = 0.5
  Profile = -> Sketch151
  ReferenceAxis = -> Sketch151 [N_Axis]
  Type = 0
FEATURE [Sketcher::SketchObject] Sketch152
  ExternalGeometry = -> [Pad074]
  FullyConstrained = true
  MapMode = 5
  Placement = pos=(0,0,1.5) rot=(0,0,1;0rad)
  Support = -> [Pad074]
  sketch-geometry (10):
    g0: LineSegment StartX=69.5 StartY=21.5 StartZ=0 EndX=87 EndY=21.5 EndZ=0
    g1: LineSegment StartX=87 StartY=21.5 StartZ=0 EndX=87 EndY=36.5 EndZ=0
    g2: LineSegment StartX=87 StartY=36.5 StartZ=0 EndX=69.5 EndY=36.5 EndZ=0
    g3: LineSegment StartX=69.5 StartY=36.5 StartZ=0 EndX=69.5 EndY=21.5 EndZ=0
    g4: LineSegment StartX=69.5 StartY=39.5 StartZ=0 EndX=87 EndY=39.5 EndZ=0
    g5: LineSegment StartX=87 StartY=39.5 StartZ=0 EndX=87 EndY=54.5 EndZ=0
    g6: LineSegment StartX=87 StartY=54.5 StartZ=0 EndX=69.5 EndY=54.5 EndZ=0
    g7: LineSegment StartX=69.5 StartY=54.5 StartZ=0 EndX=69.5 EndY=39.5 EndZ=0
    g8: GeomPoint X=87 Y=29 Z=0
    g9: GeomPoint X=87 Y=47 Z=0
  constraints (26):
    c: Coincident(g0,g1)
    c: Coincident(g1,g2)
    c: Coincident(g2,g3)
    c: Coincident(g3,g0)
    c: Horizontal(g0)
    c: Horizontal(g2)
    c: Vertical(g1)
    c: Vertical(g3)
    c: Coincident(g4,g5)
    c: Coincident(g5,g6)
    c: Coincident(g6,g7)
    c: Coincident(g7,g4)
    c: Horizontal(g4)
    c: Horizontal(g6)
    c: Vertical(g5)
    c: Vertical(g7)
    c: Equal(g5,g1)
    c: Equal(g0,g4)
    c: Vertical(g0,g4)
    c: Symmetric(g5,g5,g9)
    c: Symmetric(g1,g1,g8)
    c: DistanceY(g5,g5) = 15
    c: DistanceY(g9) = 47
    c: DistanceY(g8) = 29
    c: DistanceX(g-3,g0) = 2
    c: DistanceX(g0,g0) = 17.5
FEATURE [PartDesign::Pad] Pad075
  BaseFeature = -> Pad074
  Direction = (0,0,1)
  Length = 16
  Length2 = 10
  Profile = -> Sketch152
  ReferenceAxis = -> Sketch152 [N_Axis]
  Type = 0
FEATURE [Sketcher::SketchObject] Sketch153
  ExternalGeometry = -> [Pad075]
  FullyConstrained = true
  MapMode = 5
  Placement = pos=(0,0,1.5) rot=(0,0,1;0rad)
  Support = -> [Pad075]
  sketch-geometry (5):
    g0: LineSegment StartX=65.5 StartY=2.25 StartZ=0 EndX=87 EndY=2.25 EndZ=0
    g1: LineSegment StartX=87 StartY=2.25 StartZ=0 EndX=87 EndY=18.25 EndZ=0
    g2: LineSegment StartX=87 StartY=18.25 StartZ=0 EndX=65.5 EndY=18.25 EndZ=0
    g3: LineSegment StartX=65.5 StartY=18.25 StartZ=0 EndX=65.5 EndY=2.25 EndZ=0
    g4: GeomPoint X=87 Y=10.25 Z=0
  constraints (13):
    c: Coincident(g0,g1)
    c: Coincident(g1,g2)
    c: Coincident(g2,g3)
    c: Coincident(g3,g0)
    c: Horizontal(g0)
    c: Horizontal(g2)
    c: Vertical(g1)
    c: Vertical(g3)
    c: DistanceY(g1,g1) = 16
    c: DistanceX(g0,g0) = 21.5
    c: DistanceX(g-3,g0) = 2
    c: Symmetric(g1,g1,g4)
    c: DistanceY(g4) = 10.25
FEATURE [PartDesign::Pad] Pad076
  BaseFeature = -> Pad075
  Direction = (0,0,1)
  Length = 13.5
  Length2 = 10
  Profile = -> Sketch153
  ReferenceAxis = -> Sketch153 [N_Axis]
  Type = 0
FEATURE [Sketcher::SketchObject] Sketch154
  ExternalGeometry = -> [Pad076]
  FullyConstrained = true
  MapMode = 5
  Placement = pos=(0,0,1.5) rot=(0,0,1;0rad)
  Support = -> [Pad076]
  sketch-geometry (6):
    g0: LineSegment StartX=7.5 StartY=50 StartZ=0 EndX=57.5 EndY=50 EndZ=0
    g1: LineSegment StartX=57.5 StartY=50 StartZ=0 EndX=57.5 EndY=55 EndZ=0
    g2: LineSegment StartX=57.5 StartY=55 StartZ=0 EndX=7.5 EndY=55 EndZ=0
    g3: LineSegment StartX=7.5 StartY=55 StartZ=0 EndX=7.5 EndY=50 EndZ=0
    g4: GeomPoint X=32.5 Y=55 Z=0
    g5: GeomPoint X=7.5 Y=52.5 Z=0
  constraints (14):
    c: Coincident(g0,g1)
    c: Coincident(g1,g2)
    c: Coincident(g2,g3)
    c: Coincident(g3,g0)
    c: Horizontal(g0)
    c: Horizontal(g2)
    c: Vertical(g1)
    c: Vertical(g3)
    c: Symmetric(g2,g2,g4)
    c: DistanceX(g-3,g4) = 29
    c: DistanceY(g3,g3) = 5
    c: DistanceX(g0,g0) = 50
    c: Symmetric(g3,g3,g5)
    c: Horizontal(g5,g-3)
FEATURE [PartDesign::Pad] Pad077
  BaseFeature = -> Pad076
  Direction = (0,0,1)
  Length = 30
  Length2 = 10
  Profile = -> Sketch154
  ReferenceAxis = -> Sketch154 [N_Axis]
  Type = 0
FEATURE [Sketcher::SketchObject] Sketch155
  FullyConstrained = true
  MapMode = 5
  Placement = pos=(0,0,1.5) rot=(0,0,1;0rad)
  Support = -> [Pad077]
  sketch-geometry (5):
    g0: LineSegment StartX=6.6 StartY=4.5 StartZ=0 EndX=14.6 EndY=4.5 EndZ=0
    g1: LineSegment StartX=14.6 StartY=4.5 StartZ=0 EndX=14.6 EndY=-1.5 EndZ=0
    g2: LineSegment StartX=14.6 StartY=-1.5 StartZ=0 EndX=6.6 EndY=-1.5 EndZ=0
    g3: LineSegment StartX=6.6 StartY=-1.5 StartZ=0 EndX=6.6 EndY=4.5 EndZ=0
    g4: GeomPoint X=10.6 Y=-1.5 Z=0
  constraints (13):
    c: Coincident(g0,g1)
    c: Coincident(g1,g2)
    c: Coincident(g2,g3)
    c: Coincident(g3,g0)
    c: Horizontal(g0)
    c: Horizontal(g2)
    c: Vertical(g1)
    c: Vertical(g3)
    c: DistanceX(g2,g2) = 8
    c: DistanceY(g3,g3) = 6
    c: DistanceY(g2) = -1.5
    c: Symmetric(g2,g2,g4)
    c: DistanceX(g4) = 10.6
FEATURE [PartDesign::Pad] Pad078
  BaseFeature = -> Pad077
  Direction = (0,0,1)
  Length = 3
  Length2 = 0.5
  Profile = -> Sketch155
  ReferenceAxis = -> Sketch155 [N_Axis]
  Type = 4
FEATURE [Sketcher::SketchObject] Sketch156
  FullyConstrained = true
  MapMode = 5
  Placement = pos=(0,0,1.5) rot=(0,0,1;0rad)
  Support = -> [Pad078]
  sketch-geometry (5):
    g0: LineSegment StartX=49.875 StartY=12.5 StartZ=0 EndX=57.125 EndY=12.5 EndZ=0
    g1: LineSegment StartX=57.125 StartY=12.5 StartZ=0 EndX=57.125 EndY=-2.5 EndZ=0
    g2: LineSegment StartX=57.125 StartY=-2.5 StartZ=0 EndX=49.875 EndY=-2.5 EndZ=0
    g3: LineSegment StartX=49.875 StartY=-2.5 StartZ=0 EndX=49.875 EndY=12.5 EndZ=0
    g4: GeomPoint X=53.5 Y=-2.5 Z=0
  constraints (13):
    c: Coincident(g0,g1)
    c: Coincident(g1,g2)
    c: Coincident(g2,g3)
    c: Coincident(g3,g0)
    c: Horizontal(g0)
    c: Horizontal(g2)
    c: Vertical(g1)
    c: Vertical(g3)
    c: DistanceX(g2,g2) = 7.25
    c: Symmetric(g2,g2,g4)
    c: DistanceX(g4) = 53.5
    c: DistanceY(g1,g1) = 15
    c: DistanceY(g4) = -2.5
FEATURE [PartDesign::Pad] Pad079
  BaseFeature = -> Pad078
  Direction = (0,0,1)
  Length = 6
  Length2 = 10
  Profile = -> Sketch156
  ReferenceAxis = -> Sketch156 [N_Axis]
  Type = 0
FEATURE [Sketcher::SketchObject] Sketch157
  FullyConstrained = true
  MapMode = 5
  Placement = pos=(0,0,0) rot=(1,0,0;3.14159rad)
  Support = -> [Pad079]
  sketch-geometry (4):
    g0: LineSegment StartX=-3 StartY=-22 StartZ=0 EndX=12.8 EndY=-22 EndZ=0
    g1: LineSegment StartX=12.8 StartY=-22 StartZ=0 EndX=12.8 EndY=-34 EndZ=0
    g2: LineSegment StartX=12.8 StartY=-34 StartZ=0 EndX=-3 EndY=-34 EndZ=0
    g3: LineSegment StartX=-3 StartY=-34 StartZ=0 EndX=-3 EndY=-22 EndZ=0
  constraints (12):
    c: Coincident(g0,g1)
    c: Coincident(g1,g2)
    c: Coincident(g2,g3)
    c: Coincident(g3,g0)
    c: Horizontal(g0)
    c: Horizontal(g2)
    c: Vertical(g1)
    c: Vertical(g3)
    c: DistanceX(g2,g2) = 15.8
    c: DistanceY(g1,g1) = 12
    c: DistanceY(g0) = -22
    c: DistanceX(g0) = -3
FEATURE [PartDesign::Pad] Pad080
  BaseFeature = -> Pad079
  Direction = (0,0,-1)
  Length = 1.5
  Length2 = 10
  Profile = -> Sketch157
  ReferenceAxis = -> Sketch157 [N_Axis]
  Type = 0
FEATURE [Sketcher::SketchObject] Sketch158
  FullyConstrained = true
  MapMode = 5
  Placement = pos=(0,0,0) rot=(1,0,0;3.14159rad)
  Support = -> [Pad080]
  sketch-geometry (4):
    g0: LineSegment StartX=17 StartY=-10 StartZ=0 EndX=82 EndY=-10 EndZ=0
    g1: LineSegment StartX=82 StartY=-10 StartZ=0 EndX=82 EndY=-45 EndZ=0
    g2: LineSegment StartX=82 StartY=-45 StartZ=0 EndX=17 EndY=-45 EndZ=0
    g3: LineSegment StartX=17 StartY=-45 StartZ=0 EndX=17 EndY=-10 EndZ=0
  constraints (12):
    c: Coincident(g0,g1)
    c: Coincident(g1,g2)
    c: Coincident(g2,g3)
    c: Coincident(g3,g0)
    c: Horizontal(g0)
    c: Horizontal(g2)
    c: Vertical(g1)
    c: Vertical(g3)
    c: DistanceX(g0) = 17
    c: DistanceY(g0) = -10
    c: DistanceY(g1,g1) = 35
    c: DistanceX(g2,g2) = 65
FEATURE [PartDesign::Pad] Pad081
  BaseFeature = -> Pad080
  Direction = (0,0,-1)
  Length = 2.2
  Length2 = 10
  Profile = -> Sketch158
  ReferenceAxis = -> Sketch158 [N_Axis]
  Type = 0
FEATURE [PartDesign::Body] Body030
  Group = -> [Sketch149,Pad073,Sketch150,Pocket071,Sketch151,Pad074,Sketch152,Pad075,Sketch153,Pad076,Sketch154,Pad077,Sketch155,Pad078,Sketch156,Pad079,Sketch157,Pad080,Sketch158,Pad081]
  Origin = -> Origin029
  Tip = -> Pad081
FEATURE [Part::FeaturePython] Parts022  # WARN: FeaturePython — macro-defined, semantics opaque (R4)
  Group = -> [Body030]
  GroupMode = 0
FEATURE [App::FeaturePython] Constraints023  # WARN: FeaturePython — macro-defined, semantics opaque (R4)
  _Version = 1
FEATURE [App::FeaturePython] Elements023  # WARN: FeaturePython — macro-defined, semantics opaque (R4)
FEATURE [Sketcher::SketchObject] Sketch159
  FullyConstrained = true
  MapMode = 5
  Support = -> [XY_Plane030]
  sketch-geometry (4):
    g0: LineSegment StartX=0 StartY=0 StartZ=0 EndX=110 EndY=0 EndZ=0
    g1: LineSegment StartX=110 StartY=0 StartZ=0 EndX=110 EndY=73 EndZ=0
    g2: LineSegment StartX=110 StartY=73 StartZ=0 EndX=0 EndY=73 EndZ=0
    g3: LineSegment StartX=0 StartY=73 StartZ=0 EndX=0 EndY=0 EndZ=0
  constraints (11):
    c: Coincident(g0,g1)
    c: Coincident(g1,g2)
    c: Coincident(g2,g3)
    c: Coincident(g3,g0)
    c: Horizontal(g0)
    c: Horizontal(g2)
    c: Vertical(g1)
    c: Vertical(g3)
    c: Coincident(g0,g-1)
    c: DistanceY(g1,g1) = 73
    c: DistanceX(g0,g0) = 110
FEATURE [PartDesign::Pad] Pad082
  Direction = (0,0,1)
  Length = 37
  Length2 = 10
  Profile = -> Sketch159
  ReferenceAxis = -> Sketch159 [N_Axis]
  Type = 0
FEATURE [PartDesign::Thickness] Thickness
  Base = -> Pad082 [Face6]
  BaseFeature = -> Pad082
  Intersection = false
  Join = 0
  Mode = 0
  Reversed = true
  SupportTransform = false
  Value = 2.5
FEATURE [PartDesign::Body] Body031
  Group = -> [Sketch159,Pad082,Thickness]
  Origin = -> Origin030
  Tip = -> Thickness
FEATURE [Part::FeaturePython] Parts023  # WARN: FeaturePython — macro-defined, semantics opaque (R4)
  Group = -> [Body031]
  GroupMode = 0
FEATURE [Part::FeaturePython] Assembly023  label="assy-electronics_case"  # WARN: FeaturePython — macro-defined, semantics opaque (R4)
  AutoRelax = true
  BuildShape = 0
  Freeze = false
  Group = -> [Constraints023,Elements023,Parts023]
  Placement = pos=(309.57,-3.43882e-05,0) rot=(0,0,1;0rad)
  Verbose = false
  _SolverType = 1
  _Version = 1
FEATURE [App::FeaturePython] Constraints025  # WARN: FeaturePython — macro-defined, semantics opaque (R4)
  _Version = 1
FEATURE [Sketcher::SketchObject] Sketch160
  FullyConstrained = true
  MapMode = 5
  Support = -> [XY_Plane032]
  sketch-geometry (4):
    g0: LineSegment StartX=0 StartY=0 StartZ=0 EndX=120 EndY=0 EndZ=0
    g1: LineSegment StartX=120 StartY=0 StartZ=0 EndX=120 EndY=73 EndZ=0
    g2: LineSegment StartX=120 StartY=73 StartZ=0 EndX=0 EndY=73 EndZ=0
    g3: LineSegment StartX=0 StartY=73 StartZ=0 EndX=0 EndY=0 EndZ=0
  constraints (11):
    c: Coincident(g0,g1)
    c: Coincident(g1,g2)
    c: Coincident(g2,g3)
    c: Coincident(g3,g0)
    c: Horizontal(g0)
    c: Horizontal(g2)
    c: Vertical(g1)
    c: Vertical(g3)
    c: Coincident(g0,g-1)
    c: DistanceY(g1,g1) = 73
    c: DistanceX(g0,g0) = 120
FEATURE [PartDesign::Pad] Pad083
  Direction = (0,0,1)
  Length = 2.5
  Length2 = 10
  Profile = -> Sketch160
  ReferenceAxis = -> Sketch160 [N_Axis]
  Type = 0
FEATURE [Sketcher::SketchObject] Sketch161
  FullyConstrained = true
  MapMode = 5
  Support = -> [XY_Plane031]
  sketch-geometry (4):
    g0: LineSegment StartX=0 StartY=0 StartZ=0 EndX=120 EndY=0 EndZ=0
    g1: LineSegment StartX=120 StartY=0 StartZ=0 EndX=120 EndY=73 EndZ=0
    g2: LineSegment StartX=120 StartY=73 StartZ=0 EndX=0 EndY=73 EndZ=0
    g3: LineSegment StartX=0 StartY=73 StartZ=0 EndX=0 EndY=0 EndZ=0
  constraints (11):
    c: Coincident(g0,g1)
    c: Coincident(g1,g2)
    c: Coincident(g2,g3)
    c: Coincident(g3,g0)
    c: Horizontal(g0)
    c: Horizontal(g2)
    c: Vertical(g1)
    c: Vertical(g3)
    c: Coincident(g0,g-1)
    c: DistanceY(g1,g1) = 73
    c: DistanceX(g0,g0) = 120
FEATURE [PartDesign::Pad] Pad084
  Direction = (0,0,1)
  Length = 2.5
  Length2 = 10
  Profile = -> Sketch161
  ReferenceAxis = -> Sketch161 [N_Axis]
  Type = 0
FEATURE [Sketcher::SketchObject] Sketch162
  ExternalGeometry = -> [Pad083]
  FullyConstrained = true
  MapMode = 5
  Placement = pos=(0,0,2.5) rot=(0,0,1;0rad)
  Support = -> [Pad083]
  sketch-geometry (14):
    g0: LineSegment StartX=0 StartY=73 StartZ=0 EndX=120 EndY=73 EndZ=0
    g1: LineSegment StartX=0 StartY=70.5 StartZ=0 EndX=0 EndY=73 EndZ=0
    g2: LineSegment StartX=22 StartY=70.5 StartZ=0 EndX=22 EndY=63.5 EndZ=0
    g3: LineSegment StartX=22 StartY=63.5 StartZ=0 EndX=15 EndY=63.5 EndZ=0
    g4: LineSegment StartX=15 StartY=63.5 StartZ=0 EndX=15 EndY=70.5 EndZ=0
    g5: LineSegment StartX=15 StartY=70.5 StartZ=0 EndX=0 EndY=70.5 EndZ=0
    g6: LineSegment StartX=15 StartY=11.5 StartZ=0 EndX=22 EndY=11.5 EndZ=0
    g7: LineSegment StartX=22 StartY=11.5 StartZ=0 EndX=22 EndY=4 EndZ=0
    g8: LineSegment StartX=22 StartY=4 StartZ=0 EndX=15 EndY=4 EndZ=0
    g9: LineSegment StartX=15 StartY=4 StartZ=0 EndX=15 EndY=11.5 EndZ=0
    g10: LineSegment StartX=22 StartY=70.5 StartZ=0 EndX=104.5 EndY=70.5 EndZ=0
    g11: LineSegment StartX=104.5 StartY=70.5 StartZ=0 EndX=110 EndY=65 EndZ=0
    g12: LineSegment StartX=110 StartY=65 StartZ=0 EndX=120 EndY=65 EndZ=0
    g13: LineSegment StartX=120 StartY=65 StartZ=0 EndX=120 EndY=73 EndZ=0
  constraints (40):
    c: Coincident(g0,g-6)
    c: Coincident(g0,g-6)
    c: PointOnObject(g5,g-3)
    c: Coincident(g1,g5)
    c: Coincident(g1,g0)
    c: Coincident(g2,g3)
    c: Coincident(g3,g4)
    c: Horizontal(g3)
    c: Vertical(g2)
    c: Vertical(g4)
    c: DistanceX(g4) = 15
    c: DistanceX(g3,g3) = 7
    c: DistanceY(g2,g2) = 7
    c: Coincident(g4,g5)
    c: Horizontal(g5)
    c: Horizontal(g4,g2)
    c: Coincident(g6,g7)
    c: Coincident(g7,g8)
    c: Coincident(g8,g9)
    c: Coincident(g9,g6)
    c: Horizontal(g6)
    c: Horizontal(g8)
    c: Vertical(g7)
    c: Vertical(g9)
    c: Vertical(g6,g3)
    c: Vertical(g6,g2)
    c: DistanceY(g8) = 4
    c: DistanceY(g9,g9) = 7.5
    c: Coincident(g10,g2)
    c: Horizontal(g10)
    c: Coincident(g11,g10)
    c: Coincident(g12,g11)
    c: PointOnObject(g12,g-5)
    c: Horizontal(g12)
    c: Coincident(g13,g12)
    c: Coincident(g13,g0)
    c: DistanceX(g12,g12) = 10
    c: DistanceY(g13,g13) = 8
    c: DistanceY(g10,g0) = 2.5
    c: Angle(g10,g11) = 2.35619
FEATURE [PartDesign::Pad] Pad085
  BaseFeature = -> Pad083
  Direction = (0,0,1)
  Length = 35
  Length2 = 10
  Profile = -> Sketch162
  ReferenceAxis = -> Sketch162 [N_Axis]
  Type = 0
FEATURE [Sketcher::SketchObject] Sketch163
  ExternalGeometry = -> [Pad084]
  FullyConstrained = true
  MapMode = 5
  Placement = pos=(0,0,0) rot=(1,0,0;3.14159rad)
  Support = -> [Pad084]
  sketch-geometry (6):
    g0: LineSegment StartX=0 StartY=0 StartZ=0 EndX=120 EndY=0 EndZ=0
    g1: LineSegment StartX=120 StartY=0 StartZ=0 EndX=120 EndY=-64.9 EndZ=0
    g2: LineSegment StartX=120 StartY=-64.9 StartZ=0 EndX=117.5 EndY=-64.9 EndZ=0
    g3: LineSegment StartX=117.5 StartY=-64.9 StartZ=0 EndX=117.5 EndY=-2.5 EndZ=0
    g4: LineSegment StartX=117.5 StartY=-2.5 StartZ=0 EndX=0 EndY=-2.5 EndZ=0
    g5: LineSegment StartX=0 StartY=-2.5 StartZ=0 EndX=0 EndY=0 EndZ=0
  constraints (16):
    c: Coincident(g0,g-5)
    c: Coincident(g0,g-4)
    c: Coincident(g1,g0)
    c: PointOnObject(g1,g-4)
    c: Coincident(g2,g1)
    c: Horizontal(g2)
    c: Coincident(g3,g2)
    c: Vertical(g3)
    c: Coincident(g4,g3)
    c: PointOnObject(g4,g-5)
    c: Horizontal(g4)
    c: Coincident(g5,g4)
    c: Coincident(g5,g0)
    c: DistanceY(g5,g5) = 2.5
    c: DistanceX(g2,g2) = 2.5
    c: DistanceY(g-4,g1) = 8.1
FEATURE [PartDesign::Pad] Pad086
  BaseFeature = -> Pad084
  Direction = (0,0,-1)
  Length = 35
  Length2 = 10
  Profile = -> Sketch163
  ReferenceAxis = -> Sketch163 [N_Axis]
  Type = 0
FEATURE [App::FeaturePython] Constraints026  # WARN: FeaturePython — macro-defined, semantics opaque (R4)
  _Version = 1
FEATURE [Sketcher::SketchObject] Sketch164
  FullyConstrained = true
  MapMode = 5
  Support = -> [XY_Plane033]
  sketch-geometry (1):
    g0: Circle CenterX=0 CenterY=0 CenterZ=0 NormalX=0 NormalY=0 NormalZ=1 AngleXU=0 Radius=6.175
  constraints (2):
    c: Coincident(g0,g-1)
    c: Diameter(g0) = 12.35
FEATURE [PartDesign::Pad] Pad087
  Direction = (0,0,1)
  Length = 2
  Length2 = 10
  Profile = -> Sketch164
  ReferenceAxis = -> Sketch164 [N_Axis]
  Type = 0
FEATURE [Sketcher::SketchObject] Sketch165
  FullyConstrained = true
  MapMode = 5
  Placement = pos=(0,0,0) rot=(1,0,0;3.14159rad)
  Support = -> [Pad087]
  sketch-geometry (1):
    g0: Circle CenterX=0 CenterY=0 CenterZ=0 NormalX=0 NormalY=0 NormalZ=1 AngleXU=0 Radius=5.25
  constraints (2):
    c: Coincident(g0,g-1)
    c: Diameter(g0) = 10.5
FEATURE [PartDesign::Pad] Pad088
  BaseFeature = -> Pad087
  Direction = (0,0,-1)
  Length = 14.5
  Length2 = 10
  Profile = -> Sketch165
  ReferenceAxis = -> Sketch165 [N_Axis]
  Type = 0
FEATURE [Sketcher::SketchObject] Sketch166
  FullyConstrained = true
  MapMode = 5
  Placement = pos=(0,0,2) rot=(0,0,1;0rad)
  Support = -> [Pad088]
  sketch-geometry (1):
    g0: Circle CenterX=0 CenterY=0 CenterZ=0 NormalX=0 NormalY=0 NormalZ=1 AngleXU=0 Radius=2.8
  constraints (2):
    c: Coincident(g0,g-1)
    c: Diameter(g0) = 5.6
FEATURE [PartDesign::Pocket] Pocket072
  BaseFeature = -> Pad088
  Direction = (0,0,-1)
  Length = 5
  Length2 = 5
  Profile = -> Sketch166
  ReferenceAxis = -> Sketch166 [N_Axis]
  Type = 0
FEATURE [Sketcher::SketchObject] Sketch167
  FullyConstrained = true
  MapMode = 5
  Placement = pos=(0,0,-14.5) rot=(1,0,0;3.14159rad)
  Support = -> [Pocket072]
  sketch-geometry (4):
    g0: LineSegment StartX=-1.5 StartY=0 StartZ=0 EndX=1.5 EndY=0 EndZ=0
    g1: LineSegment StartX=1.5 StartY=0 StartZ=0 EndX=1.5 EndY=4.5 EndZ=0
    g2: LineSegment StartX=1.5 StartY=4.5 StartZ=0 EndX=-1.5 EndY=4.5 EndZ=0
    g3: LineSegment StartX=-1.5 StartY=4.5 StartZ=0 EndX=-1.5 EndY=0 EndZ=0
  constraints (11):
    c: Coincident(g0,g1)
    c: Coincident(g1,g2)
    c: Coincident(g2,g3)
    c: Coincident(g3,g0)
    c: Horizontal(g0)
    c: Horizontal(g2)
    c: Vertical(g1)
    c: Vertical(g3)
    c: Symmetric(g0,g0,g-1)
    c: DistanceY(g3,g3) = 4.5
    c: DistanceX(g0,g0) = 3
FEATURE [PartDesign::Pad] Pad089
  BaseFeature = -> Pocket072
  Direction = (0,0,-1)
  Length = 10
  Length2 = 10
  Profile = -> Sketch167
  ReferenceAxis = -> Sketch167 [N_Axis]
  Type = 0
FEATURE [Sketcher::SketchObject] Sketch168
  FullyConstrained = true
  MapMode = 5
  Placement = pos=(0,0,-14.5) rot=(1,0,0;3.14159rad)
  Support = -> [Pad089]
  sketch-geometry (7):
    g0: LineSegment StartX=3.89711 StartY=6.75 StartZ=0 EndX=-3.89711 EndY=6.75 EndZ=0
    g1: LineSegment StartX=-3.89711 StartY=6.75 StartZ=0 EndX=-7.79423 EndY=2.9177e-12 EndZ=0
    g2: LineSegment StartX=-7.79423 StartY=2.9177e-12 StartZ=0 EndX=-3.89711 EndY=-6.75 EndZ=0
    g3: LineSegment StartX=-3.89711 StartY=-6.75 StartZ=0 EndX=3.89711 EndY=-6.75 EndZ=0
    g4: LineSegment StartX=3.89711 StartY=-6.75 StartZ=0 EndX=7.79423 EndY=2.3404e-12 EndZ=0
    g5: LineSegment StartX=7.79423 StartY=2.3404e-12 StartZ=0 EndX=3.89711 EndY=6.75 EndZ=0
    g6: Circle CenterX=0 CenterY=0 CenterZ=0 NormalX=0 NormalY=0 NormalZ=1 AngleXU=0 Radius=7.79423
  constraints (16):
    c: Coincident(g0,g1)
    c: Coincident(g1,g2)
    c: Coincident(g2,g3)
    c: Coincident(g3,g4)
    c: Coincident(g4,g5)
    c: Coincident(g5,g0)
    c: Equal(g0, g1-g5) x5
    c: PointOnObject(g0,g6)
    c: PointOnObject(g1,g6)
    c: PointOnObject(g2,g6)
    c: PointOnObject(g3,g6)
    c: PointOnObject(g4,g6)
    c: PointOnObject(g5,g6)
    c: Coincident(g6,g-1)
    c: Horizontal(g0)
    c: DistanceY(g3,g0) = 13.5
FEATURE [PartDesign::Pad] Pad090
  BaseFeature = -> Pad089
  Direction = (0,0,-1)
  Length = 2
  Length2 = 10
  Profile = -> Sketch168
  ReferenceAxis = -> Sketch168 [N_Axis]
  Reversed = true
  Type = 0
FEATURE [PartDesign::Body] Body034
  Group = -> [Sketch164,Pad087,Sketch165,Pad088,Sketch166,Pocket072,Sketch167,Pad089,Sketch168,Pad090]
  Origin = -> Origin033
  Tip = -> Pad090
FEATURE [Part::FeaturePython] Parts026  # WARN: FeaturePython — macro-defined, semantics opaque (R4)
  Group = -> [Body034]
  GroupMode = 0
FEATURE [Sketcher::SketchObject] Sketch169
  ExternalGeometry = -> [Pad085]
  FullyConstrained = true
  MapMode = 5
  Placement = pos=(120,-2.136e-13,0) rot=(0.57735,0.57735,0.57735;2.0944rad)
  Support = -> [Pad085]
  sketch-geometry (4):
    g0: LineSegment StartX=65 StartY=0 StartZ=0 EndX=73 EndY=0 EndZ=0
    g1: LineSegment StartX=73 StartY=0 StartZ=0 EndX=73 EndY=37.5 EndZ=0
    g2: LineSegment StartX=73 StartY=37.5 StartZ=0 EndX=65 EndY=37.5 EndZ=0
    g3: LineSegment StartX=65 StartY=37.5 StartZ=0 EndX=65 EndY=0 EndZ=0
  constraints (11):
    c: Coincident(g0,g1)
    c: Coincident(g1,g2)
    c: Coincident(g2,g3)
    c: Coincident(g3,g0)
    c: Horizontal(g0)
    c: Horizontal(g2)
    c: Vertical(g1)
    c: Vertical(g3)
    c: PointOnObject(g0,g-1)
    c: Coincident(g1,g-3)
    c: DistanceX(g0,g0) = 8
FEATURE [PartDesign::Pad] Pad091
  BaseFeature = -> Pad085
  Direction = (1,-1.8e-15,0)
  Length = 14
  Length2 = 10
  Profile = -> Sketch169
  ReferenceAxis = -> Sketch169 [N_Axis]
  Type = 0
FEATURE [Sketcher::SketchObject] Sketch170
  ExternalGeometry = -> [Pad091]
  FullyConstrained = true
  MapMode = 5
  Placement = pos=(1.157e-13,65,0) rot=(1,0,0;1.5708rad)
  Support = -> [Pad091]
  sketch-geometry (4):
    g0: ArcOfCircle CenterX=126 CenterY=29.5 CenterZ=0 NormalX=0 NormalY=0 NormalZ=1 AngleXU=0 Radius=6 StartAngle=-9e-16 EndAngle=3.14159
    g1: ArcOfCircle CenterX=126 CenterY=8 CenterZ=0 NormalX=0 NormalY=0 NormalZ=1 AngleXU=0 Radius=6 StartAngle=3.14159 EndAngle=6.28319
    g2: LineSegment StartX=120 StartY=29.5 StartZ=0 EndX=120 EndY=8 EndZ=0
    g3: LineSegment StartX=132 StartY=8 StartZ=0 EndX=132 EndY=29.5 EndZ=0
  constraints (10):
    c: Tangent(g0,g2) = -1.5708
    c: Tangent(g2,g1) = -1.5708
    c: Tangent(g1,g3) = -1.5708
    c: Tangent(g3,g0) = -1.5708
    c: Equal(g0,g1)
    c: Vertical(g2)
    c: Diameter(g1) = 12
    c: PointOnObject(g0,g-3)
    c: DistanceY(g0,g-3) = 8
    c: DistanceY(g1) = 8
FEATURE [PartDesign::Pocket] Pocket073
  BaseFeature = -> Pad091
  Direction = (1.8e-15,1,-2e-16)
  Length = 5
  Length2 = 5
  Profile = -> Sketch170
  ReferenceAxis = -> Sketch170 [N_Axis]
  Type = 0
FEATURE [Sketcher::SketchObject] Sketch171
  ExternalGeometry = -> [Pocket073]
  FullyConstrained = true
  MapMode = 5
  Placement = pos=(9.1e-14,70,0) rot=(1,0,0;1.5708rad)
  Support = -> [Pocket073]
  sketch-geometry (4):
    g0: Circle CenterX=126 CenterY=29.5 CenterZ=0 NormalX=0 NormalY=0 NormalZ=1 AngleXU=0 Radius=3.15
    g1: Circle CenterX=126 CenterY=18.75 CenterZ=0 NormalX=0 NormalY=0 NormalZ=1 AngleXU=0 Radius=3.15
    g2: Circle CenterX=126 CenterY=8 CenterZ=0 NormalX=0 NormalY=0 NormalZ=1 AngleXU=0 Radius=3.15
    g3: LineSegment StartX=126 StartY=8 StartZ=0 EndX=126 EndY=29.5 EndZ=0
  constraints (8):
    c: Coincident(g0,g-4)
    c: Coincident(g2,g-3)
    c: Equal(g2,g1)
    c: Equal(g1,g0)
    c: Coincident(g3,g2)
    c: Coincident(g3,g0)
    c: Symmetric(g3,g3,g1)
    c: Diameter(g1) = 6.3
FEATURE [PartDesign::Pocket] Pocket074
  BaseFeature = -> Pocket073
  Direction = (1.3e-15,1,-2e-16)
  Length = 5
  Length2 = 5
  Profile = -> Sketch171
  ReferenceAxis = -> Sketch171 [N_Axis]
  Type = 0
FEATURE [Sketcher::SketchObject] Sketch172
  ExternalGeometry = -> [Pocket074]
  FullyConstrained = true
  MapMode = 5
  Placement = pos=(0,0,2.5) rot=(0,0,1;0rad)
  Support = -> [Pocket074]
  sketch-geometry (4):
    g0: Circle CenterX=33.7 CenterY=57.6 CenterZ=0 NormalX=0 NormalY=0 NormalZ=1 AngleXU=0 Radius=3
    g1: Circle CenterX=91.7 CenterY=57.6 CenterZ=0 NormalX=0 NormalY=0 NormalZ=1 AngleXU=0 Radius=3
    g2: Circle CenterX=91.7 CenterY=8.6 CenterZ=0 NormalX=0 NormalY=0 NormalZ=1 AngleXU=0 Radius=3
    g3: Circle CenterX=33.7 CenterY=8.6 CenterZ=0 NormalX=0 NormalY=0 NormalZ=1 AngleXU=0 Radius=3
  constraints (12):
    c: Equal(g0,g1)
    c: Equal(g1,g2)
    c: Equal(g2,g3)
    c: Diameter(g2) = 6
    c: DistanceX(g2,g-3) = 28.3
    c: DistanceX(g3,g2) = 58
    c: Horizontal(g3,g2)
    c: Vertical(g1,g2)
    c: Horizontal(g1,g0)
    c: DistanceY(g2,g1) = 49
    c: Vertical(g0,g3)
    c: DistanceY(g2) = 8.6
FEATURE [PartDesign::Pad] Pad092
  BaseFeature = -> Pocket074
  Direction = (0,0,1)
  Length = 3
  Length2 = 10
  Profile = -> Sketch172
  ReferenceAxis = -> Sketch172 [N_Axis]
  Type = 0
FEATURE [Sketcher::SketchObject] Sketch173
  ExternalGeometry = -> [Pad092]
  FullyConstrained = true
  MapMode = 5
  Placement = pos=(0,0,5.5) rot=(0,0,1;0rad)
  Support = -> [Pad092]
  sketch-geometry (4):
    g0: Circle CenterX=33.7 CenterY=57.6 CenterZ=0 NormalX=0 NormalY=0 NormalZ=1 AngleXU=0 Radius=1.45
    g1: Circle CenterX=91.7 CenterY=57.6 CenterZ=0 NormalX=0 NormalY=0 NormalZ=1 AngleXU=0 Radius=1.45
    g2: Circle CenterX=91.7 CenterY=8.6 CenterZ=0 NormalX=0 NormalY=0 NormalZ=1 AngleXU=0 Radius=1.45
    g3: Circle CenterX=33.7 CenterY=8.6 CenterZ=0 NormalX=0 NormalY=0 NormalZ=1 AngleXU=0 Radius=1.45
  constraints (8):
    c: Coincident(g0,g-3)
    c: Coincident(g1,g-4)
    c: Coincident(g2,g-5)
    c: Coincident(g3,g-6)
    c: Equal(g0,g1)
    c: Equal(g1,g2)
    c: Equal(g2,g3)
    c: Diameter(g1) = 2.9
FEATURE [PartDesign::Pocket] Pocket075
  BaseFeature = -> Pad092
  Direction = (0,0,-1)
  Length = 5
  Length2 = 5
  Profile = -> Sketch173
  ReferenceAxis = -> Sketch173 [N_Axis]
  Type = 1
FEATURE [Sketcher::SketchObject] Sketch174
  FullyConstrained = true
  MapMode = 5
  Placement = pos=(15,0,0) rot=(0.57735,-0.57735,-0.57735;2.0944rad)
  Support = -> [Pocket075]
  sketch-geometry (4):
    g0: Circle CenterX=-66.6 CenterY=30 CenterZ=0 NormalX=0 NormalY=0 NormalZ=1 AngleXU=0 Radius=1.65
    g1: Circle CenterX=-66.6 CenterY=7 CenterZ=0 NormalX=0 NormalY=0 NormalZ=1 AngleXU=0 Radius=1.65
    g2: Circle CenterX=-8.6 CenterY=30 CenterZ=0 NormalX=0 NormalY=0 NormalZ=1 AngleXU=0 Radius=1.65
    g3: Circle CenterX=-8.6 CenterY=7 CenterZ=0 NormalX=0 NormalY=0 NormalZ=1 AngleXU=0 Radius=1.65
  constraints (12):
    c: Vertical(g2,g3)
    c: Horizontal(g0,g2)
    c: Horizontal(g1,g3)
    c: Vertical(g1,g0)
    c: Equal(g0,g1)
    c: Equal(g1,g2)
    c: Equal(g2,g3)
    c: Diameter(g2) = 3.3
    c: DistanceX(g3) = -8.6
    c: DistanceX(g1,g3) = 58
    c: DistanceY(g3,g2) = 23
    c: DistanceY(g3) = 7
FEATURE [PartDesign::Pocket] Pocket076
  BaseFeature = -> Pocket075
  Direction = (1,0,0)
  Length = 10
  Length2 = 5
  Profile = -> Sketch174
  ReferenceAxis = -> Sketch174 [N_Axis]
  Type = 0
FEATURE [Sketcher::SketchObject] Sketch175
  ExternalGeometry = -> [Pocket076]
  FullyConstrained = true
  MapMode = 5
  Placement = pos=(22,0,0) rot=(0.57735,0.57735,0.57735;2.0944rad)
  Support = -> [Pocket076]
  sketch-geometry (28):
    g0: LineSegment StartX=11.35 StartY=31.5877 StartZ=0 EndX=8.6 EndY=33.1754 EndZ=0
    g1: LineSegment StartX=8.6 StartY=33.1754 StartZ=0 EndX=5.85 EndY=31.5877 EndZ=0
    g2: LineSegment StartX=5.85 StartY=31.5877 StartZ=0 EndX=5.85 EndY=28.4123 EndZ=0
    g3: LineSegment StartX=5.85 StartY=28.4123 StartZ=0 EndX=8.6 EndY=26.8246 EndZ=0
    g4: LineSegment StartX=8.6 StartY=26.8246 StartZ=0 EndX=11.35 EndY=28.4123 EndZ=0
    g5: LineSegment StartX=11.35 StartY=28.4123 StartZ=0 EndX=11.35 EndY=31.5877 EndZ=0
    g6: Circle CenterX=8.6 CenterY=30 CenterZ=0 NormalX=0 NormalY=0 NormalZ=1 AngleXU=0 Radius=3.17543
    g7: LineSegment StartX=11.35 StartY=8.58771 StartZ=0 EndX=8.6 EndY=10.1754 EndZ=0
    g8: LineSegment StartX=8.6 StartY=10.1754 StartZ=0 EndX=5.85 EndY=8.58771 EndZ=0
    g9: LineSegment StartX=5.85 StartY=8.58771 StartZ=0 EndX=5.85 EndY=5.41229 EndZ=0
    g10: LineSegment StartX=5.85 StartY=5.41229 StartZ=0 EndX=8.6 EndY=3.82457 EndZ=0
    g11: LineSegment StartX=8.6 StartY=3.82457 StartZ=0 EndX=11.35 EndY=5.41229 EndZ=0
    g12: LineSegment StartX=11.35 StartY=5.41229 StartZ=0 EndX=11.35 EndY=8.58771 EndZ=0
    g13: Circle CenterX=8.6 CenterY=7 CenterZ=0 NormalX=0 NormalY=0 NormalZ=1 AngleXU=0 Radius=3.17543
    g14: LineSegment StartX=69.35 StartY=31.5877 StartZ=0 EndX=66.6 EndY=33.1754 EndZ=0
    g15: LineSegment StartX=66.6 StartY=33.1754 StartZ=0 EndX=63.85 EndY=31.5877 EndZ=0
    g16: LineSegment StartX=63.85 StartY=31.5877 StartZ=0 EndX=63.85 EndY=28.4123 EndZ=0
    g17: LineSegment StartX=63.85 StartY=28.4123 StartZ=0 EndX=66.6 EndY=26.8246 EndZ=0
    g18: LineSegment StartX=66.6 StartY=26.8246 StartZ=0 EndX=69.35 EndY=28.4123 EndZ=0
    g19: LineSegment StartX=69.35 StartY=28.4123 StartZ=0 EndX=69.35 EndY=31.5877 EndZ=0
    g20: Circle CenterX=66.6 CenterY=30 CenterZ=0 NormalX=0 NormalY=0 NormalZ=1 AngleXU=0 Radius=3.17543
    g21: LineSegment StartX=69.35 StartY=8.58771 StartZ=0 EndX=66.6 EndY=10.1754 EndZ=0
    g22: LineSegment StartX=66.6 StartY=10.1754 StartZ=0 EndX=63.85 EndY=8.58771 EndZ=0
    g23: LineSegment StartX=63.85 StartY=8.58771 StartZ=0 EndX=63.85 EndY=5.41229 EndZ=0
    g24: LineSegment StartX=63.85 StartY=5.41229 StartZ=0 EndX=66.6 EndY=3.82457 EndZ=0
    g25: LineSegment StartX=66.6 StartY=3.82457 StartZ=0 EndX=69.35 EndY=5.41229 EndZ=0
    g26: LineSegment StartX=69.35 StartY=5.41229 StartZ=0 EndX=69.35 EndY=8.58771 EndZ=0
    g27: Circle CenterX=66.6 CenterY=7 CenterZ=0 NormalX=0 NormalY=0 NormalZ=1 AngleXU=0 Radius=3.17543
  constraints (64):
    c: Coincident(g0,g1)
    c: Coincident(g1,g2)
    c: Coincident(g2,g3)
    c: Coincident(g3,g4)
    c: Coincident(g4,g5)
    c: Coincident(g5,g0)
    c: Equal(g0, g1-g5) x5
    c: PointOnObject(g0,g6)
    c: PointOnObject(g1,g6)
    c: PointOnObject(g2,g6)
    c: PointOnObject(g3,g6)
    c: PointOnObject(g4,g6)
    c: PointOnObject(g5,g6)
    c: Coincident(g6,g-3)
    c: Coincident(g7,g8)
    c: Coincident(g8,g9)
    c: Coincident(g9,g10)
    c: Coincident(g10,g11)
    c: Coincident(g11,g12)
    c: Coincident(g12,g7)
    c: Equal(g7, g8-g12) x5
    c: PointOnObject(g7,g13)
    c: PointOnObject(g8,g13)
    c: PointOnObject(g9,g13)
    c: PointOnObject(g10,g13)
    c: PointOnObject(g11,g13)
    c: PointOnObject(g12,g13)
    c: Coincident(g13,g-6)
    c: Coincident(g14,g15)
    c: Coincident(g15,g16)
    c: Coincident(g16,g17)
    c: Coincident(g17,g18)
    c: Coincident(g18,g19)
    c: Coincident(g19,g14)
    c: Equal(g14, g15-g19) x5
    c: PointOnObject(g14,g20)
    c: PointOnObject(g15,g20)
    c: PointOnObject(g16,g20)
    c: PointOnObject(g17,g20)
    c: PointOnObject(g18,g20)
    c: PointOnObject(g19,g20)
    c: Coincident(g20,g-4)
    c: Coincident(g21,g22)
    c: Coincident(g22,g23)
    c: Coincident(g23,g24)
    c: Coincident(g24,g25)
    c: Coincident(g25,g26)
    c: Coincident(g26,g21)
    c: Equal(g21, g22-g26) x5
    c: PointOnObject(g21,g27)
    c: PointOnObject(g22,g27)
    c: PointOnObject(g23,g27)
    c: PointOnObject(g24,g27)
    c: PointOnObject(g25,g27)
    c: PointOnObject(g26,g27)
    c: Coincident(g27,g-5)
    c: Vertical(g12)
    c: Vertical(g5)
    c: Vertical(g19)
    c: Vertical(g26)
    c: Equal(g27,g20)
    c: Equal(g20,g6)
    c: Equal(g6,g13)
    c: Distance(g7,g9) = 5.5
FEATURE [PartDesign::Pocket] Pocket077
  BaseFeature = -> Pocket076
  Direction = (-1,0,0)
  Length = 2.75
  Length2 = 5
  Profile = -> Sketch175
  ReferenceAxis = -> Sketch175 [N_Axis]
  Type = 0
FEATURE [Sketcher::SketchObject] Sketch176
  ExternalGeometry = -> [Pocket077]
  FullyConstrained = true
  MapMode = 5
  Placement = pos=(22,0,0) rot=(0.57735,0.57735,0.57735;2.0944rad)
  Support = -> [Pocket077]
  sketch-geometry (8):
    g0: LineSegment StartX=11.5 StartY=14.5 StartZ=0 EndX=13.1 EndY=12.0751 EndZ=0
    g1: LineSegment StartX=13.1 StartY=12.0751 StartZ=0 EndX=13.1 EndY=2.5 EndZ=0
    g2: LineSegment StartX=11.5 StartY=2.5 StartZ=0 EndX=13.1 EndY=2.5 EndZ=0
    g3: LineSegment StartX=11.5 StartY=2.5 StartZ=0 EndX=11.5 EndY=14.5 EndZ=0
    g4: LineSegment StartX=63.5 StartY=2.5 StartZ=0 EndX=63.5 EndY=14.5 EndZ=0
    g5: LineSegment StartX=63.5 StartY=14.5 StartZ=0 EndX=62.1 EndY=12.0751 EndZ=0
    g6: LineSegment StartX=62.1 StartY=12.0751 StartZ=0 EndX=62.1 EndY=2.5 EndZ=0
    g7: LineSegment StartX=62.1 StartY=2.5 StartZ=0 EndX=63.5 EndY=2.5 EndZ=0
  constraints (22):
    c: PointOnObject(g0,g-6)
    c: Coincident(g1,g0)
    c: Vertical(g1)
    c: Coincident(g2,g-6)
    c: Horizontal(g2)
    c: Coincident(g3,g2)
    c: Coincident(g3,g0)
    c: Coincident(g1,g2)
    c: DistanceX(g-3,g1) = 4.5
    c: Coincident(g4,g-5)
    c: PointOnObject(g4,g-5)
    c: Coincident(g5,g4)
    c: Coincident(g6,g5)
    c: Vertical(g6)
    c: Coincident(g7,g6)
    c: Coincident(g7,g4)
    c: Horizontal(g7)
    c: Horizontal(g5,g0)
    c: Horizontal(g0,g4)
    c: DistanceX(g6,g-4) = 4.5
    c: Angle(g5,g4) = 0.523599
    c: DistanceY(g4,g4) = 12
FEATURE [PartDesign::Pad] Pad093
  BaseFeature = -> Pocket077
  Direction = (1,0,0)
  Length = 7
  Length2 = 10
  Profile = -> Sketch176
  ReferenceAxis = -> Sketch176 [N_Axis]
  Reversed = true
  Type = 0
FEATURE [Sketcher::SketchObject] Sketch177
  FullyConstrained = true
  MapMode = 5
  Support = -> [XY_Plane034]
  sketch-geometry (1):
    g0: Circle CenterX=0 CenterY=0 CenterZ=0 NormalX=0 NormalY=0 NormalZ=1 AngleXU=0 Radius=2.675
  constraints (2):
    c: Coincident(g0,g-1)
    c: Diameter(g0) = 5.35
FEATURE [PartDesign::Pad] Pad094
  Direction = (0,0,1)
  Length = 2.9
  Length2 = 10
  Profile = -> Sketch177
  ReferenceAxis = -> Sketch177 [N_Axis]
  Type = 0
FEATURE [Sketcher::SketchObject] Sketch178
  FullyConstrained = true
  MapMode = 5
  Placement = pos=(0,0,2.9) rot=(0,0,1;0rad)
  Support = -> [Pad094]
  sketch-geometry (1):
    g0: Circle CenterX=0 CenterY=0 CenterZ=0 NormalX=0 NormalY=0 NormalZ=1 AngleXU=0 Radius=1.465
  constraints (2):
    c: Coincident(g0,g-1)
    c: Diameter(g0) = 2.93
FEATURE [PartDesign::Pad] Pad095
  BaseFeature = -> Pad094
  Direction = (0,0,1)
  Length = 12
  Length2 = 10
  Profile = -> Sketch178
  ReferenceAxis = -> Sketch178 [N_Axis]
  Type = 0
FEATURE [Sketcher::SketchObject] Sketch179
  FullyConstrained = true
  MapMode = 5
  Placement = pos=(0,0,0) rot=(1,0,0;3.14159rad)
  Support = -> [Pad095]
  sketch-geometry (7):
    g0: LineSegment StartX=1.20378 StartY=0.695 StartZ=0 EndX=0 EndY=1.39 EndZ=0
    g1: LineSegment StartX=0 StartY=1.39 StartZ=0 EndX=-1.20378 EndY=0.695 EndZ=0
    g2: LineSegment StartX=-1.20378 StartY=0.695 StartZ=0 EndX=-1.20378 EndY=-0.695 EndZ=0
    g3: LineSegment StartX=-1.20378 StartY=-0.695 StartZ=0 EndX=1.122e-12 EndY=-1.39 EndZ=0
    g4: LineSegment StartX=1.122e-12 StartY=-1.39 StartZ=0 EndX=1.20378 EndY=-0.695 EndZ=0
    g5: LineSegment StartX=1.20378 StartY=-0.695 StartZ=0 EndX=1.20378 EndY=0.695 EndZ=0
    g6: Circle CenterX=0 CenterY=0 CenterZ=0 NormalX=0 NormalY=0 NormalZ=1 AngleXU=0 Radius=1.39
  constraints (16):
    c: Coincident(g0,g1)
    c: Coincident(g1,g2)
    c: Coincident(g2,g3)
    c: Coincident(g3,g4)
    c: Coincident(g4,g5)
    c: Coincident(g5,g0)
    c: Equal(g0, g1-g5) x5
    c: PointOnObject(g0,g6)
    c: PointOnObject(g1,g6)
    c: PointOnObject(g2,g6)
    c: PointOnObject(g3,g6)
    c: PointOnObject(g4,g6)
    c: PointOnObject(g5,g6)
    c: Coincident(g6,g-1)
    c: Vertical(g6,g0)
    c: Diameter(g6) = 2.78
FEATURE [PartDesign::Pocket] Pocket078
  BaseFeature = -> Pad095
  Direction = (0,0,1)
  Length = 1.94
  Length2 = 5
  Profile = -> Sketch179
  ReferenceAxis = -> Sketch179 [N_Axis]
  Type = 0
FEATURE [PartDesign::Body] Body035  label="Body_M3_20mm001"
  Group = -> [Sketch177,Pad094,Sketch178,Pad095,Sketch179,Pocket078]
  Origin = -> Origin034
  Tip = -> Pocket078
FEATURE [App::FeaturePython] Constraints027  # WARN: FeaturePython — macro-defined, semantics opaque (R4)
  _Version = 1
FEATURE [Part::FeaturePython] Parts027  # WARN: FeaturePython — macro-defined, semantics opaque (R4)
  Group = -> [Body035]
  GroupMode = 0
FEATURE [Sketcher::SketchObject] Sketch180
  ExternalGeometry = -> [Pad086]
  FullyConstrained = true
  MapMode = 5
  Placement = pos=(120,0,0) rot=(0.57735,0.57735,0.57735;2.0944rad)
  Support = -> [Pad086]
  sketch-geometry (17):
    g0: LineSegment StartX=6.85 StartY=-31 StartZ=0 EndX=23.85 EndY=-31 EndZ=0
    g1: LineSegment StartX=23.85 StartY=-31 StartZ=0 EndX=23.85 EndY=-16.5 EndZ=0
    g2: LineSegment StartX=23.85 StartY=-16.5 StartZ=0 EndX=6.85 EndY=-16.5 EndZ=0
    g3: LineSegment StartX=6.85 StartY=-16.5 StartZ=0 EndX=6.85 EndY=-31 EndZ=0
    g4: LineSegment StartX=26.1 StartY=-31 StartZ=0 EndX=42.1 EndY=-31 EndZ=0
    g5: LineSegment StartX=42.1 StartY=-31 StartZ=0 EndX=42.1 EndY=-14 EndZ=0
    g6: LineSegment StartX=42.1 StartY=-14 StartZ=0 EndX=26.1 EndY=-14 EndZ=0
    g7: LineSegment StartX=26.1 StartY=-14 StartZ=0 EndX=26.1 EndY=-31 EndZ=0
    g8: LineSegment StartX=44.1 StartY=-31 StartZ=0 EndX=60.1 EndY=-31 EndZ=0
    g9: LineSegment StartX=60.1 StartY=-31 StartZ=0 EndX=60.1 EndY=-14 EndZ=0
    g10: LineSegment StartX=60.1 StartY=-14 StartZ=0 EndX=44.1 EndY=-14 EndZ=0
    g11: LineSegment StartX=44.1 StartY=-14 StartZ=0 EndX=44.1 EndY=-31 EndZ=0
    g12: GeomPoint X=34.1 Y=-31 Z=0
    g13: GeomPoint X=52.1 Y=-31 Z=0
    g14: GeomPoint X=15.35 Y=-31 Z=0
    g15: GeomPoint X=8.6 Y=-30.5 Z=0
    g16: GeomPoint X=5.1 Y=-30.5 Z=0
  constraints (43):
    c: Coincident(g0,g1)
    c: Coincident(g1,g2)
    c: Coincident(g2,g3)
    c: Coincident(g3,g0)
    c: Horizontal(g0)
    c: Horizontal(g2)
    c: Vertical(g1)
    c: Vertical(g3)
    c: Coincident(g4,g5)
    c: Coincident(g5,g6)
    c: Coincident(g6,g7)
    c: Coincident(g7,g4)
    c: Horizontal(g4)
    c: Horizontal(g6)
    c: Vertical(g5)
    c: Vertical(g7)
    c: Coincident(g8,g9)
    c: Coincident(g9,g10)
    c: Coincident(g10,g11)
    c: Coincident(g11,g8)
    c: Horizontal(g8)
    c: Horizontal(g10)
    c: Vertical(g9)
    c: Vertical(g11)
    c: Horizontal(g0,g4)
    c: Horizontal(g4,g8)
    c: Horizontal(g10,g6)
    c: DistanceY(g9,g9) = 17
    c: Symmetric(g0,g0,g14)
    c: Symmetric(g4,g4,g12)
    c: Symmetric(g8,g8,g13)
    c: DistanceX(g15) = 8.6
    c: DistanceY(g-3,g15) = 4.5
    c: DistanceY(g14,g15) = 0.5
    c: Horizontal(g16,g15)
    c: DistanceX(g16,g15) = 3.5
    c: DistanceX(g16,g14) = 10.25
    c: DistanceX(g16,g12) = 29
    c: DistanceX(g16,g13) = 47
    c: Equal(g8,g4)
    c: DistanceX(g8,g8) = 16
    c: DistanceX(g2,g2) = 17
    c: DistanceY(g1,g1) = 14.5
FEATURE [PartDesign::Pocket] Pocket079
  BaseFeature = -> Pad086
  Direction = (-1,0,0)
  Length = 5
  Length2 = 5
  Profile = -> Sketch180
  ReferenceAxis = -> Sketch180 [N_Axis]
  Type = 0
FEATURE [Sketcher::SketchObject] Sketch181
  ExternalGeometry = -> [Pocket079]
  FullyConstrained = true
  MapMode = 5
  Placement = pos=(0,0,0) rot=(1,0,0;1.5708rad)
  Support = -> [Pocket079]
  sketch-geometry (17):
    g0: GeomPoint X=30.2 Y=-30.5 Z=0
    g1: LineSegment StartX=33.8 StartY=-33.15 StartZ=0 EndX=47.8 EndY=-33.15 EndZ=0
    g2: LineSegment StartX=47.8 StartY=-33.15 StartZ=0 EndX=47.8 EndY=-25.15 EndZ=0
    g3: LineSegment StartX=47.8 StartY=-25.15 StartZ=0 EndX=33.8 EndY=-25.15 EndZ=0
    g4: LineSegment StartX=33.8 StartY=-25.15 StartZ=0 EndX=33.8 EndY=-33.15 EndZ=0
    g5: LineSegment StartX=50.7 StartY=-35 StartZ=0 EndX=73.7 EndY=-35 EndZ=0
    g6: LineSegment StartX=73.7 StartY=-35 StartZ=0 EndX=73.7 EndY=-20 EndZ=0
    g7: LineSegment StartX=73.7 StartY=-20 StartZ=0 EndX=50.7 EndY=-20 EndZ=0
    g8: LineSegment StartX=50.7 StartY=-20 StartZ=0 EndX=50.7 EndY=-35 EndZ=0
    g9: LineSegment StartX=78.7 StartY=-22.5 StartZ=0 EndX=88.7 EndY=-22.5 EndZ=0
    g10: LineSegment StartX=88.7 StartY=-22.5 StartZ=0 EndX=88.7 EndY=-32.5 EndZ=0
    g11: LineSegment StartX=88.7 StartY=-32.5 StartZ=0 EndX=78.7 EndY=-32.5 EndZ=0
    g12: LineSegment StartX=78.7 StartY=-32.5 StartZ=0 EndX=78.7 EndY=-22.5 EndZ=0
    g13: GeomPoint X=40.8 Y=-33.15 Z=0
    g14: GeomPoint X=62.2 Y=-35 Z=0
    g15: GeomPoint X=83.7 Y=-32.5 Z=0
    g16: Circle CenterX=83 CenterY=-6.85 CenterZ=0 NormalX=0 NormalY=0 NormalZ=1 AngleXU=0 Radius=5.425
  constraints (44):
    c: DistanceY(g-3,g0) = 4.5
    c: DistanceX(g0,g-3) = 89.8
    c: Coincident(g1,g2)
    c: Coincident(g2,g3)
    c: Coincident(g3,g4)
    c: Coincident(g4,g1)
    c: Horizontal(g1)
    c: Horizontal(g3)
    c: Vertical(g2)
    c: Vertical(g4)
    c: Coincident(g5,g6)
    c: Coincident(g6,g7)
    c: Coincident(g7,g8)
    c: Coincident(g8,g5)
    c: Horizontal(g5)
    c: Horizontal(g7)
    c: Vertical(g6)
    c: Vertical(g8)
    c: Coincident(g9,g10)
    c: Coincident(g10,g11)
    c: Coincident(g11,g12)
    c: Coincident(g12,g9)
    c: Horizontal(g9)
    c: Horizontal(g11)
    c: Vertical(g10)
    c: Vertical(g12)
    c: DistanceX(g1,g1) = 14
    c: DistanceY(g2,g2) = 8
    c: Symmetric(g5,g5,g14)
    c: Symmetric(g11,g11,g15)
    c: Symmetric(g1,g1,g13)
    c: DistanceX(g0,g13) = 10.6
    c: DistanceY(g1,g0) = 2.65
    c: DistanceX(g0,g14) = 32
    c: DistanceX(g5,g5) = 23
    c: DistanceY(g6,g6) = 15
    c: PointOnObject(g5,g-3)
    c: DistanceX(g0,g15) = 53.5
    c: DistanceX(g11,g11) = 10
    c: DistanceY(g10,g10) = 10
    c: DistanceY(g11,g0) = 2
    c: Diameter(g16) = 10.85
    c: DistanceY(g16) = -6.85
    c: DistanceX(g16) = 83
FEATURE [PartDesign::Pocket] Pocket080
  BaseFeature = -> Pocket079
  Direction = (0,1,-2e-16)
  Length = 3
  Length2 = 5
  Profile = -> Sketch181
  ReferenceAxis = -> Sketch181 [N_Axis]
  Type = 0
FEATURE [Sketcher::SketchObject] Sketch182
  ExternalGeometry = -> [Pad093]
  FullyConstrained = true
  MapMode = 5
  Placement = pos=(0,0,37.5) rot=(0,0,1;0rad)
  Support = -> [Pad093]
  sketch-geometry (10):
    g0: LineSegment StartX=115.75 StartY=71.0877 StartZ=0 EndX=113 EndY=72.6754 EndZ=0
    g1: LineSegment StartX=113 StartY=72.6754 StartZ=0 EndX=110.25 EndY=71.0877 EndZ=0
    g2: LineSegment StartX=110.25 StartY=71.0877 StartZ=0 EndX=110.25 EndY=67.9123 EndZ=0
    g3: LineSegment StartX=110.25 StartY=67.9123 StartZ=0 EndX=113 EndY=66.3246 EndZ=0
    g4: LineSegment StartX=113 StartY=66.3246 StartZ=0 EndX=115.75 EndY=67.9123 EndZ=0
    g5: LineSegment StartX=115.75 StartY=67.9123 StartZ=0 EndX=115.75 EndY=71.0877 EndZ=0
    g6: Circle CenterX=113 CenterY=69.5 CenterZ=0 NormalX=0 NormalY=0 NormalZ=1 AngleXU=0 Radius=3.17543
    g7: LineSegment StartX=110.25 StartY=71.0877 StartZ=0 EndX=110.25 EndY=73 EndZ=0
    g8: LineSegment StartX=115.75 StartY=71.0877 StartZ=0 EndX=115.75 EndY=73 EndZ=0
    g9: LineSegment StartX=115.75 StartY=73 StartZ=0 EndX=110.25 EndY=73 EndZ=0
  constraints (25):
    c: Coincident(g0,g1)
    c: Coincident(g1,g2)
    c: Coincident(g2,g3)
    c: Coincident(g3,g4)
    c: Coincident(g4,g5)
    c: Coincident(g5,g0)
    c: Equal(g0, g1-g5) x5
    c: PointOnObject(g0,g6)
    c: PointOnObject(g1,g6)
    c: PointOnObject(g2,g6)
    c: PointOnObject(g3,g6)
    c: PointOnObject(g4,g6)
    c: PointOnObject(g5,g6)
    c: Vertical(g5)
    c: Coincident(g7,g2)
    c: PointOnObject(g7,g-3)
    c: Vertical(g7)
    c: Coincident(g8,g5)
    c: PointOnObject(g8,g-3)
    c: Vertical(g8)
    c: Coincident(g9,g8)
    c: Coincident(g9,g7)
    c: DistanceX(g9,g9) = 5.5
    c: DistanceX(g0,g-3) = 7
    c: DistanceY(g6,g-3) = 3.5
FEATURE [PartDesign::Pocket] Pocket081
  BaseFeature = -> Pad093
  Direction = (0,0,-1)
  Length = 10
  Length2 = 5
  Profile = -> Sketch182
  ReferenceAxis = -> Sketch182 [N_Axis]
  Type = 0
FEATURE [Sketcher::SketchObject] Sketch183
  ExternalGeometry = -> [Pocket081]
  FullyConstrained = true
  MapMode = 5
  Placement = pos=(0,0,37.5) rot=(0,0,1;0rad)
  Support = -> [Pocket081]
  sketch-geometry (5):
    g0: LineSegment StartX=110.25 StartY=73 StartZ=0 EndX=115.75 EndY=73 EndZ=0
    g1: LineSegment StartX=110.25 StartY=73 StartZ=0 EndX=110.25 EndY=67.9123 EndZ=0
    g2: LineSegment StartX=110.25 StartY=67.9123 StartZ=0 EndX=113 EndY=66.3246 EndZ=0
    g3: LineSegment StartX=113 StartY=66.3246 StartZ=0 EndX=115.75 EndY=67.9123 EndZ=0
    g4: LineSegment StartX=115.75 StartY=67.9123 StartZ=0 EndX=115.75 EndY=73 EndZ=0
  constraints (10):
    c: Coincident(g0,g-4)
    c: Coincident(g0,g-3)
    c: Coincident(g1,g0)
    c: Coincident(g1,g-6)
    c: Coincident(g2,g1)
    c: Coincident(g2,g-7)
    c: Coincident(g3,g2)
    c: Coincident(g3,g-7)
    c: Coincident(g4,g3)
    c: Coincident(g4,g0)
FEATURE [PartDesign::Pad] Pad096
  BaseFeature = -> Pocket081
  Direction = (0,0,1)
  Length = 5
  Length2 = 10
  Profile = -> Sketch183
  ReferenceAxis = -> Sketch183 [N_Axis]
  Reversed = true
  Type = 0
FEATURE [Sketcher::SketchObject] Sketch184
  ExternalGeometry = -> [Pad096]
  FullyConstrained = true
  MapMode = 5
  Placement = pos=(0,0,37.5) rot=(0,0,1;0rad)
  Support = -> [Pad096]
  sketch-geometry (3):
    g0: LineSegment StartX=110.25 StartY=67.9123 StartZ=0 EndX=113 EndY=69.5 EndZ=0
    g1: LineSegment StartX=113 StartY=69.5 StartZ=0 EndX=113 EndY=66.3246 EndZ=0
    g2: Circle CenterX=113 CenterY=69.5 CenterZ=0 NormalX=0 NormalY=0 NormalZ=1 AngleXU=0 Radius=1.65
  constraints (7):
    c: Coincident(g0,g-3)
    c: Coincident(g1,g0)
    c: Coincident(g1,g-4)
    c: Vertical(g1)
    c: Equal(g0,g1)
    c: Coincident(g2,g0)
    c: Diameter(g2) = 3.3
FEATURE [PartDesign::Pocket] Pocket082
  BaseFeature = -> Pad096
  Direction = (0,0,-1)
  Length = 5
  Length2 = 5
  Profile = -> Sketch184
  ReferenceAxis = -> Sketch184 [N_Axis]
  Type = 1
FEATURE [PartDesign::Fillet] Fillet069
  Base = -> Pocket082 [Edge161,Edge52]
  BaseFeature = -> Pocket082
  Radius = 8
  SupportTransform = false
  UseAllEdges = false
FEATURE [Sketcher::SketchObject] Sketch185
  ExternalGeometry = -> [Pocket080]
  FullyConstrained = true
  MapMode = 5
  Placement = pos=(0,0,2.5) rot=(0,0,1;0rad)
  Support = -> [Pocket080]
  sketch-geometry (1):
    g0: Circle CenterX=113 CenterY=69.5 CenterZ=0 NormalX=0 NormalY=0 NormalZ=1 AngleXU=0 Radius=1.65
  constraints (3):
    c: Diameter(g0) = 3.3
    c: DistanceX(g0,g-3) = 7
    c: DistanceY(g0,g-3) = 3.5
FEATURE [PartDesign::Pocket] Pocket083
  BaseFeature = -> Pocket080
  Direction = (0,0,-1)
  Length = 5
  Length2 = 5
  Profile = -> Sketch185
  ReferenceAxis = -> Sketch185 [N_Axis]
  Type = 0
FEATURE [Sketcher::SketchObject] Sketch186
  FullyConstrained = true
  MapMode = 5
  Placement = pos=(0,0,0) rot=(1,0,0;3.14159rad)
  Support = -> [Fillet069]
  sketch-geometry (5):
    g0: LineSegment StartX=0 StartY=0 StartZ=0 EndX=0 EndY=5 EndZ=0
    g1: LineSegment StartX=8 StartY=0 StartZ=0 EndX=8 EndY=5 EndZ=0
    g2: ArcOfCircle CenterX=4 CenterY=5 CenterZ=0 NormalX=0 NormalY=0 NormalZ=1 AngleXU=0 Radius=4 StartAngle=0 EndAngle=3.14159
    g3: LineSegment StartX=0 StartY=0 StartZ=0 EndX=8 EndY=0 EndZ=0
    g4: Circle CenterX=4 CenterY=5 CenterZ=0 NormalX=0 NormalY=0 NormalZ=1 AngleXU=0 Radius=1.65
  constraints (14):
    c: Coincident(g0,g-1)
    c: PointOnObject(g0,g-2)
    c: PointOnObject(g1,g-1)
    c: Vertical(g1)
    c: Horizontal(g1,g0)
    c: DistanceY(g0,g0) = 5
    c: Coincident(g2,g0)
    c: Coincident(g2,g1)
    c: Horizontal(g2,g1)
    c: Diameter(g2) = 8
    c: Coincident(g3,g0)
    c: Coincident(g3,g1)
    c: Coincident(g4,g2)
    c: Diameter(g4) = 3.3
FEATURE [PartDesign::Pad] Pad097
  BaseFeature = -> Fillet069
  Direction = (0,0,-1)
  Length = 2.5
  Length2 = 10
  Profile = -> Sketch186
  ReferenceAxis = -> Sketch186 [N_Axis]
  Reversed = true
  Type = 0
FEATURE [PartDesign::Fillet] Fillet070
  Base = -> Pad097 [Edge72]
  BaseFeature = -> Pad097
  Radius = 4
  SupportTransform = false
  UseAllEdges = false
FEATURE [Sketcher::SketchObject] Sketch187
  FullyConstrained = true
  MapMode = 5
  Placement = pos=(0,0,-35) rot=(1,0,0;3.14159rad)
  Support = -> [Pocket083]
  sketch-geometry (6):
    g0: LineSegment StartX=0 StartY=0 StartZ=0 EndX=8 EndY=0 EndZ=0
    g1: LineSegment StartX=8 StartY=0 StartZ=0 EndX=8 EndY=5 EndZ=0
    g2: LineSegment StartX=8 StartY=5 StartZ=0 EndX=0 EndY=5 EndZ=0
    g3: LineSegment StartX=0 StartY=5 StartZ=0 EndX=0 EndY=0 EndZ=0
    g4: ArcOfCircle CenterX=4 CenterY=5 CenterZ=0 NormalX=0 NormalY=0 NormalZ=1 AngleXU=0 Radius=4 StartAngle=0 EndAngle=3.14159
    g5: Circle CenterX=4 CenterY=5 CenterZ=0 NormalX=0 NormalY=0 NormalZ=1 AngleXU=0 Radius=1.65
  constraints (16):
    c: Coincident(g0,g1)
    c: Coincident(g1,g2)
    c: Coincident(g2,g3)
    c: Coincident(g3,g0)
    c: Horizontal(g0)
    c: Horizontal(g2)
    c: Vertical(g1)
    c: Vertical(g3)
    c: Coincident(g0,g-1)
    c: PointOnObject(g4,g2)
    c: Coincident(g4,g2)
    c: Coincident(g4,g1)
    c: Diameter(g4) = 8
    c: DistanceY(g3,g3) = 5
    c: Coincident(g5,g4)
    c: Diameter(g5) = 3.3
FEATURE [PartDesign::Pad] Pad098
  BaseFeature = -> Pocket083
  Direction = (0,0,-1)
  Length = 4
  Length2 = 10
  Profile = -> Sketch187
  ReferenceAxis = -> Sketch187 [N_Axis]
  Reversed = true
  Type = 0
FEATURE [PartDesign::Fillet] Fillet071
  Base = -> Pad098 [Edge19]
  BaseFeature = -> Pad098
  Radius = 4
  SupportTransform = false
  UseAllEdges = false
FEATURE [PartDesign::Fillet] Fillet072
  Base = -> Fillet071 [Edge6,Edge4]
  BaseFeature = -> Fillet071
  Radius = 1.8
  SupportTransform = false
  UseAllEdges = false
FEATURE [Sketcher::SketchObject] Sketch188
  ExternalGeometry = -> [Fillet070]
  FullyConstrained = true
  MapMode = 5
  Placement = pos=(0,4,0) rot=(1,0,0;1.5708rad)
  Support = -> [Fillet070]
  sketch-geometry (4):
    g0: LineSegment StartX=15 StartY=26.5 StartZ=0 EndX=18 EndY=23.5 EndZ=0
    g1: LineSegment StartX=18 StartY=23.5 StartZ=0 EndX=18 EndY=13.5 EndZ=0
    g2: LineSegment StartX=18 StartY=13.5 StartZ=0 EndX=15 EndY=10.5 EndZ=0
    g3: LineSegment StartX=15 StartY=10.5 StartZ=0 EndX=15 EndY=26.5 EndZ=0
  constraints (12):
    c: PointOnObject(g0,g-3)
    c: Coincident(g1,g0)
    c: Vertical(g1)
    c: Coincident(g2,g1)
    c: PointOnObject(g2,g-3)
    c: Coincident(g3,g2)
    c: Coincident(g3,g0)
    c: Angle(g2,g3) = 0.785398
    c: Angle(g3,g0) = 0.785398
    c: DistanceY(g0,g-3) = 11
    c: DistanceY(g-3,g2) = 8
    c: DistanceX(g2,g1) = 3
FEATURE [PartDesign::Pocket] Pocket084
  BaseFeature = -> Fillet070
  Direction = (0,1,-2e-16)
  Length = 66.5
  Length2 = 5
  Profile = -> Sketch188
  ReferenceAxis = -> Sketch188 [N_Axis]
  Type = 0
FEATURE [PartDesign::Fillet] Fillet073
  Base = -> Pocket084 [Face89]
  BaseFeature = -> Pocket084
  Radius = 1
  SupportTransform = false
  UseAllEdges = false
FEATURE [PartDesign::Fillet] Fillet074
  Base = -> Fillet073 [Edge194,Edge193,Edge132]
  BaseFeature = -> Fillet073
  Radius = 1
  SupportTransform = false
  UseAllEdges = false
FEATURE [Sketcher::SketchObject] Sketch189
  FullyConstrained = true
  MapMode = 5
  Placement = pos=(0,0,2.5) rot=(0,0,1;0rad)
  Support = -> [Fillet072]
  sketch-geometry (1):
    g0: Circle CenterX=25 CenterY=20 CenterZ=0 NormalX=0 NormalY=0 NormalZ=1 AngleXU=0 Radius=1
  constraints (3):
    c: Diameter(g0) = 2
    c: DistanceX(g0) = 25
    c: DistanceY(g0) = 20
FEATURE [PartDesign::Pocket] Pocket085
  BaseFeature = -> Fillet072
  Direction = (0,0,-1)
  Length = 2.5
  Length2 = 5
  Profile = -> Sketch189
  ReferenceAxis = -> Sketch189 [N_Axis]
  Type = 0
FEATURE [PartDesign::LinearPattern] LinearPattern
  Direction = -> Sketch189 [H_Axis]
  Length = 80
  Occurrences = 20
FEATURE [PartDesign::LinearPattern] LinearPattern001
  Direction = -> Sketch189 [V_Axis]
  Length = 40
  Occurrences = 10
FEATURE [PartDesign::MultiTransform] MultiTransform
  BaseFeature = -> Pocket085
  Originals = -> [Pocket085]
  Transformations = -> [LinearPattern,LinearPattern001]
FEATURE [Sketcher::SketchObject] Sketch190
  FullyConstrained = true
  MapMode = 5
  Placement = pos=(0,0,0) rot=(1,0,0;1.5708rad)
  Support = -> [MultiTransform]
  sketch-geometry (4):
    g0: ArcOfCircle CenterX=30 CenterY=-5.5 CenterZ=0 NormalX=0 NormalY=0 NormalZ=1 AngleXU=0 Radius=1 StartAngle=-2.363e-13 EndAngle=3.14159
    g1: ArcOfCircle CenterX=30 CenterY=-13.5 CenterZ=0 NormalX=0 NormalY=0 NormalZ=1 AngleXU=0 Radius=1 StartAngle=3.14159 EndAngle=6.28319
    g2: LineSegment StartX=29 StartY=-5.5 StartZ=0 EndX=29 EndY=-13.5 EndZ=0
    g3: LineSegment StartX=31 StartY=-13.5 StartZ=0 EndX=31 EndY=-5.5 EndZ=0
  constraints (10):
    c: Tangent(g0,g2) = -1.5708
    c: Tangent(g2,g1) = -1.5708
    c: Tangent(g1,g3) = -1.5708
    c: Tangent(g3,g0) = -1.5708
    c: Equal(g0,g1)
    c: Vertical(g2)
    c: Diameter(g0) = 2
    c: DistanceY(g3,g3) = 8
    c: DistanceX(g0) = 30
    c: DistanceY(g0) = -5.5
FEATURE [PartDesign::Pocket] Pocket086
  BaseFeature = -> MultiTransform
  Direction = (0,1,-2e-16)
  Length = 2.5
  Length2 = 5
  Profile = -> Sketch190
  ReferenceAxis = -> Sketch190 [N_Axis]
  Type = 0
FEATURE [PartDesign::LinearPattern] LinearPattern002
  BaseFeature = -> Pocket086
  Direction = -> Sketch190 [H_Axis]
  Length = 40
  Occurrences = 8
  Originals = -> [Pocket086]
FEATURE [Sketcher::SketchObject] Sketch191
  FullyConstrained = true
  MapMode = 5
  Placement = pos=(0,73,0) rot=(0,0.707107,0.707107;3.14159rad)
  Support = -> [Fillet074]
  sketch-geometry (4):
    g0: ArcOfCircle CenterX=-30 CenterY=30 CenterZ=0 NormalX=0 NormalY=0 NormalZ=1 AngleXU=0 Radius=1 StartAngle=-9e-16 EndAngle=3.14159
    g1: ArcOfCircle CenterX=-30 CenterY=10 CenterZ=0 NormalX=0 NormalY=0 NormalZ=1 AngleXU=0 Radius=1 StartAngle=3.14159 EndAngle=6.28319
    g2: LineSegment StartX=-31 StartY=30 StartZ=0 EndX=-31 EndY=10 EndZ=0
    g3: LineSegment StartX=-29 StartY=10 StartZ=0 EndX=-29 EndY=30 EndZ=0
  constraints (10):
    c: Tangent(g0,g2) = -1.5708
    c: Tangent(g2,g1) = -1.5708
    c: Tangent(g1,g3) = -1.5708
    c: Tangent(g3,g0) = -1.5708
    c: Equal(g0,g1)
    c: Vertical(g2)
    c: Diameter(g0) = 2
    c: DistanceY(g1) = 10
    c: DistanceY(g3,g3) = 20
    c: DistanceX(g1) = -30
FEATURE [PartDesign::Pocket] Pocket087
  BaseFeature = -> Fillet074
  Direction = (0,-1,2e-16)
  Length = 2.5
  Length2 = 5
  Profile = -> Sketch191
  ReferenceAxis = -> Sketch191 [N_Axis]
  Type = 0
FEATURE [PartDesign::LinearPattern] LinearPattern003
  BaseFeature = -> Pocket087
  Direction = -> Sketch191 [H_Axis]
  Length = 60
  Occurrences = 10
  Originals = -> [Pocket087]
  Reversed = true
FEATURE [Sketcher::SketchObject] Sketch192
  FullyConstrained = true
  MapMode = 5
  Placement = pos=(0,0,0) rot=(1,0,0;3.14159rad)
  Support = -> [LinearPattern003]
  sketch-geometry (1):
    g0: Circle CenterX=42.5 CenterY=-17.5 CenterZ=0 NormalX=0 NormalY=0 NormalZ=1 AngleXU=0 Radius=1
  constraints (3):
    c: Diameter(g0) = 2
    c: DistanceX(g0) = 42.5
    c: DistanceY(g0) = -17.5
FEATURE [PartDesign::Pocket] Pocket088
  BaseFeature = -> LinearPattern003
  Direction = (0,0,1)
  Length = 2.5
  Length2 = 5
  Profile = -> Sketch192
  ReferenceAxis = -> Sketch192 [N_Axis]
  Type = 0
FEATURE [PartDesign::LinearPattern] LinearPattern004
  Direction = -> Sketch192 [H_Axis]
  Length = 40
  Occurrences = 10
FEATURE [PartDesign::LinearPattern] LinearPattern005
  Direction = -> Sketch192 [V_Axis]
  Length = 30
  Occurrences = 6
  Reversed = true
FEATURE [PartDesign::MultiTransform] MultiTransform001
  BaseFeature = -> Pocket088
  Originals = -> [Pocket088]
  Transformations = -> [LinearPattern004,LinearPattern005]
FEATURE [PartDesign::Chamfer] Chamfer008
  Angle = 45
  Base = -> LinearPattern002 [Edge194,Edge185,Edge193,Edge64]
  BaseFeature = -> LinearPattern002
  ChamferType = 0
  FlipDirection = false
  Size = 1.75
  Size2 = 1
  SupportTransform = false
  UseAllEdges = false
FEATURE [PartDesign::Fillet] Fillet075
  Base = -> Chamfer008 [Edge73]
  BaseFeature = -> Chamfer008
  Radius = 3
  SupportTransform = false
  UseAllEdges = false
FEATURE [Sketcher::SketchObject] Sketch193
  FullyConstrained = true
  MapMode = 5
  Placement = pos=(0,2.5,0) rot=(0,0.707107,0.707107;3.14159rad)
  Support = -> [Fillet075]
  sketch-geometry (5):
    g0: LineSegment StartX=-75 StartY=0 StartZ=0 EndX=-91 EndY=0 EndZ=0
    g1: LineSegment StartX=-91 StartY=0 StartZ=0 EndX=-91 EndY=-8 EndZ=0
    g2: LineSegment StartX=-91 StartY=-8 StartZ=0 EndX=-75 EndY=-8 EndZ=0
    g3: LineSegment StartX=-75 StartY=-8 StartZ=0 EndX=-75 EndY=0 EndZ=0
    g4: ArcOfCircle CenterX=-83 CenterY=-8 CenterZ=0 NormalX=0 NormalY=0 NormalZ=1 AngleXU=0 Radius=8 StartAngle=3.14159 EndAngle=6.28319
  constraints (15):
    c: Coincident(g0,g1)
    c: Coincident(g1,g2)
    c: Coincident(g2,g3)
    c: Coincident(g3,g0)
    c: Horizontal(g0)
    c: Horizontal(g2)
    c: Vertical(g1)
    c: Vertical(g3)
    c: PointOnObject(g4,g2)
    c: Coincident(g4,g2)
    c: Coincident(g4,g1)
    c: DistanceY(g1,g1) = 8
    c: Diameter(g4) = 16
    c: DistanceX(g4) = -83
    c: PointOnObject(g0,g-1)
FEATURE [PartDesign::Pad] Pad099
  BaseFeature = -> Fillet075
  Direction = (0,1,-2e-16)
  Length = 3
  Length2 = 10
  Profile = -> Sketch193
  ReferenceAxis = -> Sketch193 [N_Axis]
  Type = 0
FEATURE [PartDesign::Fillet] Fillet076
  Base = -> Pad099 [Edge5,Edge1]
  BaseFeature = -> Pad099
  Radius = 3
  SupportTransform = false
  UseAllEdges = false
FEATURE [PartDesign::Fillet] Fillet077
  Base = -> Fillet076 [Edge649,Edge651,Edge648]
  BaseFeature = -> Fillet076
  Radius = 1
  SupportTransform = false
  UseAllEdges = false
FEATURE [PartDesign::Fillet] Fillet078
  Base = -> Fillet077 [Edge714,Edge237,Edge234,Edge226,Edge228,Edge222]
  BaseFeature = -> Fillet077
  Radius = 1
  SupportTransform = false
  UseAllEdges = false
FEATURE [PartDesign::Chamfer] Chamfer009
  Angle = 45
  Base = -> MultiTransform001 [Edge247]
  BaseFeature = -> MultiTransform001
  ChamferType = 0
  FlipDirection = false
  Size = 1.5
  Size2 = 1
  SupportTransform = false
  UseAllEdges = false
FEATURE [PartDesign::Chamfer] Chamfer010
  Angle = 45
  Base = -> Chamfer009 [Edge12,Edge182,Edge390,Edge393,Edge395,Edge397,Edge405,Edge599,Edge406]
  BaseFeature = -> Chamfer009
  ChamferType = 0
  FlipDirection = false
  Size = 1
  Size2 = 1
  SupportTransform = false
  UseAllEdges = false
FEATURE [PartDesign::Chamfer] Chamfer011
  Angle = 45
  Base = -> Chamfer010 [Edge4]
  BaseFeature = -> Chamfer010
  ChamferType = 0
  FlipDirection = false
  Size = 1
  Size2 = 1
  SupportTransform = false
  UseAllEdges = false
FEATURE [PartDesign::Fillet] Fillet079
  Base = -> Chamfer011 [Edge95,Edge92]
  BaseFeature = -> Chamfer011
  Radius = 0.5
  SupportTransform = false
  UseAllEdges = false
FEATURE [PartDesign::Fillet] Fillet080
  Base = -> Fillet079 [Face155,Face161,Face165,Face169,Face173,Face177,Face181,Face185,Face189,Face193]
  BaseFeature = -> Fillet079
  Radius = 1
  SupportTransform = false
  UseAllEdges = false
FEATURE [PartDesign::Fillet] Fillet081
  Base = -> Fillet080 [Face220,Face223,Face226,Face229,Face247,Face250,Face249,Face248,Face246,Face245,Face227,Face228,Face225,Face224,Face221,Face222,Face219,Face218,Face195,Face194,Face209,Face210,Face212,Face211,Face215,Face216,Face239,Face238,Face243,Face242,Face241,Face240,Face235,Face234,Face233,Face230,Face231,Face232,Face236,Face237,+20 more]
  BaseFeature = -> Fillet080
  Radius = 1
  SupportTransform = false
  UseAllEdges = false
FEATURE [PartDesign::Fillet] Fillet082
  Base = -> Fillet081 [Edge438,Edge251,Edge253]
  BaseFeature = -> Fillet081
  Radius = 2
  SupportTransform = false
  UseAllEdges = false
FEATURE [PartDesign::Fillet] Fillet083
  Base = -> Fillet082 [Edge308]
  BaseFeature = -> Fillet082
  Radius = 0.4
  SupportTransform = false
  UseAllEdges = false
FEATURE [PartDesign::Fillet] Fillet084
  Base = -> Fillet083 [Face37,Face39,Face40,Face38,Face393,Face391,Face394,Face392]
  BaseFeature = -> Fillet083
  Radius = 0.5
  SupportTransform = false
  UseAllEdges = false
FEATURE [PartDesign::Fillet] Fillet085
  Base = -> Fillet084 [Edge23,Edge22,Edge21,Edge24,Edge25,Edge20]
  BaseFeature = -> Fillet084
  Radius = 1
  SupportTransform = false
  UseAllEdges = false
FEATURE [PartDesign::Fillet] Fillet086
  Base = -> Fillet085 [Edge20,Edge21,Edge22,Edge23,Edge24]
  BaseFeature = -> Fillet085
  Radius = 1
  SupportTransform = false
  UseAllEdges = false
FEATURE [Sketcher::SketchObject] Sketch194
  ExternalGeometry = -> [Fillet086]
  FullyConstrained = true
  MapMode = 5
  Placement = pos=(15,0,0) rot=(0.57735,-0.57735,-0.57735;2.0944rad)
  Support = -> [Fillet086]
  sketch-geometry (3):
    g0: ArcOfCircle CenterX=-67.5 CenterY=5.5 CenterZ=0 NormalX=0 NormalY=0 NormalZ=1 AngleXU=0 Radius=3 StartAngle=3.14159 EndAngle=4.71239
    g1: LineSegment StartX=-70.5 StartY=5.5 StartZ=0 EndX=-70.5 EndY=2.5 EndZ=0
    g2: LineSegment StartX=-70.5 StartY=2.5 StartZ=0 EndX=-67.5 EndY=2.5 EndZ=0
  constraints (9):
    c: PointOnObject(g0,g-3)
    c: PointOnObject(g0,g-4)
    c: Angle(g0) = 1.5708
    c: Diameter(g0) = 6
    c: Coincident(g1,g0)
    c: Coincident(g1,g-4)
    c: Coincident(g2,g1)
    c: Coincident(g2,g0)
    c: Tangent(g2,g0)
FEATURE [PartDesign::Pad] Pad100
  BaseFeature = -> Fillet086
  Direction = (-1,0,0)
  Length = 11.5
  Length2 = 95
  Profile = -> Sketch194
  ReferenceAxis = -> Sketch194 [N_Axis]
  Type = 4
FEATURE [PartDesign::Body] Body033
  Group = -> [Sketch160,Pad083,Sketch162,Pad085,Sketch169,Pad091,Sketch170,Pocket073,Sketch171,Pocket074,Sketch172,Pad092,Sketch173,Pocket075,Sketch174,Pocket076,Sketch175,Pocket077,Sketch176,Pad093,Sketch182,Pocket081,Sketch183,Pad096,Sketch184,Pocket082,Fillet069,Sketch186,Pad097,Fillet070,Sketch188,Pocket084,Fillet073,Fillet074,Sketch191,Pocket087,LinearPattern003,Sketch192,Pocket088,MultiTransform001,+15 more]
  Origin = -> Origin032
  Tip = -> Pad100
FEATURE [Part::FeaturePython] Parts025  # WARN: FeaturePython — macro-defined, semantics opaque (R4)
  Group = -> [Body033]
  GroupMode = 0
FEATURE [PartDesign::Fillet] Fillet087
  Base = -> Fillet078 [Face232,Face233,Face237,Face236,Face241,Face240,Face239,Face238,Face235,Face234,Face231,Face230]
  BaseFeature = -> Fillet078
  Radius = 0.8
  SupportTransform = false
  UseAllEdges = false
FEATURE [PartDesign::Fillet] Fillet088
  Base = -> Fillet087 [Face300,Face299,Face298,Face297,Face292,Face291,Face46,Face293,Face296,Face294,Face295]
  BaseFeature = -> Fillet087
  Radius = 1
  SupportTransform = false
  UseAllEdges = false
FEATURE [PartDesign::Fillet] Fillet089
  Base = -> Fillet088 [Face55,Face52,Face53,Face49,Face48,Face51,Face47,Face44,Face45,Face41,Face40,Face43,Face39,Face36,Face37,Face33,Face32,Face35,Face31,Face28,Face27,Face24,Face25,Face29,Face54,Face50,Face46,Face42,Face38,Face34,Face30,Face26]
  BaseFeature = -> Fillet088
  Radius = 1
  SupportTransform = false
  UseAllEdges = false
FEATURE [PartDesign::Fillet] Fillet090
  Base = -> Fillet089 [Face251,Face254,Face263,Face284,Face287,Face296,Face371,Face374,Face383,Face404,Face405,Face384,Face375,Face372,Face297,Face288,Face285,Face264,Face255,Face252,Face253,Face257,Face260,Face256,Face265,Face266,Face290,Face286,Face289,Face293,Face299,Face298,Face373,Face377,Face380,Face376,Face385,Face406,Face407,Face386,+160 more]
  BaseFeature = -> Fillet089
  Radius = 1
  SupportTransform = false
  UseAllEdges = false
FEATURE [Sketcher::SketchObject] Sketch195
  ExternalGeometry = -> [Fillet090]
  FullyConstrained = true
  MapMode = 5
  Placement = pos=(0,2.5,-5e-16) rot=(1,0,0;1.5708rad)
  Support = -> [Fillet090]
  sketch-geometry (2):
    g0: GeomPoint X=83 Y=-1.425 Z=0
    g1: Circle CenterX=83 CenterY=-6.85 CenterZ=0 NormalX=0 NormalY=0 NormalZ=1 AngleXU=0 Radius=5.425
  constraints (4):
    c: PointOnObject(g0,g-3)
    c: Vertical(g0,g-3)
    c: Coincident(g1,g-3)
    c: PointOnObject(g0,g1)
FEATURE [PartDesign::Pocket] Pocket089
  BaseFeature = -> Fillet090
  Direction = (0,1,-2e-16)
  Length = 5
  Length2 = 5
  Profile = -> Sketch195
  ReferenceAxis = -> Sketch195 [N_Axis]
  Type = 0
FEATURE [PartDesign::Body] Body032
  Group = -> [Sketch161,Pad084,Sketch163,Pad086,Sketch180,Pocket079,Sketch181,Pocket080,Sketch185,Pocket083,Sketch187,Pad098,Fillet071,Fillet072,Sketch189,Pocket085,MultiTransform,LinearPattern,LinearPattern001,Sketch190,Pocket086,LinearPattern002,Chamfer008,Fillet075,Sketch193,Pad099,Fillet076,Fillet077,Fillet078,Fillet087,Fillet088,Fillet089,Fillet090,Sketch195,Pocket089]
  Origin = -> Origin031
  Tip = -> Pocket089
FEATURE [Part::FeaturePython] Parts024  # WARN: FeaturePython — macro-defined, semantics opaque (R4)
  Group = -> [Body032]
  GroupMode = 0
FEATURE [App::FeaturePython] Constraints028  # WARN: FeaturePython — macro-defined, semantics opaque (R4)
  _Version = 1
FEATURE [App::Link] Link018
  LinkedObject = -> <external MG996R.FCStd>#MG996R001
FEATURE [Part::FeaturePython] Parts028  # WARN: FeaturePython — macro-defined, semantics opaque (R4)
  Group = -> [Link018]
  GroupMode = 0
FEATURE [App::FeaturePython] Constraints029  # WARN: FeaturePython — macro-defined, semantics opaque (R4)
  _Version = 1
FEATURE [App::FeaturePython] Elements029  # WARN: FeaturePython — macro-defined, semantics opaque (R4)
FEATURE [Sketcher::SketchObject] Sketch196
  FullyConstrained = true
  MapMode = 5
  Placement = pos=(0,0,0) rot=(0.57735,0.57735,0.57735;2.0944rad)
  Support = -> [YZ_Plane036]
FEATURE [PartDesign::Body] Body036
  Group = -> [Sketch196]
  Origin = -> Origin035
FEATURE [Part::FeaturePython] Parts029  # WARN: FeaturePython — macro-defined, semantics opaque (R4)
  Group = -> [Body036]
  GroupMode = 0
FEATURE [Part::FeaturePython] Assembly029  label="assy-door_lock_left"  # WARN: FeaturePython — macro-defined, semantics opaque (R4)
  AutoRelax = true
  BuildShape = 0
  Freeze = false
  Group = -> [Constraints029,Elements029,Parts029]
  Verbose = false
  _SolverType = 1
  _Version = 1
FEATURE [App::FeaturePython] Constraints030  # WARN: FeaturePython — macro-defined, semantics opaque (R4)
  _Version = 1
FEATURE [App::FeaturePython] Constraints031  # WARN: FeaturePython — macro-defined, semantics opaque (R4)
  _Version = 1
FEATURE [Part::Feature] Body026001
  shape: bbox 28.04 x 61.66 x 74.93 mm, 96 faces (baked)
FEATURE [Part::FeaturePython] Parts031  # WARN: FeaturePython — macro-defined, semantics opaque (R4)
  Group = -> [Body026001]
  GroupMode = 0
FEATURE [Part::Feature] Part__Mirroring002001  label="Body026 (Mirror #3)001"
  shape: bbox 28.04 x 61.66 x 74.93 mm, 96 faces (baked)
FEATURE [Part::FeaturePython] Parts030  # WARN: FeaturePython — macro-defined, semantics opaque (R4)
  Group = -> [Part__Mirroring002001]
  GroupMode = 0
FEATURE [App::FeaturePython] Constraints032  # WARN: FeaturePython — macro-defined, semantics opaque (R4)
  _Version = 1
FEATURE [Sketcher::SketchObject] Sketch197
  FullyConstrained = true
  MapMode = 5
  Placement = pos=(0,0,0) rot=(0.57735,0.57735,0.57735;2.0944rad)
  Support = -> [YZ_Plane037]
  sketch-geometry (4):
    g0: LineSegment StartX=0 StartY=0 StartZ=0 EndX=31 EndY=0 EndZ=0
    g1: LineSegment StartX=31 StartY=0 StartZ=0 EndX=31 EndY=65 EndZ=0
    g2: LineSegment StartX=31 StartY=65 StartZ=0 EndX=0 EndY=65 EndZ=0
    g3: LineSegment StartX=0 StartY=65 StartZ=0 EndX=0 EndY=0 EndZ=0
  constraints (11):
    c: Coincident(g0,g1)
    c: Coincident(g1,g2)
    c: Coincident(g2,g3)
    c: Coincident(g3,g0)
    c: Horizontal(g0)
    c: Horizontal(g2)
    c: Vertical(g1)
    c: Vertical(g3)
    c: Coincident(g0,g-1)
    c: DistanceY(g1,g1) = 65
    c: DistanceX(g2,g2) = 31
FEATURE [PartDesign::Pad] Pad101  label="Pad101-servo_bracket_body"
  Direction = (1,-2e-16,3e-16)
  Length = 4
  Length2 = 10
  Placement = pos=(0,0,0) rot=(0.57735,0.57735,0.57735;2.0944rad)
  Profile = -> Sketch197
  ReferenceAxis = -> Sketch197 [N_Axis]
  Type = 0
FEATURE [Sketcher::SketchObject] Sketch198
  ExternalGeometry = -> [Pad101]
  FullyConstrained = true
  MapMode = 5
  Placement = pos=(0,1e-16,0) rot=(-0.57735,-0.57735,0.57735;4.18879rad)
  Support = -> [Pad101]
  sketch-geometry (7):
    g0: LineSegment StartX=-77 StartY=8.5 StartZ=0 EndX=12 EndY=8.5 EndZ=0
    g1: LineSegment StartX=12 StartY=-9.5 StartZ=0 EndX=-77 EndY=-9.5 EndZ=0
    g2: LineSegment StartX=-77 StartY=6.5 StartZ=0 EndX=12 EndY=6.5 EndZ=0
    g3: LineSegment StartX=12 StartY=8.5 StartZ=0 EndX=12 EndY=6.5 EndZ=0
    g4: LineSegment StartX=12 StartY=6.5 StartZ=0 EndX=12 EndY=-9.5 EndZ=0
    g5: LineSegment StartX=-77 StartY=-9.5 StartZ=0 EndX=-77 EndY=6.5 EndZ=0
    g6: LineSegment StartX=-77 StartY=6.5 StartZ=0 EndX=-77 EndY=8.5 EndZ=0
  constraints (20):
    c: Coincident(g0,g3)
    c: Coincident(g4,g1)
    c: Coincident(g1,g5)
    c: Coincident(g6,g0)
    c: Horizontal(g0)
    c: Horizontal(g1)
    c: DistanceX(g4) = 12
    c: DistanceX(g1,g-3) = 12
    c: DistanceY(g-3,g0) = 4.5
    c: Horizontal(g2)
    c: DistanceY(g2,g0) = 2
    c: Coincident(g3,g4)
    c: Vertical(g3)
    c: Vertical(g4)
    c: Coincident(g2,g3)
    c: Coincident(g5,g6)
    c: Vertical(g5)
    c: Vertical(g6)
    c: Coincident(g2,g5)
    c: DistanceY(g4,g4) = 16
FEATURE [PartDesign::Pad] Pad102  label="Pad102-rail_mount_body"
  BaseFeature = -> Pad101
  Direction = (-4e-16,-1,2e-16)
  Length = 4
  Length2 = 10
  Placement = pos=(0,0,0) rot=(0.57735,0.57735,0.57735;2.0944rad)
  Profile = -> Sketch198
  ReferenceAxis = -> Sketch198 [N_Axis]
  Reversed = true
  Type = 0
FEATURE [Sketcher::SketchObject] Sketch199
  ExternalGeometry = -> [Pad102]
  FullyConstrained = true
  MapMode = 5
  Placement = pos=(0,0,0) rot=(0.57735,0.57735,-0.57735;4.18879rad)
  Support = -> [Pad102]
  sketch-geometry (17):
    g0: LineSegment StartX=4 StartY=-11.5 StartZ=0 EndX=25 EndY=-11.5 EndZ=0
    g1: LineSegment StartX=25 StartY=-11.5 StartZ=0 EndX=25 EndY=-53.5 EndZ=0
    g2: LineSegment StartX=25 StartY=-53.5 StartZ=0 EndX=4 EndY=-53.5 EndZ=0
    g3: LineSegment StartX=4 StartY=-53.5 StartZ=0 EndX=4 EndY=-11.5 EndZ=0
    g4: LineSegment StartX=4 StartY=-11.5 StartZ=0 EndX=4 EndY=0 EndZ=0
    g5: LineSegment StartX=4 StartY=-65 StartZ=0 EndX=4 EndY=-53.5 EndZ=0
    g6: Circle CenterX=9.6 CenterY=-8.275 CenterZ=0 NormalX=0 NormalY=0 NormalZ=1 AngleXU=0 Radius=1.125
    g7: Circle CenterX=19.4 CenterY=-8.275 CenterZ=0 NormalX=0 NormalY=0 NormalZ=1 AngleXU=0 Radius=1.125
    g8: Circle CenterX=9.6 CenterY=-56.725 CenterZ=0 NormalX=0 NormalY=0 NormalZ=1 AngleXU=0 Radius=1.125
    g9: Circle CenterX=19.4 CenterY=-56.725 CenterZ=0 NormalX=0 NormalY=0 NormalZ=1 AngleXU=0 Radius=1.125
    g10: LineSegment StartX=9.6 StartY=-8.275 StartZ=0 EndX=19.4 EndY=-8.275 EndZ=0
    g11: LineSegment StartX=19.4 StartY=-8.275 StartZ=0 EndX=19.4 EndY=-56.725 EndZ=0
    g12: LineSegment StartX=19.4 StartY=-56.725 StartZ=0 EndX=9.6 EndY=-56.725 EndZ=0
    g13: LineSegment StartX=9.6 StartY=-56.725 StartZ=0 EndX=9.6 EndY=-8.275 EndZ=0
    g14: LineSegment StartX=9.6 StartY=-56.725 StartZ=0 EndX=4 EndY=-53.5 EndZ=0
    g15: LineSegment StartX=25 StartY=-53.5 StartZ=0 EndX=19.4 EndY=-56.725 EndZ=0
    g16: LineSegment StartX=19.4 StartY=-8.275 StartZ=0 EndX=25 EndY=-11.5 EndZ=0
  constraints (42):
    c: Coincident(g0,g1)
    c: Coincident(g1,g2)
    c: Coincident(g2,g3)
    c: Coincident(g3,g0)
    c: Horizontal(g0)
    c: Horizontal(g2)
    c: Vertical(g1)
    c: Vertical(g3)
    c: PointOnObject(g0,g-3)
    c: DistanceX(g0,g0) = 21
    c: DistanceY(g1,g1) = 42
    c: Coincident(g4,g0)
    c: Coincident(g4,g-3)
    c: Coincident(g5,g-3)
    c: Coincident(g5,g2)
    c: Equal(g5,g4)
    c: Equal(g8,g9)
    c: Equal(g9,g6)
    c: Equal(g6,g7)
    c: Diameter(g7) = 2.25
    c: Coincident(g10,g6)
    c: Coincident(g10,g7)
    c: Horizontal(g10)
    c: Coincident(g11,g7)
    c: Coincident(g11,g9)
    c: Vertical(g11)
    c: Coincident(g12,g9)
    c: Coincident(g12,g8)
    c: Horizontal(g12)
    c: Coincident(g13,g8)
    c: Coincident(g13,g6)
    c: Vertical(g13)
    c: Coincident(g14,g8)
    c: Coincident(g14,g2)
    c: Coincident(g15,g1)
    c: Coincident(g15,g9)
    c: Coincident(g16,g7)
    c: Coincident(g16,g0)
    c: Equal(g16,g15)
    c: Equal(g15,g14)
    c: DistanceY(g11,g11) = 48.45
    c: DistanceX(g12,g12) = 9.8
FEATURE [PartDesign::Pocket] Pocket090  label="Pocket090-servo_slot_and_holes"
  BaseFeature = -> Pad102
  Direction = (1,-6e-16,5e-16)
  Length = 5
  Length2 = 5
  Placement = pos=(0,0,0) rot=(0.57735,0.57735,0.57735;2.0944rad)
  Profile = -> Sketch199
  ReferenceAxis = -> Sketch199 [N_Axis]
  Type = 0
FEATURE [Sketcher::SketchObject] Sketch200
  ExternalGeometry = -> [Pocket090]
  FullyConstrained = true
  MapMode = 5
  Placement = pos=(0,0,0) rot=(0.57735,0.57735,-0.57735;4.18879rad)
  Support = -> [Pocket090]
  sketch-geometry (9):
    g0: LineSegment StartX=13.5 StartY=-53.5 StartZ=0 EndX=15.5 EndY=-53.5 EndZ=0
    g1: LineSegment StartX=15.5 StartY=-53.5 StartZ=0 EndX=15.5 EndY=-60.5 EndZ=0
    g2: LineSegment StartX=15.5 StartY=-60.5 StartZ=0 EndX=13.5 EndY=-60.5 EndZ=0
    g3: LineSegment StartX=13.5 StartY=-60.5 StartZ=0 EndX=13.5 EndY=-53.5 EndZ=0
    g4: LineSegment StartX=13.5 StartY=-11.5 StartZ=0 EndX=15.5 EndY=-11.5 EndZ=0
    g5: LineSegment StartX=15.5 StartY=-11.5 StartZ=0 EndX=15.5 EndY=-4.5 EndZ=0
    g6: LineSegment StartX=15.5 StartY=-4.5 StartZ=0 EndX=13.5 EndY=-4.5 EndZ=0
    g7: LineSegment StartX=13.5 StartY=-4.5 StartZ=0 EndX=13.5 EndY=-11.5 EndZ=0
    g8: GeomPoint X=14.5 Y=-11.5 Z=0
  constraints (24):
    c: Coincident(g0,g1)
    c: Coincident(g1,g2)
    c: Coincident(g2,g3)
    c: Coincident(g3,g0)
    c: Horizontal(g0)
    c: Horizontal(g2)
    c: Vertical(g1)
    c: Vertical(g3)
    c: PointOnObject(g0,g-4)
    c: Coincident(g4,g5)
    c: Coincident(g5,g6)
    c: Coincident(g6,g7)
    c: Coincident(g7,g4)
    c: Horizontal(g4)
    c: Horizontal(g6)
    c: Vertical(g5)
    c: Vertical(g7)
    c: Symmetric(g4,g4,g8)
    c: Symmetric(g-3,g-3,g8)
    c: Vertical(g0,g4)
    c: Vertical(g4,g0)
    c: DistanceX(g6,g6) = 2
    c: Equal(g5,g1)
    c: DistanceY(g5,g5) = 7
FEATURE [PartDesign::Pocket] Pocket091  label="Pocket091-servo_cantilever_slot"
  BaseFeature = -> Pocket090
  Direction = (1,-8e-16,7e-16)
  Length = 1.75
  Length2 = 5
  Placement = pos=(0,0,0) rot=(0.57735,0.57735,0.57735;2.0944rad)
  Profile = -> Sketch200
  ReferenceAxis = -> Sketch200 [N_Axis]
  Type = 0
FEATURE [Sketcher::SketchObject] Sketch201
  ExternalGeometry = -> [Pocket091]
  FullyConstrained = true
  MapMode = 5
  Placement = pos=(1.8e-15,4,-7e-16) rot=(0.57735,0.57735,0.57735;4.18879rad)
  Support = -> [Pocket091]
  sketch-geometry (6):
    g0: Circle CenterX=71 CenterY=-1.5 CenterZ=0 NormalX=0 NormalY=0 NormalZ=1 AngleXU=0 Radius=3.1
    g1: Circle CenterX=-6 CenterY=-1.5 CenterZ=0 NormalX=0 NormalY=0 NormalZ=1 AngleXU=0 Radius=3.1
    g2: LineSegment StartX=-6 StartY=-1.5 StartZ=0 EndX=-12 EndY=-9.5 EndZ=0
    g3: LineSegment StartX=71 StartY=-1.5 StartZ=0 EndX=77 EndY=-9.5 EndZ=0
    g4: LineSegment StartX=71 StartY=-1.5 StartZ=0 EndX=77 EndY=6.5 EndZ=0
    g5: LineSegment StartX=-12 StartY=6.5 StartZ=0 EndX=-6 EndY=-1.5 EndZ=0
  constraints (14):
    c: Equal(g1,g0)
    c: DistanceX(g-4,g1) = 6
    c: Coincident(g2,g1)
    c: Coincident(g2,g-4)
    c: Coincident(g3,g0)
    c: Coincident(g3,g-3)
    c: Coincident(g4,g0)
    c: Coincident(g4,g-3)
    c: Equal(g2,g3)
    c: Equal(g3,g4)
    c: Diameter(g0) = 6.2
    c: Coincident(g5,g-4)
    c: Coincident(g5,g1)
    c: Equal(g2,g5)
FEATURE [PartDesign::Pocket] Pocket092  label="Pocket092-mount_holes"
  BaseFeature = -> Pocket091
  Direction = (-4e-16,-1,1.1e-15)
  Length = 5
  Length2 = 5
  Placement = pos=(0,0,0) rot=(0.57735,0.57735,0.57735;2.0944rad)
  Profile = -> Sketch201
  ReferenceAxis = -> Sketch201 [N_Axis]
  Type = 0
FEATURE [App::FeaturePython] Constraints033  # WARN: FeaturePython — macro-defined, semantics opaque (R4)
  _Version = 1
FEATURE [App::FeaturePython] Elements033  # WARN: FeaturePython — macro-defined, semantics opaque (R4)
FEATURE [Sketcher::SketchObject] Sketch202
  FullyConstrained = true
  MapMode = 5
  Placement = pos=(0,0,0) rot=(0.57735,0.57735,0.57735;2.0944rad)
  Support = -> [YZ_Plane038]
  sketch-geometry (6):
    g0: LineSegment StartX=-50 StartY=-10 StartZ=0 EndX=-1.8181e-05 EndY=-10 EndZ=0
    g1: LineSegment StartX=-1.8181e-05 StartY=-10 StartZ=0 EndX=-1.8181e-05 EndY=10 EndZ=0
    g2: LineSegment StartX=-1.8181e-05 StartY=10 StartZ=0 EndX=-50 EndY=10 EndZ=0
    g3: LineSegment StartX=-50 StartY=10 StartZ=0 EndX=-50 EndY=-10 EndZ=0
    g4: ArcOfCircle CenterX=0 CenterY=0 CenterZ=0 NormalX=0 NormalY=0 NormalZ=1 AngleXU=0 Radius=10 StartAngle=4.71239 EndAngle=7.85398
    g5: Circle CenterX=0 CenterY=0 CenterZ=0 NormalX=0 NormalY=0 NormalZ=1 AngleXU=0 Radius=1.65
  constraints (16):
    c: Coincident(g0,g1)
    c: Coincident(g1,g2)
    c: Coincident(g2,g3)
    c: Coincident(g3,g0)
    c: Horizontal(g0)
    c: Horizontal(g2)
    c: Vertical(g1)
    c: Vertical(g3)
    c: Coincident(g4,g-1)
    c: Coincident(g4,g0)
    c: Coincident(g4,g1)
    c: Diameter(g4) = 20
    c: Coincident(g5,g4)
    c: Diameter(g5) = 3.3
    c: DistanceY(g3,g3) = 20
    c: DistanceX(g2) = -50
FEATURE [PartDesign::Pad] Pad103  label="Pad103-arm_body"
  Direction = (1,-2e-16,3e-16)
  Length = 8
  Length2 = 10
  Placement = pos=(0,0,0) rot=(0.57735,0.57735,0.57735;2.0944rad)
  Profile = -> Sketch202
  ReferenceAxis = -> Sketch202 [N_Axis]
  Type = 0
FEATURE [Sketcher::SketchObject] Sketch203
  ExternalGeometry = -> [Pad103]
  FullyConstrained = true
  MapMode = 5
  Placement = pos=(8,-1.8e-15,1.8e-15) rot=(0.57735,0.57735,0.57735;2.0944rad)
  Support = -> [Pad103]
  sketch-geometry (4):
    g0: ArcOfCircle CenterX=0 CenterY=10 CenterZ=0 NormalX=0 NormalY=0 NormalZ=1 AngleXU=0 Radius=45.4567 StartAngle=3.3634 EndAngle=3.59717
    g1: ArcOfCircle CenterX=-50 CenterY=2 CenterZ=0 NormalX=0 NormalY=0 NormalZ=1 AngleXU=0 Radius=6 StartAngle=5.94335 EndAngle=7.85398
    g2: LineSegment StartX=-50 StartY=8 StartZ=0 EndX=-50 EndY=-10 EndZ=0
    g3: LineSegment StartX=-50 StartY=-10 StartZ=0 EndX=-40.8205 EndY=-10 EndZ=0
  constraints (13):
    c: PointOnObject(g0,g-3)
    c: PointOnObject(g1,g-4)
    c: PointOnObject(g1,g-4)
    c: Coincident(g0,g1)
    c: PointOnObject(g0,g-2)
    c: DistanceY(g0) = 10
    c: Radius(g1) = 6
    c: DistanceY(g-4,g1) = 12
    c: PointOnObject(g0,g-1)
    c: Coincident(g2,g1)
    c: Coincident(g2,g-4)
    c: Coincident(g3,g2)
    c: Coincident(g3,g0)
FEATURE [PartDesign::Pocket] Pocket093  label="Pocket093-latch_cutout"
  BaseFeature = -> Pad103
  Direction = (-1,4e-16,-4e-16)
  Length = 5
  Length2 = 5
  Placement = pos=(0,0,0) rot=(0.57735,0.57735,0.57735;2.0944rad)
  Profile = -> Sketch203
  ReferenceAxis = -> Sketch203 [N_Axis]
  Type = 0
FEATURE [Sketcher::SketchObject] Sketch204
  FullyConstrained = true
  MapMode = 5
  Placement = pos=(0,0,0) rot=(0.57735,0.57735,-0.57735;4.18879rad)
  Support = -> [Pocket093]
  sketch-geometry (5):
    g0: LineSegment StartX=0 StartY=0 StartZ=0 EndX=0 EndY=3.1 EndZ=0
    g1: LineSegment StartX=0 StartY=3.1 StartZ=0 EndX=0.3384 EndY=2.67871 EndZ=0
    g2: LineSegment StartX=0.3384 StartY=2.67871 StartZ=0 EndX=0.770939 EndY=3.00261 EndZ=0
    g3: LineSegment StartX=0.770939 StartY=3.00261 StartZ=0 EndX=0 EndY=0 EndZ=0
    g4: LineSegment StartX=0.3384 StartY=2.67871 StartZ=0 EndX=0 EndY=0 EndZ=0
  constraints (13):
    c: Coincident(g0,g-1)
    c: PointOnObject(g0,g-2)
    c: Coincident(g1,g0)
    c: Coincident(g2,g1)
    c: Coincident(g3,g2)
    c: Coincident(g3,g0)
    c: Distance(g0) = 3.1
    c: Equal(g3,g0)
    c: Angle(g3,g0) = 0.251327
    c: Coincident(g4,g1)
    c: Coincident(g4,g0)
    c: Angle(g4,g0) = 0.125664
    c: Distance(g4) = 2.7
FEATURE [PartDesign::Pocket] Pocket094  label="Pocket094-spline"
  BaseFeature = -> Pocket093
  Direction = (1,-6e-16,5e-16)
  Length = 3.75
  Length2 = 5
  Placement = pos=(0,0,0) rot=(0.57735,0.57735,0.57735;2.0944rad)
  Profile = -> Sketch204
  ReferenceAxis = -> Sketch204 [N_Axis]
  Type = 0
FEATURE [PartDesign::PolarPattern] PolarPattern002
  Angle = 360
  Axis = -> X_Axis037
  BaseFeature = -> Pocket094
  Occurrences = 25
  Originals = -> [Pocket094]
  Placement = pos=(0,0,0) rot=(0.57735,0.57735,0.57735;2.0944rad)
FEATURE [Sketcher::SketchObject] Sketch205
  FullyConstrained = true
  MapMode = 5
  Placement = pos=(8,-1.8e-15,1.8e-15) rot=(0.57735,0.57735,0.57735;2.0944rad)
  Support = -> [PolarPattern002]
  sketch-geometry (1):
    g0: Circle CenterX=0 CenterY=0 CenterZ=0 NormalX=0 NormalY=0 NormalZ=1 AngleXU=0 Radius=3.25
  constraints (2):
    c: Coincident(g0,g-1)
    c: Diameter(g0) = 6.5
FEATURE [PartDesign::Pocket] Pocket095
  BaseFeature = -> PolarPattern002
  Direction = (-1,8e-16,-6e-16)
  Length = 2
  Length2 = 5
  Placement = pos=(0,0,0) rot=(0.57735,0.57735,0.57735;2.0944rad)
  Profile = -> Sketch205
  ReferenceAxis = -> Sketch205 [N_Axis]
  Type = 0
FEATURE [PartDesign::Fillet] Fillet091  label="Fillet091-screw_hole"
  Base = -> Pocket095 [Edge174]
  BaseFeature = -> Pocket095
  Placement = pos=(0,0,0) rot=(0.57735,0.57735,0.57735;2.0944rad)
  Radius = 0.45
  SupportTransform = false
  UseAllEdges = false
FEATURE [PartDesign::Fillet] Fillet092  label="Fillet092-spline"
  Base = -> Fillet091 [Face30,Face31,Face32,Face33,Face34,Face35,Face36,Face37,Face38,Face14,Face15,Face16,Face17,Face18,Face19,Face29,Face28,Face27,Face26,Face25,Face24,Face23,Face22,Face21,Face20]
  BaseFeature = -> Fillet091
  Placement = pos=(0,0,0) rot=(0.57735,0.57735,0.57735;2.0944rad)
  Radius = 0.1
  SupportTransform = false
  UseAllEdges = false
FEATURE [Sketcher::SketchObject] Sketch206
  ExternalGeometry = -> [Fillet092]
  FullyConstrained = true
  MapMode = 5
  Placement = pos=(8,-1.8e-15,1.8e-15) rot=(0.57735,0.57735,0.57735;2.0944rad)
  Support = -> [Fillet092]
  sketch-geometry (10):
    g0: LineSegment StartX=-8 StartY=1.46667 StartZ=0 EndX=-22 EndY=-6 EndZ=0
    g1: LineSegment StartX=-8 StartY=1.46667 StartZ=0 EndX=-8 EndY=-6 EndZ=0
    g2: LineSegment StartX=-8 StartY=-6 StartZ=0 EndX=-22 EndY=-6 EndZ=0
    g3: LineSegment StartX=-8 StartY=6 StartZ=0 EndX=-30.5 EndY=-6 EndZ=0
    g4: LineSegment StartX=-30.5 StartY=-6 StartZ=0 EndX=-30.5 EndY=6 EndZ=0
    g5: LineSegment StartX=-30.5 StartY=6 StartZ=0 EndX=-8 EndY=6 EndZ=0
    g6: LineSegment StartX=-34.5 StartY=-6 StartZ=0 EndX=-34.5 EndY=6 EndZ=0
    g7: LineSegment StartX=-34.5 StartY=6 StartZ=0 EndX=-39.5 EndY=6 EndZ=0
    g8: LineSegment StartX=-39.5 StartY=6 StartZ=0 EndX=-34.5 EndY=-6 EndZ=0
    g9: LineSegment StartX=-22 StartY=-6 StartZ=0 EndX=-23.8824 EndY=-2.47059 EndZ=0
  constraints (30):
    c: Coincident(g1,g0)
    c: Vertical(g1)
    c: Coincident(g2,g1)
    c: Coincident(g2,g0)
    c: Horizontal(g2)
    c: Coincident(g4,g3)
    c: Vertical(g4)
    c: Coincident(g5,g4)
    c: Coincident(g5,g3)
    c: Horizontal(g5)
    c: Vertical(g6)
    c: Coincident(g7,g6)
    c: Horizontal(g7)
    c: Coincident(g8,g7)
    c: Coincident(g8,g6)
    c: Horizontal(g6,g4)
    c: Horizontal(g0,g3)
    c: Horizontal(g3,g6)
    c: DistanceX(g6,g4) = 4
    c: Coincident(g9,g0)
    c: PointOnObject(g9,g3)
    c: Angle(g0,g9) = 1.5708
    c: Distance(g9) = 4
    c: Vertical(g0,g3)
    c: DistanceY(g-4,g1) = 4
    c: DistanceY(g3,g-3) = 4
    c: DistanceX(g5,g5) = 22.5
    c: DistanceX(g7,g7) = 5
    c: DistanceX(g1,g-1) = 8
    c: Angle(g9,g3) = 1.5708
FEATURE [PartDesign::Pocket] Pocket096
  BaseFeature = -> Fillet092
  Direction = (-1,1.1e-15,-7e-16)
  Length = 5
  Length2 = 5
  Placement = pos=(0,0,0) rot=(0.57735,0.57735,0.57735;2.0944rad)
  Profile = -> Sketch206
  ReferenceAxis = -> Sketch206 [N_Axis]
  Type = 1
FEATURE [PartDesign::Fillet] Fillet093  label="Fillet093-mount_plate"
  Base = -> Pocket092 [Edge12,Edge16,Edge11,Edge14]
  BaseFeature = -> Pocket092
  Placement = pos=(0,0,0) rot=(0.57735,0.57735,0.57735;2.0944rad)
  Radius = 7.5
  SupportTransform = false
  UseAllEdges = false
FEATURE [PartDesign::Fillet] Fillet094  label="Fillet094-servo_plate"
  Base = -> Fillet093 [Edge77,Edge46]
  BaseFeature = -> Fillet093
  Placement = pos=(0,0,0) rot=(0.57735,0.57735,0.57735;2.0944rad)
  Radius = 11
  SupportTransform = false
  UseAllEdges = false
FEATURE [PartDesign::Fillet] Fillet095  label="Fillet095-mount_plate_surface"
  Base = -> Fillet094 [Face36]
  BaseFeature = -> Fillet094
  Placement = pos=(0,0,0) rot=(0.57735,0.57735,0.57735;2.0944rad)
  Radius = 1.2
  SupportTransform = false
  UseAllEdges = false
FEATURE [Sketcher::SketchObject] Sketch207
  ExternalGeometry = -> [Fillet095]
  FullyConstrained = true
  MapMode = 5
  Placement = pos=(0,0,0) rot=(0.57735,0.57735,-0.57735;4.18879rad)
  Support = -> [Fillet095]
  sketch-geometry (8):
    g0: LineSegment StartX=4 StartY=4e-15 StartZ=0 EndX=19 EndY=4e-15 EndZ=0
    g1: LineSegment StartX=19 StartY=4e-15 StartZ=0 EndX=19 EndY=-3 EndZ=0
    g2: LineSegment StartX=19 StartY=-3 StartZ=0 EndX=4 EndY=-3 EndZ=0
    g3: LineSegment StartX=4 StartY=-3 StartZ=0 EndX=4 EndY=4e-15 EndZ=0
    g4: LineSegment StartX=4 StartY=-62 StartZ=0 EndX=19 EndY=-62 EndZ=0
    g5: LineSegment StartX=19 StartY=-62 StartZ=0 EndX=19 EndY=-65 EndZ=0
    g6: LineSegment StartX=19 StartY=-65 StartZ=0 EndX=4 EndY=-65 EndZ=0
    g7: LineSegment StartX=4 StartY=-65 StartZ=0 EndX=4 EndY=-62 EndZ=0
  constraints (22):
    c: Coincident(g0,g1)
    c: Coincident(g1,g2)
    c: Coincident(g2,g3)
    c: Coincident(g3,g0)
    c: Horizontal(g0)
    c: Horizontal(g2)
    c: Vertical(g1)
    c: Vertical(g3)
    c: Coincident(g4,g5)
    c: Coincident(g5,g6)
    c: Coincident(g6,g7)
    c: Coincident(g7,g4)
    c: Horizontal(g4)
    c: Horizontal(g6)
    c: Vertical(g5)
    c: Vertical(g7)
    c: Equal(g5,g1)
    c: Equal(g2,g4)
    c: Coincident(g6,g-4)
    c: DistanceY(g5,g5) = 3
    c: DistanceX(g6,g6) = 15
    c: Coincident(g0,g-3)
FEATURE [PartDesign::Pad] Pad104  label="Pad104-cantilever"
  BaseFeature = -> Fillet095
  Direction = (-1,1.3e-15,-8e-16)
  Length = 8
  Length2 = 10
  Placement = pos=(0,0,0) rot=(0.57735,0.57735,0.57735;2.0944rad)
  Profile = -> Sketch207
  ReferenceAxis = -> Sketch207 [N_Axis]
  Type = 0
FEATURE [Sketcher::SketchObject] Sketch208
  ExternalGeometry = -> [Pad104]
  FullyConstrained = true
  MapMode = 5
  Placement = pos=(-5.07e-14,1.82e-14,65) rot=(0,0,-1;1.5708rad)
  Support = -> [Pad104]
  sketch-geometry (3):
    g0: LineSegment StartX=-19 StartY=-4.3e-14 StartZ=0 EndX=-4 EndY=-8 EndZ=0
    g1: LineSegment StartX=-19 StartY=-4.3e-14 StartZ=0 EndX=-19 EndY=-8 EndZ=0
    g2: LineSegment StartX=-19 StartY=-8 StartZ=0 EndX=-4 EndY=-8 EndZ=0
  constraints (6):
    c: Coincident(g0,g-3)
    c: Coincident(g0,g-4)
    c: Coincident(g1,g0)
    c: Coincident(g1,g-4)
    c: Coincident(g2,g1)
    c: Coincident(g2,g0)
FEATURE [PartDesign::Pocket] Pocket097  label="Pocket097-cantilever"
  BaseFeature = -> Pad104
  Direction = (9e-16,-4e-16,-1)
  Length = 5
  Length2 = 5
  Placement = pos=(0,0,0) rot=(0.57735,0.57735,0.57735;2.0944rad)
  Profile = -> Sketch208
  ReferenceAxis = -> Sketch208 [N_Axis]
  Type = 1
FEATURE [PartDesign::Fillet] Fillet096
  Base = -> Pocket097 [Edge31,Edge18]
  BaseFeature = -> Pocket097
  Placement = pos=(0,0,0) rot=(0.57735,0.57735,0.57735;2.0944rad)
  Radius = 0.5
  SupportTransform = false
  UseAllEdges = false
FEATURE [PartDesign::Fillet] Fillet097
  Base = -> Fillet096 [Edge114,Edge113,Edge98,Edge97,Edge124,Edge117,Edge105,Edge104,Edge68,Edge66,Edge67,Edge65]
  BaseFeature = -> Fillet096
  Placement = pos=(0,0,0) rot=(0.57735,0.57735,0.57735;2.0944rad)
  Radius = 0.5
  SupportTransform = false
  UseAllEdges = false
FEATURE [PartDesign::Body] Body026002
  Group = -> [Sketch197,Pad101,Sketch198,Pad102,Sketch199,Pocket090,Sketch200,Pocket091,Sketch201,Pocket092,Fillet093,Fillet094,Fillet095,Sketch207,Pad104,Sketch208,Pocket097,Fillet096,Fillet097]
  Origin = -> Origin036
  Tip = -> Fillet097
FEATURE [Part::FeaturePython] Parts032  # WARN: FeaturePython — macro-defined, semantics opaque (R4)
  Group = -> [Body026002]
  GroupMode = 0
FEATURE [PartDesign::Fillet] Fillet098
  Base = -> Pocket096 [Edge473,Edge471]
  BaseFeature = -> Pocket096
  Placement = pos=(0,0,0) rot=(0.57735,0.57735,0.57735;2.0944rad)
  Radius = 1
  SupportTransform = false
  UseAllEdges = false
FEATURE [PartDesign::Fillet] Fillet099
  Base = -> Fillet098 [Face1]
  BaseFeature = -> Fillet098
  Placement = pos=(0,0,0) rot=(0.57735,0.57735,0.57735;2.0944rad)
  Radius = 0.5
  SupportTransform = false
  UseAllEdges = false
FEATURE [PartDesign::Fillet] Fillet100
  Base = -> Fillet099 [Edge60]
  BaseFeature = -> Fillet099
  Placement = pos=(0,0,0) rot=(0.57735,0.57735,0.57735;2.0944rad)
  Radius = 2.5
  SupportTransform = false
  UseAllEdges = false
FEATURE [PartDesign::Fillet] Fillet101
  Base = -> Fillet100 [Face12]
  BaseFeature = -> Fillet100
  Placement = pos=(0,0,0) rot=(0.57735,0.57735,0.57735;2.0944rad)
  Radius = 0.25
  SupportTransform = false
  UseAllEdges = false
FEATURE [PartDesign::Fillet] Fillet102
  Base = -> Fillet101 [Face209]
  BaseFeature = -> Fillet101
  Placement = pos=(0,0,0) rot=(0.57735,0.57735,0.57735;2.0944rad)
  Radius = 0.2
  SupportTransform = false
  UseAllEdges = false
FEATURE [PartDesign::Body] Body026003
  Group = -> [Sketch202,Pad103,Sketch203,Pocket093,Sketch204,Pocket094,PolarPattern002,Sketch205,Pocket095,Fillet091,Fillet092,Sketch206,Pocket096,Fillet098,Fillet099,Fillet100,Fillet101,Fillet102]
  Origin = -> Origin037
  Tip = -> Fillet102
FEATURE [Part::FeaturePython] Parts033  # WARN: FeaturePython — macro-defined, semantics opaque (R4)
  Group = -> [Body026003]
  GroupMode = 0
FEATURE [Part::FeaturePython] Assembly033  label="assy-lock_servo_arm"  # WARN: FeaturePython — macro-defined, semantics opaque (R4)
  AutoRelax = true
  BuildShape = 0
  Freeze = false
  Group = -> [Constraints033,Elements033,Parts033]
  Placement = pos=(17.37,-450.48,69.1898) rot=(1,0,0;0.698132rad)
  Verbose = false
  _SolverType = 1
  _Version = 1
FEATURE [App::FeaturePython] Constraints034  # WARN: FeaturePython — macro-defined, semantics opaque (R4)
  _Version = 1
FEATURE [App::FeaturePython] Elements034  # WARN: FeaturePython — macro-defined, semantics opaque (R4)
FEATURE [Sketcher::SketchObject] Sketch209
  FullyConstrained = false
  MapMode = 5
  Placement = pos=(0,0,0) rot=(1,0,0;1.5708rad)
  Support = -> [XZ_Plane038]
  sketch-geometry (4):
    g0: LineSegment StartX=0 StartY=0 StartZ=0 EndX=43.0754 EndY=0 EndZ=0
    g1: LineSegment StartX=43.0754 StartY=0 StartZ=0 EndX=43.0754 EndY=20.5261 EndZ=0
    g2: LineSegment StartX=43.0754 StartY=20.5261 StartZ=0 EndX=0 EndY=20.5261 EndZ=0
    g3: LineSegment StartX=0 StartY=20.5261 StartZ=0 EndX=0 EndY=0 EndZ=0
  constraints (9):
    c: Coincident(g0,g1)
    c: Coincident(g1,g2)
    c: Coincident(g2,g3)
    c: Coincident(g3,g0)
    c: Horizontal(g0)
    c: Horizontal(g2)
    c: Vertical(g1)
    c: Vertical(g3)
    c: Coincident(g0,g-1)
FEATURE [PartDesign::Pad] Pad105
  Direction = (0,-1,2e-16)
  Length = 10
  Length2 = 10
  Placement = pos=(0,0,0) rot=(1,0,0;1.5708rad)
  Profile = -> Sketch209
  ReferenceAxis = -> Sketch209 [N_Axis]
  Reversed = true
  Type = 0
FEATURE [PartDesign::Body] Body026004
  Group = -> [Sketch209,Pad105]
  Origin = -> Origin038
  Tip = -> Pad105
FEATURE [Part::FeaturePython] Parts034  # WARN: FeaturePython — macro-defined, semantics opaque (R4)
  Group = -> [Body026004]
  GroupMode = 0
FEATURE [Part::FeaturePython] Assembly034  label="assy-RL_bumper"  # WARN: FeaturePython — macro-defined, semantics opaque (R4)
  AutoRelax = true
  BuildShape = 0
  Freeze = false
  Group = -> [Constraints034,Elements034,Parts034]
  Placement = pos=(13,-295,0) rot=(0,0,1;0rad)
  Verbose = false
  _SolverType = 1
  _Version = 1
FEATURE [App::FeaturePython] Constraints035  # WARN: FeaturePython — macro-defined, semantics opaque (R4)
  _Version = 1
FEATURE [Sketcher::SketchObject] Sketch210
  FullyConstrained = true
  MapMode = 5
  Support = -> [XY_Plane039]
  sketch-geometry (4):
    g0: LineSegment StartX=0 StartY=0 StartZ=0 EndX=20 EndY=0 EndZ=0
    g1: LineSegment StartX=20 StartY=0 StartZ=0 EndX=20 EndY=-40 EndZ=0
    g2: LineSegment StartX=20 StartY=-40 StartZ=0 EndX=0 EndY=-40 EndZ=0
    g3: LineSegment StartX=0 StartY=-40 StartZ=0 EndX=0 EndY=0 EndZ=0
  constraints (11):
    c: Coincident(g0,g1)
    c: Coincident(g1,g2)
    c: Coincident(g2,g3)
    c: Coincident(g3,g0)
    c: Horizontal(g0)
    c: Horizontal(g2)
    c: Vertical(g1)
    c: Vertical(g3)
    c: Coincident(g0,g-1)
    c: DistanceX(g2,g2) = 20
    c: DistanceY(g1,g1) = 40
FEATURE [PartDesign::Pad] Pad106  label="Pad106-base"
  Direction = (0,0,1)
  Length = 6
  Length2 = 10
  Profile = -> Sketch210
  ReferenceAxis = -> Sketch210 [N_Axis]
  Type = 0
FEATURE [Sketcher::SketchObject] Sketch211
  ExternalGeometry = -> [Pad106]
  FullyConstrained = true
  MapMode = 5
  Placement = pos=(0,0,6) rot=(0,0,1;0rad)
  Support = -> [Pad106]
  sketch-geometry (5):
    g0: LineSegment StartX=0 StartY=-13.5 StartZ=0 EndX=8 EndY=-13.5 EndZ=0
    g1: LineSegment StartX=8 StartY=-13.5 StartZ=0 EndX=8 EndY=-26.5 EndZ=0
    g2: LineSegment StartX=8 StartY=-26.5 StartZ=0 EndX=0 EndY=-26.5 EndZ=0
    g3: LineSegment StartX=0 StartY=-26.5 StartZ=0 EndX=0 EndY=-13.5 EndZ=0
    g4: GeomPoint X=0 Y=-20 Z=0
  constraints (12):
    c: Coincident(g0,g1)
    c: Coincident(g1,g2)
    c: Coincident(g2,g3)
    c: Coincident(g3,g0)
    c: Horizontal(g0)
    c: Horizontal(g2)
    c: Vertical(g1)
    c: Vertical(g3)
    c: DistanceX(g2,g2) = 8
    c: DistanceY(g3,g3) = 13
    c: Symmetric(g3,g3,g4)
    c: Symmetric(g-3,g-3,g4)
FEATURE [PartDesign::Pad] Pad107  label="Pad107-vertical"
  BaseFeature = -> Pad106
  Direction = (0,0,1)
  Length = 20
  Length2 = 10
  Profile = -> Sketch211
  ReferenceAxis = -> Sketch211 [N_Axis]
  Type = 0
FEATURE [PartDesign::Fillet] Fillet103  label="Fillet103-base"
  Base = -> Pad107 [Edge5,Edge10,Edge1,Edge2]
  BaseFeature = -> Pad107
  Radius = 9
  SupportTransform = false
  UseAllEdges = false
FEATURE [PartDesign::Fillet] Fillet104  label="Fillet104-vertical"
  Base = -> Fillet103 [Edge36,Edge32]
  BaseFeature = -> Fillet103
  Radius = 6
  SupportTransform = false
  UseAllEdges = false
FEATURE [Sketcher::SketchObject] Sketch212
  ExternalGeometry = -> [Fillet104]
  FullyConstrained = true
  MapMode = 5
  Placement = pos=(0,0,6) rot=(0,0,1;0rad)
  Support = -> [Fillet104]
  sketch-geometry (5):
    g0: Circle CenterX=10 CenterY=-6 CenterZ=0 NormalX=0 NormalY=0 NormalZ=1 AngleXU=0 Radius=5
    g1: Circle CenterX=10 CenterY=-34 CenterZ=0 NormalX=0 NormalY=0 NormalZ=1 AngleXU=0 Radius=5
    g2: LineSegment StartX=9 StartY=0 StartZ=0 EndX=10 EndY=-6 EndZ=0
    g3: LineSegment StartX=10 StartY=-6 StartZ=0 EndX=11 EndY=0 EndZ=0
    g4: LineSegment StartX=10 StartY=-34 StartZ=0 EndX=9 EndY=-40 EndZ=0
  constraints (12):
    c: Vertical(g1,g0)
    c: Equal(g0,g1)
    c: Coincident(g2,g-3)
    c: Coincident(g2,g0)
    c: Coincident(g3,g0)
    c: Coincident(g3,g-3)
    c: Equal(g3,g2)
    c: Diameter(g0) = 10
    c: DistanceY(g0) = -6
    c: Coincident(g4,g1)
    c: Coincident(g4,g-4)
    c: Equal(g4,g2)
FEATURE [PartDesign::Pocket] Pocket098  label="Pocket098-horizontal_inset"
  BaseFeature = -> Fillet104
  Direction = (0,0,-1)
  Length = 3
  Length2 = 5
  Profile = -> Sketch212
  ReferenceAxis = -> Sketch212 [N_Axis]
  Type = 0
FEATURE [Sketcher::SketchObject] Sketch213
  ExternalGeometry = -> [Pocket098]
  FullyConstrained = true
  MapMode = 5
  Placement = pos=(0,0,0) rot=(0.57735,-0.57735,-0.57735;2.0944rad)
  Support = -> [Pocket098]
  sketch-geometry (3):
    g0: Circle CenterX=20 CenterY=19 CenterZ=0 NormalX=0 NormalY=0 NormalZ=1 AngleXU=0 Radius=5
    g1: LineSegment StartX=19.5 StartY=26 StartZ=0 EndX=20 EndY=19 EndZ=0
    g2: LineSegment StartX=20 StartY=19 StartZ=0 EndX=20.5 EndY=26 EndZ=0
  constraints (7):
    c: Diameter(g0) = 10
    c: Coincident(g1,g-3)
    c: Coincident(g1,g0)
    c: Coincident(g2,g0)
    c: Coincident(g2,g-3)
    c: Equal(g1,g2)
    c: DistanceY(g0,g2) = 7
FEATURE [PartDesign::Pocket] Pocket099  label="Pocket099-vertical_inset"
  BaseFeature = -> Pocket098
  Direction = (1,0,0)
  Length = 3
  Length2 = 5
  Profile = -> Sketch213
  ReferenceAxis = -> Sketch213 [N_Axis]
  Type = 0
FEATURE [Sketcher::SketchObject] Sketch214
  ExternalGeometry = -> [Pocket099]
  FullyConstrained = true
  MapMode = 5
  Placement = pos=(0,0,3) rot=(0,0,1;0rad)
  Support = -> [Pocket099]
  sketch-geometry (2):
    g0: Circle CenterX=10 CenterY=-6 CenterZ=0 NormalX=0 NormalY=0 NormalZ=1 AngleXU=0 Radius=2.65
    g1: Circle CenterX=10 CenterY=-34 CenterZ=0 NormalX=0 NormalY=0 NormalZ=1 AngleXU=0 Radius=2.65
  constraints (4):
    c: Coincident(g0,g-3)
    c: Coincident(g1,g-4)
    c: Equal(g1,g0)
    c: Diameter(g1) = 5.3
FEATURE [PartDesign::Pocket] Pocket100
  BaseFeature = -> Pocket099
  Direction = (0,0,-1)
  Length = 5
  Length2 = 5
  Profile = -> Sketch214
  ReferenceAxis = -> Sketch214 [N_Axis]
  Type = 0
FEATURE [Sketcher::SketchObject] Sketch215
  ExternalGeometry = -> [Pocket100]
  FullyConstrained = true
  MapMode = 5
  Placement = pos=(3,0,0) rot=(0.57735,-0.57735,-0.57735;2.0944rad)
  Support = -> [Pocket100]
  sketch-geometry (1):
    g0: Circle CenterX=20 CenterY=19 CenterZ=0 NormalX=0 NormalY=0 NormalZ=1 AngleXU=0 Radius=2.65
  constraints (2):
    c: Coincident(g0,g-3)
    c: Diameter(g0) = 5.3
FEATURE [PartDesign::Pocket] Pocket101
  BaseFeature = -> Pocket100
  Direction = (1,0,0)
  Length = 5
  Length2 = 5
  Profile = -> Sketch215
  ReferenceAxis = -> Sketch215 [N_Axis]
  Type = 0
FEATURE [PartDesign::Fillet] Fillet105
  Base = -> Pocket101 [Edge19,Edge21,Edge3]
  BaseFeature = -> Pocket101
  Radius = 2
  SupportTransform = false
  UseAllEdges = false
FEATURE [PartDesign::Chamfer] Chamfer012
  Angle = 45
  Base = -> Fillet105 [Edge54]
  BaseFeature = -> Fillet105
  ChamferType = 0
  FlipDirection = false
  Size = 2.5
  Size2 = 1
  SupportTransform = false
  UseAllEdges = false
FEATURE [PartDesign::Fillet] Fillet106
  Base = -> Chamfer012 [Face31,Face32,Face37]
  BaseFeature = -> Chamfer012
  Radius = 0.5
  SupportTransform = false
  UseAllEdges = false
FEATURE [PartDesign::Fillet] Fillet107
  Base = -> Fillet106 [Face26,Face38]
  BaseFeature = -> Fillet106
  Radius = 0.5
  SupportTransform = false
  UseAllEdges = false
FEATURE [Sketcher::SketchObject] Sketch216
  FullyConstrained = true
  MapMode = 5
  Support = -> [XY_Plane040]
  sketch-geometry (4):
    g0: LineSegment StartX=0 StartY=0 StartZ=0 EndX=20 EndY=0 EndZ=0
    g1: LineSegment StartX=20 StartY=0 StartZ=0 EndX=20 EndY=-40 EndZ=0
    g2: LineSegment StartX=20 StartY=-40 StartZ=0 EndX=0 EndY=-40 EndZ=0
    g3: LineSegment StartX=0 StartY=-40 StartZ=0 EndX=0 EndY=0 EndZ=0
  constraints (11):
    c: Coincident(g0,g1)
    c: Coincident(g1,g2)
    c: Coincident(g2,g3)
    c: Coincident(g3,g0)
    c: Horizontal(g0)
    c: Horizontal(g2)
    c: Vertical(g1)
    c: Vertical(g3)
    c: Coincident(g0,g-1)
    c: DistanceX(g2,g2) = 20
    c: DistanceY(g1,g1) = 40
FEATURE [PartDesign::Pad] Pad108  label="Pad106-base001"
  Direction = (0,0,1)
  Length = 6
  Length2 = 10
  Profile = -> Sketch216
  ReferenceAxis = -> Sketch216 [N_Axis]
  Type = 0
FEATURE [Sketcher::SketchObject] Sketch217
  FullyConstrained = true
  MapMode = 5
  Placement = pos=(0,0,6) rot=(0,0,1;0rad)
  Support = -> [Pad108]
  sketch-geometry (4):
    g0: LineSegment StartX=0 StartY=-14.5 StartZ=0 EndX=20 EndY=-14.5 EndZ=0
    g1: LineSegment StartX=20 StartY=-14.5 StartZ=0 EndX=20 EndY=-20.5 EndZ=0
    g2: LineSegment StartX=20 StartY=-20.5 StartZ=0 EndX=0 EndY=-20.5 EndZ=0
    g3: LineSegment StartX=0 StartY=-20.5 StartZ=0 EndX=0 EndY=-14.5 EndZ=0
  constraints (12):
    c: Coincident(g0,g1)
    c: Coincident(g1,g2)
    c: Coincident(g2,g3)
    c: Coincident(g3,g0)
    c: Horizontal(g0)
    c: Horizontal(g2)
    c: Vertical(g1)
    c: Vertical(g3)
    c: DistanceX(g2,g2) = 20
    c: DistanceY(g3,g3) = 6
    c: PointOnObject(g2,g-2)
    c: DistanceY(g0) = -14.5
FEATURE [PartDesign::Pad] Pad109  label="Pad107-vertical001"
  BaseFeature = -> Pad108
  Direction = (0,0,1)
  Length = 20
  Length2 = 10
  Profile = -> Sketch217
  ReferenceAxis = -> Sketch217 [N_Axis]
  Type = 0
FEATURE [PartDesign::Fillet] Fillet110  label="Fillet103-base001"
  Base = -> Pad109 [Edge5,Edge10,Edge1,Edge2]
  BaseFeature = -> Pad109
  Radius = 9
  SupportTransform = false
  UseAllEdges = false
FEATURE [App::FeaturePython] Constraints036  # WARN: FeaturePython — macro-defined, semantics opaque (R4)
  _Version = 1
FEATURE [Sketcher::SketchObject] Sketch218
  ExternalGeometry = -> [Fillet110]
  FullyConstrained = true
  MapMode = 5
  Placement = pos=(0,0,6) rot=(0,0,1;0rad)
  Support = -> [Fillet110]
  sketch-geometry (5):
    g0: Circle CenterX=10 CenterY=-7 CenterZ=0 NormalX=0 NormalY=0 NormalZ=1 AngleXU=0 Radius=5
    g1: Circle CenterX=10 CenterY=-33 CenterZ=0 NormalX=0 NormalY=0 NormalZ=1 AngleXU=0 Radius=5
    g2: LineSegment StartX=9 StartY=0 StartZ=0 EndX=10 EndY=-7 EndZ=0
    g3: LineSegment StartX=10 StartY=-7 StartZ=0 EndX=11 EndY=0 EndZ=0
    g4: LineSegment StartX=10 StartY=-33 StartZ=0 EndX=9 EndY=-40 EndZ=0
  constraints (12):
    c: Equal(g1,g0)
    c: Vertical(g1,g0)
    c: Coincident(g2,g-3)
    c: Coincident(g2,g0)
    c: Coincident(g3,g0)
    c: Coincident(g3,g-3)
    c: Equal(g3,g2)
    c: DistanceY(g0) = -7
    c: Diameter(g0) = 10
    c: Coincident(g4,g1)
    c: Coincident(g4,g-4)
    c: Equal(g4,g2)
FEATURE [PartDesign::Pocket] Pocket102  label="Pocket102-base_inset"
  BaseFeature = -> Fillet110
  Direction = (0,0,-1)
  Length = 3
  Length2 = 5
  Profile = -> Sketch218
  ReferenceAxis = -> Sketch218 [N_Axis]
  Type = 0
FEATURE [Sketcher::SketchObject] Sketch219
  ExternalGeometry = -> [Pocket102]
  FullyConstrained = true
  MapMode = 5
  Placement = pos=(0,0,3) rot=(0,0,1;0rad)
  Support = -> [Pocket102]
  sketch-geometry (2):
    g0: Circle CenterX=10 CenterY=-7 CenterZ=0 NormalX=0 NormalY=0 NormalZ=1 AngleXU=0 Radius=2.65
    g1: Circle CenterX=10 CenterY=-33 CenterZ=0 NormalX=0 NormalY=0 NormalZ=1 AngleXU=0 Radius=2.65
  constraints (4):
    c: Coincident(g0,g-3)
    c: Coincident(g1,g-4)
    c: Equal(g1,g0)
    c: Diameter(g0) = 5.3
FEATURE [PartDesign::Pocket] Pocket103
  BaseFeature = -> Pocket102
  Direction = (0,0,-1)
  Length = 5
  Length2 = 5
  Profile = -> Sketch219
  ReferenceAxis = -> Sketch219 [N_Axis]
  Type = 0
FEATURE [PartDesign::Fillet] Fillet111
  Base = -> Pocket103 [Edge45,Edge47]
  BaseFeature = -> Pocket103
  Radius = 9
  SupportTransform = false
  UseAllEdges = false
FEATURE [Sketcher::SketchObject] Sketch220
  ExternalGeometry = -> [Fillet111]
  FullyConstrained = true
  MapMode = 5
  Placement = pos=(0,-14.5,0) rot=(0,0.707107,0.707107;3.14159rad)
  Support = -> [Fillet111]
  sketch-geometry (3):
    g0: Circle CenterX=-10 CenterY=20 CenterZ=0 NormalX=0 NormalY=0 NormalZ=1 AngleXU=0 Radius=5
    g1: LineSegment StartX=-11 StartY=26 StartZ=0 EndX=-10 EndY=20 EndZ=0
    g2: LineSegment StartX=-10 StartY=20 StartZ=0 EndX=-9 EndY=26 EndZ=0
  constraints (7):
    c: Coincident(g1,g-3)
    c: Coincident(g1,g0)
    c: Coincident(g2,g0)
    c: Coincident(g2,g-3)
    c: Equal(g2,g1)
    c: DistanceY(g0,g2) = 6
    c: Diameter(g0) = 10
FEATURE [PartDesign::Pocket] Pocket104
  BaseFeature = -> Fillet111
  Direction = (0,-1,2e-16)
  Length = 3
  Length2 = 5
  Profile = -> Sketch220
  ReferenceAxis = -> Sketch220 [N_Axis]
  Type = 0
FEATURE [Sketcher::SketchObject] Sketch221
  ExternalGeometry = -> [Pocket104]
  FullyConstrained = true
  MapMode = 5
  Placement = pos=(2.1e-15,-17.5,3.7e-15) rot=(0,0.707107,0.707107;3.14159rad)
  Support = -> [Pocket104]
  sketch-geometry (1):
    g0: Circle CenterX=-10 CenterY=20 CenterZ=0 NormalX=0 NormalY=0 NormalZ=1 AngleXU=0 Radius=2.65
  constraints (2):
    c: Coincident(g0,g-3)
    c: Diameter(g0) = 5.3
FEATURE [PartDesign::Pocket] Pocket105
  BaseFeature = -> Pocket104
  Direction = (1e-16,-1,2e-16)
  Length = 5
  Length2 = 5
  Profile = -> Sketch221
  ReferenceAxis = -> Sketch221 [N_Axis]
  Type = 0
FEATURE [PartDesign::Fillet] Fillet112
  Base = -> Pocket105 [Edge3,Edge27]
  BaseFeature = -> Pocket105
  Radius = 2
  SupportTransform = false
  UseAllEdges = false
FEATURE [PartDesign::Chamfer] Chamfer013
  Angle = 45
  Base = -> Fillet112 [Edge57]
  BaseFeature = -> Fillet112
  ChamferType = 0
  FlipDirection = false
  Size = 2.5
  Size2 = 1
  SupportTransform = false
  UseAllEdges = false
FEATURE [PartDesign::Fillet] Fillet113
  Base = -> Chamfer013 [Face29,Face34,Face28,Face36,Face37,Face31]
  BaseFeature = -> Chamfer013
  Radius = 0.5
  SupportTransform = false
  UseAllEdges = false
FEATURE [PartDesign::Fillet] Fillet114
  Base = -> Fillet113 [Face32]
  BaseFeature = -> Fillet113
  Radius = 0.5
  SupportTransform = false
  UseAllEdges = false
FEATURE [PartDesign::Fillet] Fillet115
  Base = -> Fillet114 [Edge123]
  BaseFeature = -> Fillet114
  Radius = 0.4
  SupportTransform = false
  UseAllEdges = false
FEATURE [PartDesign::Body] Body026006
  Group = -> [Sketch216,Pad108,Sketch217,Pad109,Fillet110,Sketch218,Pocket102,Sketch219,Pocket103,Fillet111,Sketch220,Pocket104,Sketch221,Pocket105,Fillet112,Chamfer013,Fillet113,Fillet114,Fillet115]
  Origin = -> Origin040
  Tip = -> Fillet115
FEATURE [Part::FeaturePython] Parts036  # WARN: FeaturePython — macro-defined, semantics opaque (R4)
  Group = -> [Body026006]
  GroupMode = 0
FEATURE [Sketcher::SketchObject] Sketch222
  ExternalGeometry = -> [Fillet107]
  FullyConstrained = true
  MapMode = 5
  Placement = pos=(0,0,0) rot=(0.57735,-0.57735,-0.57735;2.0944rad)
  Support = -> [Fillet107]
  sketch-geometry (5):
    g0: LineSegment StartX=10 StartY=26 StartZ=0 EndX=30 EndY=26 EndZ=0
    g1: LineSegment StartX=30 StartY=26 StartZ=0 EndX=30 EndY=6 EndZ=0
    g2: LineSegment StartX=30 StartY=6 StartZ=0 EndX=10 EndY=6 EndZ=0
    g3: LineSegment StartX=10 StartY=6 StartZ=0 EndX=10 EndY=26 EndZ=0
    g4: GeomPoint X=20 Y=6 Z=0
  constraints (12):
    c: Coincident(g0,g1)
    c: Coincident(g1,g2)
    c: Coincident(g2,g3)
    c: Coincident(g3,g0)
    c: Horizontal(g0)
    c: Horizontal(g2)
    c: Vertical(g1)
    c: Vertical(g3)
    c: DistanceX(g0,g0) = 20
    c: Symmetric(g2,g2,g4)
    c: Symmetric(g-3,g-3,g4)
    c: DistanceY(g1,g1) = 20
FEATURE [PartDesign::Pocket] Pocket106
  BaseFeature = -> Fillet107
  Direction = (1,0,0)
  Length = 2
  Length2 = 5
  Profile = -> Sketch222
  ReferenceAxis = -> Sketch222 [N_Axis]
  Type = 0
FEATURE [PartDesign::Fillet] Fillet116
  Base = -> Pocket106 [Edge73]
  BaseFeature = -> Pocket106
  Radius = 1
  SupportTransform = false
  UseAllEdges = false
FEATURE [PartDesign::Fillet] Fillet117
  Base = -> Fillet116 [Edge34]
  BaseFeature = -> Fillet116
  Radius = 0.5
  SupportTransform = false
  UseAllEdges = false
FEATURE [PartDesign::Fillet] Fillet118
  Base = -> Fillet117 [Face35]
  BaseFeature = -> Fillet117
  Radius = 0.4
  SupportTransform = false
  UseAllEdges = false
FEATURE [PartDesign::Fillet] Fillet119
  Base = -> Fillet118 [Face9]
  BaseFeature = -> Fillet118
  Radius = 1
  SupportTransform = false
  UseAllEdges = false
FEATURE [PartDesign::Body] Body026005
  Group = -> [Sketch210,Pad106,Sketch211,Pad107,Fillet103,Fillet104,Sketch212,Pocket098,Sketch213,Pocket099,Sketch214,Pocket100,Sketch215,Pocket101,Fillet105,Chamfer012,Fillet106,Fillet107,Sketch222,Pocket106,Fillet116,Fillet117,Fillet118,Fillet119]
  Origin = -> Origin039
  Tip = -> Fillet119
FEATURE [Part::FeaturePython] Parts035  # WARN: FeaturePython — macro-defined, semantics opaque (R4)
  Group = -> [Body026005]
  GroupMode = 0
FEATURE [Part::Feature] Assembly035001  label="assy-divider_mid_bottom_bracket001"
  Placement = pos=(207,-548.98,20) rot=(0,0,1;0rad)
  shape: bbox 21.48 x 41.48 x 21.49 mm, 81 faces (baked)
FEATURE [App::FeaturePython] Constraints037  # WARN: FeaturePython — macro-defined, semantics opaque (R4)
  _Version = 1
FEATURE [Part::FeaturePython] Parts037  # WARN: FeaturePython — macro-defined, semantics opaque (R4)
  Group = -> [Assembly035001]
  GroupMode = 0
FEATURE [App::FeaturePython] Constraints038  # WARN: FeaturePython — macro-defined, semantics opaque (R4)
  _Version = 1
FEATURE [Part::Feature] Body026005001
  shape: bbox 21.48 x 41.48 x 21.49 mm, 81 faces (baked)
FEATURE [Part::FeaturePython] Parts038  # WARN: FeaturePython — macro-defined, semantics opaque (R4)
  Group = -> [Body026005001]
  GroupMode = 0
FEATURE [Sketcher::SketchObject] Sketch223
  ExternalGeometry = -> [Fillet013]
  FullyConstrained = true
  MapMode = 5
  Placement = pos=(17.5,3e-15,4.9e-15) rot=(0.57735,0.57735,-0.57735;4.18879rad)
  Support = -> [Fillet013]
  sketch-geometry (4):
    g0: LineSegment StartX=-5 StartY=-46.5 StartZ=0 EndX=-5 EndY=-52.5 EndZ=0
    g1: LineSegment StartX=-5 StartY=-52.5 StartZ=0 EndX=4.24533 EndY=-52.5 EndZ=0
    g2: LineSegment StartX=4.24533 StartY=-52.5 StartZ=0 EndX=8.44658 EndY=-46.5 EndZ=0
    g3: LineSegment StartX=8.44658 StartY=-46.5 StartZ=0 EndX=-5 EndY=-46.5 EndZ=0
  constraints (8):
    c: Coincident(g0,g-3)
    c: Coincident(g0,g-4)
    c: Coincident(g1,g0)
    c: Coincident(g1,g-4)
    c: Coincident(g2,g1)
    c: Coincident(g2,g-3)
    c: Coincident(g3,g2)
    c: Coincident(g3,g0)
FEATURE [PartDesign::Pad] Pad110  label="Pad110-servo_mount_fill_top"
  BaseFeature = -> Fillet013
  Direction = (-1,-2e-16,-7e-16)
  Length = 15
  Length2 = 10
  Placement = pos=(0,0,0) rot=(0.57735,0.57735,0.57735;2.0944rad)
  Profile = -> Sketch223
  ReferenceAxis = -> Sketch223 [N_Axis]
  Type = 0
FEATURE [Sketcher::SketchObject] Sketch224
  ExternalGeometry = -> [Pad110]
  FullyConstrained = true
  MapMode = 5
  Placement = pos=(-6e-15,-9,1e-15) rot=(-0.57735,-0.57735,0.57735;4.18879rad)
  Support = -> [Pad110]
  sketch-geometry (20):
    g0: LineSegment StartX=-50.773 StartY=16.975 StartZ=0 EndX=-51.971 EndY=14.9 EndZ=0
    g1: LineSegment StartX=-51.971 StartY=14.9 StartZ=0 EndX=-50.773 EndY=12.825 EndZ=0
    g2: LineSegment StartX=-50.773 StartY=12.825 StartZ=0 EndX=-48.377 EndY=12.825 EndZ=0
    g3: LineSegment StartX=-48.377 StartY=12.825 StartZ=0 EndX=-47.179 EndY=14.9 EndZ=0
    g4: LineSegment StartX=-47.179 StartY=14.9 StartZ=0 EndX=-48.377 EndY=16.975 EndZ=0
    g5: LineSegment StartX=-48.377 StartY=16.975 StartZ=0 EndX=-50.773 EndY=16.975 EndZ=0
    g6: Circle CenterX=-49.575 CenterY=14.9 CenterZ=0 NormalX=0 NormalY=0 NormalZ=1 AngleXU=0 Radius=2.396
    g7: LineSegment StartX=-51.971 StartY=5.1 StartZ=0 EndX=-50.773 EndY=3.025 EndZ=0
    g8: LineSegment StartX=-50.773 StartY=3.025 StartZ=0 EndX=-48.377 EndY=3.025 EndZ=0
    g9: LineSegment StartX=-48.377 StartY=3.025 StartZ=0 EndX=-47.179 EndY=5.1 EndZ=0
    g10: LineSegment StartX=-47.179 StartY=5.1 StartZ=0 EndX=-48.377 EndY=7.175 EndZ=0
    g11: LineSegment StartX=-48.377 StartY=7.175 StartZ=0 EndX=-50.773 EndY=7.175 EndZ=0
    g12: LineSegment StartX=-50.773 StartY=7.175 StartZ=0 EndX=-51.971 EndY=5.1 EndZ=0
    g13: Circle CenterX=-49.575 CenterY=5.1 CenterZ=0 NormalX=0 NormalY=0 NormalZ=1 AngleXU=0 Radius=2.396
    g14: LineSegment StartX=-50.773 StartY=7.175 StartZ=0 EndX=-52.5 EndY=7.175 EndZ=0
    g15: LineSegment StartX=-50.773 StartY=3.025 StartZ=0 EndX=-52.5 EndY=3.025 EndZ=0
    g16: LineSegment StartX=-52.5 StartY=3.025 StartZ=0 EndX=-52.5 EndY=7.175 EndZ=0
    g17: LineSegment StartX=-50.773 StartY=16.975 StartZ=0 EndX=-52.5 EndY=16.975 EndZ=0
    g18: LineSegment StartX=-50.773 StartY=12.825 StartZ=0 EndX=-52.5 EndY=12.825 EndZ=0
    g19: LineSegment StartX=-52.5 StartY=12.825 StartZ=0 EndX=-52.5 EndY=16.975 EndZ=0
  constraints (48):
    c: Coincident(g0,g1)
    c: Coincident(g1,g2)
    c: Coincident(g2,g3)
    c: Coincident(g3,g4)
    c: Coincident(g4,g5)
    c: Coincident(g5,g0)
    c: Equal(g0, g1-g5) x5
    c: PointOnObject(g0,g6)
    c: PointOnObject(g1,g6)
    c: PointOnObject(g2,g6)
    c: PointOnObject(g3,g6)
    c: PointOnObject(g4,g6)
    c: PointOnObject(g5,g6)
    c: Coincident(g6,g-3)
    c: Coincident(g7,g8)
    c: Coincident(g8,g9)
    c: Coincident(g9,g10)
    c: Coincident(g10,g11)
    c: Coincident(g11,g12)
    c: Coincident(g12,g7)
    c: Equal(g7, g8-g12) x5
    c: PointOnObject(g7,g13)
    c: PointOnObject(g8,g13)
    c: PointOnObject(g9,g13)
    c: PointOnObject(g10,g13)
    c: PointOnObject(g11,g13)
    c: PointOnObject(g12,g13)
    c: Coincident(g13,g-4)
    c: Coincident(g14,g11)
    c: PointOnObject(g14,g-6)
    c: Horizontal(g14)
    c: Coincident(g15,g7)
    c: PointOnObject(g15,g-6)
    c: Horizontal(g15)
    c: Coincident(g16,g15)
    c: Coincident(g16,g14)
    c: Coincident(g17,g0)
    c: PointOnObject(g17,g-5)
    c: Horizontal(g17)
    c: Coincident(g18,g1)
    c: PointOnObject(g18,g-5)
    c: Horizontal(g18)
    c: Coincident(g19,g18)
    c: Coincident(g19,g17)
    c: Horizontal(g5)
    c: Horizontal(g11)
    c: Equal(g6,g13)
    c: DistanceY(g19,g19) = 4.15
FEATURE [Sketcher::SketchObject] Sketch225
  ExternalGeometry = -> [Pad110]
  FullyConstrained = true
  MapMode = 5
  Placement = pos=(-6e-15,-9,1e-15) rot=(-0.57735,-0.57735,0.57735;4.18879rad)
  Support = -> [Pad110]
  sketch-geometry (2):
    g0: Circle CenterX=-49.575 CenterY=14.9 CenterZ=0 NormalX=0 NormalY=0 NormalZ=1 AngleXU=0 Radius=1.125
    g1: Circle CenterX=-49.575 CenterY=5.1 CenterZ=0 NormalX=0 NormalY=0 NormalZ=1 AngleXU=0 Radius=1.125
  constraints (4):
    c: Coincident(g0,g-3)
    c: Coincident(g1,g-4)
    c: Equal(g0,g-3)
    c: Equal(g1,g-4)
FEATURE [PartDesign::Pocket] Pocket107  label="Pocket107-servo_screw_holes"
  BaseFeature = -> Pad110
  Direction = (8e-16,1,-1e-16)
  Length = 5
  Length2 = 5
  Placement = pos=(0,0,0) rot=(0.57735,0.57735,0.57735;2.0944rad)
  Profile = -> Sketch225
  ReferenceAxis = -> Sketch225 [N_Axis]
  Type = 1
FEATURE [PartDesign::Pocket] Pocket108  label="Pocket108-servo_nut_retainers"
  BaseFeature = -> Pocket107
  Direction = (8e-16,1,-1e-16)
  Length = 7.3
  Length2 = 5
  Placement = pos=(0,0,0) rot=(0.57735,0.57735,0.57735;2.0944rad)
  Profile = -> Sketch224
  ReferenceAxis = -> Sketch224 [N_Axis]
  Type = 0
FEATURE [Sketcher::SketchObject] Sketch226
  ExternalGeometry = -> [Pocket108]
  FullyConstrained = true
  MapMode = 5
  Placement = pos=(17.5,-4.9e-15,4.9e-15) rot=(0.57735,0.57735,-0.57735;4.18879rad)
  Support = -> [Pocket108]
  sketch-geometry (5):
    g0: LineSegment StartX=5 StartY=4.1e-15 StartZ=0 EndX=5 EndY=-3.5 EndZ=0
    g1: LineSegment StartX=5 StartY=-3.5 StartZ=0 EndX=-5 EndY=-3.5 EndZ=0
    g2: LineSegment StartX=-5 StartY=-3.5 StartZ=0 EndX=-5 EndY=2.5 EndZ=0
    g3: LineSegment StartX=-5 StartY=2.5 StartZ=0 EndX=-4.62e-14 EndY=0 EndZ=0
    g4: LineSegment StartX=-4.62e-14 StartY=0 StartZ=0 EndX=5 EndY=4.1e-15 EndZ=0
  constraints (10):
    c: Coincident(g0,g-5)
    c: Coincident(g0,g-5)
    c: Coincident(g1,g0)
    c: Coincident(g1,g-3)
    c: Coincident(g2,g1)
    c: Coincident(g2,g-3)
    c: Coincident(g3,g2)
    c: Coincident(g3,g-4)
    c: Coincident(g4,g3)
    c: Coincident(g4,g0)
FEATURE [PartDesign::Pad] Pad111  label="Pad111-servo_mount_fill_bottom"
  BaseFeature = -> Pocket108
  Direction = (-1,1e-16,-8e-16)
  Length = 15
  Length2 = 10
  Placement = pos=(0,0,0) rot=(0.57735,0.57735,0.57735;2.0944rad)
  Profile = -> Sketch226
  ReferenceAxis = -> Sketch226 [N_Axis]
  Type = 0
FEATURE [Sketcher::SketchObject] Sketch227
  ExternalGeometry = -> [Pad111]
  FullyConstrained = true
  MapMode = 5
  Placement = pos=(-6e-15,-9,1e-15) rot=(-0.57735,-0.57735,0.57735;4.18879rad)
  Support = -> [Pad111]
  sketch-geometry (2):
    g0: Circle CenterX=-1.125 CenterY=14.9 CenterZ=0 NormalX=0 NormalY=0 NormalZ=1 AngleXU=0 Radius=1.125
    g1: Circle CenterX=-1.125 CenterY=5.1 CenterZ=0 NormalX=0 NormalY=0 NormalZ=1 AngleXU=0 Radius=1.125
  constraints (4):
    c: Coincident(g0,g-3)
    c: Coincident(g1,g-4)
    c: Equal(g1,g-4)
    c: Equal(g0,g-3)
FEATURE [PartDesign::Pocket] Pocket109  label="Pocket109-servo_screw_holes_bottom"
  BaseFeature = -> Pad111
  Direction = (1.1e-15,1,-2e-16)
  Length = 15
  Length2 = 5
  Placement = pos=(0,0,0) rot=(0.57735,0.57735,0.57735;2.0944rad)
  Profile = -> Sketch227
  ReferenceAxis = -> Sketch227 [N_Axis]
  Type = 0
FEATURE [Sketcher::SketchObject] Sketch228
  ExternalGeometry = -> [Pocket109]
  FullyConstrained = true
  MapMode = 5
  Placement = pos=(-6e-15,-9,1e-15) rot=(-0.57735,-0.57735,0.57735;4.18879rad)
  Support = -> [Pocket109]
  sketch-geometry (20):
    g0: LineSegment StartX=0.0730018 StartY=16.975 StartZ=0 EndX=-2.323 EndY=16.975 EndZ=0
    g1: LineSegment StartX=-2.323 StartY=16.975 StartZ=0 EndX=-3.521 EndY=14.9 EndZ=0
    g2: LineSegment StartX=-3.521 StartY=14.9 StartZ=0 EndX=-2.323 EndY=12.825 EndZ=0
    g3: LineSegment StartX=-2.323 StartY=12.825 StartZ=0 EndX=0.0730018 EndY=12.825 EndZ=0
    g4: LineSegment StartX=0.0730018 StartY=12.825 StartZ=0 EndX=1.271 EndY=14.9 EndZ=0
    g5: LineSegment StartX=1.271 StartY=14.9 StartZ=0 EndX=0.0730018 EndY=16.975 EndZ=0
    g6: Circle CenterX=-1.125 CenterY=14.9 CenterZ=0 NormalX=0 NormalY=0 NormalZ=1 AngleXU=0 Radius=2.396
    g7: LineSegment StartX=0.0730018 StartY=7.175 StartZ=0 EndX=-2.323 EndY=7.175 EndZ=0
    g8: LineSegment StartX=-2.323 StartY=7.175 StartZ=0 EndX=-3.521 EndY=5.1 EndZ=0
    g9: LineSegment StartX=-3.521 StartY=5.1 StartZ=0 EndX=-2.323 EndY=3.025 EndZ=0
    g10: LineSegment StartX=-2.323 StartY=3.025 StartZ=0 EndX=0.0730018 EndY=3.025 EndZ=0
    g11: LineSegment StartX=0.0730018 StartY=3.025 StartZ=0 EndX=1.271 EndY=5.1 EndZ=0
    g12: LineSegment StartX=1.271 StartY=5.1 StartZ=0 EndX=0.0730018 EndY=7.175 EndZ=0
    g13: Circle CenterX=-1.125 CenterY=5.1 CenterZ=0 NormalX=0 NormalY=0 NormalZ=1 AngleXU=0 Radius=2.396
    g14: LineSegment StartX=0.0730018 StartY=16.975 StartZ=0 EndX=2.5 EndY=16.975 EndZ=0
    g15: LineSegment StartX=0.0730018 StartY=12.825 StartZ=0 EndX=2.5 EndY=12.825 EndZ=0
    g16: LineSegment StartX=2.5 StartY=12.825 StartZ=0 EndX=2.5 EndY=16.975 EndZ=0
    g17: LineSegment StartX=0.0730018 StartY=7.175 StartZ=0 EndX=2.5 EndY=7.175 EndZ=0
    g18: LineSegment StartX=0.0730018 StartY=3.025 StartZ=0 EndX=2.5 EndY=3.025 EndZ=0
    g19: LineSegment StartX=2.5 StartY=3.025 StartZ=0 EndX=2.5 EndY=7.175 EndZ=0
  constraints (48):
    c: Coincident(g0,g1)
    c: Coincident(g1,g2)
    c: Coincident(g2,g3)
    c: Coincident(g3,g4)
    c: Coincident(g4,g5)
    c: Coincident(g5,g0)
    c: Equal(g0, g1-g5) x5
    c: PointOnObject(g0,g6)
    c: PointOnObject(g1,g6)
    c: PointOnObject(g2,g6)
    c: PointOnObject(g3,g6)
    c: PointOnObject(g4,g6)
    c: PointOnObject(g5,g6)
    c: Coincident(g6,g-3)
    c: Coincident(g7,g8)
    c: Coincident(g8,g9)
    c: Coincident(g9,g10)
    c: Coincident(g10,g11)
    c: Coincident(g11,g12)
    c: Coincident(g12,g7)
    c: Equal(g7, g8-g12) x5
    c: PointOnObject(g7,g13)
    c: PointOnObject(g8,g13)
    c: PointOnObject(g9,g13)
    c: PointOnObject(g10,g13)
    c: PointOnObject(g11,g13)
    c: PointOnObject(g12,g13)
    c: Coincident(g13,g-4)
    c: Coincident(g14,g0)
    c: PointOnObject(g14,g-6)
    c: Horizontal(g14)
    c: Coincident(g15,g3)
    c: PointOnObject(g15,g-6)
    c: Horizontal(g15)
    c: Coincident(g16,g15)
    c: Coincident(g16,g14)
    c: Coincident(g17,g7)
    c: PointOnObject(g17,g-5)
    c: Horizontal(g17)
    c: Coincident(g18,g10)
    c: PointOnObject(g18,g-5)
    c: Horizontal(g18)
    c: Coincident(g19,g18)
    c: Coincident(g19,g17)
    c: Equal(g6,g13)
    c: Horizontal(g0)
    c: Horizontal(g7)
    c: DistanceY(g19,g19) = 4.15
FEATURE [PartDesign::Pocket] Pocket110
  BaseFeature = -> Pocket109
  Direction = (1.1e-15,1,-2e-16)
  Length = 7.3
  Length2 = 5
  Placement = pos=(0,0,0) rot=(0.57735,0.57735,0.57735;2.0944rad)
  Profile = -> Sketch228
  ReferenceAxis = -> Sketch228 [N_Axis]
  Type = 0
FEATURE [Sketcher::SketchObject] Sketch229
  ExternalGeometry = -> [Pocket110]
  FullyConstrained = true
  MapMode = 5
  Placement = pos=(-6e-15,-9,1e-15) rot=(-0.57735,-0.57735,0.57735;4.18879rad)
  Support = -> [Pocket110]
  sketch-geometry (20):
    g0: LineSegment StartX=-4.35 StartY=20 StartZ=0 EndX=2.5 EndY=20 EndZ=0
    g1: LineSegment StartX=2.5 StartY=20 StartZ=0 EndX=2.5 EndY=11 EndZ=0
    g2: LineSegment StartX=2.5 StartY=11 StartZ=0 EndX=-4.35 EndY=11 EndZ=0
    g3: LineSegment StartX=-4.35 StartY=11 StartZ=0 EndX=-4.35 EndY=20 EndZ=0
    g4: LineSegment StartX=2.5 StartY=9 StartZ=0 EndX=-4.35 EndY=9 EndZ=0
    g5: LineSegment StartX=-4.35 StartY=9 StartZ=0 EndX=-4.35 EndY=0 EndZ=0
    g6: LineSegment StartX=-4.35 StartY=0 StartZ=0 EndX=2.5 EndY=0 EndZ=0
    g7: LineSegment StartX=2.5 StartY=0 StartZ=0 EndX=2.5 EndY=9 EndZ=0
    g8: LineSegment StartX=-46.35 StartY=0 StartZ=0 EndX=-52.5 EndY=0 EndZ=0
    g9: LineSegment StartX=-52.5 StartY=0 StartZ=0 EndX=-52.5 EndY=9 EndZ=0
    g10: LineSegment StartX=-52.5 StartY=9 StartZ=0 EndX=-46.35 EndY=9 EndZ=0
    g11: LineSegment StartX=-46.35 StartY=9 StartZ=0 EndX=-46.35 EndY=0 EndZ=0
    g12: LineSegment StartX=-52.5 StartY=11 StartZ=0 EndX=-46.35 EndY=11 EndZ=0
    g13: LineSegment StartX=-46.35 StartY=11 StartZ=0 EndX=-46.35 EndY=20 EndZ=0
    g14: LineSegment StartX=-46.35 StartY=20 StartZ=0 EndX=-52.5 EndY=20 EndZ=0
    g15: LineSegment StartX=-52.5 StartY=20 StartZ=0 EndX=-52.5 EndY=11 EndZ=0
    g16: Circle CenterX=-49.575 CenterY=14.9 CenterZ=0 NormalX=0 NormalY=0 NormalZ=1 AngleXU=0 Radius=1.125
    g17: Circle CenterX=-49.575 CenterY=5.1 CenterZ=0 NormalX=0 NormalY=0 NormalZ=1 AngleXU=0 Radius=1.125
    g18: Circle CenterX=-1.125 CenterY=5.1 CenterZ=0 NormalX=0 NormalY=0 NormalZ=1 AngleXU=0 Radius=1.125
    g19: Circle CenterX=-1.125 CenterY=14.9 CenterZ=0 NormalX=0 NormalY=0 NormalZ=1 AngleXU=0 Radius=1.125
  constraints (48):
    c: Coincident(g0,g1)
    c: Coincident(g1,g2)
    c: Coincident(g2,g3)
    c: Coincident(g3,g0)
    c: Horizontal(g0)
    c: Horizontal(g2)
    c: Vertical(g1)
    c: Vertical(g3)
    c: Coincident(g0,g-4)
    c: Coincident(g1,g-3)
    c: Coincident(g4,g5)
    c: Coincident(g5,g6)
    c: Coincident(g6,g7)
    c: Coincident(g7,g4)
    c: Horizontal(g4)
    c: Horizontal(g6)
    c: Vertical(g5)
    c: Vertical(g7)
    c: Coincident(g4,g-5)
    c: Coincident(g5,g-6)
    c: Coincident(g8,g9)
    c: Coincident(g9,g10)
    c: Coincident(g10,g11)
    c: Coincident(g11,g8)
    c: Horizontal(g8)
    c: Horizontal(g10)
    c: Vertical(g9)
    c: Vertical(g11)
    c: Coincident(g8,g-7)
    c: Coincident(g9,g-8)
    c: Coincident(g12,g13)
    c: Coincident(g13,g14)
    c: Coincident(g14,g15)
    c: Coincident(g15,g12)
    c: Horizontal(g12)
    c: Horizontal(g14)
    c: Vertical(g13)
    c: Vertical(g15)
    c: Coincident(g12,g-9)
    c: Coincident(g13,g-10)
    c: Coincident(g16,g-11)
    c: Coincident(g17,g-12)
    c: Coincident(g18,g-13)
    c: Coincident(g19,g-14)
    c: Equal(g19,g-14)
    c: Equal(g-14,g18)
    c: Equal(g18,g17)
    c: Equal(g17,g16)
FEATURE [PartDesign::Pad] Pad112
  BaseFeature = -> Pocket110
  Direction = (-1.2e-15,-1,1e-16)
  Length = 4
  Length2 = 10
  Placement = pos=(0,0,0) rot=(0.57735,0.57735,0.57735;2.0944rad)
  Profile = -> Sketch229
  ReferenceAxis = -> Sketch229 [N_Axis]
  Reversed = true
  Type = 0
FEATURE [PartDesign::Fillet] Fillet120  label="Fillet120-servo_screws"
  Base = -> Pad112 [Edge496,Edge585,Edge593,Edge516,Edge634,Edge617,Edge654,Edge664]
  BaseFeature = -> Pad112
  Placement = pos=(0,0,0) rot=(0.57735,0.57735,0.57735;2.0944rad)
  Radius = 0.3
  SupportTransform = false
  UseAllEdges = false
FEATURE [PartDesign::Fillet] Fillet121  label="Fillet121-servo_mount_inside"
  Base = -> Fillet120 [Edge246,Edge262]
  BaseFeature = -> Fillet120
  Placement = pos=(0,0,0) rot=(0.57735,0.57735,0.57735;2.0944rad)
  Radius = 1
  SupportTransform = false
  UseAllEdges = false
FEATURE [Sketcher::SketchObject] Sketch230
  ExternalGeometry = -> [Fillet121]
  FullyConstrained = true
  MapMode = 5
  Placement = pos=(-2.8e-15,-5.1e-15,46.35) rot=(0.707107,0.707107,0;3.14159rad)
  Support = -> [Fillet121]
  sketch-geometry (3):
    g0: LineSegment StartX=-9 StartY=20 StartZ=0 EndX=0 EndY=20 EndZ=0
    g1: LineSegment StartX=0 StartY=20 StartZ=0 EndX=0 EndY=25 EndZ=0
    g2: LineSegment StartX=0 StartY=25 StartZ=0 EndX=-9 EndY=20 EndZ=0
  constraints (9):
    c: PointOnObject(g0,g-3)
    c: PointOnObject(g0,g-2)
    c: Horizontal(g0)
    c: Coincident(g1,g0)
    c: PointOnObject(g1,g-2)
    c: Coincident(g2,g1)
    c: Coincident(g2,g0)
    c: DistanceY(g1,g1) = 5
    c: DistanceX(g0,g0) = 9
FEATURE [PartDesign::Pad] Pad113  label="Pad113-top_cantilever"
  BaseFeature = -> Fillet121
  Direction = (1e-16,-6e-16,-1)
  Length = 4
  Length2 = 10
  Placement = pos=(0,0,0) rot=(0.57735,0.57735,0.57735;2.0944rad)
  Profile = -> Sketch230
  ReferenceAxis = -> Sketch230 [N_Axis]
  Reversed = true
  Type = 0
FEATURE [Sketcher::SketchObject] Sketch231
  ExternalGeometry = -> [Pad113]
  FullyConstrained = true
  MapMode = 5
  Placement = pos=(-3e-16,-5e-16,4.35) rot=(0,0,-1;1.5708rad)
  Support = -> [Pad113]
  sketch-geometry (3):
    g0: LineSegment StartX=9 StartY=20 StartZ=0 EndX=0 EndY=20 EndZ=0
    g1: LineSegment StartX=0 StartY=20 StartZ=0 EndX=0 EndY=25 EndZ=0
    g2: LineSegment StartX=0 StartY=25 StartZ=0 EndX=9 EndY=20 EndZ=0
  constraints (9):
    c: PointOnObject(g0,g-3)
    c: PointOnObject(g0,g-2)
    c: Horizontal(g0)
    c: Coincident(g1,g0)
    c: PointOnObject(g1,g-2)
    c: Coincident(g2,g1)
    c: Coincident(g2,g0)
    c: DistanceY(g1,g1) = 5
    c: DistanceX(g0,g0) = 9
FEATURE [PartDesign::Pad] Pad114  label="Pad114-bottom_cantilever"
  BaseFeature = -> Pad113
  Direction = (-1e-16,7e-16,1)
  Length = 3.5
  Length2 = 10
  Placement = pos=(0,0,0) rot=(0.57735,0.57735,0.57735;2.0944rad)
  Profile = -> Sketch231
  ReferenceAxis = -> Sketch231 [N_Axis]
  Reversed = true
  Type = 0
FEATURE [Sketcher::SketchObject] Sketch232
  ExternalGeometry = -> [Pad114]
  FullyConstrained = true
  MapMode = 5
  Placement = pos=(8.8e-15,20,-4.4e-15) rot=(0.57735,0.57735,0.57735;4.18879rad)
  Support = -> [Pad114]
  sketch-geometry (7):
    g0: LineSegment StartX=8 StartY=25 StartZ=0 EndX=8 EndY=165.375 EndZ=0
    g1: LineSegment StartX=8 StartY=165.375 StartZ=0 EndX=59.0924 EndY=25 EndZ=0
    g2: LineSegment StartX=59.0924 StartY=25 StartZ=0 EndX=8 EndY=25 EndZ=0
    g3: GeomPoint X=44.7061 Y=64.5261 Z=0
    g4: GeomPoint X=19.8904 Y=132.707 Z=0
    g5: GeomPoint X=8 Y=63.5 Z=0
    g6: GeomPoint X=32.904 Y=25 Z=0
  constraints (13):
    c: Vertical(g0)
    c: Coincident(g1,g0)
    c: Coincident(g2,g1)
    c: Coincident(g2,g0)
    c: Horizontal(g2)
    c: PointOnObject(g3,g1)
    c: Symmetric(g-3,g-3,g3)
    c: PointOnObject(g4,g1)
    c: PointOnObject(g5,g0)
    c: PointOnObject(g6,g2)
    c: Symmetric(g-4,g-4,g6)
    c: Symmetric(g-5,g-5,g5)
    c: Symmetric(g-7,g-7,g4)
FEATURE [PartDesign::Pad] Pad115
  BaseFeature = -> Pad114
  Direction = (1.2e-15,1,-1e-16)
  Length = 2
  Length2 = 10
  Placement = pos=(0,0,0) rot=(0.57735,0.57735,0.57735;2.0944rad)
  Profile = -> Sketch232
  ReferenceAxis = -> Sketch232 [N_Axis]
  Reversed = true
  Type = 0
FEATURE [PartDesign::Fillet] Fillet122
  Base = -> Pad115 [Edge561,Edge567,Edge568,Edge564,Edge691,Edge690,Edge689,Edge688,Edge573,Edge574,Edge556,Edge557,Edge554,Edge555,Edge576,Edge575]
  BaseFeature = -> Pad115
  Placement = pos=(0,0,0) rot=(0.57735,0.57735,0.57735;2.0944rad)
  Radius = 0.15
  SupportTransform = false
  UseAllEdges = false
FEATURE [PartDesign::Fillet] Fillet123
  Base = -> Fillet122 [Edge24,Edge5]
  BaseFeature = -> Fillet122
  Placement = pos=(0,0,0) rot=(0.57735,0.57735,0.57735;2.0944rad)
  Radius = 1
  SupportTransform = false
  UseAllEdges = false
FEATURE [PartDesign::Fillet] Fillet124
  Base = -> Fillet123 [Edge802,Edge801,Edge800,Edge817,Edge816,Edge815,Edge814,Edge799,Edge836,Edge837,Edge828,Edge829,Edge827,Edge826,Edge835,Edge834]
  BaseFeature = -> Fillet123
  Placement = pos=(0,0,0) rot=(0.57735,0.57735,0.57735;2.0944rad)
  Radius = 0.15
  SupportTransform = false
  UseAllEdges = false
FEATURE [Sketcher::SketchObject] Sketch233
  ExternalGeometry = -> [Pocket061]
  FullyConstrained = true
  MapMode = 5
  Placement = pos=(-13.5,0,0) rot=(0.57735,-0.57735,-0.57735;2.0944rad)
  Support = -> [Pocket061]
  sketch-geometry (1):
    g0: Circle CenterX=195.5 CenterY=6 CenterZ=0 NormalX=0 NormalY=0 NormalZ=1 AngleXU=0 Radius=5
  constraints (3):
    c: DistanceX(g0,g-3) = 7
    c: DistanceY(g-3,g0) = 6
    c: Diameter(g0) = 10
FEATURE [PartDesign::Pocket] Pocket111  label="Pocket111-kibble_drain_hole"
  BaseFeature = -> Pocket061
  Direction = (1,0,0)
  Length = 6
  Length2 = 5
  Profile = -> Sketch233
  ReferenceAxis = -> Sketch233 [N_Axis]
  Type = 0
FEATURE [PartDesign::Chamfer] Chamfer014  label="Chamfer014-kibble_drain_hole"
  Angle = 45
  Base = -> Pocket111 [Edge400]
  BaseFeature = -> Pocket111
  ChamferType = 0
  FlipDirection = false
  Size = 2.5
  Size2 = 1
  SupportTransform = false
  UseAllEdges = false
FEATURE [PartDesign::Mirrored] Mirrored007  label="Mirrored007-kibble_drain_hole_R"
  BaseFeature = -> Chamfer014
  MirrorPlane = -> YZ_Plane016
  Originals = -> [Pocket111]
FEATURE [PartDesign::Chamfer] Chamfer015  label="Chamfer015-kibble_drain_hole_R"
  Angle = 45
  Base = -> Mirrored007 [Edge527]
  BaseFeature = -> Mirrored007
  ChamferType = 0
  FlipDirection = false
  Size = 2.5
  Size2 = 1
  SupportTransform = false
  UseAllEdges = false
FEATURE [Sketcher::SketchObject] Sketch234
  ExternalGeometry = -> [Chamfer014]
  FullyConstrained = true
  MapMode = 5
  Placement = pos=(-11,0,0) rot=(0.57735,-0.57735,-0.57735;2.0944rad)
  Support = -> [Chamfer014]
  sketch-geometry (8):
    g0: LineSegment StartX=25 StartY=8 StartZ=0 EndX=25 EndY=59.0924 EndZ=0
    g1: LineSegment StartX=25 StartY=59.0924 StartZ=0 EndX=102 EndY=31.0667 EndZ=0
    g2: LineSegment StartX=102 StartY=31.0667 StartZ=0 EndX=102 EndY=8 EndZ=0
    g3: LineSegment StartX=102 StartY=8 StartZ=0 EndX=25 EndY=8 EndZ=0
    g4: GeomPoint X=63.5326 Y=45.0677 Z=0
    g5: GeomPoint X=63.5 Y=8 Z=0
    g6: GeomPoint X=25 Y=32.761 Z=0
    g7: GeomPoint X=102 Y=18.7828 Z=0
  constraints (16):
    c: Coincident(g1,g0)
    c: Coincident(g2,g1)
    c: Coincident(g3,g2)
    c: Coincident(g3,g0)
    c: Horizontal(g3)
    c: PointOnObject(g4,g1)
    c: PointOnObject(g5,g3)
    c: PointOnObject(g6,g0)
    c: PointOnObject(g7,g2)
    c: Vertical(g2)
    c: Vertical(g0)
    c: Parallel(g1,g-6)
    c: Symmetric(g-6,g-6,g4)
    c: Symmetric(g-5,g-5,g7)
    c: Symmetric(g-4,g-4,g5)
    c: Symmetric(g-3,g-3,g6)
FEATURE [PartDesign::Pad] Pad116  label="Pad116-divider"
  BaseFeature = -> Chamfer015
  Direction = (-1,0,0)
  Length = 2
  Length2 = 10
  Profile = -> Sketch234
  ReferenceAxis = -> Sketch234 [N_Axis]
  Reversed = true
  Type = 0
FEATURE [Sketcher::SketchObject] Sketch235
  ExternalGeometry = -> [Pad116]
  FullyConstrained = true
  MapMode = 5
  Placement = pos=(-1,0,0) rot=(0.57735,-0.57735,-0.57735;2.0944rad)
  Support = -> [Pad116]
  sketch-geometry (4):
    g0: LineSegment StartX=83.2061 StartY=62.3832 StartZ=0 EndX=121.632 EndY=48.3974 EndZ=0
    g1: LineSegment StartX=83.2061 StartY=45.3564 StartZ=0 EndX=121.632 EndY=31.3705 EndZ=0
    g2: LineSegment StartX=121.632 StartY=31.3705 StartZ=0 EndX=121.632 EndY=48.3974 EndZ=0
    g3: LineSegment StartX=83.2061 StartY=62.3832 StartZ=0 EndX=83.2061 EndY=45.3564 EndZ=0
  constraints (12):
    c: PointOnObject(g0,g-5)
    c: PointOnObject(g0,g-6)
    c: PointOnObject(g1,g-4)
    c: PointOnObject(g1,g-3)
    c: Coincident(g2,g1)
    c: Coincident(g2,g0)
    c: Coincident(g3,g0)
    c: Coincident(g3,g1)
    c: Vertical(g2)
    c: Vertical(g3)
    c: Distance(g-3,g1) = 10.25
    c: Distance(g1,g-4) = 20
FEATURE [PartDesign::Pad] Pad117  label="Pad117-mid_support_extension"
  BaseFeature = -> Pad116
  Direction = (-1,0,0)
  Length = 2
  Length2 = 10
  Profile = -> Sketch235
  ReferenceAxis = -> Sketch235 [N_Axis]
  Reversed = true
  Type = 0
FEATURE [PartDesign::Fillet] Fillet125  label="Fillet125-mid-support"
  Base = -> Pad117 [Edge250,Edge216]
  BaseFeature = -> Pad117
  Radius = 3
  SupportTransform = false
  UseAllEdges = false
FEATURE [PartDesign::Body] Body017  label="Body-slide_mid_v3"
  Group = -> [Sketch077,Pad030,Sketch078,Sketch079,Pad031,Sketch080,Pocket039,Mirrored001,Sketch081,Pocket040,Sketch083,Pad033,Sketch085,Pocket043,Mirrored003,Sketch094,Pocket044,Mirrored004,Sketch095,Pad039,Mirrored005,Fillet021,Sketch098,Sketch100,Fillet022,Fillet023,Fillet024,Fillet025,Fillet026,Fillet027,Fillet028,Fillet029,Fillet030,Fillet031,Fillet032,Fillet033,Fillet034,Pocket051,Pocket052,Sketch101,+13 more]
  Origin = -> Origin016
  Tip = -> Fillet125
FEATURE [Part::FeaturePython] Parts012  # WARN: FeaturePython — macro-defined, semantics opaque (R4)
  Group = -> [Body017,Body018,Body020,Body021]
  GroupMode = 0
FEATURE [Part::FeaturePython] Slice010  # WARN: FeaturePython — macro-defined, semantics opaque (R4)
  Base = -> Body017
  Mode = 1
  Tolerance = 0
  Tools = -> [Body021]
FEATURE [Part::FeaturePython] Slice011  # WARN: FeaturePython — macro-defined, semantics opaque (R4)
  Base = -> Body017
  Mode = 1
  Tolerance = 0
  Tools = -> [Body021]
FEATURE [Part::FeaturePython] Slice011_child0  label="Slice011.0"  # WARN: FeaturePython — macro-defined, semantics opaque (R4)
  Base = -> Slice011
  FilterType = 1
  Invert = false
  OverrideMaxVal = 0
  WindowFrom = 80
  WindowTo = 100
  items = 0
FEATURE [Part::FeaturePython] Slice011_child1  label="Slice011.1"  # WARN: FeaturePython — macro-defined, semantics opaque (R4)
  Base = -> Slice011
  FilterType = 1
  Invert = false
  OverrideMaxVal = 0
  WindowFrom = 80
  WindowTo = 100
  items = 1
FEATURE [App::DocumentObjectGroup] GrExplode_Slice011  label="Exploded Slice-mid_slide-v2"
  Group = -> [Slice011_child0,Slice011_child1]
FEATURE [Part::FeaturePython] Slice014  # WARN: FeaturePython — macro-defined, semantics opaque (R4)
  Base = -> Body017
  Mode = 1
  Tolerance = 0
  Tools = -> [Body021]
FEATURE [Part::FeaturePython] Slice016  # WARN: FeaturePython — macro-defined, semantics opaque (R4)
  Base = -> Fillet125
  Mode = 1
  Tolerance = 0
  Tools = -> [Body021]
FEATURE [Part::FeaturePython] Slice016_child0  label="Slice016.0-mid_slide_v3_rear"  # WARN: FeaturePython — macro-defined, semantics opaque (R4)
  Base = -> Slice016
  FilterType = 1
  Invert = false
  OverrideMaxVal = 0
  WindowFrom = 80
  WindowTo = 100
  items = 0
FEATURE [Part::FeaturePython] Slice016_child1  label="Slice016.1-mid_slide_v3_front"  # WARN: FeaturePython — macro-defined, semantics opaque (R4)
  Base = -> Slice016
  FilterType = 1
  Invert = false
  OverrideMaxVal = 0
  WindowFrom = 80
  WindowTo = 100
  items = 1
FEATURE [App::DocumentObjectGroup] GrExplode_Slice016  label="Exploded Slice016-mid_slide_v3"
  Group = -> [Slice016_child0,Slice016_child1]
FEATURE [Part::FeaturePython] Slice014_child0  label="Slice014.0"  # WARN: FeaturePython — macro-defined, semantics opaque (R4)
  Base = -> Slice014
  FilterType = 1
  Invert = false
  OverrideMaxVal = 0
  WindowFrom = 80
  WindowTo = 100
  items = 0
FEATURE [Part::FeaturePython] Slice014_child1  label="Slice014.1"  # WARN: FeaturePython — macro-defined, semantics opaque (R4)
  Base = -> Slice014
  FilterType = 1
  Invert = false
  OverrideMaxVal = 0
  WindowFrom = 80
  WindowTo = 100
  items = 1
FEATURE [App::DocumentObjectGroup] GrExplode_Slice014  label="Exploded Slice014-mid_slide_v3"
  Group = -> [Slice014_child0,Slice014_child1]
FEATURE [Part::FeaturePython] Slice017  # WARN: FeaturePython — macro-defined, semantics opaque (R4)
  Base = -> Body017
  Mode = 1
  Tolerance = 0
  Tools = -> [Body021]
FEATURE [Part::FeaturePython] Slice017_child0  label="Slice017.0"  # WARN: FeaturePython — macro-defined, semantics opaque (R4)
  Base = -> Slice017
  FilterType = 1
  Invert = false
  OverrideMaxVal = 0
  WindowFrom = 80
  WindowTo = 100
  items = 0
FEATURE [Part::FeaturePython] Slice017_child1  label="Slice017.1"  # WARN: FeaturePython — macro-defined, semantics opaque (R4)
  Base = -> Slice017
  FilterType = 1
  Invert = false
  OverrideMaxVal = 0
  WindowFrom = 80
  WindowTo = 100
  items = 1
FEATURE [App::DocumentObjectGroup] GrExplode_Slice017  label="Exploded Slice017-mid_slide_v3"
  Group = -> [Slice017_child0,Slice017_child1]
FEATURE [Sketcher::SketchObject] Sketch236
  ExternalGeometry = -> [Fillet124]
  FullyConstrained = true
  MapMode = 5
  Placement = pos=(1.78e-14,20,-2.2e-15) rot=(0.57735,0.57735,0.57735;4.18879rad)
  Support = -> [Fillet124]
  sketch-geometry (5):
    g0: LineSegment StartX=29.7178 StartY=193.42 StartZ=0 EndX=64.7178 EndY=193.42 EndZ=0
    g1: LineSegment StartX=64.7178 StartY=193.42 StartZ=0 EndX=127.838 EndY=20 EndZ=0
    g2: LineSegment StartX=78.5561 StartY=20 StartZ=0 EndX=127.838 EndY=20 EndZ=0
    g3: LineSegment StartX=87.9531 StartY=33.4202 StartZ=0 EndX=29.7178 EndY=193.42 EndZ=0
    g4: LineSegment StartX=87.9531 StartY=33.4202 StartZ=0 EndX=78.5561 EndY=20 EndZ=0
  constraints (12):
    c: Horizontal(g0)
    c: Coincident(g1,g0)
    c: DistanceX(g0,g0) = 35
    c: Coincident(g2,g1)
    c: Horizontal(g2)
    c: Coincident(g3,g0)
    c: Parallel(g1,g-3)
    c: Coincident(g-3,g0)
    c: Coincident(g4,g3)
    c: Coincident(g4,g2)
    c: Coincident(g2,g-4)
    c: Coincident(g-3,g3)
FEATURE [PartDesign::Pad] Pad118  label="Pad118-built-in-divider"
  BaseFeature = -> Fillet124
  Direction = (9e-16,1,0)
  Length = 3
  Length2 = 10
  Placement = pos=(0,0,0) rot=(0.57735,0.57735,0.57735;2.0944rad)
  Profile = -> Sketch236
  ReferenceAxis = -> Sketch236 [N_Axis]
  Reversed = true
  Type = 0
FEATURE [PartDesign::Fillet] Fillet126  label="Fillet126-built-in-divider"
  Base = -> Pad118 [Edge655,Edge653]
  BaseFeature = -> Pad118
  Placement = pos=(0,0,0) rot=(0.57735,0.57735,0.57735;2.0944rad)
  Radius = 10
  SupportTransform = false
  UseAllEdges = false
FEATURE [Sketcher::SketchObject] Sketch237
  ExternalGeometry = -> [Fillet126]
  FullyConstrained = true
  MapMode = 5
  Placement = pos=(20,-1.66e-14,0) rot=(-0.57735,-0.57735,0.57735;2.0944rad)
  Support = -> [Fillet126]
  sketch-geometry (4):
    g0: LineSegment StartX=8 StartY=-60.9123 StartZ=0 EndX=20 EndY=-60.9123 EndZ=0
    g1: LineSegment StartX=20 StartY=-60.9123 StartZ=0 EndX=20 EndY=-78.5561 EndZ=0
    g2: LineSegment StartX=20 StartY=-78.5561 StartZ=0 EndX=8 EndY=-78.5561 EndZ=0
    g3: LineSegment StartX=8 StartY=-78.5561 StartZ=0 EndX=8 EndY=-60.9123 EndZ=0
  constraints (10):
    c: Coincident(g0,g1)
    c: Coincident(g1,g2)
    c: Coincident(g2,g3)
    c: Coincident(g3,g0)
    c: Horizontal(g0)
    c: Horizontal(g2)
    c: Vertical(g1)
    c: Vertical(g3)
    c: Coincident(g0,g-3)
    c: Coincident(g1,g-4)
FEATURE [PartDesign::Pad] Pad119  label="Pad119-close_back_open_bearing_slot"
  BaseFeature = -> Fillet126
  Direction = (-1,7e-16,-2e-16)
  Length = 2
  Length2 = 10
  Placement = pos=(0,0,0) rot=(0.57735,0.57735,0.57735;2.0944rad)
  Profile = -> Sketch237
  ReferenceAxis = -> Sketch237 [N_Axis]
  Type = 0
FEATURE [PartDesign::Chamfer] Chamfer016
  Angle = 45
  Base = -> Pad119 [Edge105,Edge216]
  BaseFeature = -> Pad119
  ChamferType = 0
  FlipDirection = false
  Placement = pos=(0,0,0) rot=(0.57735,0.57735,0.57735;2.0944rad)
  Size = 1.9
  Size2 = 1
  SupportTransform = false
  UseAllEdges = false
FEATURE [Sketcher::SketchObject] Sketch238
  ExternalGeometry = -> [Chamfer016]
  FullyConstrained = true
  MapMode = 5
  Placement = pos=(0,-3e-16,0) rot=(0.57735,0.57735,-0.57735;2.0944rad)
  Support = -> [Chamfer016]
  sketch-geometry (6):
    g0: LineSegment StartX=-22.35 StartY=20 StartZ=0 EndX=-26.35 EndY=20 EndZ=0
    g1: LineSegment StartX=-26.35 StartY=20 StartZ=0 EndX=-26.35 EndY=-2 EndZ=0
    g2: LineSegment StartX=-22.35 StartY=0 StartZ=0 EndX=-22.35 EndY=20 EndZ=0
    g3: LineSegment StartX=-26.35 StartY=-2 StartZ=0 EndX=0 EndY=-2 EndZ=0
    g4: LineSegment StartX=0 StartY=-2 StartZ=0 EndX=0 EndY=0 EndZ=0
    g5: LineSegment StartX=-22.35 StartY=0 StartZ=0 EndX=0 EndY=0 EndZ=0
  constraints (16):
    c: Coincident(g0,g1)
    c: Coincident(g2,g0)
    c: Horizontal(g0)
    c: Vertical(g1)
    c: Vertical(g2)
    c: Coincident(g0,g-3)
    c: DistanceX(g0,g0) = 4
    c: Coincident(g3,g1)
    c: Horizontal(g3)
    c: Coincident(g4,g3)
    c: Vertical(g4)
    c: Coincident(g4,g-1)
    c: DistanceY(g4,g4) = 2
    c: Coincident(g5,g2)
    c: Coincident(g5,g4)
    c: Horizontal(g5)
FEATURE [PartDesign::Pad] Pad120  label="Pad120-servo_hole_reinforcement"
  BaseFeature = -> Chamfer016
  Direction = (-4e-16,-1,-1e-16)
  Length = 20
  Length2 = 10
  Placement = pos=(0,0,0) rot=(0.57735,0.57735,0.57735;2.0944rad)
  Profile = -> Sketch238
  ReferenceAxis = -> Sketch238 [N_Axis]
  Reversed = true
  Type = 0
FEATURE [Sketcher::SketchObject] Sketch239
  ExternalGeometry = -> [Pad120]
  FullyConstrained = true
  MapMode = 5
  Placement = pos=(0,-3e-16,0) rot=(0.57735,0.57735,-0.57735;2.0944rad)
  Support = -> [Pad120]
  sketch-geometry (1):
    g0: Circle CenterX=-15 CenterY=10 CenterZ=0 NormalX=0 NormalY=0 NormalZ=1 AngleXU=0 Radius=8
  constraints (3):
    c: Coincident(g0,g-3)
    c: Diameter(g-3) = 13
    c: Diameter(g0) = 16
FEATURE [PartDesign::Pocket] Pocket112  label="Pocket112-16mm_servo_hole"
  BaseFeature = -> Pad120
  Direction = (4e-16,1,0)
  Length = 5
  Length2 = 5
  Placement = pos=(0,0,0) rot=(0.57735,0.57735,0.57735;2.0944rad)
  Profile = -> Sketch239
  ReferenceAxis = -> Sketch239 [N_Axis]
  Type = 1
FEATURE [Sketcher::SketchObject] Sketch240
  ExternalGeometry = -> [Fillet012]
  FullyConstrained = true
  MapMode = 5
  Placement = pos=(-22,0,0) rot=(0.57735,-0.57735,-0.57735;2.0944rad)
  Support = -> [Fillet012]
  sketch-geometry (2):
    g0: Circle CenterX=-140 CenterY=2.5 CenterZ=0 NormalX=0 NormalY=0 NormalZ=1 AngleXU=0 Radius=7.5
    g1: Circle CenterX=-140 CenterY=2.5 CenterZ=0 NormalX=0 NormalY=0 NormalZ=1 AngleXU=0 Radius=6
  constraints (4):
    c: Coincident(g0,g-3)
    c: Diameter(g0) = 15
    c: Coincident(g1,g0)
    c: Equal(g-3,g1)
FEATURE [PartDesign::Pad] Pad121
  BaseFeature = -> Fillet012
  Direction = (-1,0,0)
  Length = 40
  Length2 = 10
  Profile = -> Sketch240
  ReferenceAxis = -> Sketch240 [N_Axis]
  Reversed = true
  Type = 0
FEATURE [PartDesign::Fillet] Fillet127
  Base = -> Pad121 [Edge27]
  BaseFeature = -> Pad121
  Radius = 1.4
  SupportTransform = false
  UseAllEdges = false
FEATURE [PartDesign::Fillet] Fillet128
  Base = -> Fillet127 [Edge1,Edge8]
  BaseFeature = -> Fillet127
  Radius = 1
  SupportTransform = false
  UseAllEdges = false
FEATURE [PartDesign::Body] Body001  label="Door-back-Body"
  Group = -> [Sketch001,Pad001,Sketch002,Pad002,Sketch014,Pad008,Sketch015,Pocket004,Sketch028,Pocket011,PolarPattern,Fillet,Chamfer,Sketch067,Pad025,Sketch068,Pocket034,PolarPattern001,Sketch075,Pocket037,Sketch076,Pocket038,Fillet010,Fillet011,Fillet012,Sketch240,Pad121,Fillet127,Fillet128]
  Origin = -> Origin001
  Placement = pos=(-363,-84,159) rot=(0,0,1;0rad)
  Tip = -> Fillet128
FEATURE [Part::FeaturePython] Parts002  # WARN: FeaturePython — macro-defined, semantics opaque (R4)
  Group = -> [Body001,Body009,Body010,Body016,Body019]
  GroupMode = 0
FEATURE [Part::Mirroring] Part__Mirroring  label="Door-back-Body (Mirror #1)"
  Base = (0,0,0)
  Normal = (1,0,0)
  Source = -> Body001
FEATURE [Part::FeaturePython] Parts005  # WARN: FeaturePython — macro-defined, semantics opaque (R4)
  Group = -> [Part__Mirroring]
  GroupMode = 0
FEATURE [Part::FeaturePython] Slice002  # WARN: FeaturePython — macro-defined, semantics opaque (R4)
  Base = -> Body001
  Mode = 1
  Tolerance = 0
  Tools = -> [Body009]
FEATURE [Part::FeaturePython] Slice004  # WARN: FeaturePython — macro-defined, semantics opaque (R4)
  Base = -> Body001
  Mode = 1
  Tolerance = 0
  Tools = -> [Body009]
FEATURE [Part::FeaturePython] Slice004_child0  label="Slice004.0"  # WARN: FeaturePython — macro-defined, semantics opaque (R4)
  Base = -> Slice004
  FilterType = 1
  Invert = false
  OverrideMaxVal = 0
  WindowFrom = 80
  WindowTo = 100
  items = 0
FEATURE [Part::FeaturePython] Slice004_child1  label="Slice004.1"  # WARN: FeaturePython — macro-defined, semantics opaque (R4)
  Base = -> Slice004
  FilterType = 1
  Invert = false
  OverrideMaxVal = 0
  WindowFrom = 80
  WindowTo = 100
  items = 1
FEATURE [App::DocumentObjectGroup] GrExplode_Slice004  label="Exploded Slice-door-left-back-far-left"
  Group = -> [Slice004_child0,Slice004_child1]
FEATURE [Part::FeaturePython] Slice006  # WARN: FeaturePython — macro-defined, semantics opaque (R4)
  Base = -> Body001
  Mode = 1
  Tolerance = 0
  Tools = -> [Body016]
FEATURE [Part::FeaturePython] Slice007  # WARN: FeaturePython — macro-defined, semantics opaque (R4)
  Base = -> Body001
  Mode = 1
  Tolerance = 0
  Tools = -> [Body019]
FEATURE [Part::FeaturePython] Slice008  # WARN: FeaturePython — macro-defined, semantics opaque (R4)
  Base = -> Body001
  Mode = 1
  Tolerance = 0
  Tools = -> [Body019]
FEATURE [Part::FeaturePython] Slice008_child0  label="Slice008.0"  # WARN: FeaturePython — macro-defined, semantics opaque (R4)
  Base = -> Slice008
  FilterType = 1
  Invert = false
  OverrideMaxVal = 0
  WindowFrom = 80
  WindowTo = 100
  items = 0
FEATURE [Part::FeaturePython] Slice008_child1  label="Slice008.1"  # WARN: FeaturePython — macro-defined, semantics opaque (R4)
  Base = -> Slice008
  FilterType = 1
  Invert = false
  OverrideMaxVal = 0
  WindowFrom = 80
  WindowTo = 100
  items = 1
FEATURE [Part::FeaturePython] Slice008_child2  label="Slice008.2"  # WARN: FeaturePython — macro-defined, semantics opaque (R4)
  Base = -> Slice008
  FilterType = 1
  Invert = false
  OverrideMaxVal = 0
  WindowFrom = 80
  WindowTo = 100
  items = 2
FEATURE [App::DocumentObjectGroup] GrExplode_Slice008  label="Exploded Slice-left_back_door_v3.1"
  Group = -> [Slice008_child0,Slice008_child1,Slice008_child2]
FEATURE [PartDesign::Fillet] Fillet129
  Base = -> Pocket112 [Face100]
  BaseFeature = -> Pocket112
  Placement = pos=(0,0,0) rot=(0.57735,0.57735,0.57735;2.0944rad)
  Radius = 1
  SupportTransform = false
  UseAllEdges = false
FEATURE [PartDesign::Fillet] Fillet130
  Base = -> Fillet129 [Edge519,Edge787]
  BaseFeature = -> Fillet129
  Placement = pos=(0,0,0) rot=(0.57735,0.57735,0.57735;2.0944rad)
  Radius = 2
  SupportTransform = false
  UseAllEdges = false
FEATURE [Part::FeaturePython] Slice019  # WARN: FeaturePython — macro-defined, semantics opaque (R4)
  Base = -> Body001
  Mode = 1
  Tolerance = 0
  Tools = -> [Body019]
FEATURE [Part::FeaturePython] Slice019_child0  label="Slice019.0-v4-door_left"  # WARN: FeaturePython — macro-defined, semantics opaque (R4)
  Base = -> Slice019
  FilterType = 1
  Invert = false
  OverrideMaxVal = 0
  WindowFrom = 80
  WindowTo = 100
  items = 0
FEATURE [Part::FeaturePython] Slice019_child1  label="Slice019.1"  # WARN: FeaturePython — macro-defined, semantics opaque (R4)
  Base = -> Slice019
  FilterType = 1
  Invert = false
  OverrideMaxVal = 0
  WindowFrom = 80
  WindowTo = 100
  items = 1
FEATURE [Part::FeaturePython] Slice019_child2  label="Slice019.2-door_right"  # WARN: FeaturePython — macro-defined, semantics opaque (R4)
  Base = -> Slice019
  FilterType = 1
  Invert = false
  OverrideMaxVal = 0
  WindowFrom = 80
  WindowTo = 100
  items = 2
FEATURE [App::DocumentObjectGroup] GrExplode_Slice019  label="Exploded Slice019"
  Group = -> [Slice019_child0,Slice019_child1,Slice019_child2]
FEATURE [Sketcher::SketchObject] Sketch241
  ExternalGeometry = -> [Fillet130]
  FullyConstrained = true
  MapMode = 5
  Placement = pos=(102,-1.071e-13,0) rot=(-0.57735,-0.57735,0.57735;2.0944rad)
  Support = -> [Fillet130]
  sketch-geometry (8):
    g0: LineSegment StartX=8 StartY=-62.992 StartZ=0 EndX=-2 EndY=-62.992 EndZ=0
    g1: LineSegment StartX=-2 StartY=-62.992 StartZ=0 EndX=-2 EndY=-31.7852 EndZ=0
    g2: LineSegment StartX=-2 StartY=-31.7852 StartZ=0 EndX=8 EndY=-31.7852 EndZ=0
    g3: LineSegment StartX=8 StartY=-31.7852 StartZ=0 EndX=8 EndY=-35.217 EndZ=0
    g4: LineSegment StartX=8 StartY=-35.217 StartZ=0 EndX=1.5 EndY=-35.217 EndZ=0
    g5: LineSegment StartX=1.5 StartY=-35.217 StartZ=0 EndX=1.5 EndY=-58.8418 EndZ=0
    g6: LineSegment StartX=1.5 StartY=-58.8418 StartZ=0 EndX=8 EndY=-58.8418 EndZ=0
    g7: LineSegment StartX=8 StartY=-58.8418 StartZ=0 EndX=8 EndY=-62.992 EndZ=0
  constraints (23):
    c: PointOnObject(g0,g-9)
    c: Horizontal(g0)
    c: PointOnObject(g-3,g0)
    c: Coincident(g1,g0)
    c: Vertical(g1)
    c: Coincident(g2,g1)
    c: Horizontal(g2)
    c: Coincident(g2,g-8)
    c: PointOnObject(g-5,g1)
    c: Coincident(g3,g2)
    c: PointOnObject(g3,g-10)
    c: Coincident(g4,g3)
    c: Horizontal(g4)
    c: Coincident(g5,g4)
    c: Vertical(g5)
    c: Coincident(g6,g5)
    c: PointOnObject(g6,g-9)
    c: Coincident(g7,g6)
    c: Coincident(g7,g0)
    c: PointOnObject(g-4,g6)
    c: Horizontal(g6)
    c: PointOnObject(g-6,g5)
    c: PointOnObject(g-7,g4)
FEATURE [PartDesign::Pad] Pad122
  BaseFeature = -> Fillet130
  Direction = (0.939693,-8e-16,-0.34202)
  Length = 20
  Length2 = 10
  Placement = pos=(0,0,0) rot=(0.57735,0.57735,0.57735;2.0944rad)
  Profile = -> Sketch241
  ReferenceAxis = -> Sketch053 [Edge1]
  Type = 4
FEATURE [PartDesign::Fillet] Fillet131
  Base = -> Pad122 [Edge76,Edge388,Edge372,Edge219,Edge224]
  BaseFeature = -> Pad122
  Placement = pos=(0,0,0) rot=(0.57735,0.57735,0.57735;2.0944rad)
  Radius = 4.98
  SupportTransform = false
  UseAllEdges = false
FEATURE [PartDesign::Body] Body013  label="Slide-left-Body002"
  Group = -> [Sketch039,Pad018,Sketch040,Pocket015,Sketch041,Pocket016,Sketch042,Sketch043,Pad019,Sketch044,Pocket017,Sketch045,Pocket018,Sketch046,Pocket019,Sketch047,Pocket020,Sketch048,Pocket021,Sketch049,Pocket022,Sketch051,Pocket023,Sketch052,Pad021,Sketch053,Sketch054,Pocket024,Sketch055,Pocket025,Sketch056,Pocket026,Sketch057,Pocket027,Sketch058,Pad022,Sketch059,Pocket028,Sketch060,Pocket029,Sketch064,+60 more]
  Origin = -> Origin012
  Placement = pos=(-375,53,160) rot=(0,0,-1;1.5708rad)
  Tip = -> Fillet131
FEATURE [Part::FeaturePython] Parts010  # WARN: FeaturePython — macro-defined, semantics opaque (R4)
  Group = -> [Body013,Body014]
  GroupMode = 0
FEATURE [Part::FeaturePython] Slice003  # WARN: FeaturePython — macro-defined, semantics opaque (R4)
  Base = -> Body013
  Mode = 1
  Tolerance = 0
  Tools = -> [Body014]
FEATURE [Part::FeaturePython] Slice003_child0  label="Slice003.0"  # WARN: FeaturePython — macro-defined, semantics opaque (R4)
  Base = -> Slice003
  FilterType = 1
  Invert = false
  OverrideMaxVal = 0
  WindowFrom = 80
  WindowTo = 100
  items = 0
FEATURE [Part::FeaturePython] Slice003_child1  label="Slice003.1"  # WARN: FeaturePython — macro-defined, semantics opaque (R4)
  Base = -> Slice003
  FilterType = 1
  Invert = false
  OverrideMaxVal = 0
  WindowFrom = 80
  WindowTo = 100
  items = 1
FEATURE [App::DocumentObjectGroup] GrExplode_Slice003  label="Exploded Slice-slide-left-ramp"
  Group = -> [Slice003_child0,Slice003_child1]
FEATURE [Part::FeaturePython] Slice009  # WARN: FeaturePython — macro-defined, semantics opaque (R4)
  Base = -> Body013
  Mode = 1
  Tolerance = 0
  Tools = -> [Body014]
FEATURE [Part::FeaturePython] Slice009_child0  label="Slice009.0"  # WARN: FeaturePython — macro-defined, semantics opaque (R4)
  Base = -> Slice009
  FilterType = 1
  Invert = false
  OverrideMaxVal = 0
  WindowFrom = 80
  WindowTo = 100
  items = 0
FEATURE [Part::FeaturePython] Slice009_child1  label="Slice009.1"  # WARN: FeaturePython — macro-defined, semantics opaque (R4)
  Base = -> Slice009
  FilterType = 1
  Invert = false
  OverrideMaxVal = 0
  WindowFrom = 80
  WindowTo = 100
  items = 1
FEATURE [App::DocumentObjectGroup] GrExplode_Slice009  label="Exploded Slice-slide-left-ramp-v2.1"
  Group = -> [Slice009_child0,Slice009_child1]
FEATURE [Part::FeaturePython] Slice015  # WARN: FeaturePython — macro-defined, semantics opaque (R4)
  Base = -> Body013
  Mode = 1
  Tolerance = 0
  Tools = -> [Body014]
FEATURE [Part::FeaturePython] Slice015_child0  label="Slice015.0-v3_left_slide_rear"  # WARN: FeaturePython — macro-defined, semantics opaque (R4)
  Base = -> Slice015
  FilterType = 1
  Invert = false
  OverrideMaxVal = 0
  WindowFrom = 80
  WindowTo = 100
  items = 0
FEATURE [Part::FeaturePython] Slice015_child1  label="Slice015.1-v3_left_slide_front"  # WARN: FeaturePython — macro-defined, semantics opaque (R4)
  Base = -> Slice015
  FilterType = 1
  Invert = false
  OverrideMaxVal = 0
  WindowFrom = 80
  WindowTo = 100
  items = 1
FEATURE [App::DocumentObjectGroup] GrExplode_Slice015  label="Exploded Slice015-v3_left_slide"
  Group = -> [Slice015_child0,Slice015_child1]
FEATURE [Part::FeaturePython] Slice018  # WARN: FeaturePython — macro-defined, semantics opaque (R4)
  Base = -> Body013
  Mode = 1
  Tolerance = 0
  Tools = -> [Body014]
FEATURE [Part::FeaturePython] Slice018_child0  label="Slice018.0-left_slide_v4_front"  # WARN: FeaturePython — macro-defined, semantics opaque (R4)
  Base = -> Slice018
  FilterType = 1
  Invert = false
  OverrideMaxVal = 0
  WindowFrom = 80
  WindowTo = 100
  items = 0
FEATURE [Part::FeaturePython] Slice018_child1  label="Slice018.1-left_slide_v4_back"  # WARN: FeaturePython — macro-defined, semantics opaque (R4)
  Base = -> Slice018
  FilterType = 1
  Invert = false
  OverrideMaxVal = 0
  WindowFrom = 80
  WindowTo = 100
  items = 1
FEATURE [App::DocumentObjectGroup] GrExplode_Slice018  label="Exploded Slice018"
  Group = -> [Slice018_child0,Slice018_child1]
FEATURE [Part::FeaturePython] Slice020  # WARN: FeaturePython — macro-defined, semantics opaque (R4)
  Base = -> Body013
  Mode = 1
  Tolerance = 0
  Tools = -> [Body014]
FEATURE [Part::FeaturePython] Slice020_child0  label="Slice020.0-v4.1_left_slide_rear"  # WARN: FeaturePython — macro-defined, semantics opaque (R4)
  Base = -> Slice020
  FilterType = 1
  Invert = false
  OverrideMaxVal = 0
  WindowFrom = 80
  WindowTo = 100
  items = 0
FEATURE [Part::FeaturePython] Slice020_child1  label="Slice020.1-v4.1_left_slide_front"  # WARN: FeaturePython — macro-defined, semantics opaque (R4)
  Base = -> Slice020
  FilterType = 1
  Invert = false
  OverrideMaxVal = 0
  WindowFrom = 80
  WindowTo = 100
  items = 1
FEATURE [App::DocumentObjectGroup] GrExplode_Slice020  label="Exploded Slice020-v4.1_left_slide"
  Group = -> [Slice020_child0,Slice020_child1]
FEATURE [App::FeaturePython] Constraints039  # WARN: FeaturePython — macro-defined, semantics opaque (R4)
  _Version = 1
FEATURE [Sketcher::SketchObject] Sketch242
  FullyConstrained = true
  MapMode = 5
  Placement = pos=(0,0,0) rot=(0.57735,0.57735,0.57735;2.0944rad)
  Support = -> [YZ_Plane042]
  sketch-geometry (4):
    g0: LineSegment StartX=0 StartY=0 StartZ=0 EndX=30 EndY=0 EndZ=0
    g1: LineSegment StartX=30 StartY=0 StartZ=0 EndX=30 EndY=20 EndZ=0
    g2: LineSegment StartX=30 StartY=20 StartZ=0 EndX=0 EndY=20 EndZ=0
    g3: LineSegment StartX=0 StartY=20 StartZ=0 EndX=0 EndY=0 EndZ=0
  constraints (11):
    c: Coincident(g0,g1)
    c: Coincident(g1,g2)
    c: Coincident(g2,g3)
    c: Coincident(g3,g0)
    c: Horizontal(g0)
    c: Horizontal(g2)
    c: Vertical(g1)
    c: Vertical(g3)
    c: Coincident(g0,g-1)
    c: DistanceX(g0,g0) = 30
    c: DistanceY(g1,g1) = 20
FEATURE [PartDesign::Pad] Pad123  label="Pad123-body"
  Direction = (1,-2e-16,3e-16)
  Length = 8
  Length2 = 10
  Placement = pos=(0,0,0) rot=(0.57735,0.57735,0.57735;2.0944rad)
  Profile = -> Sketch242
  ReferenceAxis = -> Sketch242 [N_Axis]
  Type = 0
FEATURE [Sketcher::SketchObject] Sketch243
  ExternalGeometry = -> [Pad123]
  FullyConstrained = true
  MapMode = 5
  Placement = pos=(-7.8e-15,1.11e-14,20) rot=(0,0,-1;1.5708rad)
  Support = -> [Pad123]
  sketch-geometry (4):
    g0: LineSegment StartX=-12 StartY=8 StartZ=0 EndX=7.1e-15 EndY=8 EndZ=0
    g1: LineSegment StartX=7.1e-15 StartY=8 StartZ=0 EndX=7.1e-15 EndY=3 EndZ=0
    g2: LineSegment StartX=7.1e-15 StartY=3 StartZ=0 EndX=-12 EndY=3 EndZ=0
    g3: LineSegment StartX=-12 StartY=3 StartZ=0 EndX=-12 EndY=8 EndZ=0
  constraints (11):
    c: Coincident(g0,g1)
    c: Coincident(g1,g2)
    c: Coincident(g2,g3)
    c: Coincident(g3,g0)
    c: Horizontal(g0)
    c: Horizontal(g2)
    c: Vertical(g1)
    c: Vertical(g3)
    c: DistanceY(g1,g1) = 5
    c: DistanceX(g2,g2) = 12
    c: Coincident(g0,g-3)
FEATURE [PartDesign::Pad] Pad124  label="Pad124-vertical"
  BaseFeature = -> Pad123
  Direction = (-4e-16,6e-16,1)
  Length = 25
  Length2 = 10
  Placement = pos=(0,0,0) rot=(0.57735,0.57735,0.57735;2.0944rad)
  Profile = -> Sketch243
  ReferenceAxis = -> Sketch243 [N_Axis]
  Type = 0
FEATURE [PartDesign::Fillet] Fillet132  label="Fillet132-vertical"
  Base = -> Pad124 [Edge19,Edge24]
  BaseFeature = -> Pad124
  Placement = pos=(0,0,0) rot=(0.57735,0.57735,0.57735;2.0944rad)
  Radius = 5.95
  SupportTransform = false
  UseAllEdges = false
FEATURE [PartDesign::Fillet] Fillet133  label="Fillet133-vertical_base_short"
  Base = -> Fillet132 [Edge16]
  BaseFeature = -> Fillet132
  Placement = pos=(0,0,0) rot=(0.57735,0.57735,0.57735;2.0944rad)
  Radius = 2
  SupportTransform = false
  UseAllEdges = false
FEATURE [PartDesign::Fillet] Fillet134  label="Fillet134-vertical_base_long"
  Base = -> Fillet133 [Edge26]
  BaseFeature = -> Fillet133
  Placement = pos=(0,0,0) rot=(0.57735,0.57735,0.57735;2.0944rad)
  Radius = 5
  SupportTransform = false
  UseAllEdges = false
FEATURE [PartDesign::Fillet] Fillet135  label="Fillet135-base_corners"
  Base = -> Fillet134 [Edge30,Edge40,Edge34]
  BaseFeature = -> Fillet134
  Placement = pos=(0,0,0) rot=(0.57735,0.57735,0.57735;2.0944rad)
  Radius = 8
  SupportTransform = false
  UseAllEdges = false
FEATURE [Sketcher::SketchObject] Sketch244
  ExternalGeometry = -> [Fillet135]
  FullyConstrained = true
  MapMode = 5
  Placement = pos=(8,-5.3e-15,3.6e-15) rot=(0.57735,0.57735,0.57735;2.0944rad)
  Support = -> [Fillet135]
  sketch-geometry (4):
    g0: ArcOfCircle CenterX=8 CenterY=10 CenterZ=0 NormalX=0 NormalY=0 NormalZ=1 AngleXU=0 Radius=6 StartAngle=1.5708 EndAngle=4.71239
    g1: ArcOfCircle CenterX=22 CenterY=10 CenterZ=0 NormalX=0 NormalY=0 NormalZ=1 AngleXU=0 Radius=6 StartAngle=4.71239 EndAngle=7.85398
    g2: LineSegment StartX=8 StartY=4 StartZ=0 EndX=22 EndY=4 EndZ=0
    g3: LineSegment StartX=22 StartY=16 StartZ=0 EndX=8 EndY=16 EndZ=0
  constraints (10):
    c: Tangent(g0,g2) = -1.5708
    c: Tangent(g2,g1) = -1.5708
    c: Tangent(g1,g3) = -1.5708
    c: Tangent(g3,g0) = -1.5708
    c: Equal(g0,g1)
    c: Horizontal(g1,g0)
    c: Diameter(g0) = 12
    c: DistanceX(g0) = 8
    c: DistanceY(g0) = 10
    c: DistanceX(g1,g-3) = 8
FEATURE [PartDesign::Pocket] Pocket113  label="Pocket113_screw_inset"
  BaseFeature = -> Fillet135
  Direction = (-1,9e-16,-6e-16)
  Length = 2
  Length2 = 5
  Placement = pos=(0,0,0) rot=(0.57735,0.57735,0.57735;2.0944rad)
  Profile = -> Sketch244
  ReferenceAxis = -> Sketch244 [N_Axis]
  Type = 0
FEATURE [Sketcher::SketchObject] Sketch245
  ExternalGeometry = -> [Pocket113]
  FullyConstrained = true
  MapMode = 5
  Placement = pos=(6,-5.3e-15,3.7e-15) rot=(0.57735,0.57735,0.57735;2.0944rad)
  Support = -> [Pocket113]
  sketch-geometry (2):
    g0: Circle CenterX=8 CenterY=10 CenterZ=0 NormalX=0 NormalY=0 NormalZ=1 AngleXU=0 Radius=2.65
    g1: Circle CenterX=22 CenterY=10 CenterZ=0 NormalX=0 NormalY=0 NormalZ=1 AngleXU=0 Radius=2.65
  constraints (4):
    c: Coincident(g0,g-3)
    c: Coincident(g1,g-4)
    c: Equal(g0,g1)
    c: Diameter(g1) = 5.3
FEATURE [PartDesign::Pocket] Pocket114  label="Pocket114-screw_holes"
  BaseFeature = -> Pocket113
  Direction = (-1,8e-16,-6e-16)
  Length = 5
  Length2 = 5
  Placement = pos=(0,0,0) rot=(0.57735,0.57735,0.57735;2.0944rad)
  Profile = -> Sketch245
  ReferenceAxis = -> Sketch245 [N_Axis]
  Type = 1
FEATURE [PartDesign::Chamfer] Chamfer017
  Angle = 45
  Base = -> Pocket114 [Edge9]
  BaseFeature = -> Pocket114
  ChamferType = 0
  FlipDirection = false
  Placement = pos=(0,0,0) rot=(0.57735,0.57735,0.57735;2.0944rad)
  Size = 0.9
  Size2 = 1
  SupportTransform = false
  UseAllEdges = false
FEATURE [PartDesign::Fillet] Fillet136
  Base = -> Chamfer017 [Face4]
  BaseFeature = -> Chamfer017
  Placement = pos=(0,0,0) rot=(0.57735,0.57735,0.57735;2.0944rad)
  Radius = 0.6
  SupportTransform = false
  UseAllEdges = false
FEATURE [PartDesign::Fillet] Fillet137
  Base = -> Fillet136 [Face37,Face36,Face51]
  BaseFeature = -> Fillet136
  Placement = pos=(0,0,0) rot=(0.57735,0.57735,0.57735;2.0944rad)
  Radius = 0.3
  SupportTransform = false
  UseAllEdges = false
FEATURE [PartDesign::Fillet] Fillet138
  Base = -> Fillet137 [Edge58]
  BaseFeature = -> Fillet137
  Placement = pos=(0,0,0) rot=(0.57735,0.57735,0.57735;2.0944rad)
  Radius = 0.6
  SupportTransform = false
  UseAllEdges = false
FEATURE [Sketcher::SketchObject] Sketch246
  ExternalGeometry = -> [Fillet138]
  FullyConstrained = true
  MapMode = 5
  Placement = pos=(8,-5.3e-15,7.5e-15) rot=(0.57735,0.57735,0.57735;2.0944rad)
  Support = -> [Fillet138]
  sketch-geometry (4):
    g0: ArcOfCircle CenterX=5.95 CenterY=39.05 CenterZ=0 NormalX=0 NormalY=0 NormalZ=1 AngleXU=0 Radius=2.5 StartAngle=-9e-16 EndAngle=3.14159
    g1: ArcOfCircle CenterX=5.95 CenterY=25.05 CenterZ=0 NormalX=0 NormalY=0 NormalZ=1 AngleXU=0 Radius=2.5 StartAngle=3.14159 EndAngle=6.28319
    g2: LineSegment StartX=3.45 StartY=39.05 StartZ=0 EndX=3.45 EndY=25.05 EndZ=0
    g3: LineSegment StartX=8.45 StartY=25.05 StartZ=0 EndX=8.45 EndY=39.05 EndZ=0
  constraints (9):
    c: Tangent(g0,g2) = -1.5708
    c: Tangent(g2,g1) = -1.5708
    c: Tangent(g1,g3) = -1.5708
    c: Tangent(g3,g0) = -1.5708
    c: Equal(g0,g1)
    c: Coincident(g0,g-3)
    c: Vertical(g2)
    c: DistanceY(g1,g0) = 14
    c: Diameter(g0) = 5
FEATURE [PartDesign::Pocket] Pocket115
  BaseFeature = -> Fillet138
  Direction = (-1,7e-16,-1.1e-15)
  Length = 5
  Length2 = 5
  Placement = pos=(0,0,0) rot=(0.57735,0.57735,0.57735;2.0944rad)
  Profile = -> Sketch246
  ReferenceAxis = -> Sketch246 [N_Axis]
  Type = 1
FEATURE [PartDesign::Fillet] Fillet139
  Base = -> Pocket115 [Face61]
  BaseFeature = -> Pocket115
  Placement = pos=(0,0,0) rot=(0.57735,0.57735,0.57735;2.0944rad)
  Radius = 1
  SupportTransform = false
  UseAllEdges = false
FEATURE [PartDesign::Body] Body026005002
  Group = -> [Sketch242,Pad123,Sketch243,Pad124,Fillet132,Fillet133,Fillet134,Fillet135,Sketch244,Pocket113,Sketch245,Pocket114,Chamfer017,Fillet136,Fillet137,Fillet138,Sketch246,Pocket115,Fillet139]
  Origin = -> Origin041
  Tip = -> Fillet139
FEATURE [Part::FeaturePython] Parts039  # WARN: FeaturePython — macro-defined, semantics opaque (R4)
  Group = -> [Body026005002]
  GroupMode = 0
FEATURE [Part::FeaturePython] Assembly  # WARN: FeaturePython — macro-defined, semantics opaque (R4)
  AutoRelax = true
  BuildShape = 0
  Freeze = false
  Group = -> [Constraints,Elements,Parts]
  Verbose = false
  _SolverType = 1
  _Version = 1
FEATURE [App::FeaturePython] Constraints  # WARN: FeaturePython — macro-defined, semantics opaque (R4)
  Group = -> [Constraint,Constraint001,Constraint002,Constraint003,Constraint004,Constraint005,Constraint006,Constraint008,Constraint009,Constraint010,Constraint011,Constraint012,Constraint013,Constraint014,Constraint015,Constraint016,Constraint017,Constraint018,Constraint021,Constraint023,Constraint027,Constraint028,Constraint033,Constraint034,Constraint035,Constraint036,Constraint037,Constraint038,+66 more]
  _Version = 1
FEATURE [App::FeaturePython] Elements  # WARN: FeaturePython — macro-defined, semantics opaque (R4)
  Group = -> [_Element,_Element001,_Element002,_Element003,_Element004,_Element005,_Element006,_Element007,_Element008,_Element009,_Element010,_Element011,_Element012,_Element013,_Element014,_Element015,_Element016,_Element017,_Element018,_Element019,_Element020,_Element021,_Element022,_Element023,_Element024,_Element025,_Element026,_Element027,_Element028,_Element029,_Element030,_Element031,_Element032,+157 more]
FEATURE [Part::FeaturePython] Parts  # WARN: FeaturePython — macro-defined, semantics opaque (R4)
  Group = -> [Link,Link001,Link002,Link003,Link004,Link005,Link006,Link007,Link008,Link009,Assembly001,Assembly002,Assembly004,Link011,Link012,Link013,Link014,Link015,Link016,Workplane,Workplane001,Workplane002,Assembly005,Assembly006,Assembly007,Assembly008,Assembly010,Assembly011,Assembly012,Assembly014,Assembly016,Assembly017,Assembly018,Assembly019,Assembly020,Assembly028,Assembly031,Assembly029,+9 more]
  GroupMode = 0
FEATURE [Part::FeaturePython] _Element  # link proxy (typed FeaturePython)
  Detach = false
  LinkTransform = true
  LinkedObject = -> Link003 [Face106]
  _Parent = -> Elements
FEATURE [Part::FeaturePython] _Element001  # link proxy (typed FeaturePython)
  Detach = false
  LinkTransform = true
  LinkedObject = -> Link [Face1]
  _Parent = -> Elements
FEATURE [Part::FeaturePython] _Element002  # link proxy (typed FeaturePython)
  Detach = false
  LinkTransform = true
  LinkedObject = -> Link001 [Face1]
  _Parent = -> Elements
FEATURE [Part::FeaturePython] _Element003  # link proxy (typed FeaturePython)
  Detach = false
  LinkTransform = true
  LinkedObject = -> Link [Face79]
  _Parent = -> Elements
FEATURE [Part::FeaturePython] _Element004  # link proxy (typed FeaturePython)
  Detach = false
  LinkTransform = true
  LinkedObject = -> Link003 [Face80]
  _Parent = -> Elements
FEATURE [Part::FeaturePython] _Element005  # link proxy (typed FeaturePython)
  Detach = false
  LinkTransform = true
  LinkedObject = -> Link001 [Face79]
  _Parent = -> Elements
FEATURE [Part::FeaturePython] _Element006  # link proxy (typed FeaturePython)
  Detach = false
  LinkTransform = true
  LinkedObject = -> Link002 [Face1]
  _Parent = -> Elements
FEATURE [Part::FeaturePython] _Element007  # link proxy (typed FeaturePython)
  Detach = false
  LinkTransform = true
  LinkedObject = -> Link002 [Face79]
  _Parent = -> Elements
FEATURE [Part::FeaturePython] _Element008  # link proxy (typed FeaturePython)
  Detach = false
  LinkTransform = true
  LinkedObject = -> Link003 [Face1]
  _Parent = -> Elements
FEATURE [Part::FeaturePython] _Element009  # link proxy (typed FeaturePython)
  Detach = false
  LinkTransform = true
  LinkedObject = -> Link002 [Face106]
  _Parent = -> Elements
FEATURE [Part::FeaturePython] _Element010  # link proxy (typed FeaturePython)
  Detach = false
  LinkTransform = true
  LinkedObject = -> Link001 [Face50]
  _Parent = -> Elements
FEATURE [Part::FeaturePython] _Element011  # link proxy (typed FeaturePython)
  Detach = false
  LinkTransform = true
  LinkedObject = -> Link003 [Face3]
  _Parent = -> Elements
FEATURE [Part::FeaturePython] _Element012  # link proxy (typed FeaturePython)
  Detach = false
  LinkTransform = true
  LinkedObject = -> Link004 [Face80]
  _Parent = -> Elements
FEATURE [Part::FeaturePython] _Element013  # link proxy (typed FeaturePython)
  Detach = false
  LinkTransform = true
  LinkedObject = -> Link004 [Face106]
  _Parent = -> Elements
FEATURE [Part::FeaturePython] _Element014  # link proxy (typed FeaturePython)
  Detach = false
  LinkTransform = true
  LinkedObject = -> Link001 [Face3]
  _Parent = -> Elements
FEATURE [Part::FeaturePython] _Element015  # link proxy (typed FeaturePython)
  Detach = false
  LinkTransform = true
  LinkedObject = -> Link004 [Face1]
  _Parent = -> Elements
FEATURE [Part::FeaturePython] _Element016  # link proxy (typed FeaturePython)
  Detach = false
  LinkTransform = true
  LinkedObject = -> Link [Face86]
  _Parent = -> Elements
FEATURE [Part::FeaturePython] _Element017  # link proxy (typed FeaturePython)
  Detach = false
  LinkTransform = true
  LinkedObject = -> Link [Vertex59]
  _Parent = -> Elements
FEATURE [Part::FeaturePython] _Element018  # link proxy (typed FeaturePython)
  Detach = false
  LinkTransform = true
  LinkedObject = -> Link001 [Vertex103]
  _Parent = -> Elements
FEATURE [Part::FeaturePython] _Element019  # link proxy (typed FeaturePython)
  Detach = false
  LinkTransform = true
  LinkedObject = -> Link005 [Face1]
  _Parent = -> Elements
FEATURE [Part::FeaturePython] _Element020  # link proxy (typed FeaturePython)
  Detach = false
  LinkTransform = true
  LinkedObject = -> Link001 [Face4]
  _Parent = -> Elements
FEATURE [Part::FeaturePython] _Element021  # link proxy (typed FeaturePython)
  Detach = false
  LinkTransform = true
  LinkedObject = -> Link006 [Face1]
  _Parent = -> Elements
FEATURE [Part::FeaturePython] _Element022  # link proxy (typed FeaturePython)
  Detach = false
  LinkTransform = true
  LinkedObject = -> Link002 [Face2]
  _Parent = -> Elements
FEATURE [Part::FeaturePython] _Element023  # link proxy (typed FeaturePython)
  Detach = false
  LinkTransform = true
  LinkedObject = -> Link008 [Face41]
  _Parent = -> Elements
FEATURE [Part::FeaturePython] _Element024  # link proxy (typed FeaturePython)
  Detach = false
  LinkTransform = true
  LinkedObject = -> Link007 [Face2]
  _Parent = -> Elements
FEATURE [Part::FeaturePython] _Element025  # link proxy (typed FeaturePython)
  Detach = false
  LinkTransform = true
  LinkedObject = -> Link007 [Face1]
  _Parent = -> Elements
FEATURE [Part::FeaturePython] _Element026  # link proxy (typed FeaturePython)
  Detach = false
  LinkTransform = true
  LinkedObject = -> Link008 [Face45]
  _Parent = -> Elements
FEATURE [Part::FeaturePython] _Element027  # link proxy (typed FeaturePython)
  Detach = false
  LinkTransform = true
  LinkedObject = -> Link007 [Face107]
  _Parent = -> Elements
FEATURE [Part::FeaturePython] _Element028  # link proxy (typed FeaturePython)
  Detach = false
  LinkTransform = true
  LinkedObject = -> Link008 [Face1]
  _Parent = -> Elements
FEATURE [Part::FeaturePython] _Element029  # link proxy (typed FeaturePython)
  Detach = false
  LinkTransform = true
  LinkedObject = -> Link001 [Face2]
  _Parent = -> Elements
FEATURE [Part::FeaturePython] _Element030  # link proxy (typed FeaturePython)
  Detach = false
  LinkTransform = true
  LinkedObject = -> Link007 [Face80]
  _Parent = -> Elements
FEATURE [Part::FeaturePython] _Element031  # link proxy (typed FeaturePython)
  Detach = false
  LinkTransform = true
  LinkedObject = -> Link009 [Face41]
  _Parent = -> Elements
FEATURE [Part::FeaturePython] _Element032  # link proxy (typed FeaturePython)
  Detach = false
  LinkTransform = true
  LinkedObject = -> Link009 [Face39]
  _Parent = -> Elements
FEATURE [Part::FeaturePython] _Element033  # link proxy (typed FeaturePython)
  Detach = false
  LinkTransform = true
  LinkedObject = -> Link009 [Face1]
  _Parent = -> Elements
FEATURE [Part::FeaturePython] _Element034  # link proxy (typed FeaturePython)
  Detach = false
  LinkTransform = true
  LinkedObject = -> Link001 [Vertex296]
  _Parent = -> Elements
FEATURE [Part::FeaturePython] _Element035  # link proxy (typed FeaturePython)
  Detach = false
  LinkTransform = true
  LinkedObject = -> Link [Face50]
  _Parent = -> Elements
FEATURE [Part::FeaturePython] Assembly001  label="assy-slide-left-v1"  # WARN: FeaturePython — macro-defined, semantics opaque (R4)
  AutoRelax = true
  BuildShape = 0
  Freeze = false
  Group = -> [Constraints001,Elements001,Parts001]
  Placement = pos=(392,-386.446,-140) rot=(0,0,1;0rad)
  Verbose = false
  _SolverType = 1
  _Version = 1
FEATURE [App::FeaturePython] Constraints001  # WARN: FeaturePython — macro-defined, semantics opaque (R4)
  Group = -> [Constraint070,Constraint071]
  _Version = 1
FEATURE [App::FeaturePython] Elements001  # WARN: FeaturePython — macro-defined, semantics opaque (R4)
  Group = -> [Element,Element001,Element002,Element003,Element008,Element012,Element013,Element014,Element015,Element016,Element017,Element022,Element023,Element039,_Element147,_Element148,_Element149,_Element150]
FEATURE [Part::FeaturePython] Assembly002  label="assy-door-back"  # WARN: FeaturePython — macro-defined, semantics opaque (R4)
  AutoRelax = true
  BuildShape = 0
  Freeze = false
  Group = -> [Constraints002,Elements002,Parts002]
  Placement = pos=(401.949,-397.084,-109.644) rot=(-1,0,1e-06;0.228205rad)
  Verbose = false
  _SolverType = 1
  _Version = 1
FEATURE [App::FeaturePython] Constraints002  # WARN: FeaturePython — macro-defined, semantics opaque (R4)
  Group = -> [Constraint072,Constraint073,Constraint074,Constraint088,Constraint089,Constraint090,Constraint094,Constraint095,Constraint096]
  _Version = 1
FEATURE [App::FeaturePython] Elements002  # WARN: FeaturePython — macro-defined, semantics opaque (R4)
  Group = -> [Element004,Element018,Element021,Element025,Element027,Element028,_Element152,_Element153,_Element154,_Element155,_Element156,Element063,_Element178,_Element179,_Element180,_Element181,_Element182,_Element183,_Element187,_Element188,_Element191,_Element193,_Element194,_Element195,_Element196]
FEATURE [Part::FeaturePython] Element  # link proxy (typed FeaturePython)
  Detach = false
  LinkTransform = true
  LinkedObject = -> Body [Pad.Face1]
  _Parent = -> Elements001
FEATURE [Part::FeaturePython] _Element036  # link proxy (typed FeaturePython)
  Detach = false
  LinkTransform = true
  LinkedObject = -> Assembly001 [1.$Element.]
  _Parent = -> Elements
FEATURE [Part::FeaturePython] Element001  # link proxy (typed FeaturePython)
  Detach = false
  LinkTransform = true
  LinkedObject = -> Body [Pad.Face5]
  _Parent = -> Elements001
FEATURE [Part::FeaturePython] _Element037  # link proxy (typed FeaturePython)
  Detach = false
  LinkTransform = true
  LinkedObject = -> Assembly001 [1.$Element001.]
  _Parent = -> Elements
FEATURE [Part::FeaturePython] _Element038  # link proxy (typed FeaturePython)
  Detach = false
  LinkTransform = true
  LinkedObject = -> Link003 [Face50]
  _Parent = -> Elements
FEATURE [Part::FeaturePython] Element002  # link proxy (typed FeaturePython)
  Detach = false
  LinkTransform = true
  LinkedObject = -> Body [Pad.Face4]
  _Parent = -> Elements001
FEATURE [Part::FeaturePython] _Element039  # link proxy (typed FeaturePython)
  Detach = false
  LinkTransform = true
  LinkedObject = -> Assembly001 [1.$Element002.]
  _Parent = -> Elements
FEATURE [Part::FeaturePython] _Element040  # link proxy (typed FeaturePython)
  Detach = false
  LinkTransform = true
  LinkedObject = -> Link [Vertex226]
  _Parent = -> Elements
FEATURE [Part::FeaturePython] Element003  # link proxy (typed FeaturePython)
  Detach = false
  LinkTransform = true
  LinkedObject = -> Body [Pad.Face2]
  _Parent = -> Elements001
FEATURE [Part::FeaturePython] _Element041  # link proxy (typed FeaturePython)
  Detach = false
  LinkTransform = true
  LinkedObject = -> Assembly001 [1.$Element003.]
  _Parent = -> Elements
FEATURE [Part::FeaturePython] Element004  # link proxy (typed FeaturePython)
  Detach = false
  LinkTransform = true
  LinkedObject = -> Body001 [Pad002.Face2]
  _Parent = -> Elements002
FEATURE [Part::FeaturePython] _Element042  # link proxy (typed FeaturePython)
  Detach = false
  LinkTransform = true
  LinkedObject = -> Assembly002 [1.$Element004.]
  _Parent = -> Elements
FEATURE [Part::FeaturePython] Assembly004  label="assy_door_front"  # WARN: FeaturePython — macro-defined, semantics opaque (R4)
  AutoRelax = true
  BuildShape = 0
  Freeze = false
  Group = -> [Constraints004,Elements004,Parts004]
  Placement = pos=(74.2323,-401.1,54.2192) rot=(-0.034724,0.174777,0.983996;2.05564rad)
  Verbose = false
  _SolverType = 1
  _Version = 1
FEATURE [App::FeaturePython] Constraints004  # WARN: FeaturePython — macro-defined, semantics opaque (R4)
  Group = -> [Constraint076,Constraint077,Constraint103,Constraint104,Constraint105,Constraint106,Constraint109,Constraint110,Constraint111,Constraint112,Constraint113]
  _Version = 1
FEATURE [App::FeaturePython] Elements004  # WARN: FeaturePython — macro-defined, semantics opaque (R4)
  Group = -> [Element019,Element020,Element024,Element026,Element029,Element043,_Element159,_Element160,_Element161,Element064,_Element204,_Element205,_Element206,_Element207,_Element208,_Element209,_Element210,_Element211,_Element212,_Element213,_Element214,_Element215,_Element216,_Element217,_Element218,_Element219,_Element220,_Element221,_Element222,_Element223,_Element224,_Element225,_Element226,+1 more]
FEATURE [Part::FeaturePython] _Element045  # link proxy (typed FeaturePython)
  Detach = false
  LinkTransform = true
  LinkedObject = -> Link013 [Face1]
  _Parent = -> Elements
FEATURE [Part::FeaturePython] _Element046  # link proxy (typed FeaturePython)
  Detach = false
  LinkTransform = true
  LinkedObject = -> Link013 [Face45]
  _Parent = -> Elements
FEATURE [Part::FeaturePython] _Element047  # link proxy (typed FeaturePython)
  Detach = false
  LinkTransform = true
  LinkedObject = -> Link002 [Face80]
  _Parent = -> Elements
FEATURE [Part::FeaturePython] _Element048  # link proxy (typed FeaturePython)
  Detach = false
  LinkTransform = true
  LinkedObject = -> Link013 [Face41]
  _Parent = -> Elements
FEATURE [Part::FeaturePython] _Element049  # link proxy (typed FeaturePython)
  Detach = false
  LinkTransform = true
  LinkedObject = -> Link012 [Face79]
  _Parent = -> Elements
FEATURE [Part::FeaturePython] _Element050  # link proxy (typed FeaturePython)
  Detach = false
  LinkTransform = true
  LinkedObject = -> Link012 [Face50]
  _Parent = -> Elements
FEATURE [Part::FeaturePython] _Element051  # link proxy (typed FeaturePython)
  Detach = false
  LinkTransform = true
  LinkedObject = -> Link012 [Face3]
  _Parent = -> Elements
FEATURE [Part::FeaturePython] _Element052  # link proxy (typed FeaturePython)
  Detach = false
  LinkTransform = true
  LinkedObject = -> Link002 [Face4]
  _Parent = -> Elements
FEATURE [Part::FeaturePython] _Element053  # link proxy (typed FeaturePython)
  Detach = false
  LinkTransform = true
  LinkedObject = -> Link007 [Face4]
  _Parent = -> Elements
FEATURE [Part::FeaturePython] _Element054  # link proxy (typed FeaturePython)
  Detach = false
  LinkTransform = true
  LinkedObject = -> Link014 [Face106]
  _Parent = -> Elements
FEATURE [Part::FeaturePython] _Element055  # link proxy (typed FeaturePython)
  Detach = false
  LinkTransform = true
  LinkedObject = -> Link014 [Face3]
  _Parent = -> Elements
FEATURE [Part::FeaturePython] _Element056  # link proxy (typed FeaturePython)
  Detach = false
  LinkTransform = true
  LinkedObject = -> Link015 [1.$Element.]
  _Parent = -> Elements
FEATURE [Part::FeaturePython] _Element057  # link proxy (typed FeaturePython)
  Detach = false
  LinkTransform = true
  LinkedObject = -> Link014 [Face50]
  _Parent = -> Elements
FEATURE [Part::FeaturePython] _Element058  # link proxy (typed FeaturePython)
  Detach = false
  LinkTransform = true
  LinkedObject = -> Link011 [1.$Element.]
  _Parent = -> Elements
FEATURE [Part::FeaturePython] _Element059  # link proxy (typed FeaturePython)
  Detach = false
  LinkTransform = true
  LinkedObject = -> Link015 [1.$Element001.]
  _Parent = -> Elements
FEATURE [Part::FeaturePython] _Element060  # link proxy (typed FeaturePython)
  Detach = false
  LinkTransform = true
  LinkedObject = -> Link011 [1.$Element001.]
  _Parent = -> Elements
FEATURE [Part::FeaturePython] Element008  # link proxy (typed FeaturePython)
  Detach = false
  LinkTransform = true
  LinkedObject = -> Body [Pocket001.Face11]
  _Parent = -> Elements001
FEATURE [Part::FeaturePython] _Element062  # link proxy (typed FeaturePython)
  Detach = false
  LinkTransform = true
  LinkedObject = -> Assembly001 [1.$Element008.]
  _Parent = -> Elements
FEATURE [Part::FeaturePython] Element012  # link proxy (typed FeaturePython)
  Detach = false
  LinkTransform = true
  LinkedObject = -> Body [Sketch013.Edge1]
  _Parent = -> Elements001
FEATURE [Part::FeaturePython] _Element066  # link proxy (typed FeaturePython)
  Detach = false
  LinkTransform = true
  LinkedObject = -> Assembly001 [1.$Element012.]
  _Parent = -> Elements
FEATURE [Part::FeaturePython] Element013  # link proxy (typed FeaturePython)
  Detach = false
  LinkTransform = true
  LinkedObject = -> Body [Pocket001.Face4]
  _Parent = -> Elements001
FEATURE [Part::FeaturePython] _Element067  # link proxy (typed FeaturePython)
  Detach = false
  LinkTransform = true
  LinkedObject = -> Assembly001 [1.$Element013.]
  _Parent = -> Elements
FEATURE [Part::FeaturePython] Element014  # link proxy (typed FeaturePython)
  Detach = false
  LinkTransform = true
  LinkedObject = -> Body [Pocket.Face4]
  _Parent = -> Elements001
FEATURE [Part::FeaturePython] _Element068  # link proxy (typed FeaturePython)
  Detach = false
  LinkTransform = true
  LinkedObject = -> Link016 [1.$Element014.]
  _Parent = -> Elements
FEATURE [Part::FeaturePython] Element015  # link proxy (typed FeaturePython)
  Detach = false
  LinkTransform = true
  LinkedObject = -> Body [Pocket.Face3]
  _Parent = -> Elements001
FEATURE [Part::FeaturePython] _Element069  # link proxy (typed FeaturePython)
  Detach = false
  LinkTransform = true
  LinkedObject = -> Link016 [1.$Element015.]
  _Parent = -> Elements
FEATURE [Part::FeaturePython] Element016  # link proxy (typed FeaturePython)
  Detach = false
  LinkTransform = true
  LinkedObject = -> Body [Pocket.Face1]
  _Parent = -> Elements001
FEATURE [Part::FeaturePython] _Element070  # link proxy (typed FeaturePython)
  Detach = false
  LinkTransform = true
  LinkedObject = -> Link016 [1.$Element016.]
  _Parent = -> Elements
FEATURE [Part::FeaturePython] _Element071  # link proxy (typed FeaturePython)
  Detach = false
  LinkTransform = true
  LinkedObject = -> Link [Face106]
  _Parent = -> Elements
FEATURE [Part::FeaturePython] _Element074  # link proxy (typed FeaturePython)
  Detach = false
  LinkTransform = true
  LinkedObject = -> Link [Face80]
  _Parent = -> Elements
FEATURE [Part::FeaturePython] _Element076  # link proxy (typed FeaturePython)
  Detach = false
  LinkTransform = true
  LinkedObject = -> Assembly001 [1.$Element014.]
  _Parent = -> Elements
FEATURE [Part::FeaturePython] Element017  # link proxy (typed FeaturePython)
  Detach = false
  LinkTransform = true
  LinkedObject = -> Body [Pocket.Face11]
  _Parent = -> Elements001
FEATURE [Part::FeaturePython] _Element077  # link proxy (typed FeaturePython)
  Detach = false
  LinkTransform = true
  LinkedObject = -> Link016 [1.$Element017.]
  _Parent = -> Elements
FEATURE [Part::FeaturePython] Element018  # link proxy (typed FeaturePython)
  Detach = false
  LinkTransform = true
  LinkedObject = -> Body001 [Pocket004.Face37]
  _Parent = -> Elements002
FEATURE [Part::FeaturePython] _Element083  # link proxy (typed FeaturePython)
  Detach = false
  LinkTransform = true
  LinkedObject = -> Assembly002 [1.$Element018.]
  _Parent = -> Elements
FEATURE [Part::FeaturePython] Element019  # link proxy (typed FeaturePython)
  Detach = false
  LinkTransform = true
  LinkedObject = -> Body003 [Pocket005.Face22]
  _Parent = -> Elements004
FEATURE [Part::FeaturePython] _Element084  # link proxy (typed FeaturePython)
  Detach = false
  LinkTransform = true
  LinkedObject = -> Assembly004 [1.$Element019.]
  _Parent = -> Elements
FEATURE [Part::FeaturePython] Element020  # link proxy (typed FeaturePython)
  Detach = false
  LinkTransform = true
  LinkedObject = -> Body003 [Sketch018.Vertex1]
  _Parent = -> Elements004
FEATURE [Part::FeaturePython] _Element085  # link proxy (typed FeaturePython)
  Detach = false
  LinkTransform = true
  LinkedObject = -> Assembly004 [1.$Element020.]
  _Parent = -> Elements
FEATURE [Part::FeaturePython] Element021  # link proxy (typed FeaturePython)
  Detach = false
  LinkTransform = true
  LinkedObject = -> Body001 [Pocket004.Face14]
  _Parent = -> Elements002
FEATURE [Part::FeaturePython] _Element086  # link proxy (typed FeaturePython)
  Detach = false
  LinkTransform = true
  LinkedObject = -> Assembly002 [1.$Element021.]
  _Parent = -> Elements
FEATURE [Part::FeaturePython] _Element087  # link proxy (typed FeaturePython)
  Detach = false
  LinkTransform = true
  LinkedObject = -> Link003 [Face2]
  _Parent = -> Elements
FEATURE [Part::FeaturePython] _Element088  # link proxy (typed FeaturePython)
  Detach = false
  LinkTransform = true
  LinkedObject = -> Workplane [Face1]
  _Parent = -> Elements
FEATURE [App::FeaturePython] Constraint  label="PlaneAlignment"  # WARN: FeaturePython — macro-defined, semantics opaque (R4)
  Angle = 0
  AnglePitch = 0
  AngleRoll = 0
  Cascade = false
  Disabled = false
  Group = -> [ElementLink,ElementLink001]
  LockAngle = false
  _ConstraintType = 37
  _Parent = -> Constraints
FEATURE [App::FeaturePython] ElementLink  label="_Element087"  # link proxy (typed FeaturePython)
  LinkTransform = true
  LinkedObject = -> _Element087
  _Parent = -> Constraint
FEATURE [App::FeaturePython] ElementLink001  label="_Element088"  # link proxy (typed FeaturePython)
  LinkTransform = true
  LinkedObject = -> _Element088
  _Parent = -> Constraint
FEATURE [Part::FeaturePython] _Element089  # link proxy (typed FeaturePython)
  Detach = false
  LinkTransform = true
  LinkedObject = -> Link003 [Vertex202]
  _Parent = -> Elements
FEATURE [Part::FeaturePython] _Element090  # link proxy (typed FeaturePython)
  Detach = false
  LinkTransform = true
  LinkedObject = -> Workplane [Edge2]
  _Parent = -> Elements
FEATURE [App::FeaturePython] Constraint001  label="PlaneAlignment001"  # WARN: FeaturePython — macro-defined, semantics opaque (R4)
  Angle = 0
  AnglePitch = 0
  AngleRoll = 0
  Cascade = false
  Disabled = false
  Group = -> [ElementLink002,ElementLink003]
  LockAngle = false
  _ConstraintType = 37
  _Parent = -> Constraints
FEATURE [App::FeaturePython] ElementLink002  label="_Element011"  # link proxy (typed FeaturePython)
  LinkTransform = true
  LinkedObject = -> _Element011
  _Parent = -> Constraint001
FEATURE [App::FeaturePython] ElementLink003  label="_Element091"  # link proxy (typed FeaturePython)
  LinkTransform = true
  LinkedObject = -> _Element091
  _Parent = -> Constraint001
FEATURE [Part::FeaturePython] _Element091  # link proxy (typed FeaturePython)
  Detach = false
  LinkTransform = true
  LinkedObject = -> Workplane001 [Face1]
  _Parent = -> Elements
FEATURE [App::FeaturePython] Constraint002  label="PlaneAlignment002"  # WARN: FeaturePython — macro-defined, semantics opaque (R4)
  Angle = 0
  AnglePitch = 0
  AngleRoll = 0
  Cascade = false
  Disabled = false
  Group = -> [ElementLink004,ElementLink005]
  LockAngle = false
  _ConstraintType = 37
  _Parent = -> Constraints
FEATURE [App::FeaturePython] ElementLink004  label="_Element038"  # link proxy (typed FeaturePython)
  LinkTransform = true
  LinkedObject = -> _Element038
  _Parent = -> Constraint002
FEATURE [App::FeaturePython] ElementLink005  label="_Element092"  # link proxy (typed FeaturePython)
  LinkTransform = true
  LinkedObject = -> _Element092
  _Parent = -> Constraint002
FEATURE [Part::FeaturePython] _Element092  # link proxy (typed FeaturePython)
  Detach = false
  LinkTransform = true
  LinkedObject = -> Workplane002 [Face1]
  _Parent = -> Elements
FEATURE [App::FeaturePython] Constraint003  label="PlaneAlignment003"  # WARN: FeaturePython — macro-defined, semantics opaque (R4)
  Angle = 0
  AnglePitch = 0
  AngleRoll = 0
  Cascade = false
  Disabled = false
  Group = -> [ElementLink006,ElementLink007]
  LockAngle = false
  _ConstraintType = 37
  _Parent = -> Constraints
FEATURE [App::FeaturePython] ElementLink006  label="_Element010"  # link proxy (typed FeaturePython)
  LinkTransform = true
  LinkedObject = -> _Element010
  _Parent = -> Constraint003
FEATURE [App::FeaturePython] ElementLink007  label="_Element011"  # link proxy (typed FeaturePython)
  LinkTransform = true
  LinkedObject = -> _Element011
  _Parent = -> Constraint003
FEATURE [App::FeaturePython] Constraint004  label="PlaneAlignment004"  # WARN: FeaturePython — macro-defined, semantics opaque (R4)
  Angle = 0
  AnglePitch = 0
  AngleRoll = 0
  Cascade = false
  Disabled = false
  Group = -> [ElementLink008,ElementLink009]
  LockAngle = false
  _ConstraintType = 37
  _Parent = -> Constraints
FEATURE [App::FeaturePython] ElementLink008  label="_Element002"  # link proxy (typed FeaturePython)
  LinkTransform = true
  LinkedObject = -> _Element002
  _Parent = -> Constraint004
FEATURE [App::FeaturePython] ElementLink009  label="_Element"  # link proxy (typed FeaturePython)
  LinkTransform = true
  LinkedObject = -> _Element
  _Parent = -> Constraint004
FEATURE [App::FeaturePython] Constraint005  label="PlaneAlignment005"  # WARN: FeaturePython — macro-defined, semantics opaque (R4)
  Angle = 0
  AnglePitch = 0
  AngleRoll = 0
  Cascade = false
  Disabled = false
  Group = -> [ElementLink010,ElementLink011]
  LockAngle = false
  _ConstraintType = 37
  _Parent = -> Constraints
FEATURE [App::FeaturePython] ElementLink010  label="_Element029"  # link proxy (typed FeaturePython)
  LinkTransform = true
  LinkedObject = -> _Element029
  _Parent = -> Constraint005
FEATURE [App::FeaturePython] ElementLink011  label="_Element093"  # link proxy (typed FeaturePython)
  LinkTransform = true
  LinkedObject = -> _Element093
  _Parent = -> Constraint005
FEATURE [Part::FeaturePython] _Element093  # link proxy (typed FeaturePython)
  Detach = false
  LinkTransform = true
  LinkedObject = -> Link003 [Face4]
  _Parent = -> Elements
FEATURE [App::FeaturePython] Constraint006  label="PlaneAlignment006"  # WARN: FeaturePython — macro-defined, semantics opaque (R4)
  Angle = 0
  AnglePitch = 0
  AngleRoll = 0
  Cascade = false
  Disabled = false
  Group = -> [ElementLink012,ElementLink013]
  LockAngle = false
  _ConstraintType = 37
  _Parent = -> Constraints
FEATURE [App::FeaturePython] ElementLink012  label="_Element094"  # link proxy (typed FeaturePython)
  LinkTransform = true
  LinkedObject = -> _Element094
  _Parent = -> Constraint006
FEATURE [Part::FeaturePython] _Element094  # link proxy (typed FeaturePython)
  Detach = false
  LinkTransform = true
  LinkedObject = -> Link [Face2]
  _Parent = -> Elements
FEATURE [App::FeaturePython] ElementLink013  label="_Element093"  # link proxy (typed FeaturePython)
  LinkTransform = true
  LinkedObject = -> _Element093
  _Parent = -> Constraint006
FEATURE [Part::FeaturePython] _Element095  # link proxy (typed FeaturePython)
  Detach = false
  LinkTransform = true
  LinkedObject = -> Link003 [Face113]
  _Parent = -> Elements
FEATURE [App::FeaturePython] Constraint008  label="PlaneAlignment007"  # WARN: FeaturePython — macro-defined, semantics opaque (R4)
  Angle = 0
  AnglePitch = 0
  AngleRoll = 0
  Cascade = false
  Disabled = false
  Group = -> [ElementLink016,ElementLink017]
  LockAngle = false
  _ConstraintType = 37
  _Parent = -> Constraints
FEATURE [App::FeaturePython] ElementLink016  label="_Element006"  # link proxy (typed FeaturePython)
  LinkTransform = true
  LinkedObject = -> _Element006
  _Parent = -> Constraint008
FEATURE [App::FeaturePython] ElementLink017  label="_Element"  # link proxy (typed FeaturePython)
  LinkTransform = true
  LinkedObject = -> _Element
  _Parent = -> Constraint008
FEATURE [App::FeaturePython] Constraint009  label="PlaneAlignment008"  # WARN: FeaturePython — macro-defined, semantics opaque (R4)
  Angle = 0
  AnglePitch = 0
  AngleRoll = 0
  Cascade = false
  Disabled = false
  Group = -> [ElementLink018,ElementLink019]
  LockAngle = false
  _ConstraintType = 37
  _Parent = -> Constraints
FEATURE [App::FeaturePython] ElementLink018  label="_Element"  # link proxy (typed FeaturePython)
  LinkTransform = true
  LinkedObject = -> _Element
  _Parent = -> Constraint009
FEATURE [App::FeaturePython] ElementLink019  label="_Element001"  # link proxy (typed FeaturePython)
  LinkTransform = true
  LinkedObject = -> _Element001
  _Parent = -> Constraint009
FEATURE [App::FeaturePython] Constraint010  label="PlaneAlignment009"  # WARN: FeaturePython — macro-defined, semantics opaque (R4)
  Angle = 0
  AnglePitch = 0
  AngleRoll = 0
  Cascade = false
  Disabled = false
  Group = -> [ElementLink020,ElementLink021]
  LockAngle = false
  _ConstraintType = 37
  _Parent = -> Constraints
FEATURE [App::FeaturePython] ElementLink020  label="_Element022"  # link proxy (typed FeaturePython)
  LinkTransform = true
  LinkedObject = -> _Element022
  _Parent = -> Constraint010
FEATURE [App::FeaturePython] ElementLink021  label="_Element093"  # link proxy (typed FeaturePython)
  LinkTransform = true
  LinkedObject = -> _Element093
  _Parent = -> Constraint010
FEATURE [App::FeaturePython] Constraint011  label="PlaneAlignment010"  # WARN: FeaturePython — macro-defined, semantics opaque (R4)
  Angle = 0
  AnglePitch = 0
  AngleRoll = 0
  Cascade = false
  Disabled = false
  Group = -> [ElementLink022,ElementLink023]
  LockAngle = false
  _ConstraintType = 37
  _Parent = -> Constraints
FEATURE [App::FeaturePython] ElementLink022  label="_Element009"  # link proxy (typed FeaturePython)
  LinkTransform = true
  LinkedObject = -> _Element009
  _Parent = -> Constraint011
FEATURE [App::FeaturePython] ElementLink023  label="_Element008"  # link proxy (typed FeaturePython)
  LinkTransform = true
  LinkedObject = -> _Element008
  _Parent = -> Constraint011
FEATURE [App::FeaturePython] Constraint012  label="PlaneAlignment011"  # WARN: FeaturePython — macro-defined, semantics opaque (R4)
  Angle = 0
  AnglePitch = 0
  AngleRoll = 0
  Cascade = false
  Disabled = false
  Group = -> [ElementLink024,ElementLink025]
  LockAngle = false
  _ConstraintType = 37
  _Parent = -> Constraints
FEATURE [App::FeaturePython] ElementLink024  label="_Element013"  # link proxy (typed FeaturePython)
  LinkTransform = true
  LinkedObject = -> _Element013
  _Parent = -> Constraint012
FEATURE [App::FeaturePython] ElementLink025  label="_Element014"  # link proxy (typed FeaturePython)
  LinkTransform = true
  LinkedObject = -> _Element014
  _Parent = -> Constraint012
FEATURE [App::FeaturePython] Constraint013  label="PlaneAlignment012"  # WARN: FeaturePython — macro-defined, semantics opaque (R4)
  Angle = 0
  AnglePitch = 0
  AngleRoll = 0
  Cascade = false
  Disabled = false
  Group = -> [ElementLink026,ElementLink027]
  LockAngle = false
  _ConstraintType = 37
  _Parent = -> Constraints
FEATURE [App::FeaturePython] ElementLink026  label="_Element010"  # link proxy (typed FeaturePython)
  LinkTransform = true
  LinkedObject = -> _Element010
  _Parent = -> Constraint013
FEATURE [App::FeaturePython] ElementLink027  label="_Element015"  # link proxy (typed FeaturePython)
  LinkTransform = true
  LinkedObject = -> _Element015
  _Parent = -> Constraint013
FEATURE [App::FeaturePython] Constraint014  label="PlaneAlignment013"  # WARN: FeaturePython — macro-defined, semantics opaque (R4)
  Angle = 0
  AnglePitch = 0
  AngleRoll = 0
  Cascade = false
  Disabled = false
  Group = -> [ElementLink028,ElementLink029]
  LockAngle = false
  _ConstraintType = 37
  _Parent = -> Constraints
FEATURE [App::FeaturePython] ElementLink028  label="_Element096"  # link proxy (typed FeaturePython)
  LinkTransform = true
  LinkedObject = -> _Element096
  _Parent = -> Constraint014
FEATURE [Part::FeaturePython] _Element096  # link proxy (typed FeaturePython)
  Detach = false
  LinkTransform = true
  LinkedObject = -> Link004 [Face4]
  _Parent = -> Elements
FEATURE [App::FeaturePython] ElementLink029  label="_Element029"  # link proxy (typed FeaturePython)
  LinkTransform = true
  LinkedObject = -> _Element029
  _Parent = -> Constraint014
FEATURE [App::FeaturePython] Constraint015  label="PlaneAlignment014"  # WARN: FeaturePython — macro-defined, semantics opaque (R4)
  Angle = 0
  AnglePitch = 0
  AngleRoll = 0
  Cascade = false
  Disabled = false
  Group = -> [ElementLink030,ElementLink031]
  LockAngle = false
  _ConstraintType = 37
  _Parent = -> Constraints
FEATURE [App::FeaturePython] ElementLink030  label="_Element021"  # link proxy (typed FeaturePython)
  LinkTransform = true
  LinkedObject = -> _Element021
  _Parent = -> Constraint015
FEATURE [App::FeaturePython] ElementLink031  label="_Element088"  # link proxy (typed FeaturePython)
  LinkTransform = true
  LinkedObject = -> _Element088
  _Parent = -> Constraint015
FEATURE [App::FeaturePython] Constraint016  label="PlaneAlignment015"  # WARN: FeaturePython — macro-defined, semantics opaque (R4)
  Angle = 0
  AnglePitch = 0
  AngleRoll = 0
  Cascade = false
  Disabled = false
  Group = -> [ElementLink032,ElementLink033]
  LockAngle = false
  _ConstraintType = 37
  _Parent = -> Constraints
FEATURE [App::FeaturePython] ElementLink032  label="_Element019"  # link proxy (typed FeaturePython)
  LinkTransform = true
  LinkedObject = -> _Element019
  _Parent = -> Constraint016
FEATURE [App::FeaturePython] ElementLink033  label="_Element088"  # link proxy (typed FeaturePython)
  LinkTransform = true
  LinkedObject = -> _Element088
  _Parent = -> Constraint016
FEATURE [Part::FeaturePython] Element022  # link proxy (typed FeaturePython)
  Detach = false
  LinkTransform = true
  LinkedObject = -> Body [Pocket001.Face1]
  _Parent = -> Elements001
FEATURE [Part::FeaturePython] _Element097  # link proxy (typed FeaturePython)
  Detach = false
  LinkTransform = true
  LinkedObject = -> Assembly001 [1.$Element022.]
  _Parent = -> Elements
FEATURE [App::FeaturePython] Constraint018  label="PlaneAlignment017"  # WARN: FeaturePython — macro-defined, semantics opaque (R4)
  Angle = 0
  AnglePitch = 0
  AngleRoll = 0
  Cascade = false
  Disabled = false
  Group = -> [ElementLink036,ElementLink037]
  LockAngle = false
  _ConstraintType = 37
  _Parent = -> Constraints
FEATURE [App::FeaturePython] ElementLink036  label="_Element010"  # link proxy (typed FeaturePython)
  LinkTransform = true
  LinkedObject = -> _Element010
  _Parent = -> Constraint018
FEATURE [App::FeaturePython] ElementLink037  label="_Element098"  # link proxy (typed FeaturePython)
  LinkTransform = true
  LinkedObject = -> _Element098
  _Parent = -> Constraint018
FEATURE [Part::FeaturePython] Element023  # link proxy (typed FeaturePython)
  Detach = false
  LinkTransform = true
  LinkedObject = -> Body [Pocket001.Face2]
  _Parent = -> Elements001
FEATURE [Part::FeaturePython] _Element098  # link proxy (typed FeaturePython)
  Detach = false
  LinkTransform = true
  LinkedObject = -> Assembly001 [1.$Element023.]
  _Parent = -> Elements
FEATURE [App::FeaturePython] Constraint021  label="AxialAlignment001"  # WARN: FeaturePython — macro-defined, semantics opaque (R4)
  Angle = 0
  AnglePitch = 0
  AngleRoll = 0
  Disabled = false
  Group = -> [ElementLink042,ElementLink043]
  LockAngle = false
  Multiply = false
  _ConstraintType = 36
  _Parent = -> Constraints
FEATURE [App::FeaturePython] ElementLink042  label="_Element083"  # link proxy (typed FeaturePython)
  LinkTransform = true
  LinkedObject = -> _Element083
  _Parent = -> Constraint021
FEATURE [App::FeaturePython] ElementLink043  label="_Element084"  # link proxy (typed FeaturePython)
  LinkTransform = true
  LinkedObject = -> _Element084
  _Parent = -> Constraint021
FEATURE [Part::FeaturePython] Element024  # link proxy (typed FeaturePython)
  Detach = false
  LinkTransform = true
  LinkedObject = -> Body003 [Pocket005.Face2]
  _Parent = -> Elements004
FEATURE [Part::FeaturePython] _Element099  # link proxy (typed FeaturePython)
  Detach = false
  LinkTransform = true
  LinkedObject = -> Assembly004 [1.$Element024.]
  _Parent = -> Elements
FEATURE [Part::FeaturePython] Element025  # link proxy (typed FeaturePython)
  Detach = false
  LinkTransform = true
  LinkedObject = -> Body001 [Pocket004.Face2]
  _Parent = -> Elements002
FEATURE [Part::FeaturePython] _Element100  # link proxy (typed FeaturePython)
  Detach = false
  LinkTransform = true
  LinkedObject = -> Assembly002 [1.$Element025.]
  _Parent = -> Elements
FEATURE [App::FeaturePython] Constraint023  label="PlaneAlignment019"  # WARN: FeaturePython — macro-defined, semantics opaque (R4)
  Angle = 0
  AnglePitch = 0
  AngleRoll = 0
  Cascade = false
  Disabled = false
  Group = -> [ElementLink046,ElementLink047]
  LockAngle = false
  _ConstraintType = 37
  _Parent = -> Constraints
FEATURE [App::FeaturePython] ElementLink046  label="_Element101"  # link proxy (typed FeaturePython)
  LinkTransform = true
  LinkedObject = -> _Element101
  _Parent = -> Constraint023
FEATURE [Part::FeaturePython] Element026  # link proxy (typed FeaturePython)
  Detach = false
  LinkTransform = true
  LinkedObject = -> Body003 [Pocket005.Face19]
  _Parent = -> Elements004
FEATURE [Part::FeaturePython] _Element101  # link proxy (typed FeaturePython)
  Detach = false
  LinkTransform = true
  LinkedObject = -> Assembly004 [1.$Element026.]
  _Parent = -> Elements
FEATURE [App::FeaturePython] ElementLink047  label="_Element102"  # link proxy (typed FeaturePython)
  LinkTransform = true
  LinkedObject = -> _Element102
  _Parent = -> Constraint023
FEATURE [Part::FeaturePython] Element027  # link proxy (typed FeaturePython)
  Detach = false
  LinkTransform = true
  LinkedObject = -> Body001 [Pocket004.Face31]
  _Parent = -> Elements002
FEATURE [Part::FeaturePython] _Element102  # link proxy (typed FeaturePython)
  Detach = false
  LinkTransform = true
  LinkedObject = -> Assembly002 [1.$Element027.]
  _Parent = -> Elements
FEATURE [Part::FeaturePython] Element028  # link proxy (typed FeaturePython)
  Detach = false
  LinkTransform = true
  LinkedObject = -> Body001 [Pocket004.Face3]
  _Parent = -> Elements002
FEATURE [Part::FeaturePython] _Element103  # link proxy (typed FeaturePython)
  Detach = false
  LinkTransform = true
  LinkedObject = -> Assembly002 [1.$Element028.]
  _Parent = -> Elements
FEATURE [Part::FeaturePython] Element029  # link proxy (typed FeaturePython)
  Detach = false
  LinkTransform = true
  LinkedObject = -> Body003 [Pocket005.Face3]
  _Parent = -> Elements004
FEATURE [Part::FeaturePython] _Element104  # link proxy (typed FeaturePython)
  Detach = false
  LinkTransform = true
  LinkedObject = -> Assembly004 [1.$Element029.]
  _Parent = -> Elements
FEATURE [App::FeaturePython] Constraint027  label="PlaneAlignment022"  # WARN: FeaturePython — macro-defined, semantics opaque (R4)
  Angle = 0
  AnglePitch = 0
  AngleRoll = 0
  Cascade = false
  Disabled = false
  Group = -> [ElementLink054,ElementLink055]
  LockAngle = false
  _ConstraintType = 37
  _Parent = -> Constraints
FEATURE [App::FeaturePython] ElementLink054  label="_Element108"  # link proxy (typed FeaturePython)
  LinkTransform = true
  LinkedObject = -> _Element108
  _Parent = -> Constraint027
FEATURE [Part::FeaturePython] _Element108  # link proxy (typed FeaturePython)
  Detach = false
  LinkTransform = true
  LinkedObject = -> Link016 [1.$Element022.]
  _Parent = -> Elements
FEATURE [App::FeaturePython] ElementLink055  label="_Element007"  # link proxy (typed FeaturePython)
  LinkTransform = true
  LinkedObject = -> _Element007
  _Parent = -> Constraint027
FEATURE [App::FeaturePython] Constraint028  label="PlaneAlignment023"  # WARN: FeaturePython — macro-defined, semantics opaque (R4)
  Angle = 0
  AnglePitch = 0
  AngleRoll = 0
  Cascade = false
  Disabled = false
  Group = -> [ElementLink056,ElementLink057]
  LockAngle = false
  _ConstraintType = 37
  _Parent = -> Constraints
FEATURE [App::FeaturePython] ElementLink056  label="_Element109"  # link proxy (typed FeaturePython)
  LinkTransform = true
  LinkedObject = -> _Element109
  _Parent = -> Constraint028
FEATURE [Part::FeaturePython] _Element109  # link proxy (typed FeaturePython)
  Detach = false
  LinkTransform = true
  LinkedObject = -> Link016 [1.$Element023.]
  _Parent = -> Elements
FEATURE [App::FeaturePython] ElementLink057  label="_Element110"  # link proxy (typed FeaturePython)
  LinkTransform = true
  LinkedObject = -> _Element110
  _Parent = -> Constraint028
FEATURE [Part::FeaturePython] _Element110  # link proxy (typed FeaturePython)
  Detach = false
  LinkTransform = true
  LinkedObject = -> Link002 [Face50]
  _Parent = -> Elements
FEATURE [Part::FeaturePython] _Element111  # link proxy (typed FeaturePython)
  Detach = false
  LinkTransform = true
  LinkedObject = -> Link016 [1.$Element008.]
  _Parent = -> Elements
FEATURE [Part::FeaturePython] Assembly005  label="assy_door_back-right"  # WARN: FeaturePython — macro-defined, semantics opaque (R4)
  AutoRelax = true
  BuildShape = 0
  Freeze = false
  Group = -> [Constraints005,Elements005,Parts005]
  Placement = pos=(30.1404,-405.959,-103.163) rot=(-1,0,0;0.295782rad)
  Verbose = false
  _SolverType = 1
  _Version = 1
FEATURE [App::FeaturePython] Elements005  # WARN: FeaturePython — macro-defined, semantics opaque (R4)
  Group = -> [Element030,Element032,Element033,Element038,Element040,Element041]
FEATURE [Part::FeaturePython] Element030  # link proxy (typed FeaturePython)
  Detach = false
  LinkTransform = true
  LinkedObject = -> Part__Mirroring [Face14]
  _Parent = -> Elements005
FEATURE [Part::FeaturePython] _Element112  # link proxy (typed FeaturePython)
  Detach = false
  LinkTransform = true
  LinkedObject = -> Assembly005 [1.$Element030.]
  _Parent = -> Elements
FEATURE [Part::FeaturePython] Assembly006  label="assy_door_front-right"  # WARN: FeaturePython — macro-defined, semantics opaque (R4)
  AutoRelax = true
  BuildShape = 0
  Freeze = false
  Group = -> [Constraints006,Elements006,Parts006]
  Placement = pos=(393.14,-397.513,57.0842) rot=(1,0,0;0.92781rad)
  Verbose = false
  _SolverType = 1
  _Version = 1
FEATURE [App::FeaturePython] Elements006  # WARN: FeaturePython — macro-defined, semantics opaque (R4)
  Group = -> [Element031,Element034]
FEATURE [Part::FeaturePython] Element031  # link proxy (typed FeaturePython)
  Detach = false
  LinkTransform = true
  LinkedObject = -> Part__Mirroring001 [Face22]
  _Parent = -> Elements006
FEATURE [Part::FeaturePython] _Element113  # link proxy (typed FeaturePython)
  Detach = false
  LinkTransform = true
  LinkedObject = -> Assembly006 [1.$Element031.]
  _Parent = -> Elements
FEATURE [Part::FeaturePython] Element032  # link proxy (typed FeaturePython)
  Detach = false
  LinkTransform = true
  LinkedObject = -> Part__Mirroring [Face37]
  _Parent = -> Elements005
FEATURE [Part::FeaturePython] _Element114  # link proxy (typed FeaturePython)
  Detach = false
  LinkTransform = true
  LinkedObject = -> Assembly005 [1.$Element032.]
  _Parent = -> Elements
FEATURE [Part::FeaturePython] Element033  # link proxy (typed FeaturePython)
  Detach = false
  LinkTransform = true
  LinkedObject = -> Part__Mirroring [Face31]
  _Parent = -> Elements005
FEATURE [Part::FeaturePython] _Element115  # link proxy (typed FeaturePython)
  Detach = false
  LinkTransform = true
  LinkedObject = -> Assembly005 [1.$Element033.]
  _Parent = -> Elements
FEATURE [Part::FeaturePython] Element034  # link proxy (typed FeaturePython)
  Detach = false
  LinkTransform = true
  LinkedObject = -> Part__Mirroring001 [Face19]
  _Parent = -> Elements006
FEATURE [Part::FeaturePython] _Element116  # link proxy (typed FeaturePython)
  Detach = false
  LinkTransform = true
  LinkedObject = -> Assembly006 [1.$Element034.]
  _Parent = -> Elements
FEATURE [App::FeaturePython] Constraint033  label="PlaneAlignment025"  # WARN: FeaturePython — macro-defined, semantics opaque (R4)
  Angle = 0
  AnglePitch = 0
  AngleRoll = 0
  Cascade = false
  Disabled = false
  Group = -> [ElementLink066,ElementLink067]
  LockAngle = false
  _ConstraintType = 37
  _Parent = -> Constraints
FEATURE [App::FeaturePython] ElementLink066  label="_Element028"  # link proxy (typed FeaturePython)
  LinkTransform = true
  LinkedObject = -> _Element028
  _Parent = -> Constraint033
FEATURE [App::FeaturePython] ElementLink067  label="_Element010"  # link proxy (typed FeaturePython)
  LinkTransform = true
  LinkedObject = -> _Element010
  _Parent = -> Constraint033
FEATURE [App::FeaturePython] Constraint034  label="PlaneAlignment026"  # WARN: FeaturePython — macro-defined, semantics opaque (R4)
  Angle = 0
  AnglePitch = 0
  AngleRoll = 0
  Cascade = false
  Disabled = false
  Group = -> [ElementLink068,ElementLink069]
  LockAngle = false
  _ConstraintType = 37
  _Parent = -> Constraints
FEATURE [App::FeaturePython] ElementLink068  label="_Element026"  # link proxy (typed FeaturePython)
  LinkTransform = true
  LinkedObject = -> _Element026
  _Parent = -> Constraint034
FEATURE [App::FeaturePython] ElementLink069  label="_Element029"  # link proxy (typed FeaturePython)
  LinkTransform = true
  LinkedObject = -> _Element029
  _Parent = -> Constraint034
FEATURE [App::FeaturePython] Constraint035  label="PlaneAlignment027"  # WARN: FeaturePython — macro-defined, semantics opaque (R4)
  Angle = 0
  AnglePitch = 0
  AngleRoll = 0
  Cascade = false
  Disabled = false
  Group = -> [ElementLink070,ElementLink071]
  LockAngle = false
  _ConstraintType = 37
  _Parent = -> Constraints
FEATURE [App::FeaturePython] ElementLink070  label="_Element032"  # link proxy (typed FeaturePython)
  LinkTransform = true
  LinkedObject = -> _Element032
  _Parent = -> Constraint035
FEATURE [App::FeaturePython] ElementLink071  label="_Element029"  # link proxy (typed FeaturePython)
  LinkTransform = true
  LinkedObject = -> _Element029
  _Parent = -> Constraint035
FEATURE [App::FeaturePython] Constraint036  label="PlaneAlignment028"  # WARN: FeaturePython — macro-defined, semantics opaque (R4)
  Angle = 0
  AnglePitch = 0
  AngleRoll = 0
  Cascade = false
  Disabled = false
  Group = -> [ElementLink072,ElementLink073]
  LockAngle = false
  _ConstraintType = 37
  _Parent = -> Constraints
FEATURE [App::FeaturePython] ElementLink072  label="_Element033"  # link proxy (typed FeaturePython)
  LinkTransform = true
  LinkedObject = -> _Element033
  _Parent = -> Constraint036
FEATURE [App::FeaturePython] ElementLink073  label="_Element010"  # link proxy (typed FeaturePython)
  LinkTransform = true
  LinkedObject = -> _Element010
  _Parent = -> Constraint036
FEATURE [App::FeaturePython] Constraint037  label="PlaneAlignment029"  # WARN: FeaturePython — macro-defined, semantics opaque (R4)
  Angle = 0
  AnglePitch = 0
  AngleRoll = 0
  Cascade = false
  Disabled = false
  Group = -> [ElementLink074,ElementLink075]
  LockAngle = false
  _ConstraintType = 37
  _Parent = -> Constraints
FEATURE [App::FeaturePython] ElementLink074  label="_Element027"  # link proxy (typed FeaturePython)
  LinkTransform = true
  LinkedObject = -> _Element027
  _Parent = -> Constraint037
FEATURE [App::FeaturePython] ElementLink075  label="_Element010"  # link proxy (typed FeaturePython)
  LinkTransform = true
  LinkedObject = -> _Element010
  _Parent = -> Constraint037
FEATURE [App::FeaturePython] Constraint038  label="PlaneAlignment030"  # WARN: FeaturePython — macro-defined, semantics opaque (R4)
  Angle = 0
  AnglePitch = 0
  AngleRoll = 0
  Cascade = false
  Disabled = false
  Group = -> [ElementLink076,ElementLink077]
  LockAngle = false
  _ConstraintType = 37
  _Parent = -> Constraints
FEATURE [App::FeaturePython] ElementLink076  label="_Element053"  # link proxy (typed FeaturePython)
  LinkTransform = true
  LinkedObject = -> _Element053
  _Parent = -> Constraint038
FEATURE [App::FeaturePython] ElementLink077  label="_Element023"  # link proxy (typed FeaturePython)
  LinkTransform = true
  LinkedObject = -> _Element023
  _Parent = -> Constraint038
FEATURE [App::FeaturePython] Constraint039  label="PlaneAlignment031"  # WARN: FeaturePython — macro-defined, semantics opaque (R4)
  Angle = 0
  AnglePitch = 0
  AngleRoll = 0
  Cascade = false
  Disabled = false
  Group = -> [ElementLink078,ElementLink079]
  LockAngle = false
  _ConstraintType = 37
  _Parent = -> Constraints
FEATURE [App::FeaturePython] ElementLink078  label="_Element030"  # link proxy (typed FeaturePython)
  LinkTransform = true
  LinkedObject = -> _Element030
  _Parent = -> Constraint039
FEATURE [App::FeaturePython] ElementLink079  label="_Element031"  # link proxy (typed FeaturePython)
  LinkTransform = true
  LinkedObject = -> _Element031
  _Parent = -> Constraint039
FEATURE [App::FeaturePython] Constraint040  label="PlaneAlignment032"  # WARN: FeaturePython — macro-defined, semantics opaque (R4)
  Angle = 0
  AnglePitch = 0
  AngleRoll = 0
  Cascade = false
  Disabled = false
  Group = -> [ElementLink080,ElementLink081]
  LockAngle = false
  _ConstraintType = 37
  _Parent = -> Constraints
FEATURE [App::FeaturePython] ElementLink080  label="_Element025"  # link proxy (typed FeaturePython)
  LinkTransform = true
  LinkedObject = -> _Element025
  _Parent = -> Constraint040
FEATURE [App::FeaturePython] ElementLink081  label="_Element029"  # link proxy (typed FeaturePython)
  LinkTransform = true
  LinkedObject = -> _Element029
  _Parent = -> Constraint040
FEATURE [App::FeaturePython] Constraint041  label="PlaneAlignment033"  # WARN: FeaturePython — macro-defined, semantics opaque (R4)
  Angle = 0
  AnglePitch = 0
  AngleRoll = 0
  Cascade = false
  Disabled = false
  Group = -> [ElementLink082,ElementLink083]
  LockAngle = false
  _ConstraintType = 37
  _Parent = -> Constraints
FEATURE [App::FeaturePython] ElementLink082  label="_Element055"  # link proxy (typed FeaturePython)
  LinkTransform = true
  LinkedObject = -> _Element055
  _Parent = -> Constraint041
FEATURE [App::FeaturePython] ElementLink083  label="_Element027"  # link proxy (typed FeaturePython)
  LinkTransform = true
  LinkedObject = -> _Element027
  _Parent = -> Constraint041
FEATURE [App::FeaturePython] Constraint042  label="PlaneAlignment034"  # WARN: FeaturePython — macro-defined, semantics opaque (R4)
  Angle = 0
  AnglePitch = 0
  AngleRoll = 0
  Cascade = false
  Disabled = false
  Group = -> [ElementLink084,ElementLink085]
  LockAngle = false
  _ConstraintType = 37
  _Parent = -> Constraints
FEATURE [App::FeaturePython] ElementLink084  label="_Element054"  # link proxy (typed FeaturePython)
  LinkTransform = true
  LinkedObject = -> _Element054
  _Parent = -> Constraint042
FEATURE [App::FeaturePython] ElementLink085  label="_Element053"  # link proxy (typed FeaturePython)
  LinkTransform = true
  LinkedObject = -> _Element053
  _Parent = -> Constraint042
FEATURE [App::FeaturePython] Constraint043  label="PlaneAlignment035"  # WARN: FeaturePython — macro-defined, semantics opaque (R4)
  Angle = 0
  AnglePitch = 0
  AngleRoll = 0
  Cascade = false
  Disabled = false
  Group = -> [ElementLink086,ElementLink087]
  LockAngle = false
  _ConstraintType = 37
  _Parent = -> Constraints
FEATURE [App::FeaturePython] ElementLink086  label="_Element045"  # link proxy (typed FeaturePython)
  LinkTransform = true
  LinkedObject = -> _Element045
  _Parent = -> Constraint043
FEATURE [App::FeaturePython] ElementLink087  label="_Element009"  # link proxy (typed FeaturePython)
  LinkTransform = true
  LinkedObject = -> _Element009
  _Parent = -> Constraint043
FEATURE [App::FeaturePython] Constraint044  label="PlaneAlignment036"  # WARN: FeaturePython — macro-defined, semantics opaque (R4)
  Angle = 0
  AnglePitch = 0
  AngleRoll = 0
  Cascade = false
  Disabled = false
  Group = -> [ElementLink088,ElementLink089]
  LockAngle = false
  _ConstraintType = 37
  _Parent = -> Constraints
FEATURE [App::FeaturePython] ElementLink088  label="_Element117"  # link proxy (typed FeaturePython)
  LinkTransform = true
  LinkedObject = -> _Element117
  _Parent = -> Constraint044
FEATURE [Part::FeaturePython] _Element117  # link proxy (typed FeaturePython)
  Detach = false
  LinkTransform = true
  LinkedObject = -> Link013 [Face39]
  _Parent = -> Elements
FEATURE [App::FeaturePython] ElementLink089  label="_Element052"  # link proxy (typed FeaturePython)
  LinkTransform = true
  LinkedObject = -> _Element052
  _Parent = -> Constraint044
FEATURE [App::FeaturePython] Constraint045  label="PlaneAlignment037"  # WARN: FeaturePython — macro-defined, semantics opaque (R4)
  Angle = 0
  AnglePitch = 0
  AngleRoll = 0
  Cascade = false
  Disabled = false
  Group = -> [ElementLink090,ElementLink091]
  LockAngle = false
  _ConstraintType = 37
  _Parent = -> Constraints
FEATURE [App::FeaturePython] ElementLink090  label="_Element048"  # link proxy (typed FeaturePython)
  LinkTransform = true
  LinkedObject = -> _Element048
  _Parent = -> Constraint045
FEATURE [App::FeaturePython] ElementLink091  label="_Element118"  # link proxy (typed FeaturePython)
  LinkTransform = true
  LinkedObject = -> _Element118
  _Parent = -> Constraint045
FEATURE [Part::FeaturePython] _Element118  # link proxy (typed FeaturePython)
  Detach = false
  LinkTransform = true
  LinkedObject = -> Link012 [Face80]
  _Parent = -> Elements
FEATURE [App::FeaturePython] Constraint046  label="PlaneAlignment038"  # WARN: FeaturePython — macro-defined, semantics opaque (R4)
  Angle = 0
  AnglePitch = 0
  AngleRoll = 0
  Cascade = false
  Disabled = false
  Group = -> [ElementLink092,ElementLink093]
  LockAngle = false
  _ConstraintType = 37
  _Parent = -> Constraints
FEATURE [App::FeaturePython] ElementLink092  label="_Element050"  # link proxy (typed FeaturePython)
  LinkTransform = true
  LinkedObject = -> _Element050
  _Parent = -> Constraint046
FEATURE [App::FeaturePython] ElementLink093  label="_Element009"  # link proxy (typed FeaturePython)
  LinkTransform = true
  LinkedObject = -> _Element009
  _Parent = -> Constraint046
FEATURE [App::FeaturePython] Constraint047  label="PlaneAlignment039"  # WARN: FeaturePython — macro-defined, semantics opaque (R4)
  Angle = 0
  AnglePitch = 0
  AngleRoll = 0
  Cascade = false
  Disabled = false
  Group = -> [ElementLink094,ElementLink095]
  LockAngle = false
  _ConstraintType = 37
  _Parent = -> Constraints
FEATURE [App::FeaturePython] ElementLink094  label="_Element051"  # link proxy (typed FeaturePython)
  LinkTransform = true
  LinkedObject = -> _Element051
  _Parent = -> Constraint047
FEATURE [App::FeaturePython] ElementLink095  label="_Element052"  # link proxy (typed FeaturePython)
  LinkTransform = true
  LinkedObject = -> _Element052
  _Parent = -> Constraint047
FEATURE [App::FeaturePython] Constraint048  label="PlaneAlignment040"  # WARN: FeaturePython — macro-defined, semantics opaque (R4)
  Angle = 0
  AnglePitch = 0
  AngleRoll = 0
  Cascade = false
  Disabled = false
  Group = -> [ElementLink096,ElementLink097]
  LockAngle = false
  _ConstraintType = 37
  _Parent = -> Constraints
FEATURE [App::FeaturePython] ElementLink096  label="_Element054"  # link proxy (typed FeaturePython)
  LinkTransform = true
  LinkedObject = -> _Element054
  _Parent = -> Constraint048
FEATURE [App::FeaturePython] ElementLink097  label="_Element049"  # link proxy (typed FeaturePython)
  LinkTransform = true
  LinkedObject = -> _Element049
  _Parent = -> Constraint048
FEATURE [App::FeaturePython] Constraint049  label="PlaneAlignment041"  # WARN: FeaturePython — macro-defined, semantics opaque (R4)
  Angle = 0
  AnglePitch = 0
  AngleRoll = 0
  Cascade = false
  Disabled = false
  Group = -> [ElementLink098,ElementLink099]
  LockAngle = false
  _ConstraintType = 37
  _Parent = -> Constraints
FEATURE [App::FeaturePython] ElementLink098  label="_Element119"  # link proxy (typed FeaturePython)
  LinkTransform = true
  LinkedObject = -> _Element119
  _Parent = -> Constraint049
FEATURE [Part::FeaturePython] _Element119  # link proxy (typed FeaturePython)
  Detach = false
  LinkTransform = true
  LinkedObject = -> Link011 [1.$Element002.]
  _Parent = -> Elements
FEATURE [App::FeaturePython] ElementLink099  label="_Element030"  # link proxy (typed FeaturePython)
  LinkTransform = true
  LinkedObject = -> _Element030
  _Parent = -> Constraint049
FEATURE [App::FeaturePython] Constraint050  label="MultiParallel"  # WARN: FeaturePython — macro-defined, semantics opaque (R4)
  Angle = 0
  AnglePitch = 0
  AngleRoll = 0
  Disabled = false
  Group = -> [ElementLink100,ElementLink101]
  LockAngle = false
  _ConstraintType = 291
  _Parent = -> Constraints
FEATURE [App::FeaturePython] ElementLink100  label="_Element120"  # link proxy (typed FeaturePython)
  LinkTransform = true
  LinkedObject = -> _Element120
  _Parent = -> Constraint050
FEATURE [Part::FeaturePython] _Element120  # link proxy (typed FeaturePython)
  Detach = false
  LinkTransform = true
  LinkedObject = -> Link011 [1.$Element003.]
  _Parent = -> Elements
FEATURE [App::FeaturePython] ElementLink101  label="_Element088"  # link proxy (typed FeaturePython)
  LinkTransform = true
  LinkedObject = -> _Element088
  _Parent = -> Constraint050
FEATURE [App::FeaturePython] Constraint051  label="MultiParallel001"  # WARN: FeaturePython — macro-defined, semantics opaque (R4)
  Angle = 0
  AnglePitch = 0
  AngleRoll = 0
  Disabled = false
  Group = -> [ElementLink102,ElementLink103]
  LockAngle = false
  _ConstraintType = 291
  _Parent = -> Constraints
FEATURE [App::FeaturePython] ElementLink102  label="_Element121"  # link proxy (typed FeaturePython)
  LinkTransform = true
  LinkedObject = -> _Element121
  _Parent = -> Constraint051
FEATURE [Part::FeaturePython] _Element121  # link proxy (typed FeaturePython)
  Detach = false
  LinkTransform = true
  LinkedObject = -> Link015 [1.$Element003.]
  _Parent = -> Elements
FEATURE [App::FeaturePython] ElementLink103  label="_Element088"  # link proxy (typed FeaturePython)
  LinkTransform = true
  LinkedObject = -> _Element088
  _Parent = -> Constraint051
FEATURE [App::FeaturePython] Constraint052  label="PlaneAlignment042"  # WARN: FeaturePython — macro-defined, semantics opaque (R4)
  Angle = 0
  AnglePitch = 0
  AngleRoll = 0
  Cascade = false
  Disabled = false
  Group = -> [ElementLink104,ElementLink105]
  LockAngle = false
  _ConstraintType = 37
  _Parent = -> Constraints
FEATURE [App::FeaturePython] ElementLink104  label="_Element056"  # link proxy (typed FeaturePython)
  LinkTransform = true
  LinkedObject = -> _Element056
  _Parent = -> Constraint052
FEATURE [App::FeaturePython] ElementLink105  label="_Element122"  # link proxy (typed FeaturePython)
  LinkTransform = true
  LinkedObject = -> _Element122
  _Parent = -> Constraint052
FEATURE [Part::FeaturePython] _Element122  # link proxy (typed FeaturePython)
  Detach = false
  LinkTransform = true
  LinkedObject = -> Link012 [Face2]
  _Parent = -> Elements
FEATURE [App::FeaturePython] Constraint053  label="PointDistance"  # WARN: FeaturePython — macro-defined, semantics opaque (R4)
  Disabled = false
  Distance = 190
  Group = -> [ElementLink106,ElementLink107]
  _ConstraintType = 5
  _Parent = -> Constraints
FEATURE [App::FeaturePython] ElementLink106  label="_Element123"  # link proxy (typed FeaturePython)
  LinkTransform = true
  LinkedObject = -> _Element123
  _Parent = -> Constraint053
FEATURE [Part::FeaturePython] _Element123  # link proxy (typed FeaturePython)
  Detach = false
  LinkTransform = true
  LinkedObject = -> Link [Vertex45]
  _Parent = -> Elements
FEATURE [App::FeaturePython] ElementLink107  label="_Element124"  # link proxy (typed FeaturePython)
  LinkTransform = true
  LinkedObject = -> _Element124
  _Parent = -> Constraint053
FEATURE [Part::FeaturePython] _Element124  # link proxy (typed FeaturePython)
  Detach = false
  LinkTransform = true
  LinkedObject = -> Link001 [Vertex45]
  _Parent = -> Elements
FEATURE [App::FeaturePython] Constraint054  label="PointDistance001"  # WARN: FeaturePython — macro-defined, semantics opaque (R4)
  Disabled = false
  Distance = 170
  Group = -> [ElementLink108,ElementLink109]
  _ConstraintType = 5
  _Parent = -> Constraints
FEATURE [App::FeaturePython] ElementLink108  label="_Element125"  # link proxy (typed FeaturePython)
  LinkTransform = true
  LinkedObject = -> _Element125
  _Parent = -> Constraint054
FEATURE [Part::FeaturePython] _Element125  # link proxy (typed FeaturePython)
  Detach = false
  LinkTransform = true
  LinkedObject = -> Link007 [Vertex88]
  _Parent = -> Elements
FEATURE [App::FeaturePython] ElementLink109  label="_Element126"  # link proxy (typed FeaturePython)
  LinkTransform = true
  LinkedObject = -> _Element126
  _Parent = -> Constraint054
FEATURE [Part::FeaturePython] _Element126  # link proxy (typed FeaturePython)
  Detach = false
  LinkTransform = true
  LinkedObject = -> Link003 [Vertex240]
  _Parent = -> Elements
FEATURE [App::FeaturePython] Constraint055  label="PlaneAlignment043"  # WARN: FeaturePython — macro-defined, semantics opaque (R4)
  Angle = 0
  AnglePitch = 0
  AngleRoll = 0
  Cascade = false
  Disabled = false
  Group = -> [ElementLink110,ElementLink111]
  LockAngle = false
  _ConstraintType = 37
  _Parent = -> Constraints
FEATURE [App::FeaturePython] ElementLink110  label="_Element120"  # link proxy (typed FeaturePython)
  LinkTransform = true
  LinkedObject = -> _Element120
  _Parent = -> Constraint055
FEATURE [App::FeaturePython] ElementLink111  label="_Element121"  # link proxy (typed FeaturePython)
  LinkTransform = true
  LinkedObject = -> _Element121
  _Parent = -> Constraint055
FEATURE [App::FeaturePython] Constraint056  label="PointsPlaneDistance"  # WARN: FeaturePython — macro-defined, semantics opaque (R4)
  Disabled = false
  Distance = -200
  Group = -> [ElementLink112,ElementLink113]
  _ConstraintType = 7
  _Parent = -> Constraints
FEATURE [App::FeaturePython] ElementLink112  label="_Element127"  # link proxy (typed FeaturePython)
  LinkTransform = true
  LinkedObject = -> _Element127
  _Parent = -> Constraint056
FEATURE [Part::FeaturePython] _Element127  # link proxy (typed FeaturePython)
  Detach = false
  LinkTransform = true
  LinkedObject = -> Link003 [Vertex266]
  _Parent = -> Elements
FEATURE [App::FeaturePython] ElementLink113  label="_Element120"  # link proxy (typed FeaturePython)
  LinkTransform = true
  LinkedObject = -> _Element120
  _Parent = -> Constraint056
FEATURE [App::FeaturePython] Constraint057  label="PointsPlaneDistance001"  # WARN: FeaturePython — macro-defined, semantics opaque (R4)
  Disabled = false
  Distance = 10
  Group = -> [ElementLink114,ElementLink115]
  _ConstraintType = 7
  _Parent = -> Constraints
FEATURE [App::FeaturePython] ElementLink114  label="_Element128"  # link proxy (typed FeaturePython)
  LinkTransform = true
  LinkedObject = -> _Element128
  _Parent = -> Constraint057
FEATURE [Part::FeaturePython] _Element128  # link proxy (typed FeaturePython)
  Detach = false
  LinkTransform = true
  LinkedObject = -> Link011 [1.$Element004.]
  _Parent = -> Elements
FEATURE [App::FeaturePython] ElementLink115  label="_Element129"  # link proxy (typed FeaturePython)
  LinkTransform = true
  LinkedObject = -> _Element129
  _Parent = -> Constraint057
FEATURE [Part::FeaturePython] _Element129  # link proxy (typed FeaturePython)
  Detach = false
  LinkTransform = true
  LinkedObject = -> Link007 [Face50]
  _Parent = -> Elements
FEATURE [App::FeaturePython] Constraint058  label="PointsPlaneDistance002"  # WARN: FeaturePython — macro-defined, semantics opaque (R4)
  Disabled = false
  Distance = 10
  Group = -> [ElementLink116,ElementLink117]
  _ConstraintType = 7
  _Parent = -> Constraints
FEATURE [App::FeaturePython] ElementLink116  label="_Element130"  # link proxy (typed FeaturePython)
  LinkTransform = true
  LinkedObject = -> _Element130
  _Parent = -> Constraint058
FEATURE [Part::FeaturePython] _Element130  # link proxy (typed FeaturePython)
  Detach = false
  LinkTransform = true
  LinkedObject = -> Link015 [1.$Element005.]
  _Parent = -> Elements
FEATURE [App::FeaturePython] ElementLink117  label="_Element131"  # link proxy (typed FeaturePython)
  LinkTransform = true
  LinkedObject = -> _Element131
  _Parent = -> Constraint058
FEATURE [Part::FeaturePython] _Element131  # link proxy (typed FeaturePython)
  Detach = false
  LinkTransform = true
  LinkedObject = -> Link012 [Face107]
  _Parent = -> Elements
FEATURE [Part::FeaturePython] Assembly007  label="assy_slide_mid"  # WARN: FeaturePython — macro-defined, semantics opaque (R4)
  AutoRelax = true
  BuildShape = 0
  Freeze = false
  Group = -> [Constraints007,Elements007,Parts007]
  Placement = pos=(582,-346.893,-140) rot=(0,0,1;0rad)
  Verbose = false
  _SolverType = 1
  _Version = 1
FEATURE [App::FeaturePython] Elements007  # WARN: FeaturePython — macro-defined, semantics opaque (R4)
  Group = -> [Element035,Element036,Element037]
FEATURE [App::FeaturePython] Constraint059  label="PlaneAlignment044"  # WARN: FeaturePython — macro-defined, semantics opaque (R4)
  Angle = 0
  AnglePitch = 0
  AngleRoll = 0
  Cascade = false
  Disabled = false
  Group = -> [ElementLink118,ElementLink119]
  LockAngle = false
  _ConstraintType = 37
  _Parent = -> Constraints
FEATURE [App::FeaturePython] ElementLink118  label="_Element132"  # link proxy (typed FeaturePython)
  LinkTransform = true
  LinkedObject = -> _Element132
  _Parent = -> Constraint059
FEATURE [Part::FeaturePython] Element035  # link proxy (typed FeaturePython)
  Detach = false
  LinkTransform = true
  LinkedObject = -> Body004 [Pocket007.Face1]
  _Parent = -> Elements007
FEATURE [Part::FeaturePython] _Element132  # link proxy (typed FeaturePython)
  Detach = false
  LinkTransform = true
  LinkedObject = -> Assembly007 [1.$Element035.]
  _Parent = -> Elements
FEATURE [App::FeaturePython] ElementLink119  label="_Element003"  # link proxy (typed FeaturePython)
  LinkTransform = true
  LinkedObject = -> _Element003
  _Parent = -> Constraint059
FEATURE [App::FeaturePython] Constraint060  label="PlaneAlignment045"  # WARN: FeaturePython — macro-defined, semantics opaque (R4)
  Angle = 0
  AnglePitch = 0
  AngleRoll = 0
  Cascade = false
  Disabled = false
  Group = -> [ElementLink120,ElementLink121]
  LockAngle = false
  _ConstraintType = 37
  _Parent = -> Constraints
FEATURE [App::FeaturePython] ElementLink120  label="_Element133"  # link proxy (typed FeaturePython)
  LinkTransform = true
  LinkedObject = -> _Element133
  _Parent = -> Constraint060
FEATURE [Part::FeaturePython] Element036  # link proxy (typed FeaturePython)
  Detach = false
  LinkTransform = true
  LinkedObject = -> Body004 [Pocket007.Face2]
  _Parent = -> Elements007
FEATURE [Part::FeaturePython] _Element133  # link proxy (typed FeaturePython)
  Detach = false
  LinkTransform = true
  LinkedObject = -> Assembly007 [1.$Element036.]
  _Parent = -> Elements
FEATURE [App::FeaturePython] ElementLink121  label="_Element035"  # link proxy (typed FeaturePython)
  LinkTransform = true
  LinkedObject = -> _Element035
  _Parent = -> Constraint060
FEATURE [Part::FeaturePython] Element037  # link proxy (typed FeaturePython)
  Detach = false
  LinkTransform = true
  LinkedObject = -> Body004 [Pocket007.Face11]
  _Parent = -> Elements007
FEATURE [Part::FeaturePython] _Element134  # link proxy (typed FeaturePython)
  Detach = false
  LinkTransform = true
  LinkedObject = -> Assembly007 [1.$Element037.]
  _Parent = -> Elements
FEATURE [Part::FeaturePython] Element038  # link proxy (typed FeaturePython)
  Detach = false
  LinkTransform = true
  LinkedObject = -> Part__Mirroring [Face22]
  _Parent = -> Elements005
FEATURE [Part::FeaturePython] _Element135  # link proxy (typed FeaturePython)
  Detach = false
  LinkTransform = true
  LinkedObject = -> Assembly005 [1.$Element038.]
  _Parent = -> Elements
FEATURE [Part::FeaturePython] Element039  # link proxy (typed FeaturePython)
  Detach = false
  LinkTransform = true
  LinkedObject = -> Body [Pocket014.Face25]
  _Parent = -> Elements001
FEATURE [Part::FeaturePython] _Element136  # link proxy (typed FeaturePython)
  Detach = false
  LinkTransform = true
  LinkedObject = -> Link016 [1.$Element039.]
  _Parent = -> Elements
FEATURE [Part::FeaturePython] Element040  # link proxy (typed FeaturePython)
  Detach = false
  LinkTransform = true
  LinkedObject = -> Part__Mirroring [Face11]
  _Parent = -> Elements005
FEATURE [Part::FeaturePython] _Element137  # link proxy (typed FeaturePython)
  Detach = false
  LinkTransform = true
  LinkedObject = -> Assembly005 [1.$Element040.]
  _Parent = -> Elements
FEATURE [Part::FeaturePython] Element041  # link proxy (typed FeaturePython)
  Detach = false
  LinkTransform = true
  LinkedObject = -> Part__Mirroring [Face35]
  _Parent = -> Elements005
FEATURE [Part::FeaturePython] _Element138  # link proxy (typed FeaturePython)
  Detach = false
  LinkTransform = true
  LinkedObject = -> Assembly005 [1.$Element041.]
  _Parent = -> Elements
FEATURE [Part::FeaturePython] Assembly009  label="slide-left-slice"  # WARN: FeaturePython — macro-defined, semantics opaque (R4)
  AutoRelax = true
  BuildShape = 0
  Freeze = false
  Group = -> [Constraints009,Elements009,Parts009]
  Verbose = false
  _SolverType = 1
  _Version = 1
FEATURE [App::FeaturePython] Constraints009  # WARN: FeaturePython — macro-defined, semantics opaque (R4)
  Group = -> [Constraint065,Constraint067,Constraint068,Constraint069]
  _Version = 1
FEATURE [App::FeaturePython] Elements009  # WARN: FeaturePython — macro-defined, semantics opaque (R4)
  Group = -> [_Element139,_Element140,_Element141,_Element142,_Element143,_Element144,_Element145,_Element146]
FEATURE [App::FeaturePython] Constraint065  label="PlaneAlignment047"  # WARN: FeaturePython — macro-defined, semantics opaque (R4)
  Angle = 0
  AnglePitch = 0
  AngleRoll = 0
  Cascade = false
  Disabled = false
  Group = -> [ElementLink130,ElementLink131]
  LockAngle = false
  _ConstraintType = 37
  _Parent = -> Constraints009
FEATURE [App::FeaturePython] ElementLink130  label="_Element139"  # link proxy (typed FeaturePython)
  LinkTransform = true
  LinkedObject = -> _Element139
  _Parent = -> Constraint065
FEATURE [Part::FeaturePython] _Element139  # link proxy (typed FeaturePython)
  Detach = false
  LinkTransform = true
  LinkedObject = -> Workplane003 [Face1]
  _Parent = -> Elements009
FEATURE [App::FeaturePython] ElementLink131  label="_Element140"  # link proxy (typed FeaturePython)
  LinkTransform = true
  LinkedObject = -> _Element140
  _Parent = -> Constraint065
FEATURE [Part::FeaturePython] _Element140  # link proxy (typed FeaturePython)
  Detach = false
  LinkTransform = true
  LinkedObject = -> Body006 [Pad012.Face12]
  _Parent = -> Elements009
FEATURE [Part::FeaturePython] _Element141  # link proxy (typed FeaturePython)
  Detach = false
  LinkTransform = true
  LinkedObject = -> Body005 [Face1]
  _Parent = -> Elements009
FEATURE [App::FeaturePython] Constraint067  label="PlaneAlignment049"  # WARN: FeaturePython — macro-defined, semantics opaque (R4)
  Angle = 0
  AnglePitch = 0
  AngleRoll = 0
  Cascade = false
  Disabled = false
  Group = -> [ElementLink134,ElementLink135]
  LockAngle = false
  _ConstraintType = 37
  _Parent = -> Constraints009
FEATURE [App::FeaturePython] ElementLink134  label="_Element142"  # link proxy (typed FeaturePython)
  LinkTransform = true
  LinkedObject = -> _Element142
  _Parent = -> Constraint067
FEATURE [Part::FeaturePython] _Element142  # link proxy (typed FeaturePython)
  Detach = false
  LinkTransform = true
  LinkedObject = -> Body006 [Pad012.Face3]
  _Parent = -> Elements009
FEATURE [App::FeaturePython] ElementLink135  label="_Element143"  # link proxy (typed FeaturePython)
  LinkTransform = true
  LinkedObject = -> _Element143
  _Parent = -> Constraint067
FEATURE [Part::FeaturePython] _Element143  # link proxy (typed FeaturePython)
  Detach = false
  LinkTransform = true
  LinkedObject = -> Workplane004 [Face1]
  _Parent = -> Elements009
FEATURE [Part::FeaturePython] _Element144  # link proxy (typed FeaturePython)
  Detach = false
  LinkTransform = true
  LinkedObject = -> Body005 [Face8]
  _Parent = -> Elements009
FEATURE [App::FeaturePython] Constraint068  label="PlaneAlignment050"  # WARN: FeaturePython — macro-defined, semantics opaque (R4)
  Angle = 0
  AnglePitch = 0
  AngleRoll = 0
  Cascade = false
  Disabled = false
  Group = -> [ElementLink136,ElementLink137]
  LockAngle = false
  _ConstraintType = 37
  _Parent = -> Constraints009
FEATURE [App::FeaturePython] ElementLink136  label="_Element145"  # link proxy (typed FeaturePython)
  LinkTransform = true
  LinkedObject = -> _Element145
  _Parent = -> Constraint068
FEATURE [Part::FeaturePython] _Element145  # link proxy (typed FeaturePython)
  Detach = false
  LinkTransform = true
  LinkedObject = -> Body007 [BaseFeature.Face1]
  _Parent = -> Elements009
FEATURE [App::FeaturePython] ElementLink137  label="_Element139"  # link proxy (typed FeaturePython)
  LinkTransform = true
  LinkedObject = -> _Element139
  _Parent = -> Constraint068
FEATURE [App::FeaturePython] Constraint069  label="PlaneAlignment051"  # WARN: FeaturePython — macro-defined, semantics opaque (R4)
  Angle = 0
  AnglePitch = 0
  AngleRoll = 0
  Cascade = false
  Disabled = false
  Group = -> [ElementLink138,ElementLink139]
  LockAngle = false
  _ConstraintType = 37
  _Parent = -> Constraints009
FEATURE [App::FeaturePython] ElementLink138  label="_Element143"  # link proxy (typed FeaturePython)
  LinkTransform = true
  LinkedObject = -> _Element143
  _Parent = -> Constraint069
FEATURE [App::FeaturePython] ElementLink139  label="_Element146"  # link proxy (typed FeaturePython)
  LinkTransform = true
  LinkedObject = -> _Element146
  _Parent = -> Constraint069
FEATURE [Part::FeaturePython] _Element146  # link proxy (typed FeaturePython)
  Detach = false
  LinkTransform = true
  LinkedObject = -> Body007 [BaseFeature.Face8]
  _Parent = -> Elements009
FEATURE [App::FeaturePython] Constraint070  label="PlaneAlignment052"  # WARN: FeaturePython — macro-defined, semantics opaque (R4)
  Angle = 0
  AnglePitch = 0
  AngleRoll = 0
  Cascade = false
  Disabled = false
  Group = -> [ElementLink140,ElementLink141]
  LockAngle = false
  _ConstraintType = 37
  _Parent = -> Constraints001
FEATURE [App::FeaturePython] ElementLink140  label="_Element147"  # link proxy (typed FeaturePython)
  LinkTransform = true
  LinkedObject = -> _Element147
  _Parent = -> Constraint070
FEATURE [Part::FeaturePython] _Element147  # link proxy (typed FeaturePython)
  Detach = false
  LinkTransform = true
  LinkedObject = -> Body [Pocket014.Face8]
  _Parent = -> Elements001
FEATURE [App::FeaturePython] ElementLink141  label="_Element148"  # link proxy (typed FeaturePython)
  LinkTransform = true
  LinkedObject = -> _Element148
  _Parent = -> Constraint070
FEATURE [Part::FeaturePython] _Element148  # link proxy (typed FeaturePython)
  Detach = false
  LinkTransform = true
  LinkedObject = -> Body008 [Pad013.Face3]
  _Parent = -> Elements001
FEATURE [App::FeaturePython] Constraint071  label="PlaneAlignment053"  # WARN: FeaturePython — macro-defined, semantics opaque (R4)
  Angle = 0
  AnglePitch = 0
  AngleRoll = 0
  Cascade = false
  Disabled = false
  Group = -> [ElementLink142,ElementLink143]
  LockAngle = false
  _ConstraintType = 37
  _Parent = -> Constraints001
FEATURE [App::FeaturePython] ElementLink142  label="_Element149"  # link proxy (typed FeaturePython)
  LinkTransform = true
  LinkedObject = -> _Element149
  _Parent = -> Constraint071
FEATURE [Part::FeaturePython] _Element149  # link proxy (typed FeaturePython)
  Detach = false
  LinkTransform = true
  LinkedObject = -> Body [Pocket014.Face1]
  _Parent = -> Elements001
FEATURE [App::FeaturePython] ElementLink143  label="_Element150"  # link proxy (typed FeaturePython)
  LinkTransform = true
  LinkedObject = -> _Element150
  _Parent = -> Constraint071
FEATURE [Part::FeaturePython] _Element150  # link proxy (typed FeaturePython)
  Detach = false
  LinkTransform = true
  LinkedObject = -> Body008 [Pad013.Face12]
  _Parent = -> Elements001
FEATURE [Part::FeaturePython] _Element152  # link proxy (typed FeaturePython)
  Detach = false
  LinkTransform = true
  LinkedObject = -> Body009 [Pad014.Face3]
  _Parent = -> Elements002
FEATURE [Part::FeaturePython] _Element153  # link proxy (typed FeaturePython)
  Detach = false
  LinkTransform = true
  LinkedObject = -> Body010 [Pad015.Face3]
  _Parent = -> Elements002
FEATURE [Part::FeaturePython] _Element154  # link proxy (typed FeaturePython)
  Detach = false
  LinkTransform = true
  LinkedObject = -> Body010 [Pad015.Face13]
  _Parent = -> Elements002
FEATURE [Part::FeaturePython] _Element155  # link proxy (typed FeaturePython)
  Detach = false
  LinkTransform = true
  LinkedObject = -> Body009 [Pad014.Face13]
  _Parent = -> Elements002
FEATURE [Part::FeaturePython] _Element156  # link proxy (typed FeaturePython)
  Detach = false
  LinkTransform = true
  LinkedObject = -> Body001 [Fillet.Face43]
  _Parent = -> Elements002
FEATURE [Part::FeaturePython] Element043  # link proxy (typed FeaturePython)
  Detach = false
  LinkTransform = true
  LinkedObject = -> Body011 [Pad016.Face1]
  _Parent = -> Elements004
FEATURE [Part::FeaturePython] _Element158  # link proxy (typed FeaturePython)
  Detach = false
  LinkTransform = true
  LinkedObject = -> Assembly004 [1.$Element043.]
  _Parent = -> Elements
FEATURE [App::FeaturePython] Constraint076  label="PlaneAlignment058"  # WARN: FeaturePython — macro-defined, semantics opaque (R4)
  Angle = 0
  AnglePitch = 0
  AngleRoll = 0
  Cascade = false
  Disabled = false
  Group = -> [ElementLink152,ElementLink153]
  LockAngle = false
  _ConstraintType = 37
  _Parent = -> Constraints004
FEATURE [App::FeaturePython] ElementLink152  label="Element043"  # link proxy (typed FeaturePython)
  LinkTransform = true
  LinkedObject = -> Element043
  _Parent = -> Constraint076
FEATURE [App::FeaturePython] ElementLink153  label="_Element159"  # link proxy (typed FeaturePython)
  LinkTransform = true
  LinkedObject = -> _Element159
  _Parent = -> Constraint076
FEATURE [Part::FeaturePython] _Element159  # link proxy (typed FeaturePython)
  Detach = false
  LinkTransform = true
  LinkedObject = -> Body012 [Pad017.Face1]
  _Parent = -> Elements004
FEATURE [App::FeaturePython] Constraint077  label="PlaneAlignment059"  # WARN: FeaturePython — macro-defined, semantics opaque (R4)
  Angle = 0
  AnglePitch = 0
  AngleRoll = 0
  Cascade = false
  Disabled = false
  Group = -> [ElementLink154,ElementLink155]
  LockAngle = false
  _ConstraintType = 37
  _Parent = -> Constraints004
FEATURE [App::FeaturePython] ElementLink154  label="_Element160"  # link proxy (typed FeaturePython)
  LinkTransform = true
  LinkedObject = -> _Element160
  _Parent = -> Constraint077
FEATURE [Part::FeaturePython] _Element160  # link proxy (typed FeaturePython)
  Detach = false
  LinkTransform = true
  LinkedObject = -> Body012 [Pad017.Face13]
  _Parent = -> Elements004
FEATURE [App::FeaturePython] ElementLink155  label="_Element161"  # link proxy (typed FeaturePython)
  LinkTransform = true
  LinkedObject = -> _Element161
  _Parent = -> Constraint077
FEATURE [Part::FeaturePython] _Element161  # link proxy (typed FeaturePython)
  Detach = false
  LinkTransform = true
  LinkedObject = -> Body011 [Pad016.Face13]
  _Parent = -> Elements004
FEATURE [Part::FeaturePython] Assembly010  label="assy-slide-left-v2"  # WARN: FeaturePython — macro-defined, semantics opaque (R4)
  AutoRelax = true
  BuildShape = 0
  Freeze = false
  Group = -> [Constraints010,Elements010,Parts010]
  Placement = pos=(392.949,-349,-140) rot=(-1e-06,1e-06,1;0rad)
  Verbose = false
  _SolverType = 1
  _Version = 1
FEATURE [App::FeaturePython] Constraint079  label="PlaneAlignment061"  # WARN: FeaturePython — macro-defined, semantics opaque (R4)
  Angle = 0
  AnglePitch = 0
  AngleRoll = 0
  Cascade = false
  Disabled = false
  Group = -> [ElementLink158,ElementLink159]
  LockAngle = false
  _ConstraintType = 37
  _Parent = -> Constraints010
FEATURE [App::FeaturePython] Constraints010  # WARN: FeaturePython — macro-defined, semantics opaque (R4)
  Group = -> [Constraint079,Constraint087,Constraint097]
  _Version = 1
FEATURE [Part::FeaturePython] Element044  label="Element"  # link proxy (typed FeaturePython)
  Detach = false
  LinkTransform = true
  LinkedObject = -> Body013 [Pad018.Face1]
  _Parent = -> Elements010
FEATURE [Part::FeaturePython] Element045  label="Element001"  # link proxy (typed FeaturePython)
  Detach = false
  LinkTransform = true
  LinkedObject = -> Body013 [Pad018.Face5]
  _Parent = -> Elements010
FEATURE [Part::FeaturePython] Element046  label="Element002"  # link proxy (typed FeaturePython)
  Detach = false
  LinkTransform = true
  LinkedObject = -> Body013 [Pad018.Face4]
  _Parent = -> Elements010
FEATURE [Part::FeaturePython] Element047  label="Element003"  # link proxy (typed FeaturePython)
  Detach = false
  LinkTransform = true
  LinkedObject = -> Body013 [Pad018.Face2]
  _Parent = -> Elements010
FEATURE [Part::FeaturePython] Element048  label="Element008"  # link proxy (typed FeaturePython)
  Detach = false
  LinkTransform = true
  LinkedObject = -> Body013 [Pocket016.Face11]
  _Parent = -> Elements010
FEATURE [Part::FeaturePython] Element049  label="Element012"  # link proxy (typed FeaturePython)
  Detach = false
  LinkTransform = true
  LinkedObject = -> Body013 [Sketch042.Edge1]
  _Parent = -> Elements010
FEATURE [Part::FeaturePython] Element050  label="Element013"  # link proxy (typed FeaturePython)
  Detach = false
  LinkTransform = true
  LinkedObject = -> Body013 [Pocket016.Face4]
  _Parent = -> Elements010
FEATURE [Part::FeaturePython] Element051  label="Element014"  # link proxy (typed FeaturePython)
  Detach = false
  LinkTransform = true
  LinkedObject = -> Body013 [Pocket015.Face4]
  _Parent = -> Elements010
FEATURE [Part::FeaturePython] Element052  label="Element015"  # link proxy (typed FeaturePython)
  Detach = false
  LinkTransform = true
  LinkedObject = -> Body013 [Pocket015.Face3]
  _Parent = -> Elements010
FEATURE [Part::FeaturePython] Element053  label="Element016"  # link proxy (typed FeaturePython)
  Detach = false
  LinkTransform = true
  LinkedObject = -> Body013 [Pocket015.Face1]
  _Parent = -> Elements010
FEATURE [Part::FeaturePython] Element054  label="Element017"  # link proxy (typed FeaturePython)
  Detach = false
  LinkTransform = true
  LinkedObject = -> Body013 [Pocket015.Face11]
  _Parent = -> Elements010
FEATURE [Part::FeaturePython] Element055  label="Element022"  # link proxy (typed FeaturePython)
  Detach = false
  LinkTransform = true
  LinkedObject = -> Body013 [Pocket016.Face1]
  _Parent = -> Elements010
FEATURE [Part::FeaturePython] Element056  label="Element023"  # link proxy (typed FeaturePython)
  Detach = false
  LinkTransform = true
  LinkedObject = -> Body013 [Pocket016.Face2]
  _Parent = -> Elements010
FEATURE [Part::FeaturePython] Element057  label="Element039"  # link proxy (typed FeaturePython)
  Detach = false
  LinkTransform = true
  LinkedObject = -> Body013 [Pocket022.Face25]
  _Parent = -> Elements010
FEATURE [App::FeaturePython] ElementLink158  label="_Element149"  # link proxy (typed FeaturePython)
  LinkTransform = true
  LinkedObject = -> _Element164
  _Parent = -> Constraint079
FEATURE [App::FeaturePython] ElementLink159  label="_Element150"  # link proxy (typed FeaturePython)
  LinkTransform = true
  LinkedObject = -> _Element165
  _Parent = -> Constraint079
FEATURE [App::FeaturePython] Elements010  # WARN: FeaturePython — macro-defined, semantics opaque (R4)
  Group = -> [Element044,Element045,Element046,Element047,Element048,Element049,Element050,Element051,Element052,Element053,Element054,Element055,Element056,Element057,_Element162,_Element163,_Element164,_Element165,Element058,Element059,Element060,Element062,Element067,_Element176,_Element177,_Element197,Element139,Element140]
FEATURE [Part::FeaturePython] _Element162  label="_Element147"  # link proxy (typed FeaturePython)
  Detach = false
  LinkTransform = true
  LinkedObject = -> Body013 [Pocket022.Face8]
  _Parent = -> Elements010
FEATURE [Part::FeaturePython] _Element163  label="_Element148"  # link proxy (typed FeaturePython)
  Detach = false
  LinkTransform = true
  LinkedObject = -> Body014 [Pad020.Face3]
  _Parent = -> Elements010
FEATURE [Part::FeaturePython] _Element164  label="_Element149"  # link proxy (typed FeaturePython)
  Detach = false
  LinkTransform = true
  LinkedObject = -> Body013 [Pocket022.Face1]
  _Parent = -> Elements010
FEATURE [Part::FeaturePython] _Element165  label="_Element150"  # link proxy (typed FeaturePython)
  Detach = false
  LinkTransform = true
  LinkedObject = -> Body014 [Pad020.Face12]
  _Parent = -> Elements010
FEATURE [App::FeaturePython] Constraint080  label="PointOnLine"  # WARN: FeaturePython — macro-defined, semantics opaque (R4)
  Disabled = false
  Group = -> [ElementLink160,ElementLink161]
  _ConstraintType = 4
  _Parent = -> Constraints
FEATURE [App::FeaturePython] ElementLink160  label="_Element085"  # link proxy (typed FeaturePython)
  LinkTransform = true
  LinkedObject = -> _Element085
  _Parent = -> Constraint080
FEATURE [App::FeaturePython] ElementLink161  label="_Element166"  # link proxy (typed FeaturePython)
  LinkTransform = true
  LinkedObject = -> _Element166
  _Parent = -> Constraint080
FEATURE [Part::FeaturePython] Element058  # link proxy (typed FeaturePython)
  Detach = false
  LinkTransform = true
  LinkedObject = -> Body013 [Sketch053.Edge1]
  _Parent = -> Elements010
FEATURE [Part::FeaturePython] _Element166  # link proxy (typed FeaturePython)
  Detach = false
  LinkTransform = true
  LinkedObject = -> Assembly010 [1.$Element058.]
  _Parent = -> Elements
FEATURE [App::FeaturePython] Constraint081  label="PlaneAlignment062"  # WARN: FeaturePython — macro-defined, semantics opaque (R4)
  Angle = 0
  AnglePitch = 0
  AngleRoll = 0
  Cascade = false
  Disabled = false
  Group = -> [ElementLink162,ElementLink163]
  LockAngle = false
  _ConstraintType = 37
  _Parent = -> Constraints
FEATURE [App::FeaturePython] ElementLink162  label="_Element167"  # link proxy (typed FeaturePython)
  LinkTransform = true
  LinkedObject = -> _Element167
  _Parent = -> Constraint081
FEATURE [Part::FeaturePython] Element059  # link proxy (typed FeaturePython)
  Detach = false
  LinkTransform = true
  LinkedObject = -> Body013 [Pocket024.Face2]
  _Parent = -> Elements010
FEATURE [Part::FeaturePython] _Element167  # link proxy (typed FeaturePython)
  Detach = false
  LinkTransform = true
  LinkedObject = -> Assembly010 [1.$Element059.]
  _Parent = -> Elements
FEATURE [App::FeaturePython] ElementLink163  label="_Element038"  # link proxy (typed FeaturePython)
  LinkTransform = true
  LinkedObject = -> _Element038
  _Parent = -> Constraint081
FEATURE [App::FeaturePython] ElementLink034  label="_Element097"  # link proxy (typed FeaturePython)
  LinkTransform = true
  LinkedObject = -> _Element097
  _Parent = -> Constraint017
FEATURE [App::FeaturePython] ElementLink035  label="_Element005"  # link proxy (typed FeaturePython)
  LinkTransform = true
  LinkedObject = -> _Element005
  _Parent = -> Constraint017
FEATURE [App::FeaturePython] Constraint017  label="PlaneAlignment016"  # WARN: FeaturePython — macro-defined, semantics opaque (R4)
  Angle = 0
  AnglePitch = 0
  AngleRoll = 0
  Cascade = false
  Disabled = false
  Group = -> [ElementLink034,ElementLink035]
  LockAngle = false
  _ConstraintType = 37
  _Parent = -> Constraints
FEATURE [App::FeaturePython] Constraint082  label="PlaneAlignment063"  # WARN: FeaturePython — macro-defined, semantics opaque (R4)
  Angle = 0
  AnglePitch = 0
  AngleRoll = 0
  Cascade = false
  Disabled = false
  Group = -> [ElementLink164,ElementLink165]
  LockAngle = false
  _ConstraintType = 37
  _Parent = -> Constraints
FEATURE [App::FeaturePython] ElementLink164  label="_Element168"  # link proxy (typed FeaturePython)
  LinkTransform = true
  LinkedObject = -> _Element168
  _Parent = -> Constraint082
FEATURE [Part::FeaturePython] Element060  # link proxy (typed FeaturePython)
  Detach = false
  LinkTransform = true
  LinkedObject = -> Body013 [Pocket024.Face1]
  _Parent = -> Elements010
FEATURE [Part::FeaturePython] _Element168  # link proxy (typed FeaturePython)
  Detach = false
  LinkTransform = true
  LinkedObject = -> Assembly010 [1.$Element060.]
  _Parent = -> Elements
FEATURE [App::FeaturePython] ElementLink165  label="_Element005"  # link proxy (typed FeaturePython)
  LinkTransform = true
  LinkedObject = -> _Element005
  _Parent = -> Constraint082
FEATURE [Part::FeaturePython] Element062  # link proxy (typed FeaturePython)
  Detach = false
  LinkTransform = true
  LinkedObject = -> Body013 [Pocket024.Face22]
  _Parent = -> Elements010
FEATURE [Part::FeaturePython] _Element170  # link proxy (typed FeaturePython)
  Detach = false
  LinkTransform = true
  LinkedObject = -> Assembly010 [1.$Element062.]
  _Parent = -> Elements
FEATURE [App::FeaturePython] Constraint085  label="AxialAlignment"  # WARN: FeaturePython — macro-defined, semantics opaque (R4)
  Angle = 0
  AnglePitch = 0
  AngleRoll = 0
  Disabled = false
  Group = -> [ElementLink170,ElementLink171]
  LockAngle = false
  Multiply = false
  _ConstraintType = 36
  _Parent = -> Constraints
FEATURE [App::FeaturePython] ElementLink170  label="_Element171"  # link proxy (typed FeaturePython)
  LinkTransform = true
  LinkedObject = -> _Element171
  _Parent = -> Constraint085
FEATURE [Part::FeaturePython] Element063  # link proxy (typed FeaturePython)
  Detach = false
  LinkTransform = true
  LinkedObject = -> Body001 [Fillet.Face22]
  _Parent = -> Elements002
FEATURE [Part::FeaturePython] _Element171  # link proxy (typed FeaturePython)
  Detach = false
  LinkTransform = true
  LinkedObject = -> Assembly002 [1.$Element063.]
  _Parent = -> Elements
FEATURE [App::FeaturePython] ElementLink171  label="_Element170"  # link proxy (typed FeaturePython)
  LinkTransform = true
  LinkedObject = -> _Element170
  _Parent = -> Constraint085
FEATURE [Part::FeaturePython] Assembly011  label="assy-bearing_left_front"  # WARN: FeaturePython — macro-defined, semantics opaque (R4)
  AutoRelax = true
  BuildShape = 0
  Freeze = false
  Group = -> [Constraints011,Elements011,Parts011]
  Placement = pos=(-779.964,-485.997,35.0013) rot=(-0.430413,-0.793404,0.430413;1.80018rad)
  Verbose = false
  _SolverType = 1
  _Version = 1
FEATURE [App::FeaturePython] Elements011  # WARN: FeaturePython — macro-defined, semantics opaque (R4)
  Group = -> [Element065,Element066]
FEATURE [Part::FeaturePython] Element064  # link proxy (typed FeaturePython)
  Detach = false
  LinkTransform = true
  LinkedObject = -> Body003 [Fillet001.Face19]
  _Parent = -> Elements004
FEATURE [Part::FeaturePython] _Element172  # link proxy (typed FeaturePython)
  Detach = false
  LinkTransform = true
  LinkedObject = -> Assembly004 [1.$Element064.]
  _Parent = -> Elements
FEATURE [Part::FeaturePython] Element065  # link proxy (typed FeaturePython)
  Detach = false
  LinkTransform = true
  LinkedObject = -> Body015 [Pad023.Face2]
  _Parent = -> Elements011
FEATURE [Part::FeaturePython] _Element173  # link proxy (typed FeaturePython)
  Detach = false
  LinkTransform = true
  LinkedObject = -> Assembly011 [1.$Element065.]
  _Parent = -> Elements
FEATURE [Part::FeaturePython] Element066  # link proxy (typed FeaturePython)
  Detach = false
  LinkTransform = true
  LinkedObject = -> Body015 [Pad023.Face3]
  _Parent = -> Elements011
FEATURE [Part::FeaturePython] _Element174  # link proxy (typed FeaturePython)
  Detach = false
  LinkTransform = true
  LinkedObject = -> Assembly011 [1.$Element066.]
  _Parent = -> Elements
FEATURE [App::FeaturePython] Constraint086  label="AxialAlignment009"  # WARN: FeaturePython — macro-defined, semantics opaque (R4)
  Angle = 0
  AnglePitch = 0
  AngleRoll = 0
  Disabled = false
  Group = -> [ElementLink172,ElementLink173]
  LockAngle = false
  Multiply = false
  _ConstraintType = 36
  _Parent = -> Constraints
FEATURE [App::FeaturePython] ElementLink172  label="_Element172"  # link proxy (typed FeaturePython)
  LinkTransform = true
  LinkedObject = -> _Element172
  _Parent = -> Constraint086
FEATURE [App::FeaturePython] ElementLink173  label="_Element173"  # link proxy (typed FeaturePython)
  LinkTransform = true
  LinkedObject = -> _Element173
  _Parent = -> Constraint086
FEATURE [Part::FeaturePython] Element067  # link proxy (typed FeaturePython)
  Detach = false
  LinkTransform = true
  LinkedObject = -> Body013 [Pocket029.Face106]
  _Parent = -> Elements010
FEATURE [Part::FeaturePython] _Element175  # link proxy (typed FeaturePython)
  Detach = false
  LinkTransform = true
  LinkedObject = -> Assembly010 [1.$Element067.]
  _Parent = -> Elements
FEATURE [App::FeaturePython] Constraint087  label="PlaneAlignment064"  # WARN: FeaturePython — macro-defined, semantics opaque (R4)
  Angle = 0
  AnglePitch = 0
  AngleRoll = 0
  Cascade = false
  Disabled = false
  Group = -> [ElementLink174,ElementLink175]
  LockAngle = false
  _ConstraintType = 37
  _Parent = -> Constraints010
FEATURE [App::FeaturePython] ElementLink174  label="_Element176"  # link proxy (typed FeaturePython)
  LinkTransform = true
  LinkedObject = -> _Element176
  _Parent = -> Constraint087
FEATURE [Part::FeaturePython] _Element176  # link proxy (typed FeaturePython)
  Detach = false
  LinkTransform = true
  LinkedObject = -> Body014 [Pad020.Face2]
  _Parent = -> Elements010
FEATURE [App::FeaturePython] ElementLink175  label="_Element177"  # link proxy (typed FeaturePython)
  LinkTransform = true
  LinkedObject = -> _Element177
  _Parent = -> Constraint087
FEATURE [Part::FeaturePython] _Element177  # link proxy (typed FeaturePython)
  Detach = false
  LinkTransform = true
  LinkedObject = -> Body013 [Fillet005.Face111]
  _Parent = -> Elements010
FEATURE [Part::FeaturePython] _Element178  # link proxy (typed FeaturePython)
  Detach = false
  LinkTransform = true
  LinkedObject = -> Body016 [Pad029.Face13]
  _Parent = -> Elements002
FEATURE [Part::FeaturePython] _Element179  # link proxy (typed FeaturePython)
  Detach = false
  LinkTransform = true
  LinkedObject = -> Body001 [PolarPattern001.Face23]
  _Parent = -> Elements002
FEATURE [Part::FeaturePython] _Element180  # link proxy (typed FeaturePython)
  Detach = false
  LinkTransform = true
  LinkedObject = -> Body016 [Pad029.Face12]
  _Parent = -> Elements002
FEATURE [Part::FeaturePython] _Element181  # link proxy (typed FeaturePython)
  Detach = false
  LinkTransform = true
  LinkedObject = -> Body001 [PolarPattern001.Face38]
  _Parent = -> Elements002
FEATURE [Part::FeaturePython] _Element182  # link proxy (typed FeaturePython)
  Detach = false
  LinkTransform = true
  LinkedObject = -> Body001 [PolarPattern001.Face5]
  _Parent = -> Elements002
FEATURE [Part::FeaturePython] _Element183  # link proxy (typed FeaturePython)
  Detach = false
  LinkTransform = true
  LinkedObject = -> Body016 [Pad029.Face5]
  _Parent = -> Elements002
FEATURE [Part::FeaturePython] Assembly012  label="assy-slide_mid_v3"  # WARN: FeaturePython — macro-defined, semantics opaque (R4)
  AutoRelax = true
  BuildShape = 0
  Freeze = false
  Group = -> [Constraints012,Elements012,Parts012]
  Placement = pos=(216,-296,20) rot=(0,0,1;0rad)
  Verbose = false
  _SolverType = 1
  _Version = 1
FEATURE [App::FeaturePython] Constraints012  # WARN: FeaturePython — macro-defined, semantics opaque (R4)
  Group = -> [Constraint098,Constraint099,Constraint100]
  _Version = 1
FEATURE [App::FeaturePython] Elements012  # WARN: FeaturePython — macro-defined, semantics opaque (R4)
  Group = -> [Element068,Element069,Element070,_Element198,_Element199,_Element200,_Element201,_Element202,_Element203]
FEATURE [Part::FeaturePython] Element068  # link proxy (typed FeaturePython)
  Detach = false
  LinkTransform = true
  LinkedObject = -> Body017 [Pad030.Face5]
  _Parent = -> Elements012
FEATURE [Part::FeaturePython] _Element184  # link proxy (typed FeaturePython)
  Detach = false
  LinkTransform = true
  LinkedObject = -> Assembly012 [1.$Element068.]
  _Parent = -> Elements
FEATURE [App::FeaturePython] Constraint091  label="PlaneAlignment068"  # WARN: FeaturePython — macro-defined, semantics opaque (R4)
  Angle = 0
  AnglePitch = 0
  AngleRoll = 0
  Cascade = false
  Disabled = false
  Group = -> [ElementLink182,ElementLink183]
  LockAngle = false
  _ConstraintType = 37
  _Parent = -> Constraints
FEATURE [App::FeaturePython] ElementLink182  label="_Element004"  # link proxy (typed FeaturePython)
  LinkTransform = true
  LinkedObject = -> _Element004
  _Parent = -> Constraint091
FEATURE [App::FeaturePython] ElementLink183  label="_Element184"  # link proxy (typed FeaturePython)
  LinkTransform = true
  LinkedObject = -> _Element184
  _Parent = -> Constraint091
FEATURE [App::FeaturePython] Constraint092  label="PlaneAlignment069"  # WARN: FeaturePython — macro-defined, semantics opaque (R4)
  Angle = 0
  AnglePitch = 0
  AngleRoll = 0
  Cascade = false
  Disabled = false
  Group = -> [ElementLink184,ElementLink185]
  LockAngle = false
  _ConstraintType = 37
  _Parent = -> Constraints
FEATURE [App::FeaturePython] ElementLink184  label="_Element185"  # link proxy (typed FeaturePython)
  LinkTransform = true
  LinkedObject = -> _Element185
  _Parent = -> Constraint092
FEATURE [Part::FeaturePython] Element069  # link proxy (typed FeaturePython)
  Detach = false
  LinkTransform = true
  LinkedObject = -> Body017 [Pad030.Face2]
  _Parent = -> Elements012
FEATURE [Part::FeaturePython] _Element185  # link proxy (typed FeaturePython)
  Detach = false
  LinkTransform = true
  LinkedObject = -> Assembly012 [1.$Element069.]
  _Parent = -> Elements
FEATURE [App::FeaturePython] ElementLink185  label="_Element071"  # link proxy (typed FeaturePython)
  LinkTransform = true
  LinkedObject = -> _Element071
  _Parent = -> Constraint092
FEATURE [App::FeaturePython] Constraint093  label="PlaneAlignment070"  # WARN: FeaturePython — macro-defined, semantics opaque (R4)
  Angle = 0
  AnglePitch = 0
  AngleRoll = 0
  Cascade = false
  Disabled = false
  Group = -> [ElementLink186,ElementLink187]
  LockAngle = false
  _ConstraintType = 37
  _Parent = -> Constraints
FEATURE [App::FeaturePython] ElementLink186  label="_Element186"  # link proxy (typed FeaturePython)
  LinkTransform = true
  LinkedObject = -> _Element186
  _Parent = -> Constraint093
FEATURE [Part::FeaturePython] Element070  # link proxy (typed FeaturePython)
  Detach = false
  LinkTransform = true
  LinkedObject = -> Body017 [Pad030.Face1]
  _Parent = -> Elements012
FEATURE [Part::FeaturePython] _Element186  # link proxy (typed FeaturePython)
  Detach = false
  LinkTransform = true
  LinkedObject = -> Assembly012 [1.$Element070.]
  _Parent = -> Elements
FEATURE [App::FeaturePython] ElementLink187  label="_Element038"  # link proxy (typed FeaturePython)
  LinkTransform = true
  LinkedObject = -> _Element038
  _Parent = -> Constraint093
FEATURE [Part::FeaturePython] _Element187  # link proxy (typed FeaturePython)
  Detach = false
  LinkTransform = true
  LinkedObject = -> Body019 [Mirrored002.Face5]
  _Parent = -> Elements002
FEATURE [Part::FeaturePython] _Element188  # link proxy (typed FeaturePython)
  Detach = false
  LinkTransform = true
  LinkedObject = -> Body001 [Fillet012.Face10]
  _Parent = -> Elements002
FEATURE [App::FeaturePython] ElementLink144  label="_Element156"  # link proxy (typed FeaturePython)
  LinkTransform = true
  LinkedObject = -> _Element156
  _Parent = -> Constraint072
FEATURE [App::FeaturePython] ElementLink145  label="_Element153"  # link proxy (typed FeaturePython)
  LinkTransform = true
  LinkedObject = -> _Element153
  _Parent = -> Constraint072
FEATURE [App::FeaturePython] Constraint072  label="PlaneAlignment054"  # WARN: FeaturePython — macro-defined, semantics opaque (R4)
  Angle = 0
  AnglePitch = 0
  AngleRoll = 0
  Cascade = false
  Disabled = false
  Group = -> [ElementLink144,ElementLink145]
  LockAngle = false
  _ConstraintType = 37
  _Parent = -> Constraints002
FEATURE [App::FeaturePython] ElementLink146  label="_Element152"  # link proxy (typed FeaturePython)
  LinkTransform = true
  LinkedObject = -> _Element152
  _Parent = -> Constraint073
FEATURE [App::FeaturePython] ElementLink147  label="_Element153"  # link proxy (typed FeaturePython)
  LinkTransform = true
  LinkedObject = -> _Element153
  _Parent = -> Constraint073
FEATURE [App::FeaturePython] Constraint073  label="PlaneAlignment055"  # WARN: FeaturePython — macro-defined, semantics opaque (R4)
  Angle = 0
  AnglePitch = 0
  AngleRoll = 0
  Cascade = false
  Disabled = false
  Group = -> [ElementLink146,ElementLink147]
  LockAngle = false
  _ConstraintType = 37
  _Parent = -> Constraints002
FEATURE [App::FeaturePython] ElementLink148  label="_Element154"  # link proxy (typed FeaturePython)
  LinkTransform = true
  LinkedObject = -> _Element154
  _Parent = -> Constraint074
FEATURE [App::FeaturePython] ElementLink149  label="_Element155"  # link proxy (typed FeaturePython)
  LinkTransform = true
  LinkedObject = -> _Element155
  _Parent = -> Constraint074
FEATURE [App::FeaturePython] Constraint074  label="PlaneAlignment056"  # WARN: FeaturePython — macro-defined, semantics opaque (R4)
  Angle = 0
  AnglePitch = 0
  AngleRoll = 0
  Cascade = false
  Disabled = false
  Group = -> [ElementLink148,ElementLink149]
  LockAngle = false
  _ConstraintType = 37
  _Parent = -> Constraints002
FEATURE [App::FeaturePython] ElementLink176  label="_Element178"  # link proxy (typed FeaturePython)
  LinkTransform = true
  LinkedObject = -> _Element178
  _Parent = -> Constraint088
FEATURE [App::FeaturePython] ElementLink177  label="_Element179"  # link proxy (typed FeaturePython)
  LinkTransform = true
  LinkedObject = -> _Element179
  _Parent = -> Constraint088
FEATURE [App::FeaturePython] Constraint088  label="PlaneAlignment065"  # WARN: FeaturePython — macro-defined, semantics opaque (R4)
  Angle = 0
  AnglePitch = 0
  AngleRoll = 0
  Cascade = false
  Disabled = false
  Group = -> [ElementLink176,ElementLink177]
  LockAngle = false
  Offset = -1.67
  _ConstraintType = 37
  _Parent = -> Constraints002
FEATURE [App::FeaturePython] ElementLink178  label="_Element180"  # link proxy (typed FeaturePython)
  LinkTransform = true
  LinkedObject = -> _Element180
  _Parent = -> Constraint089
FEATURE [App::FeaturePython] ElementLink179  label="_Element181"  # link proxy (typed FeaturePython)
  LinkTransform = true
  LinkedObject = -> _Element181
  _Parent = -> Constraint089
FEATURE [App::FeaturePython] Constraint089  label="PlaneAlignment066"  # WARN: FeaturePython — macro-defined, semantics opaque (R4)
  Angle = 0
  AnglePitch = 0
  AngleRoll = 0
  Cascade = false
  Disabled = false
  Group = -> [ElementLink178,ElementLink179]
  LockAngle = false
  Offset = -110
  _ConstraintType = 37
  _Parent = -> Constraints002
FEATURE [App::FeaturePython] ElementLink180  label="_Element182"  # link proxy (typed FeaturePython)
  LinkTransform = true
  LinkedObject = -> _Element182
  _Parent = -> Constraint090
FEATURE [App::FeaturePython] ElementLink181  label="_Element183"  # link proxy (typed FeaturePython)
  LinkTransform = true
  LinkedObject = -> _Element183
  _Parent = -> Constraint090
FEATURE [App::FeaturePython] Constraint090  label="PlaneAlignment067"  # WARN: FeaturePython — macro-defined, semantics opaque (R4)
  Angle = 0
  AnglePitch = 0
  AngleRoll = 0
  Cascade = false
  Disabled = false
  Group = -> [ElementLink180,ElementLink181]
  LockAngle = false
  Offset = -25
  _ConstraintType = 37
  _Parent = -> Constraints002
FEATURE [Part::FeaturePython] _Element191  # link proxy (typed FeaturePython)
  Detach = false
  LinkTransform = true
  LinkedObject = -> Body001 [Fillet012.Face5]
  _Parent = -> Elements002
FEATURE [Part::FeaturePython] _Element193  # link proxy (typed FeaturePython)
  Detach = false
  LinkTransform = true
  LinkedObject = -> Body001 [Fillet012.Face11]
  _Parent = -> Elements002
FEATURE [App::FeaturePython] Constraint094  label="PlaneAlignment071"  # WARN: FeaturePython — macro-defined, semantics opaque (R4)
  Angle = 0
  AnglePitch = 0
  AngleRoll = 0
  Cascade = false
  Disabled = false
  Group = -> [ElementLink188,ElementLink189]
  LockAngle = false
  Offset = -1.67
  _ConstraintType = 37
  _Parent = -> Constraints002
FEATURE [App::FeaturePython] ElementLink188  label="_Element193"  # link proxy (typed FeaturePython)
  LinkTransform = true
  LinkedObject = -> _Element193
  _Parent = -> Constraint094
FEATURE [App::FeaturePython] ElementLink189  label="_Element194"  # link proxy (typed FeaturePython)
  LinkTransform = true
  LinkedObject = -> _Element194
  _Parent = -> Constraint094
FEATURE [Part::FeaturePython] _Element194  # link proxy (typed FeaturePython)
  Detach = false
  LinkTransform = true
  LinkedObject = -> Body019 [Fillet020.Face22]
  _Parent = -> Elements002
FEATURE [App::FeaturePython] Constraint095  label="PlaneAlignment072"  # WARN: FeaturePython — macro-defined, semantics opaque (R4)
  Angle = 0
  AnglePitch = 0
  AngleRoll = 0
  Cascade = false
  Disabled = false
  Group = -> [ElementLink190,ElementLink191]
  LockAngle = false
  _ConstraintType = 37
  _Parent = -> Constraints002
FEATURE [App::FeaturePython] ElementLink190  label="_Element188"  # link proxy (typed FeaturePython)
  LinkTransform = true
  LinkedObject = -> _Element188
  _Parent = -> Constraint095
FEATURE [App::FeaturePython] ElementLink191  label="_Element195"  # link proxy (typed FeaturePython)
  LinkTransform = true
  LinkedObject = -> _Element195
  _Parent = -> Constraint095
FEATURE [Part::FeaturePython] _Element195  # link proxy (typed FeaturePython)
  Detach = false
  LinkTransform = true
  LinkedObject = -> Body019 [Fillet020.Face5]
  _Parent = -> Elements002
FEATURE [App::FeaturePython] Constraint096  label="PlaneAlignment073"  # WARN: FeaturePython — macro-defined, semantics opaque (R4)
  Angle = 0
  AnglePitch = 0
  AngleRoll = 0
  Cascade = false
  Disabled = false
  Group = -> [ElementLink192,ElementLink193]
  LockAngle = false
  Offset = -105
  _ConstraintType = 37
  _Parent = -> Constraints002
FEATURE [App::FeaturePython] ElementLink192  label="_Element196"  # link proxy (typed FeaturePython)
  LinkTransform = true
  LinkedObject = -> _Element196
  _Parent = -> Constraint096
FEATURE [Part::FeaturePython] _Element196  # link proxy (typed FeaturePython)
  Detach = false
  LinkTransform = true
  LinkedObject = -> Body019 [Fillet020.Face24]
  _Parent = -> Elements002
FEATURE [App::FeaturePython] ElementLink193  label="_Element191"  # link proxy (typed FeaturePython)
  LinkTransform = true
  LinkedObject = -> _Element191
  _Parent = -> Constraint096
FEATURE [App::FeaturePython] Constraint097  label="PlaneAlignment074"  # WARN: FeaturePython — macro-defined, semantics opaque (R4)
  Angle = 0
  AnglePitch = 0
  AngleRoll = 0
  Cascade = false
  Disabled = false
  Group = -> [ElementLink194,ElementLink195]
  LockAngle = false
  _ConstraintType = 37
  _Parent = -> Constraints010
FEATURE [App::FeaturePython] ElementLink194  label="_Element197"  # link proxy (typed FeaturePython)
  LinkTransform = true
  LinkedObject = -> _Element197
  _Parent = -> Constraint097
FEATURE [Part::FeaturePython] _Element197  # link proxy (typed FeaturePython)
  Detach = false
  LinkTransform = true
  LinkedObject = -> Body013 [Fillet013.Face43]
  _Parent = -> Elements010
FEATURE [App::FeaturePython] ElementLink195  label="_Element148"  # link proxy (typed FeaturePython)
  LinkTransform = true
  LinkedObject = -> _Element163
  _Parent = -> Constraint097
FEATURE [App::FeaturePython] Constraint098  label="PlaneAlignment075"  # WARN: FeaturePython — macro-defined, semantics opaque (R4)
  Angle = 0
  AnglePitch = 0
  AngleRoll = 0
  Cascade = false
  Disabled = false
  Group = -> [ElementLink196,ElementLink197]
  LockAngle = false
  _ConstraintType = 37
  _Parent = -> Constraints012
FEATURE [App::FeaturePython] ElementLink196  label="_Element198"  # link proxy (typed FeaturePython)
  LinkTransform = true
  LinkedObject = -> _Element198
  _Parent = -> Constraint098
FEATURE [Part::FeaturePython] _Element198  # link proxy (typed FeaturePython)
  Detach = false
  LinkTransform = true
  LinkedObject = -> Body017 [Fillet021.Face36]
  _Parent = -> Elements012
FEATURE [App::FeaturePython] ElementLink197  label="_Element199"  # link proxy (typed FeaturePython)
  LinkTransform = true
  LinkedObject = -> _Element199
  _Parent = -> Constraint098
FEATURE [Part::FeaturePython] _Element199  # link proxy (typed FeaturePython)
  Detach = false
  LinkTransform = true
  LinkedObject = -> Body021 [Pad041.Face12]
  _Parent = -> Elements012
FEATURE [App::FeaturePython] Constraint099  label="PlaneAlignment076"  # WARN: FeaturePython — macro-defined, semantics opaque (R4)
  Angle = 0
  AnglePitch = 0
  AngleRoll = 0
  Cascade = false
  Disabled = false
  Group = -> [ElementLink198,ElementLink199]
  LockAngle = false
  _ConstraintType = 37
  _Parent = -> Constraints012
FEATURE [App::FeaturePython] ElementLink198  label="_Element200"  # link proxy (typed FeaturePython)
  LinkTransform = true
  LinkedObject = -> _Element200
  _Parent = -> Constraint099
FEATURE [Part::FeaturePython] _Element200  # link proxy (typed FeaturePython)
  Detach = false
  LinkTransform = true
  LinkedObject = -> Body021 [Pad041.Face2]
  _Parent = -> Elements012
FEATURE [App::FeaturePython] ElementLink199  label="_Element201"  # link proxy (typed FeaturePython)
  LinkTransform = true
  LinkedObject = -> _Element201
  _Parent = -> Constraint099
FEATURE [Part::FeaturePython] _Element201  # link proxy (typed FeaturePython)
  Detach = false
  LinkTransform = true
  LinkedObject = -> Body017 [Fillet021.Face56]
  _Parent = -> Elements012
FEATURE [App::FeaturePython] Constraint100  label="PlaneAlignment077"  # WARN: FeaturePython — macro-defined, semantics opaque (R4)
  Angle = 0
  AnglePitch = 0
  AngleRoll = 0
  Cascade = false
  Disabled = false
  Group = -> [ElementLink200,ElementLink201]
  LockAngle = false
  Offset = 6
  _ConstraintType = 37
  _Parent = -> Constraints012
FEATURE [App::FeaturePython] ElementLink200  label="_Element202"  # link proxy (typed FeaturePython)
  LinkTransform = true
  LinkedObject = -> _Element202
  _Parent = -> Constraint100
FEATURE [Part::FeaturePython] _Element202  # link proxy (typed FeaturePython)
  Detach = false
  LinkTransform = true
  LinkedObject = -> Body017 [Fillet021.Face14]
  _Parent = -> Elements012
FEATURE [App::FeaturePython] ElementLink201  label="_Element203"  # link proxy (typed FeaturePython)
  LinkTransform = true
  LinkedObject = -> _Element203
  _Parent = -> Constraint100
FEATURE [Part::FeaturePython] _Element203  # link proxy (typed FeaturePython)
  Detach = false
  LinkTransform = true
  LinkedObject = -> Body021 [Pad041.Face3]
  _Parent = -> Elements012
FEATURE [Part::FeaturePython] _Element204  # link proxy (typed FeaturePython)
  Detach = false
  LinkTransform = true
  LinkedObject = -> Body022 [Fillet041.Face91]
  _Parent = -> Elements004
FEATURE [Part::FeaturePython] _Element205  # link proxy (typed FeaturePython)
  Detach = false
  LinkTransform = true
  LinkedObject = -> Body003 [Pocket035.Face5]
  _Parent = -> Elements004
FEATURE [Part::FeaturePython] _Element206  # link proxy (typed FeaturePython)
  Detach = false
  LinkTransform = true
  LinkedObject = -> Body003 [Pocket035.Face12]
  _Parent = -> Elements004
FEATURE [Part::FeaturePython] _Element207  # link proxy (typed FeaturePython)
  Detach = false
  LinkTransform = true
  LinkedObject = -> Body022 [Fillet041.Face19]
  _Parent = -> Elements004
FEATURE [Part::FeaturePython] _Element208  # link proxy (typed FeaturePython)
  Detach = false
  LinkTransform = true
  LinkedObject = -> Body022 [Fillet041.Face15]
  _Parent = -> Elements004
FEATURE [Part::FeaturePython] _Element209  # link proxy (typed FeaturePython)
  Detach = false
  LinkTransform = true
  LinkedObject = -> Body003 [Pocket035.Face2]
  _Parent = -> Elements004
FEATURE [App::FeaturePython] Constraint103  label="PlaneAlignment080"  # WARN: FeaturePython — macro-defined, semantics opaque (R4)
  Angle = 0
  AnglePitch = 0
  AngleRoll = 0
  Cascade = false
  Disabled = false
  Group = -> [ElementLink206,ElementLink207]
  LockAngle = false
  Offset = -83
  _ConstraintType = 37
  _Parent = -> Constraints004
FEATURE [App::FeaturePython] ElementLink206  label="_Element210"  # link proxy (typed FeaturePython)
  LinkTransform = true
  LinkedObject = -> _Element210
  _Parent = -> Constraint103
FEATURE [Part::FeaturePython] _Element210  # link proxy (typed FeaturePython)
  Detach = false
  LinkTransform = true
  LinkedObject = -> Body022 [Fillet041.Face24]
  _Parent = -> Elements004
FEATURE [App::FeaturePython] ElementLink207  label="_Element206"  # link proxy (typed FeaturePython)
  LinkTransform = true
  LinkedObject = -> _Element206
  _Parent = -> Constraint103
FEATURE [App::FeaturePython] Constraint104  label="PlaneAlignment081"  # WARN: FeaturePython — macro-defined, semantics opaque (R4)
  Angle = 0
  AnglePitch = 0
  AngleRoll = 0
  Cascade = false
  Disabled = false
  Group = -> [ElementLink208,ElementLink209]
  LockAngle = false
  _ConstraintType = 37
  _Parent = -> Constraints004
FEATURE [App::FeaturePython] ElementLink208  label="_Element211"  # link proxy (typed FeaturePython)
  LinkTransform = true
  LinkedObject = -> _Element211
  _Parent = -> Constraint104
FEATURE [Part::FeaturePython] _Element211  # link proxy (typed FeaturePython)
  Detach = false
  LinkTransform = true
  LinkedObject = -> Body022 [Fillet041.Face5]
  _Parent = -> Elements004
FEATURE [App::FeaturePython] ElementLink209  label="_Element205"  # link proxy (typed FeaturePython)
  LinkTransform = true
  LinkedObject = -> _Element205
  _Parent = -> Constraint104
FEATURE [App::FeaturePython] Constraint105  label="PlaneAlignment082"  # WARN: FeaturePython — macro-defined, semantics opaque (R4)
  Angle = 0
  AnglePitch = 0
  AngleRoll = 0
  Cascade = false
  Disabled = false
  Group = -> [ElementLink210,ElementLink211]
  LockAngle = false
  Offset = -1.67
  _ConstraintType = 37
  _Parent = -> Constraints004
FEATURE [App::FeaturePython] ElementLink210  label="_Element208"  # link proxy (typed FeaturePython)
  LinkTransform = true
  LinkedObject = -> _Element208
  _Parent = -> Constraint105
FEATURE [App::FeaturePython] ElementLink211  label="_Element212"  # link proxy (typed FeaturePython)
  LinkTransform = true
  LinkedObject = -> _Element212
  _Parent = -> Constraint105
FEATURE [Part::FeaturePython] _Element212  # link proxy (typed FeaturePython)
  Detach = false
  LinkTransform = true
  LinkedObject = -> Body003 [Pocket035.Face19]
  _Parent = -> Elements004
FEATURE [App::FeaturePython] Constraint106  label="PlaneAlignment083"  # WARN: FeaturePython — macro-defined, semantics opaque (R4)
  Angle = 0
  AnglePitch = 0
  AngleRoll = 0
  Cascade = false
  Disabled = false
  Group = -> [ElementLink212,ElementLink213]
  LockAngle = false
  _ConstraintType = 37
  _Parent = -> Constraints004
FEATURE [App::FeaturePython] ElementLink212  label="_Element213"  # link proxy (typed FeaturePython)
  LinkTransform = true
  LinkedObject = -> _Element213
  _Parent = -> Constraint106
FEATURE [Part::FeaturePython] _Element213  # link proxy (typed FeaturePython)
  Detach = false
  LinkTransform = true
  LinkedObject = -> Body023 [Pad050.Face3]
  _Parent = -> Elements004
FEATURE [App::FeaturePython] ElementLink213  label="_Element214"  # link proxy (typed FeaturePython)
  LinkTransform = true
  LinkedObject = -> _Element214
  _Parent = -> Constraint106
FEATURE [Part::FeaturePython] _Element214  # link proxy (typed FeaturePython)
  Detach = false
  LinkTransform = true
  LinkedObject = -> Body003 [Pad049.Face38]
  _Parent = -> Elements004
FEATURE [Part::FeaturePython] _Element215  # link proxy (typed FeaturePython)
  Detach = false
  LinkTransform = true
  LinkedObject = -> Body023 [Pad050.Face2]
  _Parent = -> Elements004
FEATURE [Part::FeaturePython] _Element216  # link proxy (typed FeaturePython)
  Detach = false
  LinkTransform = true
  LinkedObject = -> Body003 [Pad049.Face40]
  _Parent = -> Elements004
FEATURE [Part::FeaturePython] _Element217  # link proxy (typed FeaturePython)
  Detach = false
  LinkTransform = true
  LinkedObject = -> Body024 [Pocket060.Face3]
  _Parent = -> Elements004
FEATURE [Part::FeaturePython] _Element218  # link proxy (typed FeaturePython)
  Detach = false
  LinkTransform = true
  LinkedObject = -> Body003 [Pocket059.Face7]
  _Parent = -> Elements004
FEATURE [Part::FeaturePython] _Element219  # link proxy (typed FeaturePython)
  Detach = false
  LinkTransform = true
  LinkedObject = -> Body003 [Pocket059.Face9]
  _Parent = -> Elements004
FEATURE [Part::FeaturePython] _Element220  # link proxy (typed FeaturePython)
  Detach = false
  LinkTransform = true
  LinkedObject = -> Body024 [Pocket060.Face10]
  _Parent = -> Elements004
FEATURE [App::FeaturePython] Constraint109  label="PlaneAlignment084"  # WARN: FeaturePython — macro-defined, semantics opaque (R4)
  Angle = 0
  AnglePitch = 0
  AngleRoll = 0
  Cascade = false
  Disabled = false
  Group = -> [ElementLink218,ElementLink219]
  LockAngle = false
  _ConstraintType = 37
  _Parent = -> Constraints004
FEATURE [App::FeaturePython] ElementLink218  label="_Element218"  # link proxy (typed FeaturePython)
  LinkTransform = true
  LinkedObject = -> _Element218
  _Parent = -> Constraint109
FEATURE [App::FeaturePython] ElementLink219  label="_Element217"  # link proxy (typed FeaturePython)
  LinkTransform = true
  LinkedObject = -> _Element217
  _Parent = -> Constraint109
FEATURE [App::FeaturePython] Constraint110  label="PlaneAlignment085"  # WARN: FeaturePython — macro-defined, semantics opaque (R4)
  Angle = 0
  AnglePitch = 0
  AngleRoll = 0
  Cascade = false
  Disabled = false
  Group = -> [ElementLink220,ElementLink221]
  LockAngle = false
  Offset = 2.5
  _ConstraintType = 37
  _Parent = -> Constraints004
FEATURE [App::FeaturePython] ElementLink220  label="_Element221"  # link proxy (typed FeaturePython)
  LinkTransform = true
  LinkedObject = -> _Element221
  _Parent = -> Constraint110
FEATURE [Part::FeaturePython] _Element221  # link proxy (typed FeaturePython)
  Detach = false
  LinkTransform = true
  LinkedObject = -> Body025 [Pad056.Face2]
  _Parent = -> Elements004
FEATURE [App::FeaturePython] ElementLink221  label="_Element222"  # link proxy (typed FeaturePython)
  LinkTransform = true
  LinkedObject = -> _Element222
  _Parent = -> Constraint110
FEATURE [Part::FeaturePython] _Element222  # link proxy (typed FeaturePython)
  Detach = false
  LinkTransform = true
  LinkedObject = -> Body003 [Pocket059.Face6]
  _Parent = -> Elements004
FEATURE [App::FeaturePython] Constraint111  label="PlaneAlignment086"  # WARN: FeaturePython — macro-defined, semantics opaque (R4)
  Angle = 0
  AnglePitch = 0
  AngleRoll = 0
  Cascade = false
  Disabled = false
  Group = -> [ElementLink222,ElementLink223]
  LockAngle = false
  Offset = -7
  _ConstraintType = 37
  _Parent = -> Constraints004
FEATURE [App::FeaturePython] ElementLink222  label="_Element223"  # link proxy (typed FeaturePython)
  LinkTransform = true
  LinkedObject = -> _Element223
  _Parent = -> Constraint111
FEATURE [Part::FeaturePython] _Element223  # link proxy (typed FeaturePython)
  Detach = false
  LinkTransform = true
  LinkedObject = -> Body025 [Pad056.Face6]
  _Parent = -> Elements004
FEATURE [App::FeaturePython] ElementLink223  label="_Element224"  # link proxy (typed FeaturePython)
  LinkTransform = true
  LinkedObject = -> _Element224
  _Parent = -> Constraint111
FEATURE [Part::FeaturePython] _Element224  # link proxy (typed FeaturePython)
  Detach = false
  LinkTransform = true
  LinkedObject = -> Body003 [Pocket059.Face26]
  _Parent = -> Elements004
FEATURE [App::FeaturePython] Constraint112  label="PlaneAlignment087"  # WARN: FeaturePython — macro-defined, semantics opaque (R4)
  Angle = 0
  AnglePitch = 0
  AngleRoll = 0
  Cascade = false
  Disabled = false
  Group = -> [ElementLink224,ElementLink225]
  LockAngle = false
  _ConstraintType = 37
  _Parent = -> Constraints004
FEATURE [App::FeaturePython] ElementLink224  label="_Element225"  # link proxy (typed FeaturePython)
  LinkTransform = true
  LinkedObject = -> _Element225
  _Parent = -> Constraint112
FEATURE [Part::FeaturePython] _Element225  # link proxy (typed FeaturePython)
  Detach = false
  LinkTransform = true
  LinkedObject = -> Body025 [Pad056.Face1]
  _Parent = -> Elements004
FEATURE [App::FeaturePython] ElementLink225  label="_Element204"  # link proxy (typed FeaturePython)
  LinkTransform = true
  LinkedObject = -> _Element204
  _Parent = -> Constraint112
FEATURE [App::FeaturePython] Constraint113  label="AxialAlignment012"  # WARN: FeaturePython — macro-defined, semantics opaque (R4)
  Angle = 0
  AnglePitch = 0
  AngleRoll = 0
  Disabled = false
  Group = -> [ElementLink226,ElementLink227]
  LockAngle = false
  Multiply = false
  _ConstraintType = 36
  _Parent = -> Constraints004
FEATURE [App::FeaturePython] ElementLink226  label="_Element226"  # link proxy (typed FeaturePython)
  LinkTransform = true
  LinkedObject = -> _Element226
  _Parent = -> Constraint113
FEATURE [Part::FeaturePython] _Element226  # link proxy (typed FeaturePython)
  Detach = false
  LinkTransform = true
  LinkedObject = -> Body024 [Pocket060.Face1]
  _Parent = -> Elements004
FEATURE [App::FeaturePython] ElementLink227  label="_Element227"  # link proxy (typed FeaturePython)
  LinkTransform = true
  LinkedObject = -> _Element227
  _Parent = -> Constraint113
FEATURE [Part::FeaturePython] _Element227  # link proxy (typed FeaturePython)
  Detach = false
  LinkTransform = true
  LinkedObject = -> Body003 [Pocket059.Face5]
  _Parent = -> Elements004
FEATURE [Part::FeaturePython] Assembly013  label="Assembly-v3.1_front_door"  # WARN: FeaturePython — macro-defined, semantics opaque (R4)
  AutoRelax = true
  BuildShape = 0
  Freeze = false
  Group = -> [Constraints013,Elements013,Parts013]
  Verbose = false
  _SolverType = 1
  _Version = 1
FEATURE [App::FeaturePython] Constraints013  # WARN: FeaturePython — macro-defined, semantics opaque (R4)
  Group = -> [Constraint114,Constraint115,Constraint116,Constraint117,Constraint118]
  _Version = 1
FEATURE [App::FeaturePython] Elements013  # WARN: FeaturePython — macro-defined, semantics opaque (R4)
  Group = -> [_Element228,_Element229,_Element230,_Element231,_Element232,_Element233,_Element234]
FEATURE [App::FeaturePython] Constraint114  label="PlaneAlignment088"  # WARN: FeaturePython — macro-defined, semantics opaque (R4)
  Angle = 0
  AnglePitch = 0
  AngleRoll = 0
  Cascade = false
  Disabled = false
  Group = -> [ElementLink228,ElementLink229]
  LockAngle = false
  _ConstraintType = 37
  _Parent = -> Constraints013
FEATURE [App::FeaturePython] ElementLink228  label="_Element228"  # link proxy (typed FeaturePython)
  LinkTransform = true
  LinkedObject = -> _Element228
  _Parent = -> Constraint114
FEATURE [Part::FeaturePython] _Element228  # link proxy (typed FeaturePython)
  Detach = false
  LinkTransform = true
  LinkedObject = -> Slice013_child0 [Face47]
  _Parent = -> Elements013
FEATURE [App::FeaturePython] ElementLink229  label="_Element229"  # link proxy (typed FeaturePython)
  LinkTransform = true
  LinkedObject = -> _Element229
  _Parent = -> Constraint114
FEATURE [Part::FeaturePython] _Element229  # link proxy (typed FeaturePython)
  Detach = false
  LinkTransform = true
  LinkedObject = -> Workplane005 [Face1]
  _Parent = -> Elements013
FEATURE [App::FeaturePython] Constraint115  label="PlaneAlignment089"  # WARN: FeaturePython — macro-defined, semantics opaque (R4)
  Angle = 0
  AnglePitch = 0
  AngleRoll = 0
  Cascade = false
  Disabled = false
  Group = -> [ElementLink230,ElementLink231]
  LockAngle = false
  _ConstraintType = 37
  _Parent = -> Constraints013
FEATURE [App::FeaturePython] ElementLink230  label="_Element230"  # link proxy (typed FeaturePython)
  LinkTransform = true
  LinkedObject = -> _Element230
  _Parent = -> Constraint115
FEATURE [Part::FeaturePython] _Element230  # link proxy (typed FeaturePython)
  Detach = false
  LinkTransform = true
  LinkedObject = -> Slice013_child4 [Face23]
  _Parent = -> Elements013
FEATURE [App::FeaturePython] ElementLink231  label="_Element229"  # link proxy (typed FeaturePython)
  LinkTransform = true
  LinkedObject = -> _Element229
  _Parent = -> Constraint115
FEATURE [App::FeaturePython] Constraint116  label="PlaneAlignment090"  # WARN: FeaturePython — macro-defined, semantics opaque (R4)
  Angle = 0
  AnglePitch = 0
  AngleRoll = 0
  Cascade = false
  Disabled = false
  Group = -> [ElementLink232,ElementLink233]
  LockAngle = false
  _ConstraintType = 37
  _Parent = -> Constraints013
FEATURE [App::FeaturePython] ElementLink232  label="_Element231"  # link proxy (typed FeaturePython)
  LinkTransform = true
  LinkedObject = -> _Element231
  _Parent = -> Constraint116
FEATURE [Part::FeaturePython] _Element231  # link proxy (typed FeaturePython)
  Detach = false
  LinkTransform = true
  LinkedObject = -> Slice013_child2 [Face13]
  _Parent = -> Elements013
FEATURE [App::FeaturePython] ElementLink233  label="_Element229"  # link proxy (typed FeaturePython)
  LinkTransform = true
  LinkedObject = -> _Element229
  _Parent = -> Constraint116
FEATURE [App::FeaturePython] Constraint117  label="PlaneAlignment091"  # WARN: FeaturePython — macro-defined, semantics opaque (R4)
  Angle = 0
  AnglePitch = 0
  AngleRoll = 0
  Cascade = false
  Disabled = false
  Group = -> [ElementLink234,ElementLink235]
  LockAngle = false
  _ConstraintType = 37
  _Parent = -> Constraints013
FEATURE [App::FeaturePython] ElementLink234  label="_Element232"  # link proxy (typed FeaturePython)
  LinkTransform = true
  LinkedObject = -> _Element232
  _Parent = -> Constraint117
FEATURE [Part::FeaturePython] _Element232  # link proxy (typed FeaturePython)
  Detach = false
  LinkTransform = true
  LinkedObject = -> Workplane007 [Face1]
  _Parent = -> Elements013
FEATURE [App::FeaturePython] ElementLink235  label="_Element233"  # link proxy (typed FeaturePython)
  LinkTransform = true
  LinkedObject = -> _Element233
  _Parent = -> Constraint117
FEATURE [Part::FeaturePython] _Element233  # link proxy (typed FeaturePython)
  Detach = false
  LinkTransform = true
  LinkedObject = -> Slice013_child0 [Face49]
  _Parent = -> Elements013
FEATURE [App::FeaturePython] Constraint118  label="PlaneAlignment092"  # WARN: FeaturePython — macro-defined, semantics opaque (R4)
  Angle = 0
  AnglePitch = 0
  AngleRoll = 0
  Cascade = false
  Disabled = false
  Group = -> [ElementLink236,ElementLink237]
  LockAngle = false
  _ConstraintType = 37
  _Parent = -> Constraints013
FEATURE [App::FeaturePython] ElementLink236  label="_Element234"  # link proxy (typed FeaturePython)
  LinkTransform = true
  LinkedObject = -> _Element234
  _Parent = -> Constraint118
FEATURE [Part::FeaturePython] _Element234  # link proxy (typed FeaturePython)
  Detach = false
  LinkTransform = true
  LinkedObject = -> Slice013_child4 [Face60]
  _Parent = -> Elements013
FEATURE [App::FeaturePython] ElementLink237  label="_Element232"  # link proxy (typed FeaturePython)
  LinkTransform = true
  LinkedObject = -> _Element232
  _Parent = -> Constraint118
FEATURE [Part::FeaturePython] Assembly014  label="assy-orthogonal_brace_v2_OG_RR"  # WARN: FeaturePython — macro-defined, semantics opaque (R4)
  AutoRelax = true
  BuildShape = 0
  Freeze = false
  Group = -> [Constraints014,Elements014,Parts014]
  Placement = pos=(417,-465.994,-1.25882e-10) rot=(0,0,1;0rad)
  Verbose = false
  _SolverType = 1
  _Version = 1
FEATURE [App::FeaturePython] Elements014  # WARN: FeaturePython — macro-defined, semantics opaque (R4)
  Group = -> [Element071,Element072,Element073]
FEATURE [Part::FeaturePython] Assembly015  label="Assembly-prints"  # WARN: FeaturePython — macro-defined, semantics opaque (R4)
  AutoRelax = true
  BuildShape = 0
  Freeze = false
  Group = -> [Constraints015,Elements015,Parts015]
  Verbose = false
  _SolverType = 1
  _Version = 1
FEATURE [Part::FeaturePython] Parts015  # WARN: FeaturePython — macro-defined, semantics opaque (R4)
  Group = -> [Assembly013,Slice010,GrExplode_Slice011,Slice012,GrExplode_Slice009,GrExplode_Slice008,Slice007,Slice006,GrExplode_Slice005,GrExplode_Slice004,GrExplode_Slice003,Slice002,Assembly009,Body005,GrExplode_Slice014,GrExplode_Slice015,GrExplode_Slice016,GrExplode_Slice017,GrExplode_Slice018,GrExplode_Slice019,GrExplode_Slice020]
  GroupMode = 0
FEATURE [App::FeaturePython] Constraint119  label="PlaneAlignment093"  # WARN: FeaturePython — macro-defined, semantics opaque (R4)
  Angle = 0
  AnglePitch = 0
  AngleRoll = 0
  Cascade = false
  Disabled = false
  Group = -> [ElementLink238,ElementLink239]
  LockAngle = false
  _ConstraintType = 37
  _Parent = -> Constraints
FEATURE [App::FeaturePython] ElementLink238  label="_Element235"  # link proxy (typed FeaturePython)
  LinkTransform = true
  LinkedObject = -> _Element235
  _Parent = -> Constraint119
FEATURE [Part::FeaturePython] Element071  # link proxy (typed FeaturePython)
  Detach = false
  LinkTransform = true
  LinkedObject = -> Body026 [Pocket066.Face37]
  _Parent = -> Elements014
FEATURE [Part::FeaturePython] _Element235  # link proxy (typed FeaturePython)
  Detach = false
  LinkTransform = true
  LinkedObject = -> Assembly014 [1.$Element071.]
  _Parent = -> Elements
FEATURE [App::FeaturePython] ElementLink239  label="_Element009"  # link proxy (typed FeaturePython)
  LinkTransform = true
  LinkedObject = -> _Element009
  _Parent = -> Constraint119
FEATURE [App::FeaturePython] Constraint120  label="PlaneAlignment094"  # WARN: FeaturePython — macro-defined, semantics opaque (R4)
  Angle = 0
  AnglePitch = 0
  AngleRoll = 0
  Cascade = false
  Disabled = false
  Group = -> [ElementLink240,ElementLink241]
  LockAngle = false
  _ConstraintType = 37
  _Parent = -> Constraints
FEATURE [App::FeaturePython] ElementLink240  label="_Element236"  # link proxy (typed FeaturePython)
  LinkTransform = true
  LinkedObject = -> _Element236
  _Parent = -> Constraint120
FEATURE [Part::FeaturePython] Element072  # link proxy (typed FeaturePython)
  Detach = false
  LinkTransform = true
  LinkedObject = -> Body026 [Pocket066.Face71]
  _Parent = -> Elements014
FEATURE [Part::FeaturePython] _Element236  # link proxy (typed FeaturePython)
  Detach = false
  LinkTransform = true
  LinkedObject = -> Assembly014 [1.$Element072.]
  _Parent = -> Elements
FEATURE [App::FeaturePython] ElementLink241  label="_Element122"  # link proxy (typed FeaturePython)
  LinkTransform = true
  LinkedObject = -> _Element122
  _Parent = -> Constraint120
FEATURE [Part::FeaturePython] Element073  # link proxy (typed FeaturePython)
  Detach = false
  LinkTransform = true
  LinkedObject = -> Body026 [Pocket066.Face6]
  _Parent = -> Elements014
FEATURE [Part::FeaturePython] _Element237  # link proxy (typed FeaturePython)
  Detach = false
  LinkTransform = true
  LinkedObject = -> Assembly014 [1.$Element073.]
  _Parent = -> Elements
FEATURE [App::FeaturePython] Constraint121  label="PlaneAlignment095"  # WARN: FeaturePython — macro-defined, semantics opaque (R4)
  Angle = 0
  AnglePitch = 0
  AngleRoll = 0
  Cascade = false
  Disabled = false
  Group = -> [ElementLink242,ElementLink243]
  LockAngle = false
  _ConstraintType = 37
  _Parent = -> Constraints
FEATURE [App::FeaturePython] ElementLink242  label="_Element237"  # link proxy (typed FeaturePython)
  LinkTransform = true
  LinkedObject = -> _Element237
  _Parent = -> Constraint121
FEATURE [App::FeaturePython] ElementLink243  label="_Element052"  # link proxy (typed FeaturePython)
  LinkTransform = true
  LinkedObject = -> _Element052
  _Parent = -> Constraint121
FEATURE [Part::FeaturePython] Assembly016  label="assy-orthogonal_brace_v2_mirror_FR"  # WARN: FeaturePython — macro-defined, semantics opaque (R4)
  AutoRelax = true
  BuildShape = 0
  Freeze = false
  Group = -> [Constraints016,Elements016,Parts016]
  Placement = pos=(417,-485.994,-1.30192e-10) rot=(0,0,1;0rad)
  Verbose = false
  _SolverType = 1
  _Version = 1
FEATURE [App::FeaturePython] Elements016  # WARN: FeaturePython — macro-defined, semantics opaque (R4)
  Group = -> [Element074,Element075,Element076]
FEATURE [App::FeaturePython] Constraint122  label="PlaneAlignment096"  # WARN: FeaturePython — macro-defined, semantics opaque (R4)
  Angle = 0
  AnglePitch = 0
  AngleRoll = 0
  Cascade = false
  Disabled = false
  Group = -> [ElementLink244,ElementLink245]
  LockAngle = false
  _ConstraintType = 37
  _Parent = -> Constraints
FEATURE [App::FeaturePython] ElementLink244  label="_Element238"  # link proxy (typed FeaturePython)
  LinkTransform = true
  LinkedObject = -> _Element238
  _Parent = -> Constraint122
FEATURE [Part::FeaturePython] Element074  # link proxy (typed FeaturePython)
  Detach = false
  LinkTransform = true
  LinkedObject = -> Part__Mirroring002 [Face71]
  _Parent = -> Elements016
FEATURE [Part::FeaturePython] _Element238  # link proxy (typed FeaturePython)
  Detach = false
  LinkTransform = true
  LinkedObject = -> Assembly016 [1.$Element074.]
  _Parent = -> Elements
FEATURE [App::FeaturePython] ElementLink245  label="_Element118"  # link proxy (typed FeaturePython)
  LinkTransform = true
  LinkedObject = -> _Element118
  _Parent = -> Constraint122
FEATURE [Part::FeaturePython] Element075  # link proxy (typed FeaturePython)
  Detach = false
  LinkTransform = true
  LinkedObject = -> Part__Mirroring002 [Face37]
  _Parent = -> Elements016
FEATURE [Part::FeaturePython] _Element239  # link proxy (typed FeaturePython)
  Detach = false
  LinkTransform = true
  LinkedObject = -> Assembly016 [1.$Element075.]
  _Parent = -> Elements
FEATURE [App::FeaturePython] Constraint123  label="PlaneAlignment097"  # WARN: FeaturePython — macro-defined, semantics opaque (R4)
  Angle = 0
  AnglePitch = 0
  AngleRoll = 0
  Cascade = false
  Disabled = false
  Group = -> [ElementLink246,ElementLink247]
  LockAngle = false
  _ConstraintType = 37
  _Parent = -> Constraints
FEATURE [App::FeaturePython] ElementLink246  label="_Element009"  # link proxy (typed FeaturePython)
  LinkTransform = true
  LinkedObject = -> _Element009
  _Parent = -> Constraint123
FEATURE [App::FeaturePython] ElementLink247  label="_Element239"  # link proxy (typed FeaturePython)
  LinkTransform = true
  LinkedObject = -> _Element239
  _Parent = -> Constraint123
FEATURE [App::FeaturePython] Constraint124  label="PlaneAlignment098"  # WARN: FeaturePython — macro-defined, semantics opaque (R4)
  Angle = 0
  AnglePitch = 0
  AngleRoll = 0
  Cascade = false
  Disabled = false
  Group = -> [ElementLink248,ElementLink249]
  LockAngle = false
  _ConstraintType = 37
  _Parent = -> Constraints
FEATURE [App::FeaturePython] ElementLink248  label="_Element240"  # link proxy (typed FeaturePython)
  LinkTransform = true
  LinkedObject = -> _Element240
  _Parent = -> Constraint124
FEATURE [Part::FeaturePython] Element076  # link proxy (typed FeaturePython)
  Detach = false
  LinkTransform = true
  LinkedObject = -> Part__Mirroring002 [Face6]
  _Parent = -> Elements016
FEATURE [Part::FeaturePython] _Element240  # link proxy (typed FeaturePython)
  Detach = false
  LinkTransform = true
  LinkedObject = -> Assembly016 [1.$Element076.]
  _Parent = -> Elements
FEATURE [App::FeaturePython] ElementLink249  label="_Element052"  # link proxy (typed FeaturePython)
  LinkTransform = true
  LinkedObject = -> _Element052
  _Parent = -> Constraint124
FEATURE [Part::FeaturePython] Assembly017  label="assy-bowl_retainer_FL"  # WARN: FeaturePython — macro-defined, semantics opaque (R4)
  AutoRelax = true
  BuildShape = 0
  Freeze = false
  Group = -> [Constraints017,Elements017,Parts017]
  Placement = pos=(36.9999,-476,20) rot=(0,0,1;0rad)
  Verbose = false
  _SolverType = 1
  _Version = 1
FEATURE [App::FeaturePython] Elements017  # WARN: FeaturePython — macro-defined, semantics opaque (R4)
  Group = -> [Element077,Element078,Element079,Element080,Element084,Element087]
FEATURE [App::FeaturePython] Constraint125  label="PlaneAlignment099"  # WARN: FeaturePython — macro-defined, semantics opaque (R4)
  Angle = 0
  AnglePitch = 0
  AngleRoll = 0
  Cascade = false
  Disabled = false
  Group = -> [ElementLink250,ElementLink251]
  LockAngle = false
  _ConstraintType = 37
  _Parent = -> Constraints
FEATURE [App::FeaturePython] ElementLink250  label="_Element241"  # link proxy (typed FeaturePython)
  LinkTransform = true
  LinkedObject = -> _Element241
  _Parent = -> Constraint125
FEATURE [Part::FeaturePython] _Element241  # link proxy (typed FeaturePython)
  Detach = false
  LinkTransform = true
  LinkedObject = -> Link001 [Face106]
  _Parent = -> Elements
FEATURE [App::FeaturePython] ElementLink251  label="_Element242"  # link proxy (typed FeaturePython)
  LinkTransform = true
  LinkedObject = -> _Element242
  _Parent = -> Constraint125
FEATURE [Part::FeaturePython] Element077  # link proxy (typed FeaturePython)
  Detach = false
  LinkTransform = true
  LinkedObject = -> Body027 [Pad064.Face5]
  _Parent = -> Elements017
FEATURE [Part::FeaturePython] _Element242  # link proxy (typed FeaturePython)
  Detach = false
  LinkTransform = true
  LinkedObject = -> Assembly017 [1.$Element077.]
  _Parent = -> Elements
FEATURE [Part::FeaturePython] Element078  # link proxy (typed FeaturePython)
  Detach = false
  LinkTransform = true
  LinkedObject = -> Body027 [Pad064.Face7]
  _Parent = -> Elements017
FEATURE [Part::FeaturePython] _Element243  # link proxy (typed FeaturePython)
  Detach = false
  LinkTransform = true
  LinkedObject = -> Assembly017 [1.$Element078.]
  _Parent = -> Elements
FEATURE [Part::FeaturePython] _Element244  # link proxy (typed FeaturePython)
  Detach = false
  LinkTransform = true
  LinkedObject = -> Link001 [Face80]
  _Parent = -> Elements
FEATURE [App::FeaturePython] Constraint127  label="PlaneAlignment101"  # WARN: FeaturePython — macro-defined, semantics opaque (R4)
  Angle = 0
  AnglePitch = 0
  AngleRoll = 0
  Cascade = false
  Disabled = false
  Group = -> [ElementLink254,ElementLink255]
  LockAngle = false
  Offset = -160
  _ConstraintType = 37
  _Parent = -> Constraints
FEATURE [App::FeaturePython] ElementLink254  label="_Element245"  # link proxy (typed FeaturePython)
  LinkTransform = true
  LinkedObject = -> _Element245
  _Parent = -> Constraint127
FEATURE [Part::FeaturePython] Element079  # link proxy (typed FeaturePython)
  Detach = false
  LinkTransform = true
  LinkedObject = -> Body027 [Pad064.Face1]
  _Parent = -> Elements017
FEATURE [Part::FeaturePython] _Element245  # link proxy (typed FeaturePython)
  Detach = false
  LinkTransform = true
  LinkedObject = -> Assembly017 [1.$Element079.]
  _Parent = -> Elements
FEATURE [App::FeaturePython] ElementLink255  label="_Element"  # link proxy (typed FeaturePython)
  LinkTransform = true
  LinkedObject = -> _Element
  _Parent = -> Constraint127
FEATURE [App::FeaturePython] Constraint128  label="PlaneAlignment102"  # WARN: FeaturePython — macro-defined, semantics opaque (R4)
  Angle = 0
  AnglePitch = 0
  AngleRoll = 0
  Cascade = false
  Disabled = false
  Group = -> [ElementLink256,ElementLink257]
  LockAngle = false
  _ConstraintType = 37
  _Parent = -> Constraints
FEATURE [App::FeaturePython] ElementLink256  label="_Element246"  # link proxy (typed FeaturePython)
  LinkTransform = true
  LinkedObject = -> _Element246
  _Parent = -> Constraint128
FEATURE [Part::FeaturePython] Element080  # link proxy (typed FeaturePython)
  Detach = false
  LinkTransform = true
  LinkedObject = -> Body027 [Pad064.Face6]
  _Parent = -> Elements017
FEATURE [Part::FeaturePython] _Element246  # link proxy (typed FeaturePython)
  Detach = false
  LinkTransform = true
  LinkedObject = -> Assembly017 [1.$Element080.]
  _Parent = -> Elements
FEATURE [App::FeaturePython] ElementLink257  label="_Element244"  # link proxy (typed FeaturePython)
  LinkTransform = true
  LinkedObject = -> _Element244
  _Parent = -> Constraint128
FEATURE [Part::FeaturePython] Assembly018  label="assy-bowl_retainer_FR"  # WARN: FeaturePython — macro-defined, semantics opaque (R4)
  AutoRelax = true
  BuildShape = 0
  Freeze = false
  Group = -> [Constraints018,Elements018,Parts018]
  Placement = pos=(207,-476,20) rot=(0,0,1;0rad)
  Verbose = false
  _SolverType = 1
  _Version = 1
FEATURE [App::FeaturePython] Elements018  # WARN: FeaturePython — macro-defined, semantics opaque (R4)
  Group = -> [Element081,Element082,Element083,Element085,Element086]
FEATURE [App::FeaturePython] Constraint129  label="PlaneAlignment103"  # WARN: FeaturePython — macro-defined, semantics opaque (R4)
  Angle = 0
  AnglePitch = 0
  AngleRoll = 0
  Cascade = false
  Disabled = false
  Group = -> [ElementLink258,ElementLink259]
  LockAngle = false
  _ConstraintType = 37
  _Parent = -> Constraints
FEATURE [App::FeaturePython] ElementLink258  label="_Element247"  # link proxy (typed FeaturePython)
  LinkTransform = true
  LinkedObject = -> _Element247
  _Parent = -> Constraint129
FEATURE [Part::FeaturePython] Element081  # link proxy (typed FeaturePython)
  Detach = false
  LinkTransform = true
  LinkedObject = -> Part__Mirroring003 [Face19]
  _Parent = -> Elements018
FEATURE [Part::FeaturePython] _Element247  # link proxy (typed FeaturePython)
  Detach = false
  LinkTransform = true
  LinkedObject = -> Assembly018 [1.$Element081.]
  _Parent = -> Elements
FEATURE [App::FeaturePython] ElementLink259  label="_Element035"  # link proxy (typed FeaturePython)
  LinkTransform = true
  LinkedObject = -> _Element035
  _Parent = -> Constraint129
FEATURE [Part::FeaturePython] Element082  # link proxy (typed FeaturePython)
  Detach = false
  LinkTransform = true
  LinkedObject = -> Part__Mirroring003 [Face74]
  _Parent = -> Elements018
FEATURE [Part::FeaturePython] _Element248  # link proxy (typed FeaturePython)
  Detach = false
  LinkTransform = true
  LinkedObject = -> Assembly018 [1.$Element082.]
  _Parent = -> Elements
FEATURE [Part::FeaturePython] Element083  # link proxy (typed FeaturePython)
  Detach = false
  LinkTransform = true
  LinkedObject = -> Part__Mirroring003 [Face77]
  _Parent = -> Elements018
FEATURE [Part::FeaturePython] _Element249  # link proxy (typed FeaturePython)
  Detach = false
  LinkTransform = true
  LinkedObject = -> Assembly018 [1.$Element083.]
  _Parent = -> Elements
FEATURE [Part::FeaturePython] Element084  # link proxy (typed FeaturePython)
  Detach = false
  LinkTransform = true
  LinkedObject = -> Body027 [Fillet068.Face77]
  _Parent = -> Elements017
FEATURE [Part::FeaturePython] _Element250  # link proxy (typed FeaturePython)
  Detach = false
  LinkTransform = true
  LinkedObject = -> Assembly017 [1.$Element084.]
  _Parent = -> Elements
FEATURE [Part::FeaturePython] Assembly019  label="assy-bowl_retainer_RR"  # WARN: FeaturePython — macro-defined, semantics opaque (R4)
  AutoRelax = true
  BuildShape = 0
  Freeze = false
  Group = -> [Constraints019,Elements019,Parts019]
  Placement = pos=(197,-316,20) rot=(0,0,1;1.5708rad)
  Verbose = false
  _SolverType = 1
  _Version = 1
FEATURE [App::FeaturePython] Elements019  # WARN: FeaturePython — macro-defined, semantics opaque (R4)
  Group = -> [Element088,Element089,Element090]
FEATURE [App::FeaturePython] Constraint130  label="PlaneAlignment104"  # WARN: FeaturePython — macro-defined, semantics opaque (R4)
  Angle = 0
  AnglePitch = 0
  AngleRoll = 0
  Cascade = false
  Disabled = false
  Group = -> [ElementLink260,ElementLink261]
  LockAngle = false
  _ConstraintType = 37
  _Parent = -> Constraints
FEATURE [App::FeaturePython] ElementLink260  label="_Element251"  # link proxy (typed FeaturePython)
  LinkTransform = true
  LinkedObject = -> _Element251
  _Parent = -> Constraint130
FEATURE [Part::FeaturePython] Element085  # link proxy (typed FeaturePython)
  Detach = false
  LinkTransform = true
  LinkedObject = -> Part__Mirroring003 [Face73]
  _Parent = -> Elements018
FEATURE [Part::FeaturePython] _Element251  # link proxy (typed FeaturePython)
  Detach = false
  LinkTransform = true
  LinkedObject = -> Assembly018 [1.$Element085.]
  _Parent = -> Elements
FEATURE [App::FeaturePython] ElementLink261  label="_Element003"  # link proxy (typed FeaturePython)
  LinkTransform = true
  LinkedObject = -> _Element003
  _Parent = -> Constraint130
FEATURE [App::FeaturePython] Constraint131  label="PlaneAlignment105"  # WARN: FeaturePython — macro-defined, semantics opaque (R4)
  Angle = 0
  AnglePitch = 0
  AngleRoll = 0
  Cascade = false
  Disabled = false
  Group = -> [ElementLink262,ElementLink263]
  LockAngle = false
  _ConstraintType = 37
  _Parent = -> Constraints
FEATURE [App::FeaturePython] ElementLink262  label="_Element252"  # link proxy (typed FeaturePython)
  LinkTransform = true
  LinkedObject = -> _Element252
  _Parent = -> Constraint131
FEATURE [Part::FeaturePython] Element086  # link proxy (typed FeaturePython)
  Detach = false
  LinkTransform = true
  LinkedObject = -> Part__Mirroring003 [Face76]
  _Parent = -> Elements018
FEATURE [Part::FeaturePython] _Element252  # link proxy (typed FeaturePython)
  Detach = false
  LinkTransform = true
  LinkedObject = -> Assembly018 [1.$Element086.]
  _Parent = -> Elements
FEATURE [App::FeaturePython] ElementLink263  label="_Element253"  # link proxy (typed FeaturePython)
  LinkTransform = true
  LinkedObject = -> _Element253
  _Parent = -> Constraint131
FEATURE [Part::FeaturePython] Element087  # link proxy (typed FeaturePython)
  Detach = false
  LinkTransform = true
  LinkedObject = -> Body027 [Fillet068.Face76]
  _Parent = -> Elements017
FEATURE [Part::FeaturePython] _Element253  # link proxy (typed FeaturePython)
  Detach = false
  LinkTransform = true
  LinkedObject = -> Assembly017 [1.$Element087.]
  _Parent = -> Elements
FEATURE [App::FeaturePython] Constraint132  label="PlaneAlignment106"  # WARN: FeaturePython — macro-defined, semantics opaque (R4)
  Angle = 0
  AnglePitch = 0
  AngleRoll = 0
  Cascade = false
  Disabled = false
  Group = -> [ElementLink264,ElementLink265]
  LockAngle = false
  _ConstraintType = 37
  _Parent = -> Constraints
FEATURE [App::FeaturePython] ElementLink264  label="_Element"  # link proxy (typed FeaturePython)
  LinkTransform = true
  LinkedObject = -> _Element
  _Parent = -> Constraint132
FEATURE [App::FeaturePython] ElementLink265  label="_Element254"  # link proxy (typed FeaturePython)
  LinkTransform = true
  LinkedObject = -> _Element254
  _Parent = -> Constraint132
FEATURE [Part::FeaturePython] Element088  # link proxy (typed FeaturePython)
  Detach = false
  LinkTransform = true
  LinkedObject = -> Part__Mirroring003001 [Face19]
  _Parent = -> Elements019
FEATURE [Part::FeaturePython] _Element254  # link proxy (typed FeaturePython)
  Detach = false
  LinkTransform = true
  LinkedObject = -> Assembly019 [1.$Element088.]
  _Parent = -> Elements
FEATURE [App::FeaturePython] Constraint133  label="PlaneAlignment107"  # WARN: FeaturePython — macro-defined, semantics opaque (R4)
  Angle = 0
  AnglePitch = 0
  AngleRoll = 0
  Cascade = false
  Disabled = false
  Group = -> [ElementLink266,ElementLink267]
  LockAngle = false
  _ConstraintType = 37
  _Parent = -> Constraints
FEATURE [App::FeaturePython] ElementLink266  label="_Element255"  # link proxy (typed FeaturePython)
  LinkTransform = true
  LinkedObject = -> _Element255
  _Parent = -> Constraint133
FEATURE [Part::FeaturePython] Element089  # link proxy (typed FeaturePython)
  Detach = false
  LinkTransform = true
  LinkedObject = -> Part__Mirroring003001 [Face73]
  _Parent = -> Elements019
FEATURE [Part::FeaturePython] _Element255  # link proxy (typed FeaturePython)
  Detach = false
  LinkTransform = true
  LinkedObject = -> Assembly019 [1.$Element089.]
  _Parent = -> Elements
FEATURE [App::FeaturePython] ElementLink267  label="_Element004"  # link proxy (typed FeaturePython)
  LinkTransform = true
  LinkedObject = -> _Element004
  _Parent = -> Constraint133
FEATURE [App::FeaturePython] Constraint134  label="PlaneAlignment108"  # WARN: FeaturePython — macro-defined, semantics opaque (R4)
  Angle = 0
  AnglePitch = 0
  AngleRoll = 0
  Cascade = false
  Disabled = false
  Group = -> [ElementLink268,ElementLink269]
  LockAngle = false
  Offset = 10
  _ConstraintType = 37
  _Parent = -> Constraints
FEATURE [App::FeaturePython] ElementLink268  label="_Element256"  # link proxy (typed FeaturePython)
  LinkTransform = true
  LinkedObject = -> _Element256
  _Parent = -> Constraint134
FEATURE [Part::FeaturePython] Element090  # link proxy (typed FeaturePython)
  Detach = false
  LinkTransform = true
  LinkedObject = -> Part__Mirroring003001 [Face76]
  _Parent = -> Elements019
FEATURE [Part::FeaturePython] _Element256  # link proxy (typed FeaturePython)
  Detach = false
  LinkTransform = true
  LinkedObject = -> Assembly019 [1.$Element090.]
  _Parent = -> Elements
FEATURE [App::FeaturePython] ElementLink269  label="_Element035"  # link proxy (typed FeaturePython)
  LinkTransform = true
  LinkedObject = -> _Element035
  _Parent = -> Constraint134
FEATURE [Part::FeaturePython] Assembly020  label="assy_electronics_assembly"  # WARN: FeaturePython — macro-defined, semantics opaque (R4)
  AutoRelax = true
  BuildShape = 0
  Freeze = false
  Group = -> [Constraints020,Elements020,Parts020]
  Verbose = false
  _SolverType = 1
  _Version = 1
FEATURE [App::FeaturePython] Constraints020  # WARN: FeaturePython — macro-defined, semantics opaque (R4)
  Group = -> [Constraint135,Constraint136,Constraint137,Constraint138,Constraint139,Constraint140,Constraint141,Constraint143,Constraint144,Constraint145,Constraint146]
  _Version = 1
FEATURE [App::FeaturePython] Elements020  # WARN: FeaturePython — macro-defined, semantics opaque (R4)
  Group = -> [_Element257,_Element258,_Element259,_Element260,_Element261,_Element262,_Element263,_Element264,_Element265,_Element266,_Element267,_Element268,_Element269,_Element270,_Element271,_Element272,_Element273,_Element274,_Element275,_Element276,_Element277,_Element278,_Element279,_Element280,_Element281,_Element282,_Element285,_Element286,_Element287,_Element288,_Element289,_Element290,_Element291,+1 more]
FEATURE [Part::FeaturePython] Parts020  # WARN: FeaturePython — macro-defined, semantics opaque (R4)
  Group = -> [Assembly021,Assembly023,Assembly022,Assembly025,Assembly024,Assembly026,Assembly027]
  GroupMode = 0
FEATURE [Part::FeaturePython] Assembly021  label="assy_servo_hat"  # WARN: FeaturePython — macro-defined, semantics opaque (R4)
  AutoRelax = true
  BuildShape = 0
  Freeze = false
  Group = -> [Constraints021,Elements021,Parts021]
  Placement = pos=(324.67,68.14,8.31) rot=(0.57735,-0.57735,-0.57735;2.0944rad)
  Verbose = false
  _SolverType = 1
  _Version = 1
FEATURE [App::FeaturePython] Elements021  # WARN: FeaturePython — macro-defined, semantics opaque (R4)
  Group = -> [Element098,Element100,Element101,Element104,Element105,Element112]
FEATURE [Part::FeaturePython] Assembly022  label="assy-raspberrry_pi_3Bplus"  # WARN: FeaturePython — macro-defined, semantics opaque (R4)
  AutoRelax = true
  BuildShape = 0
  Freeze = false
  Group = -> [Constraints022,Elements022,Parts022]
  Placement = pos=(339.87,3.13996,10.31) rot=(0,0,1;0rad)
  Verbose = false
  _SolverType = 1
  _Version = 1
FEATURE [App::FeaturePython] Elements022  # WARN: FeaturePython — macro-defined, semantics opaque (R4)
  Group = -> [Element091,Element093,Element095]
FEATURE [Part::FeaturePython] Assembly024  label="assy-electronics_case_cover"  # WARN: FeaturePython — macro-defined, semantics opaque (R4)
  AutoRelax = true
  BuildShape = 0
  Freeze = false
  Group = -> [Constraints024,Elements024,Parts024]
  Placement = pos=(309.67,-1.96004,42.31) rot=(0,0,1;0rad)
  Verbose = false
  _SolverType = 1
  _Version = 1
FEATURE [App::FeaturePython] Constraints024  # WARN: FeaturePython — macro-defined, semantics opaque (R4)
  Group = -> [Constraint142]
  _Version = 1
FEATURE [App::FeaturePython] Elements024  # WARN: FeaturePython — macro-defined, semantics opaque (R4)
  Group = -> [Element116,_Element283,_Element284,Element118,Element120,Element121,Element124]
FEATURE [Part::FeaturePython] Assembly025  label="assy-electronics_case_base"  # WARN: FeaturePython — macro-defined, semantics opaque (R4)
  AutoRelax = true
  BuildShape = 0
  Freeze = false
  Group = -> [Constraints025,Elements025,Parts025]
  Placement = pos=(309.67,-1.96004,4.81) rot=(0,0,1;0rad)
  Verbose = false
  _SolverType = 1
  _Version = 1
FEATURE [App::FeaturePython] Elements025  # WARN: FeaturePython — macro-defined, semantics opaque (R4)
  Group = -> [Element092,Element094,Element096,Element097,Element099,Element102,Element103,Element106,Element107,Element108,Element109,Element110,Element111,Element115,Element117,Element119]
FEATURE [Part::FeaturePython] Assembly026  label="assy-power_jack"  # WARN: FeaturePython — macro-defined, semantics opaque (R4)
  AutoRelax = true
  BuildShape = 0
  Freeze = false
  Group = -> [Constraints026,Elements026,Parts026]
  Placement = pos=(392.67,-1.96004,35.46) rot=(1,-0.000344,0.000344;1.5708rad)
  Verbose = false
  _SolverType = 1
  _Version = 1
FEATURE [App::FeaturePython] Elements026  # WARN: FeaturePython — macro-defined, semantics opaque (R4)
  Group = -> [Element122,Element123]
FEATURE [Part::FeaturePython] Element091  # link proxy (typed FeaturePython)
  Detach = false
  LinkTransform = true
  LinkedObject = -> Body030 [Pad081.Face15]
  _Parent = -> Elements022
FEATURE [Part::FeaturePython] _Element257  # link proxy (typed FeaturePython)
  Detach = false
  LinkTransform = true
  LinkedObject = -> Assembly022 [1.$Element091.]
  _Parent = -> Elements020
FEATURE [Part::FeaturePython] Element092  # link proxy (typed FeaturePython)
  Detach = false
  LinkTransform = true
  LinkedObject = -> Body033 [Pocket075.Face10]
  _Parent = -> Elements025
FEATURE [Part::FeaturePython] _Element258  # link proxy (typed FeaturePython)
  Detach = false
  LinkTransform = true
  LinkedObject = -> Assembly025 [1.$Element092.]
  _Parent = -> Elements020
FEATURE [Part::FeaturePython] Element093  # link proxy (typed FeaturePython)
  Detach = false
  LinkTransform = true
  LinkedObject = -> Body030 [Pad081.Face22]
  _Parent = -> Elements022
FEATURE [Part::FeaturePython] _Element259  # link proxy (typed FeaturePython)
  Detach = false
  LinkTransform = true
  LinkedObject = -> Assembly022 [1.$Element093.]
  _Parent = -> Elements020
FEATURE [Part::FeaturePython] Element094  # link proxy (typed FeaturePython)
  Detach = false
  LinkTransform = true
  LinkedObject = -> Body033 [Pocket075.Face13]
  _Parent = -> Elements025
FEATURE [Part::FeaturePython] _Element260  # link proxy (typed FeaturePython)
  Detach = false
  LinkTransform = true
  LinkedObject = -> Assembly025 [1.$Element094.]
  _Parent = -> Elements020
FEATURE [Part::FeaturePython] Element095  # link proxy (typed FeaturePython)
  Detach = false
  LinkTransform = true
  LinkedObject = -> Body030 [Pad081.Face2]
  _Parent = -> Elements022
FEATURE [Part::FeaturePython] _Element261  # link proxy (typed FeaturePython)
  Detach = false
  LinkTransform = true
  LinkedObject = -> Assembly022 [1.$Element095.]
  _Parent = -> Elements020
FEATURE [Part::FeaturePython] Element096  # link proxy (typed FeaturePython)
  Detach = false
  LinkTransform = true
  LinkedObject = -> Body033 [Pocket075.Face37]
  _Parent = -> Elements025
FEATURE [Part::FeaturePython] _Element262  # link proxy (typed FeaturePython)
  Detach = false
  LinkTransform = true
  LinkedObject = -> Assembly025 [1.$Element096.]
  _Parent = -> Elements020
FEATURE [Part::FeaturePython] Element097  # link proxy (typed FeaturePython)
  Detach = false
  LinkTransform = true
  LinkedObject = -> Body033 [Pocket076.Face47]
  _Parent = -> Elements025
FEATURE [Part::FeaturePython] _Element263  # link proxy (typed FeaturePython)
  Detach = false
  LinkTransform = true
  LinkedObject = -> Assembly025 [1.$Element097.]
  _Parent = -> Elements020
FEATURE [Part::FeaturePython] Element098  # link proxy (typed FeaturePython)
  Detach = false
  LinkTransform = true
  LinkedObject = -> Body029 [Pad072.Face10]
  _Parent = -> Elements021
FEATURE [Part::FeaturePython] _Element264  # link proxy (typed FeaturePython)
  Detach = false
  LinkTransform = true
  LinkedObject = -> Assembly021 [1.$Element098.]
  _Parent = -> Elements020
FEATURE [Part::FeaturePython] Element099  # link proxy (typed FeaturePython)
  Detach = false
  LinkTransform = true
  LinkedObject = -> Body033 [Pocket076.Face46]
  _Parent = -> Elements025
FEATURE [Part::FeaturePython] _Element265  # link proxy (typed FeaturePython)
  Detach = false
  LinkTransform = true
  LinkedObject = -> Assembly025 [1.$Element099.]
  _Parent = -> Elements020
FEATURE [Part::FeaturePython] Element100  # link proxy (typed FeaturePython)
  Detach = false
  LinkTransform = true
  LinkedObject = -> Body029 [Pad072.Face11]
  _Parent = -> Elements021
FEATURE [Part::FeaturePython] _Element266  # link proxy (typed FeaturePython)
  Detach = false
  LinkTransform = true
  LinkedObject = -> Assembly021 [1.$Element100.]
  _Parent = -> Elements020
FEATURE [Part::FeaturePython] Element101  # link proxy (typed FeaturePython)
  Detach = false
  LinkTransform = true
  LinkedObject = -> Body029 [Pad072.Face4]
  _Parent = -> Elements021
FEATURE [Part::FeaturePython] _Element267  # link proxy (typed FeaturePython)
  Detach = false
  LinkTransform = true
  LinkedObject = -> Assembly021 [1.$Element101.]
  _Parent = -> Elements020
FEATURE [Part::FeaturePython] Element102  # link proxy (typed FeaturePython)
  Detach = false
  LinkTransform = true
  LinkedObject = -> Body033 [Pocket076.Face21]
  _Parent = -> Elements025
FEATURE [Part::FeaturePython] _Element268  # link proxy (typed FeaturePython)
  Detach = false
  LinkTransform = true
  LinkedObject = -> Assembly025 [1.$Element102.]
  _Parent = -> Elements020
FEATURE [Part::FeaturePython] Element103  # link proxy (typed FeaturePython)
  Detach = false
  LinkTransform = true
  LinkedObject = -> Body033 [Pocket076.Face50]
  _Parent = -> Elements025
FEATURE [Part::FeaturePython] _Element269  # link proxy (typed FeaturePython)
  Detach = false
  LinkTransform = true
  LinkedObject = -> Assembly025 [1.$Element103.]
  _Parent = -> Elements020
FEATURE [Part::FeaturePython] Element104  # link proxy (typed FeaturePython)
  Detach = false
  LinkTransform = true
  LinkedObject = -> Body029 [Pad072.Face16]
  _Parent = -> Elements021
FEATURE [Part::FeaturePython] _Element270  # link proxy (typed FeaturePython)
  Detach = false
  LinkTransform = true
  LinkedObject = -> Assembly021 [1.$Element104.]
  _Parent = -> Elements020
FEATURE [Part::FeaturePython] Element105  # link proxy (typed FeaturePython)
  Detach = false
  LinkTransform = true
  LinkedObject = -> Body029 [Pad072.Face9]
  _Parent = -> Elements021
FEATURE [Part::FeaturePython] _Element271  # link proxy (typed FeaturePython)
  Detach = false
  LinkTransform = true
  LinkedObject = -> Assembly021 [1.$Element105.]
  _Parent = -> Elements020
FEATURE [Part::FeaturePython] Element106  # link proxy (typed FeaturePython)
  Detach = false
  LinkTransform = true
  LinkedObject = -> Body033 [Pocket076.Face10]
  _Parent = -> Elements025
FEATURE [Part::FeaturePython] _Element272  # link proxy (typed FeaturePython)
  Detach = false
  LinkTransform = true
  LinkedObject = -> Assembly025 [1.$Element106.]
  _Parent = -> Elements020
FEATURE [Part::FeaturePython] Element107  # link proxy (typed FeaturePython)
  Detach = false
  LinkTransform = true
  LinkedObject = -> Body033 [Pocket076.Face13]
  _Parent = -> Elements025
FEATURE [Part::FeaturePython] _Element273  # link proxy (typed FeaturePython)
  Detach = false
  LinkTransform = true
  LinkedObject = -> Assembly025 [1.$Element107.]
  _Parent = -> Elements020
FEATURE [Part::FeaturePython] Element108  # link proxy (typed FeaturePython)
  Detach = false
  LinkTransform = true
  LinkedObject = -> Body033 [Pocket076.Face37]
  _Parent = -> Elements025
FEATURE [Part::FeaturePython] _Element274  # link proxy (typed FeaturePython)
  Detach = false
  LinkTransform = true
  LinkedObject = -> Assembly025 [1.$Element108.]
  _Parent = -> Elements020
FEATURE [App::FeaturePython] Constraint135  label="AxialAlignment013"  # WARN: FeaturePython — macro-defined, semantics opaque (R4)
  Angle = 0
  AnglePitch = 0
  AngleRoll = 0
  Disabled = false
  Group = -> [ElementLink270,ElementLink271]
  LockAngle = false
  Multiply = false
  _ConstraintType = 36
  _Parent = -> Constraints020
FEATURE [App::FeaturePython] ElementLink270  label="_Element272"  # link proxy (typed FeaturePython)
  LinkTransform = true
  LinkedObject = -> _Element272
  _Parent = -> Constraint135
FEATURE [App::FeaturePython] ElementLink271  label="_Element257"  # link proxy (typed FeaturePython)
  LinkTransform = true
  LinkedObject = -> _Element257
  _Parent = -> Constraint135
FEATURE [App::FeaturePython] Constraint136  label="AxialAlignment014"  # WARN: FeaturePython — macro-defined, semantics opaque (R4)
  Angle = 0
  AnglePitch = 0
  AngleRoll = 0
  Disabled = false
  Group = -> [ElementLink272,ElementLink273]
  LockAngle = false
  Multiply = false
  _ConstraintType = 36
  _Parent = -> Constraints020
FEATURE [App::FeaturePython] ElementLink272  label="_Element273"  # link proxy (typed FeaturePython)
  LinkTransform = true
  LinkedObject = -> _Element273
  _Parent = -> Constraint136
FEATURE [App::FeaturePython] ElementLink273  label="_Element259"  # link proxy (typed FeaturePython)
  LinkTransform = true
  LinkedObject = -> _Element259
  _Parent = -> Constraint136
FEATURE [App::FeaturePython] Constraint137  label="PlaneAlignment109"  # WARN: FeaturePython — macro-defined, semantics opaque (R4)
  Angle = 0
  AnglePitch = 0
  AngleRoll = 0
  Cascade = false
  Disabled = false
  Group = -> [ElementLink274,ElementLink275]
  LockAngle = false
  _ConstraintType = 37
  _Parent = -> Constraints020
FEATURE [App::FeaturePython] ElementLink274  label="_Element275"  # link proxy (typed FeaturePython)
  LinkTransform = true
  LinkedObject = -> _Element275
  _Parent = -> Constraint137
FEATURE [Part::FeaturePython] Element109  # link proxy (typed FeaturePython)
  Detach = false
  LinkTransform = true
  LinkedObject = -> Body033 [Pocket076.Face38]
  _Parent = -> Elements025
FEATURE [Part::FeaturePython] _Element275  # link proxy (typed FeaturePython)
  Detach = false
  LinkTransform = true
  LinkedObject = -> Assembly025 [1.$Element109.]
  _Parent = -> Elements020
FEATURE [App::FeaturePython] ElementLink275  label="_Element261"  # link proxy (typed FeaturePython)
  LinkTransform = true
  LinkedObject = -> _Element261
  _Parent = -> Constraint137
FEATURE [App::FeaturePython] Constraint138  label="AxialAlignment015"  # WARN: FeaturePython — macro-defined, semantics opaque (R4)
  Angle = 0
  AnglePitch = 0
  AngleRoll = 0
  Disabled = false
  Group = -> [ElementLink276,ElementLink277]
  LockAngle = false
  Multiply = false
  _ConstraintType = 36
  _Parent = -> Constraints020
FEATURE [App::FeaturePython] ElementLink276  label="_Element276"  # link proxy (typed FeaturePython)
  LinkTransform = true
  LinkedObject = -> _Element276
  _Parent = -> Constraint138
FEATURE [Part::FeaturePython] Element110  # link proxy (typed FeaturePython)
  Detach = false
  LinkTransform = true
  LinkedObject = -> Body033 [Pocket076.Face45]
  _Parent = -> Elements025
FEATURE [Part::FeaturePython] _Element276  # link proxy (typed FeaturePython)
  Detach = false
  LinkTransform = true
  LinkedObject = -> Assembly025 [1.$Element110.]
  _Parent = -> Elements020
FEATURE [App::FeaturePython] ElementLink277  label="_Element270"  # link proxy (typed FeaturePython)
  LinkTransform = true
  LinkedObject = -> _Element270
  _Parent = -> Constraint138
FEATURE [App::FeaturePython] Constraint139  label="AxialAlignment016"  # WARN: FeaturePython — macro-defined, semantics opaque (R4)
  Angle = 0
  AnglePitch = 0
  AngleRoll = 0
  Disabled = false
  Group = -> [ElementLink278,ElementLink279]
  LockAngle = false
  Multiply = false
  _ConstraintType = 36
  _Parent = -> Constraints020
FEATURE [App::FeaturePython] ElementLink278  label="_Element277"  # link proxy (typed FeaturePython)
  LinkTransform = true
  LinkedObject = -> _Element277
  _Parent = -> Constraint139
FEATURE [Part::FeaturePython] Element111  # link proxy (typed FeaturePython)
  Detach = false
  LinkTransform = true
  LinkedObject = -> Body033 [Pocket076.Face42]
  _Parent = -> Elements025
FEATURE [Part::FeaturePython] _Element277  # link proxy (typed FeaturePython)
  Detach = false
  LinkTransform = true
  LinkedObject = -> Assembly025 [1.$Element111.]
  _Parent = -> Elements020
FEATURE [App::FeaturePython] ElementLink279  label="_Element271"  # link proxy (typed FeaturePython)
  LinkTransform = true
  LinkedObject = -> _Element271
  _Parent = -> Constraint139
FEATURE [App::FeaturePython] Constraint140  label="PlaneAlignment110"  # WARN: FeaturePython — macro-defined, semantics opaque (R4)
  Angle = 0
  AnglePitch = 0
  AngleRoll = 0
  Cascade = false
  Disabled = false
  Group = -> [ElementLink280,ElementLink281]
  LockAngle = false
  _ConstraintType = 37
  _Parent = -> Constraints020
FEATURE [App::FeaturePython] ElementLink280  label="_Element268"  # link proxy (typed FeaturePython)
  LinkTransform = true
  LinkedObject = -> _Element268
  _Parent = -> Constraint140
FEATURE [App::FeaturePython] ElementLink281  label="_Element267"  # link proxy (typed FeaturePython)
  LinkTransform = true
  LinkedObject = -> _Element267
  _Parent = -> Constraint140
FEATURE [Part::FeaturePython] Element112  # link proxy (typed FeaturePython)
  Detach = false
  LinkTransform = true
  LinkedObject = -> Body029 [Pad072.Face5]
  _Parent = -> Elements021
FEATURE [Part::FeaturePython] _Element278  # link proxy (typed FeaturePython)
  Detach = false
  LinkTransform = true
  LinkedObject = -> Assembly021 [1.$Element112.]
  _Parent = -> Elements020
FEATURE [Part::FeaturePython] Assembly027  label="assy-M3_screw"  # WARN: FeaturePython — macro-defined, semantics opaque (R4)
  AutoRelax = true
  BuildShape = 0
  Freeze = false
  Group = -> [Constraints027,Elements027,Parts027]
  Placement = pos=(320,6.62997,12.11) rot=(0,1,0;1.5708rad)
  Verbose = false
  _SolverType = 1
  _Version = 1
FEATURE [App::FeaturePython] Elements027  # WARN: FeaturePython — macro-defined, semantics opaque (R4)
  Group = -> [Element113,Element114]
FEATURE [Part::FeaturePython] Element113  # link proxy (typed FeaturePython)
  Detach = false
  LinkTransform = true
  LinkedObject = -> Body035 [Pocket078.Face10]
  _Parent = -> Elements027
FEATURE [Part::FeaturePython] _Element279  # link proxy (typed FeaturePython)
  Detach = false
  LinkTransform = true
  LinkedObject = -> Assembly027 [1.$Element113.]
  _Parent = -> Elements020
FEATURE [Part::FeaturePython] Element114  # link proxy (typed FeaturePython)
  Detach = false
  LinkTransform = true
  LinkedObject = -> Body035 [Pocket078.Face1]
  _Parent = -> Elements027
FEATURE [Part::FeaturePython] _Element280  # link proxy (typed FeaturePython)
  Detach = false
  LinkTransform = true
  LinkedObject = -> Assembly027 [1.$Element114.]
  _Parent = -> Elements020
FEATURE [App::FeaturePython] Constraint141  label="PlaneAlignment111"  # WARN: FeaturePython — macro-defined, semantics opaque (R4)
  Angle = 0
  AnglePitch = 0
  AngleRoll = 0
  Cascade = false
  Disabled = false
  Group = -> [ElementLink282,ElementLink283]
  LockAngle = false
  _ConstraintType = 37
  _Parent = -> Constraints020
FEATURE [App::FeaturePython] ElementLink282  label="_Element281"  # link proxy (typed FeaturePython)
  LinkTransform = true
  LinkedObject = -> _Element281
  _Parent = -> Constraint141
FEATURE [Part::FeaturePython] Element115  # link proxy (typed FeaturePython)
  Detach = false
  LinkTransform = true
  LinkedObject = -> Body033 [Pad093.Face34]
  _Parent = -> Elements025
FEATURE [Part::FeaturePython] _Element281  # link proxy (typed FeaturePython)
  Detach = false
  LinkTransform = true
  LinkedObject = -> Assembly025 [1.$Element115.]
  _Parent = -> Elements020
FEATURE [App::FeaturePython] ElementLink283  label="_Element282"  # link proxy (typed FeaturePython)
  LinkTransform = true
  LinkedObject = -> _Element282
  _Parent = -> Constraint141
FEATURE [Part::FeaturePython] Element116  # link proxy (typed FeaturePython)
  Detach = false
  LinkTransform = true
  LinkedObject = -> Body032 [Pad086.Face6]
  _Parent = -> Elements024
FEATURE [Part::FeaturePython] _Element282  # link proxy (typed FeaturePython)
  Detach = false
  LinkTransform = true
  LinkedObject = -> Assembly024 [1.$Element116.]
  _Parent = -> Elements020
FEATURE [App::FeaturePython] Constraint142  label="PlaneAlignment112"  # WARN: FeaturePython — macro-defined, semantics opaque (R4)
  Angle = 0
  AnglePitch = 0
  AngleRoll = 0
  Cascade = false
  Disabled = false
  Group = -> [ElementLink284,ElementLink285]
  LockAngle = false
  _ConstraintType = 37
  _Parent = -> Constraints024
FEATURE [App::FeaturePython] ElementLink284  label="_Element283"  # link proxy (typed FeaturePython)
  LinkTransform = true
  LinkedObject = -> _Element283
  _Parent = -> Constraint142
FEATURE [Part::FeaturePython] _Element283  # link proxy (typed FeaturePython)
  Detach = false
  LinkTransform = true
  LinkedObject = -> Body032 [Pad086.Face9]
  _Parent = -> Elements024
FEATURE [App::FeaturePython] ElementLink285  label="_Element284"  # link proxy (typed FeaturePython)
  LinkTransform = true
  LinkedObject = -> _Element284
  _Parent = -> Constraint142
FEATURE [Part::FeaturePython] _Element284  # link proxy (typed FeaturePython)
  Detach = false
  LinkTransform = true
  LinkedObject = -> Body032 [Pad086.Face3]
  _Parent = -> Elements024
FEATURE [App::FeaturePython] Constraint143  label="PlaneAlignment113"  # WARN: FeaturePython — macro-defined, semantics opaque (R4)
  Angle = 0
  AnglePitch = 0
  AngleRoll = 0
  Cascade = false
  Disabled = false
  Group = -> [ElementLink286,ElementLink287]
  LockAngle = false
  _ConstraintType = 37
  _Parent = -> Constraints020
FEATURE [App::FeaturePython] ElementLink286  label="_Element285"  # link proxy (typed FeaturePython)
  LinkTransform = true
  LinkedObject = -> _Element285
  _Parent = -> Constraint143
FEATURE [Part::FeaturePython] Element117  # link proxy (typed FeaturePython)
  Detach = false
  LinkTransform = true
  LinkedObject = -> Body033 [Pad093.Face35]
  _Parent = -> Elements025
FEATURE [Part::FeaturePython] _Element285  # link proxy (typed FeaturePython)
  Detach = false
  LinkTransform = true
  LinkedObject = -> Assembly025 [1.$Element117.]
  _Parent = -> Elements020
FEATURE [App::FeaturePython] ElementLink287  label="_Element286"  # link proxy (typed FeaturePython)
  LinkTransform = true
  LinkedObject = -> _Element286
  _Parent = -> Constraint143
FEATURE [Part::FeaturePython] Element118  # link proxy (typed FeaturePython)
  Detach = false
  LinkTransform = true
  LinkedObject = -> Body032 [Pad086.Face7]
  _Parent = -> Elements024
FEATURE [Part::FeaturePython] _Element286  # link proxy (typed FeaturePython)
  Detach = false
  LinkTransform = true
  LinkedObject = -> Assembly024 [1.$Element118.]
  _Parent = -> Elements020
FEATURE [Part::FeaturePython] Element119  # link proxy (typed FeaturePython)
  Detach = false
  LinkTransform = true
  LinkedObject = -> Body033 [Pad093.Face3]
  _Parent = -> Elements025
FEATURE [Part::FeaturePython] _Element287  # link proxy (typed FeaturePython)
  Detach = false
  LinkTransform = true
  LinkedObject = -> Assembly025 [1.$Element119.]
  _Parent = -> Elements020
FEATURE [Part::FeaturePython] Element120  # link proxy (typed FeaturePython)
  Detach = false
  LinkTransform = true
  LinkedObject = -> Body032 [Pocket079.Face9]
  _Parent = -> Elements024
FEATURE [Part::FeaturePython] _Element288  # link proxy (typed FeaturePython)
  Detach = false
  LinkTransform = true
  LinkedObject = -> Assembly024 [1.$Element120.]
  _Parent = -> Elements020
FEATURE [App::FeaturePython] Constraint144  label="PlaneAlignment114"  # WARN: FeaturePython — macro-defined, semantics opaque (R4)
  Angle = 0
  AnglePitch = 0
  AngleRoll = 0
  Cascade = false
  Disabled = false
  Group = -> [ElementLink288,ElementLink289]
  LockAngle = false
  _ConstraintType = 37
  _Parent = -> Constraints020
FEATURE [App::FeaturePython] ElementLink288  label="_Element287"  # link proxy (typed FeaturePython)
  LinkTransform = true
  LinkedObject = -> _Element287
  _Parent = -> Constraint144
FEATURE [App::FeaturePython] ElementLink289  label="_Element288"  # link proxy (typed FeaturePython)
  LinkTransform = true
  LinkedObject = -> _Element288
  _Parent = -> Constraint144
FEATURE [App::FeaturePython] Constraint145  label="AxialAlignment017"  # WARN: FeaturePython — macro-defined, semantics opaque (R4)
  Angle = 0
  AnglePitch = 0
  AngleRoll = 0
  Disabled = false
  Group = -> [ElementLink290,ElementLink291]
  LockAngle = false
  Multiply = false
  _ConstraintType = 36
  _Parent = -> Constraints020
FEATURE [App::FeaturePython] ElementLink290  label="_Element289"  # link proxy (typed FeaturePython)
  LinkTransform = true
  LinkedObject = -> _Element289
  _Parent = -> Constraint145
FEATURE [Part::FeaturePython] Element121  # link proxy (typed FeaturePython)
  Detach = false
  LinkTransform = true
  LinkedObject = -> Body032 [Pocket080.Face23]
  _Parent = -> Elements024
FEATURE [Part::FeaturePython] _Element289  # link proxy (typed FeaturePython)
  Detach = false
  LinkTransform = true
  LinkedObject = -> Assembly024 [1.$Element121.]
  _Parent = -> Elements020
FEATURE [App::FeaturePython] ElementLink291  label="_Element290"  # link proxy (typed FeaturePython)
  LinkTransform = true
  LinkedObject = -> _Element290
  _Parent = -> Constraint145
FEATURE [Part::FeaturePython] Element122  # link proxy (typed FeaturePython)
  Detach = false
  LinkTransform = true
  LinkedObject = -> Body034 [Pad090.Face4]
  _Parent = -> Elements026
FEATURE [Part::FeaturePython] _Element290  # link proxy (typed FeaturePython)
  Detach = false
  LinkTransform = true
  LinkedObject = -> Assembly026 [1.$Element122.]
  _Parent = -> Elements020
FEATURE [App::FeaturePython] Constraint146  label="PlaneAlignment115"  # WARN: FeaturePython — macro-defined, semantics opaque (R4)
  Angle = 0
  AnglePitch = 0
  AngleRoll = 0
  Cascade = false
  Disabled = false
  Group = -> [ElementLink292,ElementLink293]
  LockAngle = false
  _ConstraintType = 37
  _Parent = -> Constraints020
FEATURE [App::FeaturePython] ElementLink292  label="_Element291"  # link proxy (typed FeaturePython)
  LinkTransform = true
  LinkedObject = -> _Element291
  _Parent = -> Constraint146
FEATURE [Part::FeaturePython] Element123  # link proxy (typed FeaturePython)
  Detach = false
  LinkTransform = true
  LinkedObject = -> Body034 [Pad090.Face2]
  _Parent = -> Elements026
FEATURE [Part::FeaturePython] _Element291  # link proxy (typed FeaturePython)
  Detach = false
  LinkTransform = true
  LinkedObject = -> Assembly026 [1.$Element123.]
  _Parent = -> Elements020
FEATURE [App::FeaturePython] ElementLink293  label="_Element292"  # link proxy (typed FeaturePython)
  LinkTransform = true
  LinkedObject = -> _Element292
  _Parent = -> Constraint146
FEATURE [Part::FeaturePython] Element124  # link proxy (typed FeaturePython)
  Detach = false
  LinkTransform = true
  LinkedObject = -> Body032 [Pocket080.Face4]
  _Parent = -> Elements024
FEATURE [Part::FeaturePython] _Element292  # link proxy (typed FeaturePython)
  Detach = false
  LinkTransform = true
  LinkedObject = -> Assembly024 [1.$Element124.]
  _Parent = -> Elements020
FEATURE [Part::FeaturePython] Assembly028  label="assy-lock_servo"  # WARN: FeaturePython — macro-defined, semantics opaque (R4)
  AutoRelax = true
  BuildShape = 0
  Freeze = false
  Group = -> [Constraints028,Elements028,Parts028]
  Placement = pos=(-22.0001,-451.494,60.25) rot=(0.57735,0.57735,-0.57735;2.0944rad)
  Verbose = false
  _SolverType = 1
  _Version = 1
FEATURE [App::FeaturePython] Elements028  # WARN: FeaturePython — macro-defined, semantics opaque (R4)
  Group = -> [Element131,Element132,Element133,Element136,Element137]
FEATURE [Part::FeaturePython] Assembly030  label="assy-orthogonal_brace_v2_RL"  # WARN: FeaturePython — macro-defined, semantics opaque (R4)
  AutoRelax = true
  BuildShape = 0
  Freeze = false
  Group = -> [Constraints030,Elements030,Parts030]
  Placement = pos=(16.9999,-465.994,2.59e-13) rot=(0,0,1;3.14159rad)
  Verbose = false
  _SolverType = 1
  _Version = 1
FEATURE [App::FeaturePython] Elements030  # WARN: FeaturePython — macro-defined, semantics opaque (R4)
  Group = -> [Element128,Element129,Element130]
FEATURE [Part::FeaturePython] Assembly031  label="assy-orthogonal_brace_v2_FL"  # WARN: FeaturePython — macro-defined, semantics opaque (R4)
  AutoRelax = true
  BuildShape = 0
  Freeze = false
  Group = -> [Constraints031,Elements031,Parts031]
  Placement = pos=(16.9999,-485.994,-3.18194e-08) rot=(0,0,1;3.14159rad)
  Verbose = false
  _SolverType = 1
  _Version = 1
FEATURE [App::FeaturePython] Elements031  # WARN: FeaturePython — macro-defined, semantics opaque (R4)
  Group = -> [Element125,Element126,Element127]
FEATURE [App::FeaturePython] Constraint147  label="PlaneAlignment116"  # WARN: FeaturePython — macro-defined, semantics opaque (R4)
  Angle = 0
  AnglePitch = 0
  AngleRoll = 0
  Cascade = false
  Disabled = false
  Group = -> [ElementLink294,ElementLink295]
  LockAngle = false
  _ConstraintType = 37
  _Parent = -> Constraints
FEATURE [App::FeaturePython] ElementLink294  label="_Element024"  # link proxy (typed FeaturePython)
  LinkTransform = true
  LinkedObject = -> _Element024
  _Parent = -> Constraint147
FEATURE [App::FeaturePython] ElementLink295  label="_Element293"  # link proxy (typed FeaturePython)
  LinkTransform = true
  LinkedObject = -> _Element293
  _Parent = -> Constraint147
FEATURE [Part::FeaturePython] Element125  # link proxy (typed FeaturePython)
  Detach = false
  LinkTransform = true
  LinkedObject = -> Body026001 [Face71]
  _Parent = -> Elements031
FEATURE [Part::FeaturePython] _Element293  # link proxy (typed FeaturePython)
  Detach = false
  LinkTransform = true
  LinkedObject = -> Assembly031 [1.$Element125.]
  _Parent = -> Elements
FEATURE [App::FeaturePython] Constraint148  label="PlaneAlignment117"  # WARN: FeaturePython — macro-defined, semantics opaque (R4)
  Angle = 0
  AnglePitch = 0
  AngleRoll = 0
  Cascade = false
  Disabled = false
  Group = -> [ElementLink296,ElementLink297]
  LockAngle = false
  _ConstraintType = 37
  _Parent = -> Constraints
FEATURE [App::FeaturePython] ElementLink296  label="_Element294"  # link proxy (typed FeaturePython)
  LinkTransform = true
  LinkedObject = -> _Element294
  _Parent = -> Constraint148
FEATURE [Part::FeaturePython] Element126  # link proxy (typed FeaturePython)
  Detach = false
  LinkTransform = true
  LinkedObject = -> Body026001 [Face37]
  _Parent = -> Elements031
FEATURE [Part::FeaturePython] _Element294  # link proxy (typed FeaturePython)
  Detach = false
  LinkTransform = true
  LinkedObject = -> Assembly031 [1.$Element126.]
  _Parent = -> Elements
FEATURE [App::FeaturePython] ElementLink297  label="_Element010"  # link proxy (typed FeaturePython)
  LinkTransform = true
  LinkedObject = -> _Element010
  _Parent = -> Constraint148
FEATURE [App::FeaturePython] Constraint149  label="PlaneAlignment118"  # WARN: FeaturePython — macro-defined, semantics opaque (R4)
  Angle = 0
  AnglePitch = 0
  AngleRoll = 0
  Cascade = false
  Disabled = false
  Group = -> [ElementLink298,ElementLink299]
  LockAngle = false
  _ConstraintType = 37
  _Parent = -> Constraints
FEATURE [App::FeaturePython] ElementLink298  label="_Element295"  # link proxy (typed FeaturePython)
  LinkTransform = true
  LinkedObject = -> _Element295
  _Parent = -> Constraint149
FEATURE [Part::FeaturePython] Element127  # link proxy (typed FeaturePython)
  Detach = false
  LinkTransform = true
  LinkedObject = -> Body026001 [Face6]
  _Parent = -> Elements031
FEATURE [Part::FeaturePython] _Element295  # link proxy (typed FeaturePython)
  Detach = false
  LinkTransform = true
  LinkedObject = -> Assembly031 [1.$Element127.]
  _Parent = -> Elements
FEATURE [App::FeaturePython] ElementLink299  label="_Element029"  # link proxy (typed FeaturePython)
  LinkTransform = true
  LinkedObject = -> _Element029
  _Parent = -> Constraint149
FEATURE [App::FeaturePython] Constraint150  label="PlaneAlignment119"  # WARN: FeaturePython — macro-defined, semantics opaque (R4)
  Angle = 0
  AnglePitch = 0
  AngleRoll = 0
  Cascade = false
  Disabled = false
  Group = -> [ElementLink300,ElementLink301]
  LockAngle = false
  _ConstraintType = 37
  _Parent = -> Constraints
FEATURE [App::FeaturePython] ElementLink300  label="_Element296"  # link proxy (typed FeaturePython)
  LinkTransform = true
  LinkedObject = -> _Element296
  _Parent = -> Constraint150
FEATURE [Part::FeaturePython] Element128  # link proxy (typed FeaturePython)
  Detach = false
  LinkTransform = true
  LinkedObject = -> Part__Mirroring002001 [Face71]
  _Parent = -> Elements030
FEATURE [Part::FeaturePython] _Element296  # link proxy (typed FeaturePython)
  Detach = false
  LinkTransform = true
  LinkedObject = -> Assembly030 [1.$Element128.]
  _Parent = -> Elements
FEATURE [App::FeaturePython] ElementLink301  label="_Element030"  # link proxy (typed FeaturePython)
  LinkTransform = true
  LinkedObject = -> _Element030
  _Parent = -> Constraint150
FEATURE [App::FeaturePython] Constraint151  label="PlaneAlignment120"  # WARN: FeaturePython — macro-defined, semantics opaque (R4)
  Angle = 0
  AnglePitch = 0
  AngleRoll = 0
  Cascade = false
  Disabled = false
  Group = -> [ElementLink302,ElementLink303]
  LockAngle = false
  _ConstraintType = 37
  _Parent = -> Constraints
FEATURE [App::FeaturePython] ElementLink302  label="_Element297"  # link proxy (typed FeaturePython)
  LinkTransform = true
  LinkedObject = -> _Element297
  _Parent = -> Constraint151
FEATURE [Part::FeaturePython] Element129  # link proxy (typed FeaturePython)
  Detach = false
  LinkTransform = true
  LinkedObject = -> Part__Mirroring002001 [Face37]
  _Parent = -> Elements030
FEATURE [Part::FeaturePython] _Element297  # link proxy (typed FeaturePython)
  Detach = false
  LinkTransform = true
  LinkedObject = -> Assembly030 [1.$Element129.]
  _Parent = -> Elements
FEATURE [App::FeaturePython] ElementLink303  label="_Element010"  # link proxy (typed FeaturePython)
  LinkTransform = true
  LinkedObject = -> _Element010
  _Parent = -> Constraint151
FEATURE [App::FeaturePython] Constraint152  label="PlaneAlignment121"  # WARN: FeaturePython — macro-defined, semantics opaque (R4)
  Angle = 0
  AnglePitch = 0
  AngleRoll = 0
  Cascade = false
  Disabled = false
  Group = -> [ElementLink304,ElementLink305]
  LockAngle = false
  _ConstraintType = 37
  _Parent = -> Constraints
FEATURE [App::FeaturePython] ElementLink304  label="_Element029"  # link proxy (typed FeaturePython)
  LinkTransform = true
  LinkedObject = -> _Element029
  _Parent = -> Constraint152
FEATURE [App::FeaturePython] ElementLink305  label="_Element298"  # link proxy (typed FeaturePython)
  LinkTransform = true
  LinkedObject = -> _Element298
  _Parent = -> Constraint152
FEATURE [Part::FeaturePython] Element130  # link proxy (typed FeaturePython)
  Detach = false
  LinkTransform = true
  LinkedObject = -> Part__Mirroring002001 [Face6]
  _Parent = -> Elements030
FEATURE [Part::FeaturePython] _Element298  # link proxy (typed FeaturePython)
  Detach = false
  LinkTransform = true
  LinkedObject = -> Assembly030 [1.$Element130.]
  _Parent = -> Elements
FEATURE [Part::FeaturePython] Assembly032  label="assy-lock_body-left"  # WARN: FeaturePython — macro-defined, semantics opaque (R4)
  AutoRelax = true
  BuildShape = 0
  Freeze = false
  Group = -> [Constraints032,Elements032,Parts032]
  Placement = pos=(8.49993,-465.994,28.02) rot=(0,0,1;0rad)
  Verbose = false
  _SolverType = 1
  _Version = 1
FEATURE [App::FeaturePython] Elements032  # WARN: FeaturePython — macro-defined, semantics opaque (R4)
  Group = -> [Element134,Element135,Element138]
FEATURE [App::FeaturePython] Constraint153  label="PlaneAlignment122"  # WARN: FeaturePython — macro-defined, semantics opaque (R4)
  Angle = 0
  AnglePitch = 0
  AngleRoll = 0
  Cascade = false
  Disabled = false
  Group = -> [ElementLink306,ElementLink307]
  LockAngle = false
  _ConstraintType = 37
  _Parent = -> Constraints
FEATURE [App::FeaturePython] ElementLink306  label="_Element299"  # link proxy (typed FeaturePython)
  LinkTransform = true
  LinkedObject = -> _Element299
  _Parent = -> Constraint153
FEATURE [Part::FeaturePython] Element131  # link proxy (typed FeaturePython)
  Detach = false
  LinkTransform = true
  LinkedObject = -> Link018 [Face337]
  _Parent = -> Elements028
FEATURE [Part::FeaturePython] _Element299  # link proxy (typed FeaturePython)
  Detach = false
  LinkTransform = true
  LinkedObject = -> Assembly028 [1.$Element131.]
  _Parent = -> Elements
FEATURE [App::FeaturePython] ElementLink307  label="_Element300"  # link proxy (typed FeaturePython)
  LinkTransform = true
  LinkedObject = -> _Element300
  _Parent = -> Constraint153
FEATURE [Part::FeaturePython] _Element300  # link proxy (typed FeaturePython)
  Detach = false
  LinkTransform = true
  LinkedObject = -> Link007 [Face106]
  _Parent = -> Elements
FEATURE [App::FeaturePython] Constraint154  label="PlaneAlignment123"  # WARN: FeaturePython — macro-defined, semantics opaque (R4)
  Angle = 0
  AnglePitch = 0
  AngleRoll = 0
  Cascade = false
  Disabled = false
  Group = -> [ElementLink308,ElementLink309]
  LockAngle = false
  Offset = 4.5
  _ConstraintType = 37
  _Parent = -> Constraints
FEATURE [App::FeaturePython] ElementLink308  label="_Element301"  # link proxy (typed FeaturePython)
  LinkTransform = true
  LinkedObject = -> _Element301
  _Parent = -> Constraint154
FEATURE [Part::FeaturePython] Element132  # link proxy (typed FeaturePython)
  Detach = false
  LinkTransform = true
  LinkedObject = -> Link018 [Face154]
  _Parent = -> Elements028
FEATURE [Part::FeaturePython] _Element301  # link proxy (typed FeaturePython)
  Detach = false
  LinkTransform = true
  LinkedObject = -> Assembly028 [1.$Element132.]
  _Parent = -> Elements
FEATURE [App::FeaturePython] ElementLink309  label="_Element030"  # link proxy (typed FeaturePython)
  LinkTransform = true
  LinkedObject = -> _Element030
  _Parent = -> Constraint154
FEATURE [App::FeaturePython] Constraint155  label="PlaneAlignment124"  # WARN: FeaturePython — macro-defined, semantics opaque (R4)
  Angle = 0
  AnglePitch = 0
  AngleRoll = 0
  Cascade = false
  Disabled = false
  Group = -> [ElementLink310,ElementLink311]
  LockAngle = false
  Offset = 40
  _ConstraintType = 37
  _Parent = -> Constraints
FEATURE [App::FeaturePython] ElementLink310  label="_Element302"  # link proxy (typed FeaturePython)
  LinkTransform = true
  LinkedObject = -> _Element302
  _Parent = -> Constraint155
FEATURE [Part::FeaturePython] Element133  # link proxy (typed FeaturePython)
  Detach = false
  LinkTransform = true
  LinkedObject = -> Link018 [Face14]
  _Parent = -> Elements028
FEATURE [Part::FeaturePython] _Element302  # link proxy (typed FeaturePython)
  Detach = false
  LinkTransform = true
  LinkedObject = -> Assembly028 [1.$Element133.]
  _Parent = -> Elements
FEATURE [App::FeaturePython] ElementLink311  label="_Element029"  # link proxy (typed FeaturePython)
  LinkTransform = true
  LinkedObject = -> _Element029
  _Parent = -> Constraint155
FEATURE [App::FeaturePython] Constraint156  label="PlaneAlignment125"  # WARN: FeaturePython — macro-defined, semantics opaque (R4)
  Angle = 0
  AnglePitch = 0
  AngleRoll = 0
  Cascade = false
  Disabled = false
  Group = -> [ElementLink312,ElementLink313]
  LockAngle = false
  _ConstraintType = 37
  _Parent = -> Constraints
FEATURE [App::FeaturePython] ElementLink312  label="_Element303"  # link proxy (typed FeaturePython)
  LinkTransform = true
  LinkedObject = -> _Element303
  _Parent = -> Constraint156
FEATURE [Part::FeaturePython] Element134  # link proxy (typed FeaturePython)
  Detach = false
  LinkTransform = true
  LinkedObject = -> Body026002 [Pad102.Face2]
  _Parent = -> Elements032
FEATURE [Part::FeaturePython] _Element303  # link proxy (typed FeaturePython)
  Detach = false
  LinkTransform = true
  LinkedObject = -> Assembly032 [1.$Element134.]
  _Parent = -> Elements
FEATURE [App::FeaturePython] ElementLink313  label="_Element304"  # link proxy (typed FeaturePython)
  LinkTransform = true
  LinkedObject = -> _Element304
  _Parent = -> Constraint156
FEATURE [Part::FeaturePython] _Element304  # link proxy (typed FeaturePython)
  Detach = false
  LinkTransform = true
  LinkedObject = -> Link007 [Face79]
  _Parent = -> Elements
FEATURE [Part::FeaturePython] Element135  # link proxy (typed FeaturePython)
  Detach = false
  LinkTransform = true
  LinkedObject = -> Body026002 [Pad102.Face11]
  _Parent = -> Elements032
FEATURE [Part::FeaturePython] _Element305  # link proxy (typed FeaturePython)
  Detach = false
  LinkTransform = true
  LinkedObject = -> Assembly032 [1.$Element135.]
  _Parent = -> Elements
FEATURE [Part::FeaturePython] Element136  # link proxy (typed FeaturePython)
  Detach = false
  LinkTransform = true
  LinkedObject = -> Link018 [Face565]
  _Parent = -> Elements028
FEATURE [Part::FeaturePython] _Element306  # link proxy (typed FeaturePython)
  Detach = false
  LinkTransform = true
  LinkedObject = -> Assembly028 [1.$Element136.]
  _Parent = -> Elements
FEATURE [Part::FeaturePython] Element137  # link proxy (typed FeaturePython)
  Detach = false
  LinkTransform = true
  LinkedObject = -> Link018 [Face581]
  _Parent = -> Elements028
FEATURE [Part::FeaturePython] _Element307  # link proxy (typed FeaturePython)
  Detach = false
  LinkTransform = true
  LinkedObject = -> Assembly028 [1.$Element137.]
  _Parent = -> Elements
FEATURE [Part::FeaturePython] Element138  # link proxy (typed FeaturePython)
  Detach = false
  LinkTransform = true
  LinkedObject = -> Body026002 [Pocket090.Face11]
  _Parent = -> Elements032
FEATURE [Part::FeaturePython] _Element308  # link proxy (typed FeaturePython)
  Detach = false
  LinkTransform = true
  LinkedObject = -> Assembly032 [1.$Element138.]
  _Parent = -> Elements
FEATURE [Part::FeaturePython] Element139  # link proxy (typed FeaturePython)
  Detach = false
  LinkTransform = true
  LinkedObject = -> Body013 [Fillet013.Face101]
  _Parent = -> Elements010
FEATURE [Part::FeaturePython] _Element309  # link proxy (typed FeaturePython)
  Detach = false
  LinkTransform = true
  LinkedObject = -> Assembly010 [1.$Element139.]
  _Parent = -> Elements
FEATURE [Part::FeaturePython] Element140  # link proxy (typed FeaturePython)
  Detach = false
  LinkTransform = true
  LinkedObject = -> Body013 [Fillet013.Face28]
  _Parent = -> Elements010
FEATURE [Part::FeaturePython] _Element310  # link proxy (typed FeaturePython)
  Detach = false
  LinkTransform = true
  LinkedObject = -> Assembly010 [1.$Element140.]
  _Parent = -> Elements
FEATURE [Part::FeaturePython] Assembly035  label="assy-divider_mid_bottom_bracket"  # WARN: FeaturePython — macro-defined, semantics opaque (R4)
  AutoRelax = true
  BuildShape = 0
  Freeze = false
  Group = -> [Constraints035,Elements035,Parts035]
  Placement = pos=(207,-548.98,20) rot=(0,0,1;0rad)
  Verbose = false
  _SolverType = 1
  _Version = 1
FEATURE [App::FeaturePython] Elements035  # WARN: FeaturePython — macro-defined, semantics opaque (R4)
  Group = -> [Element146,Element147,Element148]
FEATURE [Part::FeaturePython] Assembly036  label="assy-divider_mid_top_bracket"  # WARN: FeaturePython — macro-defined, semantics opaque (R4)
  AutoRelax = true
  BuildShape = 0
  Freeze = false
  Group = -> [Constraints036,Elements036,Parts036]
  Placement = pos=(194.5,-485.994,254.795) rot=(0.57735,-0.57735,0.57735;2.0944rad)
  Verbose = false
  _SolverType = 1
  _Version = 1
FEATURE [App::FeaturePython] Elements036  # WARN: FeaturePython — macro-defined, semantics opaque (R4)
  Group = -> [Element143,Element144,Element145]
FEATURE [Part::FeaturePython] Element143  # link proxy (typed FeaturePython)
  Detach = false
  LinkTransform = true
  LinkedObject = -> Body026006 [Fillet115.Face24]
  _Parent = -> Elements036
FEATURE [Part::FeaturePython] _Element313  # link proxy (typed FeaturePython)
  Detach = false
  LinkTransform = true
  LinkedObject = -> Assembly036 [1.$Element143.]
  _Parent = -> Elements
FEATURE [Part::FeaturePython] _Element314  # link proxy (typed FeaturePython)
  Detach = false
  LinkTransform = true
  LinkedObject = -> Link014 [Face80]
  _Parent = -> Elements
FEATURE [Part::FeaturePython] Element144  # link proxy (typed FeaturePython)
  Detach = false
  LinkTransform = true
  LinkedObject = -> Body026006 [Fillet115.Face56]
  _Parent = -> Elements036
FEATURE [Part::FeaturePython] _Element315  # link proxy (typed FeaturePython)
  Detach = false
  LinkTransform = true
  LinkedObject = -> Assembly036 [1.$Element144.]
  _Parent = -> Elements
FEATURE [Part::FeaturePython] _Element316  # link proxy (typed FeaturePython)
  Detach = false
  LinkTransform = true
  LinkedObject = -> Link014 [Face107]
  _Parent = -> Elements
FEATURE [Part::FeaturePython] Element145  # link proxy (typed FeaturePython)
  Detach = false
  LinkTransform = true
  LinkedObject = -> Body026006 [Fillet115.Face49]
  _Parent = -> Elements036
FEATURE [Part::FeaturePython] _Element317  # link proxy (typed FeaturePython)
  Detach = false
  LinkTransform = true
  LinkedObject = -> Assembly036 [1.$Element145.]
  _Parent = -> Elements
FEATURE [App::FeaturePython] Constraint157  label="PlaneAlignment126"  # WARN: FeaturePython — macro-defined, semantics opaque (R4)
  Angle = 0
  AnglePitch = 0
  AngleRoll = 0
  Cascade = false
  Disabled = false
  Group = -> [ElementLink314,ElementLink315]
  LockAngle = false
  _ConstraintType = 37
  _Parent = -> Constraints
FEATURE [App::FeaturePython] ElementLink314  label="_Element318"  # link proxy (typed FeaturePython)
  LinkTransform = true
  LinkedObject = -> _Element318
  _Parent = -> Constraint157
FEATURE [Part::FeaturePython] Element146  # link proxy (typed FeaturePython)
  Detach = false
  LinkTransform = true
  LinkedObject = -> Body026005 [Fillet119.Face37]
  _Parent = -> Elements035
FEATURE [Part::FeaturePython] _Element318  # link proxy (typed FeaturePython)
  Detach = false
  LinkTransform = true
  LinkedObject = -> Assembly035 [1.$Element146.]
  _Parent = -> Elements
FEATURE [App::FeaturePython] ElementLink315  label="_Element035"  # link proxy (typed FeaturePython)
  LinkTransform = true
  LinkedObject = -> _Element035
  _Parent = -> Constraint157
FEATURE [App::FeaturePython] Constraint158  label="PlaneAlignment127"  # WARN: FeaturePython — macro-defined, semantics opaque (R4)
  Angle = 0
  AnglePitch = 0
  AngleRoll = 0
  Cascade = false
  Disabled = false
  Group = -> [ElementLink316,ElementLink317]
  LockAngle = false
  _ConstraintType = 37
  _Parent = -> Constraints
FEATURE [App::FeaturePython] ElementLink316  label="_Element003"  # link proxy (typed FeaturePython)
  LinkTransform = true
  LinkedObject = -> _Element003
  _Parent = -> Constraint158
FEATURE [App::FeaturePython] ElementLink317  label="_Element319"  # link proxy (typed FeaturePython)
  LinkTransform = true
  LinkedObject = -> _Element319
  _Parent = -> Constraint158
FEATURE [Part::FeaturePython] Element147  # link proxy (typed FeaturePython)
  Detach = false
  LinkTransform = true
  LinkedObject = -> Body026005 [Fillet119.Face66]
  _Parent = -> Elements035
FEATURE [Part::FeaturePython] _Element319  # link proxy (typed FeaturePython)
  Detach = false
  LinkTransform = true
  LinkedObject = -> Assembly035 [1.$Element147.]
  _Parent = -> Elements
FEATURE [App::FeaturePython] Constraint159  label="PlaneAlignment128"  # WARN: FeaturePython — macro-defined, semantics opaque (R4)
  Angle = 0
  AnglePitch = 0
  AngleRoll = 0
  Cascade = false
  Disabled = false
  Group = -> [ElementLink318,ElementLink319]
  LockAngle = false
  _ConstraintType = 37
  _Parent = -> Constraints
FEATURE [App::FeaturePython] ElementLink318  label="_Element313"  # link proxy (typed FeaturePython)
  LinkTransform = true
  LinkedObject = -> _Element313
  _Parent = -> Constraint159
FEATURE [App::FeaturePython] ElementLink319  label="_Element314"  # link proxy (typed FeaturePython)
  LinkTransform = true
  LinkedObject = -> _Element314
  _Parent = -> Constraint159
FEATURE [App::FeaturePython] Constraint160  label="PlaneAlignment129"  # WARN: FeaturePython — macro-defined, semantics opaque (R4)
  Angle = 0
  AnglePitch = 0
  AngleRoll = 0
  Cascade = false
  Disabled = false
  Group = -> [ElementLink320,ElementLink321]
  LockAngle = false
  _ConstraintType = 37
  _Parent = -> Constraints
FEATURE [App::FeaturePython] ElementLink320  label="_Element315"  # link proxy (typed FeaturePython)
  LinkTransform = true
  LinkedObject = -> _Element315
  _Parent = -> Constraint160
FEATURE [App::FeaturePython] ElementLink321  label="_Element054"  # link proxy (typed FeaturePython)
  LinkTransform = true
  LinkedObject = -> _Element054
  _Parent = -> Constraint160
FEATURE [App::FeaturePython] Constraint161  label="PlaneAlignment130"  # WARN: FeaturePython — macro-defined, semantics opaque (R4)
  Angle = 0
  AnglePitch = 0
  AngleRoll = 0
  Cascade = false
  Disabled = false
  Group = -> [ElementLink322,ElementLink323]
  LockAngle = false
  _ConstraintType = 37
  _Parent = -> Constraints
FEATURE [App::FeaturePython] ElementLink322  label="_Element317"  # link proxy (typed FeaturePython)
  LinkTransform = true
  LinkedObject = -> _Element317
  _Parent = -> Constraint161
FEATURE [App::FeaturePython] ElementLink323  label="_Element320"  # link proxy (typed FeaturePython)
  LinkTransform = true
  LinkedObject = -> _Element320
  _Parent = -> Constraint161
FEATURE [Part::FeaturePython] Element148  # link proxy (typed FeaturePython)
  Detach = false
  LinkTransform = true
  LinkedObject = -> Body026005 [Fillet119.Face51]
  _Parent = -> Elements035
FEATURE [Part::FeaturePython] _Element320  # link proxy (typed FeaturePython)
  Detach = false
  LinkTransform = true
  LinkedObject = -> Assembly035 [1.$Element148.]
  _Parent = -> Elements
FEATURE [Part::FeaturePython] Assembly035002  label="assy-divider_left_bottom"  # WARN: FeaturePython — macro-defined, semantics opaque (R4)
  AutoRelax = true
  BuildShape = 0
  Freeze = false
  Group = -> [Constraints037,Elements037,Parts037]
  Placement = pos=(-190,1.8738e-12,2.41285e-10) rot=(0,0,1;0rad)
  Verbose = false
  _SolverType = 1
  _Version = 1
FEATURE [App::FeaturePython] Elements037  # WARN: FeaturePython — macro-defined, semantics opaque (R4)
  Group = -> [Element149,Element150]
FEATURE [Part::FeaturePython] Assembly035003  label="assy-divider_left_top"  # WARN: FeaturePython — macro-defined, semantics opaque (R4)
  AutoRelax = true
  BuildShape = 0
  Freeze = false
  Group = -> [Constraints038,Elements038,Parts038]
  Placement = pos=(16.9999,-485.994,240.73) rot=(0,0.707107,-0.707107;3.14159rad)
  Verbose = false
  _SolverType = 1
  _Version = 1
FEATURE [App::FeaturePython] Elements038  # WARN: FeaturePython — macro-defined, semantics opaque (R4)
  Group = -> [Element151,Element152]
FEATURE [App::FeaturePython] Constraint162  label="PlaneAlignment131"  # WARN: FeaturePython — macro-defined, semantics opaque (R4)
  Angle = 0
  AnglePitch = 0
  AngleRoll = 0
  Cascade = false
  Disabled = false
  Group = -> [ElementLink324,ElementLink325]
  LockAngle = false
  _ConstraintType = 37
  _Parent = -> Constraints
FEATURE [App::FeaturePython] ElementLink324  label="_Element321"  # link proxy (typed FeaturePython)
  LinkTransform = true
  LinkedObject = -> _Element321
  _Parent = -> Constraint162
FEATURE [Part::FeaturePython] Element149  # link proxy (typed FeaturePython)
  Detach = false
  LinkTransform = true
  LinkedObject = -> Assembly035001 [Face37]
  _Parent = -> Elements037
FEATURE [Part::FeaturePython] _Element321  # link proxy (typed FeaturePython)
  Detach = false
  LinkTransform = true
  LinkedObject = -> Assembly035002 [1.$Element149.]
  _Parent = -> Elements
FEATURE [App::FeaturePython] ElementLink325  label="_Element010"  # link proxy (typed FeaturePython)
  LinkTransform = true
  LinkedObject = -> _Element010
  _Parent = -> Constraint162
FEATURE [App::FeaturePython] Constraint163  label="PlaneAlignment132"  # WARN: FeaturePython — macro-defined, semantics opaque (R4)
  Angle = 0
  AnglePitch = 0
  AngleRoll = 0
  Cascade = false
  Disabled = false
  Group = -> [ElementLink326,ElementLink327]
  LockAngle = false
  _ConstraintType = 37
  _Parent = -> Constraints
FEATURE [App::FeaturePython] ElementLink326  label="_Element322"  # link proxy (typed FeaturePython)
  LinkTransform = true
  LinkedObject = -> _Element322
  _Parent = -> Constraint163
FEATURE [Part::FeaturePython] Element150  # link proxy (typed FeaturePython)
  Detach = false
  LinkTransform = true
  LinkedObject = -> Assembly035001 [Face66]
  _Parent = -> Elements037
FEATURE [Part::FeaturePython] _Element322  # link proxy (typed FeaturePython)
  Detach = false
  LinkTransform = true
  LinkedObject = -> Assembly035002 [1.$Element150.]
  _Parent = -> Elements
FEATURE [App::FeaturePython] ElementLink327  label="_Element005"  # link proxy (typed FeaturePython)
  LinkTransform = true
  LinkedObject = -> _Element005
  _Parent = -> Constraint163
FEATURE [App::FeaturePython] Constraint164  label="PlaneAlignment133"  # WARN: FeaturePython — macro-defined, semantics opaque (R4)
  Angle = 0
  AnglePitch = 0
  AngleRoll = 0
  Cascade = false
  Disabled = false
  Group = -> [ElementLink328,ElementLink329]
  LockAngle = false
  _ConstraintType = 37
  _Parent = -> Constraints
FEATURE [App::FeaturePython] ElementLink328  label="_Element323"  # link proxy (typed FeaturePython)
  LinkTransform = true
  LinkedObject = -> _Element323
  _Parent = -> Constraint164
FEATURE [Part::FeaturePython] Element151  # link proxy (typed FeaturePython)
  Detach = false
  LinkTransform = true
  LinkedObject = -> Body026005001 [Face58]
  _Parent = -> Elements038
FEATURE [Part::FeaturePython] _Element323  # link proxy (typed FeaturePython)
  Detach = false
  LinkTransform = true
  LinkedObject = -> Assembly035003 [1.$Element151.]
  _Parent = -> Elements
FEATURE [App::FeaturePython] ElementLink329  label="_Element324"  # link proxy (typed FeaturePython)
  LinkTransform = true
  LinkedObject = -> _Element324
  _Parent = -> Constraint164
FEATURE [Part::FeaturePython] _Element324  # link proxy (typed FeaturePython)
  Detach = false
  LinkTransform = true
  LinkedObject = -> Link007 [Face49]
  _Parent = -> Elements
FEATURE [App::FeaturePython] Constraint165  label="PlaneAlignment134"  # WARN: FeaturePython — macro-defined, semantics opaque (R4)
  Angle = 0
  AnglePitch = 0
  AngleRoll = 0
  Cascade = false
  Disabled = false
  Group = -> [ElementLink330,ElementLink331]
  LockAngle = false
  _ConstraintType = 37
  _Parent = -> Constraints
FEATURE [App::FeaturePython] ElementLink330  label="_Element024"  # link proxy (typed FeaturePython)
  LinkTransform = true
  LinkedObject = -> _Element024
  _Parent = -> Constraint165
FEATURE [App::FeaturePython] ElementLink331  label="_Element325"  # link proxy (typed FeaturePython)
  LinkTransform = true
  LinkedObject = -> _Element325
  _Parent = -> Constraint165
FEATURE [Part::FeaturePython] Element152  # link proxy (typed FeaturePython)
  Detach = false
  LinkTransform = true
  LinkedObject = -> Body026005001 [Face66]
  _Parent = -> Elements038
FEATURE [Part::FeaturePython] _Element325  # link proxy (typed FeaturePython)
  Detach = false
  LinkTransform = true
  LinkedObject = -> Assembly035003 [1.$Element152.]
  _Parent = -> Elements
FEATURE [Part::FeaturePython] Assembly035004  label="assy-door_crush_support"  # WARN: FeaturePython — macro-defined, semantics opaque (R4)
  AutoRelax = true
  BuildShape = 0
  Freeze = false
  Group = -> [Constraints039,Elements039,Parts039]
  Placement = pos=(36.9999,-443.93,-1.8e-15) rot=(0,0,1;0rad)
  Verbose = false
  _SolverType = 1
  _Version = 1
FEATURE [App::FeaturePython] Elements039  # WARN: FeaturePython — macro-defined, semantics opaque (R4)
  Group = -> [Element153,Element154]
FEATURE [App::FeaturePython] Constraint166  label="PlaneAlignment135"  # WARN: FeaturePython — macro-defined, semantics opaque (R4)
  Angle = 0
  AnglePitch = 0
  AngleRoll = 0
  Cascade = false
  Disabled = false
  Group = -> [ElementLink332,ElementLink333]
  LockAngle = false
  _ConstraintType = 37
  _Parent = -> Constraints
FEATURE [App::FeaturePython] ElementLink332  label="_Element326"  # link proxy (typed FeaturePython)
  LinkTransform = true
  LinkedObject = -> _Element326
  _Parent = -> Constraint166
FEATURE [Part::FeaturePython] Element153  # link proxy (typed FeaturePython)
  Detach = false
  LinkTransform = true
  LinkedObject = -> Body026005002 [Pad123.Face5]
  _Parent = -> Elements039
FEATURE [Part::FeaturePython] _Element326  # link proxy (typed FeaturePython)
  Detach = false
  LinkTransform = true
  LinkedObject = -> Assembly035004 [1.$Element153.]
  _Parent = -> Elements
FEATURE [App::FeaturePython] ElementLink333  label="_Element241"  # link proxy (typed FeaturePython)
  LinkTransform = true
  LinkedObject = -> _Element241
  _Parent = -> Constraint166
FEATURE [App::FeaturePython] Constraint167  label="PlaneAlignment136"  # WARN: FeaturePython — macro-defined, semantics opaque (R4)
  Angle = 0
  AnglePitch = 0
  AngleRoll = 0
  Cascade = false
  Disabled = false
  Group = -> [ElementLink334,ElementLink335]
  LockAngle = false
  _ConstraintType = 37
  _Parent = -> Constraints
FEATURE [App::FeaturePython] ElementLink334  label="_Element327"  # link proxy (typed FeaturePython)
  LinkTransform = true
  LinkedObject = -> _Element327
  _Parent = -> Constraint167
FEATURE [Part::FeaturePython] Element154  # link proxy (typed FeaturePython)
  Detach = false
  LinkTransform = true
  LinkedObject = -> Body026005002 [Pad123.Face1]
  _Parent = -> Elements039
FEATURE [Part::FeaturePython] _Element327  # link proxy (typed FeaturePython)
  Detach = false
  LinkTransform = true
  LinkedObject = -> Assembly035004 [1.$Element154.]
  _Parent = -> Elements
FEATURE [App::FeaturePython] ElementLink335  label="_Element020"  # link proxy (typed FeaturePython)
  LinkTransform = true
  LinkedObject = -> _Element020
  _Parent = -> Constraint167

RESOLVED EXTERNAL PARTS (link-assembly join: the EXTERNAL_REF files above that resolve inside this repo's crawl, each included once):
---- part 40cm_2020_aluminum_extrusion.FCStd = doc fcstd_c2528f4fb2df ----
FCSTD DOCUMENT  (FreeCAD 0.20R29410 (Git))
Label: 40cm_2020_aluminum_extrusion
License: All rights reserved
LicenseURL: http://en.wikipedia.org/wiki/All_rights_reserved
objects: Part::Refine×2, App::MeasureDistance×2, Part::Feature×1, PartDesign::FeatureBase×1, PartDesign::Pad×1, PartDesign::Body×1
note: 7 computed .brp shape members not serialized (recipe doc carries the construction recipe); baked Part::Feature solids carry a one-line shape summary decoded from their .brp

FEATURE [Part::Feature] _020_aluminum_extrusion_face001002_solid  label="_020_aluminum_extrusion_face001002 (Solid)"
  shape: bbox 20 x 7 x 20 mm, 1316 faces (baked)
FEATURE [Part::Refine] _020_aluminum_extrusion_face001002_solid001  label="_020_aluminum_extrusion_face001002 (Solid)001"
  Source = -> _020_aluminum_extrusion_face001002_solid
FEATURE [App::MeasureDistance] Distance  label="Distance: 7.01 mm"
  Distance = 7.00618
  P1 = (-330,0,146.819)
  P2 = (-330,6.99856,146.492)
FEATURE [PartDesign::FeatureBase] BaseFeature
  BaseFeature = -> _020_aluminum_extrusion_face001002_solid001
FEATURE [PartDesign::Pad] Pad
  BaseFeature = -> BaseFeature
  Direction = (0,-1,0)
  Length = 393
  Length2 = 10
  Profile = -> BaseFeature [Face2]
  Type = 0
FEATURE [PartDesign::Body] Body
  BaseFeature = -> _020_aluminum_extrusion_face001002_solid001
  Group = -> [BaseFeature,Pad]
  Origin = -> Origin
  Tip = -> Pad
FEATURE [App::MeasureDistance] Distance001  label="Distance: 399.99 mm"
  Distance = 399.992
  P1 = (-330.024,-393,144.543)
  P2 = (-330.027,6.99189,144.425)
FEATURE [Part::Refine] Pad001  label="40cm_2020_aluminum_extrusion"
  Source = -> Pad
---- part dispenser.FCStd = doc fcstd_8d19a255c4b3 ----
FCSTD DOCUMENT  (FreeCAD 0.20R29410 (Git))
Label: dispenser
License: All rights reserved
LicenseURL: http://en.wikipedia.org/wiki/All_rights_reserved
objects: Part::FeaturePython×8, Sketcher::SketchObject×5, PartDesign::Pad×4, PartDesign::Fillet×4, PartDesign::Body×4, PartDesign::Thickness×3, App::FeaturePython×2, PartDesign::Pocket×1, PartDesign::Boolean×1
note: 41 computed .brp shape members not serialized (recipe doc carries the construction recipe); baked Part::Feature solids carry a one-line shape summary decoded from their .brp

FEATURE [App::FeaturePython] Constraints  # WARN: FeaturePython — macro-defined, semantics opaque (R4)
  _Version = 1
FEATURE [Sketcher::SketchObject] Sketch
  FullyConstrained = true
  MapMode = 5
  Support = -> [XY_Plane]
  sketch-geometry (4):
    g0: LineSegment StartX=0 StartY=0 StartZ=0 EndX=160 EndY=0 EndZ=0
    g1: LineSegment StartX=160 StartY=0 StartZ=0 EndX=160 EndY=160 EndZ=0
    g2: LineSegment StartX=160 StartY=160 StartZ=0 EndX=0 EndY=160 EndZ=0
    g3: LineSegment StartX=0 StartY=160 StartZ=0 EndX=0 EndY=0 EndZ=0
  constraints (11):
    c: Coincident(g0,g1)
    c: Coincident(g1,g2)
    c: Coincident(g2,g3)
    c: Coincident(g3,g0)
    c: Horizontal(g0)
    c: Horizontal(g2)
    c: Vertical(g1)
    c: Vertical(g3)
    c: Coincident(g0,g-1)
    c: DistanceX(g0,g0) = 160
    c: DistanceY(g3,g3) = 160
FEATURE [PartDesign::Pad] Pad
  Direction = (0,0,1)
  Length = 140
  Length2 = 10
  Profile = -> Sketch
  ReferenceAxis = -> Sketch [N_Axis]
  Type = 0
FEATURE [Sketcher::SketchObject] Sketch002
  FullyConstrained = true
  MapMode = 5
  Support = -> [XY_Plane001]
  sketch-geometry (7):
    g0: LineSegment StartX=0 StartY=0 StartZ=0 EndX=160 EndY=0 EndZ=0
    g1: LineSegment StartX=160 StartY=0 StartZ=0 EndX=160 EndY=160 EndZ=0
    g2: LineSegment StartX=160 StartY=160 StartZ=0 EndX=0 EndY=160 EndZ=0
    g3: LineSegment StartX=0 StartY=160 StartZ=0 EndX=0 EndY=0 EndZ=0
    g4: Circle CenterX=80 CenterY=65 CenterZ=0 NormalX=0 NormalY=0 NormalZ=1 AngleXU=0 Radius=42.5
    g5: LineSegment StartX=0 StartY=0 StartZ=0 EndX=80 EndY=65 EndZ=0
    g6: LineSegment StartX=80 StartY=65 StartZ=0 EndX=160 EndY=0 EndZ=0
  constraints (18):
    c: Coincident(g0,g1)
    c: Coincident(g1,g2)
    c: Coincident(g2,g3)
    c: Coincident(g3,g0)
    c: Horizontal(g0)
    c: Horizontal(g2)
    c: Vertical(g1)
    c: Vertical(g3)
    c: Coincident(g0,g-1)
    c: DistanceY(g3,g3) = 160
    c: DistanceX(g0,g0) = 160
    c: Diameter(g4) = 85
    c: DistanceY(g4) = 65
    c: Coincident(g5,g0)
    c: Coincident(g5,g4)
    c: Coincident(g6,g4)
    c: Coincident(g6,g0)
    c: Equal(g6,g5)
FEATURE [PartDesign::Pad] Pad001
  Direction = (0,0,1)
  Length = 55
  Length2 = 10
  Profile = -> Sketch002
  ReferenceAxis = -> Sketch002 [N_Axis]
  Reversed = true
  Type = 0
FEATURE [PartDesign::Fillet] Fillet
  Base = -> Pad [Edge2,Edge5,Edge1,Edge8]
  BaseFeature = -> Pad
  Radius = 10
  SupportTransform = false
  UseAllEdges = false
FEATURE [PartDesign::Thickness] Thickness
  Base = -> Fillet [Face5]
  BaseFeature = -> Fillet
  Intersection = false
  Join = 0
  Mode = 0
  Reversed = true
  SupportTransform = false
  Value = 2
FEATURE [PartDesign::Body] Body  label="MainBody"
  Group = -> [Sketch,Pad,Fillet,Thickness]
  Origin = -> Origin
  Tip = -> Thickness
FEATURE [PartDesign::Fillet] Fillet001
  Base = -> Pad001 [Edge3]
  BaseFeature = -> Pad001
  Radius = 12
  SupportTransform = false
  UseAllEdges = false
FEATURE [PartDesign::Thickness] Thickness001
  Base = -> Fillet001 [Face3]
  BaseFeature = -> Fillet001
  Intersection = false
  Join = 0
  Mode = 0
  Reversed = true
  SupportTransform = false
  Value = 1
FEATURE [Sketcher::SketchObject] Sketch003
  ExternalGeometry = -> [Pad001]
  FullyConstrained = true
  MapMode = 5
  Placement = pos=(0,0,-54) rot=(0,0,1;0rad)
  Support = -> [Thickness001]
  sketch-geometry (1):
    g0: Circle CenterX=80 CenterY=65 CenterZ=0 NormalX=0 NormalY=0 NormalZ=1 AngleXU=0 Radius=28.5
  constraints (2):
    c: Coincident(g0,g-3)
    c: Diameter(g0) = 57
FEATURE [PartDesign::Pocket] Pocket
  BaseFeature = -> Thickness001
  Direction = (0,0,-1)
  Length = 5
  Length2 = 5
  Profile = -> Sketch003
  ReferenceAxis = -> Sketch003 [N_Axis]
  Type = 0
FEATURE [PartDesign::Body] Body001  label="FunnelBody"
  Group = -> [Sketch002,Pad001,Fillet001,Thickness001,Sketch003,Pocket]
  Origin = -> Origin001
  Tip = -> Pocket
FEATURE [Sketcher::SketchObject] Sketch004
  FullyConstrained = true
  MapMode = 5
  Support = -> [XY_Plane002]
  sketch-geometry (4):
    g0: LineSegment StartX=0 StartY=0 StartZ=0 EndX=160 EndY=0 EndZ=0
    g1: LineSegment StartX=160 StartY=0 StartZ=0 EndX=160 EndY=160 EndZ=0
    g2: LineSegment StartX=160 StartY=160 StartZ=0 EndX=0 EndY=160 EndZ=0
    g3: LineSegment StartX=0 StartY=160 StartZ=0 EndX=0 EndY=0 EndZ=0
  constraints (11):
    c: Coincident(g0,g1)
    c: Coincident(g1,g2)
    c: Coincident(g2,g3)
    c: Coincident(g3,g0)
    c: Horizontal(g0)
    c: Horizontal(g2)
    c: Vertical(g1)
    c: Vertical(g3)
    c: Coincident(g0,g-1)
    c: DistanceY(g3,g3) = 160
    c: DistanceX(g0,g0) = 160
FEATURE [PartDesign::Pad] Pad002
  Direction = (0,0,1)
  Length = 25
  Length2 = 10
  Profile = -> Sketch004
  ReferenceAxis = -> Sketch004 [N_Axis]
  Reversed = true
  Type = 0
FEATURE [Sketcher::SketchObject] Sketch006
  FullyConstrained = true
  MapMode = 5
  Placement = pos=(0,0,0) rot=(0.57735,0.57735,0.57735;2.0944rad)
  Support = -> [YZ_Plane003]
  sketch-geometry (4):
    g0: LineSegment StartX=0 StartY=-7 StartZ=0 EndX=23 EndY=-7 EndZ=0
    g1: LineSegment StartX=23 StartY=-7 StartZ=0 EndX=23 EndY=-27 EndZ=0
    g2: LineSegment StartX=23 StartY=-27 StartZ=0 EndX=0 EndY=-27 EndZ=0
    g3: LineSegment StartX=0 StartY=-27 StartZ=0 EndX=0 EndY=-7 EndZ=0
  constraints (12):
    c: Coincident(g0,g1)
    c: Coincident(g1,g2)
    c: Coincident(g2,g3)
    c: Coincident(g3,g0)
    c: Horizontal(g0)
    c: Horizontal(g2)
    c: Vertical(g1)
    c: Vertical(g3)
    c: PointOnObject(g0,g-2)
    c: DistanceY(g3,g3) = 20
    c: DistanceY(g0,g-1) = 7
    c: DistanceX(g2,g2) = 23
FEATURE [PartDesign::Fillet] Fillet002
  Base = -> Pad002 [Edge2,Edge1,Edge5,Edge8]
  BaseFeature = -> Pad002
  Radius = 10
  SupportTransform = false
  UseAllEdges = false
FEATURE [PartDesign::Thickness] Thickness002
  Base = -> Fillet002 [Face5]
  BaseFeature = -> Fillet002
  Intersection = false
  Join = 0
  Mode = 0
  Reversed = true
  SupportTransform = false
  Value = 2
FEATURE [PartDesign::Pad] Pad003
  Direction = (1,-2e-16,3e-16)
  Length = 160
  Length2 = 10
  Placement = pos=(0,0,0) rot=(0.57735,0.57735,0.57735;2.0944rad)
  Profile = -> Sketch006
  ReferenceAxis = -> Sketch006 [N_Axis]
  Type = 0
FEATURE [PartDesign::Fillet] Fillet003
  Base = -> Pad003 [Edge2]
  BaseFeature = -> Pad003
  Placement = pos=(0,0,0) rot=(0.57735,0.57735,0.57735;2.0944rad)
  Radius = 3
  SupportTransform = false
  UseAllEdges = false
FEATURE [PartDesign::Body] Body003  label="CutawayBody"
  Group = -> [Sketch006,Pad003,Fillet003]
  Origin = -> Origin003
  Tip = -> Fillet003
FEATURE [PartDesign::Boolean] Boolean
  BaseFeature = -> Thickness002
  Group = -> [Body003]
  Type = 1
FEATURE [PartDesign::Body] Body002  label="WallBody"
  Group = -> [Sketch004,Pad002,Fillet002,Thickness002,Boolean]
  Origin = -> Origin002
  Tip = -> Boolean
FEATURE [Part::FeaturePython] Parts  # WARN: FeaturePython — macro-defined, semantics opaque (R4)
  Group = -> [Body,Body001,Body002,Body003]
  GroupMode = 0
FEATURE [Part::FeaturePython] Assembly  label="assy-dispenser"  # WARN: FeaturePython — macro-defined, semantics opaque (R4)
  AutoRelax = true
  BuildShape = 0
  Freeze = false
  Group = -> [Constraints,Elements,Parts]
  Verbose = false
  _SolverType = 1
  _Version = 1
FEATURE [App::FeaturePython] Elements  # WARN: FeaturePython — macro-defined, semantics opaque (R4)
  Group = -> [Element,Element001,Element002,Element003,Element004,Element005]
FEATURE [Part::FeaturePython] Element  # link proxy (typed FeaturePython)
  Detach = false
  LinkTransform = true
  LinkedObject = -> Body [Thickness.Face1]
  _Parent = -> Elements
FEATURE [Part::FeaturePython] Element001  # link proxy (typed FeaturePython)
  Detach = false
  LinkTransform = true
  LinkedObject = -> Body [Thickness.Face10]
  _Parent = -> Elements
FEATURE [Part::FeaturePython] Element002  # link proxy (typed FeaturePython)
  Detach = false
  LinkTransform = true
  LinkedObject = -> Body [Thickness.Face5]
  _Parent = -> Elements
FEATURE [Part::FeaturePython] Element003  # link proxy (typed FeaturePython)
  Detach = false
  LinkTransform = true
  LinkedObject = -> Body002 [Boolean.Face21]
  _Parent = -> Elements
FEATURE [Part::FeaturePython] Element004  # link proxy (typed FeaturePython)
  Detach = false
  LinkTransform = true
  LinkedObject = -> Body [Thickness.Vertex15]
  _Parent = -> Elements
FEATURE [Part::FeaturePython] Element005  # link proxy (typed FeaturePython)
  Detach = false
  LinkTransform = true
  LinkedObject = -> Body [Thickness.Vertex12]
  _Parent = -> Elements
---- part food_dish.FCStd = doc fcstd_d2047ca335ab ----
FCSTD DOCUMENT  (FreeCAD 0.20R29410 (Git))
Label: food_dish
License: All rights reserved
LicenseURL: http://en.wikipedia.org/wiki/All_rights_reserved
objects: Sketcher::SketchObject×1, PartDesign::Revolution×1, PartDesign::Body×1
note: 4 computed .brp shape members not serialized (recipe doc carries the construction recipe); baked Part::Feature solids carry a one-line shape summary decoded from their .brp

FEATURE [Sketcher::SketchObject] Sketch
  FullyConstrained = true
  MapMode = 5
  Placement = pos=(0,0,0) rot=(1,0,0;1.5708rad)
  Support = -> [XZ_Plane]
  sketch-geometry (8):
    g0: LineSegment StartX=0 StartY=0 StartZ=0 EndX=65 EndY=0 EndZ=0
    g1: LineSegment StartX=0 StartY=0 StartZ=0 EndX=0 EndY=1 EndZ=0
    g2: LineSegment StartX=0 StartY=1 StartZ=0 EndX=64.3618 EndY=1 EndZ=0
    g3: LineSegment StartX=65 StartY=0 StartZ=0 EndX=78 EndY=28 EndZ=0
    g4: LineSegment StartX=78 StartY=28 StartZ=0 EndX=76.8975 EndY=28 EndZ=0
    g5: LineSegment StartX=76.8975 StartY=28 StartZ=0 EndX=64.3618 EndY=1 EndZ=0
    g6: GeomPoint X=77.8045 Y=27.5789 Z=0
    g7: LineSegment StartX=76.8975 StartY=28 StartZ=0 EndX=77.8045 EndY=27.5789 EndZ=0
  constraints (21):
    c: Coincident(g0,g-1)
    c: PointOnObject(g0,g-1)
    c: DistanceX(g0) = 65
    c: Coincident(g1,g0)
    c: PointOnObject(g1,g-2)
    c: Coincident(g2,g1)
    c: Horizontal(g2)
    c: DistanceY(g1) = 1
    c: Coincident(g3,g0)
    c: Coincident(g4,g3)
    c: Coincident(g5,g4)
    c: Coincident(g5,g2)
    c: Parallel(g5,g3)
    c: Horizontal(g4)
    c: DistanceY(g3) = 28
    c: PointOnObject(g6,g3)
    c: Coincident(g7,g4)
    c: Coincident(g7,g6)
    c: Perpendicular(g5,g7)
    c: DistanceX(g3) = 78
    c: Distance(g7) = 1
FEATURE [PartDesign::Revolution] Revolution  label="food_dish"
  Angle = 360
  Axis = (-3e-16,3e-16,1)
  Base = (0,0,0)
  Placement = pos=(0,0,0) rot=(1,0,0;1.5708rad)
  Profile = -> Sketch
  ReferenceAxis = -> Z_Axis
  Reversed = true
FEATURE [PartDesign::Body] Body
  Group = -> [Sketch,Revolution]
  Origin = -> Origin
  Tip = -> Revolution
---- part orthogonal_2020_aluminum_connector.FCStd = doc fcstd_04cf88b14a7b ----
FCSTD DOCUMENT  (FreeCAD 0.20R29410 (Git))
Label: orthogonal_2020_aluminum_connector
License: All rights reserved
LicenseURL: http://en.wikipedia.org/wiki/All_rights_reserved
objects: Sketcher::SketchObject×5, PartDesign::Fillet×4, PartDesign::Pad×3, PartDesign::Pocket×2, PartDesign::Thickness×1, PartDesign::Body×1
note: 26 computed .brp shape members not serialized (recipe doc carries the construction recipe); baked Part::Feature solids carry a one-line shape summary decoded from their .brp

FEATURE [Sketcher::SketchObject] Sketch
  FullyConstrained = true
  MapMode = 5
  Placement = pos=(0,0,0) rot=(0.57735,0.57735,0.57735;2.0944rad)
  Support = -> [YZ_Plane]
  sketch-geometry (3):
    g0: LineSegment StartX=0 StartY=0 StartZ=0 EndX=20 EndY=0 EndZ=0
    g1: LineSegment StartX=0 StartY=20 StartZ=0 EndX=0 EndY=0 EndZ=0
    g2: LineSegment StartX=0 StartY=20 StartZ=0 EndX=20 EndY=0 EndZ=0
  constraints (8):
    c: Coincident(g0,g-1)
    c: PointOnObject(g0,g-1)
    c: PointOnObject(g1,g-2)
    c: Coincident(g1,g0)
    c: Coincident(g2,g1)
    c: Coincident(g2,g0)
    c: Equal(g0,g1)
    c: DistanceX(g0) = 20
FEATURE [PartDesign::Pad] Pad
  Direction = (1,-2e-16,3e-16)
  Length = 20
  Length2 = 10
  Placement = pos=(0,0,0) rot=(0.57735,0.57735,0.57735;2.0944rad)
  Profile = -> Sketch
  ReferenceAxis = -> Sketch [N_Axis]
  Type = 0
FEATURE [PartDesign::Thickness] Thickness
  Base = -> Pad [Face2]
  BaseFeature = -> Pad
  Intersection = false
  Join = 0
  Mode = 0
  Reversed = true
  SupportTransform = false
  Value = 2
FEATURE [Sketcher::SketchObject] Sketch001
  ExternalGeometry = -> [Thickness]
  FullyConstrained = true
  MapMode = 5
  Placement = pos=(0,0,0) rot=(1,0,0;1.5708rad)
  Support = -> [Thickness]
  sketch-geometry (11):
    g0: LineSegment StartX=1 StartY=12.5 StartZ=0 EndX=6 EndY=12.5 EndZ=0
    g1: LineSegment StartX=6 StartY=12.5 StartZ=0 EndX=6 EndY=7.5 EndZ=0
    g2: LineSegment StartX=6 StartY=7.5 StartZ=0 EndX=1 EndY=7.5 EndZ=0
    g3: LineSegment StartX=1 StartY=7.5 StartZ=0 EndX=1 EndY=12.5 EndZ=0
    g4: LineSegment StartX=19 StartY=12.5 StartZ=0 EndX=14 EndY=12.5 EndZ=0
    g5: LineSegment StartX=14 StartY=12.5 StartZ=0 EndX=14 EndY=7.5 EndZ=0
    g6: LineSegment StartX=14 StartY=7.5 StartZ=0 EndX=19 EndY=7.5 EndZ=0
    g7: LineSegment StartX=19 StartY=7.5 StartZ=0 EndX=19 EndY=12.5 EndZ=0
    g8: GeomPoint X=1 Y=10 Z=0
    g9: LineSegment StartX=1 StartY=10 StartZ=0 EndX=1 EndY=12.5 EndZ=0
    g10: LineSegment StartX=1 StartY=7.5 StartZ=0 EndX=1 EndY=10 EndZ=0
  constraints (30):
    c: Coincident(g0,g1)
    c: Coincident(g1,g2)
    c: Coincident(g2,g3)
    c: Coincident(g3,g0)
    c: Horizontal(g0)
    c: Horizontal(g2)
    c: Vertical(g1)
    c: Vertical(g3)
    c: Coincident(g4,g5)
    c: Coincident(g5,g6)
    c: Coincident(g6,g7)
    c: Coincident(g7,g4)
    c: Horizontal(g4)
    c: Horizontal(g6)
    c: Vertical(g5)
    c: Vertical(g7)
    c: Equal(g6,g5)
    c: Equal(g5,g1)
    c: Equal(g1,g2)
    c: DistanceY(g3,g3) = 5
    c: PointOnObject(g8,g3)
    c: Coincident(g9,g8)
    c: Coincident(g9,g0)
    c: Coincident(g10,g2)
    c: Equal(g9,g10)
    c: Coincident(g9,g10)
    c: DistanceY(g-1,g9) = 10
    c: Horizontal(g1,g5)
    c: DistanceX(g2) = 1
    c: DistanceX(g6,g-4) = 1
FEATURE [PartDesign::Pad] Pad001
  BaseFeature = -> Thickness
  Direction = (-4e-16,-1,2e-16)
  Length = 1.5
  Length2 = 10
  Profile = -> Sketch001
  ReferenceAxis = -> Sketch001 [N_Axis]
  Type = 0
FEATURE [Sketcher::SketchObject] Sketch002
  FullyConstrained = true
  MapMode = 5
  Placement = pos=(0,0,0) rot=(1,0,0;1.5708rad)
  Support = -> [Pad001]
  sketch-geometry (7):
    g0: ArcOfCircle CenterX=9.5 CenterY=10 CenterZ=0 NormalX=0 NormalY=0 NormalZ=1 AngleXU=0 Radius=3.1 StartAngle=1.5708 EndAngle=4.71239
    g1: ArcOfCircle CenterX=10.5 CenterY=10 CenterZ=0 NormalX=0 NormalY=0 NormalZ=1 AngleXU=0 Radius=3.1 StartAngle=4.71239 EndAngle=7.85398
    g2: LineSegment StartX=9.5 StartY=6.9 StartZ=0 EndX=10.5 EndY=6.9 EndZ=0
    g3: LineSegment StartX=10.5 StartY=13.1 StartZ=0 EndX=9.5 EndY=13.1 EndZ=0
    g4: GeomPoint X=10 Y=6.9 Z=0
    g5: LineSegment StartX=9.5 StartY=6.9 StartZ=0 EndX=10 EndY=6.9 EndZ=0
    g6: LineSegment StartX=10 StartY=6.9 StartZ=0 EndX=10.5 EndY=6.9 EndZ=0
  constraints (16):
    c: Tangent(g0,g2) = -1.5708
    c: Tangent(g2,g1) = -1.5708
    c: Tangent(g1,g3) = -1.5708
    c: Tangent(g3,g0) = -1.5708
    c: Equal(g0,g1)
    c: Horizontal(g2)
    c: Diameter(g1) = 6.2
    c: DistanceY(g0) = 10
    c: DistanceX(g2,g2) = 1
    c: PointOnObject(g4,g2)
    c: Coincident(g5,g0)
    c: Coincident(g5,g4)
    c: Coincident(g6,g5)
    c: Coincident(g6,g1)
    c: Equal(g5,g6)
    c: DistanceX(g-1,g4) = 10
FEATURE [PartDesign::Pocket] Pocket
  BaseFeature = -> Pad001
  Direction = (4e-16,1,-2e-16)
  Length = 5
  Length2 = 5
  Profile = -> Sketch002
  ReferenceAxis = -> Sketch002 [N_Axis]
  Type = 0
FEATURE [Sketcher::SketchObject] Sketch003
  ExternalGeometry = -> [Pocket]
  FullyConstrained = true
  MapMode = 5
  Placement = pos=(0,0,0) rot=(1,0,0;3.14159rad)
  Support = -> [Pocket]
  sketch-geometry (11):
    g0: LineSegment StartX=7.5 StartY=-1 StartZ=0 EndX=12.5 EndY=-1 EndZ=0
    g1: LineSegment StartX=12.5 StartY=-1 StartZ=0 EndX=12.5 EndY=-6 EndZ=0
    g2: LineSegment StartX=12.5 StartY=-6 StartZ=0 EndX=7.5 EndY=-6 EndZ=0
    g3: LineSegment StartX=7.5 StartY=-6 StartZ=0 EndX=7.5 EndY=-1 EndZ=0
    g4: LineSegment StartX=7.5 StartY=-14 StartZ=0 EndX=12.5 EndY=-14 EndZ=0
    g5: LineSegment StartX=12.5 StartY=-14 StartZ=0 EndX=12.5 EndY=-19 EndZ=0
    g6: LineSegment StartX=12.5 StartY=-19 StartZ=0 EndX=7.5 EndY=-19 EndZ=0
    g7: LineSegment StartX=7.5 StartY=-19 StartZ=0 EndX=7.5 EndY=-14 EndZ=0
    g8: GeomPoint X=10 Y=-1 Z=0
    g9: LineSegment StartX=7.5 StartY=-1 StartZ=0 EndX=10 EndY=-1 EndZ=0
    g10: LineSegment StartX=10 StartY=-1 StartZ=0 EndX=12.5 EndY=-1 EndZ=0
  constraints (30):
    c: Coincident(g0,g1)
    c: Coincident(g1,g2)
    c: Coincident(g2,g3)
    c: Coincident(g3,g0)
    c: Horizontal(g0)
    c: Horizontal(g2)
    c: Vertical(g1)
    c: Vertical(g3)
    c: Coincident(g4,g5)
    c: Coincident(g5,g6)
    c: Coincident(g6,g7)
    c: Coincident(g7,g4)
    c: Horizontal(g4)
    c: Horizontal(g6)
    c: Vertical(g5)
    c: Vertical(g7)
    c: Equal(g0,g3)
    c: Equal(g3,g4)
    c: Equal(g4,g7)
    c: Vertical(g2,g4)
    c: DistanceY(g0) = -1
    c: DistanceY(g-4,g6) = 1
    c: PointOnObject(g8,g0)
    c: Coincident(g9,g0)
    c: Coincident(g9,g8)
    c: Coincident(g10,g9)
    c: Coincident(g10,g0)
    c: Equal(g9,g10)
    c: DistanceX(g8) = 10
    c: DistanceY(g3,g3) = 5
FEATURE [PartDesign::Pad] Pad002
  BaseFeature = -> Pocket
  Direction = (4e-16,-6e-16,-1)
  Length = 1.5
  Length2 = 10
  Profile = -> Sketch003
  ReferenceAxis = -> Sketch003 [N_Axis]
  Type = 0
FEATURE [Sketcher::SketchObject] Sketch004
  FullyConstrained = true
  MapMode = 5
  Placement = pos=(0,0,0) rot=(1,0,0;3.14159rad)
  Support = -> [Pad002]
  sketch-geometry (7):
    g0: ArcOfCircle CenterX=10 CenterY=-9.5 CenterZ=0 NormalX=0 NormalY=0 NormalZ=1 AngleXU=0 Radius=3.1 StartAngle=0 EndAngle=3.14159
    g1: ArcOfCircle CenterX=10 CenterY=-10.5 CenterZ=0 NormalX=0 NormalY=0 NormalZ=1 AngleXU=0 Radius=3.1 StartAngle=3.14159 EndAngle=6.28319
    g2: LineSegment StartX=6.9 StartY=-9.5 StartZ=0 EndX=6.9 EndY=-10.5 EndZ=0
    g3: LineSegment StartX=13.1 StartY=-10.5 StartZ=0 EndX=13.1 EndY=-9.5 EndZ=0
    g4: GeomPoint X=6.9 Y=-10 Z=0
    g5: LineSegment StartX=6.9 StartY=-9.5 StartZ=0 EndX=6.9 EndY=-10 EndZ=0
    g6: LineSegment StartX=6.9 StartY=-10 StartZ=0 EndX=6.9 EndY=-10.5 EndZ=0
  constraints (16):
    c: Tangent(g0,g2) = -1.5708
    c: Tangent(g2,g1) = -1.5708
    c: Tangent(g1,g3) = -1.5708
    c: Tangent(g3,g0) = -1.5708
    c: Equal(g0,g1)
    c: Vertical(g2)
    c: DistanceY(g3,g3) = 1
    c: Diameter(g0) = 6.2
    c: DistanceX(g1) = 10
    c: PointOnObject(g4,g2)
    c: Coincident(g5,g0)
    c: Coincident(g5,g4)
    c: Coincident(g6,g5)
    c: Coincident(g6,g1)
    c: Equal(g5,g6)
    c: DistanceY(g4) = -10
FEATURE [PartDesign::Pocket] Pocket001  label="Pocket002"
  BaseFeature = -> Pad002
  Direction = (-4e-16,6e-16,1)
  Length = 5
  Length2 = 5
  Profile = -> Sketch004
  ReferenceAxis = -> Sketch004 [N_Axis]
  Type = 0
FEATURE [PartDesign::Fillet] Fillet
  Base = -> Pocket001 [Edge32,Edge18,Edge2,Edge4,Edge1,Edge3,Edge19,Edge17,Edge33,Edge37,Edge34,Edge35,Edge36,Edge89,Edge86,Edge87,Edge88,Edge90]
  BaseFeature = -> Pocket001
  Radius = 0.4
  SupportTransform = false
  UseAllEdges = false
FEATURE [PartDesign::Fillet] Fillet001
  Base = -> Fillet [Edge52,Edge49,Edge47,Edge51,Edge36,Edge33,Edge35,Edge31,Edge104,Edge102,Edge106,Edge107,Edge122,Edge123,Edge120,Edge118]
  BaseFeature = -> Fillet
  Radius = 0.5
  SupportTransform = false
  UseAllEdges = false
FEATURE [PartDesign::Fillet] Fillet002
  Base = -> Fillet001 [Edge131,Edge125,Edge127,Edge129,Edge52,Edge50,Edge48,Edge46,Edge77,Edge75,Edge76,Edge74,Edge18,Edge19,Edge20,Edge17]
  BaseFeature = -> Fillet001
  Radius = 0.2
  SupportTransform = false
  UseAllEdges = false
FEATURE [PartDesign::Fillet] Fillet003  label="orthogonal_2020_aluminum_connector"
  Base = -> Fillet002 [Edge37,Edge99,Edge39,Edge101,Edge105,Edge43,Edge102,Edge40,Edge107,Edge45,Edge110,Edge48,Edge113,Edge51,Edge47,Edge109,Edge144,Edge190,Edge147,Edge193,Edge196,Edge150,Edge192,Edge146,Edge184,Edge138,Edge182,Edge136,Edge185,Edge139,Edge188,Edge142]
  BaseFeature = -> Fillet002
  Radius = 0.4
  SupportTransform = false
  UseAllEdges = false
FEATURE [PartDesign::Body] Body
  Group = -> [Sketch,Pad,Thickness,Sketch001,Pad001,Sketch002,Pocket,Sketch003,Pad002,Sketch004,Pocket001,Fillet,Fillet001,Fillet002,Fillet003]
  Origin = -> Origin
  Tip = -> Fillet003
